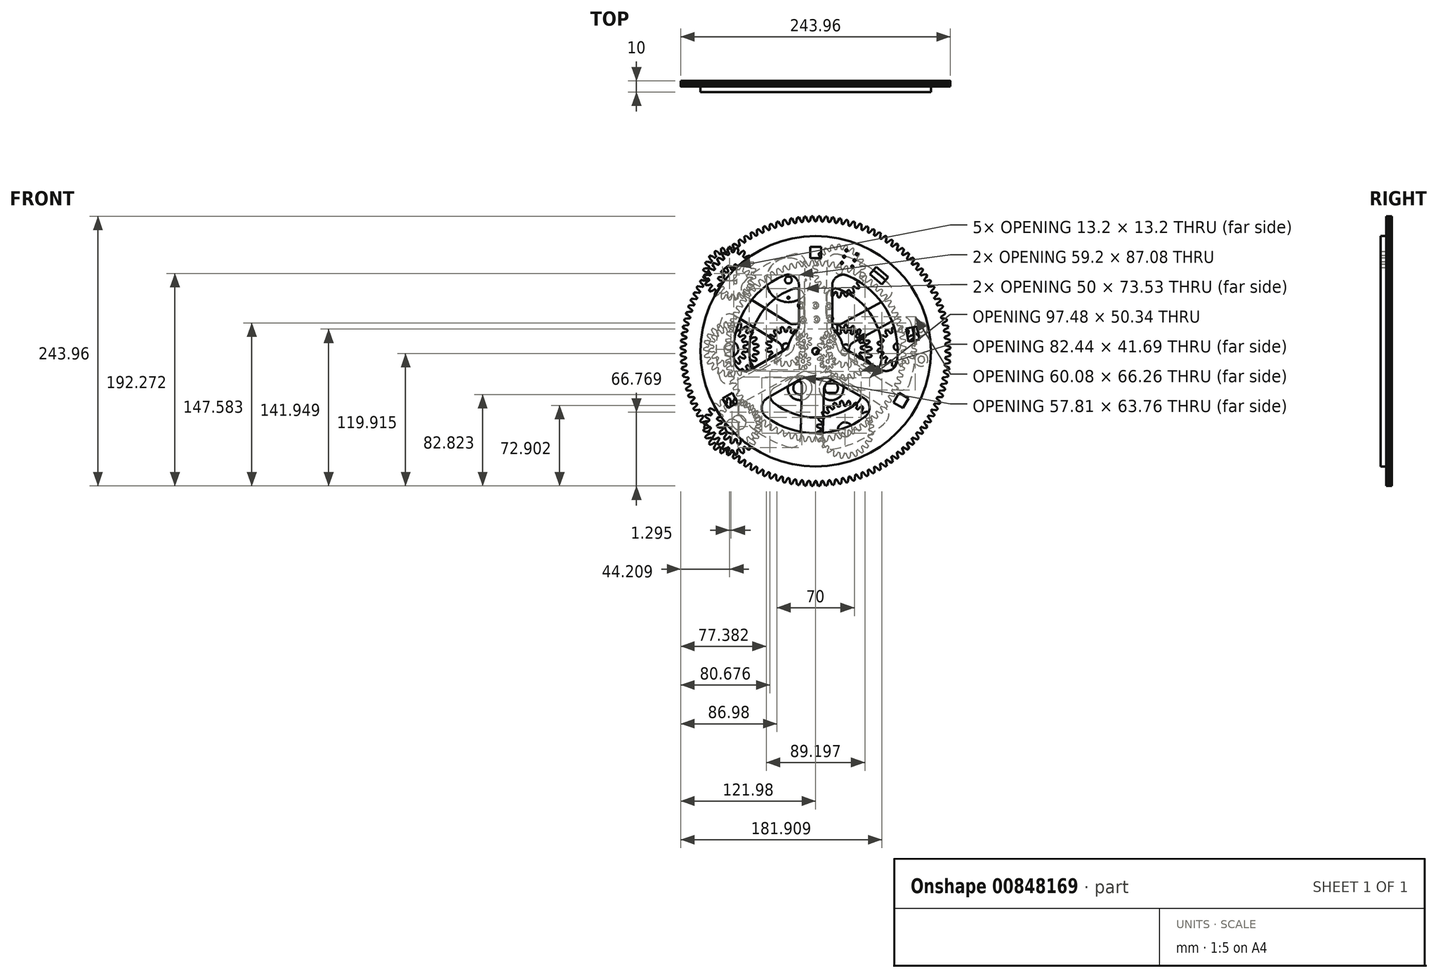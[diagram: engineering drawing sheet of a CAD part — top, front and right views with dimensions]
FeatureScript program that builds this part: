
annotation { "Feature Type Name" : "Feature", "Feature Type Description" : "" }
export const myFeature = defineFeature(function(context is Context, id is Id, definition is map)
    precondition{}
    {
        {
            var Q0;
            Q0=qCreatedBy(makeId("Front.planeOp"),FACE);
            var sketch = newSketch(context, id + "F0", { "sketchPlane" : qUnion([Q0])});
            skArc(sketch, "E0", {"start": v(10.6, 41.57) * mm, "mid": v(10.38, 40.77) * mm, "end": v(10.6, 39.97) * mm});
            skArc(sketch, "E1", {"start": v(13.36, 41.57) * mm, "mid": v(12.78, 42.16) * mm, "end": v(11.98, 42.37) * mm});
            skArc(sketch, "E2", {"start": v(13.2, 40.07) * mm, "mid": v(13.38, 40.77) * mm, "end": v(13.2, 41.47) * mm});
            skArc(sketch, "E3", {"start": v(10.77, 40.07) * mm, "mid": v(11.28, 39.56) * mm, "end": v(11.98, 39.37) * mm});
            skLineSegment(sketch, "E4", {"start": v(13.2, 41.47) * mm, "end": v(13.36, 41.57) * mm});
            skLineSegment(sketch, "E5", {"start": v(13.2, 40.07) * mm, "end": v(13.36, 39.97) * mm});
            skLineSegment(sketch, "E6", {"start": v(11.98, 39.37) * mm, "end": v(11.98, 39.17) * mm});
            skLineSegment(sketch, "E7", {"start": v(10.77, 40.07) * mm, "end": v(10.6, 39.97) * mm});
            skLineSegment(sketch, "E8", {"start": v(10.77, 41.47) * mm, "end": v(10.6, 41.57) * mm});
            skLineSegment(sketch, "E9", {"start": v(11.98, 42.17) * mm, "end": v(11.98, 42.37) * mm});
            skArc(sketch, "E10", {"start": v(11.98, 42.17) * mm, "mid": v(11.28, 41.98) * mm, "end": v(10.77, 41.47) * mm});
            skArc(sketch, "E11", {"start": v(11.98, 39.17) * mm, "mid": v(12.78, 39.38) * mm, "end": v(13.36, 39.97) * mm});
            skArc(sketch, "E12", {"start": v(-1.57, 42.17) * mm, "mid": v(-1.78, 41.37) * mm, "end": v(-1.57, 40.57) * mm});
            skArc(sketch, "E13", {"start": v(1.2, 42.17) * mm, "mid": v(0.62, 42.76) * mm, "end": v(-0.18, 42.97) * mm});
            skArc(sketch, "E14", {"start": v(1.03, 40.67) * mm, "mid": v(1.22, 41.37) * mm, "end": v(1.03, 42.07) * mm});
            skArc(sketch, "E15", {"start": v(-1.4, 40.67) * mm, "mid": v(-0.88, 40.16) * mm, "end": v(-0.18, 39.97) * mm});
            skLineSegment(sketch, "E16", {"start": v(1.03, 42.07) * mm, "end": v(1.2, 42.17) * mm});
            skLineSegment(sketch, "E17", {"start": v(1.03, 40.67) * mm, "end": v(1.2, 40.57) * mm});
            skLineSegment(sketch, "E18", {"start": v(-0.18, 39.97) * mm, "end": v(-0.18, 39.77) * mm});
            skLineSegment(sketch, "E19", {"start": v(-1.4, 40.67) * mm, "end": v(-1.57, 40.57) * mm});
            skLineSegment(sketch, "E20", {"start": v(-1.4, 42.07) * mm, "end": v(-1.57, 42.17) * mm});
            skLineSegment(sketch, "E21", {"start": v(-0.18, 42.77) * mm, "end": v(-0.18, 42.97) * mm});
            skArc(sketch, "E22", {"start": v(-0.18, 42.77) * mm, "mid": v(-0.88, 42.59) * mm, "end": v(-1.4, 42.07) * mm});
            skArc(sketch, "E23", {"start": v(-0.18, 39.77) * mm, "mid": v(0.62, 39.99) * mm, "end": v(1.2, 40.57) * mm});
            skCircle(sketch, "E24", {"center": v(-0.18, 41.37) * mm, "radius": 3 * mm});
            skArc(sketch, "E25", {"start": v(-14.37, 42.2) * mm, "mid": v(-14.59, 41.4) * mm, "end": v(-14.37, 40.6) * mm});
            skArc(sketch, "E26", {"start": v(-11.6, 42.2) * mm, "mid": v(-12.19, 42.79) * mm, "end": v(-12.99, 43) * mm});
            skArc(sketch, "E27", {"start": v(-11.77, 40.7) * mm, "mid": v(-11.59, 41.4) * mm, "end": v(-11.77, 42.1) * mm});
            skArc(sketch, "E28", {"start": v(-14.2, 40.7) * mm, "mid": v(-13.69, 40.19) * mm, "end": v(-12.99, 40) * mm});
            skLineSegment(sketch, "E29", {"start": v(-11.77, 42.1) * mm, "end": v(-11.6, 42.2) * mm});
            skLineSegment(sketch, "E30", {"start": v(-11.77, 40.7) * mm, "end": v(-11.6, 40.6) * mm});
            skLineSegment(sketch, "E31", {"start": v(-12.99, 40) * mm, "end": v(-12.99, 39.8) * mm});
            skLineSegment(sketch, "E32", {"start": v(-14.2, 40.7) * mm, "end": v(-14.37, 40.6) * mm});
            skLineSegment(sketch, "E33", {"start": v(-14.2, 42.1) * mm, "end": v(-14.37, 42.2) * mm});
            skLineSegment(sketch, "E34", {"start": v(-12.99, 42.8) * mm, "end": v(-12.99, 43) * mm});
            skArc(sketch, "E35", {"start": v(-12.99, 42.8) * mm, "mid": v(-13.69, 42.61) * mm, "end": v(-14.2, 42.1) * mm});
            skArc(sketch, "E36", {"start": v(-12.99, 39.8) * mm, "mid": v(-12.19, 40.02) * mm, "end": v(-11.6, 40.6) * mm});
            skArc(sketch, "E37", {"start": v(11.32, 30.3) * mm, "mid": v(11.1, 29.5) * mm, "end": v(11.32, 28.7) * mm});
            skArc(sketch, "E38", {"start": v(14.1, 30.3) * mm, "mid": v(13.5, 30.88) * mm, "end": v(12.7, 31.1) * mm});
            skArc(sketch, "E39", {"start": v(13.92, 28.8) * mm, "mid": v(14.1, 29.5) * mm, "end": v(13.92, 30.2) * mm});
            skArc(sketch, "E40", {"start": v(11.5, 28.8) * mm, "mid": v(12, 28.28) * mm, "end": v(12.7, 28.1) * mm});
            skLineSegment(sketch, "E41", {"start": v(13.92, 30.2) * mm, "end": v(14.1, 30.3) * mm});
            skLineSegment(sketch, "E42", {"start": v(13.92, 28.8) * mm, "end": v(14.1, 28.7) * mm});
            skLineSegment(sketch, "E43", {"start": v(12.7, 28.1) * mm, "end": v(12.7, 27.9) * mm});
            skLineSegment(sketch, "E44", {"start": v(11.5, 28.8) * mm, "end": v(11.32, 28.7) * mm});
            skLineSegment(sketch, "E45", {"start": v(11.5, 30.2) * mm, "end": v(11.32, 30.3) * mm});
            skLineSegment(sketch, "E46", {"start": v(12.7, 30.9) * mm, "end": v(12.7, 31.1) * mm});
            skArc(sketch, "E47", {"start": v(12.7, 30.9) * mm, "mid": v(12, 30.7) * mm, "end": v(11.5, 30.2) * mm});
            skArc(sketch, "E48", {"start": v(12.7, 27.9) * mm, "mid": v(13.5, 28.1) * mm, "end": v(14.1, 28.7) * mm});
            skCircle(sketch, "E49", {"center": v(12.7, 29.5) * mm, "radius": 3 * mm});
            skArc(sketch, "E50", {"start": v(-0.68, 29.53) * mm, "mid": v(-0.9, 28.73) * mm, "end": v(-0.68, 27.93) * mm});
            skArc(sketch, "E51", {"start": v(2.09, 29.53) * mm, "mid": v(1.5, 30.11) * mm, "end": v(0.7, 30.33) * mm});
            skArc(sketch, "E52", {"start": v(1.92, 28.03) * mm, "mid": v(2.1, 28.73) * mm, "end": v(1.92, 29.43) * mm});
            skArc(sketch, "E53", {"start": v(-0.5, 28.03) * mm, "mid": v(0, 27.51) * mm, "end": v(0.7, 27.33) * mm});
            skLineSegment(sketch, "E54", {"start": v(1.92, 29.43) * mm, "end": v(2.09, 29.53) * mm});
            skLineSegment(sketch, "E55", {"start": v(1.92, 28.03) * mm, "end": v(2.09, 27.93) * mm});
            skLineSegment(sketch, "E56", {"start": v(0.7, 27.33) * mm, "end": v(0.7, 27.13) * mm});
            skLineSegment(sketch, "E57", {"start": v(-0.5, 28.03) * mm, "end": v(-0.68, 27.93) * mm});
            skLineSegment(sketch, "E58", {"start": v(-0.5, 29.43) * mm, "end": v(-0.68, 29.53) * mm});
            skLineSegment(sketch, "E59", {"start": v(0.7, 30.13) * mm, "end": v(0.7, 30.33) * mm});
            skArc(sketch, "E60", {"start": v(0.7, 30.13) * mm, "mid": v(0, 29.94) * mm, "end": v(-0.5, 29.43) * mm});
            skArc(sketch, "E61", {"start": v(0.7, 27.13) * mm, "mid": v(1.5, 27.34) * mm, "end": v(2.09, 27.93) * mm});
            skArc(sketch, "E62", {"start": v(-12.86, 29.01) * mm, "mid": v(-13.07, 28.21) * mm, "end": v(-12.86, 27.41) * mm});
            skArc(sketch, "E63", {"start": v(-10.08, 29.01) * mm, "mid": v(-10.67, 29.6) * mm, "end": v(-11.47, 29.81) * mm});
            skArc(sketch, "E64", {"start": v(-10.26, 27.51) * mm, "mid": v(-10.07, 28.21) * mm, "end": v(-10.26, 28.91) * mm});
            skArc(sketch, "E65", {"start": v(-12.68, 27.51) * mm, "mid": v(-12.17, 27) * mm, "end": v(-11.47, 26.81) * mm});
            skLineSegment(sketch, "E66", {"start": v(-10.26, 28.91) * mm, "end": v(-10.08, 29.01) * mm});
            skLineSegment(sketch, "E67", {"start": v(-10.26, 27.51) * mm, "end": v(-10.08, 27.41) * mm});
            skLineSegment(sketch, "E68", {"start": v(-11.47, 26.81) * mm, "end": v(-11.47, 26.61) * mm});
            skLineSegment(sketch, "E69", {"start": v(-12.68, 27.51) * mm, "end": v(-12.86, 27.41) * mm});
            skLineSegment(sketch, "E70", {"start": v(-12.68, 28.91) * mm, "end": v(-12.86, 29.01) * mm});
            skLineSegment(sketch, "E71", {"start": v(-11.47, 29.61) * mm, "end": v(-11.47, 29.81) * mm});
            skArc(sketch, "E72", {"start": v(-11.47, 29.61) * mm, "mid": v(-12.17, 29.42) * mm, "end": v(-12.68, 28.91) * mm});
            skArc(sketch, "E73", {"start": v(-11.47, 26.61) * mm, "mid": v(-10.67, 26.83) * mm, "end": v(-10.08, 27.41) * mm});
            skArc(sketch, "E74", {"start": v(10.1, -29.05) * mm, "mid": v(8.23, -33.4) * mm, "end": v(10.1, -37.75) * mm});
            skLineSegment(sketch, "E75", {"start": v(18.36, -29.05) * mm, "end": v(10.1, -29.05) * mm});
            skLineSegment(sketch, "E76", {"start": v(18.36, -37.75) * mm, "end": v(10.1, -37.75) * mm});
            skCircle(sketch, "E77", {"center": v(14.23, -33.4) * mm, "radius": 11 * mm});
            skArc(sketch, "E78", {"start": v(18.36, -37.75) * mm, "mid": v(20.23, -33.4) * mm, "end": v(18.36, -29.05) * mm});
            skCircle(sketch, "E79", {"center": v(-14.23, -33.23) * mm, "radius": 6 * mm});
            skArc(sketch, "E80", {"start": v(9.57, -8.42) * mm, "mid": v(9.35, -9.22) * mm, "end": v(9.57, -10.02) * mm});
            skArc(sketch, "E81", {"start": v(12.34, -8.42) * mm, "mid": v(11.75, -7.84) * mm, "end": v(10.95, -7.62) * mm});
            skArc(sketch, "E82", {"start": v(12.17, -9.92) * mm, "mid": v(12.35, -9.22) * mm, "end": v(12.17, -8.52) * mm});
            skArc(sketch, "E83", {"start": v(9.74, -9.92) * mm, "mid": v(10.25, -10.43) * mm, "end": v(10.95, -10.62) * mm});
            skLineSegment(sketch, "E84", {"start": v(12.17, -8.52) * mm, "end": v(12.34, -8.42) * mm});
            skLineSegment(sketch, "E85", {"start": v(12.17, -9.92) * mm, "end": v(12.34, -10.02) * mm});
            skLineSegment(sketch, "E86", {"start": v(10.95, -10.62) * mm, "end": v(10.95, -10.82) * mm});
            skLineSegment(sketch, "E87", {"start": v(9.74, -9.92) * mm, "end": v(9.57, -10.02) * mm});
            skLineSegment(sketch, "E88", {"start": v(9.74, -8.52) * mm, "end": v(9.57, -8.42) * mm});
            skLineSegment(sketch, "E89", {"start": v(10.95, -7.82) * mm, "end": v(10.95, -7.62) * mm});
            skArc(sketch, "E90", {"start": v(10.95, -7.82) * mm, "mid": v(10.25, -8) * mm, "end": v(9.74, -8.52) * mm});
            skArc(sketch, "E91", {"start": v(10.95, -10.82) * mm, "mid": v(11.75, -10.6) * mm, "end": v(12.34, -10.02) * mm});
            skArc(sketch, "E92", {"start": v(-12.82, -8.3) * mm, "mid": v(-13.03, -9.1) * mm, "end": v(-12.82, -9.9) * mm});
            skArc(sketch, "E93", {"start": v(-10.05, -8.3) * mm, "mid": v(-10.63, -7.72) * mm, "end": v(-11.43, -7.5) * mm});
            skArc(sketch, "E94", {"start": v(-10.22, -9.8) * mm, "mid": v(-10.03, -9.1) * mm, "end": v(-10.22, -8.4) * mm});
            skArc(sketch, "E95", {"start": v(-12.65, -9.8) * mm, "mid": v(-12.13, -10.32) * mm, "end": v(-11.43, -10.5) * mm});
            skLineSegment(sketch, "E96", {"start": v(-10.22, -8.4) * mm, "end": v(-10.05, -8.3) * mm});
            skLineSegment(sketch, "E97", {"start": v(-10.22, -9.8) * mm, "end": v(-10.05, -9.9) * mm});
            skLineSegment(sketch, "E98", {"start": v(-11.43, -10.5) * mm, "end": v(-11.43, -10.7) * mm});
            skLineSegment(sketch, "E99", {"start": v(-12.65, -9.8) * mm, "end": v(-12.82, -9.9) * mm});
            skLineSegment(sketch, "E100", {"start": v(-12.65, -8.4) * mm, "end": v(-12.82, -8.3) * mm});
            skLineSegment(sketch, "E101", {"start": v(-11.43, -7.7) * mm, "end": v(-11.43, -7.5) * mm});
            skArc(sketch, "E102", {"start": v(-11.43, -7.7) * mm, "mid": v(-12.13, -7.9) * mm, "end": v(-12.65, -8.4) * mm});
            skArc(sketch, "E103", {"start": v(-11.43, -10.7) * mm, "mid": v(-10.63, -10.49) * mm, "end": v(-10.05, -9.9) * mm});
            skArc(sketch, "E104", {"start": v(12.53, -5) * mm, "mid": v(12.34, -4.94) * mm, "end": v(12.16, -4.89) * mm});
            skArc(sketch, "E105", {"start": v(12.53, -5) * mm, "mid": v(12.88, -5) * mm, "end": v(13.14, -4.76) * mm});
            skLineSegment(sketch, "E106", {"start": v(14.48, -3.36) * mm, "end": v(14.9, -3.2) * mm});
            skLineSegment(sketch, "E107", {"start": v(14.1, -3.55) * mm, "end": v(14.48, -3.36) * mm});
            skLineSegment(sketch, "E108", {"start": v(13.85, -3.73) * mm, "end": v(14.1, -3.55) * mm});
            skLineSegment(sketch, "E109", {"start": v(13.63, -3.92) * mm, "end": v(13.85, -3.73) * mm});
            skLineSegment(sketch, "E110", {"start": v(13.49, -4.09) * mm, "end": v(13.63, -3.92) * mm});
            skLineSegment(sketch, "E111", {"start": v(13.45, -4.14) * mm, "end": v(13.49, -4.09) * mm});
            skLineSegment(sketch, "E112", {"start": v(13.42, -4.2) * mm, "end": v(13.45, -4.14) * mm});
            skLineSegment(sketch, "E113", {"start": v(13.37, -4.3) * mm, "end": v(13.42, -4.2) * mm});
            skLineSegment(sketch, "E114", {"start": v(13.27, -4.5) * mm, "end": v(13.37, -4.3) * mm});
            skLineSegment(sketch, "E115", {"start": v(13.14, -4.76) * mm, "end": v(13.27, -4.5) * mm});
            skArc(sketch, "E116", {"start": v(15.47, -3.61) * mm, "mid": v(15.19, -3.4) * mm, "end": v(14.9, -3.2) * mm});
            skLineSegment(sketch, "E117", {"start": v(15.44, -4.06) * mm, "end": v(15.47, -3.61) * mm});
            skLineSegment(sketch, "E118", {"start": v(15.37, -4.47) * mm, "end": v(15.44, -4.06) * mm});
            skLineSegment(sketch, "E119", {"start": v(15.28, -4.78) * mm, "end": v(15.37, -4.47) * mm});
            skLineSegment(sketch, "E120", {"start": v(15.17, -5.03) * mm, "end": v(15.28, -4.78) * mm});
            skLineSegment(sketch, "E121", {"start": v(15.05, -5.23) * mm, "end": v(15.17, -5.03) * mm});
            skLineSegment(sketch, "E122", {"start": v(15.01, -5.28) * mm, "end": v(15.05, -5.23) * mm});
            skLineSegment(sketch, "E123", {"start": v(14.98, -5.32) * mm, "end": v(15.01, -5.28) * mm});
            skLineSegment(sketch, "E124", {"start": v(14.9, -5.4) * mm, "end": v(14.98, -5.32) * mm});
            skLineSegment(sketch, "E125", {"start": v(14.73, -5.56) * mm, "end": v(14.9, -5.4) * mm});
            skLineSegment(sketch, "E126", {"start": v(14.52, -5.76) * mm, "end": v(14.73, -5.56) * mm});
            skArc(sketch, "E127", {"start": v(14.52, -5.76) * mm, "mid": v(14.37, -6.08) * mm, "end": v(14.48, -6.42) * mm});
            skArc(sketch, "E128", {"start": v(14.7, -6.74) * mm, "mid": v(14.6, -6.58) * mm, "end": v(14.48, -6.42) * mm});
            skArc(sketch, "E129", {"start": v(14.7, -6.74) * mm, "mid": v(15, -6.94) * mm, "end": v(15.35, -6.9) * mm});
            skLineSegment(sketch, "E130", {"start": v(17.25, -6.55) * mm, "end": v(17.68, -6.66) * mm});
            skLineSegment(sketch, "E131", {"start": v(16.84, -6.5) * mm, "end": v(17.25, -6.55) * mm});
            skCircle(sketch, "E132", {"center": v(11.98, 40.77) * mm, "radius": 3 * mm});
            skLineSegment(sketch, "E133", {"start": v(16.52, -6.48) * mm, "end": v(16.84, -6.5) * mm});
            skLineSegment(sketch, "E134", {"start": v(16.24, -6.5) * mm, "end": v(16.52, -6.48) * mm});
            skLineSegment(sketch, "E135", {"start": v(16.02, -6.56) * mm, "end": v(16.24, -6.5) * mm});
            skLineSegment(sketch, "E136", {"start": v(15.96, -6.58) * mm, "end": v(16.02, -6.56) * mm});
            skLineSegment(sketch, "E137", {"start": v(15.9, -6.6) * mm, "end": v(15.96, -6.58) * mm});
            skLineSegment(sketch, "E138", {"start": v(15.8, -6.66) * mm, "end": v(15.9, -6.6) * mm});
            skLineSegment(sketch, "E139", {"start": v(15.6, -6.76) * mm, "end": v(15.8, -6.66) * mm});
            skLineSegment(sketch, "E140", {"start": v(15.35, -6.9) * mm, "end": v(15.6, -6.76) * mm});
            skArc(sketch, "E141", {"start": v(17.9, -7.33) * mm, "mid": v(17.8, -7) * mm, "end": v(17.68, -6.66) * mm});
            skLineSegment(sketch, "E142", {"start": v(17.62, -7.68) * mm, "end": v(17.9, -7.33) * mm});
            skLineSegment(sketch, "E143", {"start": v(17.32, -7.97) * mm, "end": v(17.62, -7.68) * mm});
            skLineSegment(sketch, "E144", {"start": v(17.07, -8.17) * mm, "end": v(17.32, -7.97) * mm});
            skLineSegment(sketch, "E145", {"start": v(16.83, -8.31) * mm, "end": v(17.07, -8.17) * mm});
            skLineSegment(sketch, "E146", {"start": v(16.62, -8.4) * mm, "end": v(16.83, -8.31) * mm});
            skLineSegment(sketch, "E147", {"start": v(16.55, -8.42) * mm, "end": v(16.62, -8.4) * mm});
            skLineSegment(sketch, "E148", {"start": v(16.5, -8.43) * mm, "end": v(16.55, -8.42) * mm});
            skLineSegment(sketch, "E149", {"start": v(16.38, -8.45) * mm, "end": v(16.5, -8.43) * mm});
            skLineSegment(sketch, "E150", {"start": v(16.16, -8.48) * mm, "end": v(16.38, -8.45) * mm});
            skLineSegment(sketch, "E151", {"start": v(15.87, -8.52) * mm, "end": v(16.16, -8.48) * mm});
            skArc(sketch, "E152", {"start": v(15.87, -8.52) * mm, "mid": v(15.56, -8.7) * mm, "end": v(15.45, -9.03) * mm});
            skArc(sketch, "E153", {"start": v(15.45, -9.41) * mm, "mid": v(15.45, -9.22) * mm, "end": v(15.45, -9.03) * mm});
            skArc(sketch, "E154", {"start": v(15.45, -9.41) * mm, "mid": v(15.56, -9.75) * mm, "end": v(15.87, -9.92) * mm});
            skLineSegment(sketch, "E155", {"start": v(17.62, -10.76) * mm, "end": v(17.9, -11.1) * mm});
            skLineSegment(sketch, "E156", {"start": v(17.32, -10.47) * mm, "end": v(17.62, -10.76) * mm});
            skLineSegment(sketch, "E157", {"start": v(17.07, -10.28) * mm, "end": v(17.32, -10.47) * mm});
            skLineSegment(sketch, "E158", {"start": v(16.83, -10.13) * mm, "end": v(17.07, -10.28) * mm});
            skLineSegment(sketch, "E159", {"start": v(16.62, -10.04) * mm, "end": v(16.83, -10.13) * mm});
            skLineSegment(sketch, "E160", {"start": v(16.55, -10.02) * mm, "end": v(16.62, -10.04) * mm});
            skLineSegment(sketch, "E161", {"start": v(16.5, -10.02) * mm, "end": v(16.55, -10.02) * mm});
            skLineSegment(sketch, "E162", {"start": v(16.38, -10) * mm, "end": v(16.5, -10.02) * mm});
            skLineSegment(sketch, "E163", {"start": v(16.16, -9.97) * mm, "end": v(16.38, -10) * mm});
            skLineSegment(sketch, "E164", {"start": v(15.87, -9.92) * mm, "end": v(16.16, -9.97) * mm});
            skArc(sketch, "E165", {"start": v(17.68, -11.78) * mm, "mid": v(17.8, -11.45) * mm, "end": v(17.9, -11.1) * mm});
            skLineSegment(sketch, "E166", {"start": v(17.25, -11.9) * mm, "end": v(17.68, -11.78) * mm});
            skLineSegment(sketch, "E167", {"start": v(16.84, -11.95) * mm, "end": v(17.25, -11.9) * mm});
            skLineSegment(sketch, "E168", {"start": v(16.52, -11.96) * mm, "end": v(16.84, -11.95) * mm});
            skLineSegment(sketch, "E169", {"start": v(16.24, -11.94) * mm, "end": v(16.52, -11.96) * mm});
            skLineSegment(sketch, "E170", {"start": v(16.02, -11.89) * mm, "end": v(16.24, -11.94) * mm});
            skLineSegment(sketch, "E171", {"start": v(15.96, -11.86) * mm, "end": v(16.02, -11.89) * mm});
            skLineSegment(sketch, "E172", {"start": v(15.9, -11.84) * mm, "end": v(15.96, -11.86) * mm});
            skLineSegment(sketch, "E173", {"start": v(15.8, -11.79) * mm, "end": v(15.9, -11.84) * mm});
            skLineSegment(sketch, "E174", {"start": v(15.6, -11.68) * mm, "end": v(15.8, -11.79) * mm});
            skLineSegment(sketch, "E175", {"start": v(15.35, -11.55) * mm, "end": v(15.6, -11.68) * mm});
            skArc(sketch, "E176", {"start": v(15.35, -11.55) * mm, "mid": v(15, -11.5) * mm, "end": v(14.7, -11.7) * mm});
            skArc(sketch, "E177", {"start": v(14.48, -12.02) * mm, "mid": v(14.6, -11.87) * mm, "end": v(14.7, -11.7) * mm});
            skArc(sketch, "E178", {"start": v(14.48, -12.02) * mm, "mid": v(14.37, -12.36) * mm, "end": v(14.52, -12.68) * mm});
            skLineSegment(sketch, "E179", {"start": v(15.44, -14.38) * mm, "end": v(15.47, -14.83) * mm});
            skLineSegment(sketch, "E180", {"start": v(15.37, -13.97) * mm, "end": v(15.44, -14.38) * mm});
            skLineSegment(sketch, "E181", {"start": v(15.28, -13.67) * mm, "end": v(15.37, -13.97) * mm});
            skLineSegment(sketch, "E182", {"start": v(15.17, -13.4) * mm, "end": v(15.28, -13.67) * mm});
            skLineSegment(sketch, "E183", {"start": v(15.05, -13.22) * mm, "end": v(15.17, -13.4) * mm});
            skLineSegment(sketch, "E184", {"start": v(15.01, -13.16) * mm, "end": v(15.05, -13.22) * mm});
            skLineSegment(sketch, "E185", {"start": v(14.98, -13.12) * mm, "end": v(15.01, -13.16) * mm});
            skLineSegment(sketch, "E186", {"start": v(14.9, -13.04) * mm, "end": v(14.98, -13.12) * mm});
            skLineSegment(sketch, "E187", {"start": v(14.73, -12.88) * mm, "end": v(14.9, -13.04) * mm});
            skLineSegment(sketch, "E188", {"start": v(14.52, -12.68) * mm, "end": v(14.73, -12.88) * mm});
            skArc(sketch, "E189", {"start": v(14.9, -15.25) * mm, "mid": v(15.19, -15.05) * mm, "end": v(15.47, -14.83) * mm});
            skLineSegment(sketch, "E190", {"start": v(14.48, -15.08) * mm, "end": v(14.9, -15.25) * mm});
            skLineSegment(sketch, "E191", {"start": v(14.1, -14.89) * mm, "end": v(14.48, -15.08) * mm});
            skLineSegment(sketch, "E192", {"start": v(13.85, -14.7) * mm, "end": v(14.1, -14.89) * mm});
            skLineSegment(sketch, "E193", {"start": v(13.63, -14.53) * mm, "end": v(13.85, -14.7) * mm});
            skLineSegment(sketch, "E194", {"start": v(13.49, -14.36) * mm, "end": v(13.63, -14.53) * mm});
            skLineSegment(sketch, "E195", {"start": v(13.45, -14.3) * mm, "end": v(13.49, -14.36) * mm});
            skLineSegment(sketch, "E196", {"start": v(13.42, -14.25) * mm, "end": v(13.45, -14.3) * mm});
            skLineSegment(sketch, "E197", {"start": v(13.37, -14.15) * mm, "end": v(13.42, -14.25) * mm});
            skLineSegment(sketch, "E198", {"start": v(13.27, -13.94) * mm, "end": v(13.37, -14.15) * mm});
            skLineSegment(sketch, "E199", {"start": v(13.14, -13.68) * mm, "end": v(13.27, -13.94) * mm});
            skArc(sketch, "E200", {"start": v(13.14, -13.68) * mm, "mid": v(12.88, -13.44) * mm, "end": v(12.53, -13.44) * mm});
            skArc(sketch, "E201", {"start": v(12.16, -13.56) * mm, "mid": v(12.34, -13.5) * mm, "end": v(12.53, -13.44) * mm});
            skArc(sketch, "E202", {"start": v(12.16, -13.56) * mm, "mid": v(11.87, -13.77) * mm, "end": v(11.8, -14.12) * mm});
            skLineSegment(sketch, "E203", {"start": v(-4.97, 7.85) * mm, "end": v(-4.7, 7.71) * mm});
            skLineSegment(sketch, "E204", {"start": v(-4.7, 7.71) * mm, "end": v(-4.4, 7.5) * mm});
            skLineSegment(sketch, "E205", {"start": v(-4.4, 7.5) * mm, "end": v(-4.1, 7.2) * mm});
            skLineSegment(sketch, "E206", {"start": v(-4.1, 7.2) * mm, "end": v(-3.82, 6.83) * mm});
            skLineSegment(sketch, "E207", {"start": v(-3.82, 6.83) * mm, "end": v(-3.55, 6.41) * mm});
            skArc(sketch, "E208", {"start": v(-6.5, 8.69) * mm, "mid": v(-6.38, 8.28) * mm, "end": v(-6, 8.06) * mm});
            skArc(sketch, "E209", {"start": v(-6.5, 8.69) * mm, "mid": v(-6.5, 8.9) * mm, "end": v(-6.5, 9.12) * mm});
            skArc(sketch, "E210", {"start": v(-6, 9.75) * mm, "mid": v(-6.38, 9.53) * mm, "end": v(-6.5, 9.12) * mm});
            skLineSegment(sketch, "E211", {"start": v(-6, 9.75) * mm, "end": v(-5.6, 9.83) * mm});
            skLineSegment(sketch, "E212", {"start": v(-5.6, 9.83) * mm, "end": v(-5.27, 9.89) * mm});
            skLineSegment(sketch, "E213", {"start": v(-5.27, 9.89) * mm, "end": v(-5.11, 9.92) * mm});
            skLineSegment(sketch, "E214", {"start": v(-5.11, 9.92) * mm, "end": v(-5.05, 9.93) * mm});
            skLineSegment(sketch, "E215", {"start": v(-5.05, 9.93) * mm, "end": v(-5.02, 9.94) * mm});
            skLineSegment(sketch, "E216", {"start": v(-5.02, 9.94) * mm, "end": v(-4.97, 9.96) * mm});
            skLineSegment(sketch, "E217", {"start": v(-4.97, 9.96) * mm, "end": v(-4.7, 10.1) * mm});
            skLineSegment(sketch, "E218", {"start": v(-4.7, 10.1) * mm, "end": v(-4.4, 10.32) * mm});
            skLineSegment(sketch, "E219", {"start": v(-4.4, 10.32) * mm, "end": v(-4.1, 10.61) * mm});
            skLineSegment(sketch, "E220", {"start": v(-4.1, 10.61) * mm, "end": v(-3.82, 10.97) * mm});
            skLineSegment(sketch, "E221", {"start": v(-3.82, 10.97) * mm, "end": v(-3.55, 11.4) * mm});
            skArc(sketch, "E222", {"start": v(-3.55, 11.4) * mm, "mid": v(-3.7, 11.77) * mm, "end": v(-3.86, 12.14) * mm});
            skLineSegment(sketch, "E223", {"start": v(-6.76, 11.57) * mm, "end": v(-6.41, 11.81) * mm});
            skLineSegment(sketch, "E224", {"start": v(-6.41, 11.81) * mm, "end": v(-6.14, 12) * mm});
            skLineSegment(sketch, "E225", {"start": v(-6.14, 12) * mm, "end": v(-6.01, 12.09) * mm});
            skLineSegment(sketch, "E226", {"start": v(-6.01, 12.09) * mm, "end": v(-5.96, 12.12) * mm});
            skLineSegment(sketch, "E227", {"start": v(-5.96, 12.12) * mm, "end": v(-5.93, 12.14) * mm});
            skLineSegment(sketch, "E228", {"start": v(-5.93, 12.14) * mm, "end": v(-5.88, 12.16) * mm});
            skLineSegment(sketch, "E229", {"start": v(-5.88, 12.16) * mm, "end": v(-5.6, 12.25) * mm});
            skLineSegment(sketch, "E230", {"start": v(-5.6, 12.25) * mm, "end": v(-5.23, 12.3) * mm});
            skLineSegment(sketch, "E231", {"start": v(-5.23, 12.3) * mm, "end": v(-4.8, 12.3) * mm});
            skLineSegment(sketch, "E232", {"start": v(-4.8, 12.3) * mm, "end": v(-4.35, 12.25) * mm});
            skLineSegment(sketch, "E233", {"start": v(-4.35, 12.25) * mm, "end": v(-3.86, 12.14) * mm});
            skArc(sketch, "E234", {"start": v(-7.56, 11.66) * mm, "mid": v(-7.18, 11.47) * mm, "end": v(-6.76, 11.57) * mm});
            skArc(sketch, "E235", {"start": v(-7.56, 11.66) * mm, "mid": v(-7.7, 11.82) * mm, "end": v(-7.87, 11.97) * mm});
            skArc(sketch, "E236", {"start": v(-7.96, 12.76) * mm, "mid": v(-8.06, 12.35) * mm, "end": v(-7.87, 11.97) * mm});
            skLineSegment(sketch, "E237", {"start": v(-7.96, 12.76) * mm, "end": v(-7.72, 13.12) * mm});
            skLineSegment(sketch, "E238", {"start": v(-7.72, 13.12) * mm, "end": v(-7.53, 13.39) * mm});
            skLineSegment(sketch, "E239", {"start": v(-7.53, 13.39) * mm, "end": v(-7.44, 13.52) * mm});
            skLineSegment(sketch, "E240", {"start": v(-7.44, 13.52) * mm, "end": v(-7.4, 13.57) * mm});
            skLineSegment(sketch, "E241", {"start": v(-7.4, 13.57) * mm, "end": v(-7.4, 13.6) * mm});
            skLineSegment(sketch, "E242", {"start": v(-7.4, 13.6) * mm, "end": v(-7.37, 13.65) * mm});
            skLineSegment(sketch, "E243", {"start": v(-7.37, 13.65) * mm, "end": v(-7.28, 13.93) * mm});
            skLineSegment(sketch, "E244", {"start": v(-7.28, 13.93) * mm, "end": v(-7.23, 14.3) * mm});
            skLineSegment(sketch, "E245", {"start": v(-7.23, 14.3) * mm, "end": v(-7.22, 14.72) * mm});
            skLineSegment(sketch, "E246", {"start": v(-7.22, 14.72) * mm, "end": v(-7.27, 15.18) * mm});
            skLineSegment(sketch, "E247", {"start": v(-7.27, 15.18) * mm, "end": v(-7.38, 15.67) * mm});
            skArc(sketch, "E248", {"start": v(-7.38, 15.67) * mm, "mid": v(-7.75, 15.83) * mm, "end": v(-8.13, 15.98) * mm});
            skLineSegment(sketch, "E249", {"start": v(-9.78, 13.52) * mm, "end": v(-9.7, 13.94) * mm});
            skLineSegment(sketch, "E250", {"start": v(-9.7, 13.94) * mm, "end": v(-9.64, 14.26) * mm});
            skLineSegment(sketch, "E251", {"start": v(-9.64, 14.26) * mm, "end": v(-9.61, 14.42) * mm});
            skLineSegment(sketch, "E252", {"start": v(-9.61, 14.42) * mm, "end": v(-9.6, 14.47) * mm});
            skLineSegment(sketch, "E253", {"start": v(-9.6, 14.47) * mm, "end": v(-9.59, 14.51) * mm});
            skLineSegment(sketch, "E254", {"start": v(-9.59, 14.51) * mm, "end": v(-9.57, 14.56) * mm});
            skLineSegment(sketch, "E255", {"start": v(-9.57, 14.56) * mm, "end": v(-9.43, 14.82) * mm});
            skLineSegment(sketch, "E256", {"start": v(-9.43, 14.82) * mm, "end": v(-9.21, 15.12) * mm});
            skLineSegment(sketch, "E257", {"start": v(-9.21, 15.12) * mm, "end": v(-8.92, 15.42) * mm});
            skLineSegment(sketch, "E258", {"start": v(-8.92, 15.42) * mm, "end": v(-8.55, 15.71) * mm});
            skLineSegment(sketch, "E259", {"start": v(-8.55, 15.71) * mm, "end": v(-8.13, 15.98) * mm});
            skArc(sketch, "E260", {"start": v(-10.4, 13.02) * mm, "mid": v(-10, 13.15) * mm, "end": v(-9.78, 13.52) * mm});
            skArc(sketch, "E261", {"start": v(-10.4, 13.02) * mm, "mid": v(-10.62, 13.03) * mm, "end": v(-10.84, 13.02) * mm});
            skArc(sketch, "E262", {"start": v(-11.47, 13.52) * mm, "mid": v(-11.25, 13.15) * mm, "end": v(-10.84, 13.02) * mm});
            skLineSegment(sketch, "E263", {"start": v(-11.47, 13.52) * mm, "end": v(-11.55, 13.94) * mm});
            skLineSegment(sketch, "E264", {"start": v(-11.55, 13.94) * mm, "end": v(-11.6, 14.26) * mm});
            skLineSegment(sketch, "E265", {"start": v(-11.6, 14.26) * mm, "end": v(-11.64, 14.42) * mm});
            skLineSegment(sketch, "E266", {"start": v(-11.64, 14.42) * mm, "end": v(-11.65, 14.47) * mm});
            skLineSegment(sketch, "E267", {"start": v(-11.65, 14.47) * mm, "end": v(-11.66, 14.51) * mm});
            skLineSegment(sketch, "E268", {"start": v(-11.66, 14.51) * mm, "end": v(-11.68, 14.56) * mm});
            skCircle(sketch, "E269", {"center": v(0.7, 28.73) * mm, "radius": 3 * mm});
            skLineSegment(sketch, "E270", {"start": v(-11.68, 14.56) * mm, "end": v(-11.82, 14.82) * mm});
            skLineSegment(sketch, "E271", {"start": v(-11.82, 14.82) * mm, "end": v(-12.04, 15.12) * mm});
            skLineSegment(sketch, "E272", {"start": v(-12.04, 15.12) * mm, "end": v(-12.33, 15.42) * mm});
            skLineSegment(sketch, "E273", {"start": v(-12.33, 15.42) * mm, "end": v(-12.7, 15.71) * mm});
            skLineSegment(sketch, "E274", {"start": v(-12.7, 15.71) * mm, "end": v(-13.12, 15.98) * mm});
            skArc(sketch, "E275", {"start": v(-13.12, 15.98) * mm, "mid": v(-13.5, 15.83) * mm, "end": v(-13.86, 15.67) * mm});
            skLineSegment(sketch, "E276", {"start": v(-13.29, 12.76) * mm, "end": v(-13.53, 13.12) * mm});
            skLineSegment(sketch, "E277", {"start": v(-13.53, 13.12) * mm, "end": v(-13.72, 13.39) * mm});
            skLineSegment(sketch, "E278", {"start": v(-13.72, 13.39) * mm, "end": v(-13.8, 13.52) * mm});
            skLineSegment(sketch, "E279", {"start": v(-13.8, 13.52) * mm, "end": v(-13.84, 13.57) * mm});
            skLineSegment(sketch, "E280", {"start": v(-13.84, 13.57) * mm, "end": v(-13.86, 13.6) * mm});
            skLineSegment(sketch, "E281", {"start": v(-13.86, 13.6) * mm, "end": v(-13.88, 13.65) * mm});
            skLineSegment(sketch, "E282", {"start": v(-13.88, 13.65) * mm, "end": v(-13.97, 13.93) * mm});
            skLineSegment(sketch, "E283", {"start": v(-13.97, 13.93) * mm, "end": v(-14.02, 14.3) * mm});
            skLineSegment(sketch, "E284", {"start": v(-14.02, 14.3) * mm, "end": v(-14.03, 14.72) * mm});
            skLineSegment(sketch, "E285", {"start": v(-14.03, 14.72) * mm, "end": v(-13.97, 15.18) * mm});
            skLineSegment(sketch, "E286", {"start": v(-13.97, 15.18) * mm, "end": v(-13.86, 15.67) * mm});
            skArc(sketch, "E287", {"start": v(-13.38, 11.97) * mm, "mid": v(-13.19, 12.35) * mm, "end": v(-13.29, 12.76) * mm});
            skArc(sketch, "E288", {"start": v(-13.38, 11.97) * mm, "mid": v(-13.54, 11.82) * mm, "end": v(-13.7, 11.66) * mm});
            skArc(sketch, "E289", {"start": v(-14.49, 11.57) * mm, "mid": v(-14.07, 11.47) * mm, "end": v(-13.7, 11.66) * mm});
            skLineSegment(sketch, "E290", {"start": v(-14.49, 11.57) * mm, "end": v(-14.84, 11.81) * mm});
            skLineSegment(sketch, "E291", {"start": v(-14.84, 11.81) * mm, "end": v(-15.1, 12) * mm});
            skLineSegment(sketch, "E292", {"start": v(-15.1, 12) * mm, "end": v(-15.24, 12.09) * mm});
            skLineSegment(sketch, "E293", {"start": v(-15.24, 12.09) * mm, "end": v(-15.29, 12.12) * mm});
            skLineSegment(sketch, "E294", {"start": v(-15.29, 12.12) * mm, "end": v(-15.32, 12.14) * mm});
            skLineSegment(sketch, "E295", {"start": v(-15.32, 12.14) * mm, "end": v(-15.37, 12.16) * mm});
            skLineSegment(sketch, "E296", {"start": v(-15.37, 12.16) * mm, "end": v(-15.65, 12.25) * mm});
            skLineSegment(sketch, "E297", {"start": v(-15.65, 12.25) * mm, "end": v(-16.02, 12.3) * mm});
            skLineSegment(sketch, "E298", {"start": v(-16.02, 12.3) * mm, "end": v(-16.44, 12.3) * mm});
            skLineSegment(sketch, "E299", {"start": v(-16.44, 12.3) * mm, "end": v(-16.9, 12.25) * mm});
            skLineSegment(sketch, "E300", {"start": v(-16.9, 12.25) * mm, "end": v(-17.39, 12.14) * mm});
            skArc(sketch, "E301", {"start": v(-17.39, 12.14) * mm, "mid": v(-17.55, 11.77) * mm, "end": v(-17.7, 11.4) * mm});
            skLineSegment(sketch, "E302", {"start": v(-15.24, 9.75) * mm, "end": v(-15.66, 9.83) * mm});
            skLineSegment(sketch, "E303", {"start": v(-15.66, 9.83) * mm, "end": v(-15.98, 9.89) * mm});
            skLineSegment(sketch, "E304", {"start": v(-15.98, 9.89) * mm, "end": v(-16.14, 9.92) * mm});
            skLineSegment(sketch, "E305", {"start": v(-16.14, 9.92) * mm, "end": v(-16.2, 9.93) * mm});
            skLineSegment(sketch, "E306", {"start": v(-16.2, 9.93) * mm, "end": v(-16.23, 9.94) * mm});
            skLineSegment(sketch, "E307", {"start": v(-16.23, 9.94) * mm, "end": v(-16.28, 9.96) * mm});
            skLineSegment(sketch, "E308", {"start": v(-16.28, 9.96) * mm, "end": v(-16.54, 10.1) * mm});
            skLineSegment(sketch, "E309", {"start": v(-16.54, 10.1) * mm, "end": v(-16.84, 10.32) * mm});
            skLineSegment(sketch, "E310", {"start": v(-16.84, 10.32) * mm, "end": v(-17.14, 10.61) * mm});
            skLineSegment(sketch, "E311", {"start": v(-17.14, 10.61) * mm, "end": v(-17.43, 10.97) * mm});
            skLineSegment(sketch, "E312", {"start": v(-17.43, 10.97) * mm, "end": v(-17.7, 11.4) * mm});
            skArc(sketch, "E313", {"start": v(-14.74, 9.12) * mm, "mid": v(-14.87, 9.53) * mm, "end": v(-15.24, 9.75) * mm});
            skArc(sketch, "E314", {"start": v(-14.74, 9.12) * mm, "mid": v(-14.75, 8.9) * mm, "end": v(-14.74, 8.69) * mm});
            skArc(sketch, "E315", {"start": v(-15.24, 8.06) * mm, "mid": v(-14.87, 8.28) * mm, "end": v(-14.74, 8.69) * mm});
            skLineSegment(sketch, "E316", {"start": v(-15.24, 8.06) * mm, "end": v(-15.66, 7.98) * mm});
            skLineSegment(sketch, "E317", {"start": v(-15.66, 7.98) * mm, "end": v(-15.98, 7.92) * mm});
            skLineSegment(sketch, "E318", {"start": v(-15.98, 7.92) * mm, "end": v(-16.14, 7.9) * mm});
            skLineSegment(sketch, "E319", {"start": v(-16.14, 7.9) * mm, "end": v(-16.2, 7.88) * mm});
            skLineSegment(sketch, "E320", {"start": v(-16.2, 7.88) * mm, "end": v(-16.23, 7.87) * mm});
            skLineSegment(sketch, "E321", {"start": v(-16.23, 7.87) * mm, "end": v(-16.28, 7.85) * mm});
            skLineSegment(sketch, "E322", {"start": v(-16.28, 7.85) * mm, "end": v(-16.54, 7.71) * mm});
            skLineSegment(sketch, "E323", {"start": v(-16.54, 7.71) * mm, "end": v(-16.84, 7.5) * mm});
            skLineSegment(sketch, "E324", {"start": v(-16.84, 7.5) * mm, "end": v(-17.14, 7.2) * mm});
            skLineSegment(sketch, "E325", {"start": v(-17.14, 7.2) * mm, "end": v(-17.43, 6.83) * mm});
            skLineSegment(sketch, "E326", {"start": v(-17.43, 6.83) * mm, "end": v(-17.7, 6.41) * mm});
            skArc(sketch, "E327", {"start": v(-17.7, 6.41) * mm, "mid": v(-17.55, 6.03) * mm, "end": v(-17.39, 5.66) * mm});
            skLineSegment(sketch, "E328", {"start": v(-14.49, 6.24) * mm, "end": v(-14.84, 6) * mm});
            skLineSegment(sketch, "E329", {"start": v(-14.84, 6) * mm, "end": v(-15.1, 5.8) * mm});
            skLineSegment(sketch, "E330", {"start": v(-15.1, 5.8) * mm, "end": v(-15.24, 5.72) * mm});
            skLineSegment(sketch, "E331", {"start": v(-15.24, 5.72) * mm, "end": v(-15.29, 5.69) * mm});
            skLineSegment(sketch, "E332", {"start": v(-15.29, 5.69) * mm, "end": v(-15.32, 5.67) * mm});
            skLineSegment(sketch, "E333", {"start": v(-15.32, 5.67) * mm, "end": v(-15.37, 5.65) * mm});
            skLineSegment(sketch, "E334", {"start": v(-15.37, 5.65) * mm, "end": v(-15.65, 5.56) * mm});
            skLineSegment(sketch, "E335", {"start": v(-15.65, 5.56) * mm, "end": v(-16.02, 5.5) * mm});
            skLineSegment(sketch, "E336", {"start": v(-16.02, 5.5) * mm, "end": v(-16.44, 5.5) * mm});
            skLineSegment(sketch, "E337", {"start": v(-16.44, 5.5) * mm, "end": v(-16.9, 5.55) * mm});
            skLineSegment(sketch, "E338", {"start": v(-16.9, 5.55) * mm, "end": v(-17.39, 5.66) * mm});
            skArc(sketch, "E339", {"start": v(-13.7, 6.15) * mm, "mid": v(-14.07, 6.34) * mm, "end": v(-14.49, 6.24) * mm});
            skArc(sketch, "E340", {"start": v(-13.7, 6.15) * mm, "mid": v(-13.54, 5.99) * mm, "end": v(-13.38, 5.84) * mm});
            skArc(sketch, "E341", {"start": v(-13.29, 5.04) * mm, "mid": v(-13.19, 5.46) * mm, "end": v(-13.38, 5.84) * mm});
            skLineSegment(sketch, "E342", {"start": v(-13.29, 5.04) * mm, "end": v(-13.53, 4.7) * mm});
            skLineSegment(sketch, "E343", {"start": v(-13.53, 4.7) * mm, "end": v(-13.72, 4.42) * mm});
            skLineSegment(sketch, "E344", {"start": v(-13.72, 4.42) * mm, "end": v(-13.8, 4.29) * mm});
            skLineSegment(sketch, "E345", {"start": v(-13.8, 4.29) * mm, "end": v(-13.84, 4.24) * mm});
            skLineSegment(sketch, "E346", {"start": v(-13.84, 4.24) * mm, "end": v(-13.86, 4.2) * mm});
            skLineSegment(sketch, "E347", {"start": v(-13.86, 4.2) * mm, "end": v(-13.88, 4.16) * mm});
            skLineSegment(sketch, "E348", {"start": v(-13.88, 4.16) * mm, "end": v(-13.97, 3.88) * mm});
            skLineSegment(sketch, "E349", {"start": v(-13.97, 3.88) * mm, "end": v(-14.02, 3.5) * mm});
            skLineSegment(sketch, "E350", {"start": v(-14.02, 3.5) * mm, "end": v(-14.03, 3.09) * mm});
            skLineSegment(sketch, "E351", {"start": v(-14.03, 3.09) * mm, "end": v(-13.97, 2.63) * mm});
            skLineSegment(sketch, "E352", {"start": v(-13.97, 2.63) * mm, "end": v(-13.86, 2.14) * mm});
            skArc(sketch, "E353", {"start": v(-13.86, 2.14) * mm, "mid": v(-13.5, 1.97) * mm, "end": v(-13.12, 1.83) * mm});
            skLineSegment(sketch, "E354", {"start": v(-11.47, 4.29) * mm, "end": v(-11.55, 3.87) * mm});
            skLineSegment(sketch, "E355", {"start": v(-11.55, 3.87) * mm, "end": v(-11.6, 3.55) * mm});
            skLineSegment(sketch, "E356", {"start": v(-11.6, 3.55) * mm, "end": v(-11.64, 3.39) * mm});
            skLineSegment(sketch, "E357", {"start": v(-11.64, 3.39) * mm, "end": v(-11.65, 3.33) * mm});
            skLineSegment(sketch, "E358", {"start": v(-11.65, 3.33) * mm, "end": v(-11.66, 3.3) * mm});
            skLineSegment(sketch, "E359", {"start": v(-11.66, 3.3) * mm, "end": v(-11.68, 3.25) * mm});
            skLineSegment(sketch, "E360", {"start": v(-11.68, 3.25) * mm, "end": v(-11.82, 2.98) * mm});
            skLineSegment(sketch, "E361", {"start": v(-11.82, 2.98) * mm, "end": v(-12.04, 2.69) * mm});
            skLineSegment(sketch, "E362", {"start": v(-12.04, 2.69) * mm, "end": v(-12.33, 2.39) * mm});
            skLineSegment(sketch, "E363", {"start": v(-12.33, 2.39) * mm, "end": v(-12.7, 2.1) * mm});
            skLineSegment(sketch, "E364", {"start": v(-12.7, 2.1) * mm, "end": v(-13.12, 1.83) * mm});
            skArc(sketch, "E365", {"start": v(-10.84, 4.78) * mm, "mid": v(-11.25, 4.66) * mm, "end": v(-11.47, 4.29) * mm});
            skArc(sketch, "E366", {"start": v(-10.84, 4.78) * mm, "mid": v(-10.62, 4.78) * mm, "end": v(-10.4, 4.78) * mm});
            skArc(sketch, "E367", {"start": v(-9.78, 4.29) * mm, "mid": v(-10, 4.66) * mm, "end": v(-10.4, 4.78) * mm});
            skLineSegment(sketch, "E368", {"start": v(-9.78, 4.29) * mm, "end": v(-9.7, 3.87) * mm});
            skLineSegment(sketch, "E369", {"start": v(-9.7, 3.87) * mm, "end": v(-9.64, 3.55) * mm});
            skLineSegment(sketch, "E370", {"start": v(-9.64, 3.55) * mm, "end": v(-9.61, 3.39) * mm});
            skLineSegment(sketch, "E371", {"start": v(-9.61, 3.39) * mm, "end": v(-9.6, 3.33) * mm});
            skLineSegment(sketch, "E372", {"start": v(-9.6, 3.33) * mm, "end": v(-9.59, 3.3) * mm});
            skLineSegment(sketch, "E373", {"start": v(-9.59, 3.3) * mm, "end": v(-9.57, 3.25) * mm});
            skLineSegment(sketch, "E374", {"start": v(-9.57, 3.25) * mm, "end": v(-9.43, 2.98) * mm});
            skLineSegment(sketch, "E375", {"start": v(-9.43, 2.98) * mm, "end": v(-9.21, 2.69) * mm});
            skLineSegment(sketch, "E376", {"start": v(-9.21, 2.69) * mm, "end": v(-8.92, 2.39) * mm});
            skLineSegment(sketch, "E377", {"start": v(-8.92, 2.39) * mm, "end": v(-8.55, 2.1) * mm});
            skLineSegment(sketch, "E378", {"start": v(-8.55, 2.1) * mm, "end": v(-8.13, 1.83) * mm});
            skArc(sketch, "E379", {"start": v(-8.13, 1.83) * mm, "mid": v(-7.75, 1.97) * mm, "end": v(-7.38, 2.14) * mm});
            skLineSegment(sketch, "E380", {"start": v(-7.96, 5.04) * mm, "end": v(-7.72, 4.7) * mm});
            skLineSegment(sketch, "E381", {"start": v(-7.72, 4.7) * mm, "end": v(-7.53, 4.42) * mm});
            skLineSegment(sketch, "E382", {"start": v(-7.53, 4.42) * mm, "end": v(-7.44, 4.29) * mm});
            skLineSegment(sketch, "E383", {"start": v(-7.44, 4.29) * mm, "end": v(-7.4, 4.24) * mm});
            skLineSegment(sketch, "E384", {"start": v(-7.4, 4.24) * mm, "end": v(-7.4, 4.2) * mm});
            skLineSegment(sketch, "E385", {"start": v(-7.4, 4.2) * mm, "end": v(-7.37, 4.16) * mm});
            skLineSegment(sketch, "E386", {"start": v(-7.37, 4.16) * mm, "end": v(-7.28, 3.88) * mm});
            skLineSegment(sketch, "E387", {"start": v(-7.28, 3.88) * mm, "end": v(-7.23, 3.5) * mm});
            skLineSegment(sketch, "E388", {"start": v(-7.23, 3.5) * mm, "end": v(-7.22, 3.09) * mm});
            skLineSegment(sketch, "E389", {"start": v(-7.22, 3.09) * mm, "end": v(-7.27, 2.63) * mm});
            skLineSegment(sketch, "E390", {"start": v(-7.27, 2.63) * mm, "end": v(-7.38, 2.14) * mm});
            skArc(sketch, "E391", {"start": v(-7.87, 5.84) * mm, "mid": v(-8.06, 5.46) * mm, "end": v(-7.96, 5.04) * mm});
            skArc(sketch, "E392", {"start": v(-7.87, 5.84) * mm, "mid": v(-7.7, 5.99) * mm, "end": v(-7.56, 6.15) * mm});
            skArc(sketch, "E393", {"start": v(12.61, 13.68) * mm, "mid": v(12.68, 13.33) * mm, "end": v(12.97, 13.12) * mm});
            skLineSegment(sketch, "E394", {"start": v(12.61, 13.68) * mm, "end": v(12.66, 13.97) * mm});
            skLineSegment(sketch, "E395", {"start": v(12.66, 13.97) * mm, "end": v(12.7, 14.2) * mm});
            skLineSegment(sketch, "E396", {"start": v(12.7, 14.2) * mm, "end": v(12.72, 14.3) * mm});
            skLineSegment(sketch, "E397", {"start": v(12.72, 14.3) * mm, "end": v(12.73, 14.36) * mm});
            skLineSegment(sketch, "E398", {"start": v(12.73, 14.36) * mm, "end": v(12.73, 14.43) * mm});
            skLineSegment(sketch, "E399", {"start": v(12.73, 14.43) * mm, "end": v(12.71, 14.65) * mm});
            skLineSegment(sketch, "E400", {"start": v(12.71, 14.65) * mm, "end": v(12.65, 14.93) * mm});
            skLineSegment(sketch, "E401", {"start": v(12.65, 14.93) * mm, "end": v(12.54, 15.23) * mm});
            skLineSegment(sketch, "E402", {"start": v(12.54, 15.23) * mm, "end": v(12.36, 15.6) * mm});
            skLineSegment(sketch, "E403", {"start": v(12.36, 15.6) * mm, "end": v(12.11, 15.98) * mm});
            skArc(sketch, "E404", {"start": v(12.11, 15.98) * mm, "mid": v(11.76, 15.99) * mm, "end": v(11.4, 15.98) * mm});
            skLineSegment(sketch, "E405", {"start": v(10.91, 13.68) * mm, "end": v(10.86, 13.97) * mm});
            skLineSegment(sketch, "E406", {"start": v(10.86, 13.97) * mm, "end": v(10.82, 14.2) * mm});
            skLineSegment(sketch, "E407", {"start": v(10.82, 14.2) * mm, "end": v(10.8, 14.3) * mm});
            skLineSegment(sketch, "E408", {"start": v(10.8, 14.3) * mm, "end": v(10.8, 14.36) * mm});
            skLineSegment(sketch, "E409", {"start": v(10.8, 14.36) * mm, "end": v(10.8, 14.43) * mm});
            skLineSegment(sketch, "E410", {"start": v(10.8, 14.43) * mm, "end": v(10.81, 14.65) * mm});
            skLineSegment(sketch, "E411", {"start": v(10.81, 14.65) * mm, "end": v(10.88, 14.93) * mm});
            skLineSegment(sketch, "E412", {"start": v(10.88, 14.93) * mm, "end": v(10.98, 15.23) * mm});
            skLineSegment(sketch, "E413", {"start": v(10.98, 15.23) * mm, "end": v(11.17, 15.6) * mm});
            skLineSegment(sketch, "E414", {"start": v(10.82, 3.38) * mm, "end": v(10.8, 3.27) * mm});
            skLineSegment(sketch, "E415", {"start": v(10.8, 3.27) * mm, "end": v(10.8, 3.21) * mm});
            skLineSegment(sketch, "E416", {"start": v(10.8, 3.21) * mm, "end": v(10.8, 3.14) * mm});
            skLineSegment(sketch, "E417", {"start": v(10.8, 3.14) * mm, "end": v(10.81, 2.92) * mm});
            skLineSegment(sketch, "E418", {"start": v(10.81, 2.92) * mm, "end": v(10.88, 2.65) * mm});
            skLineSegment(sketch, "E419", {"start": v(10.88, 2.65) * mm, "end": v(10.98, 2.35) * mm});
            skLineSegment(sketch, "E420", {"start": v(10.98, 2.35) * mm, "end": v(11.17, 1.97) * mm});
            skLineSegment(sketch, "E421", {"start": v(11.17, 1.97) * mm, "end": v(11.4, 1.6) * mm});
            skArc(sketch, "E422", {"start": v(11.4, 1.6) * mm, "mid": v(11.76, 1.59) * mm, "end": v(12.11, 1.6) * mm});
            skLineSegment(sketch, "E423", {"start": v(12.61, 3.89) * mm, "end": v(12.66, 3.6) * mm});
            skLineSegment(sketch, "E424", {"start": v(12.66, 3.6) * mm, "end": v(12.7, 3.38) * mm});
            skLineSegment(sketch, "E425", {"start": v(12.7, 3.38) * mm, "end": v(12.72, 3.27) * mm});
            skLineSegment(sketch, "E426", {"start": v(12.72, 3.27) * mm, "end": v(12.73, 3.21) * mm});
            skLineSegment(sketch, "E427", {"start": v(12.73, 3.21) * mm, "end": v(12.73, 3.14) * mm});
            skLineSegment(sketch, "E428", {"start": v(12.73, 3.14) * mm, "end": v(12.71, 2.92) * mm});
            skLineSegment(sketch, "E429", {"start": v(12.71, 2.92) * mm, "end": v(12.65, 2.65) * mm});
            skLineSegment(sketch, "E430", {"start": v(12.65, 2.65) * mm, "end": v(12.54, 2.35) * mm});
            skLineSegment(sketch, "E431", {"start": v(12.54, 2.35) * mm, "end": v(12.36, 1.97) * mm});
            skLineSegment(sketch, "E432", {"start": v(12.36, 1.97) * mm, "end": v(12.11, 1.6) * mm});
            skArc(sketch, "E433", {"start": v(12.97, 4.45) * mm, "mid": v(12.68, 4.24) * mm, "end": v(12.61, 3.89) * mm});
            skCircle(sketch, "E434", {"center": v(-14.23, -33.23) * mm, "radius": 11 * mm});
            skArc(sketch, "E435", {"start": v(12.97, 4.45) * mm, "mid": v(13.15, 4.5) * mm, "end": v(13.33, 4.57) * mm});
            skArc(sketch, "E436", {"start": v(13.95, 4.32) * mm, "mid": v(13.7, 4.57) * mm, "end": v(13.33, 4.57) * mm});
            skLineSegment(sketch, "E437", {"start": v(13.95, 4.32) * mm, "end": v(14.08, 4.06) * mm});
            skLineSegment(sketch, "E438", {"start": v(14.08, 4.06) * mm, "end": v(14.18, 3.86) * mm});
            skLineSegment(sketch, "E439", {"start": v(14.18, 3.86) * mm, "end": v(14.23, 3.76) * mm});
            skLineSegment(sketch, "E440", {"start": v(14.23, 3.76) * mm, "end": v(14.26, 3.7) * mm});
            skLineSegment(sketch, "E441", {"start": v(14.26, 3.7) * mm, "end": v(14.3, 3.65) * mm});
            skLineSegment(sketch, "E442", {"start": v(14.3, 3.65) * mm, "end": v(14.44, 3.48) * mm});
            skLineSegment(sketch, "E443", {"start": v(14.44, 3.48) * mm, "end": v(14.65, 3.3) * mm});
            skLineSegment(sketch, "E444", {"start": v(14.65, 3.3) * mm, "end": v(14.92, 3.12) * mm});
            skLineSegment(sketch, "E445", {"start": v(14.92, 3.12) * mm, "end": v(15.28, 2.93) * mm});
            skLineSegment(sketch, "E446", {"start": v(15.28, 2.93) * mm, "end": v(15.7, 2.76) * mm});
            skArc(sketch, "E447", {"start": v(15.7, 2.76) * mm, "mid": v(16, 2.96) * mm, "end": v(16.27, 3.18) * mm});
            skLineSegment(sketch, "E448", {"start": v(15.33, 5.33) * mm, "end": v(15.54, 5.12) * mm});
            skLineSegment(sketch, "E449", {"start": v(15.54, 5.12) * mm, "end": v(15.7, 4.97) * mm});
            skLineSegment(sketch, "E450", {"start": v(15.7, 4.97) * mm, "end": v(15.78, 4.88) * mm});
            skLineSegment(sketch, "E451", {"start": v(15.78, 4.88) * mm, "end": v(15.82, 4.85) * mm});
            skLineSegment(sketch, "E452", {"start": v(15.82, 4.85) * mm, "end": v(15.86, 4.8) * mm});
            skLineSegment(sketch, "E453", {"start": v(15.86, 4.8) * mm, "end": v(15.98, 4.6) * mm});
            skLineSegment(sketch, "E454", {"start": v(15.98, 4.6) * mm, "end": v(16.09, 4.34) * mm});
            skLineSegment(sketch, "E455", {"start": v(16.09, 4.34) * mm, "end": v(16.18, 4.04) * mm});
            skLineSegment(sketch, "E456", {"start": v(16.18, 4.04) * mm, "end": v(16.25, 3.63) * mm});
            skLineSegment(sketch, "E457", {"start": v(16.25, 3.63) * mm, "end": v(16.27, 3.18) * mm});
            skArc(sketch, "E458", {"start": v(15.29, 5.99) * mm, "mid": v(15.18, 5.65) * mm, "end": v(15.33, 5.33) * mm});
            skArc(sketch, "E459", {"start": v(15.29, 5.99) * mm, "mid": v(15.4, 6.14) * mm, "end": v(15.51, 6.3) * mm});
            skArc(sketch, "E460", {"start": v(16.16, 6.46) * mm, "mid": v(15.8, 6.5) * mm, "end": v(15.51, 6.3) * mm});
            skLineSegment(sketch, "E461", {"start": v(16.16, 6.46) * mm, "end": v(16.41, 6.33) * mm});
            skLineSegment(sketch, "E462", {"start": v(16.41, 6.33) * mm, "end": v(16.61, 6.22) * mm});
            skLineSegment(sketch, "E463", {"start": v(16.61, 6.22) * mm, "end": v(16.72, 6.17) * mm});
            skLineSegment(sketch, "E464", {"start": v(16.72, 6.17) * mm, "end": v(16.76, 6.14) * mm});
            skLineSegment(sketch, "E465", {"start": v(17.36, 9.59) * mm, "end": v(17.43, 9.6) * mm});
            skLineSegment(sketch, "E466", {"start": v(17.43, 9.6) * mm, "end": v(17.63, 9.7) * mm});
            skLineSegment(sketch, "E467", {"start": v(17.63, 9.7) * mm, "end": v(17.87, 9.84) * mm});
            skLineSegment(sketch, "E468", {"start": v(17.87, 9.84) * mm, "end": v(18.13, 10.04) * mm});
            skLineSegment(sketch, "E469", {"start": v(18.13, 10.04) * mm, "end": v(18.42, 10.33) * mm});
            skLineSegment(sketch, "E470", {"start": v(18.42, 10.33) * mm, "end": v(18.71, 10.67) * mm});
            skArc(sketch, "E471", {"start": v(18.71, 10.67) * mm, "mid": v(18.6, 11.01) * mm, "end": v(18.5, 11.34) * mm});
            skLineSegment(sketch, "E472", {"start": v(16.16, 11.1) * mm, "end": v(16.41, 11.25) * mm});
            skLineSegment(sketch, "E473", {"start": v(16.41, 11.25) * mm, "end": v(16.61, 11.35) * mm});
            skLineSegment(sketch, "E474", {"start": v(16.61, 11.35) * mm, "end": v(16.72, 11.4) * mm});
            skLineSegment(sketch, "E475", {"start": v(16.72, 11.4) * mm, "end": v(16.76, 11.43) * mm});
            skLineSegment(sketch, "E476", {"start": v(16.76, 11.43) * mm, "end": v(16.83, 11.45) * mm});
            skArc(sketch, "E477", {"start": v(15.51, 11.27) * mm, "mid": v(15.4, 11.43) * mm, "end": v(15.29, 11.59) * mm});
            skArc(sketch, "E478", {"start": v(15.33, 12.25) * mm, "mid": v(15.18, 11.92) * mm, "end": v(15.29, 11.59) * mm});
            skLineSegment(sketch, "E479", {"start": v(15.33, 12.25) * mm, "end": v(15.54, 12.45) * mm});
            skLineSegment(sketch, "E480", {"start": v(15.54, 12.45) * mm, "end": v(15.7, 12.6) * mm});
            skArc(sketch, "E481", {"start": v(15.51, 11.27) * mm, "mid": v(15.8, 11.07) * mm, "end": v(16.16, 11.1) * mm});
            skLineSegment(sketch, "E482", {"start": v(18.06, 11.46) * mm, "end": v(18.5, 11.34) * mm});
            skLineSegment(sketch, "E483", {"start": v(17.65, 11.52) * mm, "end": v(18.06, 11.46) * mm});
            skLineSegment(sketch, "E484", {"start": v(17.33, 11.53) * mm, "end": v(17.65, 11.52) * mm});
            skLineSegment(sketch, "E485", {"start": v(17.05, 11.5) * mm, "end": v(17.33, 11.53) * mm});
            skLineSegment(sketch, "E486", {"start": v(16.83, 11.45) * mm, "end": v(17.05, 11.5) * mm});
            skLineSegment(sketch, "E487", {"start": v(17.3, 9.58) * mm, "end": v(17.36, 9.59) * mm});
            skLineSegment(sketch, "E488", {"start": v(17.2, 9.56) * mm, "end": v(17.3, 9.58) * mm});
            skLineSegment(sketch, "E489", {"start": v(16.97, 9.53) * mm, "end": v(17.2, 9.56) * mm});
            skLineSegment(sketch, "E490", {"start": v(16.68, 9.49) * mm, "end": v(16.97, 9.53) * mm});
            skArc(sketch, "E491", {"start": v(16.68, 9.49) * mm, "mid": v(16.37, 9.32) * mm, "end": v(16.26, 8.98) * mm});
            skArc(sketch, "E492", {"start": v(16.26, 8.6) * mm, "mid": v(16.26, 8.79) * mm, "end": v(16.26, 8.98) * mm});
            skArc(sketch, "E493", {"start": v(16.26, 8.6) * mm, "mid": v(16.37, 8.26) * mm, "end": v(16.68, 8.08) * mm});
            skLineSegment(sketch, "E494", {"start": v(18.42, 7.25) * mm, "end": v(18.71, 6.9) * mm});
            skLineSegment(sketch, "E495", {"start": v(18.13, 7.54) * mm, "end": v(18.42, 7.25) * mm});
            skLineSegment(sketch, "E496", {"start": v(17.87, 7.73) * mm, "end": v(18.13, 7.54) * mm});
            skLineSegment(sketch, "E497", {"start": v(17.63, 7.88) * mm, "end": v(17.87, 7.73) * mm});
            skLineSegment(sketch, "E498", {"start": v(17.43, 7.97) * mm, "end": v(17.63, 7.88) * mm});
            skLineSegment(sketch, "E499", {"start": v(17.36, 7.98) * mm, "end": v(17.43, 7.97) * mm});
            skLineSegment(sketch, "E500", {"start": v(17.3, 8) * mm, "end": v(17.36, 7.98) * mm});
            skLineSegment(sketch, "E501", {"start": v(17.2, 8.01) * mm, "end": v(17.3, 8) * mm});
            skLineSegment(sketch, "E502", {"start": v(16.97, 8.04) * mm, "end": v(17.2, 8.01) * mm});
            skLineSegment(sketch, "E503", {"start": v(16.68, 8.08) * mm, "end": v(16.97, 8.04) * mm});
            skArc(sketch, "E504", {"start": v(18.5, 6.23) * mm, "mid": v(18.6, 6.56) * mm, "end": v(18.71, 6.9) * mm});
            skLineSegment(sketch, "E505", {"start": v(18.06, 6.12) * mm, "end": v(18.5, 6.23) * mm});
            skLineSegment(sketch, "E506", {"start": v(17.65, 6.06) * mm, "end": v(18.06, 6.12) * mm});
            skLineSegment(sketch, "E507", {"start": v(17.33, 6.05) * mm, "end": v(17.65, 6.06) * mm});
            skLineSegment(sketch, "E508", {"start": v(17.05, 6.07) * mm, "end": v(17.33, 6.05) * mm});
            skLineSegment(sketch, "E509", {"start": v(16.83, 6.12) * mm, "end": v(17.05, 6.07) * mm});
            skLineSegment(sketch, "E510", {"start": v(16.76, 6.14) * mm, "end": v(16.83, 6.12) * mm});
            skLineSegment(sketch, "E511", {"start": v(10.86, 3.6) * mm, "end": v(10.82, 3.38) * mm});
            skLineSegment(sketch, "E512", {"start": v(10.91, 3.89) * mm, "end": v(10.86, 3.6) * mm});
            skArc(sketch, "E513", {"start": v(10.91, 3.89) * mm, "mid": v(10.84, 4.24) * mm, "end": v(10.56, 4.45) * mm});
            skArc(sketch, "E514", {"start": v(10.19, 4.57) * mm, "mid": v(10.37, 4.5) * mm, "end": v(10.56, 4.45) * mm});
            skArc(sketch, "E515", {"start": v(10.19, 4.57) * mm, "mid": v(9.83, 4.57) * mm, "end": v(9.57, 4.32) * mm});
            skLineSegment(sketch, "E516", {"start": v(8.24, 2.93) * mm, "end": v(7.82, 2.76) * mm});
            skLineSegment(sketch, "E517", {"start": v(8.6, 3.12) * mm, "end": v(8.24, 2.93) * mm});
            skLineSegment(sketch, "E518", {"start": v(8.87, 3.3) * mm, "end": v(8.6, 3.12) * mm});
            skLineSegment(sketch, "E519", {"start": v(9.08, 3.48) * mm, "end": v(8.87, 3.3) * mm});
            skLineSegment(sketch, "E520", {"start": v(9.23, 3.65) * mm, "end": v(9.08, 3.48) * mm});
            skLineSegment(sketch, "E521", {"start": v(9.27, 3.7) * mm, "end": v(9.23, 3.65) * mm});
            skLineSegment(sketch, "E522", {"start": v(9.3, 3.76) * mm, "end": v(9.27, 3.7) * mm});
            skLineSegment(sketch, "E523", {"start": v(9.35, 3.86) * mm, "end": v(9.3, 3.76) * mm});
            skLineSegment(sketch, "E524", {"start": v(9.45, 4.06) * mm, "end": v(9.35, 3.86) * mm});
            skLineSegment(sketch, "E525", {"start": v(9.57, 4.32) * mm, "end": v(9.45, 4.06) * mm});
            skArc(sketch, "E526", {"start": v(7.25, 3.18) * mm, "mid": v(7.53, 2.96) * mm, "end": v(7.82, 2.76) * mm});
            skLineSegment(sketch, "E527", {"start": v(7.28, 3.63) * mm, "end": v(7.25, 3.18) * mm});
            skLineSegment(sketch, "E528", {"start": v(7.35, 4.04) * mm, "end": v(7.28, 3.63) * mm});
            skLineSegment(sketch, "E529", {"start": v(7.44, 4.34) * mm, "end": v(7.35, 4.04) * mm});
            skLineSegment(sketch, "E530", {"start": v(7.55, 4.6) * mm, "end": v(7.44, 4.34) * mm});
            skLineSegment(sketch, "E531", {"start": v(7.66, 4.8) * mm, "end": v(7.55, 4.6) * mm});
            skLineSegment(sketch, "E532", {"start": v(7.7, 4.85) * mm, "end": v(7.66, 4.8) * mm});
            skLineSegment(sketch, "E533", {"start": v(7.74, 4.88) * mm, "end": v(7.7, 4.85) * mm});
            skLineSegment(sketch, "E534", {"start": v(7.82, 4.97) * mm, "end": v(7.74, 4.88) * mm});
            skLineSegment(sketch, "E535", {"start": v(7.99, 5.12) * mm, "end": v(7.82, 4.97) * mm});
            skLineSegment(sketch, "E536", {"start": v(8.2, 5.33) * mm, "end": v(7.99, 5.12) * mm});
            skArc(sketch, "E537", {"start": v(8.2, 5.33) * mm, "mid": v(8.34, 5.65) * mm, "end": v(8.24, 5.99) * mm});
            skArc(sketch, "E538", {"start": v(8.01, 6.3) * mm, "mid": v(8.12, 6.14) * mm, "end": v(8.24, 5.99) * mm});
            skArc(sketch, "E539", {"start": v(8.01, 6.3) * mm, "mid": v(7.72, 6.5) * mm, "end": v(7.37, 6.46) * mm});
            skLineSegment(sketch, "E540", {"start": v(5.47, 6.12) * mm, "end": v(5.03, 6.23) * mm});
            skLineSegment(sketch, "E541", {"start": v(5.88, 6.06) * mm, "end": v(5.47, 6.12) * mm});
            skLineSegment(sketch, "E542", {"start": v(6.2, 6.05) * mm, "end": v(5.88, 6.06) * mm});
            skLineSegment(sketch, "E543", {"start": v(6.48, 6.07) * mm, "end": v(6.2, 6.05) * mm});
            skLineSegment(sketch, "E544", {"start": v(6.7, 6.12) * mm, "end": v(6.48, 6.07) * mm});
            skLineSegment(sketch, "E545", {"start": v(6.76, 6.14) * mm, "end": v(6.7, 6.12) * mm});
            skLineSegment(sketch, "E546", {"start": v(6.8, 6.17) * mm, "end": v(6.76, 6.14) * mm});
            skLineSegment(sketch, "E547", {"start": v(6.91, 6.22) * mm, "end": v(6.8, 6.17) * mm});
            skLineSegment(sketch, "E548", {"start": v(7.11, 6.33) * mm, "end": v(6.91, 6.22) * mm});
            skLineSegment(sketch, "E549", {"start": v(7.37, 6.46) * mm, "end": v(7.11, 6.33) * mm});
            skArc(sketch, "E550", {"start": v(4.81, 6.9) * mm, "mid": v(4.91, 6.56) * mm, "end": v(5.03, 6.23) * mm});
            skLineSegment(sketch, "E551", {"start": v(5.1, 7.25) * mm, "end": v(4.81, 6.9) * mm});
            skLineSegment(sketch, "E552", {"start": v(5.4, 7.54) * mm, "end": v(5.1, 7.25) * mm});
            skLineSegment(sketch, "E553", {"start": v(5.65, 7.73) * mm, "end": v(5.4, 7.54) * mm});
            skLineSegment(sketch, "E554", {"start": v(5.89, 7.88) * mm, "end": v(5.65, 7.73) * mm});
            skLineSegment(sketch, "E555", {"start": v(6.1, 7.97) * mm, "end": v(5.89, 7.88) * mm});
            skLineSegment(sketch, "E556", {"start": v(6.16, 7.98) * mm, "end": v(6.1, 7.97) * mm});
            skLineSegment(sketch, "E557", {"start": v(6.21, 8) * mm, "end": v(6.16, 7.98) * mm});
            skLineSegment(sketch, "E558", {"start": v(6.33, 8.01) * mm, "end": v(6.21, 8) * mm});
            skLineSegment(sketch, "E559", {"start": v(6.56, 8.04) * mm, "end": v(6.33, 8.01) * mm});
            skLineSegment(sketch, "E560", {"start": v(6.84, 8.08) * mm, "end": v(6.56, 8.04) * mm});
            skArc(sketch, "E561", {"start": v(6.84, 8.08) * mm, "mid": v(7.15, 8.26) * mm, "end": v(7.27, 8.6) * mm});
            skArc(sketch, "E562", {"start": v(7.27, 8.98) * mm, "mid": v(7.26, 8.79) * mm, "end": v(7.27, 8.6) * mm});
            skArc(sketch, "E563", {"start": v(7.27, 8.98) * mm, "mid": v(7.15, 9.32) * mm, "end": v(6.84, 9.49) * mm});
            skLineSegment(sketch, "E564", {"start": v(5.1, 10.33) * mm, "end": v(4.81, 10.67) * mm});
            skLineSegment(sketch, "E565", {"start": v(5.4, 10.04) * mm, "end": v(5.1, 10.33) * mm});
            skLineSegment(sketch, "E566", {"start": v(5.65, 9.84) * mm, "end": v(5.4, 10.04) * mm});
            skLineSegment(sketch, "E567", {"start": v(5.89, 9.7) * mm, "end": v(5.65, 9.84) * mm});
            skLineSegment(sketch, "E568", {"start": v(6.1, 9.6) * mm, "end": v(5.89, 9.7) * mm});
            skLineSegment(sketch, "E569", {"start": v(6.16, 9.59) * mm, "end": v(6.1, 9.6) * mm});
            skLineSegment(sketch, "E570", {"start": v(6.21, 9.58) * mm, "end": v(6.16, 9.59) * mm});
            skLineSegment(sketch, "E571", {"start": v(6.33, 9.56) * mm, "end": v(6.21, 9.58) * mm});
            skLineSegment(sketch, "E572", {"start": v(6.56, 9.53) * mm, "end": v(6.33, 9.56) * mm});
            skLineSegment(sketch, "E573", {"start": v(6.84, 9.49) * mm, "end": v(6.56, 9.53) * mm});
            skArc(sketch, "E574", {"start": v(5.03, 11.34) * mm, "mid": v(4.91, 11.01) * mm, "end": v(4.81, 10.67) * mm});
            skLineSegment(sketch, "E575", {"start": v(5.47, 11.46) * mm, "end": v(5.03, 11.34) * mm});
            skLineSegment(sketch, "E576", {"start": v(5.88, 11.52) * mm, "end": v(5.47, 11.46) * mm});
            skLineSegment(sketch, "E577", {"start": v(6.2, 11.53) * mm, "end": v(5.88, 11.52) * mm});
            skLineSegment(sketch, "E578", {"start": v(6.48, 11.5) * mm, "end": v(6.2, 11.53) * mm});
            skLineSegment(sketch, "E579", {"start": v(6.7, 11.45) * mm, "end": v(6.48, 11.5) * mm});
            skLineSegment(sketch, "E580", {"start": v(6.76, 11.43) * mm, "end": v(6.7, 11.45) * mm});
            skLineSegment(sketch, "E581", {"start": v(6.8, 11.4) * mm, "end": v(6.76, 11.43) * mm});
            skLineSegment(sketch, "E582", {"start": v(6.91, 11.35) * mm, "end": v(6.8, 11.4) * mm});
            skLineSegment(sketch, "E583", {"start": v(7.11, 11.25) * mm, "end": v(6.91, 11.35) * mm});
            skLineSegment(sketch, "E584", {"start": v(7.37, 11.1) * mm, "end": v(7.11, 11.25) * mm});
            skArc(sketch, "E585", {"start": v(7.37, 11.1) * mm, "mid": v(7.72, 11.07) * mm, "end": v(8.01, 11.27) * mm});
            skArc(sketch, "E586", {"start": v(8.24, 11.59) * mm, "mid": v(8.12, 11.43) * mm, "end": v(8.01, 11.27) * mm});
            skArc(sketch, "E587", {"start": v(8.24, 11.59) * mm, "mid": v(8.34, 11.92) * mm, "end": v(8.2, 12.25) * mm});
            skLineSegment(sketch, "E588", {"start": v(7.28, 13.95) * mm, "end": v(7.25, 14.4) * mm});
            skLineSegment(sketch, "E589", {"start": v(7.35, 13.54) * mm, "end": v(7.28, 13.95) * mm});
            skLineSegment(sketch, "E590", {"start": v(7.44, 13.23) * mm, "end": v(7.35, 13.54) * mm});
            skLineSegment(sketch, "E591", {"start": v(7.55, 12.97) * mm, "end": v(7.44, 13.23) * mm});
            skLineSegment(sketch, "E592", {"start": v(7.66, 12.78) * mm, "end": v(7.55, 12.97) * mm});
            skLineSegment(sketch, "E593", {"start": v(7.7, 12.73) * mm, "end": v(7.66, 12.78) * mm});
            skLineSegment(sketch, "E594", {"start": v(7.74, 12.69) * mm, "end": v(7.7, 12.73) * mm});
            skLineSegment(sketch, "E595", {"start": v(7.82, 12.6) * mm, "end": v(7.74, 12.69) * mm});
            skLineSegment(sketch, "E596", {"start": v(7.99, 12.45) * mm, "end": v(7.82, 12.6) * mm});
            skLineSegment(sketch, "E597", {"start": v(8.2, 12.25) * mm, "end": v(7.99, 12.45) * mm});
            skArc(sketch, "E598", {"start": v(7.82, 14.81) * mm, "mid": v(7.53, 14.61) * mm, "end": v(7.25, 14.4) * mm});
            skLineSegment(sketch, "E599", {"start": v(8.24, 14.65) * mm, "end": v(7.82, 14.81) * mm});
            skLineSegment(sketch, "E600", {"start": v(8.6, 14.45) * mm, "end": v(8.24, 14.65) * mm});
            skLineSegment(sketch, "E601", {"start": v(8.87, 14.27) * mm, "end": v(8.6, 14.45) * mm});
            skLineSegment(sketch, "E602", {"start": v(9.08, 14.1) * mm, "end": v(8.87, 14.27) * mm});
            skLineSegment(sketch, "E603", {"start": v(9.23, 13.92) * mm, "end": v(9.08, 14.1) * mm});
            skLineSegment(sketch, "E604", {"start": v(9.27, 13.86) * mm, "end": v(9.23, 13.92) * mm});
            skLineSegment(sketch, "E605", {"start": v(9.3, 13.82) * mm, "end": v(9.27, 13.86) * mm});
            skLineSegment(sketch, "E606", {"start": v(9.35, 13.71) * mm, "end": v(9.3, 13.82) * mm});
            skLineSegment(sketch, "E607", {"start": v(9.45, 13.5) * mm, "end": v(9.35, 13.71) * mm});
            skLineSegment(sketch, "E608", {"start": v(9.57, 13.25) * mm, "end": v(9.45, 13.5) * mm});
            skArc(sketch, "E609", {"start": v(9.57, 13.25) * mm, "mid": v(9.83, 13) * mm, "end": v(10.19, 13) * mm});
            skArc(sketch, "E610", {"start": v(10.56, 13.12) * mm, "mid": v(10.37, 13.07) * mm, "end": v(10.19, 13) * mm});
            skArc(sketch, "E611", {"start": v(10.56, 13.12) * mm, "mid": v(10.84, 13.33) * mm, "end": v(10.91, 13.68) * mm});
            skLineSegment(sketch, "E612", {"start": v(11.17, 15.6) * mm, "end": v(11.4, 15.98) * mm});
            skLineSegment(sketch, "E613", {"start": v(-5.02, 7.87) * mm, "end": v(-4.97, 7.85) * mm});
            skLineSegment(sketch, "E614", {"start": v(-5.05, 7.88) * mm, "end": v(-5.02, 7.87) * mm});
            skLineSegment(sketch, "E615", {"start": v(-5.11, 7.9) * mm, "end": v(-5.05, 7.88) * mm});
            skLineSegment(sketch, "E616", {"start": v(-5.27, 7.92) * mm, "end": v(-5.11, 7.9) * mm});
            skLineSegment(sketch, "E617", {"start": v(-5.6, 7.98) * mm, "end": v(-5.27, 7.92) * mm});
            skLineSegment(sketch, "E618", {"start": v(-6, 8.06) * mm, "end": v(-5.6, 7.98) * mm});
            skArc(sketch, "E619", {"start": v(-3.86, 5.66) * mm, "mid": v(-3.7, 6.03) * mm, "end": v(-3.55, 6.41) * mm});
            skLineSegment(sketch, "E620", {"start": v(-4.35, 5.55) * mm, "end": v(-3.86, 5.66) * mm});
            skLineSegment(sketch, "E621", {"start": v(-4.8, 5.5) * mm, "end": v(-4.35, 5.55) * mm});
            skLineSegment(sketch, "E622", {"start": v(-5.23, 5.5) * mm, "end": v(-4.8, 5.5) * mm});
            skLineSegment(sketch, "E623", {"start": v(-5.6, 5.56) * mm, "end": v(-5.23, 5.5) * mm});
            skLineSegment(sketch, "E624", {"start": v(-5.88, 5.65) * mm, "end": v(-5.6, 5.56) * mm});
            skLineSegment(sketch, "E625", {"start": v(-5.93, 5.67) * mm, "end": v(-5.88, 5.65) * mm});
            skLineSegment(sketch, "E626", {"start": v(-5.96, 5.69) * mm, "end": v(-5.93, 5.67) * mm});
            skLineSegment(sketch, "E627", {"start": v(-6.01, 5.72) * mm, "end": v(-5.96, 5.69) * mm});
            skLineSegment(sketch, "E628", {"start": v(-6.14, 5.8) * mm, "end": v(-6.01, 5.72) * mm});
            skLineSegment(sketch, "E629", {"start": v(-6.41, 6) * mm, "end": v(-6.14, 5.8) * mm});
            skLineSegment(sketch, "E630", {"start": v(-6.76, 6.24) * mm, "end": v(-6.41, 6) * mm});
            skArc(sketch, "E631", {"start": v(-6.76, 6.24) * mm, "mid": v(-7.18, 6.34) * mm, "end": v(-7.56, 6.15) * mm});
            skLineSegment(sketch, "E632", {"start": v(15.7, 12.6) * mm, "end": v(15.78, 12.69) * mm});
            skLineSegment(sketch, "E633", {"start": v(15.78, 12.69) * mm, "end": v(15.82, 12.73) * mm});
            skLineSegment(sketch, "E634", {"start": v(15.82, 12.73) * mm, "end": v(15.86, 12.78) * mm});
            skLineSegment(sketch, "E635", {"start": v(15.86, 12.78) * mm, "end": v(15.98, 12.97) * mm});
            skLineSegment(sketch, "E636", {"start": v(15.98, 12.97) * mm, "end": v(16.09, 13.23) * mm});
            skLineSegment(sketch, "E637", {"start": v(16.09, 13.23) * mm, "end": v(16.18, 13.54) * mm});
            skLineSegment(sketch, "E638", {"start": v(16.18, 13.54) * mm, "end": v(16.25, 13.95) * mm});
            skLineSegment(sketch, "E639", {"start": v(16.25, 13.95) * mm, "end": v(16.27, 14.4) * mm});
            skArc(sketch, "E640", {"start": v(16.27, 14.4) * mm, "mid": v(16, 14.61) * mm, "end": v(15.7, 14.81) * mm});
            skLineSegment(sketch, "E641", {"start": v(13.95, 13.25) * mm, "end": v(14.08, 13.5) * mm});
            skLineSegment(sketch, "E642", {"start": v(14.08, 13.5) * mm, "end": v(14.18, 13.71) * mm});
            skLineSegment(sketch, "E643", {"start": v(14.18, 13.71) * mm, "end": v(14.23, 13.82) * mm});
            skLineSegment(sketch, "E644", {"start": v(14.23, 13.82) * mm, "end": v(14.26, 13.86) * mm});
            skLineSegment(sketch, "E645", {"start": v(14.26, 13.86) * mm, "end": v(14.3, 13.92) * mm});
            skLineSegment(sketch, "E646", {"start": v(14.3, 13.92) * mm, "end": v(14.44, 14.1) * mm});
            skLineSegment(sketch, "E647", {"start": v(14.44, 14.1) * mm, "end": v(14.65, 14.27) * mm});
            skLineSegment(sketch, "E648", {"start": v(14.65, 14.27) * mm, "end": v(14.92, 14.45) * mm});
            skLineSegment(sketch, "E649", {"start": v(14.92, 14.45) * mm, "end": v(15.28, 14.65) * mm});
            skLineSegment(sketch, "E650", {"start": v(15.28, 14.65) * mm, "end": v(15.7, 14.81) * mm});
            skArc(sketch, "E651", {"start": v(13.33, 13) * mm, "mid": v(13.7, 13) * mm, "end": v(13.95, 13.25) * mm});
            skArc(sketch, "E652", {"start": v(13.33, 13) * mm, "mid": v(13.15, 13.07) * mm, "end": v(12.97, 13.12) * mm});
            skArc(sketch, "E653", {"start": v(-10.62, 7.3) * mm, "mid": v(-9.82, 7.52) * mm, "end": v(-9.24, 8.1) * mm});
            skArc(sketch, "E654", {"start": v(-10.62, 10.3) * mm, "mid": v(-11.32, 10.12) * mm, "end": v(-11.84, 9.6) * mm});
            skLineSegment(sketch, "E655", {"start": v(-10.62, 10.3) * mm, "end": v(-10.62, 10.5) * mm});
            skLineSegment(sketch, "E656", {"start": v(-11.84, 9.6) * mm, "end": v(-12.01, 9.7) * mm});
            skLineSegment(sketch, "E657", {"start": v(-11.84, 8.2) * mm, "end": v(-12.01, 8.1) * mm});
            skLineSegment(sketch, "E658", {"start": v(-10.62, 7.5) * mm, "end": v(-10.62, 7.3) * mm});
            skLineSegment(sketch, "E659", {"start": v(-9.41, 8.2) * mm, "end": v(-9.24, 8.1) * mm});
            skLineSegment(sketch, "E660", {"start": v(-9.41, 9.6) * mm, "end": v(-9.24, 9.7) * mm});
            skArc(sketch, "E661", {"start": v(-11.84, 8.2) * mm, "mid": v(-11.32, 7.7) * mm, "end": v(-10.62, 7.5) * mm});
            skArc(sketch, "E662", {"start": v(-9.41, 8.2) * mm, "mid": v(-9.22, 8.9) * mm, "end": v(-9.41, 9.6) * mm});
            skArc(sketch, "E663", {"start": v(-9.24, 9.7) * mm, "mid": v(-9.82, 10.29) * mm, "end": v(-10.62, 10.5) * mm});
            skArc(sketch, "E664", {"start": v(-12.01, 9.7) * mm, "mid": v(-12.22, 8.9) * mm, "end": v(-12.01, 8.1) * mm});
            skArc(sketch, "E665", {"start": v(11.76, 7.19) * mm, "mid": v(12.56, 7.4) * mm, "end": v(13.15, 7.99) * mm});
            skArc(sketch, "E666", {"start": v(11.76, 10.19) * mm, "mid": v(11.06, 10) * mm, "end": v(10.55, 9.49) * mm});
            skLineSegment(sketch, "E667", {"start": v(11.76, 10.19) * mm, "end": v(11.76, 10.39) * mm});
            skLineSegment(sketch, "E668", {"start": v(10.55, 9.49) * mm, "end": v(10.38, 9.59) * mm});
            skLineSegment(sketch, "E669", {"start": v(10.55, 8.09) * mm, "end": v(10.38, 7.99) * mm});
            skLineSegment(sketch, "E670", {"start": v(11.76, 7.39) * mm, "end": v(11.76, 7.19) * mm});
            skLineSegment(sketch, "E671", {"start": v(12.97, 8.09) * mm, "end": v(13.15, 7.99) * mm});
            skLineSegment(sketch, "E672", {"start": v(12.97, 9.49) * mm, "end": v(13.15, 9.59) * mm});
            skArc(sketch, "E673", {"start": v(10.55, 8.09) * mm, "mid": v(11.06, 7.57) * mm, "end": v(11.76, 7.39) * mm});
            skArc(sketch, "E674", {"start": v(12.97, 8.09) * mm, "mid": v(13.16, 8.79) * mm, "end": v(12.97, 9.49) * mm});
            skArc(sketch, "E675", {"start": v(13.15, 9.59) * mm, "mid": v(12.56, 10.17) * mm, "end": v(11.76, 10.39) * mm});
            skArc(sketch, "E676", {"start": v(10.38, 9.59) * mm, "mid": v(10.16, 8.79) * mm, "end": v(10.38, 7.99) * mm});
            skArc(sketch, "E677", {"start": v(-7.57, -11.77) * mm, "mid": v(-7.99, -11.67) * mm, "end": v(-8.37, -11.86) * mm});
            skLineSegment(sketch, "E678", {"start": v(-7.57, -11.77) * mm, "end": v(-7.22, -12.01) * mm});
            skLineSegment(sketch, "E679", {"start": v(-7.22, -12.01) * mm, "end": v(-6.95, -12.2) * mm});
            skLineSegment(sketch, "E680", {"start": v(-6.95, -12.2) * mm, "end": v(-6.82, -12.29) * mm});
            skLineSegment(sketch, "E681", {"start": v(-6.82, -12.29) * mm, "end": v(-6.77, -12.32) * mm});
            skLineSegment(sketch, "E682", {"start": v(-6.77, -12.32) * mm, "end": v(-6.73, -12.34) * mm});
            skLineSegment(sketch, "E683", {"start": v(-6.73, -12.34) * mm, "end": v(-6.69, -12.36) * mm});
            skLineSegment(sketch, "E684", {"start": v(-6.69, -12.36) * mm, "end": v(-6.4, -12.45) * mm});
            skLineSegment(sketch, "E685", {"start": v(-6.4, -12.45) * mm, "end": v(-6.04, -12.5) * mm});
            skLineSegment(sketch, "E686", {"start": v(-6.04, -12.5) * mm, "end": v(-5.62, -12.5) * mm});
            skLineSegment(sketch, "E687", {"start": v(-5.62, -12.5) * mm, "end": v(-5.16, -12.45) * mm});
            skLineSegment(sketch, "E688", {"start": v(-5.16, -12.45) * mm, "end": v(-4.67, -12.34) * mm});
            skArc(sketch, "E689", {"start": v(-4.67, -12.34) * mm, "mid": v(-4.5, -11.97) * mm, "end": v(-4.36, -11.6) * mm});
            skLineSegment(sketch, "E690", {"start": v(-6.82, -9.95) * mm, "end": v(-6.4, -10.03) * mm});
            skLineSegment(sketch, "E691", {"start": v(-6.4, -10.03) * mm, "end": v(-6.08, -10.09) * mm});
            skLineSegment(sketch, "E692", {"start": v(-6.08, -10.09) * mm, "end": v(-5.92, -10.12) * mm});
            skCircle(sketch, "E693", {"center": v(-12.99, 41.4) * mm, "radius": 3 * mm});
            skLineSegment(sketch, "E694", {"start": v(-5.92, -10.12) * mm, "end": v(-5.86, -10.13) * mm});
            skLineSegment(sketch, "E695", {"start": v(-5.86, -10.13) * mm, "end": v(-5.82, -10.14) * mm});
            skLineSegment(sketch, "E696", {"start": v(-5.82, -10.14) * mm, "end": v(-5.78, -10.16) * mm});
            skLineSegment(sketch, "E697", {"start": v(-5.78, -10.16) * mm, "end": v(-5.51, -10.3) * mm});
            skLineSegment(sketch, "E698", {"start": v(-5.51, -10.3) * mm, "end": v(-5.22, -10.52) * mm});
            skLineSegment(sketch, "E699", {"start": v(-5.22, -10.52) * mm, "end": v(-4.91, -10.81) * mm});
            skLineSegment(sketch, "E700", {"start": v(-4.91, -10.81) * mm, "end": v(-4.63, -11.17) * mm});
            skLineSegment(sketch, "E701", {"start": v(-4.63, -11.17) * mm, "end": v(-4.36, -11.6) * mm});
            skArc(sketch, "E702", {"start": v(-7.31, -9.32) * mm, "mid": v(-7.18, -9.73) * mm, "end": v(-6.82, -9.95) * mm});
            skArc(sketch, "E703", {"start": v(-7.31, -9.32) * mm, "mid": v(-7.3, -9.1) * mm, "end": v(-7.31, -8.89) * mm});
            skArc(sketch, "E704", {"start": v(-6.82, -8.26) * mm, "mid": v(-7.18, -8.48) * mm, "end": v(-7.31, -8.89) * mm});
            skLineSegment(sketch, "E705", {"start": v(-6.82, -8.26) * mm, "end": v(-6.4, -8.18) * mm});
            skLineSegment(sketch, "E706", {"start": v(-6.4, -8.18) * mm, "end": v(-6.08, -8.12) * mm});
            skLineSegment(sketch, "E707", {"start": v(-6.08, -8.12) * mm, "end": v(-5.92, -8.1) * mm});
            skLineSegment(sketch, "E708", {"start": v(-5.92, -8.1) * mm, "end": v(-5.86, -8.08) * mm});
            skLineSegment(sketch, "E709", {"start": v(-5.86, -8.08) * mm, "end": v(-5.82, -8.07) * mm});
            skLineSegment(sketch, "E710", {"start": v(-5.82, -8.07) * mm, "end": v(-5.78, -8.05) * mm});
            skLineSegment(sketch, "E711", {"start": v(-5.78, -8.05) * mm, "end": v(-5.51, -7.91) * mm});
            skLineSegment(sketch, "E712", {"start": v(-5.51, -7.91) * mm, "end": v(-5.22, -7.7) * mm});
            skLineSegment(sketch, "E713", {"start": v(-5.22, -7.7) * mm, "end": v(-4.91, -7.4) * mm});
            skLineSegment(sketch, "E714", {"start": v(-4.91, -7.4) * mm, "end": v(-4.63, -7.03) * mm});
            skLineSegment(sketch, "E715", {"start": v(-4.63, -7.03) * mm, "end": v(-4.36, -6.61) * mm});
            skArc(sketch, "E716", {"start": v(-4.36, -6.61) * mm, "mid": v(-4.5, -6.23) * mm, "end": v(-4.67, -5.86) * mm});
            skLineSegment(sketch, "E717", {"start": v(-7.57, -6.44) * mm, "end": v(-7.22, -6.2) * mm});
            skLineSegment(sketch, "E718", {"start": v(-7.22, -6.2) * mm, "end": v(-6.95, -6.01) * mm});
            skLineSegment(sketch, "E719", {"start": v(-6.95, -6.01) * mm, "end": v(-6.82, -5.92) * mm});
            skLineSegment(sketch, "E720", {"start": v(-6.82, -5.92) * mm, "end": v(-6.77, -5.89) * mm});
            skLineSegment(sketch, "E721", {"start": v(-6.77, -5.89) * mm, "end": v(-6.73, -5.87) * mm});
            skLineSegment(sketch, "E722", {"start": v(-6.73, -5.87) * mm, "end": v(-6.69, -5.85) * mm});
            skLineSegment(sketch, "E723", {"start": v(-6.69, -5.85) * mm, "end": v(-6.4, -5.76) * mm});
            skLineSegment(sketch, "E724", {"start": v(-6.4, -5.76) * mm, "end": v(-6.04, -5.7) * mm});
            skLineSegment(sketch, "E725", {"start": v(-6.04, -5.7) * mm, "end": v(-5.62, -5.7) * mm});
            skLineSegment(sketch, "E726", {"start": v(-5.62, -5.7) * mm, "end": v(-5.16, -5.75) * mm});
            skLineSegment(sketch, "E727", {"start": v(-5.16, -5.75) * mm, "end": v(-4.67, -5.86) * mm});
            skArc(sketch, "E728", {"start": v(-8.37, -6.35) * mm, "mid": v(-7.99, -6.54) * mm, "end": v(-7.57, -6.44) * mm});
            skArc(sketch, "E729", {"start": v(-8.37, -6.35) * mm, "mid": v(-8.52, -6.19) * mm, "end": v(-8.67, -6.04) * mm});
            skArc(sketch, "E730", {"start": v(-8.77, -5.24) * mm, "mid": v(-8.87, -5.66) * mm, "end": v(-8.67, -6.04) * mm});
            skLineSegment(sketch, "E731", {"start": v(-8.77, -5.24) * mm, "end": v(-8.52, -4.9) * mm});
            skLineSegment(sketch, "E732", {"start": v(-8.52, -4.9) * mm, "end": v(-8.34, -4.62) * mm});
            skLineSegment(sketch, "E733", {"start": v(-8.34, -4.62) * mm, "end": v(-8.25, -4.5) * mm});
            skLineSegment(sketch, "E734", {"start": v(-8.25, -4.5) * mm, "end": v(-8.22, -4.44) * mm});
            skLineSegment(sketch, "E735", {"start": v(-8.22, -4.44) * mm, "end": v(-8.2, -4.4) * mm});
            skLineSegment(sketch, "E736", {"start": v(-8.2, -4.4) * mm, "end": v(-8.18, -4.36) * mm});
            skLineSegment(sketch, "E737", {"start": v(-8.18, -4.36) * mm, "end": v(-8.1, -4.08) * mm});
            skLineSegment(sketch, "E738", {"start": v(-8.1, -4.08) * mm, "end": v(-8.04, -3.7) * mm});
            skLineSegment(sketch, "E739", {"start": v(-8.04, -3.7) * mm, "end": v(-8.03, -3.29) * mm});
            skLineSegment(sketch, "E740", {"start": v(-8.03, -3.29) * mm, "end": v(-8.08, -2.83) * mm});
            skLineSegment(sketch, "E741", {"start": v(-8.08, -2.83) * mm, "end": v(-8.2, -2.34) * mm});
            skArc(sketch, "E742", {"start": v(-8.2, -2.34) * mm, "mid": v(-8.56, -2.18) * mm, "end": v(-8.94, -2.03) * mm});
            skLineSegment(sketch, "E743", {"start": v(-10.59, -4.49) * mm, "end": v(-10.51, -4.07) * mm});
            skLineSegment(sketch, "E744", {"start": v(-10.51, -4.07) * mm, "end": v(-10.45, -3.75) * mm});
            skLineSegment(sketch, "E745", {"start": v(-10.45, -3.75) * mm, "end": v(-10.42, -3.59) * mm});
            skLineSegment(sketch, "E746", {"start": v(-10.42, -3.59) * mm, "end": v(-10.4, -3.53) * mm});
            skLineSegment(sketch, "E747", {"start": v(-10.4, -3.53) * mm, "end": v(-10.4, -3.5) * mm});
            skLineSegment(sketch, "E748", {"start": v(-10.4, -3.5) * mm, "end": v(-10.38, -3.45) * mm});
            skLineSegment(sketch, "E749", {"start": v(-10.38, -3.45) * mm, "end": v(-10.24, -3.19) * mm});
            skLineSegment(sketch, "E750", {"start": v(-10.24, -3.19) * mm, "end": v(-10.02, -2.89) * mm});
            skLineSegment(sketch, "E751", {"start": v(-10.02, -2.89) * mm, "end": v(-9.72, -2.59) * mm});
            skLineSegment(sketch, "E752", {"start": v(-9.72, -2.59) * mm, "end": v(-9.36, -2.3) * mm});
            skLineSegment(sketch, "E753", {"start": v(-9.36, -2.3) * mm, "end": v(-8.94, -2.03) * mm});
            skArc(sketch, "E754", {"start": v(-11.21, -4.99) * mm, "mid": v(-10.8, -4.86) * mm, "end": v(-10.59, -4.49) * mm});
            skArc(sketch, "E755", {"start": v(-11.21, -4.99) * mm, "mid": v(-11.43, -4.98) * mm, "end": v(-11.65, -4.99) * mm});
            skArc(sketch, "E756", {"start": v(-12.28, -4.49) * mm, "mid": v(-12.06, -4.86) * mm, "end": v(-11.65, -4.99) * mm});
            skLineSegment(sketch, "E757", {"start": v(-12.28, -4.49) * mm, "end": v(-12.35, -4.07) * mm});
            skLineSegment(sketch, "E758", {"start": v(-12.35, -4.07) * mm, "end": v(-12.41, -3.75) * mm});
            skLineSegment(sketch, "E759", {"start": v(-12.41, -3.75) * mm, "end": v(-12.44, -3.59) * mm});
            skLineSegment(sketch, "E760", {"start": v(-12.44, -3.59) * mm, "end": v(-12.46, -3.53) * mm});
            skLineSegment(sketch, "E761", {"start": v(-12.46, -3.53) * mm, "end": v(-12.47, -3.5) * mm});
            skLineSegment(sketch, "E762", {"start": v(-12.47, -3.5) * mm, "end": v(-12.49, -3.45) * mm});
            skLineSegment(sketch, "E763", {"start": v(-12.49, -3.45) * mm, "end": v(-12.62, -3.19) * mm});
            skLineSegment(sketch, "E764", {"start": v(-12.62, -3.19) * mm, "end": v(-12.85, -2.89) * mm});
            skLineSegment(sketch, "E765", {"start": v(-12.85, -2.89) * mm, "end": v(-13.14, -2.59) * mm});
            skLineSegment(sketch, "E766", {"start": v(-13.14, -2.59) * mm, "end": v(-13.5, -2.3) * mm});
            skLineSegment(sketch, "E767", {"start": v(-13.5, -2.3) * mm, "end": v(-13.92, -2.03) * mm});
            skArc(sketch, "E768", {"start": v(-13.92, -2.03) * mm, "mid": v(-14.3, -2.18) * mm, "end": v(-14.67, -2.34) * mm});
            skLineSegment(sketch, "E769", {"start": v(-14.1, -5.24) * mm, "end": v(-14.34, -4.9) * mm});
            skLineSegment(sketch, "E770", {"start": v(-14.34, -4.9) * mm, "end": v(-14.53, -4.62) * mm});
            skLineSegment(sketch, "E771", {"start": v(-14.53, -4.62) * mm, "end": v(-14.62, -4.5) * mm});
            skLineSegment(sketch, "E772", {"start": v(-14.62, -4.5) * mm, "end": v(-14.65, -4.44) * mm});
            skLineSegment(sketch, "E773", {"start": v(-14.65, -4.44) * mm, "end": v(-14.67, -4.4) * mm});
            skLineSegment(sketch, "E774", {"start": v(-14.67, -4.4) * mm, "end": v(-14.69, -4.36) * mm});
            skLineSegment(sketch, "E775", {"start": v(-14.69, -4.36) * mm, "end": v(-14.78, -4.08) * mm});
            skLineSegment(sketch, "E776", {"start": v(-14.78, -4.08) * mm, "end": v(-14.83, -3.7) * mm});
            skLineSegment(sketch, "E777", {"start": v(-14.83, -3.7) * mm, "end": v(-14.83, -3.29) * mm});
            skLineSegment(sketch, "E778", {"start": v(-14.83, -3.29) * mm, "end": v(-14.78, -2.83) * mm});
            skLineSegment(sketch, "E779", {"start": v(-14.78, -2.83) * mm, "end": v(-14.67, -2.34) * mm});
            skArc(sketch, "E780", {"start": v(-14.2, -6.04) * mm, "mid": v(-14, -5.66) * mm, "end": v(-14.1, -5.24) * mm});
            skArc(sketch, "E781", {"start": v(-14.2, -6.04) * mm, "mid": v(-14.35, -6.19) * mm, "end": v(-14.5, -6.35) * mm});
            skArc(sketch, "E782", {"start": v(-15.3, -6.44) * mm, "mid": v(-14.88, -6.54) * mm, "end": v(-14.5, -6.35) * mm});
            skLineSegment(sketch, "E783", {"start": v(-15.3, -6.44) * mm, "end": v(-15.64, -6.2) * mm});
            skLineSegment(sketch, "E784", {"start": v(-15.64, -6.2) * mm, "end": v(-15.91, -6.01) * mm});
            skLineSegment(sketch, "E785", {"start": v(-15.91, -6.01) * mm, "end": v(-16.05, -5.92) * mm});
            skLineSegment(sketch, "E786", {"start": v(-16.05, -5.92) * mm, "end": v(-16.1, -5.89) * mm});
            skLineSegment(sketch, "E787", {"start": v(-16.1, -5.89) * mm, "end": v(-16.13, -5.87) * mm});
            skLineSegment(sketch, "E788", {"start": v(-16.13, -5.87) * mm, "end": v(-16.18, -5.85) * mm});
            skLineSegment(sketch, "E789", {"start": v(-16.18, -5.85) * mm, "end": v(-16.46, -5.76) * mm});
            skLineSegment(sketch, "E790", {"start": v(-16.46, -5.76) * mm, "end": v(-16.83, -5.7) * mm});
            skLineSegment(sketch, "E791", {"start": v(-16.83, -5.7) * mm, "end": v(-17.25, -5.7) * mm});
            skLineSegment(sketch, "E792", {"start": v(-17.25, -5.7) * mm, "end": v(-17.71, -5.75) * mm});
            skLineSegment(sketch, "E793", {"start": v(-17.71, -5.75) * mm, "end": v(-18.2, -5.86) * mm});
            skArc(sketch, "E794", {"start": v(-18.2, -5.86) * mm, "mid": v(-18.36, -6.23) * mm, "end": v(-18.5, -6.61) * mm});
            skLineSegment(sketch, "E795", {"start": v(-16.05, -8.26) * mm, "end": v(-16.47, -8.18) * mm});
            skLineSegment(sketch, "E796", {"start": v(-16.47, -8.18) * mm, "end": v(-16.79, -8.12) * mm});
            skLineSegment(sketch, "E797", {"start": v(-16.79, -8.12) * mm, "end": v(-16.95, -8.1) * mm});
            skLineSegment(sketch, "E798", {"start": v(-16.95, -8.1) * mm, "end": v(-17, -8.08) * mm});
            skLineSegment(sketch, "E799", {"start": v(-17, -8.08) * mm, "end": v(-17.04, -8.07) * mm});
            skLineSegment(sketch, "E800", {"start": v(-17.04, -8.07) * mm, "end": v(-17.09, -8.05) * mm});
            skLineSegment(sketch, "E801", {"start": v(-17.09, -8.05) * mm, "end": v(-17.35, -7.91) * mm});
            skLineSegment(sketch, "E802", {"start": v(-17.35, -7.91) * mm, "end": v(-17.65, -7.7) * mm});
            skLineSegment(sketch, "E803", {"start": v(-17.65, -7.7) * mm, "end": v(-17.95, -7.4) * mm});
            skLineSegment(sketch, "E804", {"start": v(-17.95, -7.4) * mm, "end": v(-18.24, -7.03) * mm});
            skLineSegment(sketch, "E805", {"start": v(-18.24, -7.03) * mm, "end": v(-18.5, -6.61) * mm});
            skArc(sketch, "E806", {"start": v(-15.55, -8.89) * mm, "mid": v(-15.68, -8.48) * mm, "end": v(-16.05, -8.26) * mm});
            skArc(sketch, "E807", {"start": v(-15.55, -8.89) * mm, "mid": v(-15.56, -9.1) * mm, "end": v(-15.55, -9.32) * mm});
            skArc(sketch, "E808", {"start": v(-16.05, -9.95) * mm, "mid": v(-15.68, -9.73) * mm, "end": v(-15.55, -9.32) * mm});
            skLineSegment(sketch, "E809", {"start": v(-16.05, -9.95) * mm, "end": v(-16.47, -10.03) * mm});
            skLineSegment(sketch, "E810", {"start": v(-16.47, -10.03) * mm, "end": v(-16.79, -10.09) * mm});
            skLineSegment(sketch, "E811", {"start": v(-16.79, -10.09) * mm, "end": v(-16.95, -10.12) * mm});
            skLineSegment(sketch, "E812", {"start": v(-16.95, -10.12) * mm, "end": v(-17, -10.13) * mm});
            skLineSegment(sketch, "E813", {"start": v(-17, -10.13) * mm, "end": v(-17.04, -10.14) * mm});
            skLineSegment(sketch, "E814", {"start": v(-17.04, -10.14) * mm, "end": v(-17.09, -10.16) * mm});
            skLineSegment(sketch, "E815", {"start": v(-17.09, -10.16) * mm, "end": v(-17.35, -10.3) * mm});
            skLineSegment(sketch, "E816", {"start": v(-17.35, -10.3) * mm, "end": v(-17.65, -10.52) * mm});
            skLineSegment(sketch, "E817", {"start": v(-17.65, -10.52) * mm, "end": v(-17.95, -10.81) * mm});
            skLineSegment(sketch, "E818", {"start": v(-17.95, -10.81) * mm, "end": v(-18.24, -11.17) * mm});
            skLineSegment(sketch, "E819", {"start": v(-18.24, -11.17) * mm, "end": v(-18.5, -11.6) * mm});
            skArc(sketch, "E820", {"start": v(-18.5, -11.6) * mm, "mid": v(-18.36, -11.97) * mm, "end": v(-18.2, -12.34) * mm});
            skLineSegment(sketch, "E821", {"start": v(-15.3, -11.77) * mm, "end": v(-15.64, -12.01) * mm});
            skLineSegment(sketch, "E822", {"start": v(-15.64, -12.01) * mm, "end": v(-15.91, -12.2) * mm});
            skLineSegment(sketch, "E823", {"start": v(-15.91, -12.2) * mm, "end": v(-16.05, -12.29) * mm});
            skLineSegment(sketch, "E824", {"start": v(-16.05, -12.29) * mm, "end": v(-16.1, -12.32) * mm});
            skLineSegment(sketch, "E825", {"start": v(-16.1, -12.32) * mm, "end": v(-16.13, -12.34) * mm});
            skLineSegment(sketch, "E826", {"start": v(-16.13, -12.34) * mm, "end": v(-16.18, -12.36) * mm});
            skLineSegment(sketch, "E827", {"start": v(-16.18, -12.36) * mm, "end": v(-16.46, -12.45) * mm});
            skLineSegment(sketch, "E828", {"start": v(-16.46, -12.45) * mm, "end": v(-16.83, -12.5) * mm});
            skLineSegment(sketch, "E829", {"start": v(-16.83, -12.5) * mm, "end": v(-17.25, -12.5) * mm});
            skLineSegment(sketch, "E830", {"start": v(-17.25, -12.5) * mm, "end": v(-17.71, -12.45) * mm});
            skLineSegment(sketch, "E831", {"start": v(-17.71, -12.45) * mm, "end": v(-18.2, -12.34) * mm});
            skArc(sketch, "E832", {"start": v(-14.5, -11.86) * mm, "mid": v(-14.88, -11.67) * mm, "end": v(-15.3, -11.77) * mm});
            skArc(sketch, "E833", {"start": v(-14.5, -11.86) * mm, "mid": v(-14.35, -12.02) * mm, "end": v(-14.2, -12.17) * mm});
            skArc(sketch, "E834", {"start": v(-14.1, -12.97) * mm, "mid": v(-14, -12.55) * mm, "end": v(-14.2, -12.17) * mm});
            skLineSegment(sketch, "E835", {"start": v(-14.1, -12.97) * mm, "end": v(-14.34, -13.32) * mm});
            skLineSegment(sketch, "E836", {"start": v(-14.34, -13.32) * mm, "end": v(-14.53, -13.59) * mm});
            skLineSegment(sketch, "E837", {"start": v(-14.53, -13.59) * mm, "end": v(-14.62, -13.72) * mm});
            skLineSegment(sketch, "E838", {"start": v(-14.62, -13.72) * mm, "end": v(-14.65, -13.77) * mm});
            skLineSegment(sketch, "E839", {"start": v(-14.65, -13.77) * mm, "end": v(-14.67, -13.8) * mm});
            skLineSegment(sketch, "E840", {"start": v(-14.67, -13.8) * mm, "end": v(-14.69, -13.85) * mm});
            skLineSegment(sketch, "E841", {"start": v(-14.69, -13.85) * mm, "end": v(-14.78, -14.13) * mm});
            skLineSegment(sketch, "E842", {"start": v(-14.78, -14.13) * mm, "end": v(-14.83, -14.5) * mm});
            skLineSegment(sketch, "E843", {"start": v(-14.83, -14.5) * mm, "end": v(-14.83, -14.92) * mm});
            skLineSegment(sketch, "E844", {"start": v(-14.83, -14.92) * mm, "end": v(-14.78, -15.38) * mm});
            skLineSegment(sketch, "E845", {"start": v(-14.78, -15.38) * mm, "end": v(-14.67, -15.87) * mm});
            skArc(sketch, "E846", {"start": v(-14.67, -15.87) * mm, "mid": v(-14.3, -16.03) * mm, "end": v(-13.92, -16.18) * mm});
            skLineSegment(sketch, "E847", {"start": v(-12.28, -13.72) * mm, "end": v(-12.35, -14.14) * mm});
            skLineSegment(sketch, "E848", {"start": v(-12.35, -14.14) * mm, "end": v(-12.41, -14.46) * mm});
            skLineSegment(sketch, "E849", {"start": v(-12.41, -14.46) * mm, "end": v(-12.44, -14.62) * mm});
            skLineSegment(sketch, "E850", {"start": v(-12.44, -14.62) * mm, "end": v(-12.46, -14.67) * mm});
            skLineSegment(sketch, "E851", {"start": v(-12.46, -14.67) * mm, "end": v(-12.47, -14.71) * mm});
            skLineSegment(sketch, "E852", {"start": v(-12.47, -14.71) * mm, "end": v(-12.49, -14.76) * mm});
            skLineSegment(sketch, "E853", {"start": v(-12.49, -14.76) * mm, "end": v(-12.62, -15.02) * mm});
            skLineSegment(sketch, "E854", {"start": v(-12.62, -15.02) * mm, "end": v(-12.85, -15.32) * mm});
            skLineSegment(sketch, "E855", {"start": v(-12.85, -15.32) * mm, "end": v(-13.14, -15.62) * mm});
            skLineSegment(sketch, "E856", {"start": v(-13.14, -15.62) * mm, "end": v(-13.5, -15.91) * mm});
            skLineSegment(sketch, "E857", {"start": v(-13.5, -15.91) * mm, "end": v(-13.92, -16.18) * mm});
            skArc(sketch, "E858", {"start": v(-11.65, -13.22) * mm, "mid": v(-12.06, -13.35) * mm, "end": v(-12.28, -13.72) * mm});
            skArc(sketch, "E859", {"start": v(-11.65, -13.22) * mm, "mid": v(-11.43, -13.23) * mm, "end": v(-11.21, -13.22) * mm});
            skArc(sketch, "E860", {"start": v(-10.59, -13.72) * mm, "mid": v(-10.8, -13.35) * mm, "end": v(-11.21, -13.22) * mm});
            skLineSegment(sketch, "E861", {"start": v(-10.59, -13.72) * mm, "end": v(-10.51, -14.14) * mm});
            skLineSegment(sketch, "E862", {"start": v(-10.51, -14.14) * mm, "end": v(-10.45, -14.46) * mm});
            skLineSegment(sketch, "E863", {"start": v(-10.45, -14.46) * mm, "end": v(-10.42, -14.62) * mm});
            skLineSegment(sketch, "E864", {"start": v(-10.42, -14.62) * mm, "end": v(-10.4, -14.67) * mm});
            skLineSegment(sketch, "E865", {"start": v(-10.4, -14.67) * mm, "end": v(-10.4, -14.71) * mm});
            skLineSegment(sketch, "E866", {"start": v(-10.4, -14.71) * mm, "end": v(-10.38, -14.76) * mm});
            skLineSegment(sketch, "E867", {"start": v(-10.38, -14.76) * mm, "end": v(-10.24, -15.02) * mm});
            skLineSegment(sketch, "E868", {"start": v(-10.24, -15.02) * mm, "end": v(-10.02, -15.32) * mm});
            skLineSegment(sketch, "E869", {"start": v(-10.02, -15.32) * mm, "end": v(-9.72, -15.62) * mm});
            skLineSegment(sketch, "E870", {"start": v(-9.72, -15.62) * mm, "end": v(-9.36, -15.91) * mm});
            skLineSegment(sketch, "E871", {"start": v(-9.36, -15.91) * mm, "end": v(-8.94, -16.18) * mm});
            skArc(sketch, "E872", {"start": v(-8.94, -16.18) * mm, "mid": v(-8.56, -16.03) * mm, "end": v(-8.2, -15.87) * mm});
            skLineSegment(sketch, "E873", {"start": v(-8.77, -12.97) * mm, "end": v(-8.52, -13.32) * mm});
            skLineSegment(sketch, "E874", {"start": v(-8.52, -13.32) * mm, "end": v(-8.34, -13.59) * mm});
            skLineSegment(sketch, "E875", {"start": v(-8.34, -13.59) * mm, "end": v(-8.25, -13.72) * mm});
            skLineSegment(sketch, "E876", {"start": v(-8.25, -13.72) * mm, "end": v(-8.22, -13.77) * mm});
            skLineSegment(sketch, "E877", {"start": v(-8.22, -13.77) * mm, "end": v(-8.2, -13.8) * mm});
            skLineSegment(sketch, "E878", {"start": v(-8.2, -13.8) * mm, "end": v(-8.18, -13.85) * mm});
            skLineSegment(sketch, "E879", {"start": v(-8.18, -13.85) * mm, "end": v(-8.1, -14.13) * mm});
            skLineSegment(sketch, "E880", {"start": v(-8.1, -14.13) * mm, "end": v(-8.04, -14.5) * mm});
            skLineSegment(sketch, "E881", {"start": v(-8.04, -14.5) * mm, "end": v(-8.03, -14.92) * mm});
            skLineSegment(sketch, "E882", {"start": v(-8.03, -14.92) * mm, "end": v(-8.08, -15.38) * mm});
            skLineSegment(sketch, "E883", {"start": v(-8.08, -15.38) * mm, "end": v(-8.2, -15.87) * mm});
            skArc(sketch, "E884", {"start": v(-8.67, -12.17) * mm, "mid": v(-8.87, -12.55) * mm, "end": v(-8.77, -12.97) * mm});
            skArc(sketch, "E885", {"start": v(-8.67, -12.17) * mm, "mid": v(-8.52, -12.02) * mm, "end": v(-8.37, -11.86) * mm});
            skArc(sketch, "E886", {"start": v(11.8, -4.32) * mm, "mid": v(11.87, -4.67) * mm, "end": v(12.16, -4.89) * mm});
            skLineSegment(sketch, "E887", {"start": v(11.8, -4.32) * mm, "end": v(11.86, -4.04) * mm});
            skLineSegment(sketch, "E888", {"start": v(11.86, -4.04) * mm, "end": v(11.9, -3.82) * mm});
            skLineSegment(sketch, "E889", {"start": v(11.9, -3.82) * mm, "end": v(11.91, -3.7) * mm});
            skLineSegment(sketch, "E890", {"start": v(11.91, -3.7) * mm, "end": v(11.92, -3.65) * mm});
            skLineSegment(sketch, "E891", {"start": v(11.92, -3.65) * mm, "end": v(11.92, -3.58) * mm});
            skLineSegment(sketch, "E892", {"start": v(11.92, -3.58) * mm, "end": v(11.9, -3.36) * mm});
            skLineSegment(sketch, "E893", {"start": v(11.9, -3.36) * mm, "end": v(11.84, -3.08) * mm});
            skLineSegment(sketch, "E894", {"start": v(11.84, -3.08) * mm, "end": v(11.73, -2.78) * mm});
            skLineSegment(sketch, "E895", {"start": v(11.73, -2.78) * mm, "end": v(11.55, -2.41) * mm});
            skLineSegment(sketch, "E896", {"start": v(11.55, -2.41) * mm, "end": v(11.3, -2.03) * mm});
            skArc(sketch, "E897", {"start": v(11.3, -2.03) * mm, "mid": v(10.95, -2.02) * mm, "end": v(10.6, -2.03) * mm});
            skLineSegment(sketch, "E898", {"start": v(10.1, -4.32) * mm, "end": v(10.05, -4.04) * mm});
            skLineSegment(sketch, "E899", {"start": v(10.05, -4.04) * mm, "end": v(10.01, -3.82) * mm});
            skLineSegment(sketch, "E900", {"start": v(10.01, -3.82) * mm, "end": v(10, -3.7) * mm});
            skLineSegment(sketch, "E901", {"start": v(10, -3.7) * mm, "end": v(9.99, -3.65) * mm});
            skLineSegment(sketch, "E902", {"start": v(9.99, -3.65) * mm, "end": v(9.98, -3.58) * mm});
            skLineSegment(sketch, "E903", {"start": v(9.98, -3.58) * mm, "end": v(10, -3.36) * mm});
            skLineSegment(sketch, "E904", {"start": v(10, -3.36) * mm, "end": v(10.07, -3.08) * mm});
            skLineSegment(sketch, "E905", {"start": v(10.07, -3.08) * mm, "end": v(10.17, -2.78) * mm});
            skLineSegment(sketch, "E906", {"start": v(10.17, -2.78) * mm, "end": v(10.36, -2.41) * mm});
            skLineSegment(sketch, "E907", {"start": v(10.36, -2.41) * mm, "end": v(10.6, -2.03) * mm});
            skArc(sketch, "E908", {"start": v(9.75, -4.89) * mm, "mid": v(10.03, -4.67) * mm, "end": v(10.1, -4.32) * mm});
            skArc(sketch, "E909", {"start": v(9.75, -4.89) * mm, "mid": v(9.56, -4.94) * mm, "end": v(9.38, -5) * mm});
            skArc(sketch, "E910", {"start": v(8.76, -4.76) * mm, "mid": v(9.03, -5) * mm, "end": v(9.38, -5) * mm});
            skLineSegment(sketch, "E911", {"start": v(8.76, -4.76) * mm, "end": v(8.64, -4.5) * mm});
            skLineSegment(sketch, "E912", {"start": v(8.64, -4.5) * mm, "end": v(8.54, -4.3) * mm});
            skLineSegment(sketch, "E913", {"start": v(8.54, -4.3) * mm, "end": v(8.48, -4.2) * mm});
            skLineSegment(sketch, "E914", {"start": v(8.48, -4.2) * mm, "end": v(8.46, -4.14) * mm});
            skLineSegment(sketch, "E915", {"start": v(8.46, -4.14) * mm, "end": v(8.42, -4.09) * mm});
            skLineSegment(sketch, "E916", {"start": v(8.42, -4.09) * mm, "end": v(8.27, -3.92) * mm});
            skLineSegment(sketch, "E917", {"start": v(8.27, -3.92) * mm, "end": v(8.06, -3.73) * mm});
            skLineSegment(sketch, "E918", {"start": v(8.06, -3.73) * mm, "end": v(7.8, -3.55) * mm});
            skLineSegment(sketch, "E919", {"start": v(7.8, -3.55) * mm, "end": v(7.43, -3.36) * mm});
            skLineSegment(sketch, "E920", {"start": v(7.43, -3.36) * mm, "end": v(7.01, -3.2) * mm});
            skArc(sketch, "E921", {"start": v(7.01, -3.2) * mm, "mid": v(6.72, -3.4) * mm, "end": v(6.44, -3.61) * mm});
            skLineSegment(sketch, "E922", {"start": v(7.39, -5.76) * mm, "end": v(7.18, -5.56) * mm});
            skLineSegment(sketch, "E923", {"start": v(7.18, -5.56) * mm, "end": v(7.02, -5.4) * mm});
            skLineSegment(sketch, "E924", {"start": v(7.02, -5.4) * mm, "end": v(6.93, -5.32) * mm});
            skLineSegment(sketch, "E925", {"start": v(6.93, -5.32) * mm, "end": v(6.9, -5.28) * mm});
            skLineSegment(sketch, "E926", {"start": v(6.9, -5.28) * mm, "end": v(6.85, -5.23) * mm});
            skLineSegment(sketch, "E927", {"start": v(6.85, -5.23) * mm, "end": v(6.74, -5.03) * mm});
            skLineSegment(sketch, "E928", {"start": v(6.74, -5.03) * mm, "end": v(6.63, -4.78) * mm});
            skLineSegment(sketch, "E929", {"start": v(6.63, -4.78) * mm, "end": v(6.54, -4.47) * mm});
            skLineSegment(sketch, "E930", {"start": v(6.54, -4.47) * mm, "end": v(6.47, -4.06) * mm});
            skLineSegment(sketch, "E931", {"start": v(6.47, -4.06) * mm, "end": v(6.44, -3.61) * mm});
            skArc(sketch, "E932", {"start": v(7.43, -6.42) * mm, "mid": v(7.54, -6.08) * mm, "end": v(7.39, -5.76) * mm});
            skArc(sketch, "E933", {"start": v(7.43, -6.42) * mm, "mid": v(7.31, -6.58) * mm, "end": v(7.2, -6.74) * mm});
            skArc(sketch, "E934", {"start": v(6.56, -6.9) * mm, "mid": v(6.91, -6.94) * mm, "end": v(7.2, -6.74) * mm});
            skLineSegment(sketch, "E935", {"start": v(6.56, -6.9) * mm, "end": v(6.3, -6.76) * mm});
            skLineSegment(sketch, "E936", {"start": v(6.3, -6.76) * mm, "end": v(6.1, -6.66) * mm});
            skLineSegment(sketch, "E937", {"start": v(6.1, -6.66) * mm, "end": v(6, -6.6) * mm});
            skLineSegment(sketch, "E938", {"start": v(6, -6.6) * mm, "end": v(5.95, -6.58) * mm});
            skLineSegment(sketch, "E939", {"start": v(5.95, -6.58) * mm, "end": v(5.89, -6.56) * mm});
            skLineSegment(sketch, "E940", {"start": v(5.89, -6.56) * mm, "end": v(5.67, -6.5) * mm});
            skLineSegment(sketch, "E941", {"start": v(5.67, -6.5) * mm, "end": v(5.39, -6.48) * mm});
            skLineSegment(sketch, "E942", {"start": v(5.39, -6.48) * mm, "end": v(5.07, -6.5) * mm});
            skLineSegment(sketch, "E943", {"start": v(5.07, -6.5) * mm, "end": v(4.66, -6.55) * mm});
            skLineSegment(sketch, "E944", {"start": v(4.66, -6.55) * mm, "end": v(4.22, -6.66) * mm});
            skArc(sketch, "E945", {"start": v(4.22, -6.66) * mm, "mid": v(4.1, -7) * mm, "end": v(4, -7.33) * mm});
            skLineSegment(sketch, "E946", {"start": v(6.03, -8.52) * mm, "end": v(5.75, -8.48) * mm});
            skLineSegment(sketch, "E947", {"start": v(5.75, -8.48) * mm, "end": v(5.52, -8.45) * mm});
            skLineSegment(sketch, "E948", {"start": v(5.52, -8.45) * mm, "end": v(5.4, -8.43) * mm});
            skLineSegment(sketch, "E949", {"start": v(5.4, -8.43) * mm, "end": v(5.35, -8.42) * mm});
            skLineSegment(sketch, "E950", {"start": v(5.35, -8.42) * mm, "end": v(5.29, -8.4) * mm});
            skLineSegment(sketch, "E951", {"start": v(5.29, -8.4) * mm, "end": v(5.08, -8.31) * mm});
            skLineSegment(sketch, "E952", {"start": v(5.08, -8.31) * mm, "end": v(4.84, -8.17) * mm});
            skLineSegment(sketch, "E953", {"start": v(4.84, -8.17) * mm, "end": v(4.59, -7.97) * mm});
            skLineSegment(sketch, "E954", {"start": v(4.59, -7.97) * mm, "end": v(4.3, -7.68) * mm});
            skLineSegment(sketch, "E955", {"start": v(4.3, -7.68) * mm, "end": v(4, -7.33) * mm});
            skArc(sketch, "E956", {"start": v(6.46, -9.03) * mm, "mid": v(6.34, -8.7) * mm, "end": v(6.03, -8.52) * mm});
            skArc(sketch, "E957", {"start": v(6.46, -9.03) * mm, "mid": v(6.45, -9.22) * mm, "end": v(6.46, -9.41) * mm});
            skArc(sketch, "E958", {"start": v(6.03, -9.92) * mm, "mid": v(6.34, -9.75) * mm, "end": v(6.46, -9.41) * mm});
            skLineSegment(sketch, "E959", {"start": v(6.03, -9.92) * mm, "end": v(5.75, -9.97) * mm});
            skCircle(sketch, "E960", {"center": v(-11.47, 28.21) * mm, "radius": 3 * mm});
            skLineSegment(sketch, "E961", {"start": v(5.75, -9.97) * mm, "end": v(5.52, -10) * mm});
            skLineSegment(sketch, "E962", {"start": v(5.52, -10) * mm, "end": v(5.4, -10.02) * mm});
            skLineSegment(sketch, "E963", {"start": v(5.4, -10.02) * mm, "end": v(5.35, -10.02) * mm});
            skLineSegment(sketch, "E964", {"start": v(5.35, -10.02) * mm, "end": v(5.29, -10.04) * mm});
            skLineSegment(sketch, "E965", {"start": v(5.29, -10.04) * mm, "end": v(5.08, -10.13) * mm});
            skLineSegment(sketch, "E966", {"start": v(5.08, -10.13) * mm, "end": v(4.84, -10.28) * mm});
            skLineSegment(sketch, "E967", {"start": v(4.84, -10.28) * mm, "end": v(4.59, -10.47) * mm});
            skLineSegment(sketch, "E968", {"start": v(4.59, -10.47) * mm, "end": v(4.3, -10.76) * mm});
            skLineSegment(sketch, "E969", {"start": v(4.3, -10.76) * mm, "end": v(4, -11.1) * mm});
            skArc(sketch, "E970", {"start": v(4, -11.1) * mm, "mid": v(4.1, -11.45) * mm, "end": v(4.22, -11.78) * mm});
            skLineSegment(sketch, "E971", {"start": v(6.56, -11.55) * mm, "end": v(6.3, -11.68) * mm});
            skLineSegment(sketch, "E972", {"start": v(6.3, -11.68) * mm, "end": v(6.1, -11.79) * mm});
            skLineSegment(sketch, "E973", {"start": v(6.1, -11.79) * mm, "end": v(6, -11.84) * mm});
            skLineSegment(sketch, "E974", {"start": v(6, -11.84) * mm, "end": v(5.95, -11.86) * mm});
            skLineSegment(sketch, "E975", {"start": v(5.95, -11.86) * mm, "end": v(5.89, -11.89) * mm});
            skLineSegment(sketch, "E976", {"start": v(5.89, -11.89) * mm, "end": v(5.67, -11.94) * mm});
            skLineSegment(sketch, "E977", {"start": v(5.67, -11.94) * mm, "end": v(5.39, -11.96) * mm});
            skLineSegment(sketch, "E978", {"start": v(5.39, -11.96) * mm, "end": v(5.07, -11.95) * mm});
            skLineSegment(sketch, "E979", {"start": v(5.07, -11.95) * mm, "end": v(4.66, -11.9) * mm});
            skLineSegment(sketch, "E980", {"start": v(4.66, -11.9) * mm, "end": v(4.22, -11.78) * mm});
            skArc(sketch, "E981", {"start": v(7.2, -11.7) * mm, "mid": v(6.91, -11.5) * mm, "end": v(6.56, -11.55) * mm});
            skArc(sketch, "E982", {"start": v(7.2, -11.7) * mm, "mid": v(7.31, -11.87) * mm, "end": v(7.43, -12.02) * mm});
            skArc(sketch, "E983", {"start": v(7.39, -12.68) * mm, "mid": v(7.54, -12.36) * mm, "end": v(7.43, -12.02) * mm});
            skLineSegment(sketch, "E984", {"start": v(7.39, -12.68) * mm, "end": v(7.18, -12.88) * mm});
            skLineSegment(sketch, "E985", {"start": v(7.18, -12.88) * mm, "end": v(7.02, -13.04) * mm});
            skLineSegment(sketch, "E986", {"start": v(7.02, -13.04) * mm, "end": v(6.93, -13.12) * mm});
            skLineSegment(sketch, "E987", {"start": v(6.93, -13.12) * mm, "end": v(6.9, -13.16) * mm});
            skLineSegment(sketch, "E988", {"start": v(6.9, -13.16) * mm, "end": v(6.85, -13.22) * mm});
            skLineSegment(sketch, "E989", {"start": v(6.85, -13.22) * mm, "end": v(6.74, -13.4) * mm});
            skLineSegment(sketch, "E990", {"start": v(6.74, -13.4) * mm, "end": v(6.63, -13.67) * mm});
            skLineSegment(sketch, "E991", {"start": v(6.63, -13.67) * mm, "end": v(6.54, -13.97) * mm});
            skLineSegment(sketch, "E992", {"start": v(6.54, -13.97) * mm, "end": v(6.47, -14.38) * mm});
            skLineSegment(sketch, "E993", {"start": v(6.47, -14.38) * mm, "end": v(6.44, -14.83) * mm});
            skArc(sketch, "E994", {"start": v(6.44, -14.83) * mm, "mid": v(6.72, -15.05) * mm, "end": v(7.01, -15.25) * mm});
            skLineSegment(sketch, "E995", {"start": v(8.76, -13.68) * mm, "end": v(8.64, -13.94) * mm});
            skLineSegment(sketch, "E996", {"start": v(8.64, -13.94) * mm, "end": v(8.54, -14.15) * mm});
            skLineSegment(sketch, "E997", {"start": v(8.54, -14.15) * mm, "end": v(8.48, -14.25) * mm});
            skLineSegment(sketch, "E998", {"start": v(8.48, -14.25) * mm, "end": v(8.46, -14.3) * mm});
            skLineSegment(sketch, "E999", {"start": v(8.46, -14.3) * mm, "end": v(8.42, -14.36) * mm});
            skLineSegment(sketch, "E1000", {"start": v(8.42, -14.36) * mm, "end": v(8.27, -14.53) * mm});
            skLineSegment(sketch, "E1001", {"start": v(8.27, -14.53) * mm, "end": v(8.06, -14.7) * mm});
            skLineSegment(sketch, "E1002", {"start": v(8.06, -14.7) * mm, "end": v(7.8, -14.89) * mm});
            skLineSegment(sketch, "E1003", {"start": v(7.8, -14.89) * mm, "end": v(7.43, -15.08) * mm});
            skLineSegment(sketch, "E1004", {"start": v(7.43, -15.08) * mm, "end": v(7.01, -15.25) * mm});
            skArc(sketch, "E1005", {"start": v(9.38, -13.44) * mm, "mid": v(9.03, -13.44) * mm, "end": v(8.76, -13.68) * mm});
            skArc(sketch, "E1006", {"start": v(9.38, -13.44) * mm, "mid": v(9.56, -13.5) * mm, "end": v(9.75, -13.56) * mm});
            skArc(sketch, "E1007", {"start": v(10.1, -14.12) * mm, "mid": v(10.03, -13.77) * mm, "end": v(9.75, -13.56) * mm});
            skLineSegment(sketch, "E1008", {"start": v(10.1, -14.12) * mm, "end": v(10.05, -14.4) * mm});
            skLineSegment(sketch, "E1009", {"start": v(10.05, -14.4) * mm, "end": v(10.01, -14.63) * mm});
            skLineSegment(sketch, "E1010", {"start": v(10.01, -14.63) * mm, "end": v(10, -14.74) * mm});
            skLineSegment(sketch, "E1011", {"start": v(10, -14.74) * mm, "end": v(9.99, -14.8) * mm});
            skLineSegment(sketch, "E1012", {"start": v(9.99, -14.8) * mm, "end": v(9.98, -14.86) * mm});
            skLineSegment(sketch, "E1013", {"start": v(9.98, -14.86) * mm, "end": v(10, -15.09) * mm});
            skLineSegment(sketch, "E1014", {"start": v(10, -15.09) * mm, "end": v(10.07, -15.36) * mm});
            skLineSegment(sketch, "E1015", {"start": v(10.07, -15.36) * mm, "end": v(10.17, -15.66) * mm});
            skLineSegment(sketch, "E1016", {"start": v(10.17, -15.66) * mm, "end": v(10.36, -16.03) * mm});
            skLineSegment(sketch, "E1017", {"start": v(10.36, -16.03) * mm, "end": v(10.6, -16.41) * mm});
            skArc(sketch, "E1018", {"start": v(10.6, -16.41) * mm, "mid": v(10.95, -16.42) * mm, "end": v(11.3, -16.41) * mm});
            skLineSegment(sketch, "E1019", {"start": v(11.8, -14.12) * mm, "end": v(11.86, -14.4) * mm});
            skLineSegment(sketch, "E1020", {"start": v(11.86, -14.4) * mm, "end": v(11.9, -14.63) * mm});
            skLineSegment(sketch, "E1021", {"start": v(11.9, -14.63) * mm, "end": v(11.91, -14.74) * mm});
            skLineSegment(sketch, "E1022", {"start": v(11.91, -14.74) * mm, "end": v(11.92, -14.8) * mm});
            skLineSegment(sketch, "E1023", {"start": v(11.92, -14.8) * mm, "end": v(11.92, -14.86) * mm});
            skLineSegment(sketch, "E1024", {"start": v(11.92, -14.86) * mm, "end": v(11.9, -15.09) * mm});
            skLineSegment(sketch, "E1025", {"start": v(11.9, -15.09) * mm, "end": v(11.84, -15.36) * mm});
            skLineSegment(sketch, "E1026", {"start": v(11.84, -15.36) * mm, "end": v(11.73, -15.66) * mm});
            skLineSegment(sketch, "E1027", {"start": v(11.73, -15.66) * mm, "end": v(11.55, -16.03) * mm});
            skLineSegment(sketch, "E1028", {"start": v(11.55, -16.03) * mm, "end": v(11.3, -16.41) * mm});
            skSolve(sketch);
        }
        {
            var Q0;
            Q0=qCreatedBy(makeId("Front.planeOp"),FACE);
            var sketch = newSketch(context, id + "F1", { "sketchPlane" : qUnion([Q0])});
            skArc(sketch, "E1029", {"start": v(-65.12, 71.31) * mm, "mid": v(-65.39, 71.53) * mm, "end": v(-65.66, 71.75) * mm});
            skArc(sketch, "E1030", {"start": v(-65.12, 71.31) * mm, "mid": v(-64.55, 71.12) * mm, "end": v(-64, 71.37) * mm});
            skLineSegment(sketch, "E1031", {"start": v(-61.43, 72.85) * mm, "end": v(-60.46, 73.02) * mm});
            skLineSegment(sketch, "E1032", {"start": v(-62.28, 72.6) * mm, "end": v(-61.43, 72.85) * mm});
            skLineSegment(sketch, "E1033", {"start": v(-63.02, 72.25) * mm, "end": v(-62.28, 72.6) * mm});
            skLineSegment(sketch, "E1034", {"start": v(-63.17, 72.16) * mm, "end": v(-63.02, 72.25) * mm});
            skLineSegment(sketch, "E1035", {"start": v(-63.29, 72.07) * mm, "end": v(-63.17, 72.16) * mm});
            skLineSegment(sketch, "E1036", {"start": v(-63.37, 72) * mm, "end": v(-63.29, 72.07) * mm});
            skLineSegment(sketch, "E1037", {"start": v(-63.59, 71.8) * mm, "end": v(-63.37, 72) * mm});
            skLineSegment(sketch, "E1038", {"start": v(-64, 71.37) * mm, "end": v(-63.59, 71.8) * mm});
            skArc(sketch, "E1039", {"start": v(-59.66, 72) * mm, "mid": v(-60.05, 72.52) * mm, "end": v(-60.46, 73.02) * mm});
            skLineSegment(sketch, "E1040", {"start": v(-60.03, 71.1) * mm, "end": v(-59.66, 72) * mm});
            skLineSegment(sketch, "E1041", {"start": v(-60.46, 70.33) * mm, "end": v(-60.03, 71.1) * mm});
            skLineSegment(sketch, "E1042", {"start": v(-60.97, 69.68) * mm, "end": v(-60.46, 70.33) * mm});
            skLineSegment(sketch, "E1043", {"start": v(-61.1, 69.56) * mm, "end": v(-60.97, 69.68) * mm});
            skLineSegment(sketch, "E1044", {"start": v(-61.2, 69.46) * mm, "end": v(-61.1, 69.56) * mm});
            skLineSegment(sketch, "E1045", {"start": v(-61.3, 69.4) * mm, "end": v(-61.2, 69.46) * mm});
            skLineSegment(sketch, "E1046", {"start": v(-62.05, 68.93) * mm, "end": v(-61.55, 69.23) * mm});
            skArc(sketch, "E1047", {"start": v(-62.05, 68.93) * mm, "mid": v(-62.41, 68.45) * mm, "end": v(-62.35, 67.84) * mm});
            skArc(sketch, "E1048", {"start": v(-62.05, 67.22) * mm, "mid": v(-62.2, 67.53) * mm, "end": v(-62.35, 67.84) * mm});
            skArc(sketch, "E1049", {"start": v(-62.05, 67.22) * mm, "mid": v(-61.62, 66.8) * mm, "end": v(-61.01, 66.78) * mm});
            skLineSegment(sketch, "E1050", {"start": v(-58.06, 67) * mm, "end": v(-57.12, 66.73) * mm});
            skLineSegment(sketch, "E1051", {"start": v(-58.93, 67.15) * mm, "end": v(-58.06, 67) * mm});
            skLineSegment(sketch, "E1052", {"start": v(-59.76, 67.15) * mm, "end": v(-58.93, 67.15) * mm});
            skLineSegment(sketch, "E1053", {"start": v(-60.07, 67.1) * mm, "end": v(-59.93, 67.13) * mm});
            skLineSegment(sketch, "E1054", {"start": v(-60.18, 67.08) * mm, "end": v(-60.07, 67.1) * mm});
            skLineSegment(sketch, "E1055", {"start": v(-60.46, 66.98) * mm, "end": v(-60.18, 67.08) * mm});
            skLineSegment(sketch, "E1056", {"start": v(-61.01, 66.78) * mm, "end": v(-60.46, 66.98) * mm});
            skArc(sketch, "E1057", {"start": v(-56.83, 65.47) * mm, "mid": v(-56.96, 66.1) * mm, "end": v(-57.12, 66.73) * mm});
            skLineSegment(sketch, "E1058", {"start": v(-57.56, 64.81) * mm, "end": v(-56.83, 65.47) * mm});
            skLineSegment(sketch, "E1059", {"start": v(-58.28, 64.3) * mm, "end": v(-57.56, 64.81) * mm});
            skLineSegment(sketch, "E1060", {"start": v(-59.02, 63.94) * mm, "end": v(-58.28, 64.3) * mm});
            skLineSegment(sketch, "E1061", {"start": v(-59.19, 63.89) * mm, "end": v(-59.02, 63.94) * mm});
            skLineSegment(sketch, "E1062", {"start": v(-59.33, 63.85) * mm, "end": v(-59.19, 63.89) * mm});
            skLineSegment(sketch, "E1063", {"start": v(-59.43, 63.83) * mm, "end": v(-59.33, 63.85) * mm});
            skLineSegment(sketch, "E1064", {"start": v(-59.73, 63.8) * mm, "end": v(-59.43, 63.83) * mm});
            skLineSegment(sketch, "E1065", {"start": v(-60.32, 63.74) * mm, "end": v(-59.73, 63.8) * mm});
            skArc(sketch, "E1066", {"start": v(-60.32, 63.74) * mm, "mid": v(-60.86, 63.46) * mm, "end": v(-61.06, 62.9) * mm});
            skArc(sketch, "E1067", {"start": v(-61.06, 62.2) * mm, "mid": v(-61.06, 62.54) * mm, "end": v(-61.06, 62.9) * mm});
            skArc(sketch, "E1068", {"start": v(-61.06, 62.2) * mm, "mid": v(-60.86, 61.63) * mm, "end": v(-60.32, 61.35) * mm});
            skLineSegment(sketch, "E1069", {"start": v(-57.56, 60.27) * mm, "end": v(-56.83, 59.61) * mm});
            skLineSegment(sketch, "E1070", {"start": v(-58.28, 60.78) * mm, "end": v(-57.56, 60.27) * mm});
            skLineSegment(sketch, "E1071", {"start": v(-59.02, 61.14) * mm, "end": v(-58.28, 60.78) * mm});
            skLineSegment(sketch, "E1072", {"start": v(-59.19, 61.2) * mm, "end": v(-59.02, 61.14) * mm});
            skLineSegment(sketch, "E1073", {"start": v(-59.33, 61.24) * mm, "end": v(-59.19, 61.2) * mm});
            skLineSegment(sketch, "E1074", {"start": v(-59.43, 61.26) * mm, "end": v(-59.33, 61.24) * mm});
            skLineSegment(sketch, "E1075", {"start": v(-59.73, 61.3) * mm, "end": v(-59.43, 61.26) * mm});
            skLineSegment(sketch, "E1076", {"start": v(-60.32, 61.35) * mm, "end": v(-59.73, 61.3) * mm});
            skArc(sketch, "E1077", {"start": v(-57.12, 58.36) * mm, "mid": v(-56.96, 58.98) * mm, "end": v(-56.83, 59.61) * mm});
            skLineSegment(sketch, "E1078", {"start": v(-58.06, 58.08) * mm, "end": v(-57.12, 58.36) * mm});
            skLineSegment(sketch, "E1079", {"start": v(-58.93, 57.94) * mm, "end": v(-58.06, 58.08) * mm});
            skLineSegment(sketch, "E1080", {"start": v(-59.76, 57.93) * mm, "end": v(-58.93, 57.94) * mm});
            skLineSegment(sketch, "E1081", {"start": v(-59.93, 57.95) * mm, "end": v(-59.76, 57.93) * mm});
            skLineSegment(sketch, "E1082", {"start": v(-60.07, 57.98) * mm, "end": v(-59.93, 57.95) * mm});
            skLineSegment(sketch, "E1083", {"start": v(-60.18, 58) * mm, "end": v(-60.07, 57.98) * mm});
            skLineSegment(sketch, "E1084", {"start": v(-60.46, 58.1) * mm, "end": v(-60.18, 58) * mm});
            skLineSegment(sketch, "E1085", {"start": v(-61.01, 58.3) * mm, "end": v(-60.46, 58.1) * mm});
            skArc(sketch, "E1086", {"start": v(-61.01, 58.3) * mm, "mid": v(-61.62, 58.3) * mm, "end": v(-62.05, 57.87) * mm});
            skArc(sketch, "E1087", {"start": v(-62.35, 57.24) * mm, "mid": v(-62.2, 57.55) * mm, "end": v(-62.05, 57.87) * mm});
            skArc(sketch, "E1088", {"start": v(-62.35, 57.24) * mm, "mid": v(-62.41, 56.64) * mm, "end": v(-62.05, 56.16) * mm});
            skLineSegment(sketch, "E1089", {"start": v(-60.03, 54) * mm, "end": v(-59.66, 53.08) * mm});
            skLineSegment(sketch, "E1090", {"start": v(-60.46, 54.76) * mm, "end": v(-60.03, 54) * mm});
            skLineSegment(sketch, "E1091", {"start": v(-60.97, 55.4) * mm, "end": v(-60.46, 54.76) * mm});
            skLineSegment(sketch, "E1092", {"start": v(-61.1, 55.53) * mm, "end": v(-60.97, 55.4) * mm});
            skLineSegment(sketch, "E1093", {"start": v(-61.2, 55.63) * mm, "end": v(-61.1, 55.53) * mm});
            skLineSegment(sketch, "E1094", {"start": v(-61.3, 55.7) * mm, "end": v(-61.2, 55.63) * mm});
            skLineSegment(sketch, "E1095", {"start": v(-61.55, 55.85) * mm, "end": v(-61.3, 55.7) * mm});
            skLineSegment(sketch, "E1096", {"start": v(-62.05, 56.16) * mm, "end": v(-61.55, 55.85) * mm});
            skArc(sketch, "E1097", {"start": v(-60.46, 52.07) * mm, "mid": v(-60.05, 52.57) * mm, "end": v(-59.66, 53.08) * mm});
            skLineSegment(sketch, "E1098", {"start": v(-61.43, 52.23) * mm, "end": v(-60.46, 52.07) * mm});
            skLineSegment(sketch, "E1099", {"start": v(-62.28, 52.48) * mm, "end": v(-61.43, 52.23) * mm});
            skLineSegment(sketch, "E1100", {"start": v(-63.02, 52.84) * mm, "end": v(-62.28, 52.48) * mm});
            skLineSegment(sketch, "E1101", {"start": v(-63.17, 52.93) * mm, "end": v(-63.02, 52.84) * mm});
            skLineSegment(sketch, "E1102", {"start": v(-63.29, 53.01) * mm, "end": v(-63.17, 52.93) * mm});
            skLineSegment(sketch, "E1103", {"start": v(-63.37, 53.08) * mm, "end": v(-63.29, 53.01) * mm});
            skLineSegment(sketch, "E1104", {"start": v(-63.59, 53.3) * mm, "end": v(-63.37, 53.08) * mm});
            skLineSegment(sketch, "E1105", {"start": v(-64, 53.72) * mm, "end": v(-63.59, 53.3) * mm});
            skArc(sketch, "E1106", {"start": v(-64, 53.72) * mm, "mid": v(-64.55, 53.97) * mm, "end": v(-65.12, 53.77) * mm});
            skArc(sketch, "E1107", {"start": v(-65.66, 53.34) * mm, "mid": v(-65.39, 53.55) * mm, "end": v(-65.12, 53.77) * mm});
            skArc(sketch, "E1108", {"start": v(-65.66, 53.34) * mm, "mid": v(-65.98, 52.82) * mm, "end": v(-65.86, 52.23) * mm});
            skLineSegment(sketch, "E1109", {"start": v(-64.98, 49.4) * mm, "end": v(-65.04, 48.42) * mm});
            skLineSegment(sketch, "E1110", {"start": v(-65.04, 50.28) * mm, "end": v(-64.98, 49.4) * mm});
            skLineSegment(sketch, "E1111", {"start": v(-65.22, 51.09) * mm, "end": v(-65.04, 50.28) * mm});
            skLineSegment(sketch, "E1112", {"start": v(-65.27, 51.25) * mm, "end": v(-65.22, 51.09) * mm});
            skLineSegment(sketch, "E1113", {"start": v(-65.33, 51.39) * mm, "end": v(-65.27, 51.25) * mm});
            skLineSegment(sketch, "E1114", {"start": v(-65.38, 51.48) * mm, "end": v(-65.33, 51.39) * mm});
            skLineSegment(sketch, "E1115", {"start": v(-65.54, 51.74) * mm, "end": v(-65.38, 51.48) * mm});
            skLineSegment(sketch, "E1116", {"start": v(-65.86, 52.23) * mm, "end": v(-65.54, 51.74) * mm});
            skArc(sketch, "E1117", {"start": v(-66.2, 47.86) * mm, "mid": v(-65.62, 48.13) * mm, "end": v(-65.04, 48.42) * mm});
            skLineSegment(sketch, "E1118", {"start": v(-67, 48.43) * mm, "end": v(-66.2, 47.86) * mm});
            skLineSegment(sketch, "E1119", {"start": v(-67.66, 49.02) * mm, "end": v(-67, 48.43) * mm});
            skLineSegment(sketch, "E1120", {"start": v(-68.18, 49.66) * mm, "end": v(-67.66, 49.02) * mm});
            skLineSegment(sketch, "E1121", {"start": v(-87.56, 64.81) * mm, "end": v(-88.29, 65.47) * mm});
            skLineSegment(sketch, "E1122", {"start": v(-86.83, 64.3) * mm, "end": v(-87.56, 64.81) * mm});
            skLineSegment(sketch, "E1123", {"start": v(-86.1, 63.94) * mm, "end": v(-86.83, 64.3) * mm});
            skLineSegment(sketch, "E1124", {"start": v(-85.93, 63.89) * mm, "end": v(-86.1, 63.94) * mm});
            skLineSegment(sketch, "E1125", {"start": v(-85.79, 63.85) * mm, "end": v(-85.93, 63.89) * mm});
            skLineSegment(sketch, "E1126", {"start": v(-85.68, 63.83) * mm, "end": v(-85.79, 63.85) * mm});
            skLineSegment(sketch, "E1127", {"start": v(-85.38, 63.8) * mm, "end": v(-85.68, 63.83) * mm});
            skLineSegment(sketch, "E1128", {"start": v(-84.8, 63.74) * mm, "end": v(-85.38, 63.8) * mm});
            skArc(sketch, "E1129", {"start": v(-88, 66.73) * mm, "mid": v(-88.16, 66.1) * mm, "end": v(-88.29, 65.47) * mm});
            skLineSegment(sketch, "E1130", {"start": v(-87.06, 67) * mm, "end": v(-88, 66.73) * mm});
            skLineSegment(sketch, "E1131", {"start": v(-86.19, 67.15) * mm, "end": v(-87.06, 67) * mm});
            skLineSegment(sketch, "E1132", {"start": v(-85.36, 67.15) * mm, "end": v(-86.19, 67.15) * mm});
            skLineSegment(sketch, "E1133", {"start": v(-85.2, 67.13) * mm, "end": v(-85.36, 67.15) * mm});
            skLineSegment(sketch, "E1134", {"start": v(-85.04, 67.1) * mm, "end": v(-85.2, 67.13) * mm});
            skLineSegment(sketch, "E1135", {"start": v(-84.94, 67.08) * mm, "end": v(-85.04, 67.1) * mm});
            skLineSegment(sketch, "E1136", {"start": v(-84.66, 66.98) * mm, "end": v(-84.94, 67.08) * mm});
            skLineSegment(sketch, "E1137", {"start": v(-84.1, 66.78) * mm, "end": v(-84.66, 66.98) * mm});
            skArc(sketch, "E1138", {"start": v(-84.1, 66.78) * mm, "mid": v(-83.5, 66.8) * mm, "end": v(-83.07, 67.22) * mm});
            skArc(sketch, "E1139", {"start": v(-82.76, 67.84) * mm, "mid": v(-82.92, 67.53) * mm, "end": v(-83.07, 67.22) * mm});
            skArc(sketch, "E1140", {"start": v(-82.76, 67.84) * mm, "mid": v(-82.7, 68.45) * mm, "end": v(-83.07, 68.93) * mm});
            skLineSegment(sketch, "E1141", {"start": v(-85.09, 71.1) * mm, "end": v(-85.46, 72) * mm});
            skLineSegment(sketch, "E1142", {"start": v(-84.65, 70.33) * mm, "end": v(-85.09, 71.1) * mm});
            skLineSegment(sketch, "E1143", {"start": v(-84.14, 69.68) * mm, "end": v(-84.65, 70.33) * mm});
            skLineSegment(sketch, "E1144", {"start": v(-84.02, 69.56) * mm, "end": v(-84.14, 69.68) * mm});
            skLineSegment(sketch, "E1145", {"start": v(-83.91, 69.46) * mm, "end": v(-84.02, 69.56) * mm});
            skLineSegment(sketch, "E1146", {"start": v(-83.83, 69.4) * mm, "end": v(-83.91, 69.46) * mm});
            skLineSegment(sketch, "E1147", {"start": v(-83.57, 69.23) * mm, "end": v(-83.83, 69.4) * mm});
            skLineSegment(sketch, "E1148", {"start": v(-83.07, 68.93) * mm, "end": v(-83.57, 69.23) * mm});
            skArc(sketch, "E1149", {"start": v(-84.66, 73.02) * mm, "mid": v(-85.07, 72.52) * mm, "end": v(-85.46, 72) * mm});
            skLineSegment(sketch, "E1150", {"start": v(-83.68, 72.85) * mm, "end": v(-84.66, 73.02) * mm});
            skLineSegment(sketch, "E1151", {"start": v(-82.84, 72.6) * mm, "end": v(-83.68, 72.85) * mm});
            skLineSegment(sketch, "E1152", {"start": v(-82.1, 72.25) * mm, "end": v(-82.84, 72.6) * mm});
            skLineSegment(sketch, "E1153", {"start": v(-81.95, 72.16) * mm, "end": v(-82.1, 72.25) * mm});
            skLineSegment(sketch, "E1154", {"start": v(-81.83, 72.07) * mm, "end": v(-81.95, 72.16) * mm});
            skLineSegment(sketch, "E1155", {"start": v(-81.74, 72) * mm, "end": v(-81.83, 72.07) * mm});
            skLineSegment(sketch, "E1156", {"start": v(-81.53, 71.8) * mm, "end": v(-81.74, 72) * mm});
            skLineSegment(sketch, "E1157", {"start": v(-81.12, 71.37) * mm, "end": v(-81.53, 71.8) * mm});
            skArc(sketch, "E1158", {"start": v(-81.12, 71.37) * mm, "mid": v(-80.57, 71.12) * mm, "end": v(-80, 71.31) * mm});
            skArc(sketch, "E1159", {"start": v(-79.45, 71.75) * mm, "mid": v(-79.73, 71.53) * mm, "end": v(-80, 71.31) * mm});
            skArc(sketch, "E1160", {"start": v(-79.45, 71.75) * mm, "mid": v(-79.14, 72.26) * mm, "end": v(-79.26, 72.86) * mm});
            skLineSegment(sketch, "E1161", {"start": v(-80.13, 75.68) * mm, "end": v(-80.08, 76.67) * mm});
            skLineSegment(sketch, "E1162", {"start": v(-80.08, 74.8) * mm, "end": v(-80.13, 75.68) * mm});
            skLineSegment(sketch, "E1163", {"start": v(-79.9, 74) * mm, "end": v(-80.08, 74.8) * mm});
            skLineSegment(sketch, "E1164", {"start": v(-79.84, 73.84) * mm, "end": v(-79.9, 74) * mm});
            skLineSegment(sketch, "E1165", {"start": v(-79.79, 73.7) * mm, "end": v(-79.84, 73.84) * mm});
            skLineSegment(sketch, "E1166", {"start": v(-79.74, 73.6) * mm, "end": v(-79.79, 73.7) * mm});
            skLineSegment(sketch, "E1167", {"start": v(-79.58, 73.35) * mm, "end": v(-79.74, 73.6) * mm});
            skLineSegment(sketch, "E1168", {"start": v(-79.26, 72.86) * mm, "end": v(-79.58, 73.35) * mm});
            skArc(sketch, "E1169", {"start": v(-78.91, 77.23) * mm, "mid": v(-79.5, 76.96) * mm, "end": v(-80.08, 76.67) * mm});
            skLineSegment(sketch, "E1170", {"start": v(-78.1, 76.66) * mm, "end": v(-78.91, 77.23) * mm});
            skLineSegment(sketch, "E1171", {"start": v(-77.46, 76.07) * mm, "end": v(-78.1, 76.66) * mm});
            skLineSegment(sketch, "E1172", {"start": v(-76.94, 75.43) * mm, "end": v(-77.46, 76.07) * mm});
            skLineSegment(sketch, "E1173", {"start": v(-76.85, 75.28) * mm, "end": v(-76.94, 75.43) * mm});
            skLineSegment(sketch, "E1174", {"start": v(-76.77, 75.15) * mm, "end": v(-76.85, 75.28) * mm});
            skLineSegment(sketch, "E1175", {"start": v(-76.73, 75.05) * mm, "end": v(-76.77, 75.15) * mm});
            skLineSegment(sketch, "E1176", {"start": v(-76.63, 74.77) * mm, "end": v(-76.73, 75.05) * mm});
            skLineSegment(sketch, "E1177", {"start": v(-76.44, 74.2) * mm, "end": v(-76.63, 74.77) * mm});
            skArc(sketch, "E1178", {"start": v(-76.44, 74.2) * mm, "mid": v(-76.06, 73.75) * mm, "end": v(-75.46, 73.67) * mm});
            skArc(sketch, "E1179", {"start": v(-74.78, 73.83) * mm, "mid": v(-75.12, 73.75) * mm, "end": v(-75.46, 73.67) * mm});
            skArc(sketch, "E1180", {"start": v(-74.78, 73.83) * mm, "mid": v(-74.27, 74.15) * mm, "end": v(-74.12, 74.74) * mm});
            skLineSegment(sketch, "E1181", {"start": v(-73.68, 77.67) * mm, "end": v(-73.2, 78.53) * mm});
            skLineSegment(sketch, "E1182", {"start": v(-74.01, 76.85) * mm, "end": v(-73.68, 77.67) * mm});
            skLineSegment(sketch, "E1183", {"start": v(-74.2, 76.05) * mm, "end": v(-74.01, 76.85) * mm});
            skLineSegment(sketch, "E1184", {"start": v(-74.22, 75.88) * mm, "end": v(-74.2, 76.05) * mm});
            skLineSegment(sketch, "E1185", {"start": v(-74.23, 75.73) * mm, "end": v(-74.22, 75.88) * mm});
            skLineSegment(sketch, "E1186", {"start": v(-74.23, 75.62) * mm, "end": v(-74.23, 75.73) * mm});
            skLineSegment(sketch, "E1187", {"start": v(-74.2, 75.32) * mm, "end": v(-74.23, 75.62) * mm});
            skLineSegment(sketch, "E1188", {"start": v(-74.12, 74.74) * mm, "end": v(-74.2, 75.32) * mm});
            skArc(sketch, "E1189", {"start": v(-71.91, 78.53) * mm, "mid": v(-72.56, 78.54) * mm, "end": v(-73.2, 78.53) * mm});
            skLineSegment(sketch, "E1190", {"start": v(-71.43, 77.67) * mm, "end": v(-71.91, 78.53) * mm});
            skLineSegment(sketch, "E1191", {"start": v(-71.1, 76.85) * mm, "end": v(-71.43, 77.67) * mm});
            skLineSegment(sketch, "E1192", {"start": v(-70.91, 76.05) * mm, "end": v(-71.1, 76.85) * mm});
            skLineSegment(sketch, "E1193", {"start": v(-36.7, 15.65) * mm, "end": v(-36.79, 15.77) * mm});
            skLineSegment(sketch, "E1194", {"start": v(-36.56, 15.47) * mm, "end": v(-36.7, 15.65) * mm});
            skLineSegment(sketch, "E1195", {"start": v(-36.19, 15.03) * mm, "end": v(-36.56, 15.47) * mm});
            skArc(sketch, "E1196", {"start": v(-36.4, 19.44) * mm, "mid": v(-36.96, 19.08) * mm, "end": v(-37.5, 18.7) * mm});
            skLineSegment(sketch, "E1197", {"start": v(-35.5, 18.97) * mm, "end": v(-36.4, 19.44) * mm});
            skLineSegment(sketch, "E1198", {"start": v(-34.77, 18.45) * mm, "end": v(-35.5, 18.97) * mm});
            skLineSegment(sketch, "E1199", {"start": v(-34.56, 18.29) * mm, "end": v(-34.77, 18.45) * mm});
            skLineSegment(sketch, "E1200", {"start": v(-34.38, 18.12) * mm, "end": v(-34.56, 18.29) * mm});
            skLineSegment(sketch, "E1201", {"start": v(-34.22, 17.96) * mm, "end": v(-34.38, 18.12) * mm});
            skLineSegment(sketch, "E1202", {"start": v(-34.08, 17.8) * mm, "end": v(-34.22, 17.96) * mm});
            skLineSegment(sketch, "E1203", {"start": v(-33.96, 17.66) * mm, "end": v(-34.08, 17.8) * mm});
            skLineSegment(sketch, "E1204", {"start": v(-33.88, 17.54) * mm, "end": v(-33.96, 17.66) * mm});
            skLineSegment(sketch, "E1205", {"start": v(-33.77, 17.34) * mm, "end": v(-33.88, 17.54) * mm});
            skLineSegment(sketch, "E1206", {"start": v(-33.5, 16.82) * mm, "end": v(-33.77, 17.34) * mm});
            skArc(sketch, "E1207", {"start": v(-33.5, 16.82) * mm, "mid": v(-33.05, 16.43) * mm, "end": v(-32.45, 16.45) * mm});
            skArc(sketch, "E1208", {"start": v(-31.8, 16.72) * mm, "mid": v(-32.12, 16.59) * mm, "end": v(-32.45, 16.45) * mm});
            skCircle(sketch, "E1209", {"center": v(-24.64, 64.38) * mm, "radius": 20 * mm});
            skArc(sketch, "E1210", {"start": v(-31.8, 16.72) * mm, "mid": v(-31.35, 17.13) * mm, "end": v(-31.31, 17.73) * mm});
            skLineSegment(sketch, "E1211", {"start": v(-31.41, 20.67) * mm, "end": v(-31.12, 21.63) * mm});
            skLineSegment(sketch, "E1212", {"start": v(-31.57, 19.78) * mm, "end": v(-31.41, 20.67) * mm});
            skLineSegment(sketch, "E1213", {"start": v(-31.6, 19.52) * mm, "end": v(-31.57, 19.78) * mm});
            skLineSegment(sketch, "E1214", {"start": v(-31.6, 19.27) * mm, "end": v(-31.6, 19.52) * mm});
            skLineSegment(sketch, "E1215", {"start": v(-31.6, 19.04) * mm, "end": v(-31.6, 19.27) * mm});
            skLineSegment(sketch, "E1216", {"start": v(-31.6, 18.83) * mm, "end": v(-31.6, 19.04) * mm});
            skLineSegment(sketch, "E1217", {"start": v(-31.58, 18.65) * mm, "end": v(-31.6, 18.83) * mm});
            skLineSegment(sketch, "E1218", {"start": v(-31.55, 18.5) * mm, "end": v(-31.58, 18.65) * mm});
            skLineSegment(sketch, "E1219", {"start": v(-31.49, 18.28) * mm, "end": v(-31.55, 18.5) * mm});
            skLineSegment(sketch, "E1220", {"start": v(-31.31, 17.73) * mm, "end": v(-31.49, 18.28) * mm});
            skArc(sketch, "E1221", {"start": v(-29.81, 21.89) * mm, "mid": v(-30.47, 21.77) * mm, "end": v(-31.12, 21.63) * mm});
            skLineSegment(sketch, "E1222", {"start": v(-29.17, 21.11) * mm, "end": v(-29.81, 21.89) * mm});
            skLineSegment(sketch, "E1223", {"start": v(-28.68, 20.35) * mm, "end": v(-29.17, 21.11) * mm});
            skLineSegment(sketch, "E1224", {"start": v(-28.56, 20.12) * mm, "end": v(-28.68, 20.35) * mm});
            skLineSegment(sketch, "E1225", {"start": v(-28.46, 19.9) * mm, "end": v(-28.56, 20.12) * mm});
            skLineSegment(sketch, "E1226", {"start": v(-28.37, 19.68) * mm, "end": v(-28.46, 19.9) * mm});
            skLineSegment(sketch, "E1227", {"start": v(-28.3, 19.49) * mm, "end": v(-28.37, 19.68) * mm});
            skLineSegment(sketch, "E1228", {"start": v(-28.25, 19.31) * mm, "end": v(-28.3, 19.49) * mm});
            skLineSegment(sketch, "E1229", {"start": v(-28.22, 19.17) * mm, "end": v(-28.25, 19.31) * mm});
            skLineSegment(sketch, "E1230", {"start": v(-28.2, 18.94) * mm, "end": v(-28.22, 19.17) * mm});
            skLineSegment(sketch, "E1231", {"start": v(-28.14, 18.36) * mm, "end": v(-28.2, 18.94) * mm});
            skArc(sketch, "E1232", {"start": v(-28.14, 18.36) * mm, "mid": v(-27.87, 17.82) * mm, "end": v(-27.3, 17.61) * mm});
            skArc(sketch, "E1233", {"start": v(-26.6, 17.61) * mm, "mid": v(-26.96, 17.62) * mm, "end": v(-27.3, 17.61) * mm});
            skArc(sketch, "E1234", {"start": v(-26.6, 17.61) * mm, "mid": v(-26.04, 17.82) * mm, "end": v(-25.77, 18.36) * mm});
            skLineSegment(sketch, "E1235", {"start": v(-24.74, 21.11) * mm, "end": v(-24.1, 21.89) * mm});
            skLineSegment(sketch, "E1236", {"start": v(-25.23, 20.35) * mm, "end": v(-24.74, 21.11) * mm});
            skLineSegment(sketch, "E1237", {"start": v(-25.35, 20.12) * mm, "end": v(-25.23, 20.35) * mm});
            skLineSegment(sketch, "E1238", {"start": v(-25.45, 19.9) * mm, "end": v(-25.35, 20.12) * mm});
            skLineSegment(sketch, "E1239", {"start": v(-25.54, 19.68) * mm, "end": v(-25.45, 19.9) * mm});
            skLineSegment(sketch, "E1240", {"start": v(-25.61, 19.49) * mm, "end": v(-25.54, 19.68) * mm});
            skLineSegment(sketch, "E1241", {"start": v(-25.66, 19.31) * mm, "end": v(-25.61, 19.49) * mm});
            skLineSegment(sketch, "E1242", {"start": v(-25.7, 19.17) * mm, "end": v(-25.66, 19.31) * mm});
            skLineSegment(sketch, "E1243", {"start": v(-25.72, 18.94) * mm, "end": v(-25.7, 19.17) * mm});
            skLineSegment(sketch, "E1244", {"start": v(-25.77, 18.36) * mm, "end": v(-25.72, 18.94) * mm});
            skArc(sketch, "E1245", {"start": v(-22.8, 21.63) * mm, "mid": v(-23.44, 21.77) * mm, "end": v(-24.1, 21.89) * mm});
            skLineSegment(sketch, "E1246", {"start": v(-22.5, 20.67) * mm, "end": v(-22.8, 21.63) * mm});
            skLineSegment(sketch, "E1247", {"start": v(-22.34, 19.78) * mm, "end": v(-22.5, 20.67) * mm});
            skLineSegment(sketch, "E1248", {"start": v(-22.32, 19.52) * mm, "end": v(-22.34, 19.78) * mm});
            skLineSegment(sketch, "E1249", {"start": v(-22.3, 19.27) * mm, "end": v(-22.32, 19.52) * mm});
            skLineSegment(sketch, "E1250", {"start": v(-22.3, 19.04) * mm, "end": v(-22.3, 19.27) * mm});
            skLineSegment(sketch, "E1251", {"start": v(-22.32, 18.83) * mm, "end": v(-22.3, 19.04) * mm});
            skLineSegment(sketch, "E1252", {"start": v(-22.34, 18.65) * mm, "end": v(-22.32, 18.83) * mm});
            skLineSegment(sketch, "E1253", {"start": v(-22.36, 18.5) * mm, "end": v(-22.34, 18.65) * mm});
            skArc(sketch, "E1254", {"start": v(-84.05, 62.9) * mm, "mid": v(-84.26, 63.46) * mm, "end": v(-84.8, 63.74) * mm});
            skLineSegment(sketch, "E1255", {"start": v(-10.4, -0.34) * mm, "end": v(-9.44, -0.04) * mm});
            skArc(sketch, "E1256", {"start": v(-84.05, 62.9) * mm, "mid": v(-84.06, 62.54) * mm, "end": v(-84.05, 62.2) * mm});
            skArc(sketch, "E1257", {"start": v(-9.44, -0.04) * mm, "mid": v(-9.3, 0.6) * mm, "end": v(-9.18, 1.26) * mm});
            skArc(sketch, "E1258", {"start": v(-84.8, 61.35) * mm, "mid": v(-84.26, 61.63) * mm, "end": v(-84.05, 62.2) * mm});
            skLineSegment(sketch, "E1259", {"start": v(-12.71, 2.93) * mm, "end": v(-12.13, 2.88) * mm});
            skLineSegment(sketch, "E1260", {"start": v(-84.8, 61.35) * mm, "end": v(-85.38, 61.3) * mm});
            skLineSegment(sketch, "E1261", {"start": v(-12.13, 2.88) * mm, "end": v(-11.9, 2.86) * mm});
            skLineSegment(sketch, "E1262", {"start": v(-85.38, 61.3) * mm, "end": v(-85.68, 61.26) * mm});
            skLineSegment(sketch, "E1263", {"start": v(-11.9, 2.86) * mm, "end": v(-11.76, 2.82) * mm});
            skLineSegment(sketch, "E1264", {"start": v(-85.68, 61.26) * mm, "end": v(-85.79, 61.24) * mm});
            skLineSegment(sketch, "E1265", {"start": v(-11.76, 2.82) * mm, "end": v(-11.59, 2.77) * mm});
            skLineSegment(sketch, "E1266", {"start": v(-85.79, 61.24) * mm, "end": v(-85.93, 61.2) * mm});
            skLineSegment(sketch, "E1267", {"start": v(-11.59, 2.77) * mm, "end": v(-11.39, 2.7) * mm});
            skLineSegment(sketch, "E1268", {"start": v(-85.93, 61.2) * mm, "end": v(-86.1, 61.14) * mm});
            skLineSegment(sketch, "E1269", {"start": v(-11.39, 2.7) * mm, "end": v(-11.18, 2.62) * mm});
            skLineSegment(sketch, "E1270", {"start": v(-11.18, 2.62) * mm, "end": v(-10.95, 2.51) * mm});
            skLineSegment(sketch, "E1271", {"start": v(-86.83, 60.78) * mm, "end": v(-87.56, 60.27) * mm});
            skLineSegment(sketch, "E1272", {"start": v(-10.95, 2.51) * mm, "end": v(-10.72, 2.39) * mm});
            skLineSegment(sketch, "E1273", {"start": v(-87.56, 60.27) * mm, "end": v(-88.29, 59.61) * mm});
            skLineSegment(sketch, "E1274", {"start": v(-10.72, 2.39) * mm, "end": v(-9.96, 1.9) * mm});
            skArc(sketch, "E1275", {"start": v(-88.29, 59.61) * mm, "mid": v(-88.16, 58.98) * mm, "end": v(-88, 58.36) * mm});
            skLineSegment(sketch, "E1276", {"start": v(-9.96, 1.9) * mm, "end": v(-9.18, 1.26) * mm});
            skLineSegment(sketch, "E1277", {"start": v(-84.1, 58.3) * mm, "end": v(-84.66, 58.1) * mm});
            skArc(sketch, "E1278", {"start": v(-13.46, 3.76) * mm, "mid": v(-13.25, 3.2) * mm, "end": v(-12.71, 2.93) * mm});
            skLineSegment(sketch, "E1279", {"start": v(-84.66, 58.1) * mm, "end": v(-84.94, 58) * mm});
            skArc(sketch, "E1280", {"start": v(-13.46, 3.76) * mm, "mid": v(-13.46, 4.12) * mm, "end": v(-13.46, 4.47) * mm});
            skLineSegment(sketch, "E1281", {"start": v(-84.94, 58) * mm, "end": v(-85.04, 57.98) * mm});
            skArc(sketch, "E1282", {"start": v(-12.71, 5.3) * mm, "mid": v(-13.25, 5.04) * mm, "end": v(-13.46, 4.47) * mm});
            skLineSegment(sketch, "E1283", {"start": v(-85.04, 57.98) * mm, "end": v(-85.2, 57.95) * mm});
            skLineSegment(sketch, "E1284", {"start": v(-12.71, 5.3) * mm, "end": v(-12.13, 5.35) * mm});
            skLineSegment(sketch, "E1285", {"start": v(-85.2, 57.95) * mm, "end": v(-85.36, 57.93) * mm});
            skLineSegment(sketch, "E1286", {"start": v(-12.13, 5.35) * mm, "end": v(-11.9, 5.38) * mm});
            skLineSegment(sketch, "E1287", {"start": v(-85.36, 57.93) * mm, "end": v(-86.19, 57.94) * mm});
            skLineSegment(sketch, "E1288", {"start": v(-11.9, 5.38) * mm, "end": v(-11.76, 5.4) * mm});
            skLineSegment(sketch, "E1289", {"start": v(-86.19, 57.94) * mm, "end": v(-87.06, 58.08) * mm});
            skLineSegment(sketch, "E1290", {"start": v(-11.76, 5.4) * mm, "end": v(-11.59, 5.46) * mm});
            skLineSegment(sketch, "E1291", {"start": v(-87.06, 58.08) * mm, "end": v(-88, 58.36) * mm});
            skLineSegment(sketch, "E1292", {"start": v(-11.59, 5.46) * mm, "end": v(-11.39, 5.53) * mm});
            skArc(sketch, "E1293", {"start": v(-83.07, 57.87) * mm, "mid": v(-83.5, 58.3) * mm, "end": v(-84.1, 58.3) * mm});
            skLineSegment(sketch, "E1294", {"start": v(-11.39, 5.53) * mm, "end": v(-11.18, 5.62) * mm});
            skArc(sketch, "E1295", {"start": v(-83.07, 57.87) * mm, "mid": v(-82.92, 57.55) * mm, "end": v(-82.76, 57.24) * mm});
            skLineSegment(sketch, "E1296", {"start": v(-11.18, 5.62) * mm, "end": v(-10.95, 5.72) * mm});
            skArc(sketch, "E1297", {"start": v(-83.07, 56.16) * mm, "mid": v(-82.7, 56.64) * mm, "end": v(-82.76, 57.24) * mm});
            skLineSegment(sketch, "E1298", {"start": v(-10.95, 5.72) * mm, "end": v(-10.72, 5.85) * mm});
            skLineSegment(sketch, "E1299", {"start": v(-83.07, 56.16) * mm, "end": v(-83.57, 55.85) * mm});
            skLineSegment(sketch, "E1300", {"start": v(-10.72, 5.85) * mm, "end": v(-9.96, 6.33) * mm});
            skLineSegment(sketch, "E1301", {"start": v(-83.57, 55.85) * mm, "end": v(-83.83, 55.7) * mm});
            skLineSegment(sketch, "E1302", {"start": v(-9.96, 6.33) * mm, "end": v(-9.18, 6.97) * mm});
            skLineSegment(sketch, "E1303", {"start": v(-83.83, 55.7) * mm, "end": v(-83.91, 55.63) * mm});
            skArc(sketch, "E1304", {"start": v(-9.18, 6.97) * mm, "mid": v(-9.3, 7.63) * mm, "end": v(-9.44, 8.28) * mm});
            skLineSegment(sketch, "E1305", {"start": v(-83.91, 55.63) * mm, "end": v(-84.02, 55.53) * mm});
            skLineSegment(sketch, "E1306", {"start": v(-13.34, 8.47) * mm, "end": v(-12.79, 8.65) * mm});
            skLineSegment(sketch, "E1307", {"start": v(-84.02, 55.53) * mm, "end": v(-84.14, 55.4) * mm});
            skLineSegment(sketch, "E1308", {"start": v(-12.79, 8.65) * mm, "end": v(-12.57, 8.71) * mm});
            skLineSegment(sketch, "E1309", {"start": v(-84.14, 55.4) * mm, "end": v(-84.65, 54.76) * mm});
            skLineSegment(sketch, "E1310", {"start": v(-12.57, 8.71) * mm, "end": v(-12.42, 8.74) * mm});
            skLineSegment(sketch, "E1311", {"start": v(-84.65, 54.76) * mm, "end": v(-85.09, 54) * mm});
            skLineSegment(sketch, "E1312", {"start": v(-12.42, 8.74) * mm, "end": v(-12.24, 8.76) * mm});
            skLineSegment(sketch, "E1313", {"start": v(-85.09, 54) * mm, "end": v(-85.46, 53.08) * mm});
            skLineSegment(sketch, "E1314", {"start": v(-12.24, 8.76) * mm, "end": v(-12.03, 8.77) * mm});
            skArc(sketch, "E1315", {"start": v(-85.46, 53.08) * mm, "mid": v(-85.07, 52.57) * mm, "end": v(-84.66, 52.07) * mm});
            skLineSegment(sketch, "E1316", {"start": v(-12.03, 8.77) * mm, "end": v(-11.8, 8.77) * mm});
            skLineSegment(sketch, "E1317", {"start": v(-81.12, 53.72) * mm, "end": v(-81.53, 53.3) * mm});
            skLineSegment(sketch, "E1318", {"start": v(-11.8, 8.77) * mm, "end": v(-11.56, 8.76) * mm});
            skLineSegment(sketch, "E1319", {"start": v(-81.53, 53.3) * mm, "end": v(-81.74, 53.08) * mm});
            skLineSegment(sketch, "E1320", {"start": v(-11.56, 8.76) * mm, "end": v(-11.3, 8.73) * mm});
            skLineSegment(sketch, "E1321", {"start": v(-81.74, 53.08) * mm, "end": v(-81.83, 53.01) * mm});
            skLineSegment(sketch, "E1322", {"start": v(-11.3, 8.73) * mm, "end": v(-10.4, 8.57) * mm});
            skLineSegment(sketch, "E1323", {"start": v(-81.83, 53.01) * mm, "end": v(-81.95, 52.93) * mm});
            skLineSegment(sketch, "E1324", {"start": v(-10.4, 8.57) * mm, "end": v(-9.44, 8.28) * mm});
            skLineSegment(sketch, "E1325", {"start": v(-81.95, 52.93) * mm, "end": v(-82.1, 52.84) * mm});
            skArc(sketch, "E1326", {"start": v(-14.35, 8.96) * mm, "mid": v(-13.94, 8.51) * mm, "end": v(-13.34, 8.47) * mm});
            skLineSegment(sketch, "E1327", {"start": v(-82.1, 52.84) * mm, "end": v(-82.84, 52.48) * mm});
            skArc(sketch, "E1328", {"start": v(-14.35, 8.96) * mm, "mid": v(-14.48, 9.28) * mm, "end": v(-14.62, 9.6) * mm});
            skLineSegment(sketch, "E1329", {"start": v(-82.84, 52.48) * mm, "end": v(-83.68, 52.23) * mm});
            skArc(sketch, "E1330", {"start": v(-14.25, 10.66) * mm, "mid": v(-14.65, 10.2) * mm, "end": v(-14.62, 9.6) * mm});
            skLineSegment(sketch, "E1331", {"start": v(-83.68, 52.23) * mm, "end": v(-84.66, 52.07) * mm});
            skLineSegment(sketch, "E1332", {"start": v(-14.25, 10.66) * mm, "end": v(-13.73, 10.93) * mm});
            skArc(sketch, "E1333", {"start": v(-80, 53.77) * mm, "mid": v(-80.57, 53.97) * mm, "end": v(-81.12, 53.72) * mm});
            skLineSegment(sketch, "E1334", {"start": v(-13.73, 10.93) * mm, "end": v(-13.53, 11.04) * mm});
            skArc(sketch, "E1335", {"start": v(-80, 53.77) * mm, "mid": v(-79.73, 53.55) * mm, "end": v(-79.45, 53.34) * mm});
            skLineSegment(sketch, "E1336", {"start": v(-13.53, 11.04) * mm, "end": v(-13.41, 11.12) * mm});
            skArc(sketch, "E1337", {"start": v(-79.26, 52.23) * mm, "mid": v(-79.14, 52.82) * mm, "end": v(-79.45, 53.34) * mm});
            skLineSegment(sketch, "E1338", {"start": v(-13.41, 11.12) * mm, "end": v(-13.27, 11.24) * mm});
            skLineSegment(sketch, "E1339", {"start": v(-79.26, 52.23) * mm, "end": v(-79.58, 51.74) * mm});
            skLineSegment(sketch, "E1340", {"start": v(-13.27, 11.24) * mm, "end": v(-13.12, 11.38) * mm});
            skLineSegment(sketch, "E1341", {"start": v(-79.58, 51.74) * mm, "end": v(-79.74, 51.48) * mm});
            skLineSegment(sketch, "E1342", {"start": v(-13.12, 11.38) * mm, "end": v(-12.95, 11.54) * mm});
            skLineSegment(sketch, "E1343", {"start": v(-79.74, 51.48) * mm, "end": v(-79.79, 51.39) * mm});
            skLineSegment(sketch, "E1344", {"start": v(-12.95, 11.54) * mm, "end": v(-12.79, 11.73) * mm});
            skLineSegment(sketch, "E1345", {"start": v(-79.79, 51.39) * mm, "end": v(-79.84, 51.25) * mm});
            skLineSegment(sketch, "E1346", {"start": v(-12.79, 11.73) * mm, "end": v(-12.62, 11.93) * mm});
            skLineSegment(sketch, "E1347", {"start": v(-79.84, 51.25) * mm, "end": v(-79.9, 51.09) * mm});
            skLineSegment(sketch, "E1348", {"start": v(-12.62, 11.93) * mm, "end": v(-12.1, 12.67) * mm});
            skLineSegment(sketch, "E1349", {"start": v(-79.9, 51.09) * mm, "end": v(-80.08, 50.28) * mm});
            skLineSegment(sketch, "E1350", {"start": v(-12.1, 12.67) * mm, "end": v(-11.63, 13.56) * mm});
            skLineSegment(sketch, "E1351", {"start": v(-80.08, 50.28) * mm, "end": v(-80.13, 49.4) * mm});
            skArc(sketch, "E1352", {"start": v(-11.63, 13.56) * mm, "mid": v(-11.99, 14.12) * mm, "end": v(-12.37, 14.66) * mm});
            skLineSegment(sketch, "E1353", {"start": v(-80.13, 49.4) * mm, "end": v(-80.08, 48.42) * mm});
            skLineSegment(sketch, "E1354", {"start": v(-16.05, 13.35) * mm, "end": v(-15.6, 13.72) * mm});
            skArc(sketch, "E1355", {"start": v(-80.08, 48.42) * mm, "mid": v(-79.5, 48.13) * mm, "end": v(-78.91, 47.86) * mm});
            skLineSegment(sketch, "E1356", {"start": v(-15.6, 13.72) * mm, "end": v(-15.42, 13.87) * mm});
            skLineSegment(sketch, "E1357", {"start": v(-76.44, 50.88) * mm, "end": v(-76.63, 50.32) * mm});
            skLineSegment(sketch, "E1358", {"start": v(-15.42, 13.87) * mm, "end": v(-15.3, 13.95) * mm});
            skLineSegment(sketch, "E1359", {"start": v(-76.63, 50.32) * mm, "end": v(-76.73, 50.03) * mm});
            skLineSegment(sketch, "E1360", {"start": v(-15.3, 13.95) * mm, "end": v(-15.14, 14.03) * mm});
            skLineSegment(sketch, "E1361", {"start": v(-76.73, 50.03) * mm, "end": v(-76.77, 49.94) * mm});
            skLineSegment(sketch, "E1362", {"start": v(-15.14, 14.03) * mm, "end": v(-14.95, 14.12) * mm});
            skLineSegment(sketch, "E1363", {"start": v(-76.77, 49.94) * mm, "end": v(-76.85, 49.8) * mm});
            skLineSegment(sketch, "E1364", {"start": v(-14.95, 14.12) * mm, "end": v(-14.74, 14.21) * mm});
            skLineSegment(sketch, "E1365", {"start": v(-76.85, 49.8) * mm, "end": v(-76.94, 49.66) * mm});
            skLineSegment(sketch, "E1366", {"start": v(-14.74, 14.21) * mm, "end": v(-14.5, 14.3) * mm});
            skLineSegment(sketch, "E1367", {"start": v(-76.94, 49.66) * mm, "end": v(-77.46, 49.02) * mm});
            skLineSegment(sketch, "E1368", {"start": v(-14.5, 14.3) * mm, "end": v(-14.25, 14.37) * mm});
            skLineSegment(sketch, "E1369", {"start": v(-77.46, 49.02) * mm, "end": v(-78.1, 48.43) * mm});
            skLineSegment(sketch, "E1370", {"start": v(-14.25, 14.37) * mm, "end": v(-13.37, 14.57) * mm});
            skLineSegment(sketch, "E1371", {"start": v(-78.1, 48.43) * mm, "end": v(-78.91, 47.86) * mm});
            skLineSegment(sketch, "E1372", {"start": v(-13.37, 14.57) * mm, "end": v(-12.37, 14.66) * mm});
            skArc(sketch, "E1373", {"start": v(-75.46, 51.41) * mm, "mid": v(-76.06, 51.34) * mm, "end": v(-76.44, 50.88) * mm});
            skArc(sketch, "E1374", {"start": v(-17.16, 13.4) * mm, "mid": v(-16.62, 13.16) * mm, "end": v(-16.05, 13.35) * mm});
            skArc(sketch, "E1375", {"start": v(-75.46, 51.41) * mm, "mid": v(-75.12, 51.33) * mm, "end": v(-74.78, 51.26) * mm});
            skArc(sketch, "E1376", {"start": v(-17.16, 13.4) * mm, "mid": v(-17.41, 13.66) * mm, "end": v(-17.66, 13.9) * mm});
            skArc(sketch, "E1377", {"start": v(-74.12, 50.35) * mm, "mid": v(-74.27, 50.93) * mm, "end": v(-74.78, 51.26) * mm});
            skArc(sketch, "E1378", {"start": v(-17.72, 15.03) * mm, "mid": v(-17.92, 14.46) * mm, "end": v(-17.66, 13.9) * mm});
            skLineSegment(sketch, "E1379", {"start": v(-74.12, 50.35) * mm, "end": v(-74.2, 49.76) * mm});
            skLineSegment(sketch, "E1380", {"start": v(-17.72, 15.03) * mm, "end": v(-17.35, 15.47) * mm});
            skLineSegment(sketch, "E1381", {"start": v(-74.2, 49.76) * mm, "end": v(-74.23, 49.46) * mm});
            skLineSegment(sketch, "E1382", {"start": v(-17.35, 15.47) * mm, "end": v(-17.2, 15.65) * mm});
            skLineSegment(sketch, "E1383", {"start": v(-74.23, 49.46) * mm, "end": v(-74.23, 49.36) * mm});
            skLineSegment(sketch, "E1384", {"start": v(-17.2, 15.65) * mm, "end": v(-17.13, 15.77) * mm});
            skLineSegment(sketch, "E1385", {"start": v(-74.23, 49.36) * mm, "end": v(-74.22, 49.2) * mm});
            skLineSegment(sketch, "E1386", {"start": v(-17.13, 15.77) * mm, "end": v(-17.04, 15.93) * mm});
            skLineSegment(sketch, "E1387", {"start": v(-74.22, 49.2) * mm, "end": v(-74.2, 49.04) * mm});
            skLineSegment(sketch, "E1388", {"start": v(-17.04, 15.93) * mm, "end": v(-16.95, 16.12) * mm});
            skLineSegment(sketch, "E1389", {"start": v(-74.2, 49.04) * mm, "end": v(-74.01, 48.23) * mm});
            skLineSegment(sketch, "E1390", {"start": v(-16.95, 16.12) * mm, "end": v(-16.86, 16.34) * mm});
            skLineSegment(sketch, "E1391", {"start": v(-74.01, 48.23) * mm, "end": v(-73.68, 47.42) * mm});
            skLineSegment(sketch, "E1392", {"start": v(-16.86, 16.34) * mm, "end": v(-16.78, 16.57) * mm});
            skLineSegment(sketch, "E1393", {"start": v(-73.68, 47.42) * mm, "end": v(-73.2, 46.56) * mm});
            skLineSegment(sketch, "E1394", {"start": v(-16.78, 16.57) * mm, "end": v(-16.7, 16.82) * mm});
            skArc(sketch, "E1395", {"start": v(-73.2, 46.56) * mm, "mid": v(-72.56, 46.54) * mm, "end": v(-71.91, 46.56) * mm});
            skLineSegment(sketch, "E1396", {"start": v(-16.7, 16.82) * mm, "end": v(-16.5, 17.7) * mm});
            skLineSegment(sketch, "E1397", {"start": v(-71, 50.35) * mm, "end": v(-70.92, 49.76) * mm});
            skLineSegment(sketch, "E1398", {"start": v(-16.5, 17.7) * mm, "end": v(-16.4, 18.7) * mm});
            skLineSegment(sketch, "E1399", {"start": v(-70.92, 49.76) * mm, "end": v(-70.89, 49.46) * mm});
            skArc(sketch, "E1400", {"start": v(-16.4, 18.7) * mm, "mid": v(-16.96, 19.08) * mm, "end": v(-17.52, 19.44) * mm});
            skLineSegment(sketch, "E1401", {"start": v(-70.89, 49.46) * mm, "end": v(-70.89, 49.36) * mm});
            skLineSegment(sketch, "E1402", {"start": v(-20.4, 16.82) * mm, "end": v(-20.14, 17.34) * mm});
            skLineSegment(sketch, "E1403", {"start": v(-70.89, 49.36) * mm, "end": v(-70.9, 49.2) * mm});
            skLineSegment(sketch, "E1404", {"start": v(-20.14, 17.34) * mm, "end": v(-20.03, 17.54) * mm});
            skLineSegment(sketch, "E1405", {"start": v(-70.9, 49.2) * mm, "end": v(-70.91, 49.04) * mm});
            skLineSegment(sketch, "E1406", {"start": v(-20.03, 17.54) * mm, "end": v(-19.95, 17.66) * mm});
            skLineSegment(sketch, "E1407", {"start": v(-70.91, 49.04) * mm, "end": v(-71.1, 48.23) * mm});
            skLineSegment(sketch, "E1408", {"start": v(-19.95, 17.66) * mm, "end": v(-19.83, 17.8) * mm});
            skLineSegment(sketch, "E1409", {"start": v(-71.1, 48.23) * mm, "end": v(-71.43, 47.42) * mm});
            skLineSegment(sketch, "E1410", {"start": v(-19.83, 17.8) * mm, "end": v(-19.7, 17.96) * mm});
            skLineSegment(sketch, "E1411", {"start": v(-71.43, 47.42) * mm, "end": v(-71.91, 46.56) * mm});
            skLineSegment(sketch, "E1412", {"start": v(-19.7, 17.96) * mm, "end": v(-19.53, 18.12) * mm});
            skArc(sketch, "E1413", {"start": v(-70.34, 51.26) * mm, "mid": v(-70.85, 50.93) * mm, "end": v(-71, 50.35) * mm});
            skLineSegment(sketch, "E1414", {"start": v(-19.53, 18.12) * mm, "end": v(-19.35, 18.29) * mm});
            skArc(sketch, "E1415", {"start": v(-70.34, 51.26) * mm, "mid": v(-70, 51.33) * mm, "end": v(-69.66, 51.41) * mm});
            skLineSegment(sketch, "E1416", {"start": v(-19.35, 18.29) * mm, "end": v(-19.15, 18.45) * mm});
            skArc(sketch, "E1417", {"start": v(-68.67, 50.88) * mm, "mid": v(-69.06, 51.34) * mm, "end": v(-69.66, 51.41) * mm});
            skLineSegment(sketch, "E1418", {"start": v(-19.15, 18.45) * mm, "end": v(-18.4, 18.97) * mm});
            skLineSegment(sketch, "E1419", {"start": v(-68.67, 50.88) * mm, "end": v(-68.49, 50.32) * mm});
            skLineSegment(sketch, "E1420", {"start": v(-18.4, 18.97) * mm, "end": v(-17.52, 19.44) * mm});
            skLineSegment(sketch, "E1421", {"start": v(-68.49, 50.32) * mm, "end": v(-68.39, 50.03) * mm});
            skArc(sketch, "E1422", {"start": v(-21.47, 16.45) * mm, "mid": v(-20.86, 16.43) * mm, "end": v(-20.4, 16.82) * mm});
            skLineSegment(sketch, "E1423", {"start": v(-68.39, 50.03) * mm, "end": v(-68.34, 49.94) * mm});
            skArc(sketch, "E1424", {"start": v(-21.47, 16.45) * mm, "mid": v(-21.79, 16.59) * mm, "end": v(-22.12, 16.72) * mm});
            skLineSegment(sketch, "E1425", {"start": v(-68.34, 49.94) * mm, "end": v(-68.27, 49.8) * mm});
            skArc(sketch, "E1426", {"start": v(-22.6, 17.73) * mm, "mid": v(-22.56, 17.13) * mm, "end": v(-22.12, 16.72) * mm});
            skLineSegment(sketch, "E1427", {"start": v(-68.27, 49.8) * mm, "end": v(-68.18, 49.66) * mm});
            skLineSegment(sketch, "E1428", {"start": v(-22.6, 17.73) * mm, "end": v(-22.42, 18.28) * mm});
            skLineSegment(sketch, "E1429", {"start": v(-22.42, 18.28) * mm, "end": v(-22.36, 18.5) * mm});
            skLineSegment(sketch, "E1430", {"start": v(-37.05, 16.34) * mm, "end": v(-37.13, 16.57) * mm});
            skLineSegment(sketch, "E1431", {"start": v(-37.13, 16.57) * mm, "end": v(-37.21, 16.82) * mm});
            skLineSegment(sketch, "E1432", {"start": v(-37.21, 16.82) * mm, "end": v(-37.4, 17.7) * mm});
            skLineSegment(sketch, "E1433", {"start": v(-37.4, 17.7) * mm, "end": v(-37.5, 18.7) * mm});
            skArc(sketch, "E1434", {"start": v(-36.25, 13.9) * mm, "mid": v(-36, 14.46) * mm, "end": v(-36.19, 15.03) * mm});
            skArc(sketch, "E1435", {"start": v(-36.25, 13.9) * mm, "mid": v(-36.5, 13.66) * mm, "end": v(-36.75, 13.4) * mm});
            skArc(sketch, "E1436", {"start": v(-37.87, 13.35) * mm, "mid": v(-37.3, 13.16) * mm, "end": v(-36.75, 13.4) * mm});
            skLineSegment(sketch, "E1437", {"start": v(-37.87, 13.35) * mm, "end": v(-38.31, 13.72) * mm});
            skLineSegment(sketch, "E1438", {"start": v(-38.31, 13.72) * mm, "end": v(-38.49, 13.87) * mm});
            skLineSegment(sketch, "E1439", {"start": v(-38.49, 13.87) * mm, "end": v(-38.61, 13.95) * mm});
            skLineSegment(sketch, "E1440", {"start": v(-38.61, 13.95) * mm, "end": v(-38.77, 14.03) * mm});
            skLineSegment(sketch, "E1441", {"start": v(-38.77, 14.03) * mm, "end": v(-38.96, 14.12) * mm});
            skLineSegment(sketch, "E1442", {"start": v(-38.96, 14.12) * mm, "end": v(-39.18, 14.21) * mm});
            skLineSegment(sketch, "E1443", {"start": v(-39.18, 14.21) * mm, "end": v(-39.4, 14.3) * mm});
            skLineSegment(sketch, "E1444", {"start": v(-39.4, 14.3) * mm, "end": v(-39.66, 14.37) * mm});
            skLineSegment(sketch, "E1445", {"start": v(-39.66, 14.37) * mm, "end": v(-40.54, 14.57) * mm});
            skLineSegment(sketch, "E1446", {"start": v(-40.54, 14.57) * mm, "end": v(-41.54, 14.66) * mm});
            skArc(sketch, "E1447", {"start": v(-41.54, 14.66) * mm, "mid": v(-41.92, 14.12) * mm, "end": v(-42.28, 13.56) * mm});
            skLineSegment(sketch, "E1448", {"start": v(-39.66, 10.66) * mm, "end": v(-40.18, 10.93) * mm});
            skLineSegment(sketch, "E1449", {"start": v(-40.18, 10.93) * mm, "end": v(-40.38, 11.04) * mm});
            skLineSegment(sketch, "E1450", {"start": v(-40.38, 11.04) * mm, "end": v(-40.5, 11.12) * mm});
            skLineSegment(sketch, "E1451", {"start": v(-40.5, 11.12) * mm, "end": v(-40.64, 11.24) * mm});
            skLineSegment(sketch, "E1452", {"start": v(-40.64, 11.24) * mm, "end": v(-40.8, 11.38) * mm});
            skLineSegment(sketch, "E1453", {"start": v(-40.8, 11.38) * mm, "end": v(-40.96, 11.54) * mm});
            skLineSegment(sketch, "E1454", {"start": v(-40.96, 11.54) * mm, "end": v(-41.12, 11.73) * mm});
            skLineSegment(sketch, "E1455", {"start": v(-41.12, 11.73) * mm, "end": v(-41.3, 11.93) * mm});
            skLineSegment(sketch, "E1456", {"start": v(-41.3, 11.93) * mm, "end": v(-41.8, 12.67) * mm});
            skLineSegment(sketch, "E1457", {"start": v(-41.8, 12.67) * mm, "end": v(-42.28, 13.56) * mm});
            skArc(sketch, "E1458", {"start": v(-39.29, 9.6) * mm, "mid": v(-39.26, 10.2) * mm, "end": v(-39.66, 10.66) * mm});
            skArc(sketch, "E1459", {"start": v(-39.29, 9.6) * mm, "mid": v(-39.43, 9.28) * mm, "end": v(-39.56, 8.96) * mm});
            skArc(sketch, "E1460", {"start": v(-40.57, 8.47) * mm, "mid": v(-39.97, 8.51) * mm, "end": v(-39.56, 8.96) * mm});
            skLineSegment(sketch, "E1461", {"start": v(-40.57, 8.47) * mm, "end": v(-41.12, 8.65) * mm});
            skLineSegment(sketch, "E1462", {"start": v(-41.12, 8.65) * mm, "end": v(-41.34, 8.71) * mm});
            skLineSegment(sketch, "E1463", {"start": v(-41.34, 8.71) * mm, "end": v(-41.49, 8.74) * mm});
            skLineSegment(sketch, "E1464", {"start": v(-41.49, 8.74) * mm, "end": v(-41.67, 8.76) * mm});
            skLineSegment(sketch, "E1465", {"start": v(-41.67, 8.76) * mm, "end": v(-41.88, 8.77) * mm});
            skLineSegment(sketch, "E1466", {"start": v(-41.88, 8.77) * mm, "end": v(-42.1, 8.77) * mm});
            skLineSegment(sketch, "E1467", {"start": v(-42.1, 8.77) * mm, "end": v(-42.35, 8.76) * mm});
            skLineSegment(sketch, "E1468", {"start": v(-42.35, 8.76) * mm, "end": v(-42.61, 8.73) * mm});
            skLineSegment(sketch, "E1469", {"start": v(-70.88, -82.6) * mm, "end": v(-70.54, -83.46) * mm});
            skLineSegment(sketch, "E1470", {"start": v(-70.54, -83.46) * mm, "end": v(-70.07, -84.37) * mm});
            skArc(sketch, "E1471", {"start": v(-70.07, -84.37) * mm, "mid": v(-69.39, -84.38) * mm, "end": v(-68.7, -84.37) * mm});
            skLineSegment(sketch, "E1472", {"start": v(-67.72, -80.58) * mm, "end": v(-67.67, -81.15) * mm});
            skLineSegment(sketch, "E1473", {"start": v(-67.67, -81.15) * mm, "end": v(-67.66, -81.33) * mm});
            skLineSegment(sketch, "E1474", {"start": v(-67.66, -81.33) * mm, "end": v(-67.67, -81.53) * mm});
            skLineSegment(sketch, "E1475", {"start": v(-67.67, -81.53) * mm, "end": v(-67.7, -81.76) * mm});
            skLineSegment(sketch, "E1476", {"start": v(-67.7, -81.76) * mm, "end": v(-67.75, -82.02) * mm});
            skLineSegment(sketch, "E1477", {"start": v(-67.75, -82.02) * mm, "end": v(-67.81, -82.3) * mm});
            skLineSegment(sketch, "E1478", {"start": v(-67.81, -82.3) * mm, "end": v(-67.9, -82.6) * mm});
            skLineSegment(sketch, "E1479", {"start": v(-67.9, -82.6) * mm, "end": v(-68.23, -83.46) * mm});
            skLineSegment(sketch, "E1480", {"start": v(-68.23, -83.46) * mm, "end": v(-68.7, -84.37) * mm});
            skArc(sketch, "E1481", {"start": v(-67.05, -79.7) * mm, "mid": v(-67.56, -80) * mm, "end": v(-67.72, -80.58) * mm});
            skArc(sketch, "E1482", {"start": v(-67.05, -79.7) * mm, "mid": v(-66.7, -79.65) * mm, "end": v(-66.35, -79.58) * mm});
            skArc(sketch, "E1483", {"start": v(-65.41, -80.18) * mm, "mid": v(-65.76, -79.7) * mm, "end": v(-66.35, -79.58) * mm});
            skLineSegment(sketch, "E1484", {"start": v(-65.41, -80.18) * mm, "end": v(-65.27, -80.73) * mm});
            skLineSegment(sketch, "E1485", {"start": v(-65.27, -80.73) * mm, "end": v(-65.21, -80.9) * mm});
            skLineSegment(sketch, "E1486", {"start": v(-65.21, -80.9) * mm, "end": v(-65.14, -81.08) * mm});
            skLineSegment(sketch, "E1487", {"start": v(-65.14, -81.08) * mm, "end": v(-65.03, -81.3) * mm});
            skLineSegment(sketch, "E1488", {"start": v(-65.03, -81.3) * mm, "end": v(-64.9, -81.52) * mm});
            skLineSegment(sketch, "E1489", {"start": v(-64.9, -81.52) * mm, "end": v(-64.74, -81.76) * mm});
            skLineSegment(sketch, "E1490", {"start": v(-64.74, -81.76) * mm, "end": v(-64.56, -82) * mm});
            skLineSegment(sketch, "E1491", {"start": v(-64.56, -82) * mm, "end": v(-63.95, -82.7) * mm});
            skLineSegment(sketch, "E1492", {"start": v(-63.95, -82.7) * mm, "end": v(-63.2, -83.4) * mm});
            skArc(sketch, "E1493", {"start": v(-63.2, -83.4) * mm, "mid": v(-62.55, -83.18) * mm, "end": v(-61.91, -82.93) * mm});
            skLineSegment(sketch, "E1494", {"start": v(-62.28, -79.04) * mm, "end": v(-62.04, -79.55) * mm});
            skLineSegment(sketch, "E1495", {"start": v(-62.04, -79.55) * mm, "end": v(-61.97, -79.72) * mm});
            skLineSegment(sketch, "E1496", {"start": v(-61.97, -79.72) * mm, "end": v(-61.91, -79.91) * mm});
            skLineSegment(sketch, "E1497", {"start": v(-61.91, -79.91) * mm, "end": v(-61.86, -80.14) * mm});
            skLineSegment(sketch, "E1498", {"start": v(-61.86, -80.14) * mm, "end": v(-61.81, -80.4) * mm});
            skLineSegment(sketch, "E1499", {"start": v(-61.81, -80.4) * mm, "end": v(-61.78, -80.68) * mm});
            skLineSegment(sketch, "E1500", {"start": v(-61.78, -80.68) * mm, "end": v(-61.76, -80.99) * mm});
            skLineSegment(sketch, "E1501", {"start": v(-61.76, -80.99) * mm, "end": v(-61.78, -81.91) * mm});
            skLineSegment(sketch, "E1502", {"start": v(-61.78, -81.91) * mm, "end": v(-61.91, -82.93) * mm});
            skArc(sketch, "E1503", {"start": v(-61.95, -77.98) * mm, "mid": v(-62.33, -78.44) * mm, "end": v(-62.28, -79.04) * mm});
            skArc(sketch, "E1504", {"start": v(-61.95, -77.98) * mm, "mid": v(-61.64, -77.8) * mm, "end": v(-61.33, -77.63) * mm});
            skArc(sketch, "E1505", {"start": v(-60.25, -77.86) * mm, "mid": v(-60.74, -77.53) * mm, "end": v(-61.33, -77.63) * mm});
            skLineSegment(sketch, "E1506", {"start": v(-60.25, -77.86) * mm, "end": v(-59.93, -78.33) * mm});
            skLineSegment(sketch, "E1507", {"start": v(-59.93, -78.33) * mm, "end": v(-59.82, -78.48) * mm});
            skLineSegment(sketch, "E1508", {"start": v(-59.82, -78.48) * mm, "end": v(-59.68, -78.62) * mm});
            skLineSegment(sketch, "E1509", {"start": v(-59.68, -78.62) * mm, "end": v(-59.5, -78.78) * mm});
            skLineSegment(sketch, "E1510", {"start": v(-59.5, -78.78) * mm, "end": v(-59.3, -78.95) * mm});
            skLineSegment(sketch, "E1511", {"start": v(-59.3, -78.95) * mm, "end": v(-59.08, -79.12) * mm});
            skLineSegment(sketch, "E1512", {"start": v(-59.08, -79.12) * mm, "end": v(-58.82, -79.29) * mm});
            skLineSegment(sketch, "E1513", {"start": v(-58.82, -79.29) * mm, "end": v(-58.01, -79.74) * mm});
            skLineSegment(sketch, "E1514", {"start": v(-58.01, -79.74) * mm, "end": v(-57.06, -80.13) * mm});
            skArc(sketch, "E1515", {"start": v(18, 12.91) * mm, "mid": v(17.74, 12.67) * mm, "end": v(17.5, 12.41) * mm});
            skArc(sketch, "E1516", {"start": v(-42.28, -5.32) * mm, "mid": v(-41.92, -5.88) * mm, "end": v(-41.54, -6.43) * mm});
            skLineSegment(sketch, "E1517", {"start": v(80.86, -9.73) * mm, "end": v(81, -9.89) * mm});
            skLineSegment(sketch, "E1518", {"start": v(88.66, 8.6) * mm, "end": v(88.89, 8.6) * mm});
            skLineSegment(sketch, "E1519", {"start": v(25.94, 18.5) * mm, "end": v(25.87, 18.69) * mm});
            skLineSegment(sketch, "E1520", {"start": v(12.9, -1.47) * mm, "end": v(12.76, -1.5) * mm});
            skLineSegment(sketch, "E1521", {"start": v(-25.72, -10.7) * mm, "end": v(-25.7, -10.93) * mm});
            skArc(sketch, "E1522", {"start": v(-78.53, -50.9) * mm, "mid": v(-78.03, -51.24) * mm, "end": v(-77.44, -51.14) * mm});
            skLineSegment(sketch, "E1523", {"start": v(78.37, 19.35) * mm, "end": v(78.35, 19.61) * mm});
            skLineSegment(sketch, "E1524", {"start": v(-51.73, -65.83) * mm, "end": v(-51.47, -65.95) * mm});
            skLineSegment(sketch, "E1525", {"start": v(28.52, -11.7) * mm, "end": v(28.55, -11.93) * mm});
            skLineSegment(sketch, "E1526", {"start": v(42.34, 1.86) * mm, "end": v(42.48, 1.83) * mm});
            skLineSegment(sketch, "E1527", {"start": v(-65.27, -48.04) * mm, "end": v(-65.21, -47.87) * mm});
            skArc(sketch, "E1528", {"start": v(16.38, 12.35) * mm, "mid": v(16.95, 12.16) * mm, "end": v(17.5, 12.41) * mm});
            skLineSegment(sketch, "E1529", {"start": v(-37.87, -5.12) * mm, "end": v(-38.31, -5.5) * mm});
            skLineSegment(sketch, "E1530", {"start": v(81, -9.89) * mm, "end": v(81.16, -10.05) * mm});
            skLineSegment(sketch, "E1531", {"start": v(88.89, 8.6) * mm, "end": v(89.13, 8.6) * mm});
            skLineSegment(sketch, "E1532", {"start": v(25.87, 18.69) * mm, "end": v(25.79, 18.9) * mm});
            skLineSegment(sketch, "E1533", {"start": v(12.76, -1.5) * mm, "end": v(12.57, -1.52) * mm});
            skLineSegment(sketch, "E1534", {"start": v(-25.7, -10.93) * mm, "end": v(-25.66, -11.08) * mm});
            skLineSegment(sketch, "E1535", {"start": v(-78.53, -50.9) * mm, "end": v(-78.85, -50.43) * mm});
            skLineSegment(sketch, "E1536", {"start": v(78.35, 19.61) * mm, "end": v(78.19, 20.5) * mm});
            skLineSegment(sketch, "E1537", {"start": v(-51.47, -65.95) * mm, "end": v(-51.2, -66.08) * mm});
            skLineSegment(sketch, "E1538", {"start": v(28.55, -11.93) * mm, "end": v(28.58, -12.07) * mm});
            skLineSegment(sketch, "E1539", {"start": v(42.48, 1.83) * mm, "end": v(42.66, 1.78) * mm});
            skLineSegment(sketch, "E1540", {"start": v(-65.21, -47.87) * mm, "end": v(-65.14, -47.68) * mm});
            skLineSegment(sketch, "E1541", {"start": v(16.38, 12.35) * mm, "end": v(15.93, 12.73) * mm});
            skLineSegment(sketch, "E1542", {"start": v(-38.31, -5.5) * mm, "end": v(-38.49, -5.63) * mm});
            skLineSegment(sketch, "E1543", {"start": v(81.16, -10.05) * mm, "end": v(81.34, -10.22) * mm});
            skLineSegment(sketch, "E1544", {"start": v(89.13, 8.6) * mm, "end": v(89.4, 8.57) * mm});
            skLineSegment(sketch, "E1545", {"start": v(25.79, 18.9) * mm, "end": v(25.68, 19.12) * mm});
            skLineSegment(sketch, "E1546", {"start": v(12.57, -1.52) * mm, "end": v(12.36, -1.53) * mm});
            skLineSegment(sketch, "E1547", {"start": v(-25.66, -11.08) * mm, "end": v(-25.61, -11.25) * mm});
            skLineSegment(sketch, "E1548", {"start": v(-78.85, -50.43) * mm, "end": v(-78.96, -50.29) * mm});
            skLineSegment(sketch, "E1549", {"start": v(78.19, 20.5) * mm, "end": v(77.9, 21.46) * mm});
            skLineSegment(sketch, "E1550", {"start": v(-51.2, -66.08) * mm, "end": v(-50.4, -66.56) * mm});
            skLineSegment(sketch, "E1551", {"start": v(28.58, -12.07) * mm, "end": v(28.63, -12.25) * mm});
            skLineSegment(sketch, "E1552", {"start": v(42.66, 1.78) * mm, "end": v(42.85, 1.7) * mm});
            skLineSegment(sketch, "E1553", {"start": v(-65.14, -47.68) * mm, "end": v(-65.03, -47.47) * mm});
            skLineSegment(sketch, "E1554", {"start": v(15.93, 12.73) * mm, "end": v(15.76, 12.87) * mm});
            skLineSegment(sketch, "E1555", {"start": v(-38.49, -5.63) * mm, "end": v(-38.61, -5.71) * mm});
            skLineSegment(sketch, "E1556", {"start": v(81.34, -10.22) * mm, "end": v(81.54, -10.38) * mm});
            skLineSegment(sketch, "E1557", {"start": v(89.4, 8.57) * mm, "end": v(90.28, 8.4) * mm});
            skLineSegment(sketch, "E1558", {"start": v(25.68, 19.12) * mm, "end": v(25.56, 19.35) * mm});
            skLineSegment(sketch, "E1559", {"start": v(12.36, -1.53) * mm, "end": v(12.14, -1.53) * mm});
            skLineSegment(sketch, "E1560", {"start": v(-25.61, -11.25) * mm, "end": v(-25.54, -11.45) * mm});
            skLineSegment(sketch, "E1561", {"start": v(-78.96, -50.29) * mm, "end": v(-79.1, -50.14) * mm});
            skArc(sketch, "E1562", {"start": v(77.9, 21.46) * mm, "mid": v(77.25, 21.6) * mm, "end": v(76.6, 21.72) * mm});
            skLineSegment(sketch, "E1563", {"start": v(-50.4, -66.56) * mm, "end": v(-49.58, -67.18) * mm});
            skLineSegment(sketch, "E1564", {"start": v(28.63, -12.25) * mm, "end": v(28.7, -12.45) * mm});
            skLineSegment(sketch, "E1565", {"start": v(42.85, 1.7) * mm, "end": v(43.07, 1.62) * mm});
            skLineSegment(sketch, "E1566", {"start": v(-65.03, -47.47) * mm, "end": v(-64.9, -47.25) * mm});
            skLineSegment(sketch, "E1567", {"start": v(15.76, 12.87) * mm, "end": v(15.63, 12.95) * mm});
            skLineSegment(sketch, "E1568", {"start": v(-38.61, -5.71) * mm, "end": v(-38.77, -5.8) * mm});
            skLineSegment(sketch, "E1569", {"start": v(81.54, -10.38) * mm, "end": v(82.29, -10.9) * mm});
            skLineSegment(sketch, "E1570", {"start": v(90.28, 8.4) * mm, "end": v(91.25, 8.11) * mm});
            skLineSegment(sketch, "E1571", {"start": v(25.56, 19.35) * mm, "end": v(25.07, 20.12) * mm});
            skLineSegment(sketch, "E1572", {"start": v(12.14, -1.53) * mm, "end": v(11.89, -1.52) * mm});
            skLineSegment(sketch, "E1573", {"start": v(-25.54, -11.45) * mm, "end": v(-25.45, -11.66) * mm});
            skLineSegment(sketch, "E1574", {"start": v(-79.1, -50.14) * mm, "end": v(-79.27, -49.98) * mm});
            skLineSegment(sketch, "E1575", {"start": v(74.92, 18.2) * mm, "end": v(74.97, 18.77) * mm});
            skArc(sketch, "E1576", {"start": v(-53.9, -64.74) * mm, "mid": v(-53.68, -65.3) * mm, "end": v(-53.15, -65.56) * mm});
            skLineSegment(sketch, "E1577", {"start": v(28.7, -12.45) * mm, "end": v(28.79, -12.66) * mm});
            skLineSegment(sketch, "E1578", {"start": v(43.07, 1.62) * mm, "end": v(43.29, 1.51) * mm});
            skLineSegment(sketch, "E1579", {"start": v(-64.9, -47.25) * mm, "end": v(-64.74, -47) * mm});
            skLineSegment(sketch, "E1580", {"start": v(15.63, 12.95) * mm, "end": v(15.47, 13.04) * mm});
            skLineSegment(sketch, "E1581", {"start": v(-38.77, -5.8) * mm, "end": v(-38.96, -5.9) * mm});
            skLineSegment(sketch, "E1582", {"start": v(82.29, -10.9) * mm, "end": v(83.18, -11.37) * mm});
            skArc(sketch, "E1583", {"start": v(86.34, 8.79) * mm, "mid": v(86.75, 8.35) * mm, "end": v(87.35, 8.3) * mm});
            skLineSegment(sketch, "E1584", {"start": v(25.07, 20.12) * mm, "end": v(24.43, 20.9) * mm});
            skLineSegment(sketch, "E1585", {"start": v(11.89, -1.52) * mm, "end": v(11.63, -1.5) * mm});
            skLineSegment(sketch, "E1586", {"start": v(-25.45, -11.66) * mm, "end": v(-25.35, -11.88) * mm});
            skLineSegment(sketch, "E1587", {"start": v(-79.27, -49.98) * mm, "end": v(-79.47, -49.82) * mm});
            skLineSegment(sketch, "E1588", {"start": v(74.97, 18.77) * mm, "end": v(75, 19) * mm});
            skArc(sketch, "E1589", {"start": v(-53.9, -64.74) * mm, "mid": v(-53.89, -64.38) * mm, "end": v(-53.9, -64.03) * mm});
            skLineSegment(sketch, "E1590", {"start": v(28.79, -12.66) * mm, "end": v(28.9, -12.88) * mm});
            skLineSegment(sketch, "E1591", {"start": v(43.29, 1.51) * mm, "end": v(43.52, 1.4) * mm});
            skLineSegment(sketch, "E1592", {"start": v(15.47, 13.04) * mm, "end": v(15.28, 13.13) * mm});
            skLineSegment(sketch, "E1593", {"start": v(-38.96, -5.9) * mm, "end": v(-39.18, -5.98) * mm});
            skArc(sketch, "E1594", {"start": v(83.18, -11.37) * mm, "mid": v(83.74, -11.02) * mm, "end": v(84.28, -10.64) * mm});
            skArc(sketch, "E1595", {"start": v(86.34, 8.79) * mm, "mid": v(86.2, 9.12) * mm, "end": v(86.07, 9.44) * mm});
            skArc(sketch, "E1596", {"start": v(24.43, 20.9) * mm, "mid": v(23.78, 20.78) * mm, "end": v(23.13, 20.63) * mm});
            skLineSegment(sketch, "E1597", {"start": v(11.63, -1.5) * mm, "end": v(10.74, -1.33) * mm});
            skLineSegment(sketch, "E1598", {"start": v(-25.35, -11.88) * mm, "end": v(-25.23, -12.12) * mm});
            skLineSegment(sketch, "E1599", {"start": v(-79.47, -49.82) * mm, "end": v(-79.7, -49.65) * mm});
            skLineSegment(sketch, "E1600", {"start": v(75, 19) * mm, "end": v(75.03, 19.14) * mm});
            skArc(sketch, "E1601", {"start": v(-53.15, -63.2) * mm, "mid": v(-53.68, -63.47) * mm, "end": v(-53.9, -64.03) * mm});
            skLineSegment(sketch, "E1602", {"start": v(28.9, -12.88) * mm, "end": v(29.02, -13.11) * mm});
            skLineSegment(sketch, "E1603", {"start": v(43.52, 1.4) * mm, "end": v(44.28, 0.9) * mm});
            skLineSegment(sketch, "E1604", {"start": v(-64.56, -46.76) * mm, "end": v(-63.95, -46.06) * mm});
            skLineSegment(sketch, "E1605", {"start": v(15.28, 13.13) * mm, "end": v(15.07, 13.22) * mm});
            skLineSegment(sketch, "E1606", {"start": v(-39.18, -5.98) * mm, "end": v(-39.4, -6.06) * mm});
            skLineSegment(sketch, "E1607", {"start": v(82.97, -6.96) * mm, "end": v(83.34, -7.4) * mm});
            skArc(sketch, "E1608", {"start": v(86.44, 10.5) * mm, "mid": v(86.04, 10.04) * mm, "end": v(86.07, 9.44) * mm});
            skLineSegment(sketch, "E1609", {"start": v(22.93, 16.73) * mm, "end": v(22.76, 17.29) * mm});
            skLineSegment(sketch, "E1610", {"start": v(10.74, -1.33) * mm, "end": v(9.78, -1.04) * mm});
            skLineSegment(sketch, "E1611", {"start": v(-25.23, -12.12) * mm, "end": v(-24.74, -12.88) * mm});
            skLineSegment(sketch, "E1612", {"start": v(-79.7, -49.65) * mm, "end": v(-79.95, -49.48) * mm});
            skLineSegment(sketch, "E1613", {"start": v(75.03, 19.14) * mm, "end": v(75.08, 19.32) * mm});
            skLineSegment(sketch, "E1614", {"start": v(-53.15, -63.2) * mm, "end": v(-52.58, -63.17) * mm});
            skLineSegment(sketch, "E1615", {"start": v(29.02, -13.11) * mm, "end": v(29.5, -13.87) * mm});
            skLineSegment(sketch, "E1616", {"start": v(44.28, 0.9) * mm, "end": v(45.06, 0.26) * mm});
            skLineSegment(sketch, "E1617", {"start": v(-63.95, -46.06) * mm, "end": v(-63.2, -45.37) * mm});
            skLineSegment(sketch, "E1618", {"start": v(15.07, 13.22) * mm, "end": v(14.84, 13.3) * mm});
            skLineSegment(sketch, "E1619", {"start": v(-39.4, -6.06) * mm, "end": v(-39.66, -6.14) * mm});
            skLineSegment(sketch, "E1620", {"start": v(83.34, -7.4) * mm, "end": v(83.49, -7.58) * mm});
            skLineSegment(sketch, "E1621", {"start": v(86.44, 10.5) * mm, "end": v(86.96, 10.76) * mm});
            skLineSegment(sketch, "E1622", {"start": v(22.76, 17.29) * mm, "end": v(22.7, 17.5) * mm});
            skArc(sketch, "E1623", {"start": v(14.68, -1.72) * mm, "mid": v(14.28, -1.27) * mm, "end": v(13.67, -1.23) * mm});
            skLineSegment(sketch, "E1624", {"start": v(-24.74, -12.88) * mm, "end": v(-24.1, -13.65) * mm});
            skLineSegment(sketch, "E1625", {"start": v(-79.95, -49.48) * mm, "end": v(-80.76, -49.03) * mm});
            skLineSegment(sketch, "E1626", {"start": v(75.08, 19.32) * mm, "end": v(75.15, 19.52) * mm});
            skLineSegment(sketch, "E1627", {"start": v(-52.58, -63.17) * mm, "end": v(-52.4, -63.14) * mm});
            skLineSegment(sketch, "E1628", {"start": v(29.5, -13.87) * mm, "end": v(30.14, -14.65) * mm});
            skArc(sketch, "E1629", {"start": v(40.78, 2.77) * mm, "mid": v(41, 2.2) * mm, "end": v(41.53, 1.94) * mm});
            skArc(sketch, "E1630", {"start": v(-66.35, -49.18) * mm, "mid": v(-65.76, -49.08) * mm, "end": v(-65.41, -48.6) * mm});
            skLineSegment(sketch, "E1631", {"start": v(14.84, 13.3) * mm, "end": v(14.59, 13.38) * mm});
            skLineSegment(sketch, "E1632", {"start": v(-39.66, -6.14) * mm, "end": v(-40.54, -6.33) * mm});
            skLineSegment(sketch, "E1633", {"start": v(83.49, -7.58) * mm, "end": v(83.56, -7.7) * mm});
            skLineSegment(sketch, "E1634", {"start": v(86.96, 10.76) * mm, "end": v(87.16, 10.87) * mm});
            skLineSegment(sketch, "E1635", {"start": v(22.7, 17.5) * mm, "end": v(22.67, 17.65) * mm});
            skArc(sketch, "E1636", {"start": v(14.68, -1.72) * mm, "mid": v(14.82, -2.04) * mm, "end": v(14.95, -2.37) * mm});
            skArc(sketch, "E1637", {"start": v(-24.1, -13.65) * mm, "mid": v(-23.44, -13.54) * mm, "end": v(-22.8, -13.4) * mm});
            skLineSegment(sketch, "E1638", {"start": v(-80.76, -49.03) * mm, "end": v(-81.72, -48.63) * mm});
            skLineSegment(sketch, "E1639", {"start": v(75.15, 19.52) * mm, "end": v(75.24, 19.73) * mm});
            skLineSegment(sketch, "E1640", {"start": v(-52.4, -63.14) * mm, "end": v(-52.2, -63.1) * mm});
            skArc(sketch, "E1641", {"start": v(30.14, -14.65) * mm, "mid": v(30.8, -14.53) * mm, "end": v(31.45, -14.4) * mm});
            skArc(sketch, "E1642", {"start": v(40.78, 2.77) * mm, "mid": v(40.79, 3.12) * mm, "end": v(40.78, 3.47) * mm});
            skArc(sketch, "E1643", {"start": v(-66.35, -49.18) * mm, "mid": v(-66.7, -49.12) * mm, "end": v(-67.05, -49.06) * mm});
            skLineSegment(sketch, "E1644", {"start": v(14.59, 13.38) * mm, "end": v(13.7, 13.57) * mm});
            skLineSegment(sketch, "E1645", {"start": v(-40.54, -6.33) * mm, "end": v(-41.54, -6.43) * mm});
            skLineSegment(sketch, "E1646", {"start": v(83.56, -7.7) * mm, "end": v(83.65, -7.87) * mm});
            skLineSegment(sketch, "E1647", {"start": v(87.16, 10.87) * mm, "end": v(87.28, 10.96) * mm});
            skLineSegment(sketch, "E1648", {"start": v(22.67, 17.65) * mm, "end": v(22.65, 17.84) * mm});
            skArc(sketch, "E1649", {"start": v(14.58, -3.43) * mm, "mid": v(14.98, -2.97) * mm, "end": v(14.95, -2.37) * mm});
            skLineSegment(sketch, "E1650", {"start": v(-22.6, -9.5) * mm, "end": v(-22.42, -10.05) * mm});
            skArc(sketch, "E1651", {"start": v(-81.72, -48.63) * mm, "mid": v(-82.24, -49.06) * mm, "end": v(-82.76, -49.5) * mm});
            skLineSegment(sketch, "E1652", {"start": v(75.24, 19.73) * mm, "end": v(75.34, 19.95) * mm});
            skLineSegment(sketch, "E1653", {"start": v(-52.2, -63.1) * mm, "end": v(-51.98, -63.03) * mm});
            skLineSegment(sketch, "E1654", {"start": v(31.64, -10.5) * mm, "end": v(31.82, -11.05) * mm});
            skArc(sketch, "E1655", {"start": v(41.53, 4.3) * mm, "mid": v(41, 4.04) * mm, "end": v(40.78, 3.47) * mm});
            skArc(sketch, "E1656", {"start": v(-72.56, 63.94) * mm, "mid": v(-73.26, 63.76) * mm, "end": v(-73.77, 63.24) * mm});
            skLineSegment(sketch, "E1657", {"start": v(13.7, 13.57) * mm, "end": v(12.7, 13.67) * mm});
            skArc(sketch, "E1658", {"start": v(-36.75, -5.18) * mm, "mid": v(-37.3, -4.92) * mm, "end": v(-37.87, -5.12) * mm});
            skLineSegment(sketch, "E1659", {"start": v(83.65, -7.87) * mm, "end": v(83.74, -8.06) * mm});
            skLineSegment(sketch, "E1660", {"start": v(87.28, 10.96) * mm, "end": v(87.42, 11.07) * mm});
            skLineSegment(sketch, "E1661", {"start": v(22.65, 17.84) * mm, "end": v(22.64, 18.04) * mm});
            skLineSegment(sketch, "E1662", {"start": v(14.58, -3.43) * mm, "end": v(14.07, -3.7) * mm});
            skLineSegment(sketch, "E1663", {"start": v(-22.42, -10.05) * mm, "end": v(-22.36, -10.27) * mm});
            skLineSegment(sketch, "E1664", {"start": v(-81.08, -53.04) * mm, "end": v(-81.48, -52.64) * mm});
            skLineSegment(sketch, "E1665", {"start": v(75.34, 19.95) * mm, "end": v(75.46, 20.18) * mm});
            skLineSegment(sketch, "E1666", {"start": v(-51.98, -63.03) * mm, "end": v(-51.73, -62.93) * mm});
            skLineSegment(sketch, "E1667", {"start": v(31.82, -11.05) * mm, "end": v(31.88, -11.26) * mm});
            skLineSegment(sketch, "E1668", {"start": v(41.53, 4.3) * mm, "end": v(42.11, 4.36) * mm});
            skArc(sketch, "E1669", {"start": v(12.7, 13.67) * mm, "mid": v(12.32, 13.12) * mm, "end": v(11.96, 12.56) * mm});
            skArc(sketch, "E1670", {"start": v(-36.75, -5.18) * mm, "mid": v(-36.5, -5.43) * mm, "end": v(-36.25, -5.68) * mm});
            skLineSegment(sketch, "E1671", {"start": v(83.74, -8.06) * mm, "end": v(83.83, -8.27) * mm});
            skLineSegment(sketch, "E1672", {"start": v(87.42, 11.07) * mm, "end": v(87.58, 11.21) * mm});
            skLineSegment(sketch, "E1673", {"start": v(22.64, 18.04) * mm, "end": v(22.64, 18.27) * mm});
            skLineSegment(sketch, "E1674", {"start": v(14.07, -3.7) * mm, "end": v(13.87, -3.8) * mm});
            skLineSegment(sketch, "E1675", {"start": v(-22.36, -10.27) * mm, "end": v(-22.34, -10.41) * mm});
            skLineSegment(sketch, "E1676", {"start": v(-81.48, -52.64) * mm, "end": v(-81.6, -52.51) * mm});
            skLineSegment(sketch, "E1677", {"start": v(75.46, 20.18) * mm, "end": v(75.95, 20.94) * mm});
            skLineSegment(sketch, "E1678", {"start": v(-51.73, -62.93) * mm, "end": v(-51.47, -62.82) * mm});
            skLineSegment(sketch, "E1679", {"start": v(13.87, -3.8) * mm, "end": v(13.75, -3.89) * mm});
            skLineSegment(sketch, "E1680", {"start": v(-22.34, -10.41) * mm, "end": v(-22.32, -10.6) * mm});
            skLineSegment(sketch, "E1681", {"start": v(-81.6, -52.51) * mm, "end": v(-81.73, -52.35) * mm});
            skLineSegment(sketch, "E1682", {"start": v(75.95, 20.94) * mm, "end": v(76.6, 21.72) * mm});
            skLineSegment(sketch, "E1683", {"start": v(-51.47, -62.82) * mm, "end": v(-51.2, -62.69) * mm});
            skArc(sketch, "E1684", {"start": v(-72.56, 60.94) * mm, "mid": v(-71.76, 61.16) * mm, "end": v(-71.17, 61.74) * mm});
            skLineSegment(sketch, "E1685", {"start": v(13.75, -3.89) * mm, "end": v(13.6, -4) * mm});
            skLineSegment(sketch, "E1686", {"start": v(-22.32, -10.6) * mm, "end": v(-22.3, -10.8) * mm});
            skLineSegment(sketch, "E1687", {"start": v(-81.73, -52.35) * mm, "end": v(-81.85, -52.15) * mm});
            skArc(sketch, "E1688", {"start": v(74.09, 17.45) * mm, "mid": v(74.65, 17.65) * mm, "end": v(74.92, 18.2) * mm});
            skLineSegment(sketch, "E1689", {"start": v(-51.2, -62.69) * mm, "end": v(-50.4, -62.2) * mm});
            skLineSegment(sketch, "E1690", {"start": v(31.93, -11.6) * mm, "end": v(31.94, -11.8) * mm});
            skLineSegment(sketch, "E1691", {"start": v(42.48, 4.41) * mm, "end": v(42.66, 4.47) * mm});
            skLineSegment(sketch, "E1692", {"start": v(-72.56, 63.94) * mm, "end": v(-72.56, 64.14) * mm});
            skLineSegment(sketch, "E1693", {"start": v(13.6, -4) * mm, "end": v(13.45, -4.14) * mm});
            skLineSegment(sketch, "E1694", {"start": v(-22.3, -10.8) * mm, "end": v(-22.3, -11.04) * mm});
            skLineSegment(sketch, "E1695", {"start": v(-81.85, -52.15) * mm, "end": v(-81.98, -51.93) * mm});
            skArc(sketch, "E1696", {"start": v(74.09, 17.45) * mm, "mid": v(73.73, 17.45) * mm, "end": v(73.38, 17.45) * mm});
            skLineSegment(sketch, "E1697", {"start": v(-50.4, -62.2) * mm, "end": v(-49.58, -61.58) * mm});
            skLineSegment(sketch, "E1698", {"start": v(31.94, -11.8) * mm, "end": v(31.94, -12.03) * mm});
            skLineSegment(sketch, "E1699", {"start": v(42.66, 4.47) * mm, "end": v(42.85, 4.54) * mm});
            skLineSegment(sketch, "E1700", {"start": v(-73.77, 63.24) * mm, "end": v(-73.94, 63.34) * mm});
            skLineSegment(sketch, "E1701", {"start": v(13.45, -4.14) * mm, "end": v(13.28, -4.3) * mm});
            skLineSegment(sketch, "E1702", {"start": v(-22.3, -11.04) * mm, "end": v(-22.32, -11.28) * mm});
            skLineSegment(sketch, "E1703", {"start": v(-81.98, -51.93) * mm, "end": v(-82.1, -51.67) * mm});
            skArc(sketch, "E1704", {"start": v(72.55, 18.2) * mm, "mid": v(72.82, 17.65) * mm, "end": v(73.38, 17.45) * mm});
            skArc(sketch, "E1705", {"start": v(-49.58, -61.58) * mm, "mid": v(-49.7, -60.91) * mm, "end": v(-49.82, -60.24) * mm});
            skLineSegment(sketch, "E1706", {"start": v(31.94, -12.03) * mm, "end": v(31.93, -12.28) * mm});
            skLineSegment(sketch, "E1707", {"start": v(42.85, 4.54) * mm, "end": v(43.07, 4.62) * mm});
            skLineSegment(sketch, "E1708", {"start": v(-73.77, 61.84) * mm, "end": v(-73.94, 61.74) * mm});
            skLineSegment(sketch, "E1709", {"start": v(13.28, -4.3) * mm, "end": v(13.12, -4.49) * mm});
            skLineSegment(sketch, "E1710", {"start": v(-22.32, -11.28) * mm, "end": v(-22.34, -11.54) * mm});
            skLineSegment(sketch, "E1711", {"start": v(-82.1, -51.67) * mm, "end": v(-82.23, -51.4) * mm});
            skLineSegment(sketch, "E1712", {"start": v(72.55, 18.2) * mm, "end": v(72.5, 18.77) * mm});
            skLineSegment(sketch, "E1713", {"start": v(-53.72, -59.93) * mm, "end": v(-53.17, -59.78) * mm});
            skLineSegment(sketch, "E1714", {"start": v(31.93, -12.28) * mm, "end": v(31.9, -12.54) * mm});
            skLineSegment(sketch, "E1715", {"start": v(43.07, 4.62) * mm, "end": v(43.29, 4.73) * mm});
            skLineSegment(sketch, "E1716", {"start": v(-72.56, 61.14) * mm, "end": v(-72.56, 60.94) * mm});
            skLineSegment(sketch, "E1717", {"start": v(13.12, -4.49) * mm, "end": v(12.95, -4.69) * mm});
            skLineSegment(sketch, "E1718", {"start": v(-22.34, -11.54) * mm, "end": v(-22.5, -12.43) * mm});
            skLineSegment(sketch, "E1719", {"start": v(-82.23, -51.4) * mm, "end": v(-82.53, -50.51) * mm});
            skLineSegment(sketch, "E1720", {"start": v(72.5, 18.77) * mm, "end": v(72.47, 19) * mm});
            skLineSegment(sketch, "E1721", {"start": v(-53.17, -59.78) * mm, "end": v(-53, -59.74) * mm});
            skLineSegment(sketch, "E1722", {"start": v(31.9, -12.54) * mm, "end": v(31.74, -13.43) * mm});
            skLineSegment(sketch, "E1723", {"start": v(43.29, 4.73) * mm, "end": v(43.52, 4.85) * mm});
            skLineSegment(sketch, "E1724", {"start": v(-71.35, 61.84) * mm, "end": v(-71.17, 61.74) * mm});
            skLineSegment(sketch, "E1725", {"start": v(12.95, -4.69) * mm, "end": v(12.44, -5.43) * mm});
            skLineSegment(sketch, "E1726", {"start": v(-22.5, -12.43) * mm, "end": v(-22.8, -13.4) * mm});
            skLineSegment(sketch, "E1727", {"start": v(-82.53, -50.51) * mm, "end": v(-82.76, -49.5) * mm});
            skLineSegment(sketch, "E1728", {"start": v(72.47, 19) * mm, "end": v(72.44, 19.14) * mm});
            skLineSegment(sketch, "E1729", {"start": v(-53, -59.74) * mm, "end": v(-52.8, -59.72) * mm});
            skLineSegment(sketch, "E1730", {"start": v(-71.35, 63.24) * mm, "end": v(-71.17, 63.34) * mm});
            skLineSegment(sketch, "E1731", {"start": v(12.44, -5.43) * mm, "end": v(11.96, -6.32) * mm});
            skArc(sketch, "E1732", {"start": v(-22.12, -8.49) * mm, "mid": v(-22.56, -8.9) * mm, "end": v(-22.6, -9.5) * mm});
            skArc(sketch, "E1733", {"start": v(-81.03, -54.15) * mm, "mid": v(-80.83, -53.59) * mm, "end": v(-81.08, -53.04) * mm});
            skLineSegment(sketch, "E1734", {"start": v(72.44, 19.14) * mm, "end": v(72.4, 19.32) * mm});
            skLineSegment(sketch, "E1735", {"start": v(-52.8, -59.72) * mm, "end": v(-52.56, -59.7) * mm});
            skArc(sketch, "E1736", {"start": v(11.96, -6.32) * mm, "mid": v(12.32, -6.88) * mm, "end": v(12.7, -7.42) * mm});
            skArc(sketch, "E1737", {"start": v(-22.12, -8.49) * mm, "mid": v(-21.79, -8.36) * mm, "end": v(-21.47, -8.22) * mm});
            skArc(sketch, "E1738", {"start": v(-81.03, -54.15) * mm, "mid": v(-81.26, -54.42) * mm, "end": v(-81.49, -54.7) * mm});
            skLineSegment(sketch, "E1739", {"start": v(72.4, 19.32) * mm, "end": v(72.32, 19.52) * mm});
            skLineSegment(sketch, "E1740", {"start": v(-52.56, -59.7) * mm, "end": v(-52.3, -59.7) * mm});
            skLineSegment(sketch, "E1741", {"start": v(16.38, -6.11) * mm, "end": v(15.93, -6.49) * mm});
            skArc(sketch, "E1742", {"start": v(-20.4, -8.59) * mm, "mid": v(-20.86, -8.2) * mm, "end": v(-21.47, -8.22) * mm});
            skArc(sketch, "E1743", {"start": v(-82.59, -54.84) * mm, "mid": v(-82, -54.99) * mm, "end": v(-81.49, -54.7) * mm});
            skLineSegment(sketch, "E1744", {"start": v(72.32, 19.52) * mm, "end": v(72.23, 19.73) * mm});
            skLineSegment(sketch, "E1745", {"start": v(-52.3, -59.7) * mm, "end": v(-52.02, -59.72) * mm});
            skArc(sketch, "E1746", {"start": v(33.83, -9.58) * mm, "mid": v(33.38, -9.19) * mm, "end": v(32.78, -9.21) * mm});
            skLineSegment(sketch, "E1747", {"start": v(40.9, 7.48) * mm, "end": v(41.45, 7.65) * mm});
            skArc(sketch, "E1748", {"start": v(-29.47, 2.67) * mm, "mid": v(-29, 2.07) * mm, "end": v(-28.4, 1.6) * mm});
            skLineSegment(sketch, "E1749", {"start": v(15.93, -6.49) * mm, "end": v(15.76, -6.63) * mm});
            skLineSegment(sketch, "E1750", {"start": v(-20.4, -8.59) * mm, "end": v(-20.14, -9.1) * mm});
            skLineSegment(sketch, "E1751", {"start": v(-82.59, -54.84) * mm, "end": v(-83.05, -54.5) * mm});
            skLineSegment(sketch, "E1752", {"start": v(72.23, 19.73) * mm, "end": v(72.13, 19.95) * mm});
            skLineSegment(sketch, "E1753", {"start": v(-52.02, -59.72) * mm, "end": v(-51.71, -59.76) * mm});
            skLineSegment(sketch, "E1754", {"start": v(33.83, -9.58) * mm, "end": v(34.1, -10.1) * mm});
            skLineSegment(sketch, "E1755", {"start": v(41.45, 7.65) * mm, "end": v(41.67, 7.72) * mm});
            skLineSegment(sketch, "E1756", {"start": v(-65.22, 74) * mm, "end": v(-65.04, 74.8) * mm});
            skLineSegment(sketch, "E1757", {"start": v(-65.04, 74.8) * mm, "end": v(-64.98, 75.68) * mm});
            skLineSegment(sketch, "E1758", {"start": v(-64.98, 75.68) * mm, "end": v(-65.04, 76.67) * mm});
            skArc(sketch, "E1759", {"start": v(-65.04, 76.67) * mm, "mid": v(-65.62, 76.96) * mm, "end": v(-66.2, 77.23) * mm});
            skLineSegment(sketch, "E1760", {"start": v(-68.67, 74.2) * mm, "end": v(-68.49, 74.77) * mm});
            skLineSegment(sketch, "E1761", {"start": v(-68.49, 74.77) * mm, "end": v(-68.39, 75.05) * mm});
            skLineSegment(sketch, "E1762", {"start": v(-68.18, 75.43) * mm, "end": v(-67.66, 76.07) * mm});
            skLineSegment(sketch, "E1763", {"start": v(-68.27, 75.28) * mm, "end": v(-68.18, 75.43) * mm});
            skLineSegment(sketch, "E1764", {"start": v(-68.34, 75.15) * mm, "end": v(-68.27, 75.28) * mm});
            skLineSegment(sketch, "E1765", {"start": v(-68.39, 75.05) * mm, "end": v(-68.34, 75.15) * mm});
            skLineSegment(sketch, "E1766", {"start": v(36.9, -8.23) * mm, "end": v(37.04, -8.41) * mm});
            skLineSegment(sketch, "E1767", {"start": v(40, 9.67) * mm, "end": v(40.5, 9.94) * mm});
            skLineSegment(sketch, "E1768", {"start": v(-65.27, 73.84) * mm, "end": v(-65.22, 74) * mm});
            skLineSegment(sketch, "E1769", {"start": v(36.52, -7.79) * mm, "end": v(36.9, -8.23) * mm});
            skArc(sketch, "E1770", {"start": v(40, 9.67) * mm, "mid": v(39.6, 9.21) * mm, "end": v(39.62, 8.61) * mm});
            skLineSegment(sketch, "E1771", {"start": v(-65.33, 73.7) * mm, "end": v(-65.27, 73.84) * mm});
            skArc(sketch, "E1772", {"start": v(17.5, -6.17) * mm, "mid": v(17.74, -6.42) * mm, "end": v(18, -6.67) * mm});
            skArc(sketch, "E1773", {"start": v(-17.52, -11.2) * mm, "mid": v(-16.96, -10.85) * mm, "end": v(-16.4, -10.47) * mm});
            skLineSegment(sketch, "E1774", {"start": v(-84.25, -57.72) * mm, "end": v(-84.77, -57.49) * mm});
            skLineSegment(sketch, "E1775", {"start": v(69.08, 18.87) * mm, "end": v(69.08, 19.1) * mm});
            skLineSegment(sketch, "E1776", {"start": v(-53.5, -57.15) * mm, "end": v(-53.3, -56.98) * mm});
            skArc(sketch, "E1777", {"start": v(36.73, -12.2) * mm, "mid": v(37.29, -11.84) * mm, "end": v(37.83, -11.47) * mm});
            skArc(sketch, "E1778", {"start": v(39.9, 7.96) * mm, "mid": v(39.76, 8.29) * mm, "end": v(39.62, 8.61) * mm});
            skLineSegment(sketch, "E1779", {"start": v(-65.38, 73.6) * mm, "end": v(-65.33, 73.7) * mm});
            skArc(sketch, "E1780", {"start": v(17.5, -6.17) * mm, "mid": v(16.95, -5.92) * mm, "end": v(16.38, -6.11) * mm});
            skLineSegment(sketch, "E1781", {"start": v(-18.4, -10.73) * mm, "end": v(-17.52, -11.2) * mm});
            skArc(sketch, "E1782", {"start": v(-86.36, -53.8) * mm, "mid": v(-86.7, -54.38) * mm, "end": v(-87.04, -54.98) * mm});
            skLineSegment(sketch, "E1783", {"start": v(69.1, 18.66) * mm, "end": v(69.08, 18.87) * mm});
            skLineSegment(sketch, "E1784", {"start": v(-53.68, -57.3) * mm, "end": v(-53.5, -57.15) * mm});
            skLineSegment(sketch, "E1785", {"start": v(35.84, -11.73) * mm, "end": v(36.73, -12.2) * mm});
            skArc(sketch, "E1786", {"start": v(39.9, 7.96) * mm, "mid": v(40.3, 7.52) * mm, "end": v(40.9, 7.48) * mm});
            skLineSegment(sketch, "E1787", {"start": v(-65.54, 73.35) * mm, "end": v(-65.38, 73.6) * mm});
            skLineSegment(sketch, "E1788", {"start": v(13.7, -7.33) * mm, "end": v(12.7, -7.42) * mm});
            skLineSegment(sketch, "E1789", {"start": v(-19.15, -10.22) * mm, "end": v(-18.4, -10.73) * mm});
            skLineSegment(sketch, "E1790", {"start": v(-85.33, -53.85) * mm, "end": v(-86.36, -53.8) * mm});
            skLineSegment(sketch, "E1791", {"start": v(69.11, 18.48) * mm, "end": v(69.1, 18.66) * mm});
            skLineSegment(sketch, "E1792", {"start": v(-53.85, -57.4) * mm, "end": v(-53.68, -57.3) * mm});
            skLineSegment(sketch, "E1793", {"start": v(35.1, -11.21) * mm, "end": v(35.84, -11.73) * mm});
            skLineSegment(sketch, "E1794", {"start": v(43.84, 7.58) * mm, "end": v(44.8, 7.28) * mm});
            skLineSegment(sketch, "E1795", {"start": v(-65.86, 72.86) * mm, "end": v(-65.54, 73.35) * mm});
            skLineSegment(sketch, "E1796", {"start": v(14.59, -7.13) * mm, "end": v(13.7, -7.33) * mm});
            skLineSegment(sketch, "E1797", {"start": v(-19.35, -10.05) * mm, "end": v(-19.15, -10.22) * mm});
            skLineSegment(sketch, "E1798", {"start": v(-84.41, -54) * mm, "end": v(-85.33, -53.85) * mm});
            skLineSegment(sketch, "E1799", {"start": v(69.14, 18.34) * mm, "end": v(69.11, 18.48) * mm});
            skLineSegment(sketch, "E1800", {"start": v(-54, -57.49) * mm, "end": v(-53.85, -57.4) * mm});
            skLineSegment(sketch, "E1801", {"start": v(34.9, -11.05) * mm, "end": v(35.1, -11.21) * mm});
            skLineSegment(sketch, "E1802", {"start": v(42.95, 7.74) * mm, "end": v(43.84, 7.58) * mm});
            skArc(sketch, "E1803", {"start": v(-65.86, 72.86) * mm, "mid": v(-65.98, 72.26) * mm, "end": v(-65.66, 71.75) * mm});
            skLineSegment(sketch, "E1804", {"start": v(14.84, -7.06) * mm, "end": v(14.59, -7.13) * mm});
            skLineSegment(sketch, "E1805", {"start": v(-19.53, -9.89) * mm, "end": v(-19.35, -10.05) * mm});
            skLineSegment(sketch, "E1806", {"start": v(-84.12, -54.06) * mm, "end": v(-84.41, -54) * mm});
            skLineSegment(sketch, "E1807", {"start": v(69.2, 18.12) * mm, "end": v(69.14, 18.34) * mm});
            skLineSegment(sketch, "E1808", {"start": v(-54.53, -57.72) * mm, "end": v(-54, -57.49) * mm});
            skLineSegment(sketch, "E1809", {"start": v(34.71, -10.88) * mm, "end": v(34.9, -11.05) * mm});
            skLineSegment(sketch, "E1810", {"start": v(42.69, 7.76) * mm, "end": v(42.95, 7.74) * mm});
            skLineSegment(sketch, "E1811", {"start": v(15.07, -6.97) * mm, "end": v(14.84, -7.06) * mm});
            skLineSegment(sketch, "E1812", {"start": v(-19.7, -9.72) * mm, "end": v(-19.53, -9.89) * mm});
            skLineSegment(sketch, "E1813", {"start": v(-83.84, -54.14) * mm, "end": v(-84.12, -54.06) * mm});
            skLineSegment(sketch, "E1814", {"start": v(69.38, 17.56) * mm, "end": v(69.2, 18.12) * mm});
            skArc(sketch, "E1815", {"start": v(-54.53, -57.72) * mm, "mid": v(-54.94, -58.15) * mm, "end": v(-54.95, -58.75) * mm});
            skLineSegment(sketch, "E1816", {"start": v(34.55, -10.72) * mm, "end": v(34.71, -10.88) * mm});
            skLineSegment(sketch, "E1817", {"start": v(42.44, 7.77) * mm, "end": v(42.69, 7.76) * mm});
            skLineSegment(sketch, "E1818", {"start": v(15.28, -6.89) * mm, "end": v(15.07, -6.97) * mm});
            skLineSegment(sketch, "E1819", {"start": v(-19.83, -9.57) * mm, "end": v(-19.7, -9.72) * mm});
            skLineSegment(sketch, "E1820", {"start": v(-83.6, -54.23) * mm, "end": v(-83.84, -54.14) * mm});
            skArc(sketch, "E1821", {"start": v(70.88, 21.72) * mm, "mid": v(70.22, 21.6) * mm, "end": v(69.57, 21.46) * mm});
            skArc(sketch, "E1822", {"start": v(-54.7, -59.42) * mm, "mid": v(-54.82, -59.08) * mm, "end": v(-54.95, -58.75) * mm});
            skLineSegment(sketch, "E1823", {"start": v(34.41, -10.56) * mm, "end": v(34.55, -10.72) * mm});
            skLineSegment(sketch, "E1824", {"start": v(42.21, 7.77) * mm, "end": v(42.44, 7.77) * mm});
            skLineSegment(sketch, "E1825", {"start": v(15.47, -6.8) * mm, "end": v(15.28, -6.89) * mm});
            skLineSegment(sketch, "E1826", {"start": v(-19.95, -9.43) * mm, "end": v(-19.83, -9.57) * mm});
            skLineSegment(sketch, "E1827", {"start": v(-83.38, -54.32) * mm, "end": v(-83.6, -54.23) * mm});
            skLineSegment(sketch, "E1828", {"start": v(71.52, 20.94) * mm, "end": v(70.88, 21.72) * mm});
            skArc(sketch, "E1829", {"start": v(-54.7, -59.42) * mm, "mid": v(-54.32, -59.87) * mm, "end": v(-53.72, -59.93) * mm});
            skLineSegment(sketch, "E1830", {"start": v(34.3, -10.42) * mm, "end": v(34.41, -10.56) * mm});
            skLineSegment(sketch, "E1831", {"start": v(42, 7.76) * mm, "end": v(42.21, 7.77) * mm});
            skLineSegment(sketch, "E1832", {"start": v(15.63, -6.7) * mm, "end": v(15.47, -6.8) * mm});
            skLineSegment(sketch, "E1833", {"start": v(-20.03, -9.3) * mm, "end": v(-19.95, -9.43) * mm});
            skLineSegment(sketch, "E1834", {"start": v(-83.2, -54.41) * mm, "end": v(-83.38, -54.32) * mm});
            skLineSegment(sketch, "E1835", {"start": v(72, 20.18) * mm, "end": v(71.52, 20.94) * mm});
            skLineSegment(sketch, "E1836", {"start": v(-50.8, -59.93) * mm, "end": v(-49.82, -60.24) * mm});
            skLineSegment(sketch, "E1837", {"start": v(34.21, -10.3) * mm, "end": v(34.3, -10.42) * mm});
            skLineSegment(sketch, "E1838", {"start": v(41.82, 7.74) * mm, "end": v(42, 7.76) * mm});
            skLineSegment(sketch, "E1839", {"start": v(15.76, -6.63) * mm, "end": v(15.63, -6.7) * mm});
            skLineSegment(sketch, "E1840", {"start": v(-20.14, -9.1) * mm, "end": v(-20.03, -9.3) * mm});
            skLineSegment(sketch, "E1841", {"start": v(-83.05, -54.5) * mm, "end": v(-83.2, -54.41) * mm});
            skLineSegment(sketch, "E1842", {"start": v(72.13, 19.95) * mm, "end": v(72, 20.18) * mm});
            skLineSegment(sketch, "E1843", {"start": v(-51.71, -59.76) * mm, "end": v(-50.8, -59.93) * mm});
            skLineSegment(sketch, "E1844", {"start": v(34.1, -10.1) * mm, "end": v(34.21, -10.3) * mm});
            skLineSegment(sketch, "E1845", {"start": v(41.67, 7.72) * mm, "end": v(41.82, 7.74) * mm});
            skArc(sketch, "E1846", {"start": v(18, 12.91) * mm, "mid": v(18.25, 13.46) * mm, "end": v(18.06, 14.03) * mm});
            skLineSegment(sketch, "E1847", {"start": v(-41.8, -4.43) * mm, "end": v(-42.28, -5.32) * mm});
            skLineSegment(sketch, "E1848", {"start": v(80.74, -9.6) * mm, "end": v(80.86, -9.73) * mm});
            skLineSegment(sketch, "E1849", {"start": v(88.45, 8.6) * mm, "end": v(88.66, 8.6) * mm});
            skLineSegment(sketch, "E1850", {"start": v(26, 18.31) * mm, "end": v(25.94, 18.5) * mm});
            skLineSegment(sketch, "E1851", {"start": v(13.12, -1.4) * mm, "end": v(12.9, -1.47) * mm});
            skLineSegment(sketch, "E1852", {"start": v(-25.77, -10.13) * mm, "end": v(-25.72, -10.7) * mm});
            skArc(sketch, "E1853", {"start": v(-76.83, -50.79) * mm, "mid": v(-77.14, -50.96) * mm, "end": v(-77.44, -51.14) * mm});
            skLineSegment(sketch, "E1854", {"start": v(78.39, 19.1) * mm, "end": v(78.37, 19.35) * mm});
            skLineSegment(sketch, "E1855", {"start": v(-51.98, -65.74) * mm, "end": v(-51.73, -65.83) * mm});
            skLineSegment(sketch, "E1856", {"start": v(28.47, -11.12) * mm, "end": v(28.52, -11.7) * mm});
            skLineSegment(sketch, "E1857", {"start": v(42.11, 1.89) * mm, "end": v(42.34, 1.86) * mm});
            skLineSegment(sketch, "E1858", {"start": v(-65.41, -48.6) * mm, "end": v(-65.27, -48.04) * mm});
            skLineSegment(sketch, "E1859", {"start": v(16.84, 16.7) * mm, "end": v(16.74, 17.7) * mm});
            skLineSegment(sketch, "E1860", {"start": v(-41.3, -3.7) * mm, "end": v(-41.8, -4.43) * mm});
            skLineSegment(sketch, "E1861", {"start": v(80.66, -9.47) * mm, "end": v(80.74, -9.6) * mm});
            skLineSegment(sketch, "E1862", {"start": v(88.27, 8.57) * mm, "end": v(88.45, 8.6) * mm});
            skLineSegment(sketch, "E1863", {"start": v(26.03, 18.17) * mm, "end": v(26, 18.31) * mm});
            skLineSegment(sketch, "E1864", {"start": v(13.67, -1.23) * mm, "end": v(13.12, -1.4) * mm});
            skArc(sketch, "E1865", {"start": v(-25.77, -10.13) * mm, "mid": v(-26.04, -9.59) * mm, "end": v(-26.6, -9.38) * mm});
            skArc(sketch, "E1866", {"start": v(-76.83, -50.79) * mm, "mid": v(-76.45, -50.33) * mm, "end": v(-76.5, -49.73) * mm});
            skLineSegment(sketch, "E1867", {"start": v(78.39, 18.87) * mm, "end": v(78.39, 19.1) * mm});
            skLineSegment(sketch, "E1868", {"start": v(-52.2, -65.67) * mm, "end": v(-51.98, -65.74) * mm});
            skArc(sketch, "E1869", {"start": v(28.47, -11.12) * mm, "mid": v(28.2, -10.58) * mm, "end": v(27.64, -10.37) * mm});
            skLineSegment(sketch, "E1870", {"start": v(41.53, 1.94) * mm, "end": v(42.11, 1.89) * mm});
            skArc(sketch, "E1871", {"start": v(-61.91, -45.83) * mm, "mid": v(-62.55, -45.59) * mm, "end": v(-63.2, -45.37) * mm});
            skLineSegment(sketch, "E1872", {"start": v(17.03, 15.82) * mm, "end": v(16.84, 16.7) * mm});
            skLineSegment(sketch, "E1873", {"start": v(-41.12, -3.5) * mm, "end": v(-41.3, -3.7) * mm});
            skLineSegment(sketch, "E1874", {"start": v(80.55, -9.27) * mm, "end": v(80.66, -9.47) * mm});
            skLineSegment(sketch, "E1875", {"start": v(88.12, 8.55) * mm, "end": v(88.27, 8.57) * mm});
            skLineSegment(sketch, "E1876", {"start": v(26.05, 17.94) * mm, "end": v(26.03, 18.17) * mm});
            skArc(sketch, "E1877", {"start": v(9.52, 0.26) * mm, "mid": v(9.63, -0.39) * mm, "end": v(9.78, -1.04) * mm});
            skArc(sketch, "E1878", {"start": v(-27.3, -9.38) * mm, "mid": v(-26.96, -9.38) * mm, "end": v(-26.6, -9.38) * mm});
            skLineSegment(sketch, "E1879", {"start": v(-77, -46.86) * mm, "end": v(-76.86, -45.83) * mm});
            skLineSegment(sketch, "E1880", {"start": v(78.38, 18.66) * mm, "end": v(78.39, 18.87) * mm});
            skLineSegment(sketch, "E1881", {"start": v(-52.4, -65.63) * mm, "end": v(-52.2, -65.67) * mm});
            skArc(sketch, "E1882", {"start": v(26.93, -10.37) * mm, "mid": v(27.29, -10.38) * mm, "end": v(27.64, -10.37) * mm});
            skArc(sketch, "E1883", {"start": v(44.8, -1.04) * mm, "mid": v(44.94, -0.39) * mm, "end": v(45.06, 0.26) * mm});
            skLineSegment(sketch, "E1884", {"start": v(-61.78, -46.86) * mm, "end": v(-61.91, -45.83) * mm});
            skLineSegment(sketch, "E1885", {"start": v(17.1, 15.57) * mm, "end": v(17.03, 15.82) * mm});
            skLineSegment(sketch, "E1886", {"start": v(-40.96, -3.3) * mm, "end": v(-41.12, -3.5) * mm});
            skLineSegment(sketch, "E1887", {"start": v(80.28, -8.75) * mm, "end": v(80.55, -9.27) * mm});
            skLineSegment(sketch, "E1888", {"start": v(87.9, 8.48) * mm, "end": v(88.12, 8.55) * mm});
            skLineSegment(sketch, "E1889", {"start": v(26.1, 17.37) * mm, "end": v(26.05, 17.94) * mm});
            skLineSegment(sketch, "E1890", {"start": v(10.3, 0.9) * mm, "end": v(9.52, 0.26) * mm});
            skArc(sketch, "E1891", {"start": v(-27.3, -9.38) * mm, "mid": v(-27.87, -9.59) * mm, "end": v(-28.14, -10.13) * mm});
            skLineSegment(sketch, "E1892", {"start": v(-77.01, -47.78) * mm, "end": v(-77, -46.86) * mm});
            skLineSegment(sketch, "E1893", {"start": v(78.36, 18.48) * mm, "end": v(78.38, 18.66) * mm});
            skLineSegment(sketch, "E1894", {"start": v(-52.58, -65.6) * mm, "end": v(-52.4, -65.63) * mm});
            skArc(sketch, "E1895", {"start": v(26.93, -10.37) * mm, "mid": v(26.37, -10.58) * mm, "end": v(26.1, -11.12) * mm});
            skLineSegment(sketch, "E1896", {"start": v(43.84, -1.33) * mm, "end": v(44.8, -1.04) * mm});
            skLineSegment(sketch, "E1897", {"start": v(-61.76, -47.78) * mm, "end": v(-61.78, -46.86) * mm});
            skLineSegment(sketch, "E1898", {"start": v(17.2, 15.34) * mm, "end": v(17.1, 15.57) * mm});
            skLineSegment(sketch, "E1899", {"start": v(-40.8, -3.15) * mm, "end": v(-40.96, -3.3) * mm});
            skArc(sketch, "E1900", {"start": v(80.28, -8.75) * mm, "mid": v(79.83, -8.36) * mm, "end": v(79.23, -8.38) * mm});
            skLineSegment(sketch, "E1901", {"start": v(87.35, 8.3) * mm, "end": v(87.9, 8.48) * mm});
            skArc(sketch, "E1902", {"start": v(26.1, 17.37) * mm, "mid": v(26.37, 16.83) * mm, "end": v(26.93, 16.62) * mm});
            skLineSegment(sketch, "E1903", {"start": v(-77, -48.09) * mm, "end": v(-77.01, -47.78) * mm});
            skLineSegment(sketch, "E1904", {"start": v(78.33, 18.34) * mm, "end": v(78.36, 18.48) * mm});
            skLineSegment(sketch, "E1905", {"start": v(-53.15, -65.56) * mm, "end": v(-52.58, -65.6) * mm});
            skLineSegment(sketch, "E1906", {"start": v(25.07, -13.87) * mm, "end": v(24.43, -14.65) * mm});
            skLineSegment(sketch, "E1907", {"start": v(42.95, -1.5) * mm, "end": v(43.84, -1.33) * mm});
            skLineSegment(sketch, "E1908", {"start": v(-61.78, -48.09) * mm, "end": v(-61.76, -47.78) * mm});
            skLineSegment(sketch, "E1909", {"start": v(-76.96, -48.37) * mm, "end": v(-77, -48.09) * mm});
            skLineSegment(sketch, "E1910", {"start": v(78.27, 18.12) * mm, "end": v(78.33, 18.34) * mm});
            skArc(sketch, "E1911", {"start": v(-49.82, -68.52) * mm, "mid": v(-49.7, -67.86) * mm, "end": v(-49.58, -67.18) * mm});
            skLineSegment(sketch, "E1912", {"start": v(17.28, 15.13) * mm, "end": v(17.2, 15.34) * mm});
            skLineSegment(sketch, "E1913", {"start": v(-40.64, -3) * mm, "end": v(-40.8, -3.15) * mm});
            skArc(sketch, "E1914", {"start": v(78.57, -8.65) * mm, "mid": v(78.9, -8.52) * mm, "end": v(79.23, -8.38) * mm});
            skArc(sketch, "E1915", {"start": v(91.5, 6.8) * mm, "mid": v(91.39, 7.46) * mm, "end": v(91.25, 8.11) * mm});
            skArc(sketch, "E1916", {"start": v(27.64, 16.62) * mm, "mid": v(27.29, 16.62) * mm, "end": v(26.93, 16.62) * mm});
            skLineSegment(sketch, "E1917", {"start": v(25.56, -13.11) * mm, "end": v(25.07, -13.87) * mm});
            skLineSegment(sketch, "E1918", {"start": v(42.69, -1.52) * mm, "end": v(42.95, -1.5) * mm});
            skLineSegment(sketch, "E1919", {"start": v(-61.81, -48.37) * mm, "end": v(-61.78, -48.09) * mm});
            skLineSegment(sketch, "E1920", {"start": v(-76.92, -48.63) * mm, "end": v(-76.96, -48.37) * mm});
            skLineSegment(sketch, "E1921", {"start": v(78.09, 17.56) * mm, "end": v(78.27, 18.12) * mm});
            skLineSegment(sketch, "E1922", {"start": v(-50.8, -68.83) * mm, "end": v(-49.82, -68.52) * mm});
            skLineSegment(sketch, "E1923", {"start": v(17.37, 14.94) * mm, "end": v(17.28, 15.13) * mm});
            skLineSegment(sketch, "E1924", {"start": v(-40.5, -2.9) * mm, "end": v(-40.64, -3) * mm});
            skArc(sketch, "E1925", {"start": v(78.57, -8.65) * mm, "mid": v(78.13, -9.06) * mm, "end": v(78.09, -9.66) * mm});
            skLineSegment(sketch, "E1926", {"start": v(90.73, 6.17) * mm, "end": v(91.5, 6.8) * mm});
            skArc(sketch, "E1927", {"start": v(27.64, 16.62) * mm, "mid": v(28.2, 16.83) * mm, "end": v(28.47, 17.37) * mm});
            skLineSegment(sketch, "E1928", {"start": v(25.68, -12.88) * mm, "end": v(25.56, -13.11) * mm});
            skLineSegment(sketch, "E1929", {"start": v(42.44, -1.53) * mm, "end": v(42.69, -1.52) * mm});
            skLineSegment(sketch, "E1930", {"start": v(-61.86, -48.63) * mm, "end": v(-61.81, -48.37) * mm});
            skLineSegment(sketch, "E1931", {"start": v(-76.87, -48.86) * mm, "end": v(-76.92, -48.63) * mm});
            skArc(sketch, "E1932", {"start": v(78.09, 17.56) * mm, "mid": v(78.13, 16.96) * mm, "end": v(78.57, 16.55) * mm});
            skLineSegment(sketch, "E1933", {"start": v(-51.71, -69.01) * mm, "end": v(-50.8, -68.83) * mm});
            skLineSegment(sketch, "E1934", {"start": v(17.46, 14.78) * mm, "end": v(17.37, 14.94) * mm});
            skLineSegment(sketch, "E1935", {"start": v(-40.38, -2.8) * mm, "end": v(-40.5, -2.9) * mm});
            skLineSegment(sketch, "E1936", {"start": v(78.19, -12.6) * mm, "end": v(77.9, -13.56) * mm});
            skLineSegment(sketch, "E1937", {"start": v(89.97, 5.68) * mm, "end": v(90.73, 6.17) * mm});
            skLineSegment(sketch, "E1938", {"start": v(29.5, 20.12) * mm, "end": v(30.14, 20.9) * mm});
            skLineSegment(sketch, "E1939", {"start": v(25.79, -12.66) * mm, "end": v(25.68, -12.88) * mm});
            skLineSegment(sketch, "E1940", {"start": v(42.21, -1.53) * mm, "end": v(42.44, -1.53) * mm});
            skLineSegment(sketch, "E1941", {"start": v(-61.91, -48.86) * mm, "end": v(-61.86, -48.63) * mm});
            skLineSegment(sketch, "E1942", {"start": v(-76.8, -49.05) * mm, "end": v(-76.87, -48.86) * mm});
            skArc(sketch, "E1943", {"start": v(79.23, 16.28) * mm, "mid": v(78.9, 16.42) * mm, "end": v(78.57, 16.55) * mm});
            skLineSegment(sketch, "E1944", {"start": v(-52.02, -69.04) * mm, "end": v(-51.71, -69.01) * mm});
            skLineSegment(sketch, "E1945", {"start": v(17.54, 14.65) * mm, "end": v(17.46, 14.78) * mm});
            skLineSegment(sketch, "E1946", {"start": v(-40.18, -2.7) * mm, "end": v(-40.38, -2.8) * mm});
            skLineSegment(sketch, "E1947", {"start": v(78.35, -11.7) * mm, "end": v(78.19, -12.6) * mm});
            skLineSegment(sketch, "E1948", {"start": v(89.74, 5.56) * mm, "end": v(89.97, 5.68) * mm});
            skLineSegment(sketch, "E1949", {"start": v(29.02, 19.35) * mm, "end": v(29.5, 20.12) * mm});
            skLineSegment(sketch, "E1950", {"start": v(25.87, -12.45) * mm, "end": v(25.79, -12.66) * mm});
            skLineSegment(sketch, "E1951", {"start": v(42, -1.52) * mm, "end": v(42.21, -1.53) * mm});
            skLineSegment(sketch, "E1952", {"start": v(-61.97, -49.05) * mm, "end": v(-61.91, -48.86) * mm});
            skLineSegment(sketch, "E1953", {"start": v(-76.74, -49.21) * mm, "end": v(-76.8, -49.05) * mm});
            skArc(sketch, "E1954", {"start": v(79.23, 16.28) * mm, "mid": v(79.83, 16.26) * mm, "end": v(80.28, 16.66) * mm});
            skLineSegment(sketch, "E1955", {"start": v(-52.3, -69.06) * mm, "end": v(-52.02, -69.04) * mm});
            skLineSegment(sketch, "E1956", {"start": v(17.68, 14.48) * mm, "end": v(17.54, 14.65) * mm});
            skLineSegment(sketch, "E1957", {"start": v(-39.66, -2.43) * mm, "end": v(-40.18, -2.7) * mm});
            skLineSegment(sketch, "E1958", {"start": v(78.37, -11.45) * mm, "end": v(78.35, -11.7) * mm});
            skLineSegment(sketch, "E1959", {"start": v(89.51, 5.45) * mm, "end": v(89.74, 5.56) * mm});
            skLineSegment(sketch, "E1960", {"start": v(28.9, 19.12) * mm, "end": v(29.02, 19.35) * mm});
            skLineSegment(sketch, "E1961", {"start": v(25.94, -12.25) * mm, "end": v(25.87, -12.45) * mm});
            skLineSegment(sketch, "E1962", {"start": v(41.82, -1.5) * mm, "end": v(42, -1.52) * mm});
            skLineSegment(sketch, "E1963", {"start": v(-62.04, -49.21) * mm, "end": v(-61.97, -49.05) * mm});
            skLineSegment(sketch, "E1964", {"start": v(-76.5, -49.73) * mm, "end": v(-76.74, -49.21) * mm});
            skLineSegment(sketch, "E1965", {"start": v(82.29, 18.8) * mm, "end": v(83.18, 19.28) * mm});
            skLineSegment(sketch, "E1966", {"start": v(-52.56, -69.06) * mm, "end": v(-52.3, -69.06) * mm});
            skLineSegment(sketch, "E1967", {"start": v(18.06, 14.03) * mm, "end": v(17.68, 14.48) * mm});
            skArc(sketch, "E1968", {"start": v(-39.66, -2.43) * mm, "mid": v(-39.26, -1.98) * mm, "end": v(-39.29, -1.37) * mm});
            skLineSegment(sketch, "E1969", {"start": v(78.39, -11.2) * mm, "end": v(78.37, -11.45) * mm});
            skLineSegment(sketch, "E1970", {"start": v(89.3, 5.36) * mm, "end": v(89.51, 5.45) * mm});
            skLineSegment(sketch, "E1971", {"start": v(28.79, 18.9) * mm, "end": v(28.9, 19.12) * mm});
            skLineSegment(sketch, "E1972", {"start": v(26, -12.07) * mm, "end": v(25.94, -12.25) * mm});
            skLineSegment(sketch, "E1973", {"start": v(41.67, -1.47) * mm, "end": v(41.82, -1.5) * mm});
            skLineSegment(sketch, "E1974", {"start": v(-87.3, -65.95) * mm, "end": v(-87.58, -66.08) * mm});
            skLineSegment(sketch, "E1975", {"start": v(61.03, 14.2) * mm, "end": v(60.15, 14.4) * mm});
            skLineSegment(sketch, "E1976", {"start": v(-62.28, -49.73) * mm, "end": v(-62.04, -49.21) * mm});
            skArc(sketch, "E1977", {"start": v(-75.59, -45.37) * mm, "mid": v(-76.23, -45.59) * mm, "end": v(-76.86, -45.83) * mm});
            skLineSegment(sketch, "E1978", {"start": v(81.54, 18.29) * mm, "end": v(82.29, 18.8) * mm});
            skLineSegment(sketch, "E1979", {"start": v(-52.8, -69.05) * mm, "end": v(-52.56, -69.06) * mm});
            skArc(sketch, "E1980", {"start": v(17.85, 18.45) * mm, "mid": v(17.29, 18.09) * mm, "end": v(16.74, 17.7) * mm});
            skArc(sketch, "E1981", {"start": v(-39.56, -0.72) * mm, "mid": v(-39.43, -1.05) * mm, "end": v(-39.29, -1.37) * mm});
            skLineSegment(sketch, "E1982", {"start": v(78.39, -10.97) * mm, "end": v(78.39, -11.2) * mm});
            skLineSegment(sketch, "E1983", {"start": v(89.1, 5.3) * mm, "end": v(89.3, 5.36) * mm});
            skLineSegment(sketch, "E1984", {"start": v(28.7, 18.69) * mm, "end": v(28.79, 18.9) * mm});
            skLineSegment(sketch, "E1985", {"start": v(26.03, -11.93) * mm, "end": v(26, -12.07) * mm});
            skLineSegment(sketch, "E1986", {"start": v(41.45, -1.4) * mm, "end": v(41.67, -1.47) * mm});
            skLineSegment(sketch, "E1987", {"start": v(-87.04, -65.83) * mm, "end": v(-87.3, -65.95) * mm});
            skLineSegment(sketch, "E1988", {"start": v(61.28, 14.13) * mm, "end": v(61.03, 14.2) * mm});
            skArc(sketch, "E1989", {"start": v(-62.28, -49.73) * mm, "mid": v(-62.33, -50.32) * mm, "end": v(-61.95, -50.79) * mm});
            skLineSegment(sketch, "E1990", {"start": v(-74.83, -46.06) * mm, "end": v(-75.59, -45.37) * mm});
            skLineSegment(sketch, "E1991", {"start": v(81.34, 18.12) * mm, "end": v(81.54, 18.29) * mm});
            skLineSegment(sketch, "E1992", {"start": v(-53, -69.03) * mm, "end": v(-52.8, -69.05) * mm});
            skLineSegment(sketch, "E1993", {"start": v(18.74, 17.97) * mm, "end": v(17.85, 18.45) * mm});
            skArc(sketch, "E1994", {"start": v(-39.56, -0.72) * mm, "mid": v(-39.97, -0.28) * mm, "end": v(-40.57, -0.24) * mm});
            skLineSegment(sketch, "E1995", {"start": v(78.38, -10.76) * mm, "end": v(78.39, -10.97) * mm});
            skLineSegment(sketch, "E1996", {"start": v(88.93, 5.24) * mm, "end": v(89.1, 5.3) * mm});
            skLineSegment(sketch, "E1997", {"start": v(28.63, 18.5) * mm, "end": v(28.7, 18.69) * mm});
            skLineSegment(sketch, "E1998", {"start": v(26.05, -11.7) * mm, "end": v(26.03, -11.93) * mm});
            skLineSegment(sketch, "E1999", {"start": v(40.9, -1.23) * mm, "end": v(41.45, -1.4) * mm});
            skLineSegment(sketch, "E2000", {"start": v(-86.8, -65.74) * mm, "end": v(-87.04, -65.83) * mm});
            skLineSegment(sketch, "E2001", {"start": v(61.52, 14.05) * mm, "end": v(61.28, 14.13) * mm});
            skArc(sketch, "E2002", {"start": v(-61.33, -51.14) * mm, "mid": v(-61.64, -50.96) * mm, "end": v(-61.95, -50.79) * mm});
            skLineSegment(sketch, "E2003", {"start": v(-53.17, -68.99) * mm, "end": v(-53, -69.03) * mm});
            skLineSegment(sketch, "E2004", {"start": v(19.48, 17.46) * mm, "end": v(18.74, 17.97) * mm});
            skLineSegment(sketch, "E2005", {"start": v(-43.5, -0.34) * mm, "end": v(-44.47, -0.04) * mm});
            skLineSegment(sketch, "E2006", {"start": v(78.36, -10.58) * mm, "end": v(78.38, -10.76) * mm});
            skLineSegment(sketch, "E2007", {"start": v(88.78, 5.21) * mm, "end": v(88.93, 5.24) * mm});
            skLineSegment(sketch, "E2008", {"start": v(28.58, 18.31) * mm, "end": v(28.63, 18.5) * mm});
            skLineSegment(sketch, "E2009", {"start": v(26.1, -11.12) * mm, "end": v(26.05, -11.7) * mm});
            skArc(sketch, "E2010", {"start": v(40.9, -1.23) * mm, "mid": v(40.3, -1.27) * mm, "end": v(39.9, -1.72) * mm});
            skLineSegment(sketch, "E2011", {"start": v(-86.57, -65.67) * mm, "end": v(-86.8, -65.74) * mm});
            skLineSegment(sketch, "E2012", {"start": v(61.73, 13.96) * mm, "end": v(61.52, 14.05) * mm});
            skArc(sketch, "E2013", {"start": v(-61.33, -51.14) * mm, "mid": v(-60.74, -51.24) * mm, "end": v(-60.25, -50.9) * mm});
            skLineSegment(sketch, "E2014", {"start": v(-74.04, -47) * mm, "end": v(-74.22, -46.76) * mm});
            skLineSegment(sketch, "E2015", {"start": v(81, 17.8) * mm, "end": v(81.16, 17.95) * mm});
            skLineSegment(sketch, "E2016", {"start": v(-53.72, -68.83) * mm, "end": v(-53.17, -68.99) * mm});
            skLineSegment(sketch, "E2017", {"start": v(19.68, 17.3) * mm, "end": v(19.48, 17.46) * mm});
            skLineSegment(sketch, "E2018", {"start": v(-42.61, -0.5) * mm, "end": v(-43.5, -0.34) * mm});
            skLineSegment(sketch, "E2019", {"start": v(78.33, -10.43) * mm, "end": v(78.36, -10.58) * mm});
            skLineSegment(sketch, "E2020", {"start": v(88.56, 5.19) * mm, "end": v(88.78, 5.21) * mm});
            skLineSegment(sketch, "E2021", {"start": v(28.55, 18.17) * mm, "end": v(28.58, 18.31) * mm});
            skArc(sketch, "E2022", {"start": v(23.13, -14.4) * mm, "mid": v(23.78, -14.53) * mm, "end": v(24.43, -14.65) * mm});
            skArc(sketch, "E2023", {"start": v(39.62, -2.37) * mm, "mid": v(39.76, -2.04) * mm, "end": v(39.9, -1.72) * mm});
            skLineSegment(sketch, "E2024", {"start": v(-86.38, -65.63) * mm, "end": v(-86.57, -65.67) * mm});
            skLineSegment(sketch, "E2025", {"start": v(61.92, 13.87) * mm, "end": v(61.73, 13.96) * mm});
            skLineSegment(sketch, "E2026", {"start": v(-58.01, -49.03) * mm, "end": v(-57.06, -48.63) * mm});
            skLineSegment(sketch, "E2027", {"start": v(-73.88, -47.25) * mm, "end": v(-74.04, -47) * mm});
            skLineSegment(sketch, "E2028", {"start": v(80.86, 17.64) * mm, "end": v(81, 17.8) * mm});
            skArc(sketch, "E2029", {"start": v(-53.72, -68.83) * mm, "mid": v(-54.32, -68.9) * mm, "end": v(-54.7, -69.35) * mm});
            skLineSegment(sketch, "E2030", {"start": v(19.86, 17.12) * mm, "end": v(19.68, 17.3) * mm});
            skLineSegment(sketch, "E2031", {"start": v(-42.35, -0.52) * mm, "end": v(-42.61, -0.5) * mm});
            skLineSegment(sketch, "E2032", {"start": v(78.27, -10.22) * mm, "end": v(78.33, -10.43) * mm});
            skLineSegment(sketch, "E2033", {"start": v(87.98, 5.14) * mm, "end": v(88.56, 5.19) * mm});
            skLineSegment(sketch, "E2034", {"start": v(28.52, 17.94) * mm, "end": v(28.55, 18.17) * mm});
            skLineSegment(sketch, "E2035", {"start": v(22.83, -13.43) * mm, "end": v(23.13, -14.4) * mm});
            skArc(sketch, "E2036", {"start": v(39.62, -2.37) * mm, "mid": v(39.6, -2.97) * mm, "end": v(40, -3.43) * mm});
            skLineSegment(sketch, "E2037", {"start": v(-86.2, -65.6) * mm, "end": v(-86.38, -65.63) * mm});
            skLineSegment(sketch, "E2038", {"start": v(62.08, 13.78) * mm, "end": v(61.92, 13.87) * mm});
            skLineSegment(sketch, "E2039", {"start": v(-58.82, -49.48) * mm, "end": v(-58.01, -49.03) * mm});
            skLineSegment(sketch, "E2040", {"start": v(-73.75, -47.47) * mm, "end": v(-73.88, -47.25) * mm});
            skLineSegment(sketch, "E2041", {"start": v(80.74, 17.5) * mm, "end": v(80.86, 17.64) * mm});
            skArc(sketch, "E2042", {"start": v(-54.95, -70.02) * mm, "mid": v(-54.82, -69.68) * mm, "end": v(-54.7, -69.35) * mm});
            skLineSegment(sketch, "E2043", {"start": v(20.02, 16.96) * mm, "end": v(19.86, 17.12) * mm});
            skLineSegment(sketch, "E2044", {"start": v(-42.1, -0.53) * mm, "end": v(-42.35, -0.52) * mm});
            skLineSegment(sketch, "E2045", {"start": v(78.09, -9.66) * mm, "end": v(78.27, -10.22) * mm});
            skArc(sketch, "E2046", {"start": v(87.98, 5.14) * mm, "mid": v(87.44, 4.87) * mm, "end": v(87.23, 4.3) * mm});
            skLineSegment(sketch, "E2047", {"start": v(28.47, 17.37) * mm, "end": v(28.52, 17.94) * mm});
            skLineSegment(sketch, "E2048", {"start": v(22.67, -12.54) * mm, "end": v(22.83, -13.43) * mm});
            skLineSegment(sketch, "E2049", {"start": v(42.14, -5.43) * mm, "end": v(42.61, -6.32) * mm});
            skLineSegment(sketch, "E2050", {"start": v(-85.63, -65.56) * mm, "end": v(-86.2, -65.6) * mm});
            skLineSegment(sketch, "E2051", {"start": v(62.2, 13.7) * mm, "end": v(62.08, 13.78) * mm});
            skLineSegment(sketch, "E2052", {"start": v(-59.08, -49.65) * mm, "end": v(-58.82, -49.48) * mm});
            skLineSegment(sketch, "E2053", {"start": v(-73.64, -47.68) * mm, "end": v(-73.75, -47.47) * mm});
            skLineSegment(sketch, "E2054", {"start": v(80.66, 17.37) * mm, "end": v(80.74, 17.5) * mm});
            skArc(sketch, "E2055", {"start": v(-54.95, -70.02) * mm, "mid": v(-54.94, -70.61) * mm, "end": v(-54.53, -71.04) * mm});
            skLineSegment(sketch, "E2056", {"start": v(20.16, 16.8) * mm, "end": v(20.02, 16.96) * mm});
            skLineSegment(sketch, "E2057", {"start": v(-41.88, -0.53) * mm, "end": v(-42.1, -0.53) * mm});
            skArc(sketch, "E2058", {"start": v(76.6, -13.82) * mm, "mid": v(77.25, -13.7) * mm, "end": v(77.9, -13.56) * mm});
            skArc(sketch, "E2059", {"start": v(87.23, 3.6) * mm, "mid": v(87.23, 3.95) * mm, "end": v(87.23, 4.3) * mm});
            skArc(sketch, "E2060", {"start": v(31.45, 20.63) * mm, "mid": v(30.8, 20.78) * mm, "end": v(30.14, 20.9) * mm});
            skLineSegment(sketch, "E2061", {"start": v(22.65, -12.28) * mm, "end": v(22.67, -12.54) * mm});
            skLineSegment(sketch, "E2062", {"start": v(41.62, -4.69) * mm, "end": v(42.14, -5.43) * mm});
            skArc(sketch, "E2063", {"start": v(-85.63, -65.56) * mm, "mid": v(-85.1, -65.3) * mm, "end": v(-84.88, -64.74) * mm});
            skLineSegment(sketch, "E2064", {"start": v(62.38, 13.56) * mm, "end": v(62.2, 13.7) * mm});
            skLineSegment(sketch, "E2065", {"start": v(-59.3, -49.82) * mm, "end": v(-59.08, -49.65) * mm});
            skLineSegment(sketch, "E2066", {"start": v(-73.56, -47.87) * mm, "end": v(-73.64, -47.68) * mm});
            skLineSegment(sketch, "E2067", {"start": v(80.55, 17.17) * mm, "end": v(80.66, 17.37) * mm});
            skLineSegment(sketch, "E2068", {"start": v(-52.3, -72.92) * mm, "end": v(-51.74, -73.79) * mm});
            skLineSegment(sketch, "E2069", {"start": v(20.28, 16.66) * mm, "end": v(20.16, 16.8) * mm});
            skLineSegment(sketch, "E2070", {"start": v(-41.67, -0.52) * mm, "end": v(-41.88, -0.53) * mm});
            skLineSegment(sketch, "E2071", {"start": v(75.95, -13.04) * mm, "end": v(76.6, -13.82) * mm});
            skArc(sketch, "E2072", {"start": v(87.23, 3.6) * mm, "mid": v(87.44, 3.03) * mm, "end": v(87.98, 2.76) * mm});
            skLineSegment(sketch, "E2073", {"start": v(31.74, 19.67) * mm, "end": v(31.45, 20.63) * mm});
            skLineSegment(sketch, "E2074", {"start": v(22.64, -12.03) * mm, "end": v(22.65, -12.28) * mm});
            skLineSegment(sketch, "E2075", {"start": v(41.46, -4.49) * mm, "end": v(41.62, -4.69) * mm});
            skArc(sketch, "E2076", {"start": v(-84.88, -64.03) * mm, "mid": v(-84.89, -64.38) * mm, "end": v(-84.88, -64.74) * mm});
            skLineSegment(sketch, "E2077", {"start": v(62.82, 13.18) * mm, "end": v(62.38, 13.56) * mm});
            skLineSegment(sketch, "E2078", {"start": v(-59.5, -49.98) * mm, "end": v(-59.3, -49.82) * mm});
            skLineSegment(sketch, "E2079", {"start": v(-73.5, -48.04) * mm, "end": v(-73.56, -47.87) * mm});
            skLineSegment(sketch, "E2080", {"start": v(80.28, 16.66) * mm, "end": v(80.55, 17.17) * mm});
            skLineSegment(sketch, "E2081", {"start": v(-52.87, -72.2) * mm, "end": v(-52.3, -72.92) * mm});
            skLineSegment(sketch, "E2082", {"start": v(20.36, 16.54) * mm, "end": v(20.28, 16.66) * mm});
            skLineSegment(sketch, "E2083", {"start": v(-41.49, -0.5) * mm, "end": v(-41.67, -0.52) * mm});
            skLineSegment(sketch, "E2084", {"start": v(75.46, -12.28) * mm, "end": v(75.95, -13.04) * mm});
            skLineSegment(sketch, "E2085", {"start": v(90.73, 1.73) * mm, "end": v(91.5, 1.1) * mm});
            skLineSegment(sketch, "E2086", {"start": v(31.9, 18.78) * mm, "end": v(31.74, 19.67) * mm});
            skLineSegment(sketch, "E2087", {"start": v(22.64, -11.8) * mm, "end": v(22.64, -12.03) * mm});
            skLineSegment(sketch, "E2088", {"start": v(41.3, -4.3) * mm, "end": v(41.46, -4.49) * mm});
            skArc(sketch, "E2089", {"start": v(-84.88, -64.03) * mm, "mid": v(-85.1, -63.47) * mm, "end": v(-85.63, -63.2) * mm});
            skArc(sketch, "E2090", {"start": v(62.82, 13.18) * mm, "mid": v(63.4, 13) * mm, "end": v(63.94, 13.24) * mm});
            skLineSegment(sketch, "E2091", {"start": v(-59.68, -50.14) * mm, "end": v(-59.5, -49.98) * mm});
            skLineSegment(sketch, "E2092", {"start": v(-73.37, -48.6) * mm, "end": v(-73.5, -48.04) * mm});
            skArc(sketch, "E2093", {"start": v(84.28, 18.54) * mm, "mid": v(83.74, 18.92) * mm, "end": v(83.18, 19.28) * mm});
            skLineSegment(sketch, "E2094", {"start": v(-53.09, -71.98) * mm, "end": v(-52.87, -72.2) * mm});
            skLineSegment(sketch, "E2095", {"start": v(20.47, 16.34) * mm, "end": v(20.36, 16.54) * mm});
            skLineSegment(sketch, "E2096", {"start": v(-41.34, -0.48) * mm, "end": v(-41.49, -0.5) * mm});
            skLineSegment(sketch, "E2097", {"start": v(75.34, -12.05) * mm, "end": v(75.46, -12.28) * mm});
            skLineSegment(sketch, "E2098", {"start": v(89.97, 2.22) * mm, "end": v(90.73, 1.73) * mm});
            skLineSegment(sketch, "E2099", {"start": v(31.93, 18.52) * mm, "end": v(31.9, 18.78) * mm});
            skLineSegment(sketch, "E2100", {"start": v(22.65, -11.6) * mm, "end": v(22.64, -11.8) * mm});
            skLineSegment(sketch, "E2101", {"start": v(41.13, -4.14) * mm, "end": v(41.3, -4.3) * mm});
            skLineSegment(sketch, "E2102", {"start": v(-88.37, -62.2) * mm, "end": v(-89.2, -61.58) * mm});
            skArc(sketch, "E2103", {"start": v(64.44, 13.74) * mm, "mid": v(64.19, 13.5) * mm, "end": v(63.94, 13.24) * mm});
            skLineSegment(sketch, "E2104", {"start": v(-59.82, -50.29) * mm, "end": v(-59.68, -50.14) * mm});
            skArc(sketch, "E2105", {"start": v(-73.37, -48.6) * mm, "mid": v(-73.02, -49.08) * mm, "end": v(-72.43, -49.18) * mm});
            skLineSegment(sketch, "E2106", {"start": v(84.18, 17.54) * mm, "end": v(84.28, 18.54) * mm});
            skLineSegment(sketch, "E2107", {"start": v(-53.3, -71.78) * mm, "end": v(-53.09, -71.98) * mm});
            skLineSegment(sketch, "E2108", {"start": v(20.74, 15.83) * mm, "end": v(20.47, 16.34) * mm});
            skLineSegment(sketch, "E2109", {"start": v(-41.12, -0.41) * mm, "end": v(-41.34, -0.48) * mm});
            skLineSegment(sketch, "E2110", {"start": v(75.24, -11.83) * mm, "end": v(75.34, -12.05) * mm});
            skLineSegment(sketch, "E2111", {"start": v(89.74, 2.34) * mm, "end": v(89.97, 2.22) * mm});
            skLineSegment(sketch, "E2112", {"start": v(31.94, 18.27) * mm, "end": v(31.93, 18.52) * mm});
            skLineSegment(sketch, "E2113", {"start": v(22.67, -11.4) * mm, "end": v(22.65, -11.6) * mm});
            skLineSegment(sketch, "E2114", {"start": v(40.97, -4) * mm, "end": v(41.13, -4.14) * mm});
            skLineSegment(sketch, "E2115", {"start": v(-87.58, -62.69) * mm, "end": v(-88.37, -62.2) * mm});
            skArc(sketch, "E2116", {"start": v(64.44, 13.74) * mm, "mid": v(64.7, 14.3) * mm, "end": v(64.5, 14.86) * mm});
            skLineSegment(sketch, "E2117", {"start": v(-59.93, -50.43) * mm, "end": v(-59.82, -50.29) * mm});
            skArc(sketch, "E2118", {"start": v(-71.73, -49.06) * mm, "mid": v(-72.08, -49.12) * mm, "end": v(-72.43, -49.18) * mm});
            skLineSegment(sketch, "E2119", {"start": v(84, 16.65) * mm, "end": v(84.18, 17.54) * mm});
            skLineSegment(sketch, "E2120", {"start": v(-53.5, -71.61) * mm, "end": v(-53.3, -71.78) * mm});
            skArc(sketch, "E2121", {"start": v(20.74, 15.83) * mm, "mid": v(21.2, 15.43) * mm, "end": v(21.8, 15.45) * mm});
            skLineSegment(sketch, "E2122", {"start": v(-40.57, -0.24) * mm, "end": v(-41.12, -0.41) * mm});
            skLineSegment(sketch, "E2123", {"start": v(75.15, -11.62) * mm, "end": v(75.24, -11.83) * mm});
            skLineSegment(sketch, "E2124", {"start": v(89.51, 2.45) * mm, "end": v(89.74, 2.34) * mm});
            skLineSegment(sketch, "E2125", {"start": v(31.94, 18.04) * mm, "end": v(31.94, 18.27) * mm});
            skLineSegment(sketch, "E2126", {"start": v(22.7, -11.26) * mm, "end": v(22.67, -11.4) * mm});
            skLineSegment(sketch, "E2127", {"start": v(40.83, -3.89) * mm, "end": v(40.97, -4) * mm});
            skLineSegment(sketch, "E2128", {"start": v(-87.3, -62.82) * mm, "end": v(-87.58, -62.69) * mm});
            skLineSegment(sketch, "E2129", {"start": v(63.29, 17.54) * mm, "end": v(63.19, 18.54) * mm});
            skLineSegment(sketch, "E2130", {"start": v(-60.25, -50.9) * mm, "end": v(-59.93, -50.43) * mm});
            skArc(sketch, "E2131", {"start": v(-71.73, -49.06) * mm, "mid": v(-71.21, -48.76) * mm, "end": v(-71.05, -48.18) * mm});
            skLineSegment(sketch, "E2132", {"start": v(83.91, 16.4) * mm, "end": v(84, 16.65) * mm});
            skLineSegment(sketch, "E2133", {"start": v(-53.68, -71.47) * mm, "end": v(-53.5, -71.61) * mm});
            skArc(sketch, "E2134", {"start": v(22.45, 15.72) * mm, "mid": v(22.12, 15.6) * mm, "end": v(21.8, 15.45) * mm});
            skArc(sketch, "E2135", {"start": v(-44.73, 1.26) * mm, "mid": v(-44.61, 0.6) * mm, "end": v(-44.47, -0.04) * mm});
            skLineSegment(sketch, "E2136", {"start": v(75.08, -11.42) * mm, "end": v(75.15, -11.62) * mm});
            skLineSegment(sketch, "E2137", {"start": v(89.3, 2.54) * mm, "end": v(89.51, 2.45) * mm});
            skLineSegment(sketch, "E2138", {"start": v(31.93, 17.84) * mm, "end": v(31.94, 18.04) * mm});
            skLineSegment(sketch, "E2139", {"start": v(22.76, -11.05) * mm, "end": v(22.7, -11.26) * mm});
            skLineSegment(sketch, "E2140", {"start": v(40.7, -3.8) * mm, "end": v(40.83, -3.89) * mm});
            skLineSegment(sketch, "E2141", {"start": v(-87.04, -62.93) * mm, "end": v(-87.3, -62.82) * mm});
            skLineSegment(sketch, "E2142", {"start": v(63.48, 16.65) * mm, "end": v(63.29, 17.54) * mm});
            skArc(sketch, "E2143", {"start": v(-56.02, -49.5) * mm, "mid": v(-56.53, -49.06) * mm, "end": v(-57.06, -48.63) * mm});
            skLineSegment(sketch, "E2144", {"start": v(-70.54, -45.3) * mm, "end": v(-70.07, -44.4) * mm});
            skLineSegment(sketch, "E2145", {"start": v(83.83, 16.17) * mm, "end": v(83.91, 16.4) * mm});
            skLineSegment(sketch, "E2146", {"start": v(-53.85, -71.36) * mm, "end": v(-53.68, -71.47) * mm});
            skArc(sketch, "E2147", {"start": v(22.45, 15.72) * mm, "mid": v(22.9, 16.13) * mm, "end": v(22.93, 16.73) * mm});
            skLineSegment(sketch, "E2148", {"start": v(-43.95, 1.9) * mm, "end": v(-44.73, 1.26) * mm});
            skLineSegment(sketch, "E2149", {"start": v(75.03, -11.24) * mm, "end": v(75.08, -11.42) * mm});
            skLineSegment(sketch, "E2150", {"start": v(89.1, 2.6) * mm, "end": v(89.3, 2.54) * mm});
            skLineSegment(sketch, "E2151", {"start": v(31.9, 17.65) * mm, "end": v(31.93, 17.84) * mm});
            skLineSegment(sketch, "E2152", {"start": v(22.93, -10.5) * mm, "end": v(22.76, -11.05) * mm});
            skLineSegment(sketch, "E2153", {"start": v(40.5, -3.7) * mm, "end": v(40.7, -3.8) * mm});
            skLineSegment(sketch, "E2154", {"start": v(-86.8, -63.03) * mm, "end": v(-87.04, -62.93) * mm});
            skLineSegment(sketch, "E2155", {"start": v(63.56, 16.4) * mm, "end": v(63.48, 16.65) * mm});
            skLineSegment(sketch, "E2156", {"start": v(-56.24, -50.51) * mm, "end": v(-56.02, -49.5) * mm});
            skLineSegment(sketch, "E2157", {"start": v(-70.88, -46.17) * mm, "end": v(-70.54, -45.3) * mm});
            skLineSegment(sketch, "E2158", {"start": v(83.74, 15.96) * mm, "end": v(83.83, 16.17) * mm});
            skLineSegment(sketch, "E2159", {"start": v(-54, -71.28) * mm, "end": v(-53.85, -71.36) * mm});
            skLineSegment(sketch, "E2160", {"start": v(22.83, 19.67) * mm, "end": v(23.13, 20.63) * mm});
            skLineSegment(sketch, "E2161", {"start": v(-43.19, 2.39) * mm, "end": v(-43.95, 1.9) * mm});
            skLineSegment(sketch, "E2162", {"start": v(75, -11.1) * mm, "end": v(75.03, -11.24) * mm});
            skLineSegment(sketch, "E2163", {"start": v(88.93, 2.66) * mm, "end": v(89.1, 2.6) * mm});
            skLineSegment(sketch, "E2164", {"start": v(31.88, 17.5) * mm, "end": v(31.9, 17.65) * mm});
            skLineSegment(sketch, "E2165", {"start": v(11.05, 1.4) * mm, "end": v(10.3, 0.9) * mm});
            skLineSegment(sketch, "E2166", {"start": v(-29.17, -12.88) * mm, "end": v(-29.81, -13.65) * mm});
            skLineSegment(sketch, "E2167", {"start": v(-11.3, -0.5) * mm, "end": v(-10.4, -0.34) * mm});
            skArc(sketch, "E2168", {"start": v(22.93, -10.5) * mm, "mid": v(22.9, -9.9) * mm, "end": v(22.45, -9.48) * mm});
            skLineSegment(sketch, "E2169", {"start": v(40, -3.43) * mm, "end": v(40.5, -3.7) * mm});
            skLineSegment(sketch, "E2170", {"start": v(-86.57, -63.1) * mm, "end": v(-86.8, -63.03) * mm});
            skLineSegment(sketch, "E2171", {"start": v(63.64, 16.17) * mm, "end": v(63.56, 16.4) * mm});
            skLineSegment(sketch, "E2172", {"start": v(-56.54, -51.4) * mm, "end": v(-56.24, -50.51) * mm});
            skLineSegment(sketch, "E2173", {"start": v(-70.96, -46.47) * mm, "end": v(-70.88, -46.17) * mm});
            skLineSegment(sketch, "E2174", {"start": v(83.65, 15.77) * mm, "end": v(83.74, 15.96) * mm});
            skLineSegment(sketch, "E2175", {"start": v(-54.53, -71.04) * mm, "end": v(-54, -71.28) * mm});
            skLineSegment(sketch, "E2176", {"start": v(11.29, 1.51) * mm, "end": v(11.05, 1.4) * mm});
            skLineSegment(sketch, "E2177", {"start": v(-28.68, -12.12) * mm, "end": v(-29.17, -12.88) * mm});
            skLineSegment(sketch, "E2178", {"start": v(-11.56, -0.52) * mm, "end": v(-11.3, -0.5) * mm});
            skArc(sketch, "E2179", {"start": v(21.8, -9.21) * mm, "mid": v(22.12, -9.35) * mm, "end": v(22.45, -9.48) * mm});
            skArc(sketch, "E2180", {"start": v(41.87, -7.42) * mm, "mid": v(42.25, -6.88) * mm, "end": v(42.61, -6.32) * mm});
            skLineSegment(sketch, "E2181", {"start": v(-86.38, -63.14) * mm, "end": v(-86.57, -63.1) * mm});
            skLineSegment(sketch, "E2182", {"start": v(63.73, 15.96) * mm, "end": v(63.64, 16.17) * mm});
            skLineSegment(sketch, "E2183", {"start": v(-56.67, -51.67) * mm, "end": v(-56.54, -51.4) * mm});
            skLineSegment(sketch, "E2184", {"start": v(-71.03, -46.74) * mm, "end": v(-70.96, -46.47) * mm});
            skLineSegment(sketch, "E2185", {"start": v(83.56, 15.6) * mm, "end": v(83.65, 15.77) * mm});
            skArc(sketch, "E2186", {"start": v(-52.42, -74.97) * mm, "mid": v(-52.07, -74.38) * mm, "end": v(-51.74, -73.79) * mm});
            skLineSegment(sketch, "E2187", {"start": v(11.5, 1.62) * mm, "end": v(11.29, 1.51) * mm});
            skLineSegment(sketch, "E2188", {"start": v(-28.56, -11.88) * mm, "end": v(-28.68, -12.12) * mm});
            skLineSegment(sketch, "E2189", {"start": v(-11.8, -0.53) * mm, "end": v(-11.56, -0.52) * mm});
            skArc(sketch, "E2190", {"start": v(21.8, -9.21) * mm, "mid": v(21.2, -9.19) * mm, "end": v(20.74, -9.58) * mm});
            skLineSegment(sketch, "E2191", {"start": v(40.87, -7.33) * mm, "end": v(41.87, -7.42) * mm});
            skLineSegment(sketch, "E2192", {"start": v(-86.2, -63.17) * mm, "end": v(-86.38, -63.14) * mm});
            skLineSegment(sketch, "E2193", {"start": v(63.82, 15.77) * mm, "end": v(63.73, 15.96) * mm});
            skLineSegment(sketch, "E2194", {"start": v(-56.8, -51.93) * mm, "end": v(-56.67, -51.67) * mm});
            skLineSegment(sketch, "E2195", {"start": v(-71.07, -47) * mm, "end": v(-71.03, -46.74) * mm});
            skLineSegment(sketch, "E2196", {"start": v(83.49, 15.48) * mm, "end": v(83.56, 15.6) * mm});
            skLineSegment(sketch, "E2197", {"start": v(-53.45, -74.92) * mm, "end": v(-52.42, -74.97) * mm});
            skLineSegment(sketch, "E2198", {"start": v(11.72, 1.7) * mm, "end": v(11.5, 1.62) * mm});
            skLineSegment(sketch, "E2199", {"start": v(-28.46, -11.66) * mm, "end": v(-28.56, -11.88) * mm});
            skLineSegment(sketch, "E2200", {"start": v(-12.03, -0.53) * mm, "end": v(-11.8, -0.53) * mm});
            skLineSegment(sketch, "E2201", {"start": v(18.74, -11.73) * mm, "end": v(17.85, -12.2) * mm});
            skLineSegment(sketch, "E2202", {"start": v(39.99, -7.13) * mm, "end": v(40.87, -7.33) * mm});
            skLineSegment(sketch, "E2203", {"start": v(-85.63, -63.2) * mm, "end": v(-86.2, -63.17) * mm});
            skLineSegment(sketch, "E2204", {"start": v(63.9, 15.6) * mm, "end": v(63.82, 15.77) * mm});
            skLineSegment(sketch, "E2205", {"start": v(-56.92, -52.15) * mm, "end": v(-56.8, -51.93) * mm});
            skLineSegment(sketch, "E2206", {"start": v(11.89, 7.76) * mm, "end": v(11.63, 7.74) * mm});
            skLineSegment(sketch, "E2207", {"start": v(-14.5, -6.06) * mm, "end": v(-14.25, -6.14) * mm});
            skLineSegment(sketch, "E2208", {"start": v(-34.77, -10.22) * mm, "end": v(-35.5, -10.73) * mm});
            skLineSegment(sketch, "E2209", {"start": v(-71.1, -47.24) * mm, "end": v(-71.07, -47) * mm});
            skLineSegment(sketch, "E2210", {"start": v(83.34, 15.3) * mm, "end": v(83.49, 15.48) * mm});
            skLineSegment(sketch, "E2211", {"start": v(-54.36, -74.78) * mm, "end": v(-53.45, -74.92) * mm});
            skLineSegment(sketch, "E2212", {"start": v(-42.33, 2.77) * mm, "end": v(-42.52, 2.7) * mm});
            skLineSegment(sketch, "E2213", {"start": v(11.92, 1.78) * mm, "end": v(11.72, 1.7) * mm});
            skLineSegment(sketch, "E2214", {"start": v(-28.37, -11.45) * mm, "end": v(-28.46, -11.66) * mm});
            skLineSegment(sketch, "E2215", {"start": v(-12.24, -0.52) * mm, "end": v(-12.03, -0.53) * mm});
            skLineSegment(sketch, "E2216", {"start": v(19.48, -11.21) * mm, "end": v(18.74, -11.73) * mm});
            skLineSegment(sketch, "E2217", {"start": v(39.74, -7.06) * mm, "end": v(39.99, -7.13) * mm});
            skArc(sketch, "E2218", {"start": v(-88.95, -60.24) * mm, "mid": v(-89.08, -60.91) * mm, "end": v(-89.2, -61.58) * mm});
            skLineSegment(sketch, "E2219", {"start": v(63.98, 15.48) * mm, "end": v(63.9, 15.6) * mm});
            skLineSegment(sketch, "E2220", {"start": v(-57.05, -52.35) * mm, "end": v(-56.92, -52.15) * mm});
            skLineSegment(sketch, "E2221", {"start": v(12.14, 7.77) * mm, "end": v(11.89, 7.76) * mm});
            skLineSegment(sketch, "E2222", {"start": v(-14.74, -5.98) * mm, "end": v(-14.5, -6.06) * mm});
            skLineSegment(sketch, "E2223", {"start": v(-34.56, -10.05) * mm, "end": v(-34.77, -10.22) * mm});
            skLineSegment(sketch, "E2224", {"start": v(-71.12, -47.43) * mm, "end": v(-71.1, -47.24) * mm});
            skLineSegment(sketch, "E2225", {"start": v(82.97, 14.86) * mm, "end": v(83.34, 15.3) * mm});
            skLineSegment(sketch, "E2226", {"start": v(-54.66, -74.7) * mm, "end": v(-54.36, -74.78) * mm});
            skLineSegment(sketch, "E2227", {"start": v(-42.15, 2.82) * mm, "end": v(-42.33, 2.77) * mm});
            skLineSegment(sketch, "E2228", {"start": v(12.1, 1.83) * mm, "end": v(11.92, 1.78) * mm});
            skLineSegment(sketch, "E2229", {"start": v(-28.3, -11.25) * mm, "end": v(-28.37, -11.45) * mm});
            skLineSegment(sketch, "E2230", {"start": v(-12.42, -0.5) * mm, "end": v(-12.24, -0.52) * mm});
            skLineSegment(sketch, "E2231", {"start": v(19.68, -11.05) * mm, "end": v(19.48, -11.21) * mm});
            skLineSegment(sketch, "E2232", {"start": v(39.5, -6.97) * mm, "end": v(39.74, -7.06) * mm});
            skLineSegment(sketch, "E2233", {"start": v(-87.97, -59.93) * mm, "end": v(-88.95, -60.24) * mm});
            skLineSegment(sketch, "E2234", {"start": v(64.13, 15.3) * mm, "end": v(63.98, 15.48) * mm});
            skLineSegment(sketch, "E2235", {"start": v(-57.17, -52.51) * mm, "end": v(-57.05, -52.35) * mm});
            skLineSegment(sketch, "E2236", {"start": v(12.36, 7.77) * mm, "end": v(12.14, 7.77) * mm});
            skLineSegment(sketch, "E2237", {"start": v(-14.95, -5.9) * mm, "end": v(-14.74, -5.98) * mm});
            skLineSegment(sketch, "E2238", {"start": v(-34.38, -9.89) * mm, "end": v(-34.56, -10.05) * mm});
            skLineSegment(sketch, "E2239", {"start": v(-71.1, -47.62) * mm, "end": v(-71.12, -47.43) * mm});
            skArc(sketch, "E2240", {"start": v(82.97, 14.86) * mm, "mid": v(82.78, 14.3) * mm, "end": v(83.03, 13.74) * mm});
            skLineSegment(sketch, "E2241", {"start": v(-54.93, -74.62) * mm, "end": v(-54.66, -74.7) * mm});
            skLineSegment(sketch, "E2242", {"start": v(-42, 2.86) * mm, "end": v(-42.15, 2.82) * mm});
            skLineSegment(sketch, "E2243", {"start": v(12.24, 1.86) * mm, "end": v(12.1, 1.83) * mm});
            skLineSegment(sketch, "E2244", {"start": v(-28.25, -11.08) * mm, "end": v(-28.3, -11.25) * mm});
            skLineSegment(sketch, "E2245", {"start": v(-12.57, -0.48) * mm, "end": v(-12.42, -0.5) * mm});
            skLineSegment(sketch, "E2246", {"start": v(19.86, -10.88) * mm, "end": v(19.68, -11.05) * mm});
            skLineSegment(sketch, "E2247", {"start": v(39.3, -6.89) * mm, "end": v(39.5, -6.97) * mm});
            skLineSegment(sketch, "E2248", {"start": v(-87.06, -59.76) * mm, "end": v(-87.97, -59.93) * mm});
            skLineSegment(sketch, "E2249", {"start": v(64.5, 14.86) * mm, "end": v(64.13, 15.3) * mm});
            skLineSegment(sketch, "E2250", {"start": v(-57.3, -52.64) * mm, "end": v(-57.17, -52.51) * mm});
            skLineSegment(sketch, "E2251", {"start": v(12.57, 7.76) * mm, "end": v(12.36, 7.77) * mm});
            skLineSegment(sketch, "E2252", {"start": v(-15.14, -5.8) * mm, "end": v(-14.95, -5.9) * mm});
            skLineSegment(sketch, "E2253", {"start": v(-34.22, -9.72) * mm, "end": v(-34.38, -9.89) * mm});
            skLineSegment(sketch, "E2254", {"start": v(-71.05, -48.18) * mm, "end": v(-71.1, -47.62) * mm});
            skArc(sketch, "E2255", {"start": v(83.53, 13.24) * mm, "mid": v(83.28, 13.5) * mm, "end": v(83.03, 13.74) * mm});
            skLineSegment(sketch, "E2256", {"start": v(-55.18, -74.53) * mm, "end": v(-54.93, -74.62) * mm});
            skLineSegment(sketch, "E2257", {"start": v(-41.78, 2.88) * mm, "end": v(-42, 2.86) * mm});
            skLineSegment(sketch, "E2258", {"start": v(12.47, 1.89) * mm, "end": v(12.24, 1.86) * mm});
            skLineSegment(sketch, "E2259", {"start": v(-28.22, -10.93) * mm, "end": v(-28.25, -11.08) * mm});
            skLineSegment(sketch, "E2260", {"start": v(-12.79, -0.41) * mm, "end": v(-12.57, -0.48) * mm});
            skLineSegment(sketch, "E2261", {"start": v(20.02, -10.72) * mm, "end": v(19.86, -10.88) * mm});
            skLineSegment(sketch, "E2262", {"start": v(39.1, -6.8) * mm, "end": v(39.3, -6.89) * mm});
            skLineSegment(sketch, "E2263", {"start": v(-86.76, -59.72) * mm, "end": v(-87.06, -59.76) * mm});
            skArc(sketch, "E2264", {"start": v(64.3, 19.28) * mm, "mid": v(63.73, 18.92) * mm, "end": v(63.19, 18.54) * mm});
            skLineSegment(sketch, "E2265", {"start": v(-57.7, -53.04) * mm, "end": v(-57.3, -52.64) * mm});
            skLineSegment(sketch, "E2266", {"start": v(12.76, 7.74) * mm, "end": v(12.57, 7.76) * mm});
            skLineSegment(sketch, "E2267", {"start": v(-15.3, -5.71) * mm, "end": v(-15.14, -5.8) * mm});
            skLineSegment(sketch, "E2268", {"start": v(-34.08, -9.57) * mm, "end": v(-34.22, -9.72) * mm});
            skArc(sketch, "E2269", {"start": v(-68.7, -44.4) * mm, "mid": v(-69.39, -44.38) * mm, "end": v(-70.07, -44.4) * mm});
            skArc(sketch, "E2270", {"start": v(83.53, 13.24) * mm, "mid": v(84.07, 13) * mm, "end": v(84.65, 13.18) * mm});
            skLineSegment(sketch, "E2271", {"start": v(-55.4, -74.44) * mm, "end": v(-55.18, -74.53) * mm});
            skLineSegment(sketch, "E2272", {"start": v(-41.2, 2.93) * mm, "end": v(-41.78, 2.88) * mm});
            skLineSegment(sketch, "E2273", {"start": v(-70.96, -82.3) * mm, "end": v(-70.88, -82.6) * mm});
            skLineSegment(sketch, "E2274", {"start": v(64.5, -6.96) * mm, "end": v(64.13, -7.4) * mm});
            skLineSegment(sketch, "E2275", {"start": v(13.04, 1.94) * mm, "end": v(12.47, 1.89) * mm});
            skLineSegment(sketch, "E2276", {"start": v(-28.2, -10.7) * mm, "end": v(-28.22, -10.93) * mm});
            skLineSegment(sketch, "E2277", {"start": v(-13.34, -0.24) * mm, "end": v(-12.79, -0.41) * mm});
            skLineSegment(sketch, "E2278", {"start": v(20.16, -10.56) * mm, "end": v(20.02, -10.72) * mm});
            skLineSegment(sketch, "E2279", {"start": v(38.94, -6.7) * mm, "end": v(39.1, -6.8) * mm});
            skLineSegment(sketch, "E2280", {"start": v(-86.47, -59.7) * mm, "end": v(-86.76, -59.72) * mm});
            skLineSegment(sketch, "E2281", {"start": v(65.18, 18.8) * mm, "end": v(64.3, 19.28) * mm});
            skArc(sketch, "E2282", {"start": v(-57.7, -53.04) * mm, "mid": v(-57.94, -53.59) * mm, "end": v(-57.75, -54.15) * mm});
            skLineSegment(sketch, "E2283", {"start": v(12.9, 7.72) * mm, "end": v(12.76, 7.74) * mm});
            skLineSegment(sketch, "E2284", {"start": v(-15.42, -5.63) * mm, "end": v(-15.3, -5.71) * mm});
            skLineSegment(sketch, "E2285", {"start": v(-33.96, -9.43) * mm, "end": v(-34.08, -9.57) * mm});
            skLineSegment(sketch, "E2286", {"start": v(-68.23, -45.3) * mm, "end": v(-68.7, -44.4) * mm});
            skLineSegment(sketch, "E2287", {"start": v(87.32, 14.4) * mm, "end": v(88.32, 14.5) * mm});
            skLineSegment(sketch, "E2288", {"start": v(-55.57, -74.35) * mm, "end": v(-55.4, -74.44) * mm});
            skArc(sketch, "E2289", {"start": v(-41.2, 2.93) * mm, "mid": v(-40.66, 3.2) * mm, "end": v(-40.45, 3.76) * mm});
            skLineSegment(sketch, "E2290", {"start": v(-71.03, -82.02) * mm, "end": v(-70.96, -82.3) * mm});
            skArc(sketch, "E2291", {"start": v(64.5, -6.96) * mm, "mid": v(64.7, -6.39) * mm, "end": v(64.44, -5.84) * mm});
            skArc(sketch, "E2292", {"start": v(13.04, 1.94) * mm, "mid": v(13.58, 2.2) * mm, "end": v(13.8, 2.77) * mm});
            skLineSegment(sketch, "E2293", {"start": v(-28.14, -10.13) * mm, "end": v(-28.2, -10.7) * mm});
            skArc(sketch, "E2294", {"start": v(-13.34, -0.24) * mm, "mid": v(-13.94, -0.28) * mm, "end": v(-14.35, -0.72) * mm});
            skLineSegment(sketch, "E2295", {"start": v(20.28, -10.42) * mm, "end": v(20.16, -10.56) * mm});
            skLineSegment(sketch, "E2296", {"start": v(38.82, -6.63) * mm, "end": v(38.94, -6.7) * mm});
            skLineSegment(sketch, "E2297", {"start": v(-86.21, -59.7) * mm, "end": v(-86.47, -59.7) * mm});
            skLineSegment(sketch, "E2298", {"start": v(65.93, 18.29) * mm, "end": v(65.18, 18.8) * mm});
            skArc(sketch, "E2299", {"start": v(-57.29, -54.7) * mm, "mid": v(-57.51, -54.42) * mm, "end": v(-57.75, -54.15) * mm});
            skLineSegment(sketch, "E2300", {"start": v(13.12, 7.65) * mm, "end": v(12.9, 7.72) * mm});
            skLineSegment(sketch, "E2301", {"start": v(-15.6, -5.5) * mm, "end": v(-15.42, -5.63) * mm});
            skLineSegment(sketch, "E2302", {"start": v(-33.88, -9.3) * mm, "end": v(-33.96, -9.43) * mm});
            skLineSegment(sketch, "E2303", {"start": v(-67.9, -46.17) * mm, "end": v(-68.23, -45.3) * mm});
            skLineSegment(sketch, "E2304", {"start": v(86.44, 14.2) * mm, "end": v(87.32, 14.4) * mm});
            skLineSegment(sketch, "E2305", {"start": v(-55.73, -74.26) * mm, "end": v(-55.57, -74.35) * mm});
            skArc(sketch, "E2306", {"start": v(-40.45, 4.47) * mm, "mid": v(-40.46, 4.12) * mm, "end": v(-40.45, 3.76) * mm});
            skLineSegment(sketch, "E2307", {"start": v(-71.07, -81.76) * mm, "end": v(-71.03, -82.02) * mm});
            skArc(sketch, "E2308", {"start": v(63.94, -5.34) * mm, "mid": v(64.19, -5.6) * mm, "end": v(64.44, -5.84) * mm});
            skArc(sketch, "E2309", {"start": v(13.8, 3.47) * mm, "mid": v(13.79, 3.12) * mm, "end": v(13.8, 2.77) * mm});
            skArc(sketch, "E2310", {"start": v(-31.12, -13.4) * mm, "mid": v(-30.47, -13.54) * mm, "end": v(-29.81, -13.65) * mm});
            skArc(sketch, "E2311", {"start": v(-14.62, -1.37) * mm, "mid": v(-14.48, -1.05) * mm, "end": v(-14.35, -0.72) * mm});
            skLineSegment(sketch, "E2312", {"start": v(20.36, -10.3) * mm, "end": v(20.28, -10.42) * mm});
            skLineSegment(sketch, "E2313", {"start": v(38.64, -6.49) * mm, "end": v(38.82, -6.63) * mm});
            skLineSegment(sketch, "E2314", {"start": v(-85.98, -59.72) * mm, "end": v(-86.21, -59.7) * mm});
            skLineSegment(sketch, "E2315", {"start": v(66.13, 18.12) * mm, "end": v(65.93, 18.29) * mm});
            skArc(sketch, "E2316", {"start": v(-57.29, -54.7) * mm, "mid": v(-56.77, -54.99) * mm, "end": v(-56.19, -54.84) * mm});
            skLineSegment(sketch, "E2317", {"start": v(13.67, 7.48) * mm, "end": v(13.12, 7.65) * mm});
            skLineSegment(sketch, "E2318", {"start": v(-16.05, -5.12) * mm, "end": v(-15.6, -5.5) * mm});
            skLineSegment(sketch, "E2319", {"start": v(-33.77, -9.1) * mm, "end": v(-33.88, -9.3) * mm});
            skLineSegment(sketch, "E2320", {"start": v(-67.81, -46.47) * mm, "end": v(-67.9, -46.17) * mm});
            skLineSegment(sketch, "E2321", {"start": v(86.19, 14.13) * mm, "end": v(86.44, 14.2) * mm});
            skLineSegment(sketch, "E2322", {"start": v(-56.19, -73.92) * mm, "end": v(-55.73, -74.26) * mm});
            skArc(sketch, "E2323", {"start": v(-40.45, 4.47) * mm, "mid": v(-40.66, 5.04) * mm, "end": v(-41.2, 5.3) * mm});
            skLineSegment(sketch, "E2324", {"start": v(-71.1, -81.53) * mm, "end": v(-71.07, -81.76) * mm});
            skArc(sketch, "E2325", {"start": v(63.94, -5.34) * mm, "mid": v(63.4, -5.09) * mm, "end": v(62.82, -5.28) * mm});
            skArc(sketch, "E2326", {"start": v(13.8, 3.47) * mm, "mid": v(13.58, 4.04) * mm, "end": v(13.04, 4.3) * mm});
            skLineSegment(sketch, "E2327", {"start": v(-31.41, -12.43) * mm, "end": v(-31.12, -13.4) * mm});
            skArc(sketch, "E2328", {"start": v(-14.62, -1.37) * mm, "mid": v(-14.65, -1.98) * mm, "end": v(-14.25, -2.43) * mm});
            skLineSegment(sketch, "E2329", {"start": v(20.47, -10.1) * mm, "end": v(20.36, -10.3) * mm});
            skLineSegment(sketch, "E2330", {"start": v(38.2, -6.11) * mm, "end": v(38.64, -6.49) * mm});
            skLineSegment(sketch, "E2331", {"start": v(-85.78, -59.74) * mm, "end": v(-85.98, -59.72) * mm});
            skLineSegment(sketch, "E2332", {"start": v(66.3, 17.95) * mm, "end": v(66.13, 18.12) * mm});
            skLineSegment(sketch, "E2333", {"start": v(-53.45, -53.85) * mm, "end": v(-52.42, -53.8) * mm});
            skArc(sketch, "E2334", {"start": v(13.67, 7.48) * mm, "mid": v(14.28, 7.52) * mm, "end": v(14.68, 7.96) * mm});
            skArc(sketch, "E2335", {"start": v(-16.05, -5.12) * mm, "mid": v(-16.62, -4.92) * mm, "end": v(-17.16, -5.18) * mm});
            skLineSegment(sketch, "E2336", {"start": v(-33.5, -8.59) * mm, "end": v(-33.77, -9.1) * mm});
            skLineSegment(sketch, "E2337", {"start": v(-67.75, -46.74) * mm, "end": v(-67.81, -46.47) * mm});
            skLineSegment(sketch, "E2338", {"start": v(85.95, 14.05) * mm, "end": v(86.19, 14.13) * mm});
            skArc(sketch, "E2339", {"start": v(-56.19, -73.92) * mm, "mid": v(-56.77, -73.78) * mm, "end": v(-57.29, -74.07) * mm});
            skLineSegment(sketch, "E2340", {"start": v(-43.95, 6.33) * mm, "end": v(-44.73, 6.97) * mm});
            skLineSegment(sketch, "E2341", {"start": v(-71.12, -81.33) * mm, "end": v(-71.1, -81.53) * mm});
            skLineSegment(sketch, "E2342", {"start": v(60.15, -6.5) * mm, "end": v(59.15, -6.6) * mm});
            skLineSegment(sketch, "E2343", {"start": v(10.3, 5.34) * mm, "end": v(9.52, 5.98) * mm});
            skLineSegment(sketch, "E2344", {"start": v(-31.57, -11.54) * mm, "end": v(-31.41, -12.43) * mm});
            skLineSegment(sketch, "E2345", {"start": v(-12.1, -4.43) * mm, "end": v(-11.63, -5.32) * mm});
            skLineSegment(sketch, "E2346", {"start": v(20.74, -9.58) * mm, "end": v(20.47, -10.1) * mm});
            skArc(sketch, "E2347", {"start": v(38.2, -6.11) * mm, "mid": v(37.63, -5.92) * mm, "end": v(37.08, -6.17) * mm});
            skLineSegment(sketch, "E2348", {"start": v(-85.6, -59.78) * mm, "end": v(-85.78, -59.74) * mm});
            skLineSegment(sketch, "E2349", {"start": v(66.47, 17.8) * mm, "end": v(66.3, 17.95) * mm});
            skLineSegment(sketch, "E2350", {"start": v(-54.36, -54) * mm, "end": v(-53.45, -53.85) * mm});
            skArc(sketch, "E2351", {"start": v(14.95, 8.61) * mm, "mid": v(14.82, 8.29) * mm, "end": v(14.68, 7.96) * mm});
            skArc(sketch, "E2352", {"start": v(-37.5, -10.47) * mm, "mid": v(-36.96, -10.85) * mm, "end": v(-36.4, -11.2) * mm});
            skLineSegment(sketch, "E2353", {"start": v(-67.7, -47) * mm, "end": v(-67.75, -46.74) * mm});
            skLineSegment(sketch, "E2354", {"start": v(85.74, 13.96) * mm, "end": v(85.95, 14.05) * mm});
            skArc(sketch, "E2355", {"start": v(-57.75, -74.62) * mm, "mid": v(-57.51, -74.35) * mm, "end": v(-57.29, -74.07) * mm});
            skLineSegment(sketch, "E2356", {"start": v(-43.19, 5.85) * mm, "end": v(-43.95, 6.33) * mm});
            skLineSegment(sketch, "E2357", {"start": v(-71.1, -81.15) * mm, "end": v(-71.12, -81.33) * mm});
            skLineSegment(sketch, "E2358", {"start": v(61.03, -6.3) * mm, "end": v(60.15, -6.5) * mm});
            skLineSegment(sketch, "E2359", {"start": v(11.05, 4.85) * mm, "end": v(10.3, 5.34) * mm});
            skLineSegment(sketch, "E2360", {"start": v(-31.6, -11.28) * mm, "end": v(-31.57, -11.54) * mm});
            skLineSegment(sketch, "E2361", {"start": v(-12.62, -3.7) * mm, "end": v(-12.1, -4.43) * mm});
            skArc(sketch, "E2362", {"start": v(16.74, -11.47) * mm, "mid": v(17.29, -11.84) * mm, "end": v(17.85, -12.2) * mm});
            skArc(sketch, "E2363", {"start": v(-17.66, -5.68) * mm, "mid": v(-17.41, -5.43) * mm, "end": v(-17.16, -5.18) * mm});
            skLineSegment(sketch, "E2364", {"start": v(-85.05, -59.93) * mm, "end": v(-85.6, -59.78) * mm});
            skLineSegment(sketch, "E2365", {"start": v(66.61, 17.64) * mm, "end": v(66.47, 17.8) * mm});
            skLineSegment(sketch, "E2366", {"start": v(-54.66, -54.06) * mm, "end": v(-54.36, -54) * mm});
            skArc(sketch, "E2367", {"start": v(14.95, 8.61) * mm, "mid": v(14.98, 9.21) * mm, "end": v(14.58, 9.67) * mm});
            skLineSegment(sketch, "E2368", {"start": v(-37.4, -9.47) * mm, "end": v(-37.5, -10.47) * mm});
            skLineSegment(sketch, "E2369", {"start": v(-67.67, -47.24) * mm, "end": v(-67.7, -47) * mm});
            skLineSegment(sketch, "E2370", {"start": v(85.55, 13.87) * mm, "end": v(85.74, 13.96) * mm});
            skArc(sketch, "E2371", {"start": v(-57.75, -74.62) * mm, "mid": v(-57.94, -75.18) * mm, "end": v(-57.7, -75.72) * mm});
            skLineSegment(sketch, "E2372", {"start": v(-42.96, 5.72) * mm, "end": v(-43.19, 5.85) * mm});
            skLineSegment(sketch, "E2373", {"start": v(-71.05, -80.58) * mm, "end": v(-71.1, -81.15) * mm});
            skLineSegment(sketch, "E2374", {"start": v(61.28, -6.23) * mm, "end": v(61.03, -6.3) * mm});
            skLineSegment(sketch, "E2375", {"start": v(11.29, 4.73) * mm, "end": v(11.05, 4.85) * mm});
            skLineSegment(sketch, "E2376", {"start": v(-31.6, -11.04) * mm, "end": v(-31.6, -11.28) * mm});
            skLineSegment(sketch, "E2377", {"start": v(-12.79, -3.5) * mm, "end": v(-12.62, -3.7) * mm});
            skLineSegment(sketch, "E2378", {"start": v(16.84, -10.46) * mm, "end": v(16.74, -11.47) * mm});
            skArc(sketch, "E2379", {"start": v(-17.66, -5.68) * mm, "mid": v(-17.92, -6.22) * mm, "end": v(-17.72, -6.8) * mm});
            skArc(sketch, "E2380", {"start": v(-85.05, -59.93) * mm, "mid": v(-84.46, -59.87) * mm, "end": v(-84.07, -59.42) * mm});
            skLineSegment(sketch, "E2381", {"start": v(66.73, 17.5) * mm, "end": v(66.61, 17.64) * mm});
            skLineSegment(sketch, "E2382", {"start": v(-54.93, -54.14) * mm, "end": v(-54.66, -54.06) * mm});
            skLineSegment(sketch, "E2383", {"start": v(12.44, 11.67) * mm, "end": v(11.96, 12.56) * mm});
            skLineSegment(sketch, "E2384", {"start": v(-37.21, -8.58) * mm, "end": v(-37.4, -9.47) * mm});
            skLineSegment(sketch, "E2385", {"start": v(-67.66, -47.43) * mm, "end": v(-67.67, -47.24) * mm});
            skLineSegment(sketch, "E2386", {"start": v(85.4, 13.78) * mm, "end": v(85.55, 13.87) * mm});
            skLineSegment(sketch, "E2387", {"start": v(-56.24, -78.25) * mm, "end": v(-56.02, -79.26) * mm});
            skLineSegment(sketch, "E2388", {"start": v(-42.73, 5.62) * mm, "end": v(-42.96, 5.72) * mm});
            skArc(sketch, "E2389", {"start": v(-71.05, -80.58) * mm, "mid": v(-71.21, -80) * mm, "end": v(-71.73, -79.7) * mm});
            skLineSegment(sketch, "E2390", {"start": v(61.52, -6.14) * mm, "end": v(61.28, -6.23) * mm});
            skLineSegment(sketch, "E2391", {"start": v(11.5, 4.62) * mm, "end": v(11.29, 4.73) * mm});
            skLineSegment(sketch, "E2392", {"start": v(-31.6, -10.8) * mm, "end": v(-31.6, -11.04) * mm});
            skLineSegment(sketch, "E2393", {"start": v(-12.95, -3.3) * mm, "end": v(-12.79, -3.5) * mm});
            skLineSegment(sketch, "E2394", {"start": v(17.03, -9.58) * mm, "end": v(16.84, -10.46) * mm});
            skLineSegment(sketch, "E2395", {"start": v(-16.5, -9.47) * mm, "end": v(-16.4, -10.47) * mm});
            skArc(sketch, "E2396", {"start": v(-83.83, -58.75) * mm, "mid": v(-83.95, -59.08) * mm, "end": v(-84.07, -59.42) * mm});
            skLineSegment(sketch, "E2397", {"start": v(66.81, 17.37) * mm, "end": v(66.73, 17.5) * mm});
            skLineSegment(sketch, "E2398", {"start": v(-55.18, -54.23) * mm, "end": v(-54.93, -54.14) * mm});
            skLineSegment(sketch, "E2399", {"start": v(12.95, 10.93) * mm, "end": v(12.44, 11.67) * mm});
            skLineSegment(sketch, "E2400", {"start": v(-37.13, -8.33) * mm, "end": v(-37.21, -8.58) * mm});
            skLineSegment(sketch, "E2401", {"start": v(-67.67, -47.62) * mm, "end": v(-67.66, -47.43) * mm});
            skLineSegment(sketch, "E2402", {"start": v(85.27, 13.7) * mm, "end": v(85.4, 13.78) * mm});
            skLineSegment(sketch, "E2403", {"start": v(-56.54, -77.38) * mm, "end": v(-56.24, -78.25) * mm});
            skLineSegment(sketch, "E2404", {"start": v(-42.52, 5.53) * mm, "end": v(-42.73, 5.62) * mm});
            skArc(sketch, "E2405", {"start": v(-72.43, -79.58) * mm, "mid": v(-72.08, -79.65) * mm, "end": v(-71.73, -79.7) * mm});
            skLineSegment(sketch, "E2406", {"start": v(61.73, -6.06) * mm, "end": v(61.52, -6.14) * mm});
            skLineSegment(sketch, "E2407", {"start": v(11.72, 4.54) * mm, "end": v(11.5, 4.62) * mm});
            skLineSegment(sketch, "E2408", {"start": v(-31.6, -10.6) * mm, "end": v(-31.6, -10.8) * mm});
            skLineSegment(sketch, "E2409", {"start": v(-13.12, -3.15) * mm, "end": v(-12.95, -3.3) * mm});
            skArc(sketch, "E2410", {"start": v(45.06, 5.98) * mm, "mid": v(44.94, 6.63) * mm, "end": v(44.8, 7.28) * mm});
            skArc(sketch, "E2411", {"start": v(32.13, -9.48) * mm, "mid": v(32.45, -9.35) * mm, "end": v(32.78, -9.21) * mm});
            skLineSegment(sketch, "E2412", {"start": v(-36.96, 16.12) * mm, "end": v(-37.05, 16.34) * mm});
            skLineSegment(sketch, "E2413", {"start": v(17.1, -9.33) * mm, "end": v(17.03, -9.58) * mm});
            skLineSegment(sketch, "E2414", {"start": v(-16.7, -8.58) * mm, "end": v(-16.5, -9.47) * mm});
            skArc(sketch, "E2415", {"start": v(-83.83, -58.75) * mm, "mid": v(-83.83, -58.15) * mm, "end": v(-84.25, -57.72) * mm});
            skLineSegment(sketch, "E2416", {"start": v(66.92, 17.17) * mm, "end": v(66.81, 17.37) * mm});
            skLineSegment(sketch, "E2417", {"start": v(-55.4, -54.32) * mm, "end": v(-55.18, -54.23) * mm});
            skLineSegment(sketch, "E2418", {"start": v(13.12, 10.73) * mm, "end": v(12.95, 10.93) * mm});
            skLineSegment(sketch, "E2419", {"start": v(-37.05, -8.1) * mm, "end": v(-37.13, -8.33) * mm});
            skLineSegment(sketch, "E2420", {"start": v(-67.72, -48.18) * mm, "end": v(-67.67, -47.62) * mm});
            skLineSegment(sketch, "E2421", {"start": v(85.09, 13.56) * mm, "end": v(85.27, 13.7) * mm});
            skLineSegment(sketch, "E2422", {"start": v(-56.67, -77.1) * mm, "end": v(-56.54, -77.38) * mm});
            skLineSegment(sketch, "E2423", {"start": v(-42.33, 5.46) * mm, "end": v(-42.52, 5.53) * mm});
            skArc(sketch, "E2424", {"start": v(-72.43, -79.58) * mm, "mid": v(-73.02, -79.7) * mm, "end": v(-73.37, -80.18) * mm});
            skLineSegment(sketch, "E2425", {"start": v(61.92, -5.97) * mm, "end": v(61.73, -6.06) * mm});
            skLineSegment(sketch, "E2426", {"start": v(11.92, 4.47) * mm, "end": v(11.72, 4.54) * mm});
            skLineSegment(sketch, "E2427", {"start": v(-31.58, -10.41) * mm, "end": v(-31.6, -10.6) * mm});
            skLineSegment(sketch, "E2428", {"start": v(-13.27, -3) * mm, "end": v(-13.12, -3.15) * mm});
            skLineSegment(sketch, "E2429", {"start": v(44.28, 5.34) * mm, "end": v(45.06, 5.98) * mm});
            skArc(sketch, "E2430", {"start": v(32.13, -9.48) * mm, "mid": v(31.68, -9.9) * mm, "end": v(31.64, -10.5) * mm});
            skLineSegment(sketch, "E2431", {"start": v(-36.87, 15.93) * mm, "end": v(-36.96, 16.12) * mm});
            skLineSegment(sketch, "E2432", {"start": v(17.2, -9.1) * mm, "end": v(17.1, -9.33) * mm});
            skLineSegment(sketch, "E2433", {"start": v(-16.78, -8.33) * mm, "end": v(-16.7, -8.58) * mm});
            skLineSegment(sketch, "E2434", {"start": v(-86.48, -55.85) * mm, "end": v(-87.04, -54.98) * mm});
            skLineSegment(sketch, "E2435", {"start": v(67.19, 16.66) * mm, "end": v(66.92, 17.17) * mm});
            skLineSegment(sketch, "E2436", {"start": v(-55.57, -54.41) * mm, "end": v(-55.4, -54.32) * mm});
            skLineSegment(sketch, "E2437", {"start": v(13.28, 10.55) * mm, "end": v(13.12, 10.73) * mm});
            skLineSegment(sketch, "E2438", {"start": v(-36.96, -7.9) * mm, "end": v(-37.05, -8.1) * mm});
            skArc(sketch, "E2439", {"start": v(-67.72, -48.18) * mm, "mid": v(-67.56, -48.76) * mm, "end": v(-67.05, -49.06) * mm});
            skLineSegment(sketch, "E2440", {"start": v(84.65, 13.18) * mm, "end": v(85.09, 13.56) * mm});
            skLineSegment(sketch, "E2441", {"start": v(-56.8, -76.84) * mm, "end": v(-56.67, -77.1) * mm});
            skLineSegment(sketch, "E2442", {"start": v(-42.15, 5.4) * mm, "end": v(-42.33, 5.46) * mm});
            skLineSegment(sketch, "E2443", {"start": v(-74.83, -82.7) * mm, "end": v(-75.59, -83.4) * mm});
            skLineSegment(sketch, "E2444", {"start": v(62.08, -5.88) * mm, "end": v(61.92, -5.97) * mm});
            skLineSegment(sketch, "E2445", {"start": v(12.1, 4.41) * mm, "end": v(11.92, 4.47) * mm});
            skLineSegment(sketch, "E2446", {"start": v(-31.55, -10.27) * mm, "end": v(-31.58, -10.41) * mm});
            skLineSegment(sketch, "E2447", {"start": v(-13.41, -2.9) * mm, "end": v(-13.27, -3) * mm});
            skLineSegment(sketch, "E2448", {"start": v(43.52, 4.85) * mm, "end": v(44.28, 5.34) * mm});
            skLineSegment(sketch, "E2449", {"start": v(31.74, -13.43) * mm, "end": v(31.45, -14.4) * mm});
            skLineSegment(sketch, "E2450", {"start": v(-36.79, 15.77) * mm, "end": v(-36.87, 15.93) * mm});
            skLineSegment(sketch, "E2451", {"start": v(17.28, -8.89) * mm, "end": v(17.2, -9.1) * mm});
            skLineSegment(sketch, "E2452", {"start": v(-16.86, -8.1) * mm, "end": v(-16.78, -8.33) * mm});
            skLineSegment(sketch, "E2453", {"start": v(-85.9, -56.57) * mm, "end": v(-86.48, -55.85) * mm});
            skArc(sketch, "E2454", {"start": v(67.19, 16.66) * mm, "mid": v(67.64, 16.26) * mm, "end": v(68.24, 16.28) * mm});
            skLineSegment(sketch, "E2455", {"start": v(-55.73, -54.5) * mm, "end": v(-55.57, -54.41) * mm});
            skLineSegment(sketch, "E2456", {"start": v(13.45, 10.38) * mm, "end": v(13.28, 10.55) * mm});
            skLineSegment(sketch, "E2457", {"start": v(-36.87, -7.7) * mm, "end": v(-36.96, -7.9) * mm});
            skArc(sketch, "E2458", {"start": v(83.03, -5.84) * mm, "mid": v(83.28, -5.6) * mm, "end": v(83.53, -5.34) * mm});
            skArc(sketch, "E2459", {"start": v(89.06, 13.4) * mm, "mid": v(88.7, 13.95) * mm, "end": v(88.32, 14.5) * mm});
            skLineSegment(sketch, "E2460", {"start": v(-56.92, -76.61) * mm, "end": v(-56.8, -76.84) * mm});
            skLineSegment(sketch, "E2461", {"start": v(-42, 5.38) * mm, "end": v(-42.15, 5.4) * mm});
            skLineSegment(sketch, "E2462", {"start": v(-74.22, -82) * mm, "end": v(-74.83, -82.7) * mm});
            skLineSegment(sketch, "E2463", {"start": v(62.2, -5.8) * mm, "end": v(62.08, -5.88) * mm});
            skLineSegment(sketch, "E2464", {"start": v(12.24, 4.38) * mm, "end": v(12.1, 4.41) * mm});
            skLineSegment(sketch, "E2465", {"start": v(-31.49, -10.05) * mm, "end": v(-31.55, -10.27) * mm});
            skLineSegment(sketch, "E2466", {"start": v(-13.53, -2.8) * mm, "end": v(-13.41, -2.9) * mm});
            skLineSegment(sketch, "E2467", {"start": v(17.37, -8.7) * mm, "end": v(17.28, -8.89) * mm});
            skLineSegment(sketch, "E2468", {"start": v(-16.95, -7.9) * mm, "end": v(-16.86, -8.1) * mm});
            skLineSegment(sketch, "E2469", {"start": v(-85.7, -56.79) * mm, "end": v(-85.9, -56.57) * mm});
            skArc(sketch, "E2470", {"start": v(68.9, 16.55) * mm, "mid": v(68.57, 16.42) * mm, "end": v(68.24, 16.28) * mm});
            skLineSegment(sketch, "E2471", {"start": v(-56.19, -54.84) * mm, "end": v(-55.73, -54.5) * mm});
            skLineSegment(sketch, "E2472", {"start": v(13.6, 10.24) * mm, "end": v(13.45, 10.38) * mm});
            skLineSegment(sketch, "E2473", {"start": v(-36.79, -7.54) * mm, "end": v(-36.87, -7.7) * mm});
            skArc(sketch, "E2474", {"start": v(83.03, -5.84) * mm, "mid": v(82.78, -6.39) * mm, "end": v(82.97, -6.96) * mm});
            skLineSegment(sketch, "E2475", {"start": v(88.59, 12.5) * mm, "end": v(89.06, 13.4) * mm});
            skLineSegment(sketch, "E2476", {"start": v(-57.05, -76.42) * mm, "end": v(-56.92, -76.61) * mm});
            skLineSegment(sketch, "E2477", {"start": v(-41.78, 5.35) * mm, "end": v(-42, 5.38) * mm});
            skLineSegment(sketch, "E2478", {"start": v(-74.04, -81.76) * mm, "end": v(-74.22, -82) * mm});
            skLineSegment(sketch, "E2479", {"start": v(62.38, -5.66) * mm, "end": v(62.2, -5.8) * mm});
            skLineSegment(sketch, "E2480", {"start": v(12.47, 4.36) * mm, "end": v(12.24, 4.38) * mm});
            skLineSegment(sketch, "E2481", {"start": v(-31.31, -9.5) * mm, "end": v(-31.49, -10.05) * mm});
            skLineSegment(sketch, "E2482", {"start": v(-13.73, -2.7) * mm, "end": v(-13.53, -2.8) * mm});
            skLineSegment(sketch, "E2483", {"start": v(17.46, -8.54) * mm, "end": v(17.37, -8.7) * mm});
            skLineSegment(sketch, "E2484", {"start": v(-17.04, -7.7) * mm, "end": v(-16.95, -7.9) * mm});
            skLineSegment(sketch, "E2485", {"start": v(-85.48, -56.98) * mm, "end": v(-85.7, -56.79) * mm});
            skArc(sketch, "E2486", {"start": v(68.9, 16.55) * mm, "mid": v(69.34, 16.96) * mm, "end": v(69.38, 17.56) * mm});
            skArc(sketch, "E2487", {"start": v(-51.74, -54.98) * mm, "mid": v(-52.07, -54.38) * mm, "end": v(-52.42, -53.8) * mm});
            skLineSegment(sketch, "E2488", {"start": v(13.75, 10.13) * mm, "end": v(13.6, 10.24) * mm});
            skLineSegment(sketch, "E2489", {"start": v(-36.7, -7.42) * mm, "end": v(-36.79, -7.54) * mm});
            skLineSegment(sketch, "E2490", {"start": v(84.18, -9.63) * mm, "end": v(84.28, -10.64) * mm});
            skLineSegment(sketch, "E2491", {"start": v(88.07, 11.76) * mm, "end": v(88.59, 12.5) * mm});
            skLineSegment(sketch, "E2492", {"start": v(-57.17, -76.26) * mm, "end": v(-57.05, -76.42) * mm});
            skLineSegment(sketch, "E2493", {"start": v(-41.2, 5.3) * mm, "end": v(-41.78, 5.35) * mm});
            skLineSegment(sketch, "E2494", {"start": v(-73.88, -81.52) * mm, "end": v(-74.04, -81.76) * mm});
            skLineSegment(sketch, "E2495", {"start": v(62.82, -5.28) * mm, "end": v(62.38, -5.66) * mm});
            skLineSegment(sketch, "E2496", {"start": v(13.04, 4.3) * mm, "end": v(12.47, 4.36) * mm});
            skArc(sketch, "E2497", {"start": v(-31.31, -9.5) * mm, "mid": v(-31.35, -8.9) * mm, "end": v(-31.8, -8.49) * mm});
            skLineSegment(sketch, "E2498", {"start": v(-14.25, -2.43) * mm, "end": v(-13.73, -2.7) * mm});
            skLineSegment(sketch, "E2499", {"start": v(17.54, -8.41) * mm, "end": v(17.46, -8.54) * mm});
            skLineSegment(sketch, "E2500", {"start": v(-17.13, -7.54) * mm, "end": v(-17.04, -7.7) * mm});
            skLineSegment(sketch, "E2501", {"start": v(-85.28, -57.15) * mm, "end": v(-85.48, -56.98) * mm});
            skLineSegment(sketch, "E2502", {"start": v(69.28, 20.5) * mm, "end": v(69.57, 21.46) * mm});
            skLineSegment(sketch, "E2503", {"start": v(-52.3, -55.85) * mm, "end": v(-51.74, -54.98) * mm});
            skLineSegment(sketch, "E2504", {"start": v(13.87, 10.04) * mm, "end": v(13.75, 10.13) * mm});
            skLineSegment(sketch, "E2505", {"start": v(-36.56, -7.24) * mm, "end": v(-36.7, -7.42) * mm});
            skLineSegment(sketch, "E2506", {"start": v(84, -8.75) * mm, "end": v(84.18, -9.63) * mm});
            skLineSegment(sketch, "E2507", {"start": v(87.9, 11.56) * mm, "end": v(88.07, 11.76) * mm});
            skLineSegment(sketch, "E2508", {"start": v(-57.3, -76.12) * mm, "end": v(-57.17, -76.26) * mm});
            skArc(sketch, "E2509", {"start": v(-44.47, 8.28) * mm, "mid": v(-44.61, 7.63) * mm, "end": v(-44.73, 6.97) * mm});
            skLineSegment(sketch, "E2510", {"start": v(-73.75, -81.3) * mm, "end": v(-73.88, -81.52) * mm});
            skArc(sketch, "E2511", {"start": v(58.4, -5.49) * mm, "mid": v(58.77, -6.05) * mm, "end": v(59.15, -6.6) * mm});
            skArc(sketch, "E2512", {"start": v(9.78, 7.28) * mm, "mid": v(9.63, 6.63) * mm, "end": v(9.52, 5.98) * mm});
            skArc(sketch, "E2513", {"start": v(-32.45, -8.22) * mm, "mid": v(-32.12, -8.36) * mm, "end": v(-31.8, -8.49) * mm});
            skArc(sketch, "E2514", {"start": v(-12.37, -6.43) * mm, "mid": v(-11.99, -5.88) * mm, "end": v(-11.63, -5.32) * mm});
            skLineSegment(sketch, "E2515", {"start": v(17.68, -8.23) * mm, "end": v(17.54, -8.41) * mm});
            skLineSegment(sketch, "E2516", {"start": v(-17.2, -7.42) * mm, "end": v(-17.13, -7.54) * mm});
            skLineSegment(sketch, "E2517", {"start": v(-85.1, -57.3) * mm, "end": v(-85.28, -57.15) * mm});
            skLineSegment(sketch, "E2518", {"start": v(69.12, 19.61) * mm, "end": v(69.28, 20.5) * mm});
            skLineSegment(sketch, "E2519", {"start": v(-52.87, -56.57) * mm, "end": v(-52.3, -55.85) * mm});
            skLineSegment(sketch, "E2520", {"start": v(14.07, 9.94) * mm, "end": v(13.87, 10.04) * mm});
            skLineSegment(sketch, "E2521", {"start": v(-36.19, -6.8) * mm, "end": v(-36.56, -7.24) * mm});
            skLineSegment(sketch, "E2522", {"start": v(83.91, -8.5) * mm, "end": v(84, -8.75) * mm});
            skLineSegment(sketch, "E2523", {"start": v(87.74, 11.38) * mm, "end": v(87.9, 11.56) * mm});
            skLineSegment(sketch, "E2524", {"start": v(-57.7, -75.72) * mm, "end": v(-57.3, -76.12) * mm});
            skLineSegment(sketch, "E2525", {"start": v(-43.5, 8.57) * mm, "end": v(-44.47, 8.28) * mm});
            skLineSegment(sketch, "E2526", {"start": v(-73.64, -81.08) * mm, "end": v(-73.75, -81.3) * mm});
            skLineSegment(sketch, "E2527", {"start": v(58.88, -4.6) * mm, "end": v(58.4, -5.49) * mm});
            skLineSegment(sketch, "E2528", {"start": v(10.74, 7.58) * mm, "end": v(9.78, 7.28) * mm});
            skArc(sketch, "E2529", {"start": v(-32.45, -8.22) * mm, "mid": v(-33.05, -8.2) * mm, "end": v(-33.5, -8.59) * mm});
            skLineSegment(sketch, "E2530", {"start": v(-13.37, -6.33) * mm, "end": v(-12.37, -6.43) * mm});
            skLineSegment(sketch, "E2531", {"start": v(18.06, -7.79) * mm, "end": v(17.68, -8.23) * mm});
            skLineSegment(sketch, "E2532", {"start": v(-17.35, -7.24) * mm, "end": v(-17.2, -7.42) * mm});
            skLineSegment(sketch, "E2533", {"start": v(-84.93, -57.4) * mm, "end": v(-85.1, -57.3) * mm});
            skLineSegment(sketch, "E2534", {"start": v(69.1, 19.35) * mm, "end": v(69.12, 19.61) * mm});
            skLineSegment(sketch, "E2535", {"start": v(-53.09, -56.79) * mm, "end": v(-52.87, -56.57) * mm});
            skLineSegment(sketch, "E2536", {"start": v(14.58, 9.67) * mm, "end": v(14.07, 9.94) * mm});
            skArc(sketch, "E2537", {"start": v(-36.19, -6.8) * mm, "mid": v(-36, -6.22) * mm, "end": v(-36.25, -5.68) * mm});
            skLineSegment(sketch, "E2538", {"start": v(83.83, -8.27) * mm, "end": v(83.91, -8.5) * mm});
            skLineSegment(sketch, "E2539", {"start": v(87.58, 11.21) * mm, "end": v(87.74, 11.38) * mm});
            skArc(sketch, "E2540", {"start": v(-57.06, -80.13) * mm, "mid": v(-56.53, -79.7) * mm, "end": v(-56.02, -79.26) * mm});
            skLineSegment(sketch, "E2541", {"start": v(-42.61, 8.73) * mm, "end": v(-43.5, 8.57) * mm});
            skLineSegment(sketch, "E2542", {"start": v(-73.56, -80.9) * mm, "end": v(-73.64, -81.08) * mm});
            skLineSegment(sketch, "E2543", {"start": v(59.4, -3.86) * mm, "end": v(58.88, -4.6) * mm});
            skLineSegment(sketch, "E2544", {"start": v(11.63, 7.74) * mm, "end": v(10.74, 7.58) * mm});
            skLineSegment(sketch, "E2545", {"start": v(-35.5, -10.73) * mm, "end": v(-36.4, -11.2) * mm});
            skLineSegment(sketch, "E2546", {"start": v(-14.25, -6.14) * mm, "end": v(-13.37, -6.33) * mm});
            skArc(sketch, "E2547", {"start": v(18.06, -7.79) * mm, "mid": v(18.25, -7.22) * mm, "end": v(18, -6.67) * mm});
            skLineSegment(sketch, "E2548", {"start": v(-17.72, -6.8) * mm, "end": v(-17.35, -7.24) * mm});
            skLineSegment(sketch, "E2549", {"start": v(-84.77, -57.49) * mm, "end": v(-84.93, -57.4) * mm});
            skLineSegment(sketch, "E2550", {"start": v(69.08, 19.1) * mm, "end": v(69.1, 19.35) * mm});
            skLineSegment(sketch, "E2551", {"start": v(-53.3, -56.98) * mm, "end": v(-53.09, -56.79) * mm});
            skLineSegment(sketch, "E2552", {"start": v(-42.96, 2.51) * mm, "end": v(-43.19, 2.39) * mm});
            skLineSegment(sketch, "E2553", {"start": v(22.67, 18.78) * mm, "end": v(22.83, 19.67) * mm});
            skLineSegment(sketch, "E2554", {"start": v(88.78, 2.7) * mm, "end": v(88.93, 2.66) * mm});
            skLineSegment(sketch, "E2555", {"start": v(31.82, 17.29) * mm, "end": v(31.88, 17.5) * mm});
            skLineSegment(sketch, "E2556", {"start": v(74.97, -10.87) * mm, "end": v(75, -11.1) * mm});
            skLineSegment(sketch, "E2557", {"start": v(-42.73, 2.62) * mm, "end": v(-42.96, 2.51) * mm});
            skLineSegment(sketch, "E2558", {"start": v(22.65, 18.52) * mm, "end": v(22.67, 18.78) * mm});
            skLineSegment(sketch, "E2559", {"start": v(88.56, 2.72) * mm, "end": v(88.78, 2.7) * mm});
            skLineSegment(sketch, "E2560", {"start": v(31.64, 16.73) * mm, "end": v(31.82, 17.29) * mm});
            skLineSegment(sketch, "E2561", {"start": v(74.92, -10.3) * mm, "end": v(74.97, -10.87) * mm});
            skLineSegment(sketch, "E2562", {"start": v(-42.52, 2.7) * mm, "end": v(-42.73, 2.62) * mm});
            skLineSegment(sketch, "E2563", {"start": v(22.64, 18.27) * mm, "end": v(22.65, 18.52) * mm});
            skLineSegment(sketch, "E2564", {"start": v(87.98, 2.76) * mm, "end": v(88.56, 2.72) * mm});
            skArc(sketch, "E2565", {"start": v(31.64, 16.73) * mm, "mid": v(31.68, 16.13) * mm, "end": v(32.13, 15.72) * mm});
            skArc(sketch, "E2566", {"start": v(74.92, -10.3) * mm, "mid": v(74.65, -9.75) * mm, "end": v(74.09, -9.54) * mm});
            skLineSegment(sketch, "E2567", {"start": v(-73.5, -80.73) * mm, "end": v(-73.56, -80.9) * mm});
            skLineSegment(sketch, "E2568", {"start": v(59.57, -3.66) * mm, "end": v(59.4, -3.86) * mm});
            skLineSegment(sketch, "E2569", {"start": v(-73.37, -80.18) * mm, "end": v(-73.5, -80.73) * mm});
            skLineSegment(sketch, "E2570", {"start": v(59.73, -3.47) * mm, "end": v(59.57, -3.66) * mm});
            skArc(sketch, "E2571", {"start": v(-76.86, -82.93) * mm, "mid": v(-76.23, -83.18) * mm, "end": v(-75.59, -83.4) * mm});
            skLineSegment(sketch, "E2572", {"start": v(59.9, -3.31) * mm, "end": v(59.73, -3.47) * mm});
            skLineSegment(sketch, "E2573", {"start": v(-77, -81.91) * mm, "end": v(-76.86, -82.93) * mm});
            skLineSegment(sketch, "E2574", {"start": v(60.05, -3.17) * mm, "end": v(59.9, -3.31) * mm});
            skLineSegment(sketch, "E2575", {"start": v(-77.01, -80.99) * mm, "end": v(-77, -81.91) * mm});
            skLineSegment(sketch, "E2576", {"start": v(60.2, -3.06) * mm, "end": v(60.05, -3.17) * mm});
            skLineSegment(sketch, "E2577", {"start": v(-77, -80.68) * mm, "end": v(-77.01, -80.99) * mm});
            skLineSegment(sketch, "E2578", {"start": v(60.31, -2.97) * mm, "end": v(60.2, -3.06) * mm});
            skLineSegment(sketch, "E2579", {"start": v(-70.9, 75.88) * mm, "end": v(-70.91, 76.05) * mm});
            skLineSegment(sketch, "E2580", {"start": v(-76.96, -80.4) * mm, "end": v(-77, -80.68) * mm});
            skLineSegment(sketch, "E2581", {"start": v(60.51, -2.86) * mm, "end": v(60.31, -2.97) * mm});
            skLineSegment(sketch, "E2582", {"start": v(-70.89, 75.73) * mm, "end": v(-70.9, 75.88) * mm});
            skLineSegment(sketch, "E2583", {"start": v(-76.92, -80.14) * mm, "end": v(-76.96, -80.4) * mm});
            skLineSegment(sketch, "E2584", {"start": v(61.03, -2.6) * mm, "end": v(60.51, -2.86) * mm});
            skLineSegment(sketch, "E2585", {"start": v(-70.89, 75.62) * mm, "end": v(-70.89, 75.73) * mm});
            skLineSegment(sketch, "E2586", {"start": v(-76.87, -79.91) * mm, "end": v(-76.92, -80.14) * mm});
            skArc(sketch, "E2587", {"start": v(61.03, -2.6) * mm, "mid": v(61.43, -2.14) * mm, "end": v(61.4, -1.54) * mm});
            skLineSegment(sketch, "E2588", {"start": v(-70.92, 75.32) * mm, "end": v(-70.89, 75.62) * mm});
            skLineSegment(sketch, "E2589", {"start": v(-76.8, -79.72) * mm, "end": v(-76.87, -79.91) * mm});
            skArc(sketch, "E2590", {"start": v(61.13, -0.89) * mm, "mid": v(61.26, -1.22) * mm, "end": v(61.4, -1.54) * mm});
            skLineSegment(sketch, "E2591", {"start": v(-71, 74.74) * mm, "end": v(-70.92, 75.32) * mm});
            skArc(sketch, "E2592", {"start": v(-71, 74.74) * mm, "mid": v(-70.85, 74.15) * mm, "end": v(-70.34, 73.83) * mm});
            skArc(sketch, "E2593", {"start": v(-69.66, 73.67) * mm, "mid": v(-70, 73.75) * mm, "end": v(-70.34, 73.83) * mm});
            skArc(sketch, "E2594", {"start": v(-69.66, 73.67) * mm, "mid": v(-69.06, 73.75) * mm, "end": v(-68.67, 74.2) * mm});
            skLineSegment(sketch, "E2595", {"start": v(-67, 76.66) * mm, "end": v(-66.2, 77.23) * mm});
            skLineSegment(sketch, "E2596", {"start": v(-67.66, 76.07) * mm, "end": v(-67, 76.66) * mm});
            skLineSegment(sketch, "E2597", {"start": v(37.04, -8.41) * mm, "end": v(37.12, -8.54) * mm});
            skLineSegment(sketch, "E2598", {"start": v(40.5, 9.94) * mm, "end": v(40.7, 10.04) * mm});
            skLineSegment(sketch, "E2599", {"start": v(64.13, -7.4) * mm, "end": v(63.98, -7.58) * mm});
            skArc(sketch, "E2600", {"start": v(-82.76, -79.26) * mm, "mid": v(-82.24, -79.7) * mm, "end": v(-81.72, -80.13) * mm});
            skLineSegment(sketch, "E2601", {"start": v(57.73, 2.34) * mm, "end": v(57.5, 2.22) * mm});
            skLineSegment(sketch, "E2602", {"start": v(-26.96, 1.22) * mm, "end": v(-26.96, 1.02) * mm});
            skLineSegment(sketch, "E2603", {"start": v(37.12, -8.54) * mm, "end": v(37.2, -8.7) * mm});
            skLineSegment(sketch, "E2604", {"start": v(40.7, 10.04) * mm, "end": v(40.83, 10.13) * mm});
            skLineSegment(sketch, "E2605", {"start": v(63.98, -7.58) * mm, "end": v(63.9, -7.7) * mm});
            skLineSegment(sketch, "E2606", {"start": v(-78.53, -77.86) * mm, "end": v(-78.85, -78.33) * mm});
            skLineSegment(sketch, "E2607", {"start": v(57.5, 2.22) * mm, "end": v(56.74, 1.73) * mm});
            skLineSegment(sketch, "E2608", {"start": v(-25.5, 1.6) * mm, "end": v(-25.4, 1.43) * mm});
            skLineSegment(sketch, "E2609", {"start": v(37.2, -8.7) * mm, "end": v(37.3, -8.89) * mm});
            skLineSegment(sketch, "E2610", {"start": v(40.83, 10.13) * mm, "end": v(40.97, 10.24) * mm});
            skLineSegment(sketch, "E2611", {"start": v(63.9, -7.7) * mm, "end": v(63.82, -7.87) * mm});
            skLineSegment(sketch, "E2612", {"start": v(-78.85, -78.33) * mm, "end": v(-78.96, -78.48) * mm});
            skLineSegment(sketch, "E2613", {"start": v(56.74, 1.73) * mm, "end": v(55.96, 1.1) * mm});
            skLineSegment(sketch, "E2614", {"start": v(-24.44, 2.67) * mm, "end": v(-24.27, 2.57) * mm});
            skLineSegment(sketch, "E2615", {"start": v(37.3, -8.89) * mm, "end": v(37.38, -9.1) * mm});
            skLineSegment(sketch, "E2616", {"start": v(40.97, 10.24) * mm, "end": v(41.13, 10.38) * mm});
            skLineSegment(sketch, "E2617", {"start": v(63.82, -7.87) * mm, "end": v(63.73, -8.06) * mm});
            skLineSegment(sketch, "E2618", {"start": v(-78.96, -78.48) * mm, "end": v(-79.1, -78.62) * mm});
            skArc(sketch, "E2619", {"start": v(55.96, 1.1) * mm, "mid": v(56.08, 0.44) * mm, "end": v(56.22, -0.21) * mm});
            skLineSegment(sketch, "E2620", {"start": v(-24.06, 4.12) * mm, "end": v(-23.86, 4.12) * mm});
            skLineSegment(sketch, "E2621", {"start": v(37.38, -9.1) * mm, "end": v(37.47, -9.33) * mm});
            skLineSegment(sketch, "E2622", {"start": v(41.13, 10.38) * mm, "end": v(41.3, 10.55) * mm});
            skLineSegment(sketch, "E2623", {"start": v(63.73, -8.06) * mm, "end": v(63.64, -8.27) * mm});
            skLineSegment(sketch, "E2624", {"start": v(-79.1, -78.62) * mm, "end": v(-79.27, -78.78) * mm});
            skLineSegment(sketch, "E2625", {"start": v(60.12, -0.4) * mm, "end": v(59.57, -0.58) * mm});
            skLineSegment(sketch, "E2626", {"start": v(-24.44, 5.57) * mm, "end": v(-24.27, 5.67) * mm});
            skLineSegment(sketch, "E2627", {"start": v(37.47, -9.33) * mm, "end": v(37.54, -9.58) * mm});
            skLineSegment(sketch, "E2628", {"start": v(41.3, 10.55) * mm, "end": v(41.46, 10.73) * mm});
            skLineSegment(sketch, "E2629", {"start": v(63.64, -8.27) * mm, "end": v(63.56, -8.5) * mm});
            skLineSegment(sketch, "E2630", {"start": v(-79.27, -78.78) * mm, "end": v(-79.47, -78.95) * mm});
            skLineSegment(sketch, "E2631", {"start": v(59.57, -0.58) * mm, "end": v(59.35, -0.64) * mm});
            skLineSegment(sketch, "E2632", {"start": v(-25.5, 6.63) * mm, "end": v(-25.4, 6.8) * mm});
            skLineSegment(sketch, "E2633", {"start": v(37.54, -9.58) * mm, "end": v(37.74, -10.46) * mm});
            skLineSegment(sketch, "E2634", {"start": v(41.46, 10.73) * mm, "end": v(41.62, 10.93) * mm});
            skLineSegment(sketch, "E2635", {"start": v(63.56, -8.5) * mm, "end": v(63.48, -8.75) * mm});
            skLineSegment(sketch, "E2636", {"start": v(-79.47, -78.95) * mm, "end": v(-79.7, -79.12) * mm});
            skLineSegment(sketch, "E2637", {"start": v(59.35, -0.64) * mm, "end": v(59.2, -0.67) * mm});
            skArc(sketch, "E2638", {"start": v(-24.44, 5.57) * mm, "mid": v(-24.9, 6.17) * mm, "end": v(-25.5, 6.63) * mm});
            skLineSegment(sketch, "E2639", {"start": v(37.74, -10.46) * mm, "end": v(37.83, -11.47) * mm});
            skLineSegment(sketch, "E2640", {"start": v(41.62, 10.93) * mm, "end": v(42.14, 11.67) * mm});
            skLineSegment(sketch, "E2641", {"start": v(63.48, -8.75) * mm, "end": v(63.29, -9.63) * mm});
            skLineSegment(sketch, "E2642", {"start": v(-79.7, -79.12) * mm, "end": v(-79.95, -79.29) * mm});
            skLineSegment(sketch, "E2643", {"start": v(59.2, -0.67) * mm, "end": v(59.02, -0.69) * mm});
            skArc(sketch, "E2644", {"start": v(-23.86, 4.12) * mm, "mid": v(-23.96, 4.92) * mm, "end": v(-24.27, 5.67) * mm});
            skArc(sketch, "E2645", {"start": v(36.58, -6.67) * mm, "mid": v(36.33, -7.22) * mm, "end": v(36.52, -7.79) * mm});
            skLineSegment(sketch, "E2646", {"start": v(42.14, 11.67) * mm, "end": v(42.61, 12.56) * mm});
            skLineSegment(sketch, "E2647", {"start": v(63.29, -9.63) * mm, "end": v(63.19, -10.64) * mm});
            skLineSegment(sketch, "E2648", {"start": v(-79.95, -79.29) * mm, "end": v(-80.76, -79.74) * mm});
            skLineSegment(sketch, "E2649", {"start": v(59.02, -0.69) * mm, "end": v(58.81, -0.7) * mm});
            skArc(sketch, "E2650", {"start": v(-24.44, 2.67) * mm, "mid": v(-24.15, 3.37) * mm, "end": v(-24.06, 4.12) * mm});
            skArc(sketch, "E2651", {"start": v(36.58, -6.67) * mm, "mid": v(36.83, -6.42) * mm, "end": v(37.08, -6.17) * mm});
            skArc(sketch, "E2652", {"start": v(42.61, 12.56) * mm, "mid": v(42.25, 13.12) * mm, "end": v(41.87, 13.67) * mm});
            skArc(sketch, "E2653", {"start": v(63.19, -10.64) * mm, "mid": v(63.73, -11.02) * mm, "end": v(64.3, -11.37) * mm});
            skLineSegment(sketch, "E2654", {"start": v(-80.76, -79.74) * mm, "end": v(-81.72, -80.13) * mm});
            skLineSegment(sketch, "E2655", {"start": v(58.81, -0.7) * mm, "end": v(58.58, -0.7) * mm});
            skArc(sketch, "E2656", {"start": v(-25.4, 1.43) * mm, "mid": v(-24.76, 1.92) * mm, "end": v(-24.27, 2.57) * mm});
            skArc(sketch, "E2657", {"start": v(84.65, -5.28) * mm, "mid": v(84.07, -5.09) * mm, "end": v(83.53, -5.34) * mm});
            skLineSegment(sketch, "E2658", {"start": v(38.2, 12.35) * mm, "end": v(38.64, 12.73) * mm});
            skLineSegment(sketch, "E2659", {"start": v(67.19, -8.75) * mm, "end": v(66.92, -9.27) * mm});
            skArc(sketch, "E2660", {"start": v(-77.44, -77.63) * mm, "mid": v(-78.03, -77.53) * mm, "end": v(-78.53, -77.86) * mm});
            skLineSegment(sketch, "E2661", {"start": v(58.58, -0.7) * mm, "end": v(58.34, -0.69) * mm});
            skArc(sketch, "E2662", {"start": v(-26.96, 1.22) * mm, "mid": v(-26.2, 1.32) * mm, "end": v(-25.5, 1.6) * mm});
            skLineSegment(sketch, "E2663", {"start": v(84.65, -5.28) * mm, "end": v(85.09, -5.66) * mm});
            skLineSegment(sketch, "E2664", {"start": v(38.64, 12.73) * mm, "end": v(38.82, 12.87) * mm});
            skLineSegment(sketch, "E2665", {"start": v(66.92, -9.27) * mm, "end": v(66.81, -9.47) * mm});
            skArc(sketch, "E2666", {"start": v(-77.44, -77.63) * mm, "mid": v(-77.14, -77.8) * mm, "end": v(-76.83, -77.98) * mm});
            skLineSegment(sketch, "E2667", {"start": v(58.34, -0.69) * mm, "end": v(58.08, -0.66) * mm});
            skArc(sketch, "E2668", {"start": v(-28.5, 1.43) * mm, "mid": v(-27.76, 1.12) * mm, "end": v(-26.96, 1.02) * mm});
            skLineSegment(sketch, "E2669", {"start": v(85.09, -5.66) * mm, "end": v(85.27, -5.8) * mm});
            skLineSegment(sketch, "E2670", {"start": v(38.82, 12.87) * mm, "end": v(38.94, 12.95) * mm});
            skLineSegment(sketch, "E2671", {"start": v(66.81, -9.47) * mm, "end": v(66.73, -9.6) * mm});
            skArc(sketch, "E2672", {"start": v(-76.5, -79.04) * mm, "mid": v(-76.45, -78.44) * mm, "end": v(-76.83, -77.98) * mm});
            skLineSegment(sketch, "E2673", {"start": v(58.08, -0.66) * mm, "end": v(57.19, -0.5) * mm});
            skArc(sketch, "E2674", {"start": v(-30.06, 4.12) * mm, "mid": v(-29.95, 3.31) * mm, "end": v(-29.64, 2.57) * mm});
            skLineSegment(sketch, "E2675", {"start": v(85.27, -5.8) * mm, "end": v(85.4, -5.88) * mm});
            skLineSegment(sketch, "E2676", {"start": v(38.94, 12.95) * mm, "end": v(39.1, 13.04) * mm});
            skLineSegment(sketch, "E2677", {"start": v(66.73, -9.6) * mm, "end": v(66.61, -9.73) * mm});
            skLineSegment(sketch, "E2678", {"start": v(-76.5, -79.04) * mm, "end": v(-76.74, -79.55) * mm});
            skLineSegment(sketch, "E2679", {"start": v(57.19, -0.5) * mm, "end": v(56.22, -0.21) * mm});
            skArc(sketch, "E2680", {"start": v(-28.5, 6.8) * mm, "mid": v(-29.15, 6.3) * mm, "end": v(-29.64, 5.67) * mm});
            skLineSegment(sketch, "E2681", {"start": v(85.4, -5.88) * mm, "end": v(85.55, -5.97) * mm});
            skLineSegment(sketch, "E2682", {"start": v(39.1, 13.04) * mm, "end": v(39.3, 13.13) * mm});
            skLineSegment(sketch, "E2683", {"start": v(66.61, -9.73) * mm, "end": v(66.47, -9.89) * mm});
            skLineSegment(sketch, "E2684", {"start": v(-76.74, -79.55) * mm, "end": v(-76.8, -79.72) * mm});
            skArc(sketch, "E2685", {"start": v(61.13, -0.89) * mm, "mid": v(60.72, -0.44) * mm, "end": v(60.12, -0.4) * mm});
            skArc(sketch, "E2686", {"start": v(-29.47, 5.57) * mm, "mid": v(-29.76, 4.87) * mm, "end": v(-29.86, 4.12) * mm});
            skLineSegment(sketch, "E2687", {"start": v(85.55, -5.97) * mm, "end": v(85.74, -6.06) * mm});
            skLineSegment(sketch, "E2688", {"start": v(39.3, 13.13) * mm, "end": v(39.5, 13.22) * mm});
            skLineSegment(sketch, "E2689", {"start": v(66.47, -9.89) * mm, "end": v(66.3, -10.05) * mm});
            skLineSegment(sketch, "E2690", {"start": v(85.74, -6.06) * mm, "end": v(85.95, -6.14) * mm});
            skLineSegment(sketch, "E2691", {"start": v(39.5, 13.22) * mm, "end": v(39.74, 13.3) * mm});
            skLineSegment(sketch, "E2692", {"start": v(66.3, -10.05) * mm, "end": v(66.13, -10.22) * mm});
            skLineSegment(sketch, "E2693", {"start": v(85.95, -6.14) * mm, "end": v(86.19, -6.23) * mm});
            skLineSegment(sketch, "E2694", {"start": v(39.74, 13.3) * mm, "end": v(39.99, 13.38) * mm});
            skLineSegment(sketch, "E2695", {"start": v(66.13, -10.22) * mm, "end": v(65.93, -10.38) * mm});
            skLineSegment(sketch, "E2696", {"start": v(86.19, -6.23) * mm, "end": v(86.44, -6.3) * mm});
            skLineSegment(sketch, "E2697", {"start": v(39.99, 13.38) * mm, "end": v(40.87, 13.57) * mm});
            skLineSegment(sketch, "E2698", {"start": v(65.93, -10.38) * mm, "end": v(65.18, -10.9) * mm});
            skLineSegment(sketch, "E2699", {"start": v(86.44, -6.3) * mm, "end": v(87.32, -6.5) * mm});
            skLineSegment(sketch, "E2700", {"start": v(40.87, 13.57) * mm, "end": v(41.87, 13.67) * mm});
            skLineSegment(sketch, "E2701", {"start": v(65.18, -10.9) * mm, "end": v(64.3, -11.37) * mm});
            skLineSegment(sketch, "E2702", {"start": v(87.32, -6.5) * mm, "end": v(88.32, -6.6) * mm});
            skArc(sketch, "E2703", {"start": v(37.08, 12.41) * mm, "mid": v(37.63, 12.16) * mm, "end": v(38.2, 12.35) * mm});
            skArc(sketch, "E2704", {"start": v(68.24, -8.38) * mm, "mid": v(67.64, -8.36) * mm, "end": v(67.19, -8.75) * mm});
            skArc(sketch, "E2705", {"start": v(88.32, -6.6) * mm, "mid": v(88.7, -6.05) * mm, "end": v(89.06, -5.49) * mm});
            skArc(sketch, "E2706", {"start": v(37.08, 12.41) * mm, "mid": v(36.83, 12.67) * mm, "end": v(36.58, 12.91) * mm});
            skArc(sketch, "E2707", {"start": v(68.24, -8.38) * mm, "mid": v(68.57, -8.52) * mm, "end": v(68.9, -8.65) * mm});
            skLineSegment(sketch, "E2708", {"start": v(86.44, -2.6) * mm, "end": v(86.96, -2.86) * mm});
            skArc(sketch, "E2709", {"start": v(36.52, 14.03) * mm, "mid": v(36.33, 13.46) * mm, "end": v(36.58, 12.91) * mm});
            skArc(sketch, "E2710", {"start": v(69.38, -9.66) * mm, "mid": v(69.34, -9.06) * mm, "end": v(68.9, -8.65) * mm});
            skLineSegment(sketch, "E2711", {"start": v(86.96, -2.86) * mm, "end": v(87.16, -2.97) * mm});
            skLineSegment(sketch, "E2712", {"start": v(36.52, 14.03) * mm, "end": v(36.9, 14.48) * mm});
            skLineSegment(sketch, "E2713", {"start": v(69.38, -9.66) * mm, "end": v(69.2, -10.22) * mm});
            skLineSegment(sketch, "E2714", {"start": v(87.16, -2.97) * mm, "end": v(87.28, -3.06) * mm});
            skLineSegment(sketch, "E2715", {"start": v(36.9, 14.48) * mm, "end": v(37.04, 14.65) * mm});
            skLineSegment(sketch, "E2716", {"start": v(69.2, -10.22) * mm, "end": v(69.14, -10.43) * mm});
            skLineSegment(sketch, "E2717", {"start": v(87.28, -3.06) * mm, "end": v(87.42, -3.17) * mm});
            skLineSegment(sketch, "E2718", {"start": v(37.04, 14.65) * mm, "end": v(37.12, 14.78) * mm});
            skLineSegment(sketch, "E2719", {"start": v(69.14, -10.43) * mm, "end": v(69.11, -10.58) * mm});
            skLineSegment(sketch, "E2720", {"start": v(87.42, -3.17) * mm, "end": v(87.58, -3.31) * mm});
            skLineSegment(sketch, "E2721", {"start": v(37.12, 14.78) * mm, "end": v(37.2, 14.94) * mm});
            skLineSegment(sketch, "E2722", {"start": v(69.11, -10.58) * mm, "end": v(69.1, -10.76) * mm});
            skLineSegment(sketch, "E2723", {"start": v(87.58, -3.31) * mm, "end": v(87.74, -3.47) * mm});
            skLineSegment(sketch, "E2724", {"start": v(37.2, 14.94) * mm, "end": v(37.3, 15.13) * mm});
            skLineSegment(sketch, "E2725", {"start": v(69.1, -10.76) * mm, "end": v(69.08, -10.97) * mm});
            skLineSegment(sketch, "E2726", {"start": v(87.74, -3.47) * mm, "end": v(87.9, -3.66) * mm});
            skLineSegment(sketch, "E2727", {"start": v(37.3, 15.13) * mm, "end": v(37.38, 15.34) * mm});
            skLineSegment(sketch, "E2728", {"start": v(69.08, -10.97) * mm, "end": v(69.08, -11.2) * mm});
            skLineSegment(sketch, "E2729", {"start": v(87.9, -3.66) * mm, "end": v(88.07, -3.86) * mm});
            skLineSegment(sketch, "E2730", {"start": v(37.38, 15.34) * mm, "end": v(37.47, 15.57) * mm});
            skLineSegment(sketch, "E2731", {"start": v(69.08, -11.2) * mm, "end": v(69.1, -11.45) * mm});
            skLineSegment(sketch, "E2732", {"start": v(88.07, -3.86) * mm, "end": v(88.59, -4.6) * mm});
            skLineSegment(sketch, "E2733", {"start": v(37.47, 15.57) * mm, "end": v(37.54, 15.82) * mm});
            skLineSegment(sketch, "E2734", {"start": v(69.1, -11.45) * mm, "end": v(69.12, -11.7) * mm});
            skLineSegment(sketch, "E2735", {"start": v(88.59, -4.6) * mm, "end": v(89.06, -5.49) * mm});
            skLineSegment(sketch, "E2736", {"start": v(37.54, 15.82) * mm, "end": v(37.74, 16.7) * mm});
            skLineSegment(sketch, "E2737", {"start": v(69.12, -11.7) * mm, "end": v(69.28, -12.6) * mm});
            skArc(sketch, "E2738", {"start": v(86.07, -1.54) * mm, "mid": v(86.04, -2.14) * mm, "end": v(86.44, -2.6) * mm});
            skLineSegment(sketch, "E2739", {"start": v(37.74, 16.7) * mm, "end": v(37.83, 17.7) * mm});
            skLineSegment(sketch, "E2740", {"start": v(69.28, -12.6) * mm, "end": v(69.57, -13.56) * mm});
            skArc(sketch, "E2741", {"start": v(86.07, -1.54) * mm, "mid": v(86.2, -1.22) * mm, "end": v(86.34, -0.89) * mm});
            skArc(sketch, "E2742", {"start": v(37.83, 17.7) * mm, "mid": v(37.29, 18.09) * mm, "end": v(36.73, 18.45) * mm});
            skArc(sketch, "E2743", {"start": v(69.57, -13.56) * mm, "mid": v(70.22, -13.7) * mm, "end": v(70.88, -13.82) * mm});
            skArc(sketch, "E2744", {"start": v(87.35, -0.4) * mm, "mid": v(86.75, -0.44) * mm, "end": v(86.34, -0.89) * mm});
            skLineSegment(sketch, "E2745", {"start": v(33.83, 15.83) * mm, "end": v(34.1, 16.34) * mm});
            skLineSegment(sketch, "E2746", {"start": v(72.55, -10.3) * mm, "end": v(72.5, -10.87) * mm});
            skLineSegment(sketch, "E2747", {"start": v(87.35, -0.4) * mm, "end": v(87.9, -0.58) * mm});
            skLineSegment(sketch, "E2748", {"start": v(34.1, 16.34) * mm, "end": v(34.21, 16.54) * mm});
            skLineSegment(sketch, "E2749", {"start": v(72.5, -10.87) * mm, "end": v(72.47, -11.1) * mm});
            skLineSegment(sketch, "E2750", {"start": v(87.9, -0.58) * mm, "end": v(88.12, -0.64) * mm});
            skLineSegment(sketch, "E2751", {"start": v(34.21, 16.54) * mm, "end": v(34.3, 16.66) * mm});
            skLineSegment(sketch, "E2752", {"start": v(72.47, -11.1) * mm, "end": v(72.44, -11.24) * mm});
            skLineSegment(sketch, "E2753", {"start": v(88.12, -0.64) * mm, "end": v(88.27, -0.67) * mm});
            skLineSegment(sketch, "E2754", {"start": v(34.3, 16.66) * mm, "end": v(34.41, 16.8) * mm});
            skLineSegment(sketch, "E2755", {"start": v(72.44, -11.24) * mm, "end": v(72.4, -11.42) * mm});
            skLineSegment(sketch, "E2756", {"start": v(88.27, -0.67) * mm, "end": v(88.45, -0.69) * mm});
            skLineSegment(sketch, "E2757", {"start": v(34.41, 16.8) * mm, "end": v(34.55, 16.96) * mm});
            skLineSegment(sketch, "E2758", {"start": v(72.4, -11.42) * mm, "end": v(72.32, -11.62) * mm});
            skLineSegment(sketch, "E2759", {"start": v(88.45, -0.69) * mm, "end": v(88.66, -0.7) * mm});
            skLineSegment(sketch, "E2760", {"start": v(34.55, 16.96) * mm, "end": v(34.71, 17.12) * mm});
            skLineSegment(sketch, "E2761", {"start": v(72.32, -11.62) * mm, "end": v(72.23, -11.83) * mm});
            skLineSegment(sketch, "E2762", {"start": v(88.66, -0.7) * mm, "end": v(88.89, -0.7) * mm});
            skLineSegment(sketch, "E2763", {"start": v(34.71, 17.12) * mm, "end": v(34.9, 17.3) * mm});
            skLineSegment(sketch, "E2764", {"start": v(72.23, -11.83) * mm, "end": v(72.13, -12.05) * mm});
            skLineSegment(sketch, "E2765", {"start": v(88.89, -0.7) * mm, "end": v(89.13, -0.69) * mm});
            skLineSegment(sketch, "E2766", {"start": v(34.9, 17.3) * mm, "end": v(35.1, 17.46) * mm});
            skLineSegment(sketch, "E2767", {"start": v(72.13, -12.05) * mm, "end": v(72, -12.28) * mm});
            skLineSegment(sketch, "E2768", {"start": v(89.13, -0.69) * mm, "end": v(89.4, -0.66) * mm});
            skLineSegment(sketch, "E2769", {"start": v(35.1, 17.46) * mm, "end": v(35.84, 17.97) * mm});
            skLineSegment(sketch, "E2770", {"start": v(72, -12.28) * mm, "end": v(71.52, -13.04) * mm});
            skLineSegment(sketch, "E2771", {"start": v(89.4, -0.66) * mm, "end": v(90.28, -0.5) * mm});
            skLineSegment(sketch, "E2772", {"start": v(35.84, 17.97) * mm, "end": v(36.73, 18.45) * mm});
            skLineSegment(sketch, "E2773", {"start": v(71.52, -13.04) * mm, "end": v(70.88, -13.82) * mm});
            skLineSegment(sketch, "E2774", {"start": v(90.28, -0.5) * mm, "end": v(91.25, -0.21) * mm});
            skArc(sketch, "E2775", {"start": v(32.78, 15.45) * mm, "mid": v(33.38, 15.43) * mm, "end": v(33.83, 15.83) * mm});
            skArc(sketch, "E2776", {"start": v(73.38, -9.54) * mm, "mid": v(72.82, -9.75) * mm, "end": v(72.55, -10.3) * mm});
            skArc(sketch, "E2777", {"start": v(91.25, -0.21) * mm, "mid": v(91.39, 0.44) * mm, "end": v(91.5, 1.1) * mm});
            skArc(sketch, "E2778", {"start": v(32.78, 15.45) * mm, "mid": v(32.45, 15.6) * mm, "end": v(32.13, 15.72) * mm});
            skArc(sketch, "E2779", {"start": v(73.38, -9.54) * mm, "mid": v(73.73, -9.55) * mm, "end": v(74.09, -9.54) * mm});
            skCircle(sketch, "E2780", {"center": v(27.29, 3.12) * mm, "radius": 3.1 * mm});
            skLineSegment(sketch, "E2781", {"start": v(-87.58, -66.08) * mm, "end": v(-88.37, -66.56) * mm});
            skLineSegment(sketch, "E2782", {"start": v(60.15, 14.4) * mm, "end": v(59.15, 14.5) * mm});
            skArc(sketch, "E2783", {"start": v(-71.35, 61.84) * mm, "mid": v(-71.16, 62.54) * mm, "end": v(-71.35, 63.24) * mm});
            skLineSegment(sketch, "E2784", {"start": v(-88.37, -66.56) * mm, "end": v(-89.2, -67.18) * mm});
            skArc(sketch, "E2785", {"start": v(59.15, 14.5) * mm, "mid": v(58.77, 13.95) * mm, "end": v(58.4, 13.4) * mm});
            skArc(sketch, "E2786", {"start": v(-73.77, 61.84) * mm, "mid": v(-73.26, 61.33) * mm, "end": v(-72.56, 61.14) * mm});
            skArc(sketch, "E2787", {"start": v(-89.2, -67.18) * mm, "mid": v(-89.08, -67.86) * mm, "end": v(-88.95, -68.52) * mm});
            skLineSegment(sketch, "E2788", {"start": v(61.03, 10.5) * mm, "end": v(60.51, 10.76) * mm});
            skArc(sketch, "E2789", {"start": v(-71.17, 63.34) * mm, "mid": v(-71.76, 63.93) * mm, "end": v(-72.56, 64.14) * mm});
            skLineSegment(sketch, "E2790", {"start": v(-85.05, -68.83) * mm, "end": v(-85.6, -68.99) * mm});
            skLineSegment(sketch, "E2791", {"start": v(60.51, 10.76) * mm, "end": v(60.31, 10.87) * mm});
            skArc(sketch, "E2792", {"start": v(-73.94, 63.34) * mm, "mid": v(-74.16, 62.54) * mm, "end": v(-73.94, 61.74) * mm});
            skLineSegment(sketch, "E2793", {"start": v(-85.6, -68.99) * mm, "end": v(-85.78, -69.03) * mm});
            skLineSegment(sketch, "E2794", {"start": v(60.31, 10.87) * mm, "end": v(60.2, 10.96) * mm});
            skLineSegment(sketch, "E2795", {"start": v(-85.78, -69.03) * mm, "end": v(-85.98, -69.05) * mm});
            skLineSegment(sketch, "E2796", {"start": v(60.2, 10.96) * mm, "end": v(60.05, 11.07) * mm});
            skLineSegment(sketch, "E2797", {"start": v(-85.98, -69.05) * mm, "end": v(-86.21, -69.06) * mm});
            skLineSegment(sketch, "E2798", {"start": v(60.05, 11.07) * mm, "end": v(59.9, 11.21) * mm});
            skLineSegment(sketch, "E2799", {"start": v(-86.21, -69.06) * mm, "end": v(-86.47, -69.06) * mm});
            skLineSegment(sketch, "E2800", {"start": v(59.9, 11.21) * mm, "end": v(59.73, 11.38) * mm});
            skLineSegment(sketch, "E2801", {"start": v(-86.47, -69.06) * mm, "end": v(-86.76, -69.04) * mm});
            skLineSegment(sketch, "E2802", {"start": v(59.73, 11.38) * mm, "end": v(59.57, 11.56) * mm});
            skLineSegment(sketch, "E2803", {"start": v(-86.76, -69.04) * mm, "end": v(-87.06, -69.01) * mm});
            skLineSegment(sketch, "E2804", {"start": v(59.57, 11.56) * mm, "end": v(59.4, 11.76) * mm});
            skLineSegment(sketch, "E2805", {"start": v(-87.06, -69.01) * mm, "end": v(-87.97, -68.83) * mm});
            skLineSegment(sketch, "E2806", {"start": v(59.4, 11.76) * mm, "end": v(58.88, 12.5) * mm});
            skLineSegment(sketch, "E2807", {"start": v(-87.97, -68.83) * mm, "end": v(-88.95, -68.52) * mm});
            skLineSegment(sketch, "E2808", {"start": v(58.88, 12.5) * mm, "end": v(58.4, 13.4) * mm});
            skArc(sketch, "E2809", {"start": v(-84.07, -69.35) * mm, "mid": v(-84.46, -68.9) * mm, "end": v(-85.05, -68.83) * mm});
            skArc(sketch, "E2810", {"start": v(61.4, 9.44) * mm, "mid": v(61.43, 10.04) * mm, "end": v(61.03, 10.5) * mm});
            skArc(sketch, "E2811", {"start": v(-84.07, -69.35) * mm, "mid": v(-83.95, -69.68) * mm, "end": v(-83.83, -70.02) * mm});
            skArc(sketch, "E2812", {"start": v(61.4, 9.44) * mm, "mid": v(61.26, 9.12) * mm, "end": v(61.13, 8.79) * mm});
            skArc(sketch, "E2813", {"start": v(-84.25, -71.04) * mm, "mid": v(-83.83, -70.61) * mm, "end": v(-83.83, -70.02) * mm});
            skArc(sketch, "E2814", {"start": v(60.12, 8.3) * mm, "mid": v(60.72, 8.35) * mm, "end": v(61.13, 8.79) * mm});
            skArc(sketch, "E2815", {"start": v(-66.09, -58.67) * mm, "mid": v(-67.68, -58) * mm, "end": v(-69.39, -57.78) * mm});
            skLineSegment(sketch, "E2816", {"start": v(-84.25, -71.04) * mm, "end": v(-84.77, -71.28) * mm});
            skLineSegment(sketch, "E2817", {"start": v(60.12, 8.3) * mm, "end": v(59.57, 8.48) * mm});
            skArc(sketch, "E2818", {"start": v(-69.39, -57.98) * mm, "mid": v(-71.04, -58.2) * mm, "end": v(-72.59, -58.84) * mm});
            skLineSegment(sketch, "E2819", {"start": v(-84.77, -71.28) * mm, "end": v(-84.93, -71.36) * mm});
            skLineSegment(sketch, "E2820", {"start": v(59.57, 8.48) * mm, "end": v(59.35, 8.55) * mm});
            skLineSegment(sketch, "E2821", {"start": v(-69.39, -57.98) * mm, "end": v(-69.39, -57.78) * mm});
            skLineSegment(sketch, "E2822", {"start": v(-84.93, -71.36) * mm, "end": v(-85.1, -71.47) * mm});
            skLineSegment(sketch, "E2823", {"start": v(59.35, 8.55) * mm, "end": v(59.2, 8.57) * mm});
            skLineSegment(sketch, "E2824", {"start": v(-72.59, -58.84) * mm, "end": v(-72.69, -58.67) * mm});
            skLineSegment(sketch, "E2825", {"start": v(-85.1, -71.47) * mm, "end": v(-85.28, -71.61) * mm});
            skLineSegment(sketch, "E2826", {"start": v(59.2, 8.57) * mm, "end": v(59.02, 8.6) * mm});
            skLineSegment(sketch, "E2827", {"start": v(-74.93, -61.18) * mm, "end": v(-75.1, -61.08) * mm});
            skLineSegment(sketch, "E2828", {"start": v(-85.28, -71.61) * mm, "end": v(-85.48, -71.78) * mm});
            skLineSegment(sketch, "E2829", {"start": v(59.02, 8.6) * mm, "end": v(58.81, 8.6) * mm});
            skLineSegment(sketch, "E2830", {"start": v(-75.79, -64.38) * mm, "end": v(-75.99, -64.38) * mm});
            skLineSegment(sketch, "E2831", {"start": v(-85.48, -71.78) * mm, "end": v(-85.7, -71.98) * mm});
            skLineSegment(sketch, "E2832", {"start": v(58.81, 8.6) * mm, "end": v(58.58, 8.6) * mm});
            skLineSegment(sketch, "E2833", {"start": v(-74.93, -67.58) * mm, "end": v(-75.1, -67.68) * mm});
            skLineSegment(sketch, "E2834", {"start": v(-85.7, -71.98) * mm, "end": v(-85.9, -72.2) * mm});
            skLineSegment(sketch, "E2835", {"start": v(58.58, 8.6) * mm, "end": v(58.34, 8.6) * mm});
            skLineSegment(sketch, "E2836", {"start": v(-72.59, -69.93) * mm, "end": v(-72.69, -70.1) * mm});
            skLineSegment(sketch, "E2837", {"start": v(-85.9, -72.2) * mm, "end": v(-86.48, -72.92) * mm});
            skLineSegment(sketch, "E2838", {"start": v(58.34, 8.6) * mm, "end": v(58.08, 8.57) * mm});
            skLineSegment(sketch, "E2839", {"start": v(-69.39, -70.78) * mm, "end": v(-69.39, -70.98) * mm});
            skLineSegment(sketch, "E2840", {"start": v(-86.48, -72.92) * mm, "end": v(-87.04, -73.79) * mm});
            skLineSegment(sketch, "E2841", {"start": v(58.08, 8.57) * mm, "end": v(57.19, 8.4) * mm});
            skLineSegment(sketch, "E2842", {"start": v(-66.19, -69.93) * mm, "end": v(-66.09, -70.1) * mm});
            skArc(sketch, "E2843", {"start": v(-87.04, -73.79) * mm, "mid": v(-86.7, -74.38) * mm, "end": v(-86.36, -74.97) * mm});
            skLineSegment(sketch, "E2844", {"start": v(57.19, 8.4) * mm, "end": v(56.22, 8.11) * mm});
            skLineSegment(sketch, "E2845", {"start": v(-63.85, -67.58) * mm, "end": v(-63.67, -67.68) * mm});
            skLineSegment(sketch, "E2846", {"start": v(-82.59, -73.92) * mm, "end": v(-83.05, -74.26) * mm});
            skArc(sketch, "E2847", {"start": v(56.22, 8.11) * mm, "mid": v(56.08, 7.46) * mm, "end": v(55.96, 6.8) * mm});
            skLineSegment(sketch, "E2848", {"start": v(-62.99, -64.38) * mm, "end": v(-62.79, -64.38) * mm});
            skLineSegment(sketch, "E2849", {"start": v(-83.05, -74.26) * mm, "end": v(-83.2, -74.35) * mm});
            skLineSegment(sketch, "E2850", {"start": v(59.5, 5.14) * mm, "end": v(58.91, 5.19) * mm});
            skLineSegment(sketch, "E2851", {"start": v(-63.85, -61.18) * mm, "end": v(-63.67, -61.08) * mm});
            skLineSegment(sketch, "E2852", {"start": v(-83.2, -74.35) * mm, "end": v(-83.38, -74.44) * mm});
            skLineSegment(sketch, "E2853", {"start": v(58.91, 5.19) * mm, "end": v(58.69, 5.21) * mm});
            skLineSegment(sketch, "E2854", {"start": v(-66.19, -58.84) * mm, "end": v(-66.09, -58.67) * mm});
            skLineSegment(sketch, "E2855", {"start": v(-83.38, -74.44) * mm, "end": v(-83.6, -74.53) * mm});
            skLineSegment(sketch, "E2856", {"start": v(58.69, 5.21) * mm, "end": v(58.54, 5.24) * mm});
            skArc(sketch, "E2857", {"start": v(-63.85, -61.18) * mm, "mid": v(-64.86, -59.86) * mm, "end": v(-66.19, -58.84) * mm});
            skLineSegment(sketch, "E2858", {"start": v(58.54, 5.24) * mm, "end": v(58.37, 5.3) * mm});
            skLineSegment(sketch, "E2859", {"start": v(-83.6, -74.53) * mm, "end": v(-83.84, -74.62) * mm});
            skArc(sketch, "E2860", {"start": v(-62.79, -64.38) * mm, "mid": v(-63.01, -62.68) * mm, "end": v(-63.67, -61.08) * mm});
            skLineSegment(sketch, "E2861", {"start": v(58.37, 5.3) * mm, "end": v(58.17, 5.36) * mm});
            skLineSegment(sketch, "E2862", {"start": v(-83.84, -74.62) * mm, "end": v(-84.12, -74.7) * mm});
            skArc(sketch, "E2863", {"start": v(-63.85, -67.58) * mm, "mid": v(-63.2, -66.04) * mm, "end": v(-62.99, -64.38) * mm});
            skLineSegment(sketch, "E2864", {"start": v(58.17, 5.36) * mm, "end": v(57.96, 5.45) * mm});
            skLineSegment(sketch, "E2865", {"start": v(-84.12, -74.7) * mm, "end": v(-84.41, -74.78) * mm});
            skArc(sketch, "E2866", {"start": v(-66.09, -70.1) * mm, "mid": v(-64.72, -69.05) * mm, "end": v(-63.67, -67.68) * mm});
            skLineSegment(sketch, "E2867", {"start": v(-84.41, -74.78) * mm, "end": v(-85.33, -74.92) * mm});
            skLineSegment(sketch, "E2868", {"start": v(57.96, 5.45) * mm, "end": v(57.73, 5.56) * mm});
            skArc(sketch, "E2869", {"start": v(-69.39, -70.78) * mm, "mid": v(-67.73, -70.57) * mm, "end": v(-66.19, -69.93) * mm});
            skLineSegment(sketch, "E2870", {"start": v(-85.33, -74.92) * mm, "end": v(-86.36, -74.97) * mm});
            skLineSegment(sketch, "E2871", {"start": v(57.73, 5.56) * mm, "end": v(57.5, 5.68) * mm});
            skArc(sketch, "E2872", {"start": v(-72.69, -70.1) * mm, "mid": v(-71.1, -70.76) * mm, "end": v(-69.39, -70.98) * mm});
            skArc(sketch, "E2873", {"start": v(-81.49, -74.07) * mm, "mid": v(-82, -73.78) * mm, "end": v(-82.59, -73.92) * mm});
            skLineSegment(sketch, "E2874", {"start": v(57.5, 5.68) * mm, "end": v(56.74, 6.17) * mm});
            skArc(sketch, "E2875", {"start": v(-75.99, -64.38) * mm, "mid": v(-75.76, -66.1) * mm, "end": v(-75.1, -67.68) * mm});
            skArc(sketch, "E2876", {"start": v(-81.49, -74.07) * mm, "mid": v(-81.26, -74.35) * mm, "end": v(-81.03, -74.62) * mm});
            skLineSegment(sketch, "E2877", {"start": v(56.74, 6.17) * mm, "end": v(55.96, 6.8) * mm});
            skArc(sketch, "E2878", {"start": v(-72.69, -58.67) * mm, "mid": v(-74.05, -59.72) * mm, "end": v(-75.1, -61.08) * mm});
            skArc(sketch, "E2879", {"start": v(-81.08, -75.72) * mm, "mid": v(-80.83, -75.18) * mm, "end": v(-81.03, -74.62) * mm});
            skArc(sketch, "E2880", {"start": v(60.24, 4.3) * mm, "mid": v(60.03, 4.87) * mm, "end": v(59.5, 5.14) * mm});
            skArc(sketch, "E2881", {"start": v(-74.93, -61.18) * mm, "mid": v(-75.57, -62.73) * mm, "end": v(-75.79, -64.38) * mm});
            skLineSegment(sketch, "E2882", {"start": v(-81.08, -75.72) * mm, "end": v(-81.48, -76.12) * mm});
            skArc(sketch, "E2883", {"start": v(60.24, 4.3) * mm, "mid": v(60.23, 3.95) * mm, "end": v(60.24, 3.6) * mm});
            skArc(sketch, "E2884", {"start": v(-74.93, -67.58) * mm, "mid": v(-73.91, -68.9) * mm, "end": v(-72.59, -69.93) * mm});
            skLineSegment(sketch, "E2885", {"start": v(-81.48, -76.12) * mm, "end": v(-81.6, -76.26) * mm});
            skArc(sketch, "E2886", {"start": v(59.5, 2.76) * mm, "mid": v(60.03, 3.03) * mm, "end": v(60.24, 3.6) * mm});
            skArc(sketch, "E2887", {"start": v(-25.4, 6.8) * mm, "mid": v(-26.15, 7.11) * mm, "end": v(-26.96, 7.22) * mm});
            skLineSegment(sketch, "E2888", {"start": v(-74.22, -46.76) * mm, "end": v(-74.83, -46.06) * mm});
            skLineSegment(sketch, "E2889", {"start": v(81.16, 17.95) * mm, "end": v(81.34, 18.12) * mm});
            skCircle(sketch, "E2890", {"center": v(73.73, 3.95) * mm, "radius": 3.1 * mm});
            skLineSegment(sketch, "E2891", {"start": v(-81.6, -76.26) * mm, "end": v(-81.73, -76.42) * mm});
            skLineSegment(sketch, "E2892", {"start": v(59.5, 2.76) * mm, "end": v(58.91, 2.72) * mm});
            skArc(sketch, "E2893", {"start": v(-26.96, 7.02) * mm, "mid": v(-27.7, 6.92) * mm, "end": v(-28.4, 6.63) * mm});
            skLineSegment(sketch, "E2894", {"start": v(-81.73, -76.42) * mm, "end": v(-81.85, -76.61) * mm});
            skLineSegment(sketch, "E2895", {"start": v(58.91, 2.72) * mm, "end": v(58.69, 2.7) * mm});
            skLineSegment(sketch, "E2896", {"start": v(-26.96, 7.02) * mm, "end": v(-26.96, 7.22) * mm});
            skLineSegment(sketch, "E2897", {"start": v(-81.85, -76.61) * mm, "end": v(-81.98, -76.84) * mm});
            skLineSegment(sketch, "E2898", {"start": v(58.69, 2.7) * mm, "end": v(58.54, 2.66) * mm});
            skLineSegment(sketch, "E2899", {"start": v(-28.4, 6.63) * mm, "end": v(-28.5, 6.8) * mm});
            skLineSegment(sketch, "E2900", {"start": v(-81.98, -76.84) * mm, "end": v(-82.1, -77.1) * mm});
            skLineSegment(sketch, "E2901", {"start": v(58.54, 2.66) * mm, "end": v(58.37, 2.6) * mm});
            skLineSegment(sketch, "E2902", {"start": v(-29.47, 5.57) * mm, "end": v(-29.64, 5.67) * mm});
            skLineSegment(sketch, "E2903", {"start": v(-82.1, -77.1) * mm, "end": v(-82.23, -77.38) * mm});
            skLineSegment(sketch, "E2904", {"start": v(58.37, 2.6) * mm, "end": v(58.17, 2.54) * mm});
            skLineSegment(sketch, "E2905", {"start": v(-29.86, 4.12) * mm, "end": v(-30.06, 4.12) * mm});
            skLineSegment(sketch, "E2906", {"start": v(-82.23, -77.38) * mm, "end": v(-82.53, -78.25) * mm});
            skLineSegment(sketch, "E2907", {"start": v(58.17, 2.54) * mm, "end": v(57.96, 2.45) * mm});
            skLineSegment(sketch, "E2908", {"start": v(-29.47, 2.67) * mm, "end": v(-29.64, 2.57) * mm});
            skLineSegment(sketch, "E2909", {"start": v(-82.53, -78.25) * mm, "end": v(-82.76, -79.26) * mm});
            skLineSegment(sketch, "E2910", {"start": v(57.96, 2.45) * mm, "end": v(57.73, 2.34) * mm});
            skLineSegment(sketch, "E2911", {"start": v(-28.4, 1.6) * mm, "end": v(-28.5, 1.43) * mm});
            skCircle(sketch, "E2912", {"center": v(-24.64, 64.38) * mm, "radius": 3.1 * mm});
            skLineSegment(sketch, "E2913", {"start": v(31.88, -11.26) * mm, "end": v(31.9, -11.4) * mm});
            skLineSegment(sketch, "E2914", {"start": v(42.11, 4.36) * mm, "end": v(42.34, 4.38) * mm});
            skCircle(sketch, "E2915", {"center": v(-8.9, 64.38) * mm, "radius": 0.75 * mm});
            skCircle(sketch, "E2916", {"center": v(-24.64, 48.38) * mm, "radius": 1 * mm});
            skLineSegment(sketch, "E2917", {"start": v(31.9, -11.4) * mm, "end": v(31.93, -11.6) * mm});
            skLineSegment(sketch, "E2918", {"start": v(42.34, 4.38) * mm, "end": v(42.48, 4.41) * mm});
            skCircle(sketch, "E2919", {"center": v(-40.14, 64.38) * mm, "radius": 0.5 * mm});
            skLineSegment(sketch, "E2920", {"start": v(-88.47, 15.45) * mm, "end": v(-88.55, 15.58) * mm});
            skLineSegment(sketch, "E2921", {"start": v(-88.33, 15.28) * mm, "end": v(-88.47, 15.45) * mm});
            skLineSegment(sketch, "E2922", {"start": v(-87.95, 14.83) * mm, "end": v(-88.33, 15.28) * mm});
            skArc(sketch, "E2923", {"start": v(-88.16, 19.25) * mm, "mid": v(-88.72, 18.89) * mm, "end": v(-89.27, 18.5) * mm});
            skLineSegment(sketch, "E2924", {"start": v(-87.27, 18.77) * mm, "end": v(-88.16, 19.25) * mm});
            skLineSegment(sketch, "E2925", {"start": v(-86.53, 18.26) * mm, "end": v(-87.27, 18.77) * mm});
            skLineSegment(sketch, "E2926", {"start": v(-86.33, 18.1) * mm, "end": v(-86.53, 18.26) * mm});
            skLineSegment(sketch, "E2927", {"start": v(-86.15, 17.92) * mm, "end": v(-86.33, 18.1) * mm});
            skLineSegment(sketch, "E2928", {"start": v(-85.98, 17.76) * mm, "end": v(-86.15, 17.92) * mm});
            skLineSegment(sketch, "E2929", {"start": v(-85.84, 17.6) * mm, "end": v(-85.98, 17.76) * mm});
            skLineSegment(sketch, "E2930", {"start": v(-85.73, 17.46) * mm, "end": v(-85.84, 17.6) * mm});
            skLineSegment(sketch, "E2931", {"start": v(-85.64, 17.34) * mm, "end": v(-85.73, 17.46) * mm});
            skLineSegment(sketch, "E2932", {"start": v(-85.53, 17.14) * mm, "end": v(-85.64, 17.34) * mm});
            skLineSegment(sketch, "E2933", {"start": v(-85.27, 16.63) * mm, "end": v(-85.53, 17.14) * mm});
            skArc(sketch, "E2934", {"start": v(-85.27, 16.63) * mm, "mid": v(-84.81, 16.23) * mm, "end": v(-84.21, 16.25) * mm});
            skArc(sketch, "E2935", {"start": v(-83.56, 16.52) * mm, "mid": v(-83.89, 16.4) * mm, "end": v(-84.21, 16.25) * mm});
            skArc(sketch, "E2936", {"start": v(-83.56, 16.52) * mm, "mid": v(-83.12, 16.93) * mm, "end": v(-83.08, 17.53) * mm});
            skLineSegment(sketch, "E2937", {"start": v(-83.18, 20.47) * mm, "end": v(-82.88, 21.43) * mm});
            skLineSegment(sketch, "E2938", {"start": v(-83.34, 19.58) * mm, "end": v(-83.18, 20.47) * mm});
            skLineSegment(sketch, "E2939", {"start": v(-83.36, 19.32) * mm, "end": v(-83.34, 19.58) * mm});
            skLineSegment(sketch, "E2940", {"start": v(-83.37, 19.07) * mm, "end": v(-83.36, 19.32) * mm});
            skLineSegment(sketch, "E2941", {"start": v(-83.37, 18.84) * mm, "end": v(-83.37, 19.07) * mm});
            skLineSegment(sketch, "E2942", {"start": v(-83.36, 18.63) * mm, "end": v(-83.37, 18.84) * mm});
            skLineSegment(sketch, "E2943", {"start": v(-83.34, 18.45) * mm, "end": v(-83.36, 18.63) * mm});
            skLineSegment(sketch, "E2944", {"start": v(-83.32, 18.3) * mm, "end": v(-83.34, 18.45) * mm});
            skLineSegment(sketch, "E2945", {"start": v(-83.25, 18.09) * mm, "end": v(-83.32, 18.3) * mm});
            skLineSegment(sketch, "E2946", {"start": v(-83.08, 17.53) * mm, "end": v(-83.25, 18.09) * mm});
            skArc(sketch, "E2947", {"start": v(-81.58, 21.7) * mm, "mid": v(-82.23, 21.58) * mm, "end": v(-82.88, 21.43) * mm});
            skLineSegment(sketch, "E2948", {"start": v(-80.94, 20.92) * mm, "end": v(-81.58, 21.7) * mm});
            skLineSegment(sketch, "E2949", {"start": v(-80.45, 20.15) * mm, "end": v(-80.94, 20.92) * mm});
            skLineSegment(sketch, "E2950", {"start": v(-80.33, 19.92) * mm, "end": v(-80.45, 20.15) * mm});
            skLineSegment(sketch, "E2951", {"start": v(-80.22, 19.7) * mm, "end": v(-80.33, 19.92) * mm});
            skLineSegment(sketch, "E2952", {"start": v(-80.13, 19.49) * mm, "end": v(-80.22, 19.7) * mm});
            skLineSegment(sketch, "E2953", {"start": v(-80.06, 19.3) * mm, "end": v(-80.13, 19.49) * mm});
            skLineSegment(sketch, "E2954", {"start": v(-80.01, 19.11) * mm, "end": v(-80.06, 19.3) * mm});
            skLineSegment(sketch, "E2955", {"start": v(-79.98, 18.97) * mm, "end": v(-80.01, 19.11) * mm});
            skLineSegment(sketch, "E2956", {"start": v(-79.96, 18.74) * mm, "end": v(-79.98, 18.97) * mm});
            skLineSegment(sketch, "E2957", {"start": v(-79.9, 18.16) * mm, "end": v(-79.96, 18.74) * mm});
            skArc(sketch, "E2958", {"start": v(-79.9, 18.16) * mm, "mid": v(-79.64, 17.63) * mm, "end": v(-79.07, 17.42) * mm});
            skArc(sketch, "E2959", {"start": v(-78.37, 17.42) * mm, "mid": v(-78.72, 17.42) * mm, "end": v(-79.07, 17.42) * mm});
            skArc(sketch, "E2960", {"start": v(-78.37, 17.42) * mm, "mid": v(-77.8, 17.63) * mm, "end": v(-77.53, 18.16) * mm});
            skLineSegment(sketch, "E2961", {"start": v(-76.5, 20.92) * mm, "end": v(-75.86, 21.7) * mm});
            skLineSegment(sketch, "E2962", {"start": v(-77, 20.15) * mm, "end": v(-76.5, 20.92) * mm});
            skLineSegment(sketch, "E2963", {"start": v(-77.11, 19.92) * mm, "end": v(-77, 20.15) * mm});
            skLineSegment(sketch, "E2964", {"start": v(-77.22, 19.7) * mm, "end": v(-77.11, 19.92) * mm});
            skLineSegment(sketch, "E2965", {"start": v(-77.3, 19.49) * mm, "end": v(-77.22, 19.7) * mm});
            skLineSegment(sketch, "E2966", {"start": v(-77.38, 19.3) * mm, "end": v(-77.3, 19.49) * mm});
            skLineSegment(sketch, "E2967", {"start": v(-77.43, 19.11) * mm, "end": v(-77.38, 19.3) * mm});
            skLineSegment(sketch, "E2968", {"start": v(-77.46, 18.97) * mm, "end": v(-77.43, 19.11) * mm});
            skLineSegment(sketch, "E2969", {"start": v(-77.49, 18.74) * mm, "end": v(-77.46, 18.97) * mm});
            skLineSegment(sketch, "E2970", {"start": v(-77.53, 18.16) * mm, "end": v(-77.49, 18.74) * mm});
            skArc(sketch, "E2971", {"start": v(-74.56, 21.43) * mm, "mid": v(-75.2, 21.58) * mm, "end": v(-75.86, 21.7) * mm});
            skLineSegment(sketch, "E2972", {"start": v(-74.27, 20.47) * mm, "end": v(-74.56, 21.43) * mm});
            skLineSegment(sketch, "E2973", {"start": v(-74.1, 19.58) * mm, "end": v(-74.27, 20.47) * mm});
            skLineSegment(sketch, "E2974", {"start": v(-74.08, 19.32) * mm, "end": v(-74.1, 19.58) * mm});
            skLineSegment(sketch, "E2975", {"start": v(-74.07, 19.07) * mm, "end": v(-74.08, 19.32) * mm});
            skLineSegment(sketch, "E2976", {"start": v(-74.07, 18.84) * mm, "end": v(-74.07, 19.07) * mm});
            skLineSegment(sketch, "E2977", {"start": v(-74.08, 18.63) * mm, "end": v(-74.07, 18.84) * mm});
            skLineSegment(sketch, "E2978", {"start": v(-74.1, 18.45) * mm, "end": v(-74.08, 18.63) * mm});
            skLineSegment(sketch, "E2979", {"start": v(-74.13, 18.3) * mm, "end": v(-74.1, 18.45) * mm});
            skLineSegment(sketch, "E2980", {"start": v(-62.17, -0.53) * mm, "end": v(-61.2, -0.24) * mm});
            skArc(sketch, "E2981", {"start": v(-61.2, -0.24) * mm, "mid": v(-61.07, 0.4) * mm, "end": v(-60.95, 1.06) * mm});
            skLineSegment(sketch, "E2982", {"start": v(-64.48, 2.73) * mm, "end": v(-63.9, 2.69) * mm});
            skLineSegment(sketch, "E2983", {"start": v(-63.9, 2.69) * mm, "end": v(-63.67, 2.66) * mm});
            skLineSegment(sketch, "E2984", {"start": v(-63.67, 2.66) * mm, "end": v(-63.53, 2.63) * mm});
            skLineSegment(sketch, "E2985", {"start": v(-63.53, 2.63) * mm, "end": v(-63.35, 2.58) * mm});
            skLineSegment(sketch, "E2986", {"start": v(-63.35, 2.58) * mm, "end": v(-63.15, 2.5) * mm});
            skLineSegment(sketch, "E2987", {"start": v(-63.15, 2.5) * mm, "end": v(-62.94, 2.42) * mm});
            skLineSegment(sketch, "E2988", {"start": v(-62.94, 2.42) * mm, "end": v(-62.72, 2.31) * mm});
            skLineSegment(sketch, "E2989", {"start": v(-62.72, 2.31) * mm, "end": v(-62.49, 2.2) * mm});
            skLineSegment(sketch, "E2990", {"start": v(-62.49, 2.2) * mm, "end": v(-61.73, 1.7) * mm});
            skLineSegment(sketch, "E2991", {"start": v(-61.73, 1.7) * mm, "end": v(-60.95, 1.06) * mm});
            skArc(sketch, "E2992", {"start": v(-65.23, 3.57) * mm, "mid": v(-65.02, 3) * mm, "end": v(-64.48, 2.73) * mm});
            skArc(sketch, "E2993", {"start": v(-65.23, 3.57) * mm, "mid": v(-65.22, 3.92) * mm, "end": v(-65.23, 4.27) * mm});
            skArc(sketch, "E2994", {"start": v(-64.48, 5.1) * mm, "mid": v(-65.02, 4.84) * mm, "end": v(-65.23, 4.27) * mm});
            skLineSegment(sketch, "E2995", {"start": v(-64.48, 5.1) * mm, "end": v(-63.9, 5.16) * mm});
            skLineSegment(sketch, "E2996", {"start": v(-63.9, 5.16) * mm, "end": v(-63.67, 5.18) * mm});
            skLineSegment(sketch, "E2997", {"start": v(-63.67, 5.18) * mm, "end": v(-63.53, 5.21) * mm});
            skLineSegment(sketch, "E2998", {"start": v(-63.53, 5.21) * mm, "end": v(-63.35, 5.27) * mm});
            skLineSegment(sketch, "E2999", {"start": v(-63.35, 5.27) * mm, "end": v(-63.15, 5.34) * mm});
            skLineSegment(sketch, "E3000", {"start": v(-63.15, 5.34) * mm, "end": v(-62.94, 5.42) * mm});
            skLineSegment(sketch, "E3001", {"start": v(-62.94, 5.42) * mm, "end": v(-62.72, 5.53) * mm});
            skLineSegment(sketch, "E3002", {"start": v(-62.72, 5.53) * mm, "end": v(-62.49, 5.65) * mm});
            skLineSegment(sketch, "E3003", {"start": v(-62.49, 5.65) * mm, "end": v(-61.73, 6.14) * mm});
            skLineSegment(sketch, "E3004", {"start": v(-61.73, 6.14) * mm, "end": v(-60.95, 6.78) * mm});
            skArc(sketch, "E3005", {"start": v(-60.95, 6.78) * mm, "mid": v(-61.07, 7.43) * mm, "end": v(-61.2, 8.08) * mm});
            skLineSegment(sketch, "E3006", {"start": v(-65.1, 8.28) * mm, "end": v(-64.55, 8.45) * mm});
            skLineSegment(sketch, "E3007", {"start": v(-64.55, 8.45) * mm, "end": v(-64.33, 8.52) * mm});
            skLineSegment(sketch, "E3008", {"start": v(-64.33, 8.52) * mm, "end": v(-64.19, 8.54) * mm});
            skLineSegment(sketch, "E3009", {"start": v(-64.19, 8.54) * mm, "end": v(-64, 8.56) * mm});
            skLineSegment(sketch, "E3010", {"start": v(-64, 8.56) * mm, "end": v(-63.8, 8.57) * mm});
            skLineSegment(sketch, "E3011", {"start": v(-63.8, 8.57) * mm, "end": v(-63.57, 8.57) * mm});
            skLineSegment(sketch, "E3012", {"start": v(-63.57, 8.57) * mm, "end": v(-63.32, 8.56) * mm});
            skLineSegment(sketch, "E3013", {"start": v(-63.32, 8.56) * mm, "end": v(-63.06, 8.54) * mm});
            skLineSegment(sketch, "E3014", {"start": v(-63.06, 8.54) * mm, "end": v(-62.17, 8.38) * mm});
            skLineSegment(sketch, "E3015", {"start": v(-62.17, 8.38) * mm, "end": v(-61.2, 8.08) * mm});
            skArc(sketch, "E3016", {"start": v(-66.12, 8.76) * mm, "mid": v(-65.7, 8.32) * mm, "end": v(-65.1, 8.28) * mm});
            skArc(sketch, "E3017", {"start": v(-66.12, 8.76) * mm, "mid": v(-66.25, 9.09) * mm, "end": v(-66.39, 9.41) * mm});
            skArc(sketch, "E3018", {"start": v(-66.02, 10.47) * mm, "mid": v(-66.41, 10.01) * mm, "end": v(-66.39, 9.41) * mm});
            skLineSegment(sketch, "E3019", {"start": v(-66.02, 10.47) * mm, "end": v(-65.5, 10.73) * mm});
            skLineSegment(sketch, "E3020", {"start": v(-65.5, 10.73) * mm, "end": v(-65.3, 10.84) * mm});
            skLineSegment(sketch, "E3021", {"start": v(-65.3, 10.84) * mm, "end": v(-65.18, 10.93) * mm});
            skLineSegment(sketch, "E3022", {"start": v(-65.18, 10.93) * mm, "end": v(-65.04, 11.04) * mm});
            skLineSegment(sketch, "E3023", {"start": v(-65.04, 11.04) * mm, "end": v(-64.88, 11.18) * mm});
            skLineSegment(sketch, "E3024", {"start": v(-64.88, 11.18) * mm, "end": v(-64.72, 11.35) * mm});
            skLineSegment(sketch, "E3025", {"start": v(-64.72, 11.35) * mm, "end": v(-64.55, 11.53) * mm});
            skLineSegment(sketch, "E3026", {"start": v(-64.55, 11.53) * mm, "end": v(-64.38, 11.73) * mm});
            skLineSegment(sketch, "E3027", {"start": v(-64.38, 11.73) * mm, "end": v(-63.87, 12.47) * mm});
            skLineSegment(sketch, "E3028", {"start": v(-63.87, 12.47) * mm, "end": v(-63.4, 13.36) * mm});
            skArc(sketch, "E3029", {"start": v(-63.4, 13.36) * mm, "mid": v(-63.75, 13.92) * mm, "end": v(-64.13, 14.47) * mm});
            skLineSegment(sketch, "E3030", {"start": v(-67.8, 13.15) * mm, "end": v(-67.37, 13.53) * mm});
            skLineSegment(sketch, "E3031", {"start": v(-67.37, 13.53) * mm, "end": v(-67.19, 13.67) * mm});
            skLineSegment(sketch, "E3032", {"start": v(-67.19, 13.67) * mm, "end": v(-67.06, 13.75) * mm});
            skLineSegment(sketch, "E3033", {"start": v(-67.06, 13.75) * mm, "end": v(-66.9, 13.84) * mm});
            skLineSegment(sketch, "E3034", {"start": v(-66.9, 13.84) * mm, "end": v(-66.71, 13.93) * mm});
            skLineSegment(sketch, "E3035", {"start": v(-66.71, 13.93) * mm, "end": v(-66.5, 14.02) * mm});
            skLineSegment(sketch, "E3036", {"start": v(-66.5, 14.02) * mm, "end": v(-66.27, 14.1) * mm});
            skLineSegment(sketch, "E3037", {"start": v(-66.27, 14.1) * mm, "end": v(-66.02, 14.18) * mm});
            skLineSegment(sketch, "E3038", {"start": v(-66.02, 14.18) * mm, "end": v(-65.14, 14.37) * mm});
            skLineSegment(sketch, "E3039", {"start": v(-65.14, 14.37) * mm, "end": v(-64.13, 14.47) * mm});
            skArc(sketch, "E3040", {"start": v(-68.93, 13.21) * mm, "mid": v(-68.38, 12.96) * mm, "end": v(-67.8, 13.15) * mm});
            skArc(sketch, "E3041", {"start": v(-68.93, 13.21) * mm, "mid": v(-69.17, 13.47) * mm, "end": v(-69.43, 13.71) * mm});
            skArc(sketch, "E3042", {"start": v(-69.49, 14.83) * mm, "mid": v(-69.68, 14.26) * mm, "end": v(-69.43, 13.71) * mm});
            skLineSegment(sketch, "E3043", {"start": v(-69.49, 14.83) * mm, "end": v(-69.11, 15.28) * mm});
            skLineSegment(sketch, "E3044", {"start": v(-69.11, 15.28) * mm, "end": v(-68.97, 15.45) * mm});
            skLineSegment(sketch, "E3045", {"start": v(-68.97, 15.45) * mm, "end": v(-68.9, 15.58) * mm});
            skLineSegment(sketch, "E3046", {"start": v(-68.9, 15.58) * mm, "end": v(-68.8, 15.74) * mm});
            skLineSegment(sketch, "E3047", {"start": v(-68.8, 15.74) * mm, "end": v(-68.71, 15.93) * mm});
            skLineSegment(sketch, "E3048", {"start": v(-68.71, 15.93) * mm, "end": v(-68.63, 16.14) * mm});
            skLineSegment(sketch, "E3049", {"start": v(-68.63, 16.14) * mm, "end": v(-68.54, 16.37) * mm});
            skLineSegment(sketch, "E3050", {"start": v(-68.54, 16.37) * mm, "end": v(-68.46, 16.62) * mm});
            skLineSegment(sketch, "E3051", {"start": v(-68.46, 16.62) * mm, "end": v(-68.27, 17.5) * mm});
            skLineSegment(sketch, "E3052", {"start": v(-68.27, 17.5) * mm, "end": v(-68.17, 18.5) * mm});
            skArc(sketch, "E3053", {"start": v(-68.17, 18.5) * mm, "mid": v(-68.72, 18.89) * mm, "end": v(-69.28, 19.25) * mm});
            skLineSegment(sketch, "E3054", {"start": v(-72.17, 16.63) * mm, "end": v(-71.9, 17.14) * mm});
            skLineSegment(sketch, "E3055", {"start": v(-71.9, 17.14) * mm, "end": v(-71.8, 17.34) * mm});
            skLineSegment(sketch, "E3056", {"start": v(-71.8, 17.34) * mm, "end": v(-71.71, 17.46) * mm});
            skLineSegment(sketch, "E3057", {"start": v(-71.71, 17.46) * mm, "end": v(-71.6, 17.6) * mm});
            skLineSegment(sketch, "E3058", {"start": v(-71.6, 17.6) * mm, "end": v(-71.46, 17.76) * mm});
            skLineSegment(sketch, "E3059", {"start": v(-71.46, 17.76) * mm, "end": v(-71.3, 17.92) * mm});
            skLineSegment(sketch, "E3060", {"start": v(-71.3, 17.92) * mm, "end": v(-71.11, 18.1) * mm});
            skLineSegment(sketch, "E3061", {"start": v(-71.11, 18.1) * mm, "end": v(-70.91, 18.26) * mm});
            skLineSegment(sketch, "E3062", {"start": v(-70.91, 18.26) * mm, "end": v(-70.17, 18.77) * mm});
            skLineSegment(sketch, "E3063", {"start": v(-70.17, 18.77) * mm, "end": v(-69.28, 19.25) * mm});
            skArc(sketch, "E3064", {"start": v(-73.23, 16.25) * mm, "mid": v(-72.63, 16.23) * mm, "end": v(-72.17, 16.63) * mm});
            skArc(sketch, "E3065", {"start": v(-73.23, 16.25) * mm, "mid": v(-73.55, 16.4) * mm, "end": v(-73.88, 16.52) * mm});
            skArc(sketch, "E3066", {"start": v(-74.37, 17.53) * mm, "mid": v(-74.33, 16.93) * mm, "end": v(-73.88, 16.52) * mm});
            skLineSegment(sketch, "E3067", {"start": v(-74.37, 17.53) * mm, "end": v(-74.19, 18.09) * mm});
            skLineSegment(sketch, "E3068", {"start": v(-74.19, 18.09) * mm, "end": v(-74.13, 18.3) * mm});
            skLineSegment(sketch, "E3069", {"start": v(-88.82, 16.14) * mm, "end": v(-88.9, 16.37) * mm});
            skLineSegment(sketch, "E3070", {"start": v(-88.9, 16.37) * mm, "end": v(-88.98, 16.62) * mm});
            skLineSegment(sketch, "E3071", {"start": v(-88.98, 16.62) * mm, "end": v(-89.17, 17.5) * mm});
            skLineSegment(sketch, "E3072", {"start": v(-89.17, 17.5) * mm, "end": v(-89.27, 18.5) * mm});
            skArc(sketch, "E3073", {"start": v(-88.01, 13.71) * mm, "mid": v(-87.76, 14.26) * mm, "end": v(-87.95, 14.83) * mm});
            skArc(sketch, "E3074", {"start": v(-88.01, 13.71) * mm, "mid": v(-88.27, 13.47) * mm, "end": v(-88.51, 13.21) * mm});
            skArc(sketch, "E3075", {"start": v(-89.63, 13.15) * mm, "mid": v(-89.06, 12.96) * mm, "end": v(-88.51, 13.21) * mm});
            skLineSegment(sketch, "E3076", {"start": v(-89.63, 13.15) * mm, "end": v(-90.07, 13.53) * mm});
            skLineSegment(sketch, "E3077", {"start": v(-90.07, 13.53) * mm, "end": v(-90.25, 13.67) * mm});
            skLineSegment(sketch, "E3078", {"start": v(-90.25, 13.67) * mm, "end": v(-90.38, 13.75) * mm});
            skLineSegment(sketch, "E3079", {"start": v(-90.38, 13.75) * mm, "end": v(-90.54, 13.84) * mm});
            skLineSegment(sketch, "E3080", {"start": v(-90.54, 13.84) * mm, "end": v(-90.73, 13.93) * mm});
            skLineSegment(sketch, "E3081", {"start": v(-90.73, 13.93) * mm, "end": v(-90.94, 14.02) * mm});
            skLineSegment(sketch, "E3082", {"start": v(-90.94, 14.02) * mm, "end": v(-91.17, 14.1) * mm});
            skLineSegment(sketch, "E3083", {"start": v(-91.17, 14.1) * mm, "end": v(-91.42, 14.18) * mm});
            skLineSegment(sketch, "E3084", {"start": v(-91.42, 14.18) * mm, "end": v(-92.3, 14.37) * mm});
            skLineSegment(sketch, "E3085", {"start": v(-92.3, 14.37) * mm, "end": v(-93.3, 14.47) * mm});
            skArc(sketch, "E3086", {"start": v(-93.3, 14.47) * mm, "mid": v(-93.69, 13.92) * mm, "end": v(-94.05, 13.36) * mm});
            skLineSegment(sketch, "E3087", {"start": v(-91.43, 10.47) * mm, "end": v(-91.94, 10.73) * mm});
            skLineSegment(sketch, "E3088", {"start": v(-91.94, 10.73) * mm, "end": v(-92.14, 10.84) * mm});
            skLineSegment(sketch, "E3089", {"start": v(-92.14, 10.84) * mm, "end": v(-92.26, 10.93) * mm});
            skLineSegment(sketch, "E3090", {"start": v(-92.26, 10.93) * mm, "end": v(-92.4, 11.04) * mm});
            skLineSegment(sketch, "E3091", {"start": v(-92.4, 11.04) * mm, "end": v(-92.56, 11.18) * mm});
            skLineSegment(sketch, "E3092", {"start": v(-92.56, 11.18) * mm, "end": v(-92.72, 11.35) * mm});
            skLineSegment(sketch, "E3093", {"start": v(-92.72, 11.35) * mm, "end": v(-92.89, 11.53) * mm});
            skLineSegment(sketch, "E3094", {"start": v(-92.89, 11.53) * mm, "end": v(-93.06, 11.73) * mm});
            skLineSegment(sketch, "E3095", {"start": v(-93.06, 11.73) * mm, "end": v(-93.57, 12.47) * mm});
            skLineSegment(sketch, "E3096", {"start": v(-93.57, 12.47) * mm, "end": v(-94.05, 13.36) * mm});
            skArc(sketch, "E3097", {"start": v(-91.05, 9.41) * mm, "mid": v(-91.03, 10.01) * mm, "end": v(-91.43, 10.47) * mm});
            skArc(sketch, "E3098", {"start": v(-91.05, 9.41) * mm, "mid": v(-91.2, 9.09) * mm, "end": v(-91.32, 8.76) * mm});
            skArc(sketch, "E3099", {"start": v(-92.33, 8.28) * mm, "mid": v(-91.73, 8.32) * mm, "end": v(-91.32, 8.76) * mm});
            skLineSegment(sketch, "E3100", {"start": v(-92.33, 8.28) * mm, "end": v(-92.89, 8.45) * mm});
            skLineSegment(sketch, "E3101", {"start": v(-92.89, 8.45) * mm, "end": v(-93.1, 8.52) * mm});
            skLineSegment(sketch, "E3102", {"start": v(-93.1, 8.52) * mm, "end": v(-93.25, 8.54) * mm});
            skLineSegment(sketch, "E3103", {"start": v(-93.25, 8.54) * mm, "end": v(-93.43, 8.56) * mm});
            skLineSegment(sketch, "E3104", {"start": v(-93.43, 8.56) * mm, "end": v(-93.64, 8.57) * mm});
            skLineSegment(sketch, "E3105", {"start": v(-93.64, 8.57) * mm, "end": v(-93.87, 8.57) * mm});
            skLineSegment(sketch, "E3106", {"start": v(-93.87, 8.57) * mm, "end": v(-94.12, 8.56) * mm});
            skLineSegment(sketch, "E3107", {"start": v(-94.12, 8.56) * mm, "end": v(-94.38, 8.54) * mm});
            skArc(sketch, "E3108", {"start": v(-94.05, -5.52) * mm, "mid": v(-93.69, -6.08) * mm, "end": v(-93.3, -6.62) * mm});
            skLineSegment(sketch, "E3109", {"start": v(-77.49, -10.9) * mm, "end": v(-77.46, -11.13) * mm});
            skLineSegment(sketch, "E3110", {"start": v(-89.63, -5.31) * mm, "end": v(-90.07, -5.69) * mm});
            skLineSegment(sketch, "E3111", {"start": v(-77.46, -11.13) * mm, "end": v(-77.43, -11.27) * mm});
            skLineSegment(sketch, "E3112", {"start": v(-90.07, -5.69) * mm, "end": v(-90.25, -5.83) * mm});
            skLineSegment(sketch, "E3113", {"start": v(-77.43, -11.27) * mm, "end": v(-77.38, -11.45) * mm});
            skLineSegment(sketch, "E3114", {"start": v(-90.25, -5.83) * mm, "end": v(-90.38, -5.9) * mm});
            skLineSegment(sketch, "E3115", {"start": v(-77.38, -11.45) * mm, "end": v(-77.3, -11.65) * mm});
            skLineSegment(sketch, "E3116", {"start": v(-90.38, -5.9) * mm, "end": v(-90.54, -6) * mm});
            skLineSegment(sketch, "E3117", {"start": v(-77.3, -11.65) * mm, "end": v(-77.22, -11.86) * mm});
            skLineSegment(sketch, "E3118", {"start": v(-90.54, -6) * mm, "end": v(-90.73, -6.09) * mm});
            skLineSegment(sketch, "E3119", {"start": v(-77.22, -11.86) * mm, "end": v(-77.11, -12.08) * mm});
            skLineSegment(sketch, "E3120", {"start": v(-90.73, -6.09) * mm, "end": v(-90.94, -6.17) * mm});
            skLineSegment(sketch, "E3121", {"start": v(-77.11, -12.08) * mm, "end": v(-77, -12.31) * mm});
            skLineSegment(sketch, "E3122", {"start": v(-90.94, -6.17) * mm, "end": v(-91.17, -6.26) * mm});
            skLineSegment(sketch, "E3123", {"start": v(-77, -12.31) * mm, "end": v(-76.5, -13.07) * mm});
            skLineSegment(sketch, "E3124", {"start": v(-91.17, -6.26) * mm, "end": v(-91.42, -6.33) * mm});
            skLineSegment(sketch, "E3125", {"start": v(-76.5, -13.07) * mm, "end": v(-75.86, -13.85) * mm});
            skLineSegment(sketch, "E3126", {"start": v(-91.42, -6.33) * mm, "end": v(-92.3, -6.53) * mm});
            skArc(sketch, "E3127", {"start": v(-75.86, -13.85) * mm, "mid": v(-75.2, -13.73) * mm, "end": v(-74.56, -13.6) * mm});
            skLineSegment(sketch, "E3128", {"start": v(-92.3, -6.53) * mm, "end": v(-93.3, -6.62) * mm});
            skLineSegment(sketch, "E3129", {"start": v(-74.37, -9.7) * mm, "end": v(-74.19, -10.25) * mm});
            skArc(sketch, "E3130", {"start": v(-88.51, -5.37) * mm, "mid": v(-89.06, -5.12) * mm, "end": v(-89.63, -5.31) * mm});
            skLineSegment(sketch, "E3131", {"start": v(-74.19, -10.25) * mm, "end": v(-74.13, -10.46) * mm});
            skArc(sketch, "E3132", {"start": v(-88.51, -5.37) * mm, "mid": v(-88.27, -5.62) * mm, "end": v(-88.01, -5.87) * mm});
            skLineSegment(sketch, "E3133", {"start": v(-74.13, -10.46) * mm, "end": v(-74.1, -10.6) * mm});
            skLineSegment(sketch, "E3134", {"start": v(-74.1, -10.6) * mm, "end": v(-74.08, -10.8) * mm});
            skLineSegment(sketch, "E3135", {"start": v(-74.08, -10.8) * mm, "end": v(-74.07, -11) * mm});
            skLineSegment(sketch, "E3136", {"start": v(-74.07, -11) * mm, "end": v(-74.07, -11.23) * mm});
            skLineSegment(sketch, "E3137", {"start": v(-74.07, -11.23) * mm, "end": v(-74.08, -11.48) * mm});
            skLineSegment(sketch, "E3138", {"start": v(-74.08, -11.48) * mm, "end": v(-74.1, -11.74) * mm});
            skLineSegment(sketch, "E3139", {"start": v(-74.1, -11.74) * mm, "end": v(-74.27, -12.63) * mm});
            skLineSegment(sketch, "E3140", {"start": v(-74.27, -12.63) * mm, "end": v(-74.56, -13.6) * mm});
            skArc(sketch, "E3141", {"start": v(-73.88, -8.68) * mm, "mid": v(-74.33, -9.1) * mm, "end": v(-74.37, -9.7) * mm});
            skArc(sketch, "E3142", {"start": v(-73.88, -8.68) * mm, "mid": v(-73.55, -8.55) * mm, "end": v(-73.23, -8.41) * mm});
            skArc(sketch, "E3143", {"start": v(-72.17, -8.78) * mm, "mid": v(-72.63, -8.39) * mm, "end": v(-73.23, -8.41) * mm});
            skArc(sketch, "E3144", {"start": v(-81.23, 2.47) * mm, "mid": v(-80.77, 1.87) * mm, "end": v(-80.17, 1.4) * mm});
            skLineSegment(sketch, "E3145", {"start": v(-72.17, -8.78) * mm, "end": v(-71.9, -9.3) * mm});
            skArc(sketch, "E3146", {"start": v(-69.28, -11.4) * mm, "mid": v(-68.72, -11.04) * mm, "end": v(-68.17, -10.67) * mm});
            skLineSegment(sketch, "E3147", {"start": v(-70.17, -10.93) * mm, "end": v(-69.28, -11.4) * mm});
            skLineSegment(sketch, "E3148", {"start": v(-70.91, -10.41) * mm, "end": v(-70.17, -10.93) * mm});
            skLineSegment(sketch, "E3149", {"start": v(-71.11, -10.25) * mm, "end": v(-70.91, -10.41) * mm});
            skLineSegment(sketch, "E3150", {"start": v(-71.3, -10.08) * mm, "end": v(-71.11, -10.25) * mm});
            skLineSegment(sketch, "E3151", {"start": v(-71.46, -9.92) * mm, "end": v(-71.3, -10.08) * mm});
            skLineSegment(sketch, "E3152", {"start": v(-71.6, -9.76) * mm, "end": v(-71.46, -9.92) * mm});
            skLineSegment(sketch, "E3153", {"start": v(-71.71, -9.62) * mm, "end": v(-71.6, -9.76) * mm});
            skLineSegment(sketch, "E3154", {"start": v(-71.8, -9.5) * mm, "end": v(-71.71, -9.62) * mm});
            skLineSegment(sketch, "E3155", {"start": v(-71.9, -9.3) * mm, "end": v(-71.8, -9.5) * mm});
            skLineSegment(sketch, "E3156", {"start": v(-93.57, -4.63) * mm, "end": v(-94.05, -5.52) * mm});
            skLineSegment(sketch, "E3157", {"start": v(-77.53, -10.32) * mm, "end": v(-77.49, -10.9) * mm});
            skLineSegment(sketch, "E3158", {"start": v(-93.06, -3.89) * mm, "end": v(-93.57, -4.63) * mm});
            skArc(sketch, "E3159", {"start": v(-77.53, -10.32) * mm, "mid": v(-77.8, -9.78) * mm, "end": v(-78.37, -9.57) * mm});
            skLineSegment(sketch, "E3160", {"start": v(-92.89, -3.69) * mm, "end": v(-93.06, -3.89) * mm});
            skArc(sketch, "E3161", {"start": v(-79.07, -9.57) * mm, "mid": v(-78.72, -9.58) * mm, "end": v(-78.37, -9.57) * mm});
            skLineSegment(sketch, "E3162", {"start": v(-92.72, -3.5) * mm, "end": v(-92.89, -3.69) * mm});
            skArc(sketch, "E3163", {"start": v(-79.07, -9.57) * mm, "mid": v(-79.64, -9.78) * mm, "end": v(-79.9, -10.32) * mm});
            skLineSegment(sketch, "E3164", {"start": v(-92.56, -3.34) * mm, "end": v(-92.72, -3.5) * mm});
            skLineSegment(sketch, "E3165", {"start": v(-92.4, -3.2) * mm, "end": v(-92.56, -3.34) * mm});
            skLineSegment(sketch, "E3166", {"start": v(-92.26, -3.09) * mm, "end": v(-92.4, -3.2) * mm});
            skLineSegment(sketch, "E3167", {"start": v(-92.14, -3) * mm, "end": v(-92.26, -3.09) * mm});
            skLineSegment(sketch, "E3168", {"start": v(-91.94, -2.9) * mm, "end": v(-92.14, -3) * mm});
            skLineSegment(sketch, "E3169", {"start": v(-91.43, -2.63) * mm, "end": v(-91.94, -2.9) * mm});
            skArc(sketch, "E3170", {"start": v(-91.43, -2.63) * mm, "mid": v(-91.03, -2.17) * mm, "end": v(-91.05, -1.57) * mm});
            skArc(sketch, "E3171", {"start": v(-91.32, -0.92) * mm, "mid": v(-91.2, -1.24) * mm, "end": v(-91.05, -1.57) * mm});
            skArc(sketch, "E3172", {"start": v(-91.32, -0.92) * mm, "mid": v(-91.73, -0.47) * mm, "end": v(-92.33, -0.43) * mm});
            skLineSegment(sketch, "E3173", {"start": v(-95.27, -0.53) * mm, "end": v(-96.23, -0.24) * mm});
            skLineSegment(sketch, "E3174", {"start": v(-94.38, -0.7) * mm, "end": v(-95.27, -0.53) * mm});
            skLineSegment(sketch, "E3175", {"start": v(-94.12, -0.72) * mm, "end": v(-94.38, -0.7) * mm});
            skLineSegment(sketch, "E3176", {"start": v(-93.87, -0.73) * mm, "end": v(-94.12, -0.72) * mm});
            skLineSegment(sketch, "E3177", {"start": v(-93.64, -0.73) * mm, "end": v(-93.87, -0.73) * mm});
            skLineSegment(sketch, "E3178", {"start": v(-93.43, -0.72) * mm, "end": v(-93.64, -0.73) * mm});
            skLineSegment(sketch, "E3179", {"start": v(-93.25, -0.7) * mm, "end": v(-93.43, -0.72) * mm});
            skLineSegment(sketch, "E3180", {"start": v(-93.1, -0.67) * mm, "end": v(-93.25, -0.7) * mm});
            skLineSegment(sketch, "E3181", {"start": v(-92.89, -0.6) * mm, "end": v(-93.1, -0.67) * mm});
            skLineSegment(sketch, "E3182", {"start": v(-92.33, -0.43) * mm, "end": v(-92.89, -0.6) * mm});
            skArc(sketch, "E3183", {"start": v(-96.5, 1.06) * mm, "mid": v(-96.37, 0.4) * mm, "end": v(-96.23, -0.24) * mm});
            skLineSegment(sketch, "E3184", {"start": v(-95.71, 1.7) * mm, "end": v(-96.5, 1.06) * mm});
            skLineSegment(sketch, "E3185", {"start": v(-94.95, 2.2) * mm, "end": v(-95.71, 1.7) * mm});
            skLineSegment(sketch, "E3186", {"start": v(-80.94, -13.07) * mm, "end": v(-81.58, -13.85) * mm});
            skLineSegment(sketch, "E3187", {"start": v(-63.06, -0.7) * mm, "end": v(-62.17, -0.53) * mm});
            skLineSegment(sketch, "E3188", {"start": v(-80.45, -12.31) * mm, "end": v(-80.94, -13.07) * mm});
            skLineSegment(sketch, "E3189", {"start": v(-63.32, -0.72) * mm, "end": v(-63.06, -0.7) * mm});
            skLineSegment(sketch, "E3190", {"start": v(-80.33, -12.08) * mm, "end": v(-80.45, -12.31) * mm});
            skLineSegment(sketch, "E3191", {"start": v(-63.57, -0.73) * mm, "end": v(-63.32, -0.72) * mm});
            skLineSegment(sketch, "E3192", {"start": v(-80.22, -11.86) * mm, "end": v(-80.33, -12.08) * mm});
            skLineSegment(sketch, "E3193", {"start": v(-63.8, -0.73) * mm, "end": v(-63.57, -0.73) * mm});
            skLineSegment(sketch, "E3194", {"start": v(-66.27, -6.26) * mm, "end": v(-66.02, -6.33) * mm});
            skLineSegment(sketch, "E3195", {"start": v(-86.53, -10.41) * mm, "end": v(-87.27, -10.93) * mm});
            skLineSegment(sketch, "E3196", {"start": v(-94.09, 2.58) * mm, "end": v(-94.29, 2.5) * mm});
            skLineSegment(sketch, "E3197", {"start": v(-80.13, -11.65) * mm, "end": v(-80.22, -11.86) * mm});
            skLineSegment(sketch, "E3198", {"start": v(-64, -0.72) * mm, "end": v(-63.8, -0.73) * mm});
            skLineSegment(sketch, "E3199", {"start": v(-66.5, -6.17) * mm, "end": v(-66.27, -6.26) * mm});
            skLineSegment(sketch, "E3200", {"start": v(-86.33, -10.25) * mm, "end": v(-86.53, -10.41) * mm});
            skLineSegment(sketch, "E3201", {"start": v(-93.91, 2.63) * mm, "end": v(-94.09, 2.58) * mm});
            skLineSegment(sketch, "E3202", {"start": v(-80.06, -11.45) * mm, "end": v(-80.13, -11.65) * mm});
            skLineSegment(sketch, "E3203", {"start": v(-64.19, -0.7) * mm, "end": v(-64, -0.72) * mm});
            skLineSegment(sketch, "E3204", {"start": v(-66.71, -6.09) * mm, "end": v(-66.5, -6.17) * mm});
            skLineSegment(sketch, "E3205", {"start": v(-86.15, -10.08) * mm, "end": v(-86.33, -10.25) * mm});
            skLineSegment(sketch, "E3206", {"start": v(-93.77, 2.66) * mm, "end": v(-93.91, 2.63) * mm});
            skLineSegment(sketch, "E3207", {"start": v(-80.01, -11.27) * mm, "end": v(-80.06, -11.45) * mm});
            skLineSegment(sketch, "E3208", {"start": v(-64.33, -0.67) * mm, "end": v(-64.19, -0.7) * mm});
            skLineSegment(sketch, "E3209", {"start": v(-66.9, -6) * mm, "end": v(-66.71, -6.09) * mm});
            skLineSegment(sketch, "E3210", {"start": v(-85.98, -9.92) * mm, "end": v(-86.15, -10.08) * mm});
            skLineSegment(sketch, "E3211", {"start": v(-93.54, 2.69) * mm, "end": v(-93.77, 2.66) * mm});
            skLineSegment(sketch, "E3212", {"start": v(-79.98, -11.13) * mm, "end": v(-80.01, -11.27) * mm});
            skLineSegment(sketch, "E3213", {"start": v(-64.55, -0.6) * mm, "end": v(-64.33, -0.67) * mm});
            skLineSegment(sketch, "E3214", {"start": v(-67.06, -5.9) * mm, "end": v(-66.9, -6) * mm});
            skLineSegment(sketch, "E3215", {"start": v(-85.84, -9.76) * mm, "end": v(-85.98, -9.92) * mm});
            skLineSegment(sketch, "E3216", {"start": v(-92.96, 2.73) * mm, "end": v(-93.54, 2.69) * mm});
            skLineSegment(sketch, "E3217", {"start": v(-79.96, -10.9) * mm, "end": v(-79.98, -11.13) * mm});
            skLineSegment(sketch, "E3218", {"start": v(-65.1, -0.43) * mm, "end": v(-64.55, -0.6) * mm});
            skLineSegment(sketch, "E3219", {"start": v(-67.19, -5.83) * mm, "end": v(-67.06, -5.9) * mm});
            skLineSegment(sketch, "E3220", {"start": v(-85.73, -9.62) * mm, "end": v(-85.84, -9.76) * mm});
            skArc(sketch, "E3221", {"start": v(-92.96, 2.73) * mm, "mid": v(-92.42, 3) * mm, "end": v(-92.22, 3.57) * mm});
            skLineSegment(sketch, "E3222", {"start": v(-79.9, -10.32) * mm, "end": v(-79.96, -10.9) * mm});
            skArc(sketch, "E3223", {"start": v(-65.1, -0.43) * mm, "mid": v(-65.7, -0.47) * mm, "end": v(-66.12, -0.92) * mm});
            skLineSegment(sketch, "E3224", {"start": v(-67.37, -5.69) * mm, "end": v(-67.19, -5.83) * mm});
            skLineSegment(sketch, "E3225", {"start": v(-85.64, -9.5) * mm, "end": v(-85.73, -9.62) * mm});
            skArc(sketch, "E3226", {"start": v(-92.22, 4.27) * mm, "mid": v(-92.22, 3.92) * mm, "end": v(-92.22, 3.57) * mm});
            skArc(sketch, "E3227", {"start": v(-82.88, -13.6) * mm, "mid": v(-82.23, -13.73) * mm, "end": v(-81.58, -13.85) * mm});
            skArc(sketch, "E3228", {"start": v(-66.39, -1.57) * mm, "mid": v(-66.25, -1.24) * mm, "end": v(-66.12, -0.92) * mm});
            skLineSegment(sketch, "E3229", {"start": v(-67.8, -5.31) * mm, "end": v(-67.37, -5.69) * mm});
            skLineSegment(sketch, "E3230", {"start": v(-85.53, -9.3) * mm, "end": v(-85.64, -9.5) * mm});
            skArc(sketch, "E3231", {"start": v(-92.22, 4.27) * mm, "mid": v(-92.42, 4.84) * mm, "end": v(-92.96, 5.1) * mm});
            skLineSegment(sketch, "E3232", {"start": v(-83.18, -12.63) * mm, "end": v(-82.88, -13.6) * mm});
            skArc(sketch, "E3233", {"start": v(-66.39, -1.57) * mm, "mid": v(-66.41, -2.17) * mm, "end": v(-66.02, -2.63) * mm});
            skArc(sketch, "E3234", {"start": v(-67.8, -5.31) * mm, "mid": v(-68.38, -5.12) * mm, "end": v(-68.93, -5.37) * mm});
            skLineSegment(sketch, "E3235", {"start": v(-85.27, -8.78) * mm, "end": v(-85.53, -9.3) * mm});
            skLineSegment(sketch, "E3236", {"start": v(-95.71, 6.14) * mm, "end": v(-96.5, 6.78) * mm});
            skLineSegment(sketch, "E3237", {"start": v(-83.34, -11.74) * mm, "end": v(-83.18, -12.63) * mm});
            skLineSegment(sketch, "E3238", {"start": v(-63.87, -4.63) * mm, "end": v(-63.4, -5.52) * mm});
            skArc(sketch, "E3239", {"start": v(-89.27, -10.67) * mm, "mid": v(-88.72, -11.04) * mm, "end": v(-88.16, -11.4) * mm});
            skLineSegment(sketch, "E3240", {"start": v(-94.95, 5.65) * mm, "end": v(-95.71, 6.14) * mm});
            skLineSegment(sketch, "E3241", {"start": v(-83.36, -11.48) * mm, "end": v(-83.34, -11.74) * mm});
            skLineSegment(sketch, "E3242", {"start": v(-64.38, -3.89) * mm, "end": v(-63.87, -4.63) * mm});
            skArc(sketch, "E3243", {"start": v(-69.43, -5.87) * mm, "mid": v(-69.17, -5.62) * mm, "end": v(-68.93, -5.37) * mm});
            skLineSegment(sketch, "E3244", {"start": v(-89.17, -9.66) * mm, "end": v(-89.27, -10.67) * mm});
            skLineSegment(sketch, "E3245", {"start": v(-94.72, 5.53) * mm, "end": v(-94.95, 5.65) * mm});
            skLineSegment(sketch, "E3246", {"start": v(-83.37, -11.23) * mm, "end": v(-83.36, -11.48) * mm});
            skLineSegment(sketch, "E3247", {"start": v(-64.55, -3.69) * mm, "end": v(-64.38, -3.89) * mm});
            skArc(sketch, "E3248", {"start": v(-69.43, -5.87) * mm, "mid": v(-69.68, -6.42) * mm, "end": v(-69.49, -6.99) * mm});
            skLineSegment(sketch, "E3249", {"start": v(-88.98, -8.78) * mm, "end": v(-89.17, -9.66) * mm});
            skLineSegment(sketch, "E3250", {"start": v(-94.5, 5.42) * mm, "end": v(-94.72, 5.53) * mm});
            skLineSegment(sketch, "E3251", {"start": v(-83.37, -11) * mm, "end": v(-83.37, -11.23) * mm});
            skLineSegment(sketch, "E3252", {"start": v(-64.72, -3.5) * mm, "end": v(-64.55, -3.69) * mm});
            skLineSegment(sketch, "E3253", {"start": v(-68.27, -9.66) * mm, "end": v(-68.17, -10.67) * mm});
            skLineSegment(sketch, "E3254", {"start": v(-88.9, -8.53) * mm, "end": v(-88.98, -8.78) * mm});
            skLineSegment(sketch, "E3255", {"start": v(-94.29, 5.34) * mm, "end": v(-94.5, 5.42) * mm});
            skLineSegment(sketch, "E3256", {"start": v(-83.36, -10.8) * mm, "end": v(-83.37, -11) * mm});
            skLineSegment(sketch, "E3257", {"start": v(-64.88, -3.34) * mm, "end": v(-64.72, -3.5) * mm});
            skLineSegment(sketch, "E3258", {"start": v(-88.73, 15.93) * mm, "end": v(-88.82, 16.14) * mm});
            skLineSegment(sketch, "E3259", {"start": v(-68.46, -8.78) * mm, "end": v(-68.27, -9.66) * mm});
            skLineSegment(sketch, "E3260", {"start": v(-88.82, -8.3) * mm, "end": v(-88.9, -8.53) * mm});
            skLineSegment(sketch, "E3261", {"start": v(-94.09, 5.27) * mm, "end": v(-94.29, 5.34) * mm});
            skLineSegment(sketch, "E3262", {"start": v(-83.34, -10.6) * mm, "end": v(-83.36, -10.8) * mm});
            skLineSegment(sketch, "E3263", {"start": v(-65.04, -3.2) * mm, "end": v(-64.88, -3.34) * mm});
            skLineSegment(sketch, "E3264", {"start": v(-88.64, 15.74) * mm, "end": v(-88.73, 15.93) * mm});
            skLineSegment(sketch, "E3265", {"start": v(-68.54, -8.53) * mm, "end": v(-68.46, -8.78) * mm});
            skLineSegment(sketch, "E3266", {"start": v(-88.73, -8.09) * mm, "end": v(-88.82, -8.3) * mm});
            skLineSegment(sketch, "E3267", {"start": v(-93.91, 5.21) * mm, "end": v(-94.09, 5.27) * mm});
            skLineSegment(sketch, "E3268", {"start": v(-83.32, -10.46) * mm, "end": v(-83.34, -10.6) * mm});
            skLineSegment(sketch, "E3269", {"start": v(-65.18, -3.09) * mm, "end": v(-65.04, -3.2) * mm});
            skLineSegment(sketch, "E3270", {"start": v(-88.55, 15.58) * mm, "end": v(-88.64, 15.74) * mm});
            skLineSegment(sketch, "E3271", {"start": v(-68.63, -8.3) * mm, "end": v(-68.54, -8.53) * mm});
            skLineSegment(sketch, "E3272", {"start": v(-88.64, -7.9) * mm, "end": v(-88.73, -8.09) * mm});
            skLineSegment(sketch, "E3273", {"start": v(-93.77, 5.18) * mm, "end": v(-93.91, 5.21) * mm});
            skLineSegment(sketch, "E3274", {"start": v(-83.25, -10.25) * mm, "end": v(-83.32, -10.46) * mm});
            skLineSegment(sketch, "E3275", {"start": v(-65.3, -3) * mm, "end": v(-65.18, -3.09) * mm});
            skLineSegment(sketch, "E3276", {"start": v(-68.71, -8.09) * mm, "end": v(-68.63, -8.3) * mm});
            skLineSegment(sketch, "E3277", {"start": v(-88.55, -7.74) * mm, "end": v(-88.64, -7.9) * mm});
            skLineSegment(sketch, "E3278", {"start": v(-93.54, 5.16) * mm, "end": v(-93.77, 5.18) * mm});
            skLineSegment(sketch, "E3279", {"start": v(-83.08, -9.7) * mm, "end": v(-83.25, -10.25) * mm});
            skLineSegment(sketch, "E3280", {"start": v(-65.5, -2.9) * mm, "end": v(-65.3, -3) * mm});
            skLineSegment(sketch, "E3281", {"start": v(-68.8, -7.9) * mm, "end": v(-68.71, -8.09) * mm});
            skLineSegment(sketch, "E3282", {"start": v(-88.47, -7.61) * mm, "end": v(-88.55, -7.74) * mm});
            skLineSegment(sketch, "E3283", {"start": v(-92.96, 5.1) * mm, "end": v(-93.54, 5.16) * mm});
            skArc(sketch, "E3284", {"start": v(-83.08, -9.7) * mm, "mid": v(-83.12, -9.1) * mm, "end": v(-83.56, -8.68) * mm});
            skLineSegment(sketch, "E3285", {"start": v(-66.02, -2.63) * mm, "end": v(-65.5, -2.9) * mm});
            skLineSegment(sketch, "E3286", {"start": v(-68.9, -7.74) * mm, "end": v(-68.8, -7.9) * mm});
            skLineSegment(sketch, "E3287", {"start": v(-88.33, -7.43) * mm, "end": v(-88.47, -7.61) * mm});
            skArc(sketch, "E3288", {"start": v(-96.23, 8.08) * mm, "mid": v(-96.37, 7.43) * mm, "end": v(-96.5, 6.78) * mm});
            skArc(sketch, "E3289", {"start": v(-84.21, -8.41) * mm, "mid": v(-83.89, -8.55) * mm, "end": v(-83.56, -8.68) * mm});
            skArc(sketch, "E3290", {"start": v(-64.13, -6.62) * mm, "mid": v(-63.75, -6.08) * mm, "end": v(-63.4, -5.52) * mm});
            skLineSegment(sketch, "E3291", {"start": v(-68.97, -7.61) * mm, "end": v(-68.9, -7.74) * mm});
            skLineSegment(sketch, "E3292", {"start": v(-87.95, -6.99) * mm, "end": v(-88.33, -7.43) * mm});
            skLineSegment(sketch, "E3293", {"start": v(-95.27, 8.38) * mm, "end": v(-96.23, 8.08) * mm});
            skArc(sketch, "E3294", {"start": v(-84.21, -8.41) * mm, "mid": v(-84.81, -8.39) * mm, "end": v(-85.27, -8.78) * mm});
            skLineSegment(sketch, "E3295", {"start": v(-65.14, -6.53) * mm, "end": v(-64.13, -6.62) * mm});
            skLineSegment(sketch, "E3296", {"start": v(-69.11, -7.43) * mm, "end": v(-68.97, -7.61) * mm});
            skArc(sketch, "E3297", {"start": v(-87.95, -6.99) * mm, "mid": v(-87.76, -6.42) * mm, "end": v(-88.01, -5.87) * mm});
            skLineSegment(sketch, "E3298", {"start": v(-94.38, 8.54) * mm, "end": v(-95.27, 8.38) * mm});
            skLineSegment(sketch, "E3299", {"start": v(-87.27, -10.93) * mm, "end": v(-88.16, -11.4) * mm});
            skLineSegment(sketch, "E3300", {"start": v(-66.02, -6.33) * mm, "end": v(-65.14, -6.53) * mm});
            skLineSegment(sketch, "E3301", {"start": v(-69.49, -6.99) * mm, "end": v(-69.11, -7.43) * mm});
            skLineSegment(sketch, "E3302", {"start": v(-94.72, 2.31) * mm, "end": v(-94.95, 2.2) * mm});
            skLineSegment(sketch, "E3303", {"start": v(-94.5, 2.42) * mm, "end": v(-94.72, 2.31) * mm});
            skLineSegment(sketch, "E3304", {"start": v(-94.29, 2.5) * mm, "end": v(-94.5, 2.42) * mm});
            skLineSegment(sketch, "E3305", {"start": v(-78.72, 1.02) * mm, "end": v(-78.72, 0.82) * mm});
            skLineSegment(sketch, "E3306", {"start": v(-77.27, 1.4) * mm, "end": v(-77.17, 1.24) * mm});
            skLineSegment(sketch, "E3307", {"start": v(-76.2, 2.47) * mm, "end": v(-76.04, 2.37) * mm});
            skLineSegment(sketch, "E3308", {"start": v(-75.82, 3.92) * mm, "end": v(-75.62, 3.92) * mm});
            skLineSegment(sketch, "E3309", {"start": v(-76.2, 5.37) * mm, "end": v(-76.04, 5.47) * mm});
            skLineSegment(sketch, "E3310", {"start": v(-77.27, 6.43) * mm, "end": v(-77.17, 6.6) * mm});
            skArc(sketch, "E3311", {"start": v(-76.2, 5.37) * mm, "mid": v(-76.67, 5.97) * mm, "end": v(-77.27, 6.43) * mm});
            skArc(sketch, "E3312", {"start": v(-75.62, 3.92) * mm, "mid": v(-75.73, 4.72) * mm, "end": v(-76.04, 5.47) * mm});
            skArc(sketch, "E3313", {"start": v(-76.2, 2.47) * mm, "mid": v(-75.92, 3.17) * mm, "end": v(-75.82, 3.92) * mm});
            skArc(sketch, "E3314", {"start": v(-77.17, 1.24) * mm, "mid": v(-76.53, 1.73) * mm, "end": v(-76.04, 2.37) * mm});
            skArc(sketch, "E3315", {"start": v(-78.72, 1.02) * mm, "mid": v(-77.97, 1.12) * mm, "end": v(-77.27, 1.4) * mm});
            skArc(sketch, "E3316", {"start": v(-80.27, 1.24) * mm, "mid": v(-79.52, 0.93) * mm, "end": v(-78.72, 0.82) * mm});
            skArc(sketch, "E3317", {"start": v(-81.82, 3.92) * mm, "mid": v(-81.71, 3.12) * mm, "end": v(-81.4, 2.37) * mm});
            skArc(sketch, "E3318", {"start": v(-80.27, 6.6) * mm, "mid": v(-80.91, 6.11) * mm, "end": v(-81.4, 5.47) * mm});
            skArc(sketch, "E3319", {"start": v(-81.23, 5.37) * mm, "mid": v(-81.52, 4.67) * mm, "end": v(-81.62, 3.92) * mm});
            skArc(sketch, "E3320", {"start": v(-77.17, 6.6) * mm, "mid": v(-77.92, 6.92) * mm, "end": v(-78.72, 7.02) * mm});
            skArc(sketch, "E3321", {"start": v(-78.72, 6.82) * mm, "mid": v(-79.47, 6.72) * mm, "end": v(-80.17, 6.43) * mm});
            skLineSegment(sketch, "E3322", {"start": v(-78.72, 6.82) * mm, "end": v(-78.72, 7.02) * mm});
            skLineSegment(sketch, "E3323", {"start": v(-80.17, 6.43) * mm, "end": v(-80.27, 6.6) * mm});
            skLineSegment(sketch, "E3324", {"start": v(-81.23, 5.37) * mm, "end": v(-81.4, 5.47) * mm});
            skLineSegment(sketch, "E3325", {"start": v(-81.62, 3.92) * mm, "end": v(-81.82, 3.92) * mm});
            skLineSegment(sketch, "E3326", {"start": v(-81.23, 2.47) * mm, "end": v(-81.4, 2.37) * mm});
            skLineSegment(sketch, "E3327", {"start": v(-80.17, 1.4) * mm, "end": v(-80.27, 1.24) * mm});
            skLineSegment(sketch, "E3328", {"start": v(-64.74, -47) * mm, "end": v(-64.56, -46.76) * mm});
            skLineSegment(sketch, "E3329", {"start": v(-61.3, 69.4) * mm, "end": v(-61.55, 69.23) * mm});
            skLineSegment(sketch, "E3330", {"start": v(-59.76, 67.15) * mm, "end": v(-59.93, 67.13) * mm});
            skLineSegment(sketch, "E3331", {"start": v(-86.83, 60.78) * mm, "end": v(-86.1, 61.14) * mm});
            skSolve(sketch);
        }
        {
            var Q0;
            Q0=qCreatedBy(makeId("Front.planeOp"),FACE);
            var sketch = newSketch(context, id + "F2", { "sketchPlane" : qUnion([Q0])});
            skArc(sketch, "E3332", {"start": v(8.16, 58.25) * mm, "mid": v(8.42, 58.01) * mm, "end": v(8.7, 57.79) * mm});
            skArc(sketch, "E3333", {"start": v(8.16, 58.25) * mm, "mid": v(7.61, 58.45) * mm, "end": v(7.08, 58.2) * mm});
            skLineSegment(sketch, "E3334", {"start": v(4.56, 56.78) * mm, "end": v(3.52, 56.5) * mm});
            skLineSegment(sketch, "E3335", {"start": v(5.47, 57.12) * mm, "end": v(4.56, 56.78) * mm});
            skLineSegment(sketch, "E3336", {"start": v(5.8, 57.28) * mm, "end": v(5.47, 57.12) * mm});
            skLineSegment(sketch, "E3337", {"start": v(6.11, 57.44) * mm, "end": v(5.8, 57.28) * mm});
            skLineSegment(sketch, "E3338", {"start": v(6.38, 57.6) * mm, "end": v(6.11, 57.44) * mm});
            skLineSegment(sketch, "E3339", {"start": v(6.6, 57.75) * mm, "end": v(6.38, 57.6) * mm});
            skLineSegment(sketch, "E3340", {"start": v(6.75, 57.88) * mm, "end": v(6.6, 57.75) * mm});
            skLineSegment(sketch, "E3341", {"start": v(7.08, 58.2) * mm, "end": v(6.75, 57.88) * mm});
            skArc(sketch, "E3342", {"start": v(2.6, 57.57) * mm, "mid": v(3.05, 57.03) * mm, "end": v(3.52, 56.5) * mm});
            skLineSegment(sketch, "E3343", {"start": v(3.02, 58.56) * mm, "end": v(2.6, 57.57) * mm});
            skLineSegment(sketch, "E3344", {"start": v(3.48, 59.41) * mm, "end": v(3.02, 58.56) * mm});
            skLineSegment(sketch, "E3345", {"start": v(3.69, 59.72) * mm, "end": v(3.48, 59.41) * mm});
            skLineSegment(sketch, "E3346", {"start": v(3.89, 60) * mm, "end": v(3.69, 59.72) * mm});
            skLineSegment(sketch, "E3347", {"start": v(4.09, 60.24) * mm, "end": v(3.89, 60) * mm});
            skLineSegment(sketch, "E3348", {"start": v(4.27, 60.44) * mm, "end": v(4.09, 60.24) * mm});
            skLineSegment(sketch, "E3349", {"start": v(4.42, 60.58) * mm, "end": v(4.27, 60.44) * mm});
            skLineSegment(sketch, "E3350", {"start": v(4.8, 60.85) * mm, "end": v(4.42, 60.58) * mm});
            skArc(sketch, "E3351", {"start": v(4.8, 60.85) * mm, "mid": v(5.1, 61.35) * mm, "end": v(4.98, 61.91) * mm});
            skArc(sketch, "E3352", {"start": v(4.6, 62.5) * mm, "mid": v(4.79, 62.2) * mm, "end": v(4.98, 61.92) * mm});
            skArc(sketch, "E3353", {"start": v(4.6, 62.5) * mm, "mid": v(4.13, 62.85) * mm, "end": v(3.56, 62.77) * mm});
            skLineSegment(sketch, "E3354", {"start": v(0.74, 62.11) * mm, "end": v(-0.34, 62.15) * mm});
            skLineSegment(sketch, "E3355", {"start": v(1.7, 62.18) * mm, "end": v(0.74, 62.11) * mm});
            skLineSegment(sketch, "E3356", {"start": v(2.07, 62.24) * mm, "end": v(1.7, 62.18) * mm});
            skLineSegment(sketch, "E3357", {"start": v(2.4, 62.3) * mm, "end": v(2.07, 62.24) * mm});
            skLineSegment(sketch, "E3358", {"start": v(2.7, 62.39) * mm, "end": v(2.4, 62.3) * mm});
            skLineSegment(sketch, "E3359", {"start": v(2.97, 62.47) * mm, "end": v(2.7, 62.39) * mm});
            skLineSegment(sketch, "E3360", {"start": v(3.15, 62.55) * mm, "end": v(2.97, 62.47) * mm});
            skLineSegment(sketch, "E3361", {"start": v(3.56, 62.77) * mm, "end": v(3.15, 62.55) * mm});
            skArc(sketch, "E3362", {"start": v(-0.92, 63.43) * mm, "mid": v(-0.64, 62.78) * mm, "end": v(-0.34, 62.15) * mm});
            skLineSegment(sketch, "E3363", {"start": v(-0.24, 64.26) * mm, "end": v(-0.92, 63.43) * mm});
            skLineSegment(sketch, "E3364", {"start": v(0.44, 64.94) * mm, "end": v(-0.24, 64.26) * mm});
            skLineSegment(sketch, "E3365", {"start": v(0.73, 65.18) * mm, "end": v(0.44, 64.94) * mm});
            skLineSegment(sketch, "E3366", {"start": v(1, 65.4) * mm, "end": v(0.73, 65.18) * mm});
            skLineSegment(sketch, "E3367", {"start": v(1.26, 65.57) * mm, "end": v(1, 65.4) * mm});
            skLineSegment(sketch, "E3368", {"start": v(1.49, 65.7) * mm, "end": v(1.26, 65.57) * mm});
            skLineSegment(sketch, "E3369", {"start": v(1.67, 65.8) * mm, "end": v(1.49, 65.7) * mm});
            skLineSegment(sketch, "E3370", {"start": v(2.1, 65.96) * mm, "end": v(1.67, 65.8) * mm});
            skArc(sketch, "E3371", {"start": v(2.1, 65.96) * mm, "mid": v(2.54, 66.34) * mm, "end": v(2.58, 66.92) * mm});
            skArc(sketch, "E3372", {"start": v(2.39, 67.6) * mm, "mid": v(2.48, 67.26) * mm, "end": v(2.58, 66.92) * mm});
            skArc(sketch, "E3373", {"start": v(2.39, 67.6) * mm, "mid": v(2.03, 68.06) * mm, "end": v(1.46, 68.15) * mm});
            skLineSegment(sketch, "E3374", {"start": v(-1.43, 68.3) * mm, "end": v(-2.45, 68.64) * mm});
            skLineSegment(sketch, "E3375", {"start": v(-0.49, 68.1) * mm, "end": v(-1.43, 68.3) * mm});
            skLineSegment(sketch, "E3376", {"start": v(-0.12, 68.05) * mm, "end": v(-0.49, 68.1) * mm});
            skLineSegment(sketch, "E3377", {"start": v(0.23, 68.02) * mm, "end": v(-0.12, 68.05) * mm});
            skLineSegment(sketch, "E3378", {"start": v(0.54, 68.02) * mm, "end": v(0.23, 68.02) * mm});
            skLineSegment(sketch, "E3379", {"start": v(0.8, 68.02) * mm, "end": v(0.54, 68.02) * mm});
            skLineSegment(sketch, "E3380", {"start": v(1, 68.05) * mm, "end": v(0.8, 68.02) * mm});
            skLineSegment(sketch, "E3381", {"start": v(1.46, 68.15) * mm, "end": v(1, 68.05) * mm});
            skArc(sketch, "E3382", {"start": v(-2.65, 70.03) * mm, "mid": v(-2.56, 69.34) * mm, "end": v(-2.45, 68.64) * mm});
            skLineSegment(sketch, "E3383", {"start": v(-1.77, 70.64) * mm, "end": v(-2.65, 70.03) * mm});
            skLineSegment(sketch, "E3384", {"start": v(-0.92, 71.1) * mm, "end": v(-1.77, 70.64) * mm});
            skLineSegment(sketch, "E3385", {"start": v(-0.58, 71.26) * mm, "end": v(-0.92, 71.1) * mm});
            skLineSegment(sketch, "E3386", {"start": v(-0.26, 71.38) * mm, "end": v(-0.58, 71.26) * mm});
            skLineSegment(sketch, "E3387", {"start": v(0.04, 71.48) * mm, "end": v(-0.26, 71.38) * mm});
            skLineSegment(sketch, "E3388", {"start": v(0.3, 71.54) * mm, "end": v(0.04, 71.48) * mm});
            skLineSegment(sketch, "E3389", {"start": v(0.5, 71.58) * mm, "end": v(0.3, 71.54) * mm});
            skLineSegment(sketch, "E3390", {"start": v(0.96, 71.6) * mm, "end": v(0.5, 71.58) * mm});
            skArc(sketch, "E3391", {"start": v(0.96, 71.6) * mm, "mid": v(1.49, 71.86) * mm, "end": v(1.7, 72.4) * mm});
            skArc(sketch, "E3392", {"start": v(1.7, 73.1) * mm, "mid": v(1.7, 72.75) * mm, "end": v(1.7, 72.4) * mm});
            skArc(sketch, "E3393", {"start": v(1.7, 73.1) * mm, "mid": v(1.49, 73.65) * mm, "end": v(0.96, 73.9) * mm});
            skLineSegment(sketch, "E3394", {"start": v(-1.77, 74.86) * mm, "end": v(-2.65, 75.47) * mm});
            skLineSegment(sketch, "E3395", {"start": v(-0.92, 74.4) * mm, "end": v(-1.77, 74.86) * mm});
            skLineSegment(sketch, "E3396", {"start": v(-0.58, 74.25) * mm, "end": v(-0.92, 74.4) * mm});
            skLineSegment(sketch, "E3397", {"start": v(-0.26, 74.12) * mm, "end": v(-0.58, 74.25) * mm});
            skLineSegment(sketch, "E3398", {"start": v(0.04, 74.03) * mm, "end": v(-0.26, 74.12) * mm});
            skLineSegment(sketch, "E3399", {"start": v(0.3, 73.96) * mm, "end": v(0.04, 74.03) * mm});
            skLineSegment(sketch, "E3400", {"start": v(0.5, 73.92) * mm, "end": v(0.3, 73.96) * mm});
            skLineSegment(sketch, "E3401", {"start": v(0.96, 73.9) * mm, "end": v(0.5, 73.92) * mm});
            skArc(sketch, "E3402", {"start": v(-2.45, 76.86) * mm, "mid": v(-2.56, 76.17) * mm, "end": v(-2.65, 75.47) * mm});
            skLineSegment(sketch, "E3403", {"start": v(-1.43, 77.2) * mm, "end": v(-2.45, 76.86) * mm});
            skLineSegment(sketch, "E3404", {"start": v(-0.49, 77.4) * mm, "end": v(-1.43, 77.2) * mm});
            skLineSegment(sketch, "E3405", {"start": v(-0.12, 77.45) * mm, "end": v(-0.49, 77.4) * mm});
            skLineSegment(sketch, "E3406", {"start": v(0.23, 77.48) * mm, "end": v(-0.12, 77.45) * mm});
            skLineSegment(sketch, "E3407", {"start": v(0.54, 77.49) * mm, "end": v(0.23, 77.48) * mm});
            skLineSegment(sketch, "E3408", {"start": v(0.8, 77.48) * mm, "end": v(0.54, 77.49) * mm});
            skLineSegment(sketch, "E3409", {"start": v(1, 77.46) * mm, "end": v(0.8, 77.48) * mm});
            skLineSegment(sketch, "E3410", {"start": v(1.46, 77.36) * mm, "end": v(1, 77.46) * mm});
            skArc(sketch, "E3411", {"start": v(1.46, 77.36) * mm, "mid": v(2.03, 77.44) * mm, "end": v(2.39, 77.9) * mm});
            skArc(sketch, "E3412", {"start": v(2.58, 78.58) * mm, "mid": v(2.48, 78.25) * mm, "end": v(2.39, 77.9) * mm});
            skArc(sketch, "E3413", {"start": v(2.58, 78.58) * mm, "mid": v(2.54, 79.16) * mm, "end": v(2.1, 79.55) * mm});
            skLineSegment(sketch, "E3414", {"start": v(-0.24, 81.24) * mm, "end": v(-0.92, 82.08) * mm});
            skLineSegment(sketch, "E3415", {"start": v(0.44, 80.56) * mm, "end": v(-0.24, 81.24) * mm});
            skLineSegment(sketch, "E3416", {"start": v(0.73, 80.32) * mm, "end": v(0.44, 80.56) * mm});
            skLineSegment(sketch, "E3417", {"start": v(1, 80.1) * mm, "end": v(0.73, 80.32) * mm});
            skLineSegment(sketch, "E3418", {"start": v(1.26, 79.93) * mm, "end": v(1, 80.1) * mm});
            skLineSegment(sketch, "E3419", {"start": v(1.49, 79.8) * mm, "end": v(1.26, 79.93) * mm});
            skLineSegment(sketch, "E3420", {"start": v(1.67, 79.7) * mm, "end": v(1.49, 79.8) * mm});
            skLineSegment(sketch, "E3421", {"start": v(2.1, 79.55) * mm, "end": v(1.67, 79.7) * mm});
            skArc(sketch, "E3422", {"start": v(-0.34, 83.36) * mm, "mid": v(-0.64, 82.72) * mm, "end": v(-0.92, 82.08) * mm});
            skLineSegment(sketch, "E3423", {"start": v(0.74, 83.39) * mm, "end": v(-0.34, 83.36) * mm});
            skLineSegment(sketch, "E3424", {"start": v(1.7, 83.32) * mm, "end": v(0.74, 83.39) * mm});
            skLineSegment(sketch, "E3425", {"start": v(2.07, 83.26) * mm, "end": v(1.7, 83.32) * mm});
            skLineSegment(sketch, "E3426", {"start": v(2.4, 83.2) * mm, "end": v(2.07, 83.26) * mm});
            skLineSegment(sketch, "E3427", {"start": v(2.7, 83.11) * mm, "end": v(2.4, 83.2) * mm});
            skLineSegment(sketch, "E3428", {"start": v(2.97, 83.03) * mm, "end": v(2.7, 83.11) * mm});
            skLineSegment(sketch, "E3429", {"start": v(3.15, 82.95) * mm, "end": v(2.97, 83.03) * mm});
            skLineSegment(sketch, "E3430", {"start": v(3.56, 82.73) * mm, "end": v(3.15, 82.95) * mm});
            skArc(sketch, "E3431", {"start": v(3.56, 82.73) * mm, "mid": v(4.13, 82.65) * mm, "end": v(4.6, 83) * mm});
            skArc(sketch, "E3432", {"start": v(4.98, 83.59) * mm, "mid": v(4.79, 83.3) * mm, "end": v(4.6, 83) * mm});
            skArc(sketch, "E3433", {"start": v(4.98, 83.59) * mm, "mid": v(5.1, 84.16) * mm, "end": v(4.8, 84.65) * mm});
            skLineSegment(sketch, "E3434", {"start": v(3.02, 86.94) * mm, "end": v(2.6, 87.93) * mm});
            skLineSegment(sketch, "E3435", {"start": v(3.48, 86.1) * mm, "end": v(3.02, 86.94) * mm});
            skLineSegment(sketch, "E3436", {"start": v(3.69, 85.78) * mm, "end": v(3.48, 86.1) * mm});
            skLineSegment(sketch, "E3437", {"start": v(3.89, 85.5) * mm, "end": v(3.69, 85.78) * mm});
            skLineSegment(sketch, "E3438", {"start": v(4.09, 85.26) * mm, "end": v(3.89, 85.5) * mm});
            skLineSegment(sketch, "E3439", {"start": v(4.27, 85.06) * mm, "end": v(4.09, 85.26) * mm});
            skLineSegment(sketch, "E3440", {"start": v(4.42, 84.93) * mm, "end": v(4.27, 85.06) * mm});
            skLineSegment(sketch, "E3441", {"start": v(4.8, 84.65) * mm, "end": v(4.42, 84.93) * mm});
            skArc(sketch, "E3442", {"start": v(3.52, 89) * mm, "mid": v(3.05, 88.47) * mm, "end": v(2.6, 87.93) * mm});
            skLineSegment(sketch, "E3443", {"start": v(4.56, 88.72) * mm, "end": v(3.52, 89) * mm});
            skLineSegment(sketch, "E3444", {"start": v(5.47, 88.38) * mm, "end": v(4.56, 88.72) * mm});
            skLineSegment(sketch, "E3445", {"start": v(5.8, 88.23) * mm, "end": v(5.47, 88.38) * mm});
            skLineSegment(sketch, "E3446", {"start": v(6.11, 88.06) * mm, "end": v(5.8, 88.23) * mm});
            skLineSegment(sketch, "E3447", {"start": v(6.38, 87.9) * mm, "end": v(6.11, 88.06) * mm});
            skLineSegment(sketch, "E3448", {"start": v(6.6, 87.75) * mm, "end": v(6.38, 87.9) * mm});
            skLineSegment(sketch, "E3449", {"start": v(6.75, 87.62) * mm, "end": v(6.6, 87.75) * mm});
            skLineSegment(sketch, "E3450", {"start": v(7.08, 87.3) * mm, "end": v(6.75, 87.62) * mm});
            skArc(sketch, "E3451", {"start": v(7.08, 87.3) * mm, "mid": v(7.61, 87.06) * mm, "end": v(8.16, 87.26) * mm});
            skArc(sketch, "E3452", {"start": v(8.7, 87.72) * mm, "mid": v(8.42, 87.49) * mm, "end": v(8.16, 87.26) * mm});
            skArc(sketch, "E3453", {"start": v(8.7, 87.72) * mm, "mid": v(8.96, 88.23) * mm, "end": v(8.8, 88.79) * mm});
            skLineSegment(sketch, "E3454", {"start": v(7.75, 91.49) * mm, "end": v(7.63, 92.55) * mm});
            skLineSegment(sketch, "E3455", {"start": v(7.96, 90.54) * mm, "end": v(7.75, 91.49) * mm});
            skLineSegment(sketch, "E3456", {"start": v(8.07, 90.18) * mm, "end": v(7.96, 90.54) * mm});
            skLineSegment(sketch, "E3457", {"start": v(8.18, 89.86) * mm, "end": v(8.07, 90.18) * mm});
            skLineSegment(sketch, "E3458", {"start": v(8.3, 89.57) * mm, "end": v(8.18, 89.86) * mm});
            skLineSegment(sketch, "E3459", {"start": v(8.42, 89.33) * mm, "end": v(8.3, 89.57) * mm});
            skLineSegment(sketch, "E3460", {"start": v(8.53, 89.16) * mm, "end": v(8.42, 89.33) * mm});
            skLineSegment(sketch, "E3461", {"start": v(8.8, 88.79) * mm, "end": v(8.53, 89.16) * mm});
            skArc(sketch, "E3462", {"start": v(8.82, 93.31) * mm, "mid": v(8.22, 92.94) * mm, "end": v(7.63, 92.55) * mm});
            skLineSegment(sketch, "E3463", {"start": v(9.74, 92.76) * mm, "end": v(8.82, 93.31) * mm});
            skLineSegment(sketch, "E3464", {"start": v(10.5, 92.18) * mm, "end": v(9.74, 92.76) * mm});
            skLineSegment(sketch, "E3465", {"start": v(10.79, 91.93) * mm, "end": v(10.5, 92.18) * mm});
            skLineSegment(sketch, "E3466", {"start": v(11.04, 91.7) * mm, "end": v(10.79, 91.93) * mm});
            skLineSegment(sketch, "E3467", {"start": v(11.25, 91.46) * mm, "end": v(11.04, 91.7) * mm});
            skLineSegment(sketch, "E3468", {"start": v(11.42, 91.25) * mm, "end": v(11.25, 91.46) * mm});
            skLineSegment(sketch, "E3469", {"start": v(11.53, 91.09) * mm, "end": v(11.42, 91.25) * mm});
            skLineSegment(sketch, "E3470", {"start": v(11.75, 90.68) * mm, "end": v(11.53, 91.09) * mm});
            skArc(sketch, "E3471", {"start": v(11.75, 90.68) * mm, "mid": v(12.2, 90.3) * mm, "end": v(12.77, 90.34) * mm});
            skArc(sketch, "E3472", {"start": v(13.41, 90.63) * mm, "mid": v(13.1, 90.49) * mm, "end": v(12.77, 90.34) * mm});
            skArc(sketch, "E3473", {"start": v(13.41, 90.63) * mm, "mid": v(13.82, 91.05) * mm, "end": v(13.83, 91.63) * mm});
            skLineSegment(sketch, "E3474", {"start": v(13.57, 94.51) * mm, "end": v(13.76, 95.57) * mm});
            skLineSegment(sketch, "E3475", {"start": v(13.5, 93.55) * mm, "end": v(13.57, 94.51) * mm});
            skLineSegment(sketch, "E3476", {"start": v(13.5, 93.18) * mm, "end": v(13.5, 93.55) * mm});
            skLineSegment(sketch, "E3477", {"start": v(13.53, 92.83) * mm, "end": v(13.5, 93.18) * mm});
            skLineSegment(sketch, "E3478", {"start": v(13.57, 92.52) * mm, "end": v(13.53, 92.83) * mm});
            skLineSegment(sketch, "E3479", {"start": v(13.61, 92.26) * mm, "end": v(13.57, 92.52) * mm});
            skLineSegment(sketch, "E3480", {"start": v(13.66, 92.06) * mm, "end": v(13.61, 92.26) * mm});
            skLineSegment(sketch, "E3481", {"start": v(13.83, 91.63) * mm, "end": v(13.66, 92.06) * mm});
            skArc(sketch, "E3482", {"start": v(15.1, 95.97) * mm, "mid": v(14.43, 95.78) * mm, "end": v(13.76, 95.57) * mm});
            skLineSegment(sketch, "E3483", {"start": v(15.84, 95.18) * mm, "end": v(15.1, 95.97) * mm});
            skLineSegment(sketch, "E3484", {"start": v(16.42, 94.4) * mm, "end": v(15.84, 95.18) * mm});
            skLineSegment(sketch, "E3485", {"start": v(16.61, 94.09) * mm, "end": v(16.42, 94.4) * mm});
            skLineSegment(sketch, "E3486", {"start": v(16.78, 93.79) * mm, "end": v(16.61, 94.09) * mm});
            skLineSegment(sketch, "E3487", {"start": v(16.92, 93.5) * mm, "end": v(16.78, 93.79) * mm});
            skLineSegment(sketch, "E3488", {"start": v(17.02, 93.26) * mm, "end": v(16.92, 93.5) * mm});
            skLineSegment(sketch, "E3489", {"start": v(17.09, 93.07) * mm, "end": v(17.02, 93.26) * mm});
            skLineSegment(sketch, "E3490", {"start": v(17.18, 92.61) * mm, "end": v(17.09, 93.07) * mm});
            skArc(sketch, "E3491", {"start": v(17.18, 92.61) * mm, "mid": v(17.5, 92.13) * mm, "end": v(18.07, 92) * mm});
            skArc(sketch, "E3492", {"start": v(18.77, 92.1) * mm, "mid": v(18.42, 92.05) * mm, "end": v(18.07, 92) * mm});
            skArc(sketch, "E3493", {"start": v(18.77, 92.1) * mm, "mid": v(19.27, 92.38) * mm, "end": v(19.44, 92.94) * mm});
            skLineSegment(sketch, "E3494", {"start": v(20.01, 95.78) * mm, "end": v(20.49, 96.74) * mm});
            skLineSegment(sketch, "E3495", {"start": v(19.68, 94.87) * mm, "end": v(20.01, 95.78) * mm});
            skLineSegment(sketch, "E3496", {"start": v(19.57, 94.51) * mm, "end": v(19.68, 94.87) * mm});
            skLineSegment(sketch, "E3497", {"start": v(19.5, 94.18) * mm, "end": v(19.57, 94.51) * mm});
            skLineSegment(sketch, "E3498", {"start": v(19.44, 93.87) * mm, "end": v(19.5, 94.18) * mm});
            skLineSegment(sketch, "E3499", {"start": v(19.42, 93.6) * mm, "end": v(19.44, 93.87) * mm});
            skLineSegment(sketch, "E3500", {"start": v(19.4, 93.4) * mm, "end": v(19.42, 93.6) * mm});
            skLineSegment(sketch, "E3501", {"start": v(19.44, 92.94) * mm, "end": v(19.4, 93.4) * mm});
            skArc(sketch, "E3502", {"start": v(21.9, 96.74) * mm, "mid": v(21.2, 96.75) * mm, "end": v(20.49, 96.74) * mm});
            skLineSegment(sketch, "E3503", {"start": v(22.37, 95.78) * mm, "end": v(21.9, 96.74) * mm});
            skLineSegment(sketch, "E3504", {"start": v(22.7, 94.87) * mm, "end": v(22.37, 95.78) * mm});
            skLineSegment(sketch, "E3505", {"start": v(22.81, 94.51) * mm, "end": v(22.7, 94.87) * mm});
            skLineSegment(sketch, "E3506", {"start": v(22.89, 94.18) * mm, "end": v(22.81, 94.51) * mm});
            skLineSegment(sketch, "E3507", {"start": v(22.94, 93.87) * mm, "end": v(22.89, 94.18) * mm});
            skLineSegment(sketch, "E3508", {"start": v(22.97, 93.6) * mm, "end": v(22.94, 93.87) * mm});
            skLineSegment(sketch, "E3509", {"start": v(22.98, 93.4) * mm, "end": v(22.97, 93.6) * mm});
            skLineSegment(sketch, "E3510", {"start": v(22.94, 92.94) * mm, "end": v(22.98, 93.4) * mm});
            skArc(sketch, "E3511", {"start": v(22.94, 92.94) * mm, "mid": v(23.11, 92.38) * mm, "end": v(23.62, 92.1) * mm});
            skArc(sketch, "E3512", {"start": v(24.32, 92) * mm, "mid": v(23.97, 92.05) * mm, "end": v(23.62, 92.1) * mm});
            skArc(sketch, "E3513", {"start": v(24.32, 92) * mm, "mid": v(24.88, 92.13) * mm, "end": v(25.2, 92.61) * mm});
            skLineSegment(sketch, "E3514", {"start": v(26.55, 95.18) * mm, "end": v(27.28, 95.97) * mm});
            skLineSegment(sketch, "E3515", {"start": v(25.97, 94.4) * mm, "end": v(26.55, 95.18) * mm});
            skLineSegment(sketch, "E3516", {"start": v(25.77, 94.09) * mm, "end": v(25.97, 94.4) * mm});
            skLineSegment(sketch, "E3517", {"start": v(25.6, 93.79) * mm, "end": v(25.77, 94.09) * mm});
            skLineSegment(sketch, "E3518", {"start": v(25.46, 93.5) * mm, "end": v(25.6, 93.79) * mm});
            skLineSegment(sketch, "E3519", {"start": v(25.36, 93.26) * mm, "end": v(25.46, 93.5) * mm});
            skLineSegment(sketch, "E3520", {"start": v(25.3, 93.07) * mm, "end": v(25.36, 93.26) * mm});
            skLineSegment(sketch, "E3521", {"start": v(25.2, 92.61) * mm, "end": v(25.3, 93.07) * mm});
            skArc(sketch, "E3522", {"start": v(28.63, 95.57) * mm, "mid": v(27.95, 95.78) * mm, "end": v(27.28, 95.97) * mm});
            skLineSegment(sketch, "E3523", {"start": v(28.81, 94.51) * mm, "end": v(28.63, 95.57) * mm});
            skLineSegment(sketch, "E3524", {"start": v(28.88, 93.55) * mm, "end": v(28.81, 94.51) * mm});
            skLineSegment(sketch, "E3525", {"start": v(28.88, 93.18) * mm, "end": v(28.88, 93.55) * mm});
            skLineSegment(sketch, "E3526", {"start": v(28.86, 92.83) * mm, "end": v(28.88, 93.18) * mm});
            skLineSegment(sketch, "E3527", {"start": v(28.82, 92.52) * mm, "end": v(28.86, 92.83) * mm});
            skLineSegment(sketch, "E3528", {"start": v(28.77, 92.26) * mm, "end": v(28.82, 92.52) * mm});
            skLineSegment(sketch, "E3529", {"start": v(28.72, 92.06) * mm, "end": v(28.77, 92.26) * mm});
            skLineSegment(sketch, "E3530", {"start": v(28.56, 91.63) * mm, "end": v(28.72, 92.06) * mm});
            skArc(sketch, "E3531", {"start": v(28.56, 91.63) * mm, "mid": v(28.56, 91.05) * mm, "end": v(28.97, 90.63) * mm});
            skArc(sketch, "E3532", {"start": v(29.61, 90.34) * mm, "mid": v(29.3, 90.49) * mm, "end": v(28.97, 90.63) * mm});
            skArc(sketch, "E3533", {"start": v(29.61, 90.34) * mm, "mid": v(30.2, 90.3) * mm, "end": v(30.64, 90.68) * mm});
            skLineSegment(sketch, "E3534", {"start": v(32.65, 92.76) * mm, "end": v(33.57, 93.31) * mm});
            skLineSegment(sketch, "E3535", {"start": v(31.88, 92.18) * mm, "end": v(32.65, 92.76) * mm});
            skLineSegment(sketch, "E3536", {"start": v(31.6, 91.93) * mm, "end": v(31.88, 92.18) * mm});
            skLineSegment(sketch, "E3537", {"start": v(31.35, 91.7) * mm, "end": v(31.6, 91.93) * mm});
            skLineSegment(sketch, "E3538", {"start": v(31.14, 91.46) * mm, "end": v(31.35, 91.7) * mm});
            skLineSegment(sketch, "E3539", {"start": v(30.97, 91.25) * mm, "end": v(31.14, 91.46) * mm});
            skLineSegment(sketch, "E3540", {"start": v(30.86, 91.09) * mm, "end": v(30.97, 91.25) * mm});
            skLineSegment(sketch, "E3541", {"start": v(30.64, 90.68) * mm, "end": v(30.86, 91.09) * mm});
            skArc(sketch, "E3542", {"start": v(34.75, 92.55) * mm, "mid": v(34.17, 92.94) * mm, "end": v(33.57, 93.31) * mm});
            skLineSegment(sketch, "E3543", {"start": v(34.63, 91.49) * mm, "end": v(34.75, 92.55) * mm});
            skLineSegment(sketch, "E3544", {"start": v(34.43, 90.54) * mm, "end": v(34.63, 91.49) * mm});
            skLineSegment(sketch, "E3545", {"start": v(34.32, 90.18) * mm, "end": v(34.43, 90.54) * mm});
            skLineSegment(sketch, "E3546", {"start": v(34.2, 89.86) * mm, "end": v(34.32, 90.18) * mm});
            skLineSegment(sketch, "E3547", {"start": v(34.08, 89.57) * mm, "end": v(34.2, 89.86) * mm});
            skLineSegment(sketch, "E3548", {"start": v(33.96, 89.33) * mm, "end": v(34.08, 89.57) * mm});
            skLineSegment(sketch, "E3549", {"start": v(33.86, 89.16) * mm, "end": v(33.96, 89.33) * mm});
            skLineSegment(sketch, "E3550", {"start": v(33.58, 88.79) * mm, "end": v(33.86, 89.16) * mm});
            skArc(sketch, "E3551", {"start": v(33.58, 88.79) * mm, "mid": v(33.42, 88.23) * mm, "end": v(33.7, 87.72) * mm});
            skArc(sketch, "E3552", {"start": v(34.23, 87.26) * mm, "mid": v(33.96, 87.49) * mm, "end": v(33.7, 87.72) * mm});
            skArc(sketch, "E3553", {"start": v(34.23, 87.26) * mm, "mid": v(34.77, 87.06) * mm, "end": v(35.3, 87.3) * mm});
            skLineSegment(sketch, "E3554", {"start": v(37.82, 88.72) * mm, "end": v(38.86, 89) * mm});
            skLineSegment(sketch, "E3555", {"start": v(36.92, 88.38) * mm, "end": v(37.82, 88.72) * mm});
            skLineSegment(sketch, "E3556", {"start": v(36.58, 88.23) * mm, "end": v(36.92, 88.38) * mm});
            skLineSegment(sketch, "E3557", {"start": v(36.27, 88.06) * mm, "end": v(36.58, 88.23) * mm});
            skLineSegment(sketch, "E3558", {"start": v(36, 87.9) * mm, "end": v(36.27, 88.06) * mm});
            skLineSegment(sketch, "E3559", {"start": v(35.79, 87.75) * mm, "end": v(36, 87.9) * mm});
            skLineSegment(sketch, "E3560", {"start": v(35.63, 87.62) * mm, "end": v(35.79, 87.75) * mm});
            skLineSegment(sketch, "E3561", {"start": v(35.3, 87.3) * mm, "end": v(35.63, 87.62) * mm});
            skArc(sketch, "E3562", {"start": v(39.78, 87.93) * mm, "mid": v(39.33, 88.47) * mm, "end": v(38.86, 89) * mm});
            skLineSegment(sketch, "E3563", {"start": v(39.37, 86.94) * mm, "end": v(39.78, 87.93) * mm});
            skLineSegment(sketch, "E3564", {"start": v(38.9, 86.1) * mm, "end": v(39.37, 86.94) * mm});
            skLineSegment(sketch, "E3565", {"start": v(38.7, 85.78) * mm, "end": v(38.9, 86.1) * mm});
            skLineSegment(sketch, "E3566", {"start": v(38.5, 85.5) * mm, "end": v(38.7, 85.78) * mm});
            skLineSegment(sketch, "E3567", {"start": v(38.3, 85.26) * mm, "end": v(38.5, 85.5) * mm});
            skLineSegment(sketch, "E3568", {"start": v(38.11, 85.06) * mm, "end": v(38.3, 85.26) * mm});
            skLineSegment(sketch, "E3569", {"start": v(37.97, 84.93) * mm, "end": v(38.11, 85.06) * mm});
            skLineSegment(sketch, "E3570", {"start": v(37.6, 84.65) * mm, "end": v(37.97, 84.93) * mm});
            skArc(sketch, "E3571", {"start": v(37.6, 84.65) * mm, "mid": v(37.29, 84.16) * mm, "end": v(37.4, 83.59) * mm});
            skArc(sketch, "E3572", {"start": v(37.78, 83) * mm, "mid": v(37.6, 83.3) * mm, "end": v(37.4, 83.59) * mm});
            skArc(sketch, "E3573", {"start": v(37.78, 83) * mm, "mid": v(38.25, 82.65) * mm, "end": v(38.83, 82.73) * mm});
            skLineSegment(sketch, "E3574", {"start": v(41.65, 83.39) * mm, "end": v(42.72, 83.36) * mm});
            skLineSegment(sketch, "E3575", {"start": v(40.68, 83.32) * mm, "end": v(41.65, 83.39) * mm});
            skLineSegment(sketch, "E3576", {"start": v(40.31, 83.26) * mm, "end": v(40.68, 83.32) * mm});
            skLineSegment(sketch, "E3577", {"start": v(39.98, 83.2) * mm, "end": v(40.31, 83.26) * mm});
            skLineSegment(sketch, "E3578", {"start": v(39.68, 83.11) * mm, "end": v(39.98, 83.2) * mm});
            skLineSegment(sketch, "E3579", {"start": v(39.42, 83.03) * mm, "end": v(39.68, 83.11) * mm});
            skLineSegment(sketch, "E3580", {"start": v(39.24, 82.95) * mm, "end": v(39.42, 83.03) * mm});
            skLineSegment(sketch, "E3581", {"start": v(38.83, 82.73) * mm, "end": v(39.24, 82.95) * mm});
            skArc(sketch, "E3582", {"start": v(43.3, 82.08) * mm, "mid": v(43.02, 82.72) * mm, "end": v(42.72, 83.36) * mm});
            skLineSegment(sketch, "E3583", {"start": v(42.63, 81.24) * mm, "end": v(43.3, 82.08) * mm});
            skLineSegment(sketch, "E3584", {"start": v(41.94, 80.56) * mm, "end": v(42.63, 81.24) * mm});
            skLineSegment(sketch, "E3585", {"start": v(41.66, 80.32) * mm, "end": v(41.94, 80.56) * mm});
            skLineSegment(sketch, "E3586", {"start": v(41.39, 80.1) * mm, "end": v(41.66, 80.32) * mm});
            skLineSegment(sketch, "E3587", {"start": v(41.13, 79.93) * mm, "end": v(41.39, 80.1) * mm});
            skLineSegment(sketch, "E3588", {"start": v(40.9, 79.8) * mm, "end": v(41.13, 79.93) * mm});
            skLineSegment(sketch, "E3589", {"start": v(40.72, 79.7) * mm, "end": v(40.9, 79.8) * mm});
            skLineSegment(sketch, "E3590", {"start": v(40.28, 79.55) * mm, "end": v(40.72, 79.7) * mm});
            skArc(sketch, "E3591", {"start": v(40.28, 79.55) * mm, "mid": v(39.85, 79.16) * mm, "end": v(39.8, 78.58) * mm});
            skArc(sketch, "E3592", {"start": v(40, 77.9) * mm, "mid": v(39.9, 78.25) * mm, "end": v(39.8, 78.58) * mm});
            skArc(sketch, "E3593", {"start": v(40, 77.9) * mm, "mid": v(40.35, 77.44) * mm, "end": v(40.93, 77.36) * mm});
            skLineSegment(sketch, "E3594", {"start": v(43.82, 77.2) * mm, "end": v(44.84, 76.86) * mm});
            skLineSegment(sketch, "E3595", {"start": v(42.87, 77.4) * mm, "end": v(43.82, 77.2) * mm});
            skLineSegment(sketch, "E3596", {"start": v(42.5, 77.45) * mm, "end": v(42.87, 77.4) * mm});
            skLineSegment(sketch, "E3597", {"start": v(42.16, 77.48) * mm, "end": v(42.5, 77.45) * mm});
            skLineSegment(sketch, "E3598", {"start": v(41.85, 77.49) * mm, "end": v(42.16, 77.48) * mm});
            skLineSegment(sketch, "E3599", {"start": v(41.58, 77.48) * mm, "end": v(41.85, 77.49) * mm});
            skLineSegment(sketch, "E3600", {"start": v(41.38, 77.46) * mm, "end": v(41.58, 77.48) * mm});
            skLineSegment(sketch, "E3601", {"start": v(40.93, 77.36) * mm, "end": v(41.38, 77.46) * mm});
            skArc(sketch, "E3602", {"start": v(45.04, 75.47) * mm, "mid": v(44.95, 76.17) * mm, "end": v(44.84, 76.86) * mm});
            skLineSegment(sketch, "E3603", {"start": v(44.15, 74.86) * mm, "end": v(45.04, 75.47) * mm});
            skLineSegment(sketch, "E3604", {"start": v(43.3, 74.4) * mm, "end": v(44.15, 74.86) * mm});
            skLineSegment(sketch, "E3605", {"start": v(42.96, 74.25) * mm, "end": v(43.3, 74.4) * mm});
            skLineSegment(sketch, "E3606", {"start": v(42.64, 74.12) * mm, "end": v(42.96, 74.25) * mm});
            skLineSegment(sketch, "E3607", {"start": v(42.34, 74.03) * mm, "end": v(42.64, 74.12) * mm});
            skLineSegment(sketch, "E3608", {"start": v(42.08, 73.96) * mm, "end": v(42.34, 74.03) * mm});
            skLineSegment(sketch, "E3609", {"start": v(41.89, 73.92) * mm, "end": v(42.08, 73.96) * mm});
            skLineSegment(sketch, "E3610", {"start": v(41.42, 73.9) * mm, "end": v(41.89, 73.92) * mm});
            skArc(sketch, "E3611", {"start": v(41.42, 73.9) * mm, "mid": v(40.9, 73.65) * mm, "end": v(40.69, 73.1) * mm});
            skArc(sketch, "E3612", {"start": v(40.69, 72.4) * mm, "mid": v(40.7, 72.75) * mm, "end": v(40.69, 73.1) * mm});
            skArc(sketch, "E3613", {"start": v(40.69, 72.4) * mm, "mid": v(40.9, 71.86) * mm, "end": v(41.42, 71.6) * mm});
            skLineSegment(sketch, "E3614", {"start": v(44.15, 70.64) * mm, "end": v(45.04, 70.03) * mm});
            skLineSegment(sketch, "E3615", {"start": v(43.3, 71.1) * mm, "end": v(44.15, 70.64) * mm});
            skLineSegment(sketch, "E3616", {"start": v(42.96, 71.26) * mm, "end": v(43.3, 71.1) * mm});
            skLineSegment(sketch, "E3617", {"start": v(42.64, 71.38) * mm, "end": v(42.96, 71.26) * mm});
            skLineSegment(sketch, "E3618", {"start": v(42.08, 71.54) * mm, "end": v(42.34, 71.48) * mm});
            skLineSegment(sketch, "E3619", {"start": v(41.89, 71.58) * mm, "end": v(42.08, 71.54) * mm});
            skLineSegment(sketch, "E3620", {"start": v(41.42, 71.6) * mm, "end": v(41.89, 71.58) * mm});
            skArc(sketch, "E3621", {"start": v(44.84, 68.64) * mm, "mid": v(44.95, 69.34) * mm, "end": v(45.04, 70.03) * mm});
            skLineSegment(sketch, "E3622", {"start": v(43.82, 68.3) * mm, "end": v(44.84, 68.64) * mm});
            skLineSegment(sketch, "E3623", {"start": v(42.87, 68.1) * mm, "end": v(43.82, 68.3) * mm});
            skLineSegment(sketch, "E3624", {"start": v(42.5, 68.05) * mm, "end": v(42.87, 68.1) * mm});
            skLineSegment(sketch, "E3625", {"start": v(42.16, 68.02) * mm, "end": v(42.5, 68.05) * mm});
            skLineSegment(sketch, "E3626", {"start": v(41.85, 68.02) * mm, "end": v(42.16, 68.02) * mm});
            skLineSegment(sketch, "E3627", {"start": v(41.58, 68.02) * mm, "end": v(41.85, 68.02) * mm});
            skLineSegment(sketch, "E3628", {"start": v(41.38, 68.05) * mm, "end": v(41.58, 68.02) * mm});
            skLineSegment(sketch, "E3629", {"start": v(40.93, 68.15) * mm, "end": v(41.38, 68.05) * mm});
            skArc(sketch, "E3630", {"start": v(40.93, 68.15) * mm, "mid": v(40.35, 68.06) * mm, "end": v(40, 67.6) * mm});
            skArc(sketch, "E3631", {"start": v(39.8, 66.92) * mm, "mid": v(39.9, 67.26) * mm, "end": v(40, 67.6) * mm});
            skArc(sketch, "E3632", {"start": v(39.8, 66.92) * mm, "mid": v(39.85, 66.34) * mm, "end": v(40.28, 65.96) * mm});
            skLineSegment(sketch, "E3633", {"start": v(42.63, 64.26) * mm, "end": v(43.3, 63.43) * mm});
            skLineSegment(sketch, "E3634", {"start": v(41.94, 64.94) * mm, "end": v(42.63, 64.26) * mm});
            skLineSegment(sketch, "E3635", {"start": v(41.66, 65.18) * mm, "end": v(41.94, 64.94) * mm});
            skLineSegment(sketch, "E3636", {"start": v(41.39, 65.4) * mm, "end": v(41.66, 65.18) * mm});
            skLineSegment(sketch, "E3637", {"start": v(41.13, 65.57) * mm, "end": v(41.39, 65.4) * mm});
            skLineSegment(sketch, "E3638", {"start": v(40.9, 65.7) * mm, "end": v(41.13, 65.57) * mm});
            skLineSegment(sketch, "E3639", {"start": v(40.72, 65.8) * mm, "end": v(40.9, 65.7) * mm});
            skLineSegment(sketch, "E3640", {"start": v(40.28, 65.96) * mm, "end": v(40.72, 65.8) * mm});
            skArc(sketch, "E3641", {"start": v(42.72, 62.15) * mm, "mid": v(43.02, 62.78) * mm, "end": v(43.3, 63.43) * mm});
            skLineSegment(sketch, "E3642", {"start": v(41.65, 62.11) * mm, "end": v(42.72, 62.15) * mm});
            skLineSegment(sketch, "E3643", {"start": v(40.68, 62.18) * mm, "end": v(41.65, 62.11) * mm});
            skLineSegment(sketch, "E3644", {"start": v(40.31, 62.24) * mm, "end": v(40.68, 62.18) * mm});
            skLineSegment(sketch, "E3645", {"start": v(39.98, 62.3) * mm, "end": v(40.31, 62.24) * mm});
            skLineSegment(sketch, "E3646", {"start": v(39.68, 62.39) * mm, "end": v(39.98, 62.3) * mm});
            skLineSegment(sketch, "E3647", {"start": v(39.42, 62.47) * mm, "end": v(39.68, 62.39) * mm});
            skLineSegment(sketch, "E3648", {"start": v(39.24, 62.55) * mm, "end": v(39.42, 62.47) * mm});
            skLineSegment(sketch, "E3649", {"start": v(38.83, 62.77) * mm, "end": v(39.24, 62.55) * mm});
            skArc(sketch, "E3650", {"start": v(38.83, 62.77) * mm, "mid": v(38.25, 62.85) * mm, "end": v(37.78, 62.5) * mm});
            skArc(sketch, "E3651", {"start": v(37.4, 61.91) * mm, "mid": v(37.6, 62.2) * mm, "end": v(37.78, 62.5) * mm});
            skArc(sketch, "E3652", {"start": v(37.4, 61.91) * mm, "mid": v(37.29, 61.35) * mm, "end": v(37.6, 60.85) * mm});
            skLineSegment(sketch, "E3653", {"start": v(39.37, 58.56) * mm, "end": v(39.78, 57.57) * mm});
            skLineSegment(sketch, "E3654", {"start": v(38.9, 59.41) * mm, "end": v(39.37, 58.56) * mm});
            skLineSegment(sketch, "E3655", {"start": v(38.7, 59.72) * mm, "end": v(38.9, 59.41) * mm});
            skLineSegment(sketch, "E3656", {"start": v(38.5, 60) * mm, "end": v(38.7, 59.72) * mm});
            skLineSegment(sketch, "E3657", {"start": v(38.3, 60.24) * mm, "end": v(38.5, 60) * mm});
            skLineSegment(sketch, "E3658", {"start": v(38.11, 60.44) * mm, "end": v(38.3, 60.24) * mm});
            skLineSegment(sketch, "E3659", {"start": v(37.97, 60.58) * mm, "end": v(38.11, 60.44) * mm});
            skLineSegment(sketch, "E3660", {"start": v(37.6, 60.85) * mm, "end": v(37.97, 60.58) * mm});
            skArc(sketch, "E3661", {"start": v(38.86, 56.5) * mm, "mid": v(39.33, 57.03) * mm, "end": v(39.78, 57.57) * mm});
            skLineSegment(sketch, "E3662", {"start": v(37.82, 56.78) * mm, "end": v(38.86, 56.5) * mm});
            skLineSegment(sketch, "E3663", {"start": v(36.92, 57.12) * mm, "end": v(37.82, 56.78) * mm});
            skLineSegment(sketch, "E3664", {"start": v(36.58, 57.28) * mm, "end": v(36.92, 57.12) * mm});
            skLineSegment(sketch, "E3665", {"start": v(36.27, 57.44) * mm, "end": v(36.58, 57.28) * mm});
            skLineSegment(sketch, "E3666", {"start": v(36, 57.6) * mm, "end": v(36.27, 57.44) * mm});
            skLineSegment(sketch, "E3667", {"start": v(35.79, 57.75) * mm, "end": v(36, 57.6) * mm});
            skLineSegment(sketch, "E3668", {"start": v(35.63, 57.88) * mm, "end": v(35.79, 57.75) * mm});
            skLineSegment(sketch, "E3669", {"start": v(35.3, 58.2) * mm, "end": v(35.63, 57.88) * mm});
            skArc(sketch, "E3670", {"start": v(35.3, 58.2) * mm, "mid": v(34.77, 58.45) * mm, "end": v(34.23, 58.25) * mm});
            skArc(sketch, "E3671", {"start": v(33.7, 57.79) * mm, "mid": v(33.96, 58.01) * mm, "end": v(34.23, 58.25) * mm});
            skArc(sketch, "E3672", {"start": v(33.7, 57.79) * mm, "mid": v(33.42, 57.27) * mm, "end": v(33.58, 56.71) * mm});
            skLineSegment(sketch, "E3673", {"start": v(34.63, 54.02) * mm, "end": v(34.75, 52.95) * mm});
            skLineSegment(sketch, "E3674", {"start": v(34.43, 54.96) * mm, "end": v(34.63, 54.02) * mm});
            skLineSegment(sketch, "E3675", {"start": v(34.32, 55.32) * mm, "end": v(34.43, 54.96) * mm});
            skLineSegment(sketch, "E3676", {"start": v(34.2, 55.64) * mm, "end": v(34.32, 55.32) * mm});
            skLineSegment(sketch, "E3677", {"start": v(34.08, 55.93) * mm, "end": v(34.2, 55.64) * mm});
            skLineSegment(sketch, "E3678", {"start": v(33.96, 56.17) * mm, "end": v(34.08, 55.93) * mm});
            skLineSegment(sketch, "E3679", {"start": v(33.86, 56.34) * mm, "end": v(33.96, 56.17) * mm});
            skLineSegment(sketch, "E3680", {"start": v(33.58, 56.71) * mm, "end": v(33.86, 56.34) * mm});
            skArc(sketch, "E3681", {"start": v(33.57, 52.19) * mm, "mid": v(34.17, 52.56) * mm, "end": v(34.75, 52.95) * mm});
            skLineSegment(sketch, "E3682", {"start": v(32.65, 52.74) * mm, "end": v(33.57, 52.19) * mm});
            skLineSegment(sketch, "E3683", {"start": v(31.88, 53.32) * mm, "end": v(32.65, 52.74) * mm});
            skLineSegment(sketch, "E3684", {"start": v(31.6, 53.57) * mm, "end": v(31.88, 53.32) * mm});
            skLineSegment(sketch, "E3685", {"start": v(31.35, 53.81) * mm, "end": v(31.6, 53.57) * mm});
            skLineSegment(sketch, "E3686", {"start": v(31.14, 54.04) * mm, "end": v(31.35, 53.81) * mm});
            skLineSegment(sketch, "E3687", {"start": v(30.97, 54.25) * mm, "end": v(31.14, 54.04) * mm});
            skLineSegment(sketch, "E3688", {"start": v(30.86, 54.41) * mm, "end": v(30.97, 54.25) * mm});
            skLineSegment(sketch, "E3689", {"start": v(30.64, 54.82) * mm, "end": v(30.86, 54.41) * mm});
            skArc(sketch, "E3690", {"start": v(30.64, 54.82) * mm, "mid": v(30.2, 55.2) * mm, "end": v(29.61, 55.16) * mm});
            skArc(sketch, "E3691", {"start": v(28.97, 54.87) * mm, "mid": v(29.3, 55.01) * mm, "end": v(29.61, 55.16) * mm});
            skArc(sketch, "E3692", {"start": v(28.97, 54.87) * mm, "mid": v(28.56, 54.46) * mm, "end": v(28.56, 53.87) * mm});
            skLineSegment(sketch, "E3693", {"start": v(28.81, 50.99) * mm, "end": v(28.63, 49.93) * mm});
            skLineSegment(sketch, "E3694", {"start": v(28.88, 51.96) * mm, "end": v(28.81, 50.99) * mm});
            skLineSegment(sketch, "E3695", {"start": v(28.88, 52.33) * mm, "end": v(28.88, 51.96) * mm});
            skLineSegment(sketch, "E3696", {"start": v(28.86, 52.67) * mm, "end": v(28.88, 52.33) * mm});
            skLineSegment(sketch, "E3697", {"start": v(28.82, 52.98) * mm, "end": v(28.86, 52.67) * mm});
            skLineSegment(sketch, "E3698", {"start": v(28.77, 53.25) * mm, "end": v(28.82, 52.98) * mm});
            skLineSegment(sketch, "E3699", {"start": v(28.72, 53.44) * mm, "end": v(28.77, 53.25) * mm});
            skLineSegment(sketch, "E3700", {"start": v(28.56, 53.87) * mm, "end": v(28.72, 53.44) * mm});
            skArc(sketch, "E3701", {"start": v(27.28, 49.54) * mm, "mid": v(27.95, 49.72) * mm, "end": v(28.63, 49.93) * mm});
            skLineSegment(sketch, "E3702", {"start": v(26.55, 50.33) * mm, "end": v(27.28, 49.54) * mm});
            skLineSegment(sketch, "E3703", {"start": v(25.97, 51.1) * mm, "end": v(26.55, 50.33) * mm});
            skLineSegment(sketch, "E3704", {"start": v(25.77, 51.42) * mm, "end": v(25.97, 51.1) * mm});
            skLineSegment(sketch, "E3705", {"start": v(25.6, 51.72) * mm, "end": v(25.77, 51.42) * mm});
            skLineSegment(sketch, "E3706", {"start": v(25.46, 52) * mm, "end": v(25.6, 51.72) * mm});
            skLineSegment(sketch, "E3707", {"start": v(25.36, 52.25) * mm, "end": v(25.46, 52) * mm});
            skLineSegment(sketch, "E3708", {"start": v(25.3, 52.43) * mm, "end": v(25.36, 52.25) * mm});
            skLineSegment(sketch, "E3709", {"start": v(25.2, 52.89) * mm, "end": v(25.3, 52.43) * mm});
            skArc(sketch, "E3710", {"start": v(25.2, 52.89) * mm, "mid": v(24.88, 53.37) * mm, "end": v(24.32, 53.5) * mm});
            skArc(sketch, "E3711", {"start": v(23.62, 53.4) * mm, "mid": v(23.97, 53.45) * mm, "end": v(24.32, 53.5) * mm});
            skArc(sketch, "E3712", {"start": v(23.62, 53.4) * mm, "mid": v(23.11, 53.12) * mm, "end": v(22.94, 52.56) * mm});
            skLineSegment(sketch, "E3713", {"start": v(22.37, 49.72) * mm, "end": v(21.9, 48.76) * mm});
            skLineSegment(sketch, "E3714", {"start": v(22.7, 50.63) * mm, "end": v(22.37, 49.72) * mm});
            skLineSegment(sketch, "E3715", {"start": v(22.81, 51) * mm, "end": v(22.7, 50.63) * mm});
            skLineSegment(sketch, "E3716", {"start": v(22.89, 51.33) * mm, "end": v(22.81, 51) * mm});
            skLineSegment(sketch, "E3717", {"start": v(22.94, 51.63) * mm, "end": v(22.89, 51.33) * mm});
            skLineSegment(sketch, "E3718", {"start": v(22.97, 51.9) * mm, "end": v(22.94, 51.63) * mm});
            skLineSegment(sketch, "E3719", {"start": v(22.98, 52.1) * mm, "end": v(22.97, 51.9) * mm});
            skLineSegment(sketch, "E3720", {"start": v(22.94, 52.56) * mm, "end": v(22.98, 52.1) * mm});
            skArc(sketch, "E3721", {"start": v(20.49, 48.76) * mm, "mid": v(21.2, 48.75) * mm, "end": v(21.9, 48.76) * mm});
            skLineSegment(sketch, "E3722", {"start": v(20.01, 49.72) * mm, "end": v(20.49, 48.76) * mm});
            skLineSegment(sketch, "E3723", {"start": v(19.68, 50.63) * mm, "end": v(20.01, 49.72) * mm});
            skLineSegment(sketch, "E3724", {"start": v(19.57, 51) * mm, "end": v(19.68, 50.63) * mm});
            skLineSegment(sketch, "E3725", {"start": v(19.5, 51.33) * mm, "end": v(19.57, 51) * mm});
            skLineSegment(sketch, "E3726", {"start": v(19.44, 51.63) * mm, "end": v(19.5, 51.33) * mm});
            skLineSegment(sketch, "E3727", {"start": v(19.42, 51.9) * mm, "end": v(19.44, 51.63) * mm});
            skLineSegment(sketch, "E3728", {"start": v(19.4, 52.1) * mm, "end": v(19.42, 51.9) * mm});
            skLineSegment(sketch, "E3729", {"start": v(19.44, 52.56) * mm, "end": v(19.4, 52.1) * mm});
            skArc(sketch, "E3730", {"start": v(19.44, 52.56) * mm, "mid": v(19.27, 53.12) * mm, "end": v(18.77, 53.4) * mm});
            skArc(sketch, "E3731", {"start": v(18.07, 53.5) * mm, "mid": v(18.42, 53.45) * mm, "end": v(18.77, 53.4) * mm});
            skArc(sketch, "E3732", {"start": v(18.07, 53.5) * mm, "mid": v(17.5, 53.37) * mm, "end": v(17.18, 52.89) * mm});
            skLineSegment(sketch, "E3733", {"start": v(15.84, 50.33) * mm, "end": v(15.1, 49.54) * mm});
            skLineSegment(sketch, "E3734", {"start": v(16.42, 51.1) * mm, "end": v(15.84, 50.33) * mm});
            skLineSegment(sketch, "E3735", {"start": v(16.61, 51.42) * mm, "end": v(16.42, 51.1) * mm});
            skLineSegment(sketch, "E3736", {"start": v(16.78, 51.72) * mm, "end": v(16.61, 51.42) * mm});
            skLineSegment(sketch, "E3737", {"start": v(16.92, 52) * mm, "end": v(16.78, 51.72) * mm});
            skLineSegment(sketch, "E3738", {"start": v(17.02, 52.25) * mm, "end": v(16.92, 52) * mm});
            skLineSegment(sketch, "E3739", {"start": v(17.09, 52.43) * mm, "end": v(17.02, 52.25) * mm});
            skLineSegment(sketch, "E3740", {"start": v(17.18, 52.89) * mm, "end": v(17.09, 52.43) * mm});
            skArc(sketch, "E3741", {"start": v(13.76, 49.93) * mm, "mid": v(14.43, 49.72) * mm, "end": v(15.1, 49.54) * mm});
            skLineSegment(sketch, "E3742", {"start": v(13.57, 50.99) * mm, "end": v(13.76, 49.93) * mm});
            skLineSegment(sketch, "E3743", {"start": v(13.5, 51.96) * mm, "end": v(13.57, 50.99) * mm});
            skLineSegment(sketch, "E3744", {"start": v(13.5, 52.33) * mm, "end": v(13.5, 51.96) * mm});
            skLineSegment(sketch, "E3745", {"start": v(13.53, 52.67) * mm, "end": v(13.5, 52.33) * mm});
            skLineSegment(sketch, "E3746", {"start": v(13.57, 52.98) * mm, "end": v(13.53, 52.67) * mm});
            skLineSegment(sketch, "E3747", {"start": v(13.61, 53.25) * mm, "end": v(13.57, 52.98) * mm});
            skLineSegment(sketch, "E3748", {"start": v(13.66, 53.44) * mm, "end": v(13.61, 53.25) * mm});
            skLineSegment(sketch, "E3749", {"start": v(13.83, 53.87) * mm, "end": v(13.66, 53.44) * mm});
            skArc(sketch, "E3750", {"start": v(13.83, 53.87) * mm, "mid": v(13.82, 54.46) * mm, "end": v(13.41, 54.87) * mm});
            skArc(sketch, "E3751", {"start": v(12.77, 55.16) * mm, "mid": v(13.1, 55.01) * mm, "end": v(13.41, 54.87) * mm});
            skArc(sketch, "E3752", {"start": v(12.77, 55.16) * mm, "mid": v(12.2, 55.2) * mm, "end": v(11.75, 54.82) * mm});
            skLineSegment(sketch, "E3753", {"start": v(9.74, 52.74) * mm, "end": v(8.82, 52.19) * mm});
            skLineSegment(sketch, "E3754", {"start": v(10.5, 53.32) * mm, "end": v(9.74, 52.74) * mm});
            skLineSegment(sketch, "E3755", {"start": v(10.79, 53.57) * mm, "end": v(10.5, 53.32) * mm});
            skLineSegment(sketch, "E3756", {"start": v(11.04, 53.81) * mm, "end": v(10.79, 53.57) * mm});
            skLineSegment(sketch, "E3757", {"start": v(11.25, 54.04) * mm, "end": v(11.04, 53.81) * mm});
            skLineSegment(sketch, "E3758", {"start": v(11.42, 54.25) * mm, "end": v(11.25, 54.04) * mm});
            skLineSegment(sketch, "E3759", {"start": v(11.53, 54.41) * mm, "end": v(11.42, 54.25) * mm});
            skLineSegment(sketch, "E3760", {"start": v(11.75, 54.82) * mm, "end": v(11.53, 54.41) * mm});
            skArc(sketch, "E3761", {"start": v(7.63, 52.95) * mm, "mid": v(8.22, 52.56) * mm, "end": v(8.82, 52.19) * mm});
            skLineSegment(sketch, "E3762", {"start": v(7.75, 54.02) * mm, "end": v(7.63, 52.95) * mm});
            skLineSegment(sketch, "E3763", {"start": v(7.96, 54.96) * mm, "end": v(7.75, 54.02) * mm});
            skLineSegment(sketch, "E3764", {"start": v(8.07, 55.32) * mm, "end": v(7.96, 54.96) * mm});
            skLineSegment(sketch, "E3765", {"start": v(8.18, 55.64) * mm, "end": v(8.07, 55.32) * mm});
            skLineSegment(sketch, "E3766", {"start": v(8.3, 55.93) * mm, "end": v(8.18, 55.64) * mm});
            skLineSegment(sketch, "E3767", {"start": v(8.42, 56.17) * mm, "end": v(8.3, 55.93) * mm});
            skLineSegment(sketch, "E3768", {"start": v(8.53, 56.34) * mm, "end": v(8.42, 56.17) * mm});
            skLineSegment(sketch, "E3769", {"start": v(8.8, 56.71) * mm, "end": v(8.53, 56.34) * mm});
            skArc(sketch, "E3770", {"start": v(8.8, 56.71) * mm, "mid": v(8.96, 57.27) * mm, "end": v(8.7, 57.79) * mm});
            skArc(sketch, "E3771", {"start": v(94.83, 23.2) * mm, "mid": v(94.03, 23.09) * mm, "end": v(93.28, 22.78) * mm});
            skArc(sketch, "E3772", {"start": v(97.52, 21.64) * mm, "mid": v(97.03, 22.29) * mm, "end": v(96.38, 22.78) * mm});
            skArc(sketch, "E3773", {"start": v(97.52, 18.54) * mm, "mid": v(97.83, 19.3) * mm, "end": v(97.93, 20.1) * mm});
            skArc(sketch, "E3774", {"start": v(94.83, 17) * mm, "mid": v(95.64, 17.1) * mm, "end": v(96.38, 17.41) * mm});
            skArc(sketch, "E3775", {"start": v(92.15, 18.54) * mm, "mid": v(92.64, 17.9) * mm, "end": v(93.28, 17.41) * mm});
            skArc(sketch, "E3776", {"start": v(91.93, 20.1) * mm, "mid": v(92.03, 19.34) * mm, "end": v(92.32, 18.64) * mm});
            skArc(sketch, "E3777", {"start": v(93.38, 17.58) * mm, "mid": v(94.08, 17.3) * mm, "end": v(94.83, 17.2) * mm});
            skArc(sketch, "E3778", {"start": v(96.28, 17.58) * mm, "mid": v(96.88, 18.04) * mm, "end": v(97.35, 18.64) * mm});
            skArc(sketch, "E3779", {"start": v(97.73, 20.1) * mm, "mid": v(97.64, 20.85) * mm, "end": v(97.35, 21.54) * mm});
            skArc(sketch, "E3780", {"start": v(96.28, 22.6) * mm, "mid": v(95.58, 22.9) * mm, "end": v(94.83, 23) * mm});
            skLineSegment(sketch, "E3781", {"start": v(96.28, 22.6) * mm, "end": v(96.38, 22.78) * mm});
            skLineSegment(sketch, "E3782", {"start": v(97.35, 21.54) * mm, "end": v(97.52, 21.64) * mm});
            skLineSegment(sketch, "E3783", {"start": v(97.73, 20.1) * mm, "end": v(97.93, 20.1) * mm});
            skLineSegment(sketch, "E3784", {"start": v(97.35, 18.64) * mm, "end": v(97.52, 18.54) * mm});
            skLineSegment(sketch, "E3785", {"start": v(96.28, 17.58) * mm, "end": v(96.38, 17.41) * mm});
            skLineSegment(sketch, "E3786", {"start": v(94.83, 17.2) * mm, "end": v(94.83, 17) * mm});
            skLineSegment(sketch, "E3787", {"start": v(93.38, 17.58) * mm, "end": v(93.28, 17.41) * mm});
            skLineSegment(sketch, "E3788", {"start": v(92.32, 18.64) * mm, "end": v(92.15, 18.54) * mm});
            skLineSegment(sketch, "E3789", {"start": v(91.93, 20.1) * mm, "end": v(91.73, 20.1) * mm});
            skLineSegment(sketch, "E3790", {"start": v(92.32, 21.54) * mm, "end": v(92.15, 21.64) * mm});
            skLineSegment(sketch, "E3791", {"start": v(93.38, 22.6) * mm, "end": v(93.28, 22.78) * mm});
            skLineSegment(sketch, "E3792", {"start": v(94.83, 23) * mm, "end": v(94.83, 23.2) * mm});
            skArc(sketch, "E3793", {"start": v(93.38, 22.6) * mm, "mid": v(92.78, 22.15) * mm, "end": v(92.32, 21.54) * mm});
            skArc(sketch, "E3794", {"start": v(92.15, 21.64) * mm, "mid": v(91.84, 20.9) * mm, "end": v(91.73, 20.1) * mm});
            skLineSegment(sketch, "E3795", {"start": v(42.34, 71.48) * mm, "end": v(42.64, 71.38) * mm});
            skCircle(sketch, "E3796", {"center": v(94.83, 20.1) * mm, "radius": 6 * mm});
            skArc(sketch, "E3797", {"start": v(95.62, -4.48) * mm, "mid": v(94.81, -4.58) * mm, "end": v(94.07, -4.9) * mm});
            skArc(sketch, "E3798", {"start": v(98.3, -6.03) * mm, "mid": v(97.8, -5.38) * mm, "end": v(97.17, -4.9) * mm});
            skArc(sketch, "E3799", {"start": v(98.3, -9.13) * mm, "mid": v(98.61, -8.38) * mm, "end": v(98.72, -7.58) * mm});
            skArc(sketch, "E3800", {"start": v(95.62, -10.68) * mm, "mid": v(96.42, -10.57) * mm, "end": v(97.17, -10.26) * mm});
            skArc(sketch, "E3801", {"start": v(92.93, -9.13) * mm, "mid": v(93.43, -9.77) * mm, "end": v(94.07, -10.26) * mm});
            skArc(sketch, "E3802", {"start": v(92.72, -7.58) * mm, "mid": v(92.82, -8.33) * mm, "end": v(93.1, -9.03) * mm});
            skArc(sketch, "E3803", {"start": v(94.17, -10.09) * mm, "mid": v(94.87, -10.38) * mm, "end": v(95.62, -10.48) * mm});
            skArc(sketch, "E3804", {"start": v(97.07, -10.09) * mm, "mid": v(97.67, -9.63) * mm, "end": v(98.13, -9.03) * mm});
            skArc(sketch, "E3805", {"start": v(98.52, -7.58) * mm, "mid": v(98.42, -6.83) * mm, "end": v(98.13, -6.13) * mm});
            skArc(sketch, "E3806", {"start": v(97.07, -5.07) * mm, "mid": v(96.37, -4.78) * mm, "end": v(95.62, -4.68) * mm});
            skLineSegment(sketch, "E3807", {"start": v(97.07, -5.07) * mm, "end": v(97.17, -4.9) * mm});
            skLineSegment(sketch, "E3808", {"start": v(98.13, -6.13) * mm, "end": v(98.3, -6.03) * mm});
            skLineSegment(sketch, "E3809", {"start": v(98.52, -7.58) * mm, "end": v(98.72, -7.58) * mm});
            skLineSegment(sketch, "E3810", {"start": v(98.13, -9.03) * mm, "end": v(98.3, -9.13) * mm});
            skLineSegment(sketch, "E3811", {"start": v(97.07, -10.09) * mm, "end": v(97.17, -10.26) * mm});
            skLineSegment(sketch, "E3812", {"start": v(95.62, -10.48) * mm, "end": v(95.62, -10.68) * mm});
            skLineSegment(sketch, "E3813", {"start": v(94.17, -10.09) * mm, "end": v(94.07, -10.26) * mm});
            skLineSegment(sketch, "E3814", {"start": v(93.1, -9.03) * mm, "end": v(92.93, -9.13) * mm});
            skLineSegment(sketch, "E3815", {"start": v(92.72, -7.58) * mm, "end": v(92.52, -7.58) * mm});
            skLineSegment(sketch, "E3816", {"start": v(93.1, -6.13) * mm, "end": v(92.93, -6.03) * mm});
            skLineSegment(sketch, "E3817", {"start": v(94.17, -5.07) * mm, "end": v(94.07, -4.9) * mm});
            skLineSegment(sketch, "E3818", {"start": v(95.62, -4.68) * mm, "end": v(95.62, -4.48) * mm});
            skArc(sketch, "E3819", {"start": v(94.17, -5.07) * mm, "mid": v(93.57, -5.53) * mm, "end": v(93.1, -6.13) * mm});
            skArc(sketch, "E3820", {"start": v(92.93, -6.03) * mm, "mid": v(92.62, -6.77) * mm, "end": v(92.52, -7.58) * mm});
            skCircle(sketch, "E3821", {"center": v(95.62, -7.58) * mm, "radius": 6 * mm});
            skArc(sketch, "E3822", {"start": v(26.72, -64.3) * mm, "mid": v(25.01, -64.52) * mm, "end": v(23.42, -65.17) * mm});
            skArc(sketch, "E3823", {"start": v(32.43, -67.6) * mm, "mid": v(31.39, -66.22) * mm, "end": v(30.02, -65.17) * mm});
            skArc(sketch, "E3824", {"start": v(32.43, -74.2) * mm, "mid": v(33.1, -72.6) * mm, "end": v(33.32, -70.9) * mm});
            skArc(sketch, "E3825", {"start": v(26.72, -77.5) * mm, "mid": v(28.43, -77.27) * mm, "end": v(30.02, -76.6) * mm});
            skArc(sketch, "E3826", {"start": v(21, -74.2) * mm, "mid": v(22.05, -75.56) * mm, "end": v(23.42, -76.6) * mm});
            skArc(sketch, "E3827", {"start": v(20.32, -70.9) * mm, "mid": v(20.54, -72.55) * mm, "end": v(21.18, -74.1) * mm});
            skArc(sketch, "E3828", {"start": v(23.52, -76.43) * mm, "mid": v(25.06, -77.07) * mm, "end": v(26.72, -77.3) * mm});
            skArc(sketch, "E3829", {"start": v(29.92, -76.43) * mm, "mid": v(31.24, -75.42) * mm, "end": v(32.26, -74.1) * mm});
            skArc(sketch, "E3830", {"start": v(33.12, -70.9) * mm, "mid": v(32.9, -69.23) * mm, "end": v(32.26, -67.7) * mm});
            skArc(sketch, "E3831", {"start": v(29.92, -65.35) * mm, "mid": v(28.37, -64.7) * mm, "end": v(26.72, -64.5) * mm});
            skLineSegment(sketch, "E3832", {"start": v(29.92, -65.35) * mm, "end": v(30.02, -65.17) * mm});
            skLineSegment(sketch, "E3833", {"start": v(32.26, -67.7) * mm, "end": v(32.43, -67.6) * mm});
            skLineSegment(sketch, "E3834", {"start": v(33.12, -70.9) * mm, "end": v(33.32, -70.9) * mm});
            skLineSegment(sketch, "E3835", {"start": v(32.26, -74.1) * mm, "end": v(32.43, -74.2) * mm});
            skLineSegment(sketch, "E3836", {"start": v(29.92, -76.43) * mm, "end": v(30.02, -76.6) * mm});
            skLineSegment(sketch, "E3837", {"start": v(26.72, -77.3) * mm, "end": v(26.72, -77.5) * mm});
            skLineSegment(sketch, "E3838", {"start": v(23.52, -76.43) * mm, "end": v(23.42, -76.6) * mm});
            skLineSegment(sketch, "E3839", {"start": v(21.18, -74.1) * mm, "end": v(21, -74.2) * mm});
            skLineSegment(sketch, "E3840", {"start": v(20.32, -70.9) * mm, "end": v(20.12, -70.9) * mm});
            skLineSegment(sketch, "E3841", {"start": v(21.18, -67.7) * mm, "end": v(21, -67.6) * mm});
            skLineSegment(sketch, "E3842", {"start": v(23.52, -65.35) * mm, "end": v(23.42, -65.17) * mm});
            skLineSegment(sketch, "E3843", {"start": v(26.72, -64.5) * mm, "end": v(26.72, -64.3) * mm});
            skArc(sketch, "E3844", {"start": v(23.52, -65.35) * mm, "mid": v(22.2, -66.37) * mm, "end": v(21.18, -67.7) * mm});
            skArc(sketch, "E3845", {"start": v(21, -67.6) * mm, "mid": v(20.34, -69.18) * mm, "end": v(20.12, -70.9) * mm});
            skArc(sketch, "E3846", {"start": v(-75.55, -61.56) * mm, "mid": v(-77.26, -61.78) * mm, "end": v(-78.85, -62.44) * mm});
            skArc(sketch, "E3847", {"start": v(-69.83, -64.86) * mm, "mid": v(-70.88, -63.5) * mm, "end": v(-72.25, -62.44) * mm});
            skArc(sketch, "E3848", {"start": v(-69.83, -71.46) * mm, "mid": v(-69.17, -69.87) * mm, "end": v(-68.95, -68.16) * mm});
            skArc(sketch, "E3849", {"start": v(-75.55, -74.76) * mm, "mid": v(-73.84, -74.53) * mm, "end": v(-72.25, -73.87) * mm});
            skArc(sketch, "E3850", {"start": v(-81.27, -71.46) * mm, "mid": v(-80.22, -72.82) * mm, "end": v(-78.85, -73.87) * mm});
            skArc(sketch, "E3851", {"start": v(-81.95, -68.16) * mm, "mid": v(-81.73, -69.81) * mm, "end": v(-81.1, -71.36) * mm});
            skArc(sketch, "E3852", {"start": v(-78.75, -73.7) * mm, "mid": v(-77.2, -74.34) * mm, "end": v(-75.55, -74.56) * mm});
            skArc(sketch, "E3853", {"start": v(-72.35, -73.7) * mm, "mid": v(-71.02, -72.68) * mm, "end": v(-70, -71.36) * mm});
            skArc(sketch, "E3854", {"start": v(-69.15, -68.16) * mm, "mid": v(-69.37, -66.5) * mm, "end": v(-70, -64.96) * mm});
            skArc(sketch, "E3855", {"start": v(-72.35, -62.62) * mm, "mid": v(-73.9, -61.98) * mm, "end": v(-75.55, -61.76) * mm});
            skLineSegment(sketch, "E3856", {"start": v(-72.35, -62.62) * mm, "end": v(-72.25, -62.44) * mm});
            skLineSegment(sketch, "E3857", {"start": v(-70, -64.96) * mm, "end": v(-69.83, -64.86) * mm});
            skLineSegment(sketch, "E3858", {"start": v(-69.15, -68.16) * mm, "end": v(-68.95, -68.16) * mm});
            skLineSegment(sketch, "E3859", {"start": v(-70, -71.36) * mm, "end": v(-69.83, -71.46) * mm});
            skLineSegment(sketch, "E3860", {"start": v(-72.35, -73.7) * mm, "end": v(-72.25, -73.87) * mm});
            skLineSegment(sketch, "E3861", {"start": v(-75.55, -74.56) * mm, "end": v(-75.55, -74.76) * mm});
            skLineSegment(sketch, "E3862", {"start": v(-78.75, -73.7) * mm, "end": v(-78.85, -73.87) * mm});
            skLineSegment(sketch, "E3863", {"start": v(-81.1, -71.36) * mm, "end": v(-81.27, -71.46) * mm});
            skLineSegment(sketch, "E3864", {"start": v(-81.95, -68.16) * mm, "end": v(-82.15, -68.16) * mm});
            skLineSegment(sketch, "E3865", {"start": v(-81.1, -64.96) * mm, "end": v(-81.27, -64.86) * mm});
            skLineSegment(sketch, "E3866", {"start": v(-78.75, -62.62) * mm, "end": v(-78.85, -62.44) * mm});
            skLineSegment(sketch, "E3867", {"start": v(-75.55, -61.76) * mm, "end": v(-75.55, -61.56) * mm});
            skArc(sketch, "E3868", {"start": v(-78.75, -62.62) * mm, "mid": v(-80.08, -63.63) * mm, "end": v(-81.1, -64.96) * mm});
            skArc(sketch, "E3869", {"start": v(-81.27, -64.86) * mm, "mid": v(-81.92, -66.45) * mm, "end": v(-82.15, -68.16) * mm});
            skArc(sketch, "E3870", {"start": v(25.8, 2.2) * mm, "mid": v(24.99, 2.1) * mm, "end": v(24.24, 1.8) * mm});
            skArc(sketch, "E3871", {"start": v(28.48, 0.66) * mm, "mid": v(27.98, 1.3) * mm, "end": v(27.34, 1.8) * mm});
            skArc(sketch, "E3872", {"start": v(28.48, -2.44) * mm, "mid": v(28.79, -1.7) * mm, "end": v(28.9, -0.9) * mm});
            skArc(sketch, "E3873", {"start": v(25.8, -4) * mm, "mid": v(26.6, -3.88) * mm, "end": v(27.34, -3.58) * mm});
            skArc(sketch, "E3874", {"start": v(23.1, -2.44) * mm, "mid": v(23.6, -3.08) * mm, "end": v(24.24, -3.58) * mm});
            skArc(sketch, "E3875", {"start": v(22.9, -0.9) * mm, "mid": v(23, -1.64) * mm, "end": v(23.28, -2.34) * mm});
            skArc(sketch, "E3876", {"start": v(24.34, -3.4) * mm, "mid": v(25.04, -3.7) * mm, "end": v(25.8, -3.8) * mm});
            skArc(sketch, "E3877", {"start": v(27.24, -3.4) * mm, "mid": v(27.84, -2.94) * mm, "end": v(28.3, -2.34) * mm});
            skArc(sketch, "E3878", {"start": v(28.7, -0.9) * mm, "mid": v(28.6, -0.14) * mm, "end": v(28.3, 0.56) * mm});
            skArc(sketch, "E3879", {"start": v(27.24, 1.62) * mm, "mid": v(26.54, 1.91) * mm, "end": v(25.8, 2) * mm});
            skLineSegment(sketch, "E3880", {"start": v(27.24, 1.62) * mm, "end": v(27.34, 1.8) * mm});
            skLineSegment(sketch, "E3881", {"start": v(28.3, 0.56) * mm, "end": v(28.48, 0.66) * mm});
            skLineSegment(sketch, "E3882", {"start": v(28.7, -0.9) * mm, "end": v(28.9, -0.9) * mm});
            skLineSegment(sketch, "E3883", {"start": v(28.3, -2.34) * mm, "end": v(28.48, -2.44) * mm});
            skLineSegment(sketch, "E3884", {"start": v(27.24, -3.4) * mm, "end": v(27.34, -3.58) * mm});
            skLineSegment(sketch, "E3885", {"start": v(25.8, -3.8) * mm, "end": v(25.8, -4) * mm});
            skLineSegment(sketch, "E3886", {"start": v(24.34, -3.4) * mm, "end": v(24.24, -3.58) * mm});
            skLineSegment(sketch, "E3887", {"start": v(23.28, -2.34) * mm, "end": v(23.1, -2.44) * mm});
            skLineSegment(sketch, "E3888", {"start": v(22.9, -0.9) * mm, "end": v(22.7, -0.9) * mm});
            skLineSegment(sketch, "E3889", {"start": v(23.28, 0.56) * mm, "end": v(23.1, 0.66) * mm});
            skLineSegment(sketch, "E3890", {"start": v(24.34, 1.62) * mm, "end": v(24.24, 1.8) * mm});
            skLineSegment(sketch, "E3891", {"start": v(25.8, 2) * mm, "end": v(25.8, 2.2) * mm});
            skArc(sketch, "E3892", {"start": v(24.34, 1.62) * mm, "mid": v(23.74, 1.16) * mm, "end": v(23.28, 0.56) * mm});
            skArc(sketch, "E3893", {"start": v(23.1, 0.66) * mm, "mid": v(22.8, -0.09) * mm, "end": v(22.7, -0.9) * mm});
            skArc(sketch, "E3894", {"start": v(-76.48, 8.44) * mm, "mid": v(-78.18, 8.22) * mm, "end": v(-79.78, 7.56) * mm});
            skArc(sketch, "E3895", {"start": v(-70.76, 5.14) * mm, "mid": v(-71.8, 6.5) * mm, "end": v(-73.18, 7.56) * mm});
            skArc(sketch, "E3896", {"start": v(-70.76, -1.46) * mm, "mid": v(-70.1, 0.13) * mm, "end": v(-69.88, 1.84) * mm});
            skArc(sketch, "E3897", {"start": v(-76.48, -4.76) * mm, "mid": v(-74.77, -4.53) * mm, "end": v(-73.18, -3.87) * mm});
            skArc(sketch, "E3898", {"start": v(-82.2, -1.46) * mm, "mid": v(-81.14, -2.82) * mm, "end": v(-79.78, -3.87) * mm});
            skArc(sketch, "E3899", {"start": v(-82.88, 1.84) * mm, "mid": v(-82.66, 0.19) * mm, "end": v(-82.02, -1.36) * mm});
            skArc(sketch, "E3900", {"start": v(-79.68, -3.7) * mm, "mid": v(-78.13, -4.34) * mm, "end": v(-76.48, -4.56) * mm});
            skArc(sketch, "E3901", {"start": v(-73.28, -3.7) * mm, "mid": v(-71.95, -2.68) * mm, "end": v(-70.93, -1.36) * mm});
            skArc(sketch, "E3902", {"start": v(-70.08, 1.84) * mm, "mid": v(-70.3, 3.5) * mm, "end": v(-70.93, 5.04) * mm});
            skArc(sketch, "E3903", {"start": v(-73.28, 7.38) * mm, "mid": v(-74.82, 8.02) * mm, "end": v(-76.48, 8.24) * mm});
            skLineSegment(sketch, "E3904", {"start": v(-73.28, 7.38) * mm, "end": v(-73.18, 7.56) * mm});
            skLineSegment(sketch, "E3905", {"start": v(-70.93, 5.04) * mm, "end": v(-70.76, 5.14) * mm});
            skLineSegment(sketch, "E3906", {"start": v(-70.08, 1.84) * mm, "end": v(-69.88, 1.84) * mm});
            skCircle(sketch, "E3907", {"center": v(21.2, 72.75) * mm, "radius": 3.1 * mm});
            skLineSegment(sketch, "E3908", {"start": v(-70.93, -1.36) * mm, "end": v(-70.76, -1.46) * mm});
            skLineSegment(sketch, "E3909", {"start": v(-73.28, -3.7) * mm, "end": v(-73.18, -3.87) * mm});
            skLineSegment(sketch, "E3910", {"start": v(-76.48, -4.56) * mm, "end": v(-76.48, -4.76) * mm});
            skLineSegment(sketch, "E3911", {"start": v(-79.68, -3.7) * mm, "end": v(-79.78, -3.87) * mm});
            skLineSegment(sketch, "E3912", {"start": v(-82.02, -1.36) * mm, "end": v(-82.2, -1.46) * mm});
            skLineSegment(sketch, "E3913", {"start": v(-82.88, 1.84) * mm, "end": v(-83.08, 1.84) * mm});
            skLineSegment(sketch, "E3914", {"start": v(-82.02, 5.04) * mm, "end": v(-82.2, 5.14) * mm});
            skLineSegment(sketch, "E3915", {"start": v(-79.68, 7.38) * mm, "end": v(-79.78, 7.56) * mm});
            skLineSegment(sketch, "E3916", {"start": v(-76.48, 8.24) * mm, "end": v(-76.48, 8.44) * mm});
            skArc(sketch, "E3917", {"start": v(-79.68, 7.38) * mm, "mid": v(-81, 6.37) * mm, "end": v(-82.02, 5.04) * mm});
            skArc(sketch, "E3918", {"start": v(-82.2, 5.14) * mm, "mid": v(-82.85, 3.55) * mm, "end": v(-83.08, 1.84) * mm});
            skArc(sketch, "E3919", {"start": v(-77.77, 76.9) * mm, "mid": v(-79.48, 76.67) * mm, "end": v(-81.07, 76) * mm});
            skArc(sketch, "E3920", {"start": v(-72.06, 73.6) * mm, "mid": v(-73.1, 74.96) * mm, "end": v(-74.47, 76) * mm});
            skArc(sketch, "E3921", {"start": v(-72.06, 67) * mm, "mid": v(-71.4, 68.58) * mm, "end": v(-71.17, 70.3) * mm});
            skArc(sketch, "E3922", {"start": v(-77.77, 63.7) * mm, "mid": v(-76.06, 63.92) * mm, "end": v(-74.47, 64.58) * mm});
            skArc(sketch, "E3923", {"start": v(-83.49, 67) * mm, "mid": v(-82.44, 65.63) * mm, "end": v(-81.07, 64.58) * mm});
            skArc(sketch, "E3924", {"start": v(-84.17, 70.3) * mm, "mid": v(-83.95, 68.64) * mm, "end": v(-83.31, 67.1) * mm});
            skArc(sketch, "E3925", {"start": v(-80.97, 64.75) * mm, "mid": v(-79.43, 64.11) * mm, "end": v(-77.77, 63.9) * mm});
            skArc(sketch, "E3926", {"start": v(-74.57, 64.75) * mm, "mid": v(-73.25, 65.77) * mm, "end": v(-72.23, 67.1) * mm});
            skArc(sketch, "E3927", {"start": v(-71.37, 70.3) * mm, "mid": v(-71.59, 71.95) * mm, "end": v(-72.23, 73.5) * mm});
            skArc(sketch, "E3928", {"start": v(-74.57, 75.83) * mm, "mid": v(-76.11, 76.47) * mm, "end": v(-77.77, 76.7) * mm});
            skLineSegment(sketch, "E3929", {"start": v(-74.57, 75.83) * mm, "end": v(-74.47, 76) * mm});
            skLineSegment(sketch, "E3930", {"start": v(-72.23, 73.5) * mm, "end": v(-72.06, 73.6) * mm});
            skLineSegment(sketch, "E3931", {"start": v(-71.37, 70.3) * mm, "end": v(-71.17, 70.3) * mm});
            skLineSegment(sketch, "E3932", {"start": v(-72.23, 67.1) * mm, "end": v(-72.06, 67) * mm});
            skLineSegment(sketch, "E3933", {"start": v(-74.57, 64.75) * mm, "end": v(-74.47, 64.58) * mm});
            skLineSegment(sketch, "E3934", {"start": v(-77.77, 63.9) * mm, "end": v(-77.77, 63.7) * mm});
            skLineSegment(sketch, "E3935", {"start": v(-80.97, 64.75) * mm, "end": v(-81.07, 64.58) * mm});
            skLineSegment(sketch, "E3936", {"start": v(-83.31, 67.1) * mm, "end": v(-83.49, 67) * mm});
            skLineSegment(sketch, "E3937", {"start": v(-84.17, 70.3) * mm, "end": v(-84.37, 70.3) * mm});
            skLineSegment(sketch, "E3938", {"start": v(-83.31, 73.5) * mm, "end": v(-83.49, 73.6) * mm});
            skLineSegment(sketch, "E3939", {"start": v(-80.97, 75.83) * mm, "end": v(-81.07, 76) * mm});
            skLineSegment(sketch, "E3940", {"start": v(-77.77, 76.7) * mm, "end": v(-77.77, 76.9) * mm});
            skArc(sketch, "E3941", {"start": v(-80.97, 75.83) * mm, "mid": v(-82.3, 74.82) * mm, "end": v(-83.31, 73.5) * mm});
            skArc(sketch, "E3942", {"start": v(-83.49, 73.6) * mm, "mid": v(-84.15, 72) * mm, "end": v(-84.37, 70.3) * mm});
            skArc(sketch, "E3943", {"start": v(5.86, -76.12) * mm, "mid": v(5.95, -76.46) * mm, "end": v(6.04, -76.79) * mm});
            skArc(sketch, "E3944", {"start": v(5.86, -76.12) * mm, "mid": v(5.53, -75.66) * mm, "end": v(4.96, -75.56) * mm});
            skLineSegment(sketch, "E3945", {"start": v(2.08, -75.33) * mm, "end": v(1.04, -75) * mm});
            skLineSegment(sketch, "E3946", {"start": v(3.04, -75.55) * mm, "end": v(2.08, -75.33) * mm});
            skLineSegment(sketch, "E3947", {"start": v(3.5, -75.61) * mm, "end": v(3.04, -75.55) * mm});
            skLineSegment(sketch, "E3948", {"start": v(3.9, -75.65) * mm, "end": v(3.5, -75.61) * mm});
            skLineSegment(sketch, "E3949", {"start": v(4.27, -75.65) * mm, "end": v(3.9, -75.65) * mm});
            skLineSegment(sketch, "E3950", {"start": v(4.56, -75.64) * mm, "end": v(4.27, -75.65) * mm});
            skLineSegment(sketch, "E3951", {"start": v(4.96, -75.56) * mm, "end": v(4.56, -75.64) * mm});
            skArc(sketch, "E3952", {"start": v(0.86, -73.58) * mm, "mid": v(0.94, -74.28) * mm, "end": v(1.04, -75) * mm});
            skLineSegment(sketch, "E3953", {"start": v(1.77, -72.98) * mm, "end": v(0.86, -73.58) * mm});
            skLineSegment(sketch, "E3954", {"start": v(2.64, -72.52) * mm, "end": v(1.77, -72.98) * mm});
            skLineSegment(sketch, "E3955", {"start": v(3.06, -72.34) * mm, "end": v(2.64, -72.52) * mm});
            skLineSegment(sketch, "E3956", {"start": v(3.45, -72.2) * mm, "end": v(3.06, -72.34) * mm});
            skLineSegment(sketch, "E3957", {"start": v(3.8, -72.1) * mm, "end": v(3.45, -72.2) * mm});
            skLineSegment(sketch, "E3958", {"start": v(4.08, -72.04) * mm, "end": v(3.8, -72.1) * mm});
            skLineSegment(sketch, "E3959", {"start": v(4.5, -72.01) * mm, "end": v(4.08, -72.04) * mm});
            skArc(sketch, "E3960", {"start": v(4.5, -72.01) * mm, "mid": v(5.02, -71.77) * mm, "end": v(5.22, -71.24) * mm});
            skArc(sketch, "E3961", {"start": v(5.22, -70.54) * mm, "mid": v(5.22, -70.9) * mm, "end": v(5.22, -71.24) * mm});
            skArc(sketch, "E3962", {"start": v(5.22, -70.54) * mm, "mid": v(5.02, -70) * mm, "end": v(4.5, -69.77) * mm});
            skLineSegment(sketch, "E3963", {"start": v(1.77, -68.8) * mm, "end": v(0.86, -68.2) * mm});
            skLineSegment(sketch, "E3964", {"start": v(2.64, -69.26) * mm, "end": v(1.77, -68.8) * mm});
            skLineSegment(sketch, "E3965", {"start": v(3.06, -69.44) * mm, "end": v(2.64, -69.26) * mm});
            skLineSegment(sketch, "E3966", {"start": v(3.45, -69.58) * mm, "end": v(3.06, -69.44) * mm});
            skLineSegment(sketch, "E3967", {"start": v(3.8, -69.68) * mm, "end": v(3.45, -69.58) * mm});
            skLineSegment(sketch, "E3968", {"start": v(4.08, -69.74) * mm, "end": v(3.8, -69.68) * mm});
            skLineSegment(sketch, "E3969", {"start": v(4.5, -69.77) * mm, "end": v(4.08, -69.74) * mm});
            skArc(sketch, "E3970", {"start": v(1.04, -66.8) * mm, "mid": v(0.94, -67.5) * mm, "end": v(0.86, -68.2) * mm});
            skLineSegment(sketch, "E3971", {"start": v(2.08, -66.45) * mm, "end": v(1.04, -66.8) * mm});
            skLineSegment(sketch, "E3972", {"start": v(3.04, -66.23) * mm, "end": v(2.08, -66.45) * mm});
            skLineSegment(sketch, "E3973", {"start": v(3.5, -66.17) * mm, "end": v(3.04, -66.23) * mm});
            skLineSegment(sketch, "E3974", {"start": v(3.9, -66.13) * mm, "end": v(3.5, -66.17) * mm});
            skLineSegment(sketch, "E3975", {"start": v(4.27, -66.13) * mm, "end": v(3.9, -66.13) * mm});
            skLineSegment(sketch, "E3976", {"start": v(4.56, -66.15) * mm, "end": v(4.27, -66.13) * mm});
            skLineSegment(sketch, "E3977", {"start": v(4.96, -66.22) * mm, "end": v(4.56, -66.15) * mm});
            skArc(sketch, "E3978", {"start": v(4.96, -66.22) * mm, "mid": v(5.53, -66.12) * mm, "end": v(5.86, -65.66) * mm});
            skArc(sketch, "E3979", {"start": v(6.04, -65) * mm, "mid": v(5.95, -65.33) * mm, "end": v(5.86, -65.66) * mm});
            skArc(sketch, "E3980", {"start": v(6.04, -65) * mm, "mid": v(5.98, -64.42) * mm, "end": v(5.54, -64.06) * mm});
            skLineSegment(sketch, "E3981", {"start": v(3.16, -62.42) * mm, "end": v(2.43, -61.6) * mm});
            skLineSegment(sketch, "E3982", {"start": v(3.89, -63.09) * mm, "end": v(3.16, -62.42) * mm});
            skLineSegment(sketch, "E3983", {"start": v(4.24, -63.37) * mm, "end": v(3.89, -63.09) * mm});
            skLineSegment(sketch, "E3984", {"start": v(4.58, -63.6) * mm, "end": v(4.24, -63.37) * mm});
            skLineSegment(sketch, "E3985", {"start": v(4.9, -63.79) * mm, "end": v(4.58, -63.6) * mm});
            skLineSegment(sketch, "E3986", {"start": v(5.15, -63.92) * mm, "end": v(4.9, -63.79) * mm});
            skLineSegment(sketch, "E3987", {"start": v(5.54, -64.06) * mm, "end": v(5.15, -63.92) * mm});
            skArc(sketch, "E3988", {"start": v(2.98, -60.29) * mm, "mid": v(2.7, -60.94) * mm, "end": v(2.43, -61.6) * mm});
            skLineSegment(sketch, "E3989", {"start": v(4.07, -60.22) * mm, "end": v(2.98, -60.29) * mm});
            skLineSegment(sketch, "E3990", {"start": v(5.06, -60.26) * mm, "end": v(4.07, -60.22) * mm});
            skLineSegment(sketch, "E3991", {"start": v(5.5, -60.32) * mm, "end": v(5.06, -60.26) * mm});
            skLineSegment(sketch, "E3992", {"start": v(5.91, -60.4) * mm, "end": v(5.5, -60.32) * mm});
            skLineSegment(sketch, "E3993", {"start": v(6.26, -60.48) * mm, "end": v(5.91, -60.4) * mm});
            skLineSegment(sketch, "E3994", {"start": v(6.54, -60.57) * mm, "end": v(6.26, -60.48) * mm});
            skLineSegment(sketch, "E3995", {"start": v(6.91, -60.75) * mm, "end": v(6.54, -60.57) * mm});
            skArc(sketch, "E3996", {"start": v(6.91, -60.75) * mm, "mid": v(7.48, -60.8) * mm, "end": v(7.93, -60.44) * mm});
            skArc(sketch, "E3997", {"start": v(8.27, -59.84) * mm, "mid": v(8.1, -60.14) * mm, "end": v(7.93, -60.44) * mm});
            skArc(sketch, "E3998", {"start": v(8.27, -59.84) * mm, "mid": v(8.36, -59.28) * mm, "end": v(8.03, -58.8) * mm});
            skLineSegment(sketch, "E3999", {"start": v(6.16, -56.61) * mm, "end": v(5.66, -55.63) * mm});
            skLineSegment(sketch, "E4000", {"start": v(6.68, -57.45) * mm, "end": v(6.16, -56.61) * mm});
            skLineSegment(sketch, "E4001", {"start": v(6.96, -57.8) * mm, "end": v(6.68, -57.45) * mm});
            skLineSegment(sketch, "E4002", {"start": v(7.22, -58.12) * mm, "end": v(6.96, -57.8) * mm});
            skLineSegment(sketch, "E4003", {"start": v(7.47, -58.38) * mm, "end": v(7.22, -58.12) * mm});
            skLineSegment(sketch, "E4004", {"start": v(7.7, -58.58) * mm, "end": v(7.47, -58.38) * mm});
            skLineSegment(sketch, "E4005", {"start": v(8.03, -58.8) * mm, "end": v(7.7, -58.58) * mm});
            skArc(sketch, "E4006", {"start": v(6.53, -54.5) * mm, "mid": v(6.1, -55.06) * mm, "end": v(5.66, -55.63) * mm});
            skLineSegment(sketch, "E4007", {"start": v(7.6, -54.72) * mm, "end": v(6.53, -54.5) * mm});
            skLineSegment(sketch, "E4008", {"start": v(8.55, -55.02) * mm, "end": v(7.6, -54.72) * mm});
            skLineSegment(sketch, "E4009", {"start": v(8.97, -55.19) * mm, "end": v(8.55, -55.02) * mm});
            skLineSegment(sketch, "E4010", {"start": v(9.34, -55.36) * mm, "end": v(8.97, -55.19) * mm});
            skLineSegment(sketch, "E4011", {"start": v(9.66, -55.54) * mm, "end": v(9.34, -55.36) * mm});
            skLineSegment(sketch, "E4012", {"start": v(9.9, -55.7) * mm, "end": v(9.66, -55.54) * mm});
            skLineSegment(sketch, "E4013", {"start": v(10.21, -55.97) * mm, "end": v(9.9, -55.7) * mm});
            skArc(sketch, "E4014", {"start": v(10.21, -55.97) * mm, "mid": v(10.75, -56.17) * mm, "end": v(11.27, -55.93) * mm});
            skArc(sketch, "E4015", {"start": v(11.76, -55.44) * mm, "mid": v(11.52, -55.69) * mm, "end": v(11.27, -55.93) * mm});
            skArc(sketch, "E4016", {"start": v(11.76, -55.44) * mm, "mid": v(12, -54.92) * mm, "end": v(11.8, -54.38) * mm});
            skLineSegment(sketch, "E4017", {"start": v(10.55, -51.78) * mm, "end": v(10.33, -50.7) * mm});
            skLineSegment(sketch, "E4018", {"start": v(10.85, -52.72) * mm, "end": v(10.55, -51.78) * mm});
            skLineSegment(sketch, "E4019", {"start": v(11.01, -53.14) * mm, "end": v(10.85, -52.72) * mm});
            skLineSegment(sketch, "E4020", {"start": v(11.2, -53.51) * mm, "end": v(11.01, -53.14) * mm});
            skLineSegment(sketch, "E4021", {"start": v(11.37, -53.83) * mm, "end": v(11.2, -53.51) * mm});
            skLineSegment(sketch, "E4022", {"start": v(11.53, -54.07) * mm, "end": v(11.37, -53.83) * mm});
            skLineSegment(sketch, "E4023", {"start": v(11.8, -54.38) * mm, "end": v(11.53, -54.07) * mm});
            skArc(sketch, "E4024", {"start": v(11.46, -49.84) * mm, "mid": v(10.9, -50.26) * mm, "end": v(10.33, -50.7) * mm});
            skLineSegment(sketch, "E4025", {"start": v(12.44, -50.33) * mm, "end": v(11.46, -49.84) * mm});
            skLineSegment(sketch, "E4026", {"start": v(13.27, -50.85) * mm, "end": v(12.44, -50.33) * mm});
            skLineSegment(sketch, "E4027", {"start": v(13.64, -51.13) * mm, "end": v(13.27, -50.85) * mm});
            skLineSegment(sketch, "E4028", {"start": v(13.95, -51.4) * mm, "end": v(13.64, -51.13) * mm});
            skLineSegment(sketch, "E4029", {"start": v(14.21, -51.65) * mm, "end": v(13.95, -51.4) * mm});
            skLineSegment(sketch, "E4030", {"start": v(14.4, -51.87) * mm, "end": v(14.21, -51.65) * mm});
            skLineSegment(sketch, "E4031", {"start": v(14.64, -52.2) * mm, "end": v(14.4, -51.87) * mm});
            skArc(sketch, "E4032", {"start": v(14.64, -52.2) * mm, "mid": v(15.1, -52.54) * mm, "end": v(15.67, -52.45) * mm});
            skArc(sketch, "E4033", {"start": v(16.27, -52.1) * mm, "mid": v(15.97, -52.27) * mm, "end": v(15.67, -52.45) * mm});
            skArc(sketch, "E4034", {"start": v(16.27, -52.1) * mm, "mid": v(16.63, -51.65) * mm, "end": v(16.58, -51.09) * mm});
            skLineSegment(sketch, "E4035", {"start": v(16.05, -48.24) * mm, "end": v(16.11, -47.15) * mm});
            skLineSegment(sketch, "E4036", {"start": v(16.09, -49.23) * mm, "end": v(16.05, -48.24) * mm});
            skLineSegment(sketch, "E4037", {"start": v(16.14, -49.68) * mm, "end": v(16.09, -49.23) * mm});
            skLineSegment(sketch, "E4038", {"start": v(16.22, -50.09) * mm, "end": v(16.14, -49.68) * mm});
            skLineSegment(sketch, "E4039", {"start": v(16.3, -50.44) * mm, "end": v(16.22, -50.09) * mm});
            skLineSegment(sketch, "E4040", {"start": v(16.4, -50.71) * mm, "end": v(16.3, -50.44) * mm});
            skLineSegment(sketch, "E4041", {"start": v(16.58, -51.09) * mm, "end": v(16.4, -50.71) * mm});
            skArc(sketch, "E4042", {"start": v(17.43, -46.6) * mm, "mid": v(16.77, -46.87) * mm, "end": v(16.11, -47.15) * mm});
            skLineSegment(sketch, "E4043", {"start": v(18.25, -47.33) * mm, "end": v(17.43, -46.6) * mm});
            skLineSegment(sketch, "E4044", {"start": v(18.92, -48.06) * mm, "end": v(18.25, -47.33) * mm});
            skLineSegment(sketch, "E4045", {"start": v(19.2, -48.41) * mm, "end": v(18.92, -48.06) * mm});
            skLineSegment(sketch, "E4046", {"start": v(19.43, -48.75) * mm, "end": v(19.2, -48.41) * mm});
            skLineSegment(sketch, "E4047", {"start": v(19.62, -49.07) * mm, "end": v(19.43, -48.75) * mm});
            skLineSegment(sketch, "E4048", {"start": v(19.75, -49.33) * mm, "end": v(19.62, -49.07) * mm});
            skLineSegment(sketch, "E4049", {"start": v(19.88, -49.72) * mm, "end": v(19.75, -49.33) * mm});
            skArc(sketch, "E4050", {"start": v(19.88, -49.72) * mm, "mid": v(20.25, -50.16) * mm, "end": v(20.82, -50.22) * mm});
            skArc(sketch, "E4051", {"start": v(21.49, -50.04) * mm, "mid": v(21.15, -50.12) * mm, "end": v(20.82, -50.22) * mm});
            skArc(sketch, "E4052", {"start": v(21.49, -50.04) * mm, "mid": v(21.95, -49.7) * mm, "end": v(22.05, -49.14) * mm});
            skLineSegment(sketch, "E4053", {"start": v(22.28, -46.25) * mm, "end": v(22.62, -45.22) * mm});
            skLineSegment(sketch, "E4054", {"start": v(22.06, -47.22) * mm, "end": v(22.28, -46.25) * mm});
            skLineSegment(sketch, "E4055", {"start": v(22, -47.67) * mm, "end": v(22.06, -47.22) * mm});
            skLineSegment(sketch, "E4056", {"start": v(21.96, -48.08) * mm, "end": v(22, -47.67) * mm});
            skLineSegment(sketch, "E4057", {"start": v(21.95, -48.44) * mm, "end": v(21.96, -48.08) * mm});
            skLineSegment(sketch, "E4058", {"start": v(21.97, -48.73) * mm, "end": v(21.95, -48.44) * mm});
            skLineSegment(sketch, "E4059", {"start": v(22.05, -49.14) * mm, "end": v(21.97, -48.73) * mm});
            skArc(sketch, "E4060", {"start": v(24.03, -45.03) * mm, "mid": v(23.32, -45.11) * mm, "end": v(22.62, -45.22) * mm});
            skLineSegment(sketch, "E4061", {"start": v(24.63, -45.94) * mm, "end": v(24.03, -45.03) * mm});
            skLineSegment(sketch, "E4062", {"start": v(25.1, -46.82) * mm, "end": v(24.63, -45.94) * mm});
            skLineSegment(sketch, "E4063", {"start": v(25.27, -47.23) * mm, "end": v(25.1, -46.82) * mm});
            skLineSegment(sketch, "E4064", {"start": v(25.4, -47.62) * mm, "end": v(25.27, -47.23) * mm});
            skLineSegment(sketch, "E4065", {"start": v(25.5, -47.97) * mm, "end": v(25.4, -47.62) * mm});
            skLineSegment(sketch, "E4066", {"start": v(25.57, -48.26) * mm, "end": v(25.5, -47.97) * mm});
            skLineSegment(sketch, "E4067", {"start": v(25.6, -48.67) * mm, "end": v(25.57, -48.26) * mm});
            skArc(sketch, "E4068", {"start": v(25.6, -48.67) * mm, "mid": v(25.84, -49.19) * mm, "end": v(26.37, -49.4) * mm});
            skArc(sketch, "E4069", {"start": v(27.07, -49.4) * mm, "mid": v(26.72, -49.4) * mm, "end": v(26.37, -49.4) * mm});
            skArc(sketch, "E4070", {"start": v(27.07, -49.4) * mm, "mid": v(27.6, -49.19) * mm, "end": v(27.84, -48.67) * mm});
            skLineSegment(sketch, "E4071", {"start": v(28.8, -45.94) * mm, "end": v(29.4, -45.03) * mm});
            skLineSegment(sketch, "E4072", {"start": v(28.34, -46.82) * mm, "end": v(28.8, -45.94) * mm});
            skLineSegment(sketch, "E4073", {"start": v(28.17, -47.23) * mm, "end": v(28.34, -46.82) * mm});
            skLineSegment(sketch, "E4074", {"start": v(28.03, -47.62) * mm, "end": v(28.17, -47.23) * mm});
            skLineSegment(sketch, "E4075", {"start": v(27.93, -47.97) * mm, "end": v(28.03, -47.62) * mm});
            skLineSegment(sketch, "E4076", {"start": v(27.87, -48.26) * mm, "end": v(27.93, -47.97) * mm});
            skLineSegment(sketch, "E4077", {"start": v(27.84, -48.67) * mm, "end": v(27.87, -48.26) * mm});
            skArc(sketch, "E4078", {"start": v(30.82, -45.22) * mm, "mid": v(30.11, -45.11) * mm, "end": v(29.4, -45.03) * mm});
            skLineSegment(sketch, "E4079", {"start": v(31.16, -46.25) * mm, "end": v(30.82, -45.22) * mm});
            skLineSegment(sketch, "E4080", {"start": v(31.38, -47.22) * mm, "end": v(31.16, -46.25) * mm});
            skLineSegment(sketch, "E4081", {"start": v(31.44, -47.67) * mm, "end": v(31.38, -47.22) * mm});
            skLineSegment(sketch, "E4082", {"start": v(31.48, -48.08) * mm, "end": v(31.44, -47.67) * mm});
            skLineSegment(sketch, "E4083", {"start": v(31.48, -48.44) * mm, "end": v(31.48, -48.08) * mm});
            skLineSegment(sketch, "E4084", {"start": v(31.46, -48.73) * mm, "end": v(31.48, -48.44) * mm});
            skLineSegment(sketch, "E4085", {"start": v(31.39, -49.14) * mm, "end": v(31.46, -48.73) * mm});
            skArc(sketch, "E4086", {"start": v(31.39, -49.14) * mm, "mid": v(31.48, -49.7) * mm, "end": v(31.95, -50.04) * mm});
            skArc(sketch, "E4087", {"start": v(32.62, -50.22) * mm, "mid": v(32.28, -50.12) * mm, "end": v(31.95, -50.04) * mm});
            skArc(sketch, "E4088", {"start": v(32.62, -50.22) * mm, "mid": v(33.19, -50.16) * mm, "end": v(33.55, -49.72) * mm});
            skLineSegment(sketch, "E4089", {"start": v(35.19, -47.33) * mm, "end": v(36, -46.6) * mm});
            skLineSegment(sketch, "E4090", {"start": v(34.52, -48.06) * mm, "end": v(35.19, -47.33) * mm});
            skLineSegment(sketch, "E4091", {"start": v(34.24, -48.41) * mm, "end": v(34.52, -48.06) * mm});
            skLineSegment(sketch, "E4092", {"start": v(34, -48.75) * mm, "end": v(34.24, -48.41) * mm});
            skLineSegment(sketch, "E4093", {"start": v(33.82, -49.07) * mm, "end": v(34, -48.75) * mm});
            skLineSegment(sketch, "E4094", {"start": v(33.69, -49.33) * mm, "end": v(33.82, -49.07) * mm});
            skLineSegment(sketch, "E4095", {"start": v(33.55, -49.72) * mm, "end": v(33.69, -49.33) * mm});
            skArc(sketch, "E4096", {"start": v(37.32, -47.15) * mm, "mid": v(36.67, -46.87) * mm, "end": v(36, -46.6) * mm});
            skLineSegment(sketch, "E4097", {"start": v(37.39, -48.24) * mm, "end": v(37.32, -47.15) * mm});
            skLineSegment(sketch, "E4098", {"start": v(37.35, -49.23) * mm, "end": v(37.39, -48.24) * mm});
            skLineSegment(sketch, "E4099", {"start": v(37.3, -49.68) * mm, "end": v(37.35, -49.23) * mm});
            skLineSegment(sketch, "E4100", {"start": v(37.22, -50.09) * mm, "end": v(37.3, -49.68) * mm});
            skLineSegment(sketch, "E4101", {"start": v(37.13, -50.44) * mm, "end": v(37.22, -50.09) * mm});
            skLineSegment(sketch, "E4102", {"start": v(37.04, -50.71) * mm, "end": v(37.13, -50.44) * mm});
            skLineSegment(sketch, "E4103", {"start": v(36.86, -51.09) * mm, "end": v(37.04, -50.71) * mm});
            skArc(sketch, "E4104", {"start": v(36.86, -51.09) * mm, "mid": v(36.8, -51.65) * mm, "end": v(37.17, -52.1) * mm});
            skArc(sketch, "E4105", {"start": v(37.77, -52.45) * mm, "mid": v(37.47, -52.27) * mm, "end": v(37.17, -52.1) * mm});
            skArc(sketch, "E4106", {"start": v(37.77, -52.45) * mm, "mid": v(38.33, -52.54) * mm, "end": v(38.8, -52.2) * mm});
            skLineSegment(sketch, "E4107", {"start": v(41, -50.33) * mm, "end": v(41.97, -49.84) * mm});
            skLineSegment(sketch, "E4108", {"start": v(40.16, -50.85) * mm, "end": v(41, -50.33) * mm});
            skLineSegment(sketch, "E4109", {"start": v(39.8, -51.13) * mm, "end": v(40.16, -50.85) * mm});
            skLineSegment(sketch, "E4110", {"start": v(39.49, -51.4) * mm, "end": v(39.8, -51.13) * mm});
            skLineSegment(sketch, "E4111", {"start": v(39.23, -51.65) * mm, "end": v(39.49, -51.4) * mm});
            skLineSegment(sketch, "E4112", {"start": v(39.03, -51.87) * mm, "end": v(39.23, -51.65) * mm});
            skLineSegment(sketch, "E4113", {"start": v(38.8, -52.2) * mm, "end": v(39.03, -51.87) * mm});
            skArc(sketch, "E4114", {"start": v(43.1, -50.7) * mm, "mid": v(42.55, -50.26) * mm, "end": v(41.97, -49.84) * mm});
            skLineSegment(sketch, "E4115", {"start": v(42.88, -51.78) * mm, "end": v(43.1, -50.7) * mm});
            skLineSegment(sketch, "E4116", {"start": v(42.6, -52.72) * mm, "end": v(42.88, -51.78) * mm});
            skLineSegment(sketch, "E4117", {"start": v(42.42, -53.14) * mm, "end": v(42.6, -52.72) * mm});
            skLineSegment(sketch, "E4118", {"start": v(42.25, -53.51) * mm, "end": v(42.42, -53.14) * mm});
            skLineSegment(sketch, "E4119", {"start": v(42.07, -53.83) * mm, "end": v(42.25, -53.51) * mm});
            skLineSegment(sketch, "E4120", {"start": v(41.9, -54.07) * mm, "end": v(42.07, -53.83) * mm});
            skLineSegment(sketch, "E4121", {"start": v(41.64, -54.38) * mm, "end": v(41.9, -54.07) * mm});
            skArc(sketch, "E4122", {"start": v(41.64, -54.38) * mm, "mid": v(41.44, -54.92) * mm, "end": v(41.67, -55.44) * mm});
            skArc(sketch, "E4123", {"start": v(42.16, -55.93) * mm, "mid": v(41.92, -55.69) * mm, "end": v(41.67, -55.44) * mm});
            skArc(sketch, "E4124", {"start": v(42.16, -55.93) * mm, "mid": v(42.69, -56.17) * mm, "end": v(43.22, -55.97) * mm});
            skLineSegment(sketch, "E4125", {"start": v(45.83, -54.72) * mm, "end": v(46.9, -54.5) * mm});
            skLineSegment(sketch, "E4126", {"start": v(44.9, -55.02) * mm, "end": v(45.83, -54.72) * mm});
            skLineSegment(sketch, "E4127", {"start": v(44.47, -55.19) * mm, "end": v(44.9, -55.02) * mm});
            skLineSegment(sketch, "E4128", {"start": v(44.1, -55.36) * mm, "end": v(44.47, -55.19) * mm});
            skLineSegment(sketch, "E4129", {"start": v(43.78, -55.54) * mm, "end": v(44.1, -55.36) * mm});
            skLineSegment(sketch, "E4130", {"start": v(43.54, -55.7) * mm, "end": v(43.78, -55.54) * mm});
            skLineSegment(sketch, "E4131", {"start": v(43.22, -55.97) * mm, "end": v(43.54, -55.7) * mm});
            skArc(sketch, "E4132", {"start": v(47.77, -55.63) * mm, "mid": v(47.35, -55.06) * mm, "end": v(46.9, -54.5) * mm});
            skLineSegment(sketch, "E4133", {"start": v(47.28, -56.61) * mm, "end": v(47.77, -55.63) * mm});
            skLineSegment(sketch, "E4134", {"start": v(46.75, -57.45) * mm, "end": v(47.28, -56.61) * mm});
            skLineSegment(sketch, "E4135", {"start": v(46.48, -57.8) * mm, "end": v(46.75, -57.45) * mm});
            skLineSegment(sketch, "E4136", {"start": v(46.21, -58.12) * mm, "end": v(46.48, -57.8) * mm});
            skLineSegment(sketch, "E4137", {"start": v(45.96, -58.38) * mm, "end": v(46.21, -58.12) * mm});
            skLineSegment(sketch, "E4138", {"start": v(45.74, -58.58) * mm, "end": v(45.96, -58.38) * mm});
            skLineSegment(sketch, "E4139", {"start": v(45.4, -58.8) * mm, "end": v(45.74, -58.58) * mm});
            skArc(sketch, "E4140", {"start": v(45.4, -58.8) * mm, "mid": v(45.07, -59.28) * mm, "end": v(45.16, -59.84) * mm});
            skArc(sketch, "E4141", {"start": v(45.5, -60.44) * mm, "mid": v(45.34, -60.14) * mm, "end": v(45.16, -59.84) * mm});
            skArc(sketch, "E4142", {"start": v(45.5, -60.44) * mm, "mid": v(45.95, -60.8) * mm, "end": v(46.52, -60.75) * mm});
            skLineSegment(sketch, "E4143", {"start": v(49.37, -60.22) * mm, "end": v(50.46, -60.29) * mm});
            skLineSegment(sketch, "E4144", {"start": v(48.38, -60.26) * mm, "end": v(49.37, -60.22) * mm});
            skLineSegment(sketch, "E4145", {"start": v(47.93, -60.32) * mm, "end": v(48.38, -60.26) * mm});
            skLineSegment(sketch, "E4146", {"start": v(47.52, -60.4) * mm, "end": v(47.93, -60.32) * mm});
            skLineSegment(sketch, "E4147", {"start": v(47.17, -60.48) * mm, "end": v(47.52, -60.4) * mm});
            skLineSegment(sketch, "E4148", {"start": v(46.9, -60.57) * mm, "end": v(47.17, -60.48) * mm});
            skLineSegment(sketch, "E4149", {"start": v(46.52, -60.75) * mm, "end": v(46.9, -60.57) * mm});
            skArc(sketch, "E4150", {"start": v(51, -61.6) * mm, "mid": v(50.74, -60.94) * mm, "end": v(50.46, -60.29) * mm});
            skLineSegment(sketch, "E4151", {"start": v(50.28, -62.42) * mm, "end": v(51, -61.6) * mm});
            skLineSegment(sketch, "E4152", {"start": v(49.55, -63.09) * mm, "end": v(50.28, -62.42) * mm});
            skLineSegment(sketch, "E4153", {"start": v(49.2, -63.37) * mm, "end": v(49.55, -63.09) * mm});
            skLineSegment(sketch, "E4154", {"start": v(48.85, -63.6) * mm, "end": v(49.2, -63.37) * mm});
            skLineSegment(sketch, "E4155", {"start": v(48.54, -63.79) * mm, "end": v(48.85, -63.6) * mm});
            skLineSegment(sketch, "E4156", {"start": v(48.28, -63.92) * mm, "end": v(48.54, -63.79) * mm});
            skLineSegment(sketch, "E4157", {"start": v(47.9, -64.06) * mm, "end": v(48.28, -63.92) * mm});
            skArc(sketch, "E4158", {"start": v(47.9, -64.06) * mm, "mid": v(47.45, -64.42) * mm, "end": v(47.4, -65) * mm});
            skArc(sketch, "E4159", {"start": v(47.57, -65.66) * mm, "mid": v(47.49, -65.33) * mm, "end": v(47.4, -65) * mm});
            skArc(sketch, "E4160", {"start": v(47.57, -65.66) * mm, "mid": v(47.9, -66.12) * mm, "end": v(48.47, -66.22) * mm});
            skLineSegment(sketch, "E4161", {"start": v(51.36, -66.45) * mm, "end": v(52.4, -66.8) * mm});
            skLineSegment(sketch, "E4162", {"start": v(50.4, -66.23) * mm, "end": v(51.36, -66.45) * mm});
            skLineSegment(sketch, "E4163", {"start": v(49.94, -66.17) * mm, "end": v(50.4, -66.23) * mm});
            skLineSegment(sketch, "E4164", {"start": v(49.53, -66.13) * mm, "end": v(49.94, -66.17) * mm});
            skLineSegment(sketch, "E4165", {"start": v(49.17, -66.13) * mm, "end": v(49.53, -66.13) * mm});
            skLineSegment(sketch, "E4166", {"start": v(48.88, -66.15) * mm, "end": v(49.17, -66.13) * mm});
            skLineSegment(sketch, "E4167", {"start": v(48.47, -66.22) * mm, "end": v(48.88, -66.15) * mm});
            skArc(sketch, "E4168", {"start": v(52.58, -68.2) * mm, "mid": v(52.5, -67.5) * mm, "end": v(52.4, -66.8) * mm});
            skLineSegment(sketch, "E4169", {"start": v(51.67, -68.8) * mm, "end": v(52.58, -68.2) * mm});
            skLineSegment(sketch, "E4170", {"start": v(50.8, -69.26) * mm, "end": v(51.67, -68.8) * mm});
            skLineSegment(sketch, "E4171", {"start": v(50.37, -69.44) * mm, "end": v(50.8, -69.26) * mm});
            skLineSegment(sketch, "E4172", {"start": v(49.99, -69.58) * mm, "end": v(50.37, -69.44) * mm});
            skLineSegment(sketch, "E4173", {"start": v(49.64, -69.68) * mm, "end": v(49.99, -69.58) * mm});
            skLineSegment(sketch, "E4174", {"start": v(49.35, -69.74) * mm, "end": v(49.64, -69.68) * mm});
            skLineSegment(sketch, "E4175", {"start": v(48.94, -69.77) * mm, "end": v(49.35, -69.74) * mm});
            skArc(sketch, "E4176", {"start": v(48.94, -69.77) * mm, "mid": v(48.42, -70) * mm, "end": v(48.22, -70.54) * mm});
            skArc(sketch, "E4177", {"start": v(48.22, -71.24) * mm, "mid": v(48.22, -70.9) * mm, "end": v(48.22, -70.54) * mm});
            skArc(sketch, "E4178", {"start": v(48.22, -71.24) * mm, "mid": v(48.42, -71.77) * mm, "end": v(48.94, -72.01) * mm});
            skLineSegment(sketch, "E4179", {"start": v(51.67, -72.98) * mm, "end": v(52.58, -73.58) * mm});
            skLineSegment(sketch, "E4180", {"start": v(50.8, -72.52) * mm, "end": v(51.67, -72.98) * mm});
            skLineSegment(sketch, "E4181", {"start": v(50.37, -72.34) * mm, "end": v(50.8, -72.52) * mm});
            skLineSegment(sketch, "E4182", {"start": v(49.99, -72.2) * mm, "end": v(50.37, -72.34) * mm});
            skLineSegment(sketch, "E4183", {"start": v(49.64, -72.1) * mm, "end": v(49.99, -72.2) * mm});
            skLineSegment(sketch, "E4184", {"start": v(49.35, -72.04) * mm, "end": v(49.64, -72.1) * mm});
            skLineSegment(sketch, "E4185", {"start": v(48.94, -72.01) * mm, "end": v(49.35, -72.04) * mm});
            skArc(sketch, "E4186", {"start": v(52.4, -75) * mm, "mid": v(52.5, -74.28) * mm, "end": v(52.58, -73.58) * mm});
            skLineSegment(sketch, "E4187", {"start": v(51.36, -75.33) * mm, "end": v(52.4, -75) * mm});
            skLineSegment(sketch, "E4188", {"start": v(50.4, -75.55) * mm, "end": v(51.36, -75.33) * mm});
            skLineSegment(sketch, "E4189", {"start": v(49.94, -75.61) * mm, "end": v(50.4, -75.55) * mm});
            skLineSegment(sketch, "E4190", {"start": v(49.53, -75.65) * mm, "end": v(49.94, -75.61) * mm});
            skLineSegment(sketch, "E4191", {"start": v(49.17, -75.65) * mm, "end": v(49.53, -75.65) * mm});
            skLineSegment(sketch, "E4192", {"start": v(48.88, -75.64) * mm, "end": v(49.17, -75.65) * mm});
            skLineSegment(sketch, "E4193", {"start": v(48.47, -75.56) * mm, "end": v(48.88, -75.64) * mm});
            skArc(sketch, "E4194", {"start": v(48.47, -75.56) * mm, "mid": v(47.9, -75.66) * mm, "end": v(47.57, -76.12) * mm});
            skArc(sketch, "E4195", {"start": v(47.4, -76.79) * mm, "mid": v(47.49, -76.46) * mm, "end": v(47.57, -76.12) * mm});
            skArc(sketch, "E4196", {"start": v(47.4, -76.79) * mm, "mid": v(47.45, -77.36) * mm, "end": v(47.9, -77.73) * mm});
            skLineSegment(sketch, "E4197", {"start": v(50.28, -79.36) * mm, "end": v(51, -80.18) * mm});
            skLineSegment(sketch, "E4198", {"start": v(49.55, -78.7) * mm, "end": v(50.28, -79.36) * mm});
            skLineSegment(sketch, "E4199", {"start": v(49.2, -78.41) * mm, "end": v(49.55, -78.7) * mm});
            skLineSegment(sketch, "E4200", {"start": v(48.85, -78.18) * mm, "end": v(49.2, -78.41) * mm});
            skLineSegment(sketch, "E4201", {"start": v(48.54, -78) * mm, "end": v(48.85, -78.18) * mm});
            skLineSegment(sketch, "E4202", {"start": v(48.28, -77.86) * mm, "end": v(48.54, -78) * mm});
            skLineSegment(sketch, "E4203", {"start": v(47.9, -77.73) * mm, "end": v(48.28, -77.86) * mm});
            skArc(sketch, "E4204", {"start": v(50.46, -81.5) * mm, "mid": v(50.74, -80.84) * mm, "end": v(51, -80.18) * mm});
            skLineSegment(sketch, "E4205", {"start": v(49.37, -81.56) * mm, "end": v(50.46, -81.5) * mm});
            skLineSegment(sketch, "E4206", {"start": v(48.38, -81.52) * mm, "end": v(49.37, -81.56) * mm});
            skLineSegment(sketch, "E4207", {"start": v(47.93, -81.46) * mm, "end": v(48.38, -81.52) * mm});
            skLineSegment(sketch, "E4208", {"start": v(47.52, -81.4) * mm, "end": v(47.93, -81.46) * mm});
            skLineSegment(sketch, "E4209", {"start": v(47.17, -81.3) * mm, "end": v(47.52, -81.4) * mm});
            skLineSegment(sketch, "E4210", {"start": v(46.9, -81.2) * mm, "end": v(47.17, -81.3) * mm});
            skLineSegment(sketch, "E4211", {"start": v(46.52, -81.03) * mm, "end": v(46.9, -81.2) * mm});
            skArc(sketch, "E4212", {"start": v(46.52, -81.03) * mm, "mid": v(45.95, -80.98) * mm, "end": v(45.5, -81.34) * mm});
            skArc(sketch, "E4213", {"start": v(45.16, -81.94) * mm, "mid": v(45.34, -81.64) * mm, "end": v(45.5, -81.34) * mm});
            skArc(sketch, "E4214", {"start": v(45.16, -81.94) * mm, "mid": v(45.07, -82.5) * mm, "end": v(45.4, -82.97) * mm});
            skLineSegment(sketch, "E4215", {"start": v(47.28, -85.17) * mm, "end": v(47.77, -86.15) * mm});
            skLineSegment(sketch, "E4216", {"start": v(46.75, -84.34) * mm, "end": v(47.28, -85.17) * mm});
            skLineSegment(sketch, "E4217", {"start": v(46.48, -83.97) * mm, "end": v(46.75, -84.34) * mm});
            skLineSegment(sketch, "E4218", {"start": v(46.21, -83.66) * mm, "end": v(46.48, -83.97) * mm});
            skLineSegment(sketch, "E4219", {"start": v(45.96, -83.4) * mm, "end": v(46.21, -83.66) * mm});
            skLineSegment(sketch, "E4220", {"start": v(45.74, -83.2) * mm, "end": v(45.96, -83.4) * mm});
            skLineSegment(sketch, "E4221", {"start": v(45.4, -82.97) * mm, "end": v(45.74, -83.2) * mm});
            skArc(sketch, "E4222", {"start": v(46.9, -87.28) * mm, "mid": v(47.35, -86.72) * mm, "end": v(47.77, -86.15) * mm});
            skLineSegment(sketch, "E4223", {"start": v(45.83, -87.06) * mm, "end": v(46.9, -87.28) * mm});
            skLineSegment(sketch, "E4224", {"start": v(44.9, -86.76) * mm, "end": v(45.83, -87.06) * mm});
            skLineSegment(sketch, "E4225", {"start": v(44.47, -86.6) * mm, "end": v(44.9, -86.76) * mm});
            skLineSegment(sketch, "E4226", {"start": v(44.1, -86.42) * mm, "end": v(44.47, -86.6) * mm});
            skLineSegment(sketch, "E4227", {"start": v(43.78, -86.24) * mm, "end": v(44.1, -86.42) * mm});
            skLineSegment(sketch, "E4228", {"start": v(43.54, -86.08) * mm, "end": v(43.78, -86.24) * mm});
            skLineSegment(sketch, "E4229", {"start": v(43.22, -85.81) * mm, "end": v(43.54, -86.08) * mm});
            skArc(sketch, "E4230", {"start": v(43.22, -85.81) * mm, "mid": v(42.69, -85.61) * mm, "end": v(42.16, -85.85) * mm});
            skArc(sketch, "E4231", {"start": v(41.67, -86.34) * mm, "mid": v(41.92, -86.1) * mm, "end": v(42.16, -85.85) * mm});
            skArc(sketch, "E4232", {"start": v(41.67, -86.34) * mm, "mid": v(41.44, -86.86) * mm, "end": v(41.64, -87.4) * mm});
            skLineSegment(sketch, "E4233", {"start": v(42.88, -90) * mm, "end": v(43.1, -91.08) * mm});
            skLineSegment(sketch, "E4234", {"start": v(42.6, -89.06) * mm, "end": v(42.88, -90) * mm});
            skLineSegment(sketch, "E4235", {"start": v(42.42, -88.64) * mm, "end": v(42.6, -89.06) * mm});
            skLineSegment(sketch, "E4236", {"start": v(42.25, -88.27) * mm, "end": v(42.42, -88.64) * mm});
            skLineSegment(sketch, "E4237", {"start": v(42.07, -87.95) * mm, "end": v(42.25, -88.27) * mm});
            skLineSegment(sketch, "E4238", {"start": v(41.9, -87.7) * mm, "end": v(42.07, -87.95) * mm});
            skLineSegment(sketch, "E4239", {"start": v(41.64, -87.4) * mm, "end": v(41.9, -87.7) * mm});
            skArc(sketch, "E4240", {"start": v(41.97, -91.94) * mm, "mid": v(42.55, -91.52) * mm, "end": v(43.1, -91.08) * mm});
            skLineSegment(sketch, "E4241", {"start": v(41, -91.45) * mm, "end": v(41.97, -91.94) * mm});
            skLineSegment(sketch, "E4242", {"start": v(40.16, -90.93) * mm, "end": v(41, -91.45) * mm});
            skLineSegment(sketch, "E4243", {"start": v(39.8, -90.65) * mm, "end": v(40.16, -90.93) * mm});
            skLineSegment(sketch, "E4244", {"start": v(39.49, -90.39) * mm, "end": v(39.8, -90.65) * mm});
            skLineSegment(sketch, "E4245", {"start": v(39.23, -90.13) * mm, "end": v(39.49, -90.39) * mm});
            skLineSegment(sketch, "E4246", {"start": v(39.03, -89.92) * mm, "end": v(39.23, -90.13) * mm});
            skLineSegment(sketch, "E4247", {"start": v(38.8, -89.57) * mm, "end": v(39.03, -89.92) * mm});
            skArc(sketch, "E4248", {"start": v(38.8, -89.57) * mm, "mid": v(38.33, -89.25) * mm, "end": v(37.77, -89.33) * mm});
            skArc(sketch, "E4249", {"start": v(37.17, -89.68) * mm, "mid": v(37.47, -89.51) * mm, "end": v(37.77, -89.33) * mm});
            skArc(sketch, "E4250", {"start": v(37.17, -89.68) * mm, "mid": v(36.8, -90.13) * mm, "end": v(36.86, -90.7) * mm});
            skLineSegment(sketch, "E4251", {"start": v(37.39, -93.54) * mm, "end": v(37.32, -94.63) * mm});
            skLineSegment(sketch, "E4252", {"start": v(37.35, -92.55) * mm, "end": v(37.39, -93.54) * mm});
            skLineSegment(sketch, "E4253", {"start": v(37.3, -92.1) * mm, "end": v(37.35, -92.55) * mm});
            skLineSegment(sketch, "E4254", {"start": v(37.22, -91.7) * mm, "end": v(37.3, -92.1) * mm});
            skLineSegment(sketch, "E4255", {"start": v(37.13, -91.34) * mm, "end": v(37.22, -91.7) * mm});
            skLineSegment(sketch, "E4256", {"start": v(37.04, -91.07) * mm, "end": v(37.13, -91.34) * mm});
            skLineSegment(sketch, "E4257", {"start": v(36.86, -90.7) * mm, "end": v(37.04, -91.07) * mm});
            skArc(sketch, "E4258", {"start": v(36, -95.18) * mm, "mid": v(36.67, -94.91) * mm, "end": v(37.32, -94.63) * mm});
            skLineSegment(sketch, "E4259", {"start": v(35.19, -94.45) * mm, "end": v(36, -95.18) * mm});
            skLineSegment(sketch, "E4260", {"start": v(34.52, -93.72) * mm, "end": v(35.19, -94.45) * mm});
            skLineSegment(sketch, "E4261", {"start": v(34.24, -93.37) * mm, "end": v(34.52, -93.72) * mm});
            skLineSegment(sketch, "E4262", {"start": v(34, -93.03) * mm, "end": v(34.24, -93.37) * mm});
            skLineSegment(sketch, "E4263", {"start": v(33.82, -92.72) * mm, "end": v(34, -93.03) * mm});
            skLineSegment(sketch, "E4264", {"start": v(33.69, -92.45) * mm, "end": v(33.82, -92.72) * mm});
            skLineSegment(sketch, "E4265", {"start": v(33.55, -92.06) * mm, "end": v(33.69, -92.45) * mm});
            skArc(sketch, "E4266", {"start": v(33.55, -92.06) * mm, "mid": v(33.19, -91.63) * mm, "end": v(32.62, -91.57) * mm});
            skArc(sketch, "E4267", {"start": v(31.95, -91.74) * mm, "mid": v(32.28, -91.66) * mm, "end": v(32.62, -91.57) * mm});
            skArc(sketch, "E4268", {"start": v(31.95, -91.74) * mm, "mid": v(31.48, -92.08) * mm, "end": v(31.39, -92.65) * mm});
            skLineSegment(sketch, "E4269", {"start": v(31.16, -95.53) * mm, "end": v(30.82, -96.57) * mm});
            skLineSegment(sketch, "E4270", {"start": v(31.38, -94.57) * mm, "end": v(31.16, -95.53) * mm});
            skLineSegment(sketch, "E4271", {"start": v(31.44, -94.12) * mm, "end": v(31.38, -94.57) * mm});
            skLineSegment(sketch, "E4272", {"start": v(31.48, -93.7) * mm, "end": v(31.44, -94.12) * mm});
            skLineSegment(sketch, "E4273", {"start": v(31.48, -93.34) * mm, "end": v(31.48, -93.7) * mm});
            skLineSegment(sketch, "E4274", {"start": v(31.46, -93.05) * mm, "end": v(31.48, -93.34) * mm});
            skLineSegment(sketch, "E4275", {"start": v(31.39, -92.65) * mm, "end": v(31.46, -93.05) * mm});
            skArc(sketch, "E4276", {"start": v(29.4, -96.75) * mm, "mid": v(30.11, -96.67) * mm, "end": v(30.82, -96.57) * mm});
            skLineSegment(sketch, "E4277", {"start": v(28.8, -95.84) * mm, "end": v(29.4, -96.75) * mm});
            skLineSegment(sketch, "E4278", {"start": v(28.34, -94.96) * mm, "end": v(28.8, -95.84) * mm});
            skLineSegment(sketch, "E4279", {"start": v(28.17, -94.55) * mm, "end": v(28.34, -94.96) * mm});
            skLineSegment(sketch, "E4280", {"start": v(28.03, -94.16) * mm, "end": v(28.17, -94.55) * mm});
            skLineSegment(sketch, "E4281", {"start": v(27.93, -93.8) * mm, "end": v(28.03, -94.16) * mm});
            skLineSegment(sketch, "E4282", {"start": v(27.87, -93.52) * mm, "end": v(27.93, -93.8) * mm});
            skLineSegment(sketch, "E4283", {"start": v(27.84, -93.11) * mm, "end": v(27.87, -93.52) * mm});
            skArc(sketch, "E4284", {"start": v(27.84, -93.11) * mm, "mid": v(27.6, -92.6) * mm, "end": v(27.07, -92.39) * mm});
            skArc(sketch, "E4285", {"start": v(26.37, -92.39) * mm, "mid": v(26.72, -92.4) * mm, "end": v(27.07, -92.39) * mm});
            skArc(sketch, "E4286", {"start": v(26.37, -92.39) * mm, "mid": v(25.84, -92.6) * mm, "end": v(25.6, -93.11) * mm});
            skLineSegment(sketch, "E4287", {"start": v(24.63, -95.84) * mm, "end": v(24.03, -96.75) * mm});
            skLineSegment(sketch, "E4288", {"start": v(25.1, -94.96) * mm, "end": v(24.63, -95.84) * mm});
            skLineSegment(sketch, "E4289", {"start": v(25.27, -94.55) * mm, "end": v(25.1, -94.96) * mm});
            skLineSegment(sketch, "E4290", {"start": v(25.4, -94.16) * mm, "end": v(25.27, -94.55) * mm});
            skLineSegment(sketch, "E4291", {"start": v(25.5, -93.8) * mm, "end": v(25.4, -94.16) * mm});
            skLineSegment(sketch, "E4292", {"start": v(25.57, -93.52) * mm, "end": v(25.5, -93.8) * mm});
            skLineSegment(sketch, "E4293", {"start": v(25.6, -93.11) * mm, "end": v(25.57, -93.52) * mm});
            skArc(sketch, "E4294", {"start": v(22.62, -96.57) * mm, "mid": v(23.32, -96.67) * mm, "end": v(24.03, -96.75) * mm});
            skLineSegment(sketch, "E4295", {"start": v(22.28, -95.53) * mm, "end": v(22.62, -96.57) * mm});
            skLineSegment(sketch, "E4296", {"start": v(22.06, -94.57) * mm, "end": v(22.28, -95.53) * mm});
            skLineSegment(sketch, "E4297", {"start": v(22, -94.12) * mm, "end": v(22.06, -94.57) * mm});
            skLineSegment(sketch, "E4298", {"start": v(21.96, -93.7) * mm, "end": v(22, -94.12) * mm});
            skLineSegment(sketch, "E4299", {"start": v(21.95, -93.34) * mm, "end": v(21.96, -93.7) * mm});
            skLineSegment(sketch, "E4300", {"start": v(21.97, -93.05) * mm, "end": v(21.95, -93.34) * mm});
            skLineSegment(sketch, "E4301", {"start": v(22.05, -92.65) * mm, "end": v(21.97, -93.05) * mm});
            skArc(sketch, "E4302", {"start": v(22.05, -92.65) * mm, "mid": v(21.95, -92.08) * mm, "end": v(21.49, -91.74) * mm});
            skArc(sketch, "E4303", {"start": v(20.82, -91.57) * mm, "mid": v(21.15, -91.66) * mm, "end": v(21.49, -91.74) * mm});
            skArc(sketch, "E4304", {"start": v(20.82, -91.57) * mm, "mid": v(20.25, -91.63) * mm, "end": v(19.88, -92.06) * mm});
            skLineSegment(sketch, "E4305", {"start": v(18.25, -94.45) * mm, "end": v(17.43, -95.18) * mm});
            skLineSegment(sketch, "E4306", {"start": v(18.92, -93.72) * mm, "end": v(18.25, -94.45) * mm});
            skLineSegment(sketch, "E4307", {"start": v(19.2, -93.37) * mm, "end": v(18.92, -93.72) * mm});
            skLineSegment(sketch, "E4308", {"start": v(19.43, -93.03) * mm, "end": v(19.2, -93.37) * mm});
            skLineSegment(sketch, "E4309", {"start": v(19.62, -92.72) * mm, "end": v(19.43, -93.03) * mm});
            skLineSegment(sketch, "E4310", {"start": v(19.75, -92.45) * mm, "end": v(19.62, -92.72) * mm});
            skLineSegment(sketch, "E4311", {"start": v(19.88, -92.06) * mm, "end": v(19.75, -92.45) * mm});
            skArc(sketch, "E4312", {"start": v(16.11, -94.63) * mm, "mid": v(16.77, -94.91) * mm, "end": v(17.43, -95.18) * mm});
            skLineSegment(sketch, "E4313", {"start": v(16.05, -93.54) * mm, "end": v(16.11, -94.63) * mm});
            skLineSegment(sketch, "E4314", {"start": v(16.09, -92.55) * mm, "end": v(16.05, -93.54) * mm});
            skLineSegment(sketch, "E4315", {"start": v(16.14, -92.1) * mm, "end": v(16.09, -92.55) * mm});
            skLineSegment(sketch, "E4316", {"start": v(16.22, -91.7) * mm, "end": v(16.14, -92.1) * mm});
            skLineSegment(sketch, "E4317", {"start": v(16.3, -91.34) * mm, "end": v(16.22, -91.7) * mm});
            skLineSegment(sketch, "E4318", {"start": v(16.4, -91.07) * mm, "end": v(16.3, -91.34) * mm});
            skLineSegment(sketch, "E4319", {"start": v(16.58, -90.7) * mm, "end": v(16.4, -91.07) * mm});
            skArc(sketch, "E4320", {"start": v(16.58, -90.7) * mm, "mid": v(16.63, -90.13) * mm, "end": v(16.27, -89.68) * mm});
            skArc(sketch, "E4321", {"start": v(15.67, -89.33) * mm, "mid": v(15.97, -89.51) * mm, "end": v(16.27, -89.68) * mm});
            skArc(sketch, "E4322", {"start": v(15.67, -89.33) * mm, "mid": v(15.1, -89.25) * mm, "end": v(14.64, -89.57) * mm});
            skLineSegment(sketch, "E4323", {"start": v(12.44, -91.45) * mm, "end": v(11.46, -91.94) * mm});
            skLineSegment(sketch, "E4324", {"start": v(13.27, -90.93) * mm, "end": v(12.44, -91.45) * mm});
            skLineSegment(sketch, "E4325", {"start": v(13.64, -90.65) * mm, "end": v(13.27, -90.93) * mm});
            skLineSegment(sketch, "E4326", {"start": v(13.95, -90.39) * mm, "end": v(13.64, -90.65) * mm});
            skLineSegment(sketch, "E4327", {"start": v(14.21, -90.13) * mm, "end": v(13.95, -90.39) * mm});
            skLineSegment(sketch, "E4328", {"start": v(14.4, -89.92) * mm, "end": v(14.21, -90.13) * mm});
            skLineSegment(sketch, "E4329", {"start": v(14.64, -89.57) * mm, "end": v(14.4, -89.92) * mm});
            skArc(sketch, "E4330", {"start": v(10.33, -91.08) * mm, "mid": v(10.9, -91.52) * mm, "end": v(11.46, -91.94) * mm});
            skLineSegment(sketch, "E4331", {"start": v(10.55, -90) * mm, "end": v(10.33, -91.08) * mm});
            skLineSegment(sketch, "E4332", {"start": v(10.85, -89.06) * mm, "end": v(10.55, -90) * mm});
            skLineSegment(sketch, "E4333", {"start": v(11.01, -88.64) * mm, "end": v(10.85, -89.06) * mm});
            skLineSegment(sketch, "E4334", {"start": v(11.2, -88.27) * mm, "end": v(11.01, -88.64) * mm});
            skLineSegment(sketch, "E4335", {"start": v(11.37, -87.95) * mm, "end": v(11.2, -88.27) * mm});
            skLineSegment(sketch, "E4336", {"start": v(11.53, -87.7) * mm, "end": v(11.37, -87.95) * mm});
            skLineSegment(sketch, "E4337", {"start": v(11.8, -87.4) * mm, "end": v(11.53, -87.7) * mm});
            skArc(sketch, "E4338", {"start": v(11.8, -87.4) * mm, "mid": v(12, -86.86) * mm, "end": v(11.76, -86.34) * mm});
            skArc(sketch, "E4339", {"start": v(11.27, -85.85) * mm, "mid": v(11.52, -86.1) * mm, "end": v(11.76, -86.34) * mm});
            skArc(sketch, "E4340", {"start": v(11.27, -85.85) * mm, "mid": v(10.75, -85.61) * mm, "end": v(10.21, -85.81) * mm});
            skLineSegment(sketch, "E4341", {"start": v(7.6, -87.06) * mm, "end": v(6.53, -87.28) * mm});
            skLineSegment(sketch, "E4342", {"start": v(8.55, -86.76) * mm, "end": v(7.6, -87.06) * mm});
            skLineSegment(sketch, "E4343", {"start": v(8.97, -86.6) * mm, "end": v(8.55, -86.76) * mm});
            skLineSegment(sketch, "E4344", {"start": v(9.34, -86.42) * mm, "end": v(8.97, -86.6) * mm});
            skLineSegment(sketch, "E4345", {"start": v(9.66, -86.24) * mm, "end": v(9.34, -86.42) * mm});
            skLineSegment(sketch, "E4346", {"start": v(9.9, -86.08) * mm, "end": v(9.66, -86.24) * mm});
            skLineSegment(sketch, "E4347", {"start": v(10.21, -85.81) * mm, "end": v(9.9, -86.08) * mm});
            skArc(sketch, "E4348", {"start": v(5.66, -86.15) * mm, "mid": v(6.1, -86.72) * mm, "end": v(6.53, -87.28) * mm});
            skLineSegment(sketch, "E4349", {"start": v(6.16, -85.17) * mm, "end": v(5.66, -86.15) * mm});
            skLineSegment(sketch, "E4350", {"start": v(6.68, -84.34) * mm, "end": v(6.16, -85.17) * mm});
            skLineSegment(sketch, "E4351", {"start": v(6.96, -83.97) * mm, "end": v(6.68, -84.34) * mm});
            skLineSegment(sketch, "E4352", {"start": v(7.22, -83.66) * mm, "end": v(6.96, -83.97) * mm});
            skLineSegment(sketch, "E4353", {"start": v(7.47, -83.4) * mm, "end": v(7.22, -83.66) * mm});
            skLineSegment(sketch, "E4354", {"start": v(7.7, -83.2) * mm, "end": v(7.47, -83.4) * mm});
            skLineSegment(sketch, "E4355", {"start": v(8.03, -82.97) * mm, "end": v(7.7, -83.2) * mm});
            skArc(sketch, "E4356", {"start": v(8.03, -82.97) * mm, "mid": v(8.36, -82.5) * mm, "end": v(8.27, -81.94) * mm});
            skArc(sketch, "E4357", {"start": v(7.93, -81.34) * mm, "mid": v(8.1, -81.64) * mm, "end": v(8.27, -81.94) * mm});
            skArc(sketch, "E4358", {"start": v(7.93, -81.34) * mm, "mid": v(7.48, -80.98) * mm, "end": v(6.91, -81.03) * mm});
            skLineSegment(sketch, "E4359", {"start": v(4.07, -81.56) * mm, "end": v(2.98, -81.5) * mm});
            skLineSegment(sketch, "E4360", {"start": v(5.06, -81.52) * mm, "end": v(4.07, -81.56) * mm});
            skLineSegment(sketch, "E4361", {"start": v(5.5, -81.46) * mm, "end": v(5.06, -81.52) * mm});
            skLineSegment(sketch, "E4362", {"start": v(5.91, -81.4) * mm, "end": v(5.5, -81.46) * mm});
            skLineSegment(sketch, "E4363", {"start": v(6.26, -81.3) * mm, "end": v(5.91, -81.4) * mm});
            skLineSegment(sketch, "E4364", {"start": v(6.54, -81.2) * mm, "end": v(6.26, -81.3) * mm});
            skLineSegment(sketch, "E4365", {"start": v(6.91, -81.03) * mm, "end": v(6.54, -81.2) * mm});
            skArc(sketch, "E4366", {"start": v(2.43, -80.18) * mm, "mid": v(2.7, -80.84) * mm, "end": v(2.98, -81.5) * mm});
            skLineSegment(sketch, "E4367", {"start": v(3.16, -79.36) * mm, "end": v(2.43, -80.18) * mm});
            skLineSegment(sketch, "E4368", {"start": v(3.89, -78.7) * mm, "end": v(3.16, -79.36) * mm});
            skLineSegment(sketch, "E4369", {"start": v(4.24, -78.41) * mm, "end": v(3.89, -78.7) * mm});
            skLineSegment(sketch, "E4370", {"start": v(4.58, -78.18) * mm, "end": v(4.24, -78.41) * mm});
            skLineSegment(sketch, "E4371", {"start": v(4.9, -78) * mm, "end": v(4.58, -78.18) * mm});
            skLineSegment(sketch, "E4372", {"start": v(5.15, -77.86) * mm, "end": v(4.9, -78) * mm});
            skLineSegment(sketch, "E4373", {"start": v(5.54, -77.73) * mm, "end": v(5.15, -77.86) * mm});
            skArc(sketch, "E4374", {"start": v(5.54, -77.73) * mm, "mid": v(5.98, -77.36) * mm, "end": v(6.04, -76.79) * mm});
            skArc(sketch, "E4375", {"start": v(9.67, -13.55) * mm, "mid": v(9.89, -13.83) * mm, "end": v(10.11, -14.1) * mm});
            skArc(sketch, "E4376", {"start": v(9.67, -13.55) * mm, "mid": v(9.17, -13.27) * mm, "end": v(8.61, -13.4) * mm});
            skLineSegment(sketch, "E4377", {"start": v(5.89, -14.38) * mm, "end": v(4.8, -14.48) * mm});
            skLineSegment(sketch, "E4378", {"start": v(6.85, -14.2) * mm, "end": v(5.89, -14.38) * mm});
            skLineSegment(sketch, "E4379", {"start": v(7.2, -14.1) * mm, "end": v(6.85, -14.2) * mm});
            skLineSegment(sketch, "E4380", {"start": v(7.54, -13.98) * mm, "end": v(7.2, -14.1) * mm});
            skLineSegment(sketch, "E4381", {"start": v(7.84, -13.87) * mm, "end": v(7.54, -13.98) * mm});
            skLineSegment(sketch, "E4382", {"start": v(8.09, -13.75) * mm, "end": v(7.84, -13.87) * mm});
            skLineSegment(sketch, "E4383", {"start": v(8.27, -13.65) * mm, "end": v(8.09, -13.75) * mm});
            skLineSegment(sketch, "E4384", {"start": v(8.61, -13.4) * mm, "end": v(8.27, -13.65) * mm});
            skArc(sketch, "E4385", {"start": v(4.07, -13.27) * mm, "mid": v(4.43, -13.88) * mm, "end": v(4.8, -14.48) * mm});
            skLineSegment(sketch, "E4386", {"start": v(4.66, -12.36) * mm, "end": v(4.07, -13.27) * mm});
            skLineSegment(sketch, "E4387", {"start": v(5.26, -11.6) * mm, "end": v(4.66, -12.36) * mm});
            skLineSegment(sketch, "E4388", {"start": v(5.52, -11.31) * mm, "end": v(5.26, -11.6) * mm});
            skLineSegment(sketch, "E4389", {"start": v(5.77, -11.07) * mm, "end": v(5.52, -11.31) * mm});
            skLineSegment(sketch, "E4390", {"start": v(6, -10.86) * mm, "end": v(5.77, -11.07) * mm});
            skLineSegment(sketch, "E4391", {"start": v(6.22, -10.7) * mm, "end": v(6, -10.86) * mm});
            skLineSegment(sketch, "E4392", {"start": v(6.4, -10.58) * mm, "end": v(6.22, -10.7) * mm});
            skLineSegment(sketch, "E4393", {"start": v(6.77, -10.39) * mm, "end": v(6.4, -10.58) * mm});
            skArc(sketch, "E4394", {"start": v(6.77, -10.39) * mm, "mid": v(7.16, -9.95) * mm, "end": v(7.13, -9.38) * mm});
            skArc(sketch, "E4395", {"start": v(6.85, -8.74) * mm, "mid": v(6.99, -9.06) * mm, "end": v(7.13, -9.38) * mm});
            skArc(sketch, "E4396", {"start": v(6.85, -8.74) * mm, "mid": v(6.45, -8.32) * mm, "end": v(5.87, -8.3) * mm});
            skLineSegment(sketch, "E4397", {"start": v(2.99, -8.51) * mm, "end": v(1.92, -8.32) * mm});
            skLineSegment(sketch, "E4398", {"start": v(3.96, -8.59) * mm, "end": v(2.99, -8.51) * mm});
            skLineSegment(sketch, "E4399", {"start": v(4.34, -8.6) * mm, "end": v(3.96, -8.59) * mm});
            skLineSegment(sketch, "E4400", {"start": v(4.69, -8.58) * mm, "end": v(4.34, -8.6) * mm});
            skLineSegment(sketch, "E4401", {"start": v(5, -8.54) * mm, "end": v(4.69, -8.58) * mm});
            skLineSegment(sketch, "E4402", {"start": v(5.27, -8.5) * mm, "end": v(5, -8.54) * mm});
            skLineSegment(sketch, "E4403", {"start": v(5.47, -8.45) * mm, "end": v(5.27, -8.5) * mm});
            skLineSegment(sketch, "E4404", {"start": v(5.87, -8.3) * mm, "end": v(5.47, -8.45) * mm});
            skArc(sketch, "E4405", {"start": v(1.54, -6.95) * mm, "mid": v(1.72, -7.64) * mm, "end": v(1.92, -8.32) * mm});
            skLineSegment(sketch, "E4406", {"start": v(2.35, -6.23) * mm, "end": v(1.54, -6.95) * mm});
            skLineSegment(sketch, "E4407", {"start": v(3.14, -5.66) * mm, "end": v(2.35, -6.23) * mm});
            skLineSegment(sketch, "E4408", {"start": v(3.46, -5.46) * mm, "end": v(3.14, -5.66) * mm});
            skLineSegment(sketch, "E4409", {"start": v(3.77, -5.3) * mm, "end": v(3.46, -5.46) * mm});
            skLineSegment(sketch, "E4410", {"start": v(4.05, -5.15) * mm, "end": v(3.77, -5.3) * mm});
            skLineSegment(sketch, "E4411", {"start": v(4.3, -5.05) * mm, "end": v(4.05, -5.15) * mm});
            skLineSegment(sketch, "E4412", {"start": v(4.5, -4.99) * mm, "end": v(4.3, -5.05) * mm});
            skLineSegment(sketch, "E4413", {"start": v(4.92, -4.9) * mm, "end": v(4.5, -4.99) * mm});
            skArc(sketch, "E4414", {"start": v(4.92, -4.9) * mm, "mid": v(5.4, -4.59) * mm, "end": v(5.53, -4.03) * mm});
            skArc(sketch, "E4415", {"start": v(5.44, -3.34) * mm, "mid": v(5.48, -3.68) * mm, "end": v(5.53, -4.03) * mm});
            skArc(sketch, "E4416", {"start": v(5.44, -3.34) * mm, "mid": v(5.16, -2.83) * mm, "end": v(4.6, -2.66) * mm});
            skLineSegment(sketch, "E4417", {"start": v(1.78, -2.07) * mm, "end": v(0.8, -1.6) * mm});
            skLineSegment(sketch, "E4418", {"start": v(2.7, -2.41) * mm, "end": v(1.78, -2.07) * mm});
            skLineSegment(sketch, "E4419", {"start": v(3.05, -2.52) * mm, "end": v(2.7, -2.41) * mm});
            skLineSegment(sketch, "E4420", {"start": v(3.4, -2.6) * mm, "end": v(3.05, -2.52) * mm});
            skLineSegment(sketch, "E4421", {"start": v(3.7, -2.65) * mm, "end": v(3.4, -2.6) * mm});
            skLineSegment(sketch, "E4422", {"start": v(3.98, -2.68) * mm, "end": v(3.7, -2.65) * mm});
            skLineSegment(sketch, "E4423", {"start": v(4.19, -2.69) * mm, "end": v(3.98, -2.68) * mm});
            skLineSegment(sketch, "E4424", {"start": v(4.6, -2.66) * mm, "end": v(4.19, -2.69) * mm});
            skArc(sketch, "E4425", {"start": v(0.8, -0.18) * mm, "mid": v(0.8, -0.9) * mm, "end": v(0.8, -1.6) * mm});
            skLineSegment(sketch, "E4426", {"start": v(1.78, 0.3) * mm, "end": v(0.8, -0.18) * mm});
            skLineSegment(sketch, "E4427", {"start": v(-58.58, 14.08) * mm, "end": v(-58.43, 14.22) * mm});
            skLineSegment(sketch, "E4428", {"start": v(-58.43, 14.22) * mm, "end": v(-58.24, 14.41) * mm});
            skLineSegment(sketch, "E4429", {"start": v(-58.24, 14.41) * mm, "end": v(-58.03, 14.65) * mm});
            skLineSegment(sketch, "E4430", {"start": v(-58.03, 14.65) * mm, "end": v(-57.81, 14.93) * mm});
            skLineSegment(sketch, "E4431", {"start": v(-57.81, 14.93) * mm, "end": v(-57.6, 15.24) * mm});
            skLineSegment(sketch, "E4432", {"start": v(-57.6, 15.24) * mm, "end": v(-57.1, 16.08) * mm});
            skLineSegment(sketch, "E4433", {"start": v(-57.1, 16.08) * mm, "end": v(-56.64, 17.06) * mm});
            skArc(sketch, "E4434", {"start": v(-56.64, 17.06) * mm, "mid": v(-57.08, 17.62) * mm, "end": v(-57.54, 18.16) * mm});
            skLineSegment(sketch, "E4435", {"start": v(-61.16, 16.58) * mm, "end": v(-60.85, 16.87) * mm});
            skLineSegment(sketch, "E4436", {"start": v(-60.85, 16.87) * mm, "end": v(-60.69, 17) * mm});
            skLineSegment(sketch, "E4437", {"start": v(-60.69, 17) * mm, "end": v(-60.46, 17.14) * mm});
            skLineSegment(sketch, "E4438", {"start": v(-60.46, 17.14) * mm, "end": v(-60.18, 17.3) * mm});
            skLineSegment(sketch, "E4439", {"start": v(-60.18, 17.3) * mm, "end": v(-59.87, 17.45) * mm});
            skLineSegment(sketch, "E4440", {"start": v(-59.87, 17.45) * mm, "end": v(-59.52, 17.6) * mm});
            skLineSegment(sketch, "E4441", {"start": v(-59.52, 17.6) * mm, "end": v(-58.6, 17.92) * mm});
            skLineSegment(sketch, "E4442", {"start": v(-58.6, 17.92) * mm, "end": v(-57.54, 18.16) * mm});
            skArc(sketch, "E4443", {"start": v(-62.23, 16.58) * mm, "mid": v(-61.7, 16.37) * mm, "end": v(-61.16, 16.58) * mm});
            skArc(sketch, "E4444", {"start": v(-62.23, 16.58) * mm, "mid": v(-62.48, 16.82) * mm, "end": v(-62.74, 17.06) * mm});
            skArc(sketch, "E4445", {"start": v(-62.82, 18.13) * mm, "mid": v(-63, 17.58) * mm, "end": v(-62.74, 17.06) * mm});
            skLineSegment(sketch, "E4446", {"start": v(-62.82, 18.13) * mm, "end": v(-62.55, 18.46) * mm});
            skLineSegment(sketch, "E4447", {"start": v(-62.55, 18.46) * mm, "end": v(-62.44, 18.63) * mm});
            skLineSegment(sketch, "E4448", {"start": v(-62.44, 18.63) * mm, "end": v(-62.3, 18.87) * mm});
            skLineSegment(sketch, "E4449", {"start": v(-62.3, 18.87) * mm, "end": v(-62.17, 19.16) * mm});
            skLineSegment(sketch, "E4450", {"start": v(-91.13, 19.76) * mm, "end": v(-92, 20.2) * mm});
            skLineSegment(sketch, "E4451", {"start": v(-92, 20.2) * mm, "end": v(-93.02, 20.59) * mm});
            skArc(sketch, "E4452", {"start": v(-93.02, 20.59) * mm, "mid": v(-93.54, 20.11) * mm, "end": v(-94.05, 19.62) * mm});
            skLineSegment(sketch, "E4453", {"start": v(-92.23, 16.12) * mm, "end": v(-92.54, 16.4) * mm});
            skLineSegment(sketch, "E4454", {"start": v(-92.54, 16.4) * mm, "end": v(-92.67, 16.56) * mm});
            skLineSegment(sketch, "E4455", {"start": v(-92.67, 16.56) * mm, "end": v(-92.84, 16.78) * mm});
            skLineSegment(sketch, "E4456", {"start": v(-92.84, 16.78) * mm, "end": v(-93, 17.05) * mm});
            skLineSegment(sketch, "E4457", {"start": v(-93, 17.05) * mm, "end": v(-93.18, 17.35) * mm});
            skLineSegment(sketch, "E4458", {"start": v(-93.18, 17.35) * mm, "end": v(-93.36, 17.68) * mm});
            skLineSegment(sketch, "E4459", {"start": v(-93.36, 17.68) * mm, "end": v(-93.73, 18.59) * mm});
            skLineSegment(sketch, "E4460", {"start": v(-93.73, 18.59) * mm, "end": v(-94.05, 19.62) * mm});
            skArc(sketch, "E4461", {"start": v(-92.16, 15.05) * mm, "mid": v(-91.98, 15.6) * mm, "end": v(-92.23, 16.12) * mm});
            skArc(sketch, "E4462", {"start": v(-92.16, 15.05) * mm, "mid": v(-92.38, 14.78) * mm, "end": v(-92.6, 14.5) * mm});
            skArc(sketch, "E4463", {"start": v(-93.66, 14.36) * mm, "mid": v(-93.1, 14.22) * mm, "end": v(-92.6, 14.5) * mm});
            skLineSegment(sketch, "E4464", {"start": v(-93.66, 14.36) * mm, "end": v(-94, 14.6) * mm});
            skLineSegment(sketch, "E4465", {"start": v(-94, 14.6) * mm, "end": v(-94.18, 14.7) * mm});
            skLineSegment(sketch, "E4466", {"start": v(-94.18, 14.7) * mm, "end": v(-94.43, 14.82) * mm});
            skLineSegment(sketch, "E4467", {"start": v(-94.43, 14.82) * mm, "end": v(-94.73, 14.94) * mm});
            skLineSegment(sketch, "E4468", {"start": v(-94.73, 14.94) * mm, "end": v(-95.06, 15.05) * mm});
            skLineSegment(sketch, "E4469", {"start": v(-95.06, 15.05) * mm, "end": v(-95.42, 15.15) * mm});
            skLineSegment(sketch, "E4470", {"start": v(-95.42, 15.15) * mm, "end": v(-96.38, 15.33) * mm});
            skLineSegment(sketch, "E4471", {"start": v(-96.38, 15.33) * mm, "end": v(-97.46, 15.43) * mm});
            skArc(sketch, "E4472", {"start": v(-97.46, 15.43) * mm, "mid": v(-97.84, 14.83) * mm, "end": v(-98.2, 14.22) * mm});
            skLineSegment(sketch, "E4473", {"start": v(-95.5, 11.34) * mm, "end": v(-95.87, 11.53) * mm});
            skLineSegment(sketch, "E4474", {"start": v(-95.87, 11.53) * mm, "end": v(-96.04, 11.65) * mm});
            skLineSegment(sketch, "E4475", {"start": v(-96.04, 11.65) * mm, "end": v(-96.26, 11.81) * mm});
            skLineSegment(sketch, "E4476", {"start": v(-96.26, 11.81) * mm, "end": v(-96.5, 12.02) * mm});
            skLineSegment(sketch, "E4477", {"start": v(-96.5, 12.02) * mm, "end": v(-96.75, 12.27) * mm});
            skLineSegment(sketch, "E4478", {"start": v(-96.75, 12.27) * mm, "end": v(-97, 12.54) * mm});
            skLineSegment(sketch, "E4479", {"start": v(-97, 12.54) * mm, "end": v(-97.61, 13.3) * mm});
            skLineSegment(sketch, "E4480", {"start": v(-97.61, 13.3) * mm, "end": v(-98.2, 14.22) * mm});
            skArc(sketch, "E4481", {"start": v(-95.14, 10.33) * mm, "mid": v(-95.11, 10.9) * mm, "end": v(-95.5, 11.34) * mm});
            skArc(sketch, "E4482", {"start": v(-95.14, 10.33) * mm, "mid": v(-95.28, 10) * mm, "end": v(-95.42, 9.69) * mm});
            skArc(sketch, "E4483", {"start": v(-96.4, 9.26) * mm, "mid": v(-95.82, 9.28) * mm, "end": v(-95.42, 9.69) * mm});
            skLineSegment(sketch, "E4484", {"start": v(-96.4, 9.26) * mm, "end": v(-96.8, 9.4) * mm});
            skLineSegment(sketch, "E4485", {"start": v(-96.8, 9.4) * mm, "end": v(-97, 9.45) * mm});
            skLineSegment(sketch, "E4486", {"start": v(-97, 9.45) * mm, "end": v(-97.27, 9.5) * mm});
            skArc(sketch, "E4487", {"start": v(-90.16, 54.26) * mm, "mid": v(-90, 54.81) * mm, "end": v(-90.27, 55.33) * mm});
            skLineSegment(sketch, "E4488", {"start": v(-97.27, 9.5) * mm, "end": v(-97.58, 9.53) * mm});
            skLineSegment(sketch, "E4489", {"start": v(-90.16, 54.26) * mm, "end": v(-90.44, 53.88) * mm});
            skLineSegment(sketch, "E4490", {"start": v(-97.58, 9.53) * mm, "end": v(-97.93, 9.54) * mm});
            skLineSegment(sketch, "E4491", {"start": v(-90.44, 53.88) * mm, "end": v(-90.54, 53.71) * mm});
            skLineSegment(sketch, "E4492", {"start": v(-97.93, 9.54) * mm, "end": v(-98.3, 9.54) * mm});
            skLineSegment(sketch, "E4493", {"start": v(-90.54, 53.71) * mm, "end": v(-90.66, 53.47) * mm});
            skLineSegment(sketch, "E4494", {"start": v(-98.3, 9.54) * mm, "end": v(-99.28, 9.46) * mm});
            skLineSegment(sketch, "E4495", {"start": v(-90.66, 53.47) * mm, "end": v(-90.78, 53.19) * mm});
            skLineSegment(sketch, "E4496", {"start": v(-99.28, 9.46) * mm, "end": v(-100.35, 9.27) * mm});
            skLineSegment(sketch, "E4497", {"start": v(-90.78, 53.19) * mm, "end": v(-90.9, 52.86) * mm});
            skArc(sketch, "E4498", {"start": v(-100.35, 9.27) * mm, "mid": v(-100.55, 8.59) * mm, "end": v(-100.73, 7.9) * mm});
            skLineSegment(sketch, "E4499", {"start": v(-90.9, 52.86) * mm, "end": v(-91, 52.5) * mm});
            skLineSegment(sketch, "E4500", {"start": v(-97.35, 5.85) * mm, "end": v(-97.77, 5.94) * mm});
            skLineSegment(sketch, "E4501", {"start": v(-91, 52.5) * mm, "end": v(-91.21, 51.56) * mm});
            skLineSegment(sketch, "E4502", {"start": v(-97.77, 5.94) * mm, "end": v(-97.96, 6) * mm});
            skLineSegment(sketch, "E4503", {"start": v(-91.21, 51.56) * mm, "end": v(-91.33, 50.5) * mm});
            skLineSegment(sketch, "E4504", {"start": v(-97.96, 6) * mm, "end": v(-98.22, 6.1) * mm});
            skArc(sketch, "E4505", {"start": v(-91.33, 50.5) * mm, "mid": v(-90.75, 50.1) * mm, "end": v(-90.15, 49.73) * mm});
            skLineSegment(sketch, "E4506", {"start": v(-98.22, 6.1) * mm, "end": v(-98.5, 6.24) * mm});
            skLineSegment(sketch, "E4507", {"start": v(-87.21, 52.36) * mm, "end": v(-87.43, 51.96) * mm});
            skLineSegment(sketch, "E4508", {"start": v(-98.5, 6.24) * mm, "end": v(-98.8, 6.41) * mm});
            skLineSegment(sketch, "E4509", {"start": v(-87.43, 51.96) * mm, "end": v(-87.55, 51.8) * mm});
            skLineSegment(sketch, "E4510", {"start": v(-98.8, 6.41) * mm, "end": v(-99.13, 6.6) * mm});
            skLineSegment(sketch, "E4511", {"start": v(-87.55, 51.8) * mm, "end": v(-87.72, 51.58) * mm});
            skLineSegment(sketch, "E4512", {"start": v(-99.13, 6.6) * mm, "end": v(-99.92, 7.18) * mm});
            skLineSegment(sketch, "E4513", {"start": v(-87.72, 51.58) * mm, "end": v(-87.93, 51.35) * mm});
            skLineSegment(sketch, "E4514", {"start": v(-99.92, 7.18) * mm, "end": v(-100.73, 7.9) * mm});
            skLineSegment(sketch, "E4515", {"start": v(-87.93, 51.35) * mm, "end": v(-88.17, 51.11) * mm});
            skArc(sketch, "E4516", {"start": v(-96.74, 4.98) * mm, "mid": v(-96.87, 5.54) * mm, "end": v(-97.35, 5.85) * mm});
            skLineSegment(sketch, "E4517", {"start": v(-88.17, 51.11) * mm, "end": v(-88.45, 50.86) * mm});
            skArc(sketch, "E4518", {"start": v(-96.74, 4.98) * mm, "mid": v(-96.79, 4.63) * mm, "end": v(-96.83, 4.29) * mm});
            skLineSegment(sketch, "E4519", {"start": v(-88.45, 50.86) * mm, "end": v(-89.23, 50.28) * mm});
            skArc(sketch, "E4520", {"start": v(-97.66, 3.61) * mm, "mid": v(-97.1, 3.78) * mm, "end": v(-96.83, 4.29) * mm});
            skLineSegment(sketch, "E4521", {"start": v(-89.23, 50.28) * mm, "end": v(-90.15, 49.73) * mm});
            skLineSegment(sketch, "E4522", {"start": v(-97.66, 3.61) * mm, "end": v(-98.08, 3.64) * mm});
            skArc(sketch, "E4523", {"start": v(-86.2, 52.7) * mm, "mid": v(-86.77, 52.74) * mm, "end": v(-87.21, 52.36) * mm});
            skLineSegment(sketch, "E4524", {"start": v(-98.08, 3.64) * mm, "end": v(-98.29, 3.63) * mm});
            skArc(sketch, "E4525", {"start": v(-86.2, 52.7) * mm, "mid": v(-85.87, 52.55) * mm, "end": v(-85.55, 52.41) * mm});
            skLineSegment(sketch, "E4526", {"start": v(-98.29, 3.63) * mm, "end": v(-98.56, 3.6) * mm});
            skArc(sketch, "E4527", {"start": v(-85.14, 51.42) * mm, "mid": v(-85.14, 52) * mm, "end": v(-85.55, 52.41) * mm});
            skLineSegment(sketch, "E4528", {"start": v(-98.56, 3.6) * mm, "end": v(-98.87, 3.55) * mm});
            skLineSegment(sketch, "E4529", {"start": v(-85.14, 51.42) * mm, "end": v(-85.3, 50.98) * mm});
            skLineSegment(sketch, "E4530", {"start": v(-98.87, 3.55) * mm, "end": v(-99.21, 3.47) * mm});
            skLineSegment(sketch, "E4531", {"start": v(-85.3, 50.98) * mm, "end": v(-85.35, 50.79) * mm});
            skLineSegment(sketch, "E4532", {"start": v(-99.21, 3.47) * mm, "end": v(-99.58, 3.37) * mm});
            skLineSegment(sketch, "E4533", {"start": v(-85.35, 50.79) * mm, "end": v(-85.4, 50.52) * mm});
            skLineSegment(sketch, "E4534", {"start": v(-99.58, 3.37) * mm, "end": v(-100.5, 3.03) * mm});
            skLineSegment(sketch, "E4535", {"start": v(-85.4, 50.52) * mm, "end": v(-85.44, 50.21) * mm});
            skLineSegment(sketch, "E4536", {"start": v(-100.5, 3.03) * mm, "end": v(-101.47, 2.55) * mm});
            skLineSegment(sketch, "E4537", {"start": v(-85.44, 50.21) * mm, "end": v(-85.46, 49.87) * mm});
            skArc(sketch, "E4538", {"start": v(-101.47, 2.55) * mm, "mid": v(-101.48, 1.84) * mm, "end": v(-101.47, 1.13) * mm});
            skLineSegment(sketch, "E4539", {"start": v(-85.46, 49.87) * mm, "end": v(-85.46, 49.5) * mm});
            skLineSegment(sketch, "E4540", {"start": v(-97.66, 0.07) * mm, "end": v(-98.08, 0.04) * mm});
            skLineSegment(sketch, "E4541", {"start": v(-85.46, 49.5) * mm, "end": v(-85.4, 48.53) * mm});
            skLineSegment(sketch, "E4542", {"start": v(-98.08, 0.04) * mm, "end": v(-98.29, 0.05) * mm});
            skLineSegment(sketch, "E4543", {"start": v(-85.4, 48.53) * mm, "end": v(-85.2, 47.47) * mm});
            skLineSegment(sketch, "E4544", {"start": v(-98.29, 0.05) * mm, "end": v(-98.56, 0.08) * mm});
            skArc(sketch, "E4545", {"start": v(-85.2, 47.47) * mm, "mid": v(-84.53, 47.26) * mm, "end": v(-83.85, 47.08) * mm});
            skLineSegment(sketch, "E4546", {"start": v(-98.56, 0.08) * mm, "end": v(-98.87, 0.14) * mm});
            skLineSegment(sketch, "E4547", {"start": v(-81.78, 50.43) * mm, "end": v(-81.88, 49.98) * mm});
            skLineSegment(sketch, "E4548", {"start": v(-98.87, 0.14) * mm, "end": v(-99.21, 0.22) * mm});
            skLineSegment(sketch, "E4549", {"start": v(-81.88, 49.98) * mm, "end": v(-81.94, 49.79) * mm});
            skLineSegment(sketch, "E4550", {"start": v(-99.21, 0.22) * mm, "end": v(-99.58, 0.32) * mm});
            skLineSegment(sketch, "E4551", {"start": v(-81.94, 49.79) * mm, "end": v(-82.04, 49.54) * mm});
            skLineSegment(sketch, "E4552", {"start": v(-99.58, 0.32) * mm, "end": v(-100.5, 0.66) * mm});
            skLineSegment(sketch, "E4553", {"start": v(-82.04, 49.54) * mm, "end": v(-82.18, 49.26) * mm});
            skLineSegment(sketch, "E4554", {"start": v(-100.5, 0.66) * mm, "end": v(-101.47, 1.13) * mm});
            skLineSegment(sketch, "E4555", {"start": v(-82.18, 49.26) * mm, "end": v(-82.35, 48.96) * mm});
            skArc(sketch, "E4556", {"start": v(-96.83, -0.6) * mm, "mid": v(-97.1, -0.1) * mm, "end": v(-97.66, 0.07) * mm});
            skLineSegment(sketch, "E4557", {"start": v(-82.35, 48.96) * mm, "end": v(-82.55, 48.64) * mm});
            skArc(sketch, "E4558", {"start": v(-96.83, -0.6) * mm, "mid": v(-96.79, -0.95) * mm, "end": v(-96.74, -1.3) * mm});
            skLineSegment(sketch, "E4559", {"start": v(-82.55, 48.64) * mm, "end": v(-83.13, 47.87) * mm});
            skArc(sketch, "E4560", {"start": v(-97.35, -2.17) * mm, "mid": v(-96.87, -1.86) * mm, "end": v(-96.74, -1.3) * mm});
            skLineSegment(sketch, "E4561", {"start": v(-83.13, 47.87) * mm, "end": v(-83.85, 47.08) * mm});
            skLineSegment(sketch, "E4562", {"start": v(-97.35, -2.17) * mm, "end": v(-97.77, -2.25) * mm});
            skArc(sketch, "E4563", {"start": v(-80.9, 51.04) * mm, "mid": v(-81.46, 50.92) * mm, "end": v(-81.78, 50.43) * mm});
            skLineSegment(sketch, "E4564", {"start": v(-97.77, -2.25) * mm, "end": v(-97.96, -2.32) * mm});
            skArc(sketch, "E4565", {"start": v(-80.9, 51.04) * mm, "mid": v(-80.55, 51) * mm, "end": v(-80.2, 50.94) * mm});
            skLineSegment(sketch, "E4566", {"start": v(-97.96, -2.32) * mm, "end": v(-98.22, -2.42) * mm});
            skArc(sketch, "E4567", {"start": v(-79.52, 50.1) * mm, "mid": v(-79.7, 50.66) * mm, "end": v(-80.2, 50.94) * mm});
            skLineSegment(sketch, "E4568", {"start": v(-98.22, -2.42) * mm, "end": v(-98.5, -2.56) * mm});
            skLineSegment(sketch, "E4569", {"start": v(-79.52, 50.1) * mm, "end": v(-79.56, 49.64) * mm});
            skLineSegment(sketch, "E4570", {"start": v(-98.5, -2.56) * mm, "end": v(-98.8, -2.73) * mm});
            skLineSegment(sketch, "E4571", {"start": v(-79.56, 49.64) * mm, "end": v(-79.55, 49.44) * mm});
            skLineSegment(sketch, "E4572", {"start": v(-98.8, -2.73) * mm, "end": v(-99.13, -2.92) * mm});
            skLineSegment(sketch, "E4573", {"start": v(-79.55, 49.44) * mm, "end": v(-79.52, 49.18) * mm});
            skLineSegment(sketch, "E4574", {"start": v(-99.13, -2.92) * mm, "end": v(-99.92, -3.5) * mm});
            skLineSegment(sketch, "E4575", {"start": v(-79.52, 49.18) * mm, "end": v(-79.47, 48.87) * mm});
            skLineSegment(sketch, "E4576", {"start": v(-99.92, -3.5) * mm, "end": v(-100.73, -4.22) * mm});
            skLineSegment(sketch, "E4577", {"start": v(-79.47, 48.87) * mm, "end": v(-79.4, 48.53) * mm});
            skArc(sketch, "E4578", {"start": v(-100.73, -4.22) * mm, "mid": v(-100.55, -4.9) * mm, "end": v(-100.35, -5.58) * mm});
            skLineSegment(sketch, "E4579", {"start": v(-79.4, 48.53) * mm, "end": v(-79.29, 48.17) * mm});
            skLineSegment(sketch, "E4580", {"start": v(-96.4, -5.58) * mm, "end": v(-96.8, -5.72) * mm});
            skLineSegment(sketch, "E4581", {"start": v(-79.29, 48.17) * mm, "end": v(-78.95, 47.27) * mm});
            skLineSegment(sketch, "E4582", {"start": v(-96.8, -5.72) * mm, "end": v(-97, -5.77) * mm});
            skLineSegment(sketch, "E4583", {"start": v(-78.95, 47.27) * mm, "end": v(-78.48, 46.3) * mm});
            skLineSegment(sketch, "E4584", {"start": v(-97, -5.77) * mm, "end": v(-97.27, -5.81) * mm});
            skArc(sketch, "E4585", {"start": v(-78.48, 46.3) * mm, "mid": v(-77.77, 46.3) * mm, "end": v(-77.07, 46.3) * mm});
            skLineSegment(sketch, "E4586", {"start": v(-97.27, -5.81) * mm, "end": v(-97.58, -5.84) * mm});
            skLineSegment(sketch, "E4587", {"start": v(-76.02, 50.1) * mm, "end": v(-75.99, 49.64) * mm});
            skLineSegment(sketch, "E4588", {"start": v(-97.58, -5.84) * mm, "end": v(-97.93, -5.86) * mm});
            skLineSegment(sketch, "E4589", {"start": v(-75.99, 49.64) * mm, "end": v(-76, 49.44) * mm});
            skLineSegment(sketch, "E4590", {"start": v(-97.93, -5.86) * mm, "end": v(-98.3, -5.86) * mm});
            skLineSegment(sketch, "E4591", {"start": v(-76, 49.44) * mm, "end": v(-76.02, 49.18) * mm});
            skLineSegment(sketch, "E4592", {"start": v(-98.3, -5.86) * mm, "end": v(-99.28, -5.78) * mm});
            skLineSegment(sketch, "E4593", {"start": v(-76.02, 49.18) * mm, "end": v(-76.08, 48.87) * mm});
            skLineSegment(sketch, "E4594", {"start": v(-99.28, -5.78) * mm, "end": v(-100.35, -5.58) * mm});
            skLineSegment(sketch, "E4595", {"start": v(-76.08, 48.87) * mm, "end": v(-76.15, 48.53) * mm});
            skArc(sketch, "E4596", {"start": v(-95.42, -6) * mm, "mid": v(-95.82, -5.6) * mm, "end": v(-96.4, -5.58) * mm});
            skLineSegment(sketch, "E4597", {"start": v(-76.15, 48.53) * mm, "end": v(-76.25, 48.17) * mm});
            skArc(sketch, "E4598", {"start": v(-95.42, -6) * mm, "mid": v(-95.28, -6.33) * mm, "end": v(-95.14, -6.64) * mm});
            skLineSegment(sketch, "E4599", {"start": v(-76.25, 48.17) * mm, "end": v(-76.6, 47.27) * mm});
            skArc(sketch, "E4600", {"start": v(-95.5, -7.65) * mm, "mid": v(-95.11, -7.22) * mm, "end": v(-95.14, -6.64) * mm});
            skLineSegment(sketch, "E4601", {"start": v(-76.6, 47.27) * mm, "end": v(-77.07, 46.3) * mm});
            skLineSegment(sketch, "E4602", {"start": v(-95.5, -7.65) * mm, "end": v(-95.87, -7.85) * mm});
            skArc(sketch, "E4603", {"start": v(-75.34, 50.94) * mm, "mid": v(-75.85, 50.66) * mm, "end": v(-76.02, 50.1) * mm});
            skLineSegment(sketch, "E4604", {"start": v(-95.87, -7.85) * mm, "end": v(-96.04, -7.96) * mm});
            skArc(sketch, "E4605", {"start": v(-75.34, 50.94) * mm, "mid": v(-75, 51) * mm, "end": v(-74.65, 51.04) * mm});
            skLineSegment(sketch, "E4606", {"start": v(-96.04, -7.96) * mm, "end": v(-96.26, -8.13) * mm});
            skArc(sketch, "E4607", {"start": v(-73.76, 50.43) * mm, "mid": v(-74.08, 50.92) * mm, "end": v(-74.65, 51.04) * mm});
            skLineSegment(sketch, "E4608", {"start": v(-96.26, -8.13) * mm, "end": v(-96.5, -8.34) * mm});
            skLineSegment(sketch, "E4609", {"start": v(-73.76, 50.43) * mm, "end": v(-73.67, 49.98) * mm});
            skLineSegment(sketch, "E4610", {"start": v(-96.5, -8.34) * mm, "end": v(-96.75, -8.58) * mm});
            skLineSegment(sketch, "E4611", {"start": v(-73.67, 49.98) * mm, "end": v(-73.6, 49.79) * mm});
            skLineSegment(sketch, "E4612", {"start": v(-96.75, -8.58) * mm, "end": v(-97, -8.86) * mm});
            skLineSegment(sketch, "E4613", {"start": v(-73.6, 49.79) * mm, "end": v(-73.5, 49.54) * mm});
            skLineSegment(sketch, "E4614", {"start": v(-97, -8.86) * mm, "end": v(-97.61, -9.62) * mm});
            skLineSegment(sketch, "E4615", {"start": v(-73.5, 49.54) * mm, "end": v(-73.36, 49.26) * mm});
            skLineSegment(sketch, "E4616", {"start": v(-97.61, -9.62) * mm, "end": v(-98.2, -10.54) * mm});
            skLineSegment(sketch, "E4617", {"start": v(-73.36, 49.26) * mm, "end": v(-73.2, 48.96) * mm});
            skArc(sketch, "E4618", {"start": v(-98.2, -10.54) * mm, "mid": v(-97.84, -11.15) * mm, "end": v(-97.46, -11.75) * mm});
            skLineSegment(sketch, "E4619", {"start": v(-73.2, 48.96) * mm, "end": v(-73, 48.64) * mm});
            skLineSegment(sketch, "E4620", {"start": v(-93.66, -10.68) * mm, "end": v(-94, -10.92) * mm});
            skLineSegment(sketch, "E4621", {"start": v(-73, 48.64) * mm, "end": v(-72.42, 47.87) * mm});
            skLineSegment(sketch, "E4622", {"start": v(-94, -10.92) * mm, "end": v(-94.18, -11.02) * mm});
            skLineSegment(sketch, "E4623", {"start": v(-72.42, 47.87) * mm, "end": v(-71.69, 47.08) * mm});
            skLineSegment(sketch, "E4624", {"start": v(-94.18, -11.02) * mm, "end": v(-94.43, -11.14) * mm});
            skArc(sketch, "E4625", {"start": v(-71.69, 47.08) * mm, "mid": v(-71, 47.26) * mm, "end": v(-70.34, 47.47) * mm});
            skLineSegment(sketch, "E4626", {"start": v(-94.43, -11.14) * mm, "end": v(-94.73, -11.25) * mm});
            skLineSegment(sketch, "E4627", {"start": v(-70.4, 51.42) * mm, "end": v(-70.24, 50.98) * mm});
            skLineSegment(sketch, "E4628", {"start": v(-94.73, -11.25) * mm, "end": v(-95.06, -11.36) * mm});
            skLineSegment(sketch, "E4629", {"start": v(-70.24, 50.98) * mm, "end": v(-70.2, 50.79) * mm});
            skLineSegment(sketch, "E4630", {"start": v(-95.06, -11.36) * mm, "end": v(-95.42, -11.46) * mm});
            skLineSegment(sketch, "E4631", {"start": v(-70.2, 50.79) * mm, "end": v(-70.14, 50.52) * mm});
            skLineSegment(sketch, "E4632", {"start": v(-95.42, -11.46) * mm, "end": v(-96.38, -11.65) * mm});
            skLineSegment(sketch, "E4633", {"start": v(-70.14, 50.52) * mm, "end": v(-70.1, 50.21) * mm});
            skLineSegment(sketch, "E4634", {"start": v(-96.38, -11.65) * mm, "end": v(-97.46, -11.75) * mm});
            skLineSegment(sketch, "E4635", {"start": v(-70.1, 50.21) * mm, "end": v(-70.09, 49.87) * mm});
            skArc(sketch, "E4636", {"start": v(-92.6, -10.82) * mm, "mid": v(-93.1, -10.53) * mm, "end": v(-93.66, -10.68) * mm});
            skLineSegment(sketch, "E4637", {"start": v(-70.09, 49.87) * mm, "end": v(-70.08, 49.5) * mm});
            skArc(sketch, "E4638", {"start": v(-92.6, -10.82) * mm, "mid": v(-92.38, -11.1) * mm, "end": v(-92.16, -11.36) * mm});
            skLineSegment(sketch, "E4639", {"start": v(-70.08, 49.5) * mm, "end": v(-70.15, 48.53) * mm});
            skArc(sketch, "E4640", {"start": v(-96.72, -75) * mm, "mid": v(-96.29, -74.63) * mm, "end": v(-96.22, -74.06) * mm});
            skLineSegment(sketch, "E4641", {"start": v(-70.15, 48.53) * mm, "end": v(-70.34, 47.47) * mm});
            skLineSegment(sketch, "E4642", {"start": v(-96.72, -75) * mm, "end": v(-97.11, -75.13) * mm});
            skArc(sketch, "E4643", {"start": v(-70, 52.41) * mm, "mid": v(-70.4, 52) * mm, "end": v(-70.4, 51.42) * mm});
            skLineSegment(sketch, "E4644", {"start": v(-97.11, -75.13) * mm, "end": v(-97.37, -75.26) * mm});
            skArc(sketch, "E4645", {"start": v(-70, 52.41) * mm, "mid": v(-69.67, 52.55) * mm, "end": v(-69.35, 52.7) * mm});
            skLineSegment(sketch, "E4646", {"start": v(-97.37, -75.26) * mm, "end": v(-97.69, -75.44) * mm});
            skArc(sketch, "E4647", {"start": v(-68.33, 52.36) * mm, "mid": v(-68.77, 52.74) * mm, "end": v(-69.35, 52.7) * mm});
            skLineSegment(sketch, "E4648", {"start": v(-97.69, -75.44) * mm, "end": v(-98.03, -75.68) * mm});
            skLineSegment(sketch, "E4649", {"start": v(-68.33, 52.36) * mm, "end": v(-68.1, 51.96) * mm});
            skLineSegment(sketch, "E4650", {"start": v(-98.03, -75.68) * mm, "end": v(-98.38, -75.96) * mm});
            skLineSegment(sketch, "E4651", {"start": v(-68.1, 51.96) * mm, "end": v(-68, 51.8) * mm});
            skLineSegment(sketch, "E4652", {"start": v(-98.38, -75.96) * mm, "end": v(-99.1, -76.63) * mm});
            skLineSegment(sketch, "E4653", {"start": v(-68, 51.8) * mm, "end": v(-67.83, 51.58) * mm});
            skLineSegment(sketch, "E4654", {"start": v(-99.1, -76.63) * mm, "end": v(-99.83, -77.44) * mm});
            skLineSegment(sketch, "E4655", {"start": v(-67.83, 51.58) * mm, "end": v(-67.61, 51.35) * mm});
            skArc(sketch, "E4656", {"start": v(-99.83, -77.44) * mm, "mid": v(-99.57, -78.1) * mm, "end": v(-99.29, -78.76) * mm});
            skLineSegment(sketch, "E4657", {"start": v(-67.61, 51.35) * mm, "end": v(-67.37, 51.11) * mm});
            skLineSegment(sketch, "E4658", {"start": v(-95.36, -78.3) * mm, "end": v(-95.73, -78.48) * mm});
            skLineSegment(sketch, "E4659", {"start": v(-67.37, 51.11) * mm, "end": v(-67.09, 50.86) * mm});
            skLineSegment(sketch, "E4660", {"start": v(-95.73, -78.48) * mm, "end": v(-96, -78.57) * mm});
            skLineSegment(sketch, "E4661", {"start": v(-67.09, 50.86) * mm, "end": v(-66.31, 50.28) * mm});
            skLineSegment(sketch, "E4662", {"start": v(-96, -78.57) * mm, "end": v(-96.35, -78.66) * mm});
            skLineSegment(sketch, "E4663", {"start": v(-66.31, 50.28) * mm, "end": v(-65.4, 49.73) * mm});
            skLineSegment(sketch, "E4664", {"start": v(-96.35, -78.66) * mm, "end": v(-96.76, -78.73) * mm});
            skArc(sketch, "E4665", {"start": v(-65.4, 49.73) * mm, "mid": v(-64.8, 50.1) * mm, "end": v(-64.2, 50.5) * mm});
            skLineSegment(sketch, "E4666", {"start": v(-96.76, -78.73) * mm, "end": v(-97.21, -78.79) * mm});
            skLineSegment(sketch, "E4667", {"start": v(-65.39, 54.26) * mm, "end": v(-65.1, 53.88) * mm});
            skLineSegment(sketch, "E4668", {"start": v(-97.21, -78.79) * mm, "end": v(-98.2, -78.83) * mm});
            skLineSegment(sketch, "E4669", {"start": v(-65.1, 53.88) * mm, "end": v(-65, 53.71) * mm});
            skLineSegment(sketch, "E4670", {"start": v(-98.2, -78.83) * mm, "end": v(-99.29, -78.76) * mm});
            skLineSegment(sketch, "E4671", {"start": v(-65, 53.71) * mm, "end": v(-64.88, 53.47) * mm});
            skArc(sketch, "E4672", {"start": v(-94.34, -78.6) * mm, "mid": v(-94.79, -78.25) * mm, "end": v(-95.36, -78.3) * mm});
            skLineSegment(sketch, "E4673", {"start": v(-64.88, 53.47) * mm, "end": v(-64.76, 53.19) * mm});
            skArc(sketch, "E4674", {"start": v(-94.34, -78.6) * mm, "mid": v(-94.17, -78.9) * mm, "end": v(-94, -79.2) * mm});
            skLineSegment(sketch, "E4675", {"start": v(-64.76, 53.19) * mm, "end": v(-64.64, 52.86) * mm});
            skArc(sketch, "E4676", {"start": v(-94.23, -80.24) * mm, "mid": v(-93.9, -79.77) * mm, "end": v(-94, -79.2) * mm});
            skLineSegment(sketch, "E4677", {"start": v(-64.64, 52.86) * mm, "end": v(-64.54, 52.5) * mm});
            skLineSegment(sketch, "E4678", {"start": v(-94.23, -80.24) * mm, "end": v(-94.58, -80.47) * mm});
            skLineSegment(sketch, "E4679", {"start": v(-64.54, 52.5) * mm, "end": v(-64.33, 51.56) * mm});
            skLineSegment(sketch, "E4680", {"start": v(-94.58, -80.47) * mm, "end": v(-94.8, -80.67) * mm});
            skLineSegment(sketch, "E4681", {"start": v(-64.33, 51.56) * mm, "end": v(-64.2, 50.5) * mm});
            skLineSegment(sketch, "E4682", {"start": v(-94.8, -80.67) * mm, "end": v(-95.05, -80.93) * mm});
            skArc(sketch, "E4683", {"start": v(-65.27, 55.33) * mm, "mid": v(-65.54, 54.81) * mm, "end": v(-65.39, 54.26) * mm});
            skLineSegment(sketch, "E4684", {"start": v(-95.05, -80.93) * mm, "end": v(-95.31, -81.24) * mm});
            skArc(sketch, "E4685", {"start": v(-65.27, 55.33) * mm, "mid": v(-65, 55.56) * mm, "end": v(-64.74, 55.79) * mm});
            skLineSegment(sketch, "E4686", {"start": v(-95.31, -81.24) * mm, "end": v(-95.59, -81.6) * mm});
            skArc(sketch, "E4687", {"start": v(-63.66, 55.75) * mm, "mid": v(-64.2, 55.99) * mm, "end": v(-64.74, 55.79) * mm});
            skLineSegment(sketch, "E4688", {"start": v(-95.59, -81.6) * mm, "end": v(-96.11, -82.44) * mm});
            skLineSegment(sketch, "E4689", {"start": v(-63.66, 55.75) * mm, "end": v(-63.33, 55.42) * mm});
            skLineSegment(sketch, "E4690", {"start": v(-96.11, -82.44) * mm, "end": v(-96.6, -83.41) * mm});
            skLineSegment(sketch, "E4691", {"start": v(-63.33, 55.42) * mm, "end": v(-63.18, 55.3) * mm});
            skArc(sketch, "E4692", {"start": v(-96.6, -83.41) * mm, "mid": v(-96.18, -83.99) * mm, "end": v(-95.73, -84.55) * mm});
            skLineSegment(sketch, "E4693", {"start": v(-63.18, 55.3) * mm, "end": v(-62.96, 55.14) * mm});
            skLineSegment(sketch, "E4694", {"start": v(-92.06, -83.08) * mm, "end": v(-92.37, -83.35) * mm});
            skLineSegment(sketch, "E4695", {"start": v(-62.96, 55.14) * mm, "end": v(-62.69, 54.98) * mm});
            skLineSegment(sketch, "E4696", {"start": v(-92.37, -83.35) * mm, "end": v(-92.61, -83.5) * mm});
            skLineSegment(sketch, "E4697", {"start": v(-62.69, 54.98) * mm, "end": v(-62.39, 54.82) * mm});
            skLineSegment(sketch, "E4698", {"start": v(-92.61, -83.5) * mm, "end": v(-92.93, -83.68) * mm});
            skLineSegment(sketch, "E4699", {"start": v(-62.39, 54.82) * mm, "end": v(-62.05, 54.66) * mm});
            skLineSegment(sketch, "E4700", {"start": v(-92.93, -83.68) * mm, "end": v(-93.3, -83.86) * mm});
            skLineSegment(sketch, "E4701", {"start": v(-62.05, 54.66) * mm, "end": v(-61.14, 54.32) * mm});
            skLineSegment(sketch, "E4702", {"start": v(-93.3, -83.86) * mm, "end": v(-93.72, -84.03) * mm});
            skLineSegment(sketch, "E4703", {"start": v(-61.14, 54.32) * mm, "end": v(-60.1, 54.05) * mm});
            skLineSegment(sketch, "E4704", {"start": v(-93.72, -84.03) * mm, "end": v(-94.66, -84.32) * mm});
            skArc(sketch, "E4705", {"start": v(-60.1, 54.05) * mm, "mid": v(-59.63, 54.58) * mm, "end": v(-59.18, 55.11) * mm});
            skLineSegment(sketch, "E4706", {"start": v(-94.66, -84.32) * mm, "end": v(-95.73, -84.55) * mm});
            skLineSegment(sketch, "E4707", {"start": v(-61.37, 58.4) * mm, "end": v(-61, 58.12) * mm});
            skArc(sketch, "E4708", {"start": v(-91, -83.11) * mm, "mid": v(-91.52, -82.88) * mm, "end": v(-92.06, -83.08) * mm});
            skLineSegment(sketch, "E4709", {"start": v(-61, 58.12) * mm, "end": v(-60.85, 57.98) * mm});
            skArc(sketch, "E4710", {"start": v(-91, -83.11) * mm, "mid": v(-90.75, -83.36) * mm, "end": v(-90.5, -83.6) * mm});
            skLineSegment(sketch, "E4711", {"start": v(-60.85, 57.98) * mm, "end": v(-60.67, 57.78) * mm});
            skArc(sketch, "E4712", {"start": v(-90.47, -84.66) * mm, "mid": v(-90.27, -84.13) * mm, "end": v(-90.5, -83.6) * mm});
            skLineSegment(sketch, "E4713", {"start": v(-60.67, 57.78) * mm, "end": v(-60.47, 57.54) * mm});
            skLineSegment(sketch, "E4714", {"start": v(-90.47, -84.66) * mm, "end": v(-90.74, -84.98) * mm});
            skLineSegment(sketch, "E4715", {"start": v(-60.47, 57.54) * mm, "end": v(-60.27, 57.27) * mm});
            skLineSegment(sketch, "E4716", {"start": v(-90.74, -84.98) * mm, "end": v(-90.9, -85.22) * mm});
            skLineSegment(sketch, "E4717", {"start": v(-60.27, 57.27) * mm, "end": v(-60.06, 56.95) * mm});
            skLineSegment(sketch, "E4718", {"start": v(-90.9, -85.22) * mm, "end": v(-91.08, -85.54) * mm});
            skLineSegment(sketch, "E4719", {"start": v(-60.06, 56.95) * mm, "end": v(-59.6, 56.1) * mm});
            skLineSegment(sketch, "E4720", {"start": v(-91.08, -85.54) * mm, "end": v(-91.25, -85.9) * mm});
            skLineSegment(sketch, "E4721", {"start": v(-59.6, 56.1) * mm, "end": v(-59.18, 55.11) * mm});
            skLineSegment(sketch, "E4722", {"start": v(-91.25, -85.9) * mm, "end": v(-91.42, -86.33) * mm});
            skArc(sketch, "E4723", {"start": v(-61.56, 59.46) * mm, "mid": v(-61.68, 58.89) * mm, "end": v(-61.37, 58.4) * mm});
            skLineSegment(sketch, "E4724", {"start": v(-91.42, -86.33) * mm, "end": v(-91.72, -87.27) * mm});
            skArc(sketch, "E4725", {"start": v(-61.56, 59.46) * mm, "mid": v(-61.37, 59.75) * mm, "end": v(-61.18, 60.05) * mm});
            skLineSegment(sketch, "E4726", {"start": v(-91.72, -87.27) * mm, "end": v(-91.94, -88.34) * mm});
            skArc(sketch, "E4727", {"start": v(-60.14, 60.32) * mm, "mid": v(-60.71, 60.4) * mm, "end": v(-61.18, 60.05) * mm});
            skArc(sketch, "E4728", {"start": v(-91.94, -88.34) * mm, "mid": v(-91.38, -88.78) * mm, "end": v(-90.8, -89.21) * mm});
            skLineSegment(sketch, "E4729", {"start": v(-60.14, 60.32) * mm, "end": v(-59.73, 60.1) * mm});
            skLineSegment(sketch, "E4730", {"start": v(-87.63, -86.84) * mm, "end": v(-87.86, -87.18) * mm});
            skLineSegment(sketch, "E4731", {"start": v(-59.73, 60.1) * mm, "end": v(-59.54, 60.01) * mm});
            skLineSegment(sketch, "E4732", {"start": v(-87.86, -87.18) * mm, "end": v(-88.06, -87.4) * mm});
            skLineSegment(sketch, "E4733", {"start": v(-59.54, 60.01) * mm, "end": v(-59.29, 59.93) * mm});
            skLineSegment(sketch, "E4734", {"start": v(-88.06, -87.4) * mm, "end": v(-88.32, -87.65) * mm});
            skLineSegment(sketch, "E4735", {"start": v(-59.29, 59.93) * mm, "end": v(-58.99, 59.85) * mm});
            skLineSegment(sketch, "E4736", {"start": v(-88.32, -87.65) * mm, "end": v(-88.63, -87.92) * mm});
            skLineSegment(sketch, "E4737", {"start": v(-58.99, 59.85) * mm, "end": v(-58.65, 59.78) * mm});
            skLineSegment(sketch, "E4738", {"start": v(-88.63, -87.92) * mm, "end": v(-89, -88.2) * mm});
            skLineSegment(sketch, "E4739", {"start": v(-58.65, 59.78) * mm, "end": v(-58.28, 59.72) * mm});
            skLineSegment(sketch, "E4740", {"start": v(-89, -88.2) * mm, "end": v(-89.83, -88.72) * mm});
            skLineSegment(sketch, "E4741", {"start": v(-58.28, 59.72) * mm, "end": v(-57.32, 59.65) * mm});
            skLineSegment(sketch, "E4742", {"start": v(-89.83, -88.72) * mm, "end": v(-90.8, -89.21) * mm});
            skLineSegment(sketch, "E4743", {"start": v(-57.32, 59.65) * mm, "end": v(-56.24, 59.69) * mm});
            skArc(sketch, "E4744", {"start": v(-86.6, -86.6) * mm, "mid": v(-87.16, -86.51) * mm, "end": v(-87.63, -86.84) * mm});
            skArc(sketch, "E4745", {"start": v(-56.24, 59.69) * mm, "mid": v(-55.94, 60.32) * mm, "end": v(-55.66, 60.97) * mm});
            skArc(sketch, "E4746", {"start": v(-86.6, -86.6) * mm, "mid": v(-86.3, -86.78) * mm, "end": v(-86, -86.95) * mm});
            skLineSegment(sketch, "E4747", {"start": v(-58.68, 63.5) * mm, "end": v(-58.25, 63.34) * mm});
            skArc(sketch, "E4748", {"start": v(-85.69, -87.96) * mm, "mid": v(-85.64, -87.4) * mm, "end": v(-86, -86.95) * mm});
            skLineSegment(sketch, "E4749", {"start": v(-58.25, 63.34) * mm, "end": v(-58.07, 63.25) * mm});
            skLineSegment(sketch, "E4750", {"start": v(-85.69, -87.96) * mm, "end": v(-85.87, -88.34) * mm});
            skLineSegment(sketch, "E4751", {"start": v(-58.07, 63.25) * mm, "end": v(-57.84, 63.11) * mm});
            skLineSegment(sketch, "E4752", {"start": v(-85.87, -88.34) * mm, "end": v(-85.96, -88.61) * mm});
            skLineSegment(sketch, "E4753", {"start": v(-57.84, 63.11) * mm, "end": v(-57.58, 62.93) * mm});
            skLineSegment(sketch, "E4754", {"start": v(-85.96, -88.61) * mm, "end": v(-86.05, -88.96) * mm});
            skLineSegment(sketch, "E4755", {"start": v(-57.58, 62.93) * mm, "end": v(-57.3, 62.72) * mm});
            skLineSegment(sketch, "E4756", {"start": v(-86.05, -88.96) * mm, "end": v(-86.12, -89.37) * mm});
            skLineSegment(sketch, "E4757", {"start": v(-57.3, 62.72) * mm, "end": v(-57.02, 62.48) * mm});
            skLineSegment(sketch, "E4758", {"start": v(-86.12, -89.37) * mm, "end": v(-86.18, -89.82) * mm});
            skLineSegment(sketch, "E4759", {"start": v(-57.02, 62.48) * mm, "end": v(-56.34, 61.8) * mm});
            skLineSegment(sketch, "E4760", {"start": v(-86.18, -89.82) * mm, "end": v(-86.22, -90.8) * mm});
            skLineSegment(sketch, "E4761", {"start": v(-56.34, 61.8) * mm, "end": v(-55.66, 60.97) * mm});
            skLineSegment(sketch, "E4762", {"start": v(-86.22, -90.8) * mm, "end": v(-86.16, -91.9) * mm});
            skArc(sketch, "E4763", {"start": v(-59.16, 64.46) * mm, "mid": v(-59.12, 63.88) * mm, "end": v(-58.68, 63.5) * mm});
            skArc(sketch, "E4764", {"start": v(-86.16, -91.9) * mm, "mid": v(-85.5, -92.18) * mm, "end": v(-84.84, -92.44) * mm});
            skArc(sketch, "E4765", {"start": v(-59.16, 64.46) * mm, "mid": v(-59.06, 64.8) * mm, "end": v(-58.97, 65.14) * mm});
            skLineSegment(sketch, "E4766", {"start": v(-82.38, -89.33) * mm, "end": v(-82.52, -89.72) * mm});
            skArc(sketch, "E4767", {"start": v(-58.04, 65.69) * mm, "mid": v(-58.61, 65.6) * mm, "end": v(-58.97, 65.14) * mm});
            skLineSegment(sketch, "E4768", {"start": v(-82.52, -89.72) * mm, "end": v(-82.65, -89.98) * mm});
            skLineSegment(sketch, "E4769", {"start": v(-58.04, 65.69) * mm, "end": v(-57.59, 65.59) * mm});
            skLineSegment(sketch, "E4770", {"start": v(-82.65, -89.98) * mm, "end": v(-82.84, -90.3) * mm});
            skLineSegment(sketch, "E4771", {"start": v(-57.59, 65.59) * mm, "end": v(-57.39, 65.57) * mm});
            skLineSegment(sketch, "E4772", {"start": v(-82.84, -90.3) * mm, "end": v(-83.07, -90.63) * mm});
            skLineSegment(sketch, "E4773", {"start": v(-57.39, 65.57) * mm, "end": v(-57.12, 65.56) * mm});
            skLineSegment(sketch, "E4774", {"start": v(-83.07, -90.63) * mm, "end": v(-83.35, -91) * mm});
            skLineSegment(sketch, "E4775", {"start": v(-57.12, 65.56) * mm, "end": v(-56.8, 65.56) * mm});
            skLineSegment(sketch, "E4776", {"start": v(-83.35, -91) * mm, "end": v(-84.02, -91.72) * mm});
            skLineSegment(sketch, "E4777", {"start": v(-56.8, 65.56) * mm, "end": v(-56.46, 65.6) * mm});
            skLineSegment(sketch, "E4778", {"start": v(-84.02, -91.72) * mm, "end": v(-84.84, -92.44) * mm});
            skLineSegment(sketch, "E4779", {"start": v(-56.46, 65.6) * mm, "end": v(-56.1, 65.64) * mm});
            skArc(sketch, "E4780", {"start": v(-81.45, -88.83) * mm, "mid": v(-82.02, -88.9) * mm, "end": v(-82.38, -89.33) * mm});
            skLineSegment(sketch, "E4781", {"start": v(-56.1, 65.64) * mm, "end": v(-55.15, 65.85) * mm});
            skArc(sketch, "E4782", {"start": v(-81.45, -88.83) * mm, "mid": v(-81.11, -88.93) * mm, "end": v(-80.78, -89.01) * mm});
            skLineSegment(sketch, "E4783", {"start": v(-55.15, 65.85) * mm, "end": v(-54.13, 66.18) * mm});
            skArc(sketch, "E4784", {"start": v(-80.22, -89.91) * mm, "mid": v(-80.32, -89.35) * mm, "end": v(-80.78, -89.01) * mm});
            skArc(sketch, "E4785", {"start": v(-54.13, 66.18) * mm, "mid": v(-54.02, 66.88) * mm, "end": v(-53.93, 67.58) * mm});
            skLineSegment(sketch, "E4786", {"start": v(-80.22, -89.91) * mm, "end": v(-80.3, -90.32) * mm});
            skLineSegment(sketch, "E4787", {"start": v(-57.54, 69.15) * mm, "end": v(-57.08, 69.12) * mm});
            skLineSegment(sketch, "E4788", {"start": v(-80.3, -90.32) * mm, "end": v(-80.31, -90.6) * mm});
            skLineSegment(sketch, "E4789", {"start": v(-57.08, 69.12) * mm, "end": v(-56.88, 69.08) * mm});
            skLineSegment(sketch, "E4790", {"start": v(-80.31, -90.6) * mm, "end": v(-80.3, -90.97) * mm});
            skLineSegment(sketch, "E4791", {"start": v(-56.88, 69.08) * mm, "end": v(-56.62, 69.02) * mm});
            skLineSegment(sketch, "E4792", {"start": v(-80.3, -90.97) * mm, "end": v(-80.27, -91.38) * mm});
            skLineSegment(sketch, "E4793", {"start": v(-56.62, 69.02) * mm, "end": v(-56.32, 68.92) * mm});
            skLineSegment(sketch, "E4794", {"start": v(-80.27, -91.38) * mm, "end": v(-80.2, -91.83) * mm});
            skLineSegment(sketch, "E4795", {"start": v(-56.32, 68.92) * mm, "end": v(-56, 68.8) * mm});
            skLineSegment(sketch, "E4796", {"start": v(-80.2, -91.83) * mm, "end": v(-80, -92.8) * mm});
            skLineSegment(sketch, "E4797", {"start": v(-56, 68.8) * mm, "end": v(-55.66, 68.65) * mm});
            skLineSegment(sketch, "E4798", {"start": v(-80, -92.8) * mm, "end": v(-79.65, -93.83) * mm});
            skLineSegment(sketch, "E4799", {"start": v(-55.66, 68.65) * mm, "end": v(-54.81, 68.18) * mm});
            skArc(sketch, "E4800", {"start": v(-79.65, -93.83) * mm, "mid": v(-78.94, -93.94) * mm, "end": v(-78.23, -94.02) * mm});
            skLineSegment(sketch, "E4801", {"start": v(-54.81, 68.18) * mm, "end": v(-53.93, 67.58) * mm});
            skLineSegment(sketch, "E4802", {"start": v(-76.67, -90.38) * mm, "end": v(-76.7, -90.8) * mm});
            skArc(sketch, "E4803", {"start": v(-58.27, 69.94) * mm, "mid": v(-58.07, 69.4) * mm, "end": v(-57.54, 69.15) * mm});
            skLineSegment(sketch, "E4804", {"start": v(-76.7, -90.8) * mm, "end": v(-76.76, -91.08) * mm});
            skArc(sketch, "E4805", {"start": v(-58.27, 69.94) * mm, "mid": v(-58.27, 70.3) * mm, "end": v(-58.27, 70.64) * mm});
            skLineSegment(sketch, "E4806", {"start": v(-76.76, -91.08) * mm, "end": v(-76.86, -91.43) * mm});
            skArc(sketch, "E4807", {"start": v(-57.54, 71.43) * mm, "mid": v(-58.07, 71.19) * mm, "end": v(-58.27, 70.64) * mm});
            skLineSegment(sketch, "E4808", {"start": v(-76.86, -91.43) * mm, "end": v(-77, -91.81) * mm});
            skLineSegment(sketch, "E4809", {"start": v(-57.54, 71.43) * mm, "end": v(-57.08, 71.46) * mm});
            skLineSegment(sketch, "E4810", {"start": v(-77, -91.81) * mm, "end": v(-77.18, -92.23) * mm});
            skLineSegment(sketch, "E4811", {"start": v(-57.08, 71.46) * mm, "end": v(-56.88, 71.5) * mm});
            skLineSegment(sketch, "E4812", {"start": v(-77.18, -92.23) * mm, "end": v(-77.63, -93.1) * mm});
            skLineSegment(sketch, "E4813", {"start": v(-56.88, 71.5) * mm, "end": v(-56.62, 71.57) * mm});
            skLineSegment(sketch, "E4814", {"start": v(-77.63, -93.1) * mm, "end": v(-78.23, -94.02) * mm});
            skLineSegment(sketch, "E4815", {"start": v(-56.62, 71.57) * mm, "end": v(-56.32, 71.66) * mm});
            skArc(sketch, "E4816", {"start": v(-75.9, -89.66) * mm, "mid": v(-76.43, -89.86) * mm, "end": v(-76.67, -90.38) * mm});
            skLineSegment(sketch, "E4817", {"start": v(-56.32, 71.66) * mm, "end": v(-56, 71.79) * mm});
            skArc(sketch, "E4818", {"start": v(-75.9, -89.66) * mm, "mid": v(-75.55, -89.66) * mm, "end": v(-75.2, -89.66) * mm});
            skLineSegment(sketch, "E4819", {"start": v(-56, 71.79) * mm, "end": v(-55.66, 71.94) * mm});
            skArc(sketch, "E4820", {"start": v(-74.43, -90.38) * mm, "mid": v(-74.67, -89.86) * mm, "end": v(-75.2, -89.66) * mm});
            skLineSegment(sketch, "E4821", {"start": v(-55.66, 71.94) * mm, "end": v(-54.81, 72.4) * mm});
            skLineSegment(sketch, "E4822", {"start": v(-74.43, -90.38) * mm, "end": v(-74.4, -90.8) * mm});
            skLineSegment(sketch, "E4823", {"start": v(-54.81, 72.4) * mm, "end": v(-53.93, 73) * mm});
            skLineSegment(sketch, "E4824", {"start": v(-74.4, -90.8) * mm, "end": v(-74.34, -91.08) * mm});
            skArc(sketch, "E4825", {"start": v(-53.93, 73) * mm, "mid": v(-54.02, 73.7) * mm, "end": v(-54.13, 74.4) * mm});
            skLineSegment(sketch, "E4826", {"start": v(-74.34, -91.08) * mm, "end": v(-74.24, -91.43) * mm});
            skLineSegment(sketch, "E4827", {"start": v(-58.04, 74.9) * mm, "end": v(-57.59, 75) * mm});
            skLineSegment(sketch, "E4828", {"start": v(-74.24, -91.43) * mm, "end": v(-74.1, -91.81) * mm});
            skLineSegment(sketch, "E4829", {"start": v(-57.59, 75) * mm, "end": v(-57.39, 75.02) * mm});
            skLineSegment(sketch, "E4830", {"start": v(-74.1, -91.81) * mm, "end": v(-73.92, -92.23) * mm});
            skLineSegment(sketch, "E4831", {"start": v(-57.39, 75.02) * mm, "end": v(-57.12, 75.03) * mm});
            skLineSegment(sketch, "E4832", {"start": v(-73.92, -92.23) * mm, "end": v(-73.46, -93.1) * mm});
            skLineSegment(sketch, "E4833", {"start": v(-57.12, 75.03) * mm, "end": v(-56.8, 75.02) * mm});
            skLineSegment(sketch, "E4834", {"start": v(-56.8, 75.02) * mm, "end": v(-56.46, 75) * mm});
            skLineSegment(sketch, "E4835", {"start": v(-56.46, 75) * mm, "end": v(-56.1, 74.94) * mm});
            skLineSegment(sketch, "E4836", {"start": v(-56.1, 74.94) * mm, "end": v(-55.15, 74.74) * mm});
            skLineSegment(sketch, "E4837", {"start": v(-55.15, 74.74) * mm, "end": v(-54.13, 74.4) * mm});
            skArc(sketch, "E4838", {"start": v(-58.97, 75.45) * mm, "mid": v(-58.61, 74.99) * mm, "end": v(-58.04, 74.9) * mm});
            skArc(sketch, "E4839", {"start": v(-58.97, 75.45) * mm, "mid": v(-59.06, 75.79) * mm, "end": v(-59.16, 76.12) * mm});
            skArc(sketch, "E4840", {"start": v(-58.68, 77.09) * mm, "mid": v(-59.12, 76.7) * mm, "end": v(-59.16, 76.12) * mm});
            skLineSegment(sketch, "E4841", {"start": v(-97.96, 65.59) * mm, "end": v(-98.16, 65.57) * mm});
            skLineSegment(sketch, "E4842", {"start": v(-98.16, 65.57) * mm, "end": v(-98.42, 65.56) * mm});
            skLineSegment(sketch, "E4843", {"start": v(-98.42, 65.56) * mm, "end": v(-98.74, 65.56) * mm});
            skLineSegment(sketch, "E4844", {"start": v(-98.74, 65.56) * mm, "end": v(-99.08, 65.6) * mm});
            skLineSegment(sketch, "E4845", {"start": v(-99.08, 65.6) * mm, "end": v(-99.45, 65.64) * mm});
            skLineSegment(sketch, "E4846", {"start": v(-99.45, 65.64) * mm, "end": v(-100.4, 65.85) * mm});
            skLineSegment(sketch, "E4847", {"start": v(-100.4, 65.85) * mm, "end": v(-101.42, 66.18) * mm});
            skArc(sketch, "E4848", {"start": v(-96.58, 65.14) * mm, "mid": v(-96.93, 65.6) * mm, "end": v(-97.5, 65.69) * mm});
            skArc(sketch, "E4849", {"start": v(-96.58, 65.14) * mm, "mid": v(-96.48, 64.8) * mm, "end": v(-96.38, 64.46) * mm});
            skArc(sketch, "E4850", {"start": v(-96.86, 63.5) * mm, "mid": v(-96.43, 63.88) * mm, "end": v(-96.38, 64.46) * mm});
            skLineSegment(sketch, "E4851", {"start": v(-96.86, 63.5) * mm, "end": v(-97.3, 63.34) * mm});
            skLineSegment(sketch, "E4852", {"start": v(-97.3, 63.34) * mm, "end": v(-97.48, 63.25) * mm});
            skLineSegment(sketch, "E4853", {"start": v(-97.48, 63.25) * mm, "end": v(-97.7, 63.11) * mm});
            skLineSegment(sketch, "E4854", {"start": v(-97.7, 63.11) * mm, "end": v(-97.97, 62.93) * mm});
            skLineSegment(sketch, "E4855", {"start": v(-97.97, 62.93) * mm, "end": v(-98.24, 62.72) * mm});
            skLineSegment(sketch, "E4856", {"start": v(-98.24, 62.72) * mm, "end": v(-98.52, 62.48) * mm});
            skLineSegment(sketch, "E4857", {"start": v(-98.52, 62.48) * mm, "end": v(-99.2, 61.8) * mm});
            skLineSegment(sketch, "E4858", {"start": v(-99.2, 61.8) * mm, "end": v(-99.89, 60.97) * mm});
            skArc(sketch, "E4859", {"start": v(-99.89, 60.97) * mm, "mid": v(-99.6, 60.32) * mm, "end": v(-99.3, 59.69) * mm});
            skLineSegment(sketch, "E4860", {"start": v(-95.4, 60.32) * mm, "end": v(-95.81, 60.1) * mm});
            skLineSegment(sketch, "E4861", {"start": v(-95.81, 60.1) * mm, "end": v(-96, 60.01) * mm});
            skLineSegment(sketch, "E4862", {"start": v(-96, 60.01) * mm, "end": v(-96.25, 59.93) * mm});
            skLineSegment(sketch, "E4863", {"start": v(-96.25, 59.93) * mm, "end": v(-96.56, 59.85) * mm});
            skLineSegment(sketch, "E4864", {"start": v(-96.56, 59.85) * mm, "end": v(-96.9, 59.78) * mm});
            skLineSegment(sketch, "E4865", {"start": v(-96.9, 59.78) * mm, "end": v(-97.26, 59.72) * mm});
            skLineSegment(sketch, "E4866", {"start": v(-97.26, 59.72) * mm, "end": v(-98.23, 59.65) * mm});
            skLineSegment(sketch, "E4867", {"start": v(-98.23, 59.65) * mm, "end": v(-99.3, 59.69) * mm});
            skArc(sketch, "E4868", {"start": v(-94.36, 60.05) * mm, "mid": v(-94.83, 60.4) * mm, "end": v(-95.4, 60.32) * mm});
            skArc(sketch, "E4869", {"start": v(-94.36, 60.05) * mm, "mid": v(-94.18, 59.75) * mm, "end": v(-93.98, 59.46) * mm});
            skArc(sketch, "E4870", {"start": v(-94.17, 58.4) * mm, "mid": v(-93.86, 58.89) * mm, "end": v(-93.98, 59.46) * mm});
            skLineSegment(sketch, "E4871", {"start": v(-94.17, 58.4) * mm, "end": v(-94.55, 58.12) * mm});
            skLineSegment(sketch, "E4872", {"start": v(-94.55, 58.12) * mm, "end": v(-94.7, 57.98) * mm});
            skLineSegment(sketch, "E4873", {"start": v(-94.7, 57.98) * mm, "end": v(-94.88, 57.78) * mm});
            skLineSegment(sketch, "E4874", {"start": v(-94.88, 57.78) * mm, "end": v(-95.07, 57.54) * mm});
            skLineSegment(sketch, "E4875", {"start": v(-95.07, 57.54) * mm, "end": v(-95.28, 57.27) * mm});
            skLineSegment(sketch, "E4876", {"start": v(-95.28, 57.27) * mm, "end": v(-95.48, 56.95) * mm});
            skLineSegment(sketch, "E4877", {"start": v(-95.48, 56.95) * mm, "end": v(-95.95, 56.1) * mm});
            skLineSegment(sketch, "E4878", {"start": v(-95.95, 56.1) * mm, "end": v(-96.36, 55.11) * mm});
            skArc(sketch, "E4879", {"start": v(-96.36, 55.11) * mm, "mid": v(-95.9, 54.58) * mm, "end": v(-95.44, 54.05) * mm});
            skLineSegment(sketch, "E4880", {"start": v(-91.88, 55.75) * mm, "end": v(-92.2, 55.42) * mm});
            skLineSegment(sketch, "E4881", {"start": v(-92.2, 55.42) * mm, "end": v(-92.36, 55.3) * mm});
            skLineSegment(sketch, "E4882", {"start": v(-92.36, 55.3) * mm, "end": v(-92.59, 55.14) * mm});
            skLineSegment(sketch, "E4883", {"start": v(-92.59, 55.14) * mm, "end": v(-92.85, 54.98) * mm});
            skLineSegment(sketch, "E4884", {"start": v(-92.85, 54.98) * mm, "end": v(-93.16, 54.82) * mm});
            skLineSegment(sketch, "E4885", {"start": v(-93.16, 54.82) * mm, "end": v(-93.5, 54.66) * mm});
            skLineSegment(sketch, "E4886", {"start": v(-93.5, 54.66) * mm, "end": v(-94.4, 54.32) * mm});
            skLineSegment(sketch, "E4887", {"start": v(-94.4, 54.32) * mm, "end": v(-95.44, 54.05) * mm});
            skArc(sketch, "E4888", {"start": v(-90.8, 55.79) * mm, "mid": v(-91.35, 55.99) * mm, "end": v(-91.88, 55.75) * mm});
            skArc(sketch, "E4889", {"start": v(-90.8, 55.79) * mm, "mid": v(-90.54, 55.56) * mm, "end": v(-90.27, 55.33) * mm});
            skArc(sketch, "E4890", {"start": v(-92.23, -12.43) * mm, "mid": v(-91.98, -11.91) * mm, "end": v(-92.16, -11.36) * mm});
            skLineSegment(sketch, "E4891", {"start": v(-92.23, -12.43) * mm, "end": v(-92.54, -12.72) * mm});
            skLineSegment(sketch, "E4892", {"start": v(-92.54, -12.72) * mm, "end": v(-92.67, -12.88) * mm});
            skLineSegment(sketch, "E4893", {"start": v(-92.67, -12.88) * mm, "end": v(-92.84, -13.1) * mm});
            skLineSegment(sketch, "E4894", {"start": v(-92.84, -13.1) * mm, "end": v(-93, -13.36) * mm});
            skLineSegment(sketch, "E4895", {"start": v(-93, -13.36) * mm, "end": v(-93.18, -13.66) * mm});
            skLineSegment(sketch, "E4896", {"start": v(-93.18, -13.66) * mm, "end": v(-93.36, -14) * mm});
            skLineSegment(sketch, "E4897", {"start": v(-93.36, -14) * mm, "end": v(-93.73, -14.9) * mm});
            skLineSegment(sketch, "E4898", {"start": v(-93.73, -14.9) * mm, "end": v(-94.05, -15.94) * mm});
            skArc(sketch, "E4899", {"start": v(-94.05, -15.94) * mm, "mid": v(-93.54, -16.43) * mm, "end": v(-93.02, -16.9) * mm});
            skLineSegment(sketch, "E4900", {"start": v(-89.64, -14.85) * mm, "end": v(-89.9, -15.18) * mm});
            skLineSegment(sketch, "E4901", {"start": v(-89.9, -15.18) * mm, "end": v(-90.06, -15.32) * mm});
            skLineSegment(sketch, "E4902", {"start": v(-90.06, -15.32) * mm, "end": v(-90.26, -15.5) * mm});
            skLineSegment(sketch, "E4903", {"start": v(-90.26, -15.5) * mm, "end": v(-90.52, -15.7) * mm});
            skLineSegment(sketch, "E4904", {"start": v(-90.52, -15.7) * mm, "end": v(-90.8, -15.89) * mm});
            skLineSegment(sketch, "E4905", {"start": v(-90.8, -15.89) * mm, "end": v(-91.13, -16.08) * mm});
            skLineSegment(sketch, "E4906", {"start": v(-91.13, -16.08) * mm, "end": v(-92, -16.52) * mm});
            skLineSegment(sketch, "E4907", {"start": v(-92, -16.52) * mm, "end": v(-93.02, -16.9) * mm});
            skArc(sketch, "E4908", {"start": v(-88.58, -14.7) * mm, "mid": v(-89.14, -14.56) * mm, "end": v(-89.64, -14.85) * mm});
            skArc(sketch, "E4909", {"start": v(-88.58, -14.7) * mm, "mid": v(-88.3, -14.9) * mm, "end": v(-88.01, -15.1) * mm});
            skArc(sketch, "E4910", {"start": v(-87.8, -16.15) * mm, "mid": v(-87.7, -15.58) * mm, "end": v(-88.01, -15.1) * mm});
            skLineSegment(sketch, "E4911", {"start": v(-87.8, -16.15) * mm, "end": v(-88.01, -16.51) * mm});
            skLineSegment(sketch, "E4912", {"start": v(-88.01, -16.51) * mm, "end": v(-88.1, -16.7) * mm});
            skLineSegment(sketch, "E4913", {"start": v(-88.1, -16.7) * mm, "end": v(-88.2, -16.96) * mm});
            skLineSegment(sketch, "E4914", {"start": v(-88.2, -16.96) * mm, "end": v(-88.3, -17.26) * mm});
            skLineSegment(sketch, "E4915", {"start": v(-88.3, -17.26) * mm, "end": v(-88.38, -17.6) * mm});
            skLineSegment(sketch, "E4916", {"start": v(-88.38, -17.6) * mm, "end": v(-88.46, -17.97) * mm});
            skLineSegment(sketch, "E4917", {"start": v(-88.46, -17.97) * mm, "end": v(-88.58, -18.94) * mm});
            skLineSegment(sketch, "E4918", {"start": v(-88.58, -18.94) * mm, "end": v(-88.6, -20.02) * mm});
            skArc(sketch, "E4919", {"start": v(-88.6, -20.02) * mm, "mid": v(-87.98, -20.35) * mm, "end": v(-87.34, -20.67) * mm});
            skLineSegment(sketch, "E4920", {"start": v(-84.65, -17.78) * mm, "end": v(-84.82, -18.17) * mm});
            skLineSegment(sketch, "E4921", {"start": v(-84.82, -18.17) * mm, "end": v(-84.92, -18.35) * mm});
            skLineSegment(sketch, "E4922", {"start": v(-84.92, -18.35) * mm, "end": v(-85.07, -18.58) * mm});
            skLineSegment(sketch, "E4923", {"start": v(-85.07, -18.58) * mm, "end": v(-85.27, -18.83) * mm});
            skLineSegment(sketch, "E4924", {"start": v(-85.27, -18.83) * mm, "end": v(-85.5, -19.1) * mm});
            skLineSegment(sketch, "E4925", {"start": v(-85.5, -19.1) * mm, "end": v(-85.75, -19.37) * mm});
            skLineSegment(sketch, "E4926", {"start": v(-85.75, -19.37) * mm, "end": v(-86.47, -20.03) * mm});
            skLineSegment(sketch, "E4927", {"start": v(-86.47, -20.03) * mm, "end": v(-87.34, -20.67) * mm});
            skArc(sketch, "E4928", {"start": v(-83.67, -17.35) * mm, "mid": v(-84.25, -17.37) * mm, "end": v(-84.65, -17.78) * mm});
            skArc(sketch, "E4929", {"start": v(-83.67, -17.35) * mm, "mid": v(-83.34, -17.47) * mm, "end": v(-83.01, -17.59) * mm});
            skArc(sketch, "E4930", {"start": v(-82.52, -18.54) * mm, "mid": v(-82.57, -17.96) * mm, "end": v(-83.01, -17.59) * mm});
            skLineSegment(sketch, "E4931", {"start": v(-82.52, -18.54) * mm, "end": v(-82.63, -18.95) * mm});
            skLineSegment(sketch, "E4932", {"start": v(-82.63, -18.95) * mm, "end": v(-82.67, -19.15) * mm});
            skLineSegment(sketch, "E4933", {"start": v(-82.67, -19.15) * mm, "end": v(-82.7, -19.42) * mm});
            skLineSegment(sketch, "E4934", {"start": v(-82.7, -19.42) * mm, "end": v(-82.7, -19.74) * mm});
            skLineSegment(sketch, "E4935", {"start": v(-82.7, -19.74) * mm, "end": v(-82.7, -20.09) * mm});
            skLineSegment(sketch, "E4936", {"start": v(-82.7, -20.09) * mm, "end": v(-82.67, -20.46) * mm});
            skLineSegment(sketch, "E4937", {"start": v(-82.67, -20.46) * mm, "end": v(-82.52, -21.43) * mm});
            skLineSegment(sketch, "E4938", {"start": v(-82.52, -21.43) * mm, "end": v(-82.26, -22.48) * mm});
            skArc(sketch, "E4939", {"start": v(-82.26, -22.48) * mm, "mid": v(-81.56, -22.63) * mm, "end": v(-80.87, -22.77) * mm});
            skLineSegment(sketch, "E4940", {"start": v(-79.05, -19.26) * mm, "end": v(-79.11, -19.68) * mm});
            skLineSegment(sketch, "E4941", {"start": v(-79.11, -19.68) * mm, "end": v(-79.16, -19.88) * mm});
            skLineSegment(sketch, "E4942", {"start": v(-79.16, -19.88) * mm, "end": v(-79.25, -20.14) * mm});
            skLineSegment(sketch, "E4943", {"start": v(-65.36, -17) * mm, "end": v(-65.18, -17.21) * mm});
            skLineSegment(sketch, "E4944", {"start": v(-65.18, -17.21) * mm, "end": v(-64.95, -17.44) * mm});
            skLineSegment(sketch, "E4945", {"start": v(-64.95, -17.44) * mm, "end": v(-64.7, -17.67) * mm});
            skLineSegment(sketch, "E4946", {"start": v(-64.7, -17.67) * mm, "end": v(-64.4, -17.9) * mm});
            skLineSegment(sketch, "E4947", {"start": v(-64.4, -17.9) * mm, "end": v(-63.6, -18.46) * mm});
            skLineSegment(sketch, "E4948", {"start": v(-63.6, -18.46) * mm, "end": v(-62.64, -18.98) * mm});
            skArc(sketch, "E4949", {"start": v(-62.64, -18.98) * mm, "mid": v(-62.06, -18.58) * mm, "end": v(-61.49, -18.16) * mm});
            skLineSegment(sketch, "E4950", {"start": v(-62.82, -14.44) * mm, "end": v(-62.55, -14.77) * mm});
            skLineSegment(sketch, "E4951", {"start": v(-62.55, -14.77) * mm, "end": v(-62.44, -14.95) * mm});
            skLineSegment(sketch, "E4952", {"start": v(-62.44, -14.95) * mm, "end": v(-62.3, -15.19) * mm});
            skLineSegment(sketch, "E4953", {"start": v(-62.3, -15.19) * mm, "end": v(-62.17, -15.47) * mm});
            skLineSegment(sketch, "E4954", {"start": v(-62.17, -15.47) * mm, "end": v(-62.04, -15.8) * mm});
            skLineSegment(sketch, "E4955", {"start": v(-62.04, -15.8) * mm, "end": v(-61.91, -16.15) * mm});
            skLineSegment(sketch, "E4956", {"start": v(-61.91, -16.15) * mm, "end": v(-61.66, -17.1) * mm});
            skLineSegment(sketch, "E4957", {"start": v(-61.66, -17.1) * mm, "end": v(-61.49, -18.16) * mm});
            skArc(sketch, "E4958", {"start": v(-62.74, -13.38) * mm, "mid": v(-63, -13.9) * mm, "end": v(-62.82, -14.44) * mm});
            skArc(sketch, "E4959", {"start": v(-62.74, -13.38) * mm, "mid": v(-62.48, -13.14) * mm, "end": v(-62.23, -12.9) * mm});
            skArc(sketch, "E4960", {"start": v(-61.16, -12.9) * mm, "mid": v(-61.7, -12.68) * mm, "end": v(-62.23, -12.9) * mm});
            skLineSegment(sketch, "E4961", {"start": v(-61.16, -12.9) * mm, "end": v(-60.85, -13.19) * mm});
            skLineSegment(sketch, "E4962", {"start": v(-60.85, -13.19) * mm, "end": v(-60.69, -13.31) * mm});
            skLineSegment(sketch, "E4963", {"start": v(-60.69, -13.31) * mm, "end": v(-60.46, -13.46) * mm});
            skLineSegment(sketch, "E4964", {"start": v(-60.46, -13.46) * mm, "end": v(-60.18, -13.61) * mm});
            skLineSegment(sketch, "E4965", {"start": v(-60.18, -13.61) * mm, "end": v(-59.87, -13.77) * mm});
            skLineSegment(sketch, "E4966", {"start": v(-59.87, -13.77) * mm, "end": v(-59.52, -13.92) * mm});
            skArc(sketch, "E4967", {"start": v(-59.15, -9.1) * mm, "mid": v(-58.96, -8.8) * mm, "end": v(-58.78, -8.5) * mm});
            skArc(sketch, "E4968", {"start": v(-57.75, -8.22) * mm, "mid": v(-58.33, -8.16) * mm, "end": v(-58.78, -8.5) * mm});
            skLineSegment(sketch, "E4969", {"start": v(-57.75, -8.22) * mm, "end": v(-57.38, -8.42) * mm});
            skLineSegment(sketch, "E4970", {"start": v(-57.38, -8.42) * mm, "end": v(-57.18, -8.49) * mm});
            skLineSegment(sketch, "E4971", {"start": v(-57.18, -8.49) * mm, "end": v(-56.92, -8.57) * mm});
            skLineSegment(sketch, "E4972", {"start": v(-56.92, -8.57) * mm, "end": v(-56.61, -8.64) * mm});
            skLineSegment(sketch, "E4973", {"start": v(-54.92, -8.81) * mm, "end": v(-53.84, -8.76) * mm});
            skLineSegment(sketch, "E4974", {"start": v(-55.9, -8.76) * mm, "end": v(-54.92, -8.81) * mm});
            skLineSegment(sketch, "E4975", {"start": v(-56.27, -8.7) * mm, "end": v(-55.9, -8.76) * mm});
            skLineSegment(sketch, "E4976", {"start": v(-56.61, -8.64) * mm, "end": v(-56.27, -8.7) * mm});
            skArc(sketch, "E4977", {"start": v(-59.15, -9.1) * mm, "mid": v(-59.25, -9.67) * mm, "end": v(-58.93, -10.15) * mm});
            skLineSegment(sketch, "E4978", {"start": v(-57.1, -12.4) * mm, "end": v(-56.64, -13.38) * mm});
            skLineSegment(sketch, "E4979", {"start": v(-57.6, -11.55) * mm, "end": v(-57.1, -12.4) * mm});
            skLineSegment(sketch, "E4980", {"start": v(-57.81, -11.24) * mm, "end": v(-57.6, -11.55) * mm});
            skLineSegment(sketch, "E4981", {"start": v(-58.03, -10.97) * mm, "end": v(-57.81, -11.24) * mm});
            skLineSegment(sketch, "E4982", {"start": v(-58.24, -10.73) * mm, "end": v(-58.03, -10.97) * mm});
            skLineSegment(sketch, "E4983", {"start": v(-58.43, -10.53) * mm, "end": v(-58.24, -10.73) * mm});
            skLineSegment(sketch, "E4984", {"start": v(-58.58, -10.4) * mm, "end": v(-58.43, -10.53) * mm});
            skLineSegment(sketch, "E4985", {"start": v(-58.93, -10.15) * mm, "end": v(-58.58, -10.4) * mm});
            skArc(sketch, "E4986", {"start": v(-57.54, -14.48) * mm, "mid": v(-57.08, -13.93) * mm, "end": v(-56.64, -13.38) * mm});
            skLineSegment(sketch, "E4987", {"start": v(-58.6, -14.23) * mm, "end": v(-57.54, -14.48) * mm});
            skLineSegment(sketch, "E4988", {"start": v(-59.52, -13.92) * mm, "end": v(-58.6, -14.23) * mm});
            skLineSegment(sketch, "E4989", {"start": v(-65.49, -16.85) * mm, "end": v(-65.36, -17) * mm});
            skLineSegment(sketch, "E4990", {"start": v(-65.7, -16.48) * mm, "end": v(-65.49, -16.85) * mm});
            skArc(sketch, "E4991", {"start": v(-65.7, -16.48) * mm, "mid": v(-66.16, -16.13) * mm, "end": v(-66.74, -16.2) * mm});
            skArc(sketch, "E4992", {"start": v(-67.36, -16.52) * mm, "mid": v(-67.05, -16.36) * mm, "end": v(-66.74, -16.2) * mm});
            skArc(sketch, "E4993", {"start": v(-67.36, -16.52) * mm, "mid": v(-67.74, -16.95) * mm, "end": v(-67.72, -17.53) * mm});
            skLineSegment(sketch, "E4994", {"start": v(-67.32, -20.4) * mm, "end": v(-67.44, -21.47) * mm});
            skLineSegment(sketch, "E4995", {"start": v(-67.3, -19.41) * mm, "end": v(-67.32, -20.4) * mm});
            skLineSegment(sketch, "E4996", {"start": v(-67.33, -19.04) * mm, "end": v(-67.3, -19.41) * mm});
            skLineSegment(sketch, "E4997", {"start": v(-67.37, -18.7) * mm, "end": v(-67.33, -19.04) * mm});
            skLineSegment(sketch, "E4998", {"start": v(-67.42, -18.38) * mm, "end": v(-67.37, -18.7) * mm});
            skLineSegment(sketch, "E4999", {"start": v(-67.49, -18.11) * mm, "end": v(-67.42, -18.38) * mm});
            skLineSegment(sketch, "E5000", {"start": v(-67.55, -17.91) * mm, "end": v(-67.49, -18.11) * mm});
            skLineSegment(sketch, "E5001", {"start": v(-67.72, -17.53) * mm, "end": v(-67.55, -17.91) * mm});
            skArc(sketch, "E5002", {"start": v(-68.78, -21.94) * mm, "mid": v(-68.1, -21.71) * mm, "end": v(-67.44, -21.47) * mm});
            skLineSegment(sketch, "E5003", {"start": v(-69.55, -21.18) * mm, "end": v(-68.78, -21.94) * mm});
            skLineSegment(sketch, "E5004", {"start": v(-70.18, -20.43) * mm, "end": v(-69.55, -21.18) * mm});
            skLineSegment(sketch, "E5005", {"start": v(-70.4, -20.13) * mm, "end": v(-70.18, -20.43) * mm});
            skLineSegment(sketch, "E5006", {"start": v(-70.58, -19.83) * mm, "end": v(-70.4, -20.13) * mm});
            skLineSegment(sketch, "E5007", {"start": v(-70.74, -19.56) * mm, "end": v(-70.58, -19.83) * mm});
            skLineSegment(sketch, "E5008", {"start": v(-70.86, -19.3) * mm, "end": v(-70.74, -19.56) * mm});
            skLineSegment(sketch, "E5009", {"start": v(-70.94, -19.12) * mm, "end": v(-70.86, -19.3) * mm});
            skLineSegment(sketch, "E5010", {"start": v(-71.05, -18.7) * mm, "end": v(-70.94, -19.12) * mm});
            skArc(sketch, "E5011", {"start": v(-71.05, -18.7) * mm, "mid": v(-71.4, -18.25) * mm, "end": v(-71.96, -18.15) * mm});
            skArc(sketch, "E5012", {"start": v(-72.65, -18.3) * mm, "mid": v(-72.3, -18.23) * mm, "end": v(-71.96, -18.15) * mm});
            skArc(sketch, "E5013", {"start": v(-72.65, -18.3) * mm, "mid": v(-73.13, -18.6) * mm, "end": v(-73.27, -19.17) * mm});
            skLineSegment(sketch, "E5014", {"start": v(-73.66, -22.04) * mm, "end": v(-74.06, -23.04) * mm});
            skLineSegment(sketch, "E5015", {"start": v(-73.38, -21.1) * mm, "end": v(-73.66, -22.04) * mm});
            skLineSegment(sketch, "E5016", {"start": v(-73.3, -20.73) * mm, "end": v(-73.38, -21.1) * mm});
            skLineSegment(sketch, "E5017", {"start": v(-73.25, -20.39) * mm, "end": v(-73.3, -20.73) * mm});
            skLineSegment(sketch, "E5018", {"start": v(-73.21, -20.07) * mm, "end": v(-73.25, -20.39) * mm});
            skLineSegment(sketch, "E5019", {"start": v(-73.2, -19.8) * mm, "end": v(-73.21, -20.07) * mm});
            skLineSegment(sketch, "E5020", {"start": v(-73.2, -19.6) * mm, "end": v(-73.2, -19.8) * mm});
            skLineSegment(sketch, "E5021", {"start": v(-73.27, -19.17) * mm, "end": v(-73.2, -19.6) * mm});
            skArc(sketch, "E5022", {"start": v(-75.48, -23.14) * mm, "mid": v(-74.77, -23.1) * mm, "end": v(-74.06, -23.04) * mm});
            skLineSegment(sketch, "E5023", {"start": v(-76.02, -22.2) * mm, "end": v(-75.48, -23.14) * mm});
            skLineSegment(sketch, "E5024", {"start": v(-76.42, -21.3) * mm, "end": v(-76.02, -22.2) * mm});
            skLineSegment(sketch, "E5025", {"start": v(-76.55, -20.95) * mm, "end": v(-76.42, -21.3) * mm});
            skLineSegment(sketch, "E5026", {"start": v(-76.65, -20.62) * mm, "end": v(-76.55, -20.95) * mm});
            skLineSegment(sketch, "E5027", {"start": v(-76.72, -20.31) * mm, "end": v(-76.65, -20.62) * mm});
            skLineSegment(sketch, "E5028", {"start": v(-76.77, -20.04) * mm, "end": v(-76.72, -20.31) * mm});
            skLineSegment(sketch, "E5029", {"start": v(-76.8, -19.84) * mm, "end": v(-76.77, -20.04) * mm});
            skLineSegment(sketch, "E5030", {"start": v(-76.8, -19.41) * mm, "end": v(-76.8, -19.84) * mm});
            skArc(sketch, "E5031", {"start": v(-76.8, -19.41) * mm, "mid": v(-77, -18.87) * mm, "end": v(-77.53, -18.63) * mm});
            skArc(sketch, "E5032", {"start": v(-78.22, -18.58) * mm, "mid": v(-77.88, -18.6) * mm, "end": v(-77.53, -18.63) * mm});
            skArc(sketch, "E5033", {"start": v(-78.22, -18.58) * mm, "mid": v(-78.78, -18.75) * mm, "end": v(-79.05, -19.26) * mm});
            skLineSegment(sketch, "E5034", {"start": v(-80.2, -21.91) * mm, "end": v(-80.87, -22.77) * mm});
            skLineSegment(sketch, "E5035", {"start": v(-79.68, -21.08) * mm, "end": v(-80.2, -21.91) * mm});
            skLineSegment(sketch, "E5036", {"start": v(-79.5, -20.75) * mm, "end": v(-79.68, -21.08) * mm});
            skLineSegment(sketch, "E5037", {"start": v(-79.36, -20.43) * mm, "end": v(-79.5, -20.75) * mm});
            skLineSegment(sketch, "E5038", {"start": v(-79.25, -20.14) * mm, "end": v(-79.36, -20.43) * mm});
            skLineSegment(sketch, "E5039", {"start": v(-97.5, 65.69) * mm, "end": v(-97.96, 65.59) * mm});
            skArc(sketch, "E5040", {"start": v(-101.62, 67.58) * mm, "mid": v(-101.53, 66.88) * mm, "end": v(-101.42, 66.18) * mm});
            skLineSegment(sketch, "E5041", {"start": v(-100.73, 68.18) * mm, "end": v(-101.62, 67.58) * mm});
            skLineSegment(sketch, "E5042", {"start": v(-99.88, 68.65) * mm, "end": v(-100.73, 68.18) * mm});
            skLineSegment(sketch, "E5043", {"start": v(-99.54, 68.8) * mm, "end": v(-99.88, 68.65) * mm});
            skLineSegment(sketch, "E5044", {"start": v(-99.22, 68.92) * mm, "end": v(-99.54, 68.8) * mm});
            skLineSegment(sketch, "E5045", {"start": v(-98.92, 69.02) * mm, "end": v(-99.22, 68.92) * mm});
            skLineSegment(sketch, "E5046", {"start": v(-98.66, 69.08) * mm, "end": v(-98.92, 69.02) * mm});
            skLineSegment(sketch, "E5047", {"start": v(-98.47, 69.12) * mm, "end": v(-98.66, 69.08) * mm});
            skLineSegment(sketch, "E5048", {"start": v(-98, 69.15) * mm, "end": v(-98.47, 69.12) * mm});
            skArc(sketch, "E5049", {"start": v(-98, 69.15) * mm, "mid": v(-97.48, 69.4) * mm, "end": v(-97.27, 69.94) * mm});
            skArc(sketch, "E5050", {"start": v(-97.27, 70.64) * mm, "mid": v(-97.27, 70.3) * mm, "end": v(-97.27, 69.94) * mm});
            skArc(sketch, "E5051", {"start": v(-97.27, 70.64) * mm, "mid": v(-97.48, 71.19) * mm, "end": v(-98, 71.43) * mm});
            skLineSegment(sketch, "E5052", {"start": v(-100.73, 72.4) * mm, "end": v(-101.62, 73) * mm});
            skLineSegment(sketch, "E5053", {"start": v(-99.88, 71.94) * mm, "end": v(-100.73, 72.4) * mm});
            skLineSegment(sketch, "E5054", {"start": v(-99.54, 71.79) * mm, "end": v(-99.88, 71.94) * mm});
            skLineSegment(sketch, "E5055", {"start": v(-99.22, 71.66) * mm, "end": v(-99.54, 71.79) * mm});
            skLineSegment(sketch, "E5056", {"start": v(-98.92, 71.57) * mm, "end": v(-99.22, 71.66) * mm});
            skLineSegment(sketch, "E5057", {"start": v(-98.66, 71.5) * mm, "end": v(-98.92, 71.57) * mm});
            skLineSegment(sketch, "E5058", {"start": v(-98.47, 71.46) * mm, "end": v(-98.66, 71.5) * mm});
            skLineSegment(sketch, "E5059", {"start": v(-98, 71.43) * mm, "end": v(-98.47, 71.46) * mm});
            skArc(sketch, "E5060", {"start": v(-101.42, 74.4) * mm, "mid": v(-101.53, 73.7) * mm, "end": v(-101.62, 73) * mm});
            skLineSegment(sketch, "E5061", {"start": v(-100.4, 74.74) * mm, "end": v(-101.42, 74.4) * mm});
            skLineSegment(sketch, "E5062", {"start": v(-99.45, 74.94) * mm, "end": v(-100.4, 74.74) * mm});
            skLineSegment(sketch, "E5063", {"start": v(-99.08, 75) * mm, "end": v(-99.45, 74.94) * mm});
            skLineSegment(sketch, "E5064", {"start": v(-98.74, 75.02) * mm, "end": v(-99.08, 75) * mm});
            skLineSegment(sketch, "E5065", {"start": v(-98.42, 75.03) * mm, "end": v(-98.74, 75.02) * mm});
            skLineSegment(sketch, "E5066", {"start": v(-98.16, 75.02) * mm, "end": v(-98.42, 75.03) * mm});
            skLineSegment(sketch, "E5067", {"start": v(-97.96, 75) * mm, "end": v(-98.16, 75.02) * mm});
            skLineSegment(sketch, "E5068", {"start": v(-97.5, 74.9) * mm, "end": v(-97.96, 75) * mm});
            skArc(sketch, "E5069", {"start": v(-97.5, 74.9) * mm, "mid": v(-96.93, 74.99) * mm, "end": v(-96.58, 75.45) * mm});
            skArc(sketch, "E5070", {"start": v(-96.38, 76.12) * mm, "mid": v(-96.48, 75.79) * mm, "end": v(-96.58, 75.45) * mm});
            skArc(sketch, "E5071", {"start": v(-96.38, 76.12) * mm, "mid": v(-96.43, 76.7) * mm, "end": v(-96.86, 77.09) * mm});
            skLineSegment(sketch, "E5072", {"start": v(-99.2, 78.79) * mm, "end": v(-99.89, 79.62) * mm});
            skLineSegment(sketch, "E5073", {"start": v(-98.52, 78.1) * mm, "end": v(-99.2, 78.79) * mm});
            skLineSegment(sketch, "E5074", {"start": v(-98.24, 77.86) * mm, "end": v(-98.52, 78.1) * mm});
            skLineSegment(sketch, "E5075", {"start": v(-97.97, 77.65) * mm, "end": v(-98.24, 77.86) * mm});
            skLineSegment(sketch, "E5076", {"start": v(-97.7, 77.47) * mm, "end": v(-97.97, 77.65) * mm});
            skLineSegment(sketch, "E5077", {"start": v(-97.48, 77.34) * mm, "end": v(-97.7, 77.47) * mm});
            skLineSegment(sketch, "E5078", {"start": v(-97.3, 77.25) * mm, "end": v(-97.48, 77.34) * mm});
            skLineSegment(sketch, "E5079", {"start": v(-96.86, 77.09) * mm, "end": v(-97.3, 77.25) * mm});
            skArc(sketch, "E5080", {"start": v(-99.3, 80.9) * mm, "mid": v(-99.6, 80.26) * mm, "end": v(-99.89, 79.62) * mm});
            skLineSegment(sketch, "E5081", {"start": v(-98.23, 80.93) * mm, "end": v(-99.3, 80.9) * mm});
            skLineSegment(sketch, "E5082", {"start": v(-97.26, 80.86) * mm, "end": v(-98.23, 80.93) * mm});
            skLineSegment(sketch, "E5083", {"start": v(-96.9, 80.8) * mm, "end": v(-97.26, 80.86) * mm});
            skLineSegment(sketch, "E5084", {"start": v(-96.56, 80.74) * mm, "end": v(-96.9, 80.8) * mm});
            skLineSegment(sketch, "E5085", {"start": v(-96.25, 80.66) * mm, "end": v(-96.56, 80.74) * mm});
            skLineSegment(sketch, "E5086", {"start": v(-96, 80.57) * mm, "end": v(-96.25, 80.66) * mm});
            skLineSegment(sketch, "E5087", {"start": v(-95.81, 80.5) * mm, "end": v(-96, 80.57) * mm});
            skLineSegment(sketch, "E5088", {"start": v(-95.4, 80.27) * mm, "end": v(-95.81, 80.5) * mm});
            skArc(sketch, "E5089", {"start": v(-95.4, 80.27) * mm, "mid": v(-94.83, 80.2) * mm, "end": v(-94.36, 80.54) * mm});
            skArc(sketch, "E5090", {"start": v(-93.98, 81.13) * mm, "mid": v(-94.18, 80.83) * mm, "end": v(-94.36, 80.54) * mm});
            skArc(sketch, "E5091", {"start": v(-93.98, 81.13) * mm, "mid": v(-93.86, 81.7) * mm, "end": v(-94.17, 82.2) * mm});
            skLineSegment(sketch, "E5092", {"start": v(-95.95, 84.48) * mm, "end": v(-96.36, 85.47) * mm});
            skLineSegment(sketch, "E5093", {"start": v(-95.48, 83.63) * mm, "end": v(-95.95, 84.48) * mm});
            skLineSegment(sketch, "E5094", {"start": v(-95.28, 83.32) * mm, "end": v(-95.48, 83.63) * mm});
            skLineSegment(sketch, "E5095", {"start": v(-95.07, 83.04) * mm, "end": v(-95.28, 83.32) * mm});
            skLineSegment(sketch, "E5096", {"start": v(-94.88, 82.8) * mm, "end": v(-95.07, 83.04) * mm});
            skLineSegment(sketch, "E5097", {"start": v(-94.7, 82.6) * mm, "end": v(-94.88, 82.8) * mm});
            skLineSegment(sketch, "E5098", {"start": v(-94.55, 82.47) * mm, "end": v(-94.7, 82.6) * mm});
            skLineSegment(sketch, "E5099", {"start": v(-94.17, 82.2) * mm, "end": v(-94.55, 82.47) * mm});
            skArc(sketch, "E5100", {"start": v(-95.44, 86.53) * mm, "mid": v(-95.9, 86) * mm, "end": v(-96.36, 85.47) * mm});
            skLineSegment(sketch, "E5101", {"start": v(-94.4, 86.26) * mm, "end": v(-95.44, 86.53) * mm});
            skLineSegment(sketch, "E5102", {"start": v(-93.5, 85.92) * mm, "end": v(-94.4, 86.26) * mm});
            skLineSegment(sketch, "E5103", {"start": v(-93.16, 85.77) * mm, "end": v(-93.5, 85.92) * mm});
            skLineSegment(sketch, "E5104", {"start": v(-92.85, 85.6) * mm, "end": v(-93.16, 85.77) * mm});
            skLineSegment(sketch, "E5105", {"start": v(-92.59, 85.44) * mm, "end": v(-92.85, 85.6) * mm});
            skLineSegment(sketch, "E5106", {"start": v(-92.36, 85.29) * mm, "end": v(-92.59, 85.44) * mm});
            skLineSegment(sketch, "E5107", {"start": v(-92.2, 85.16) * mm, "end": v(-92.36, 85.29) * mm});
            skLineSegment(sketch, "E5108", {"start": v(-91.88, 84.83) * mm, "end": v(-92.2, 85.16) * mm});
            skArc(sketch, "E5109", {"start": v(-91.88, 84.83) * mm, "mid": v(-91.35, 84.6) * mm, "end": v(-90.8, 84.8) * mm});
            skArc(sketch, "E5110", {"start": v(-90.27, 85.26) * mm, "mid": v(-90.54, 85.03) * mm, "end": v(-90.8, 84.8) * mm});
            skArc(sketch, "E5111", {"start": v(-90.27, 85.26) * mm, "mid": v(-90, 85.77) * mm, "end": v(-90.16, 86.33) * mm});
            skLineSegment(sketch, "E5112", {"start": v(-91.21, 89.03) * mm, "end": v(-91.33, 90.1) * mm});
            skLineSegment(sketch, "E5113", {"start": v(-91, 88.08) * mm, "end": v(-91.21, 89.03) * mm});
            skLineSegment(sketch, "E5114", {"start": v(-90.9, 87.72) * mm, "end": v(-91, 88.08) * mm});
            skLineSegment(sketch, "E5115", {"start": v(-90.78, 87.4) * mm, "end": v(-90.9, 87.72) * mm});
            skLineSegment(sketch, "E5116", {"start": v(-90.66, 87.11) * mm, "end": v(-90.78, 87.4) * mm});
            skLineSegment(sketch, "E5117", {"start": v(-90.54, 86.87) * mm, "end": v(-90.66, 87.11) * mm});
            skLineSegment(sketch, "E5118", {"start": v(-90.44, 86.7) * mm, "end": v(-90.54, 86.87) * mm});
            skLineSegment(sketch, "E5119", {"start": v(-90.16, 86.33) * mm, "end": v(-90.44, 86.7) * mm});
            skArc(sketch, "E5120", {"start": v(-90.15, 90.85) * mm, "mid": v(-90.75, 90.48) * mm, "end": v(-91.33, 90.1) * mm});
            skLineSegment(sketch, "E5121", {"start": v(-89.23, 90.3) * mm, "end": v(-90.15, 90.85) * mm});
            skLineSegment(sketch, "E5122", {"start": v(-88.45, 89.72) * mm, "end": v(-89.23, 90.3) * mm});
            skLineSegment(sketch, "E5123", {"start": v(-88.17, 89.47) * mm, "end": v(-88.45, 89.72) * mm});
            skLineSegment(sketch, "E5124", {"start": v(-87.93, 89.23) * mm, "end": v(-88.17, 89.47) * mm});
            skLineSegment(sketch, "E5125", {"start": v(-87.72, 89) * mm, "end": v(-87.93, 89.23) * mm});
            skLineSegment(sketch, "E5126", {"start": v(-87.55, 88.8) * mm, "end": v(-87.72, 89) * mm});
            skLineSegment(sketch, "E5127", {"start": v(-87.43, 88.63) * mm, "end": v(-87.55, 88.8) * mm});
            skLineSegment(sketch, "E5128", {"start": v(-87.21, 88.22) * mm, "end": v(-87.43, 88.63) * mm});
            skArc(sketch, "E5129", {"start": v(-87.21, 88.22) * mm, "mid": v(-86.77, 87.84) * mm, "end": v(-86.2, 87.88) * mm});
            skArc(sketch, "E5130", {"start": v(-85.55, 88.17) * mm, "mid": v(-85.87, 88.03) * mm, "end": v(-86.2, 87.88) * mm});
            skArc(sketch, "E5131", {"start": v(-85.55, 88.17) * mm, "mid": v(-85.14, 88.59) * mm, "end": v(-85.14, 89.17) * mm});
            skLineSegment(sketch, "E5132", {"start": v(-85.4, 92.05) * mm, "end": v(-85.2, 93.11) * mm});
            skLineSegment(sketch, "E5133", {"start": v(-85.46, 91.09) * mm, "end": v(-85.4, 92.05) * mm});
            skLineSegment(sketch, "E5134", {"start": v(-85.46, 90.72) * mm, "end": v(-85.46, 91.09) * mm});
            skLineSegment(sketch, "E5135", {"start": v(-85.44, 90.37) * mm, "end": v(-85.46, 90.72) * mm});
            skLineSegment(sketch, "E5136", {"start": v(-85.4, 90.06) * mm, "end": v(-85.44, 90.37) * mm});
            skLineSegment(sketch, "E5137", {"start": v(-85.35, 89.8) * mm, "end": v(-85.4, 90.06) * mm});
            skLineSegment(sketch, "E5138", {"start": v(-85.3, 89.6) * mm, "end": v(-85.35, 89.8) * mm});
            skLineSegment(sketch, "E5139", {"start": v(-85.14, 89.17) * mm, "end": v(-85.3, 89.6) * mm});
            skArc(sketch, "E5140", {"start": v(-83.85, 93.5) * mm, "mid": v(-84.53, 93.32) * mm, "end": v(-85.2, 93.11) * mm});
            skLineSegment(sketch, "E5141", {"start": v(-83.13, 92.72) * mm, "end": v(-83.85, 93.5) * mm});
            skLineSegment(sketch, "E5142", {"start": v(-82.55, 91.94) * mm, "end": v(-83.13, 92.72) * mm});
            skLineSegment(sketch, "E5143", {"start": v(-82.35, 91.63) * mm, "end": v(-82.55, 91.94) * mm});
            skLineSegment(sketch, "E5144", {"start": v(-82.18, 91.33) * mm, "end": v(-82.35, 91.63) * mm});
            skLineSegment(sketch, "E5145", {"start": v(-82.04, 91.05) * mm, "end": v(-82.18, 91.33) * mm});
            skLineSegment(sketch, "E5146", {"start": v(-81.94, 90.8) * mm, "end": v(-82.04, 91.05) * mm});
            skLineSegment(sketch, "E5147", {"start": v(-81.88, 90.6) * mm, "end": v(-81.94, 90.8) * mm});
            skLineSegment(sketch, "E5148", {"start": v(-81.78, 90.15) * mm, "end": v(-81.88, 90.6) * mm});
            skArc(sketch, "E5149", {"start": v(-81.78, 90.15) * mm, "mid": v(-81.46, 89.67) * mm, "end": v(-80.9, 89.54) * mm});
            skArc(sketch, "E5150", {"start": v(-80.2, 89.64) * mm, "mid": v(-80.55, 89.6) * mm, "end": v(-80.9, 89.54) * mm});
            skArc(sketch, "E5151", {"start": v(-80.2, 89.64) * mm, "mid": v(-79.7, 89.92) * mm, "end": v(-79.52, 90.48) * mm});
            skLineSegment(sketch, "E5152", {"start": v(-78.95, 93.32) * mm, "end": v(-78.48, 94.28) * mm});
            skLineSegment(sketch, "E5153", {"start": v(-79.29, 92.41) * mm, "end": v(-78.95, 93.32) * mm});
            skLineSegment(sketch, "E5154", {"start": v(-79.4, 92.05) * mm, "end": v(-79.29, 92.41) * mm});
            skLineSegment(sketch, "E5155", {"start": v(-79.47, 91.72) * mm, "end": v(-79.4, 92.05) * mm});
            skLineSegment(sketch, "E5156", {"start": v(-79.52, 91.4) * mm, "end": v(-79.47, 91.72) * mm});
            skLineSegment(sketch, "E5157", {"start": v(-79.55, 91.14) * mm, "end": v(-79.52, 91.4) * mm});
            skLineSegment(sketch, "E5158", {"start": v(-79.56, 90.94) * mm, "end": v(-79.55, 91.14) * mm});
            skLineSegment(sketch, "E5159", {"start": v(-79.52, 90.48) * mm, "end": v(-79.56, 90.94) * mm});
            skArc(sketch, "E5160", {"start": v(-77.07, 94.28) * mm, "mid": v(-77.77, 94.3) * mm, "end": v(-78.48, 94.28) * mm});
            skLineSegment(sketch, "E5161", {"start": v(-76.6, 93.32) * mm, "end": v(-77.07, 94.28) * mm});
            skLineSegment(sketch, "E5162", {"start": v(-76.25, 92.41) * mm, "end": v(-76.6, 93.32) * mm});
            skLineSegment(sketch, "E5163", {"start": v(-76.15, 92.05) * mm, "end": v(-76.25, 92.41) * mm});
            skLineSegment(sketch, "E5164", {"start": v(-76.08, 91.72) * mm, "end": v(-76.15, 92.05) * mm});
            skLineSegment(sketch, "E5165", {"start": v(-76.02, 91.4) * mm, "end": v(-76.08, 91.72) * mm});
            skLineSegment(sketch, "E5166", {"start": v(-76, 91.14) * mm, "end": v(-76.02, 91.4) * mm});
            skLineSegment(sketch, "E5167", {"start": v(-75.99, 90.94) * mm, "end": v(-76, 91.14) * mm});
            skLineSegment(sketch, "E5168", {"start": v(-76.02, 90.48) * mm, "end": v(-75.99, 90.94) * mm});
            skArc(sketch, "E5169", {"start": v(-76.02, 90.48) * mm, "mid": v(-75.85, 89.92) * mm, "end": v(-75.34, 89.64) * mm});
            skArc(sketch, "E5170", {"start": v(-74.65, 89.54) * mm, "mid": v(-75, 89.6) * mm, "end": v(-75.34, 89.64) * mm});
            skArc(sketch, "E5171", {"start": v(-74.65, 89.54) * mm, "mid": v(-74.08, 89.67) * mm, "end": v(-73.76, 90.15) * mm});
            skLineSegment(sketch, "E5172", {"start": v(-72.42, 92.72) * mm, "end": v(-71.69, 93.5) * mm});
            skLineSegment(sketch, "E5173", {"start": v(-73, 91.94) * mm, "end": v(-72.42, 92.72) * mm});
            skLineSegment(sketch, "E5174", {"start": v(-73.2, 91.63) * mm, "end": v(-73, 91.94) * mm});
            skLineSegment(sketch, "E5175", {"start": v(-73.36, 91.33) * mm, "end": v(-73.2, 91.63) * mm});
            skLineSegment(sketch, "E5176", {"start": v(-73.5, 91.05) * mm, "end": v(-73.36, 91.33) * mm});
            skLineSegment(sketch, "E5177", {"start": v(-73.6, 90.8) * mm, "end": v(-73.5, 91.05) * mm});
            skLineSegment(sketch, "E5178", {"start": v(-73.67, 90.6) * mm, "end": v(-73.6, 90.8) * mm});
            skLineSegment(sketch, "E5179", {"start": v(-73.76, 90.15) * mm, "end": v(-73.67, 90.6) * mm});
            skArc(sketch, "E5180", {"start": v(-70.34, 93.11) * mm, "mid": v(-71, 93.32) * mm, "end": v(-71.69, 93.5) * mm});
            skLineSegment(sketch, "E5181", {"start": v(-70.15, 92.05) * mm, "end": v(-70.34, 93.11) * mm});
            skLineSegment(sketch, "E5182", {"start": v(-70.08, 91.09) * mm, "end": v(-70.15, 92.05) * mm});
            skLineSegment(sketch, "E5183", {"start": v(-70.09, 90.72) * mm, "end": v(-70.08, 91.09) * mm});
            skLineSegment(sketch, "E5184", {"start": v(-70.1, 90.37) * mm, "end": v(-70.09, 90.72) * mm});
            skLineSegment(sketch, "E5185", {"start": v(-70.14, 90.06) * mm, "end": v(-70.1, 90.37) * mm});
            skLineSegment(sketch, "E5186", {"start": v(-70.2, 89.8) * mm, "end": v(-70.14, 90.06) * mm});
            skLineSegment(sketch, "E5187", {"start": v(-70.24, 89.6) * mm, "end": v(-70.2, 89.8) * mm});
            skLineSegment(sketch, "E5188", {"start": v(-70.4, 89.17) * mm, "end": v(-70.24, 89.6) * mm});
            skArc(sketch, "E5189", {"start": v(-70.4, 89.17) * mm, "mid": v(-70.4, 88.59) * mm, "end": v(-70, 88.17) * mm});
            skArc(sketch, "E5190", {"start": v(-69.35, 87.88) * mm, "mid": v(-69.67, 88.03) * mm, "end": v(-70, 88.17) * mm});
            skArc(sketch, "E5191", {"start": v(-69.35, 87.88) * mm, "mid": v(-68.77, 87.84) * mm, "end": v(-68.33, 88.22) * mm});
            skLineSegment(sketch, "E5192", {"start": v(-66.31, 90.3) * mm, "end": v(-65.4, 90.85) * mm});
            skLineSegment(sketch, "E5193", {"start": v(-67.09, 89.72) * mm, "end": v(-66.31, 90.3) * mm});
            skLineSegment(sketch, "E5194", {"start": v(-67.37, 89.47) * mm, "end": v(-67.09, 89.72) * mm});
            skLineSegment(sketch, "E5195", {"start": v(-67.61, 89.23) * mm, "end": v(-67.37, 89.47) * mm});
            skLineSegment(sketch, "E5196", {"start": v(-67.83, 89) * mm, "end": v(-67.61, 89.23) * mm});
            skLineSegment(sketch, "E5197", {"start": v(-68, 88.8) * mm, "end": v(-67.83, 89) * mm});
            skLineSegment(sketch, "E5198", {"start": v(-68.1, 88.63) * mm, "end": v(-68, 88.8) * mm});
            skLineSegment(sketch, "E5199", {"start": v(-68.33, 88.22) * mm, "end": v(-68.1, 88.63) * mm});
            skArc(sketch, "E5200", {"start": v(-64.2, 90.1) * mm, "mid": v(-64.8, 90.48) * mm, "end": v(-65.4, 90.85) * mm});
            skLineSegment(sketch, "E5201", {"start": v(-64.33, 89.03) * mm, "end": v(-64.2, 90.1) * mm});
            skLineSegment(sketch, "E5202", {"start": v(-64.54, 88.08) * mm, "end": v(-64.33, 89.03) * mm});
            skLineSegment(sketch, "E5203", {"start": v(-64.64, 87.72) * mm, "end": v(-64.54, 88.08) * mm});
            skLineSegment(sketch, "E5204", {"start": v(-64.76, 87.4) * mm, "end": v(-64.64, 87.72) * mm});
            skLineSegment(sketch, "E5205", {"start": v(-64.88, 87.11) * mm, "end": v(-64.76, 87.4) * mm});
            skLineSegment(sketch, "E5206", {"start": v(-65, 86.87) * mm, "end": v(-64.88, 87.11) * mm});
            skLineSegment(sketch, "E5207", {"start": v(-65.1, 86.7) * mm, "end": v(-65, 86.87) * mm});
            skLineSegment(sketch, "E5208", {"start": v(-65.39, 86.33) * mm, "end": v(-65.1, 86.7) * mm});
            skArc(sketch, "E5209", {"start": v(-65.39, 86.33) * mm, "mid": v(-65.54, 85.77) * mm, "end": v(-65.27, 85.26) * mm});
            skArc(sketch, "E5210", {"start": v(-64.74, 84.8) * mm, "mid": v(-65, 85.03) * mm, "end": v(-65.27, 85.26) * mm});
            skArc(sketch, "E5211", {"start": v(-64.74, 84.8) * mm, "mid": v(-64.2, 84.6) * mm, "end": v(-63.66, 84.83) * mm});
            skLineSegment(sketch, "E5212", {"start": v(-61.14, 86.26) * mm, "end": v(-60.1, 86.53) * mm});
            skLineSegment(sketch, "E5213", {"start": v(-62.05, 85.92) * mm, "end": v(-61.14, 86.26) * mm});
            skLineSegment(sketch, "E5214", {"start": v(-62.39, 85.77) * mm, "end": v(-62.05, 85.92) * mm});
            skLineSegment(sketch, "E5215", {"start": v(-62.69, 85.6) * mm, "end": v(-62.39, 85.77) * mm});
            skLineSegment(sketch, "E5216", {"start": v(-62.96, 85.44) * mm, "end": v(-62.69, 85.6) * mm});
            skLineSegment(sketch, "E5217", {"start": v(-63.18, 85.29) * mm, "end": v(-62.96, 85.44) * mm});
            skLineSegment(sketch, "E5218", {"start": v(-63.33, 85.16) * mm, "end": v(-63.18, 85.29) * mm});
            skLineSegment(sketch, "E5219", {"start": v(-63.66, 84.83) * mm, "end": v(-63.33, 85.16) * mm});
            skArc(sketch, "E5220", {"start": v(-59.18, 85.47) * mm, "mid": v(-59.63, 86) * mm, "end": v(-60.1, 86.53) * mm});
            skLineSegment(sketch, "E5221", {"start": v(-59.6, 84.48) * mm, "end": v(-59.18, 85.47) * mm});
            skLineSegment(sketch, "E5222", {"start": v(-60.06, 83.63) * mm, "end": v(-59.6, 84.48) * mm});
            skLineSegment(sketch, "E5223", {"start": v(-60.27, 83.32) * mm, "end": v(-60.06, 83.63) * mm});
            skLineSegment(sketch, "E5224", {"start": v(-60.47, 83.04) * mm, "end": v(-60.27, 83.32) * mm});
            skLineSegment(sketch, "E5225", {"start": v(-60.67, 82.8) * mm, "end": v(-60.47, 83.04) * mm});
            skLineSegment(sketch, "E5226", {"start": v(-60.85, 82.6) * mm, "end": v(-60.67, 82.8) * mm});
            skLineSegment(sketch, "E5227", {"start": v(-61, 82.47) * mm, "end": v(-60.85, 82.6) * mm});
            skLineSegment(sketch, "E5228", {"start": v(-61.37, 82.2) * mm, "end": v(-61, 82.47) * mm});
            skArc(sketch, "E5229", {"start": v(-61.37, 82.2) * mm, "mid": v(-61.68, 81.7) * mm, "end": v(-61.56, 81.13) * mm});
            skArc(sketch, "E5230", {"start": v(-61.18, 80.54) * mm, "mid": v(-61.37, 80.83) * mm, "end": v(-61.56, 81.13) * mm});
            skArc(sketch, "E5231", {"start": v(-61.18, 80.54) * mm, "mid": v(-60.71, 80.2) * mm, "end": v(-60.14, 80.27) * mm});
            skLineSegment(sketch, "E5232", {"start": v(-57.32, 80.93) * mm, "end": v(-56.24, 80.9) * mm});
            skLineSegment(sketch, "E5233", {"start": v(-58.28, 80.86) * mm, "end": v(-57.32, 80.93) * mm});
            skLineSegment(sketch, "E5234", {"start": v(-58.65, 80.8) * mm, "end": v(-58.28, 80.86) * mm});
            skLineSegment(sketch, "E5235", {"start": v(-58.99, 80.74) * mm, "end": v(-58.65, 80.8) * mm});
            skLineSegment(sketch, "E5236", {"start": v(-59.29, 80.66) * mm, "end": v(-58.99, 80.74) * mm});
            skLineSegment(sketch, "E5237", {"start": v(-59.54, 80.57) * mm, "end": v(-59.29, 80.66) * mm});
            skLineSegment(sketch, "E5238", {"start": v(-59.73, 80.5) * mm, "end": v(-59.54, 80.57) * mm});
            skLineSegment(sketch, "E5239", {"start": v(-60.14, 80.27) * mm, "end": v(-59.73, 80.5) * mm});
            skArc(sketch, "E5240", {"start": v(-55.66, 79.62) * mm, "mid": v(-55.94, 80.26) * mm, "end": v(-56.24, 80.9) * mm});
            skLineSegment(sketch, "E5241", {"start": v(-56.34, 78.79) * mm, "end": v(-55.66, 79.62) * mm});
            skLineSegment(sketch, "E5242", {"start": v(-57.02, 78.1) * mm, "end": v(-56.34, 78.79) * mm});
            skLineSegment(sketch, "E5243", {"start": v(-57.3, 77.86) * mm, "end": v(-57.02, 78.1) * mm});
            skLineSegment(sketch, "E5244", {"start": v(-57.58, 77.65) * mm, "end": v(-57.3, 77.86) * mm});
            skLineSegment(sketch, "E5245", {"start": v(-57.84, 77.47) * mm, "end": v(-57.58, 77.65) * mm});
            skLineSegment(sketch, "E5246", {"start": v(-58.07, 77.34) * mm, "end": v(-57.84, 77.47) * mm});
            skLineSegment(sketch, "E5247", {"start": v(-58.25, 77.25) * mm, "end": v(-58.07, 77.34) * mm});
            skLineSegment(sketch, "E5248", {"start": v(-58.68, 77.09) * mm, "end": v(-58.25, 77.25) * mm});
            skLineSegment(sketch, "E5249", {"start": v(-58.93, 13.84) * mm, "end": v(-58.58, 14.08) * mm});
            skArc(sketch, "E5250", {"start": v(-58.93, 13.84) * mm, "mid": v(-59.25, 13.36) * mm, "end": v(-59.15, 12.8) * mm});
            skArc(sketch, "E5251", {"start": v(-58.78, 12.2) * mm, "mid": v(-58.96, 12.5) * mm, "end": v(-59.15, 12.8) * mm});
            skArc(sketch, "E5252", {"start": v(-58.78, 12.2) * mm, "mid": v(-58.33, 11.84) * mm, "end": v(-57.75, 11.9) * mm});
            skLineSegment(sketch, "E5253", {"start": v(-54.92, 12.5) * mm, "end": v(-53.84, 12.45) * mm});
            skLineSegment(sketch, "E5254", {"start": v(-55.9, 12.44) * mm, "end": v(-54.92, 12.5) * mm});
            skLineSegment(sketch, "E5255", {"start": v(-56.27, 12.4) * mm, "end": v(-55.9, 12.44) * mm});
            skLineSegment(sketch, "E5256", {"start": v(-56.61, 12.33) * mm, "end": v(-56.27, 12.4) * mm});
            skLineSegment(sketch, "E5257", {"start": v(-56.92, 12.25) * mm, "end": v(-56.61, 12.33) * mm});
            skLineSegment(sketch, "E5258", {"start": v(-57.18, 12.17) * mm, "end": v(-56.92, 12.25) * mm});
            skLineSegment(sketch, "E5259", {"start": v(-57.38, 12.1) * mm, "end": v(-57.18, 12.17) * mm});
            skLineSegment(sketch, "E5260", {"start": v(-57.75, 11.9) * mm, "end": v(-57.38, 12.1) * mm});
            skArc(sketch, "E5261", {"start": v(-53.27, 11.15) * mm, "mid": v(-53.55, 11.8) * mm, "end": v(-53.84, 12.45) * mm});
            skLineSegment(sketch, "E5262", {"start": v(-53.98, 10.32) * mm, "end": v(-53.27, 11.15) * mm});
            skLineSegment(sketch, "E5263", {"start": v(-54.68, 9.65) * mm, "end": v(-53.98, 10.32) * mm});
            skLineSegment(sketch, "E5264", {"start": v(-54.97, 9.4) * mm, "end": v(-54.68, 9.65) * mm});
            skLineSegment(sketch, "E5265", {"start": v(-55.25, 9.2) * mm, "end": v(-54.97, 9.4) * mm});
            skLineSegment(sketch, "E5266", {"start": v(-55.52, 9.03) * mm, "end": v(-55.25, 9.2) * mm});
            skLineSegment(sketch, "E5267", {"start": v(-55.76, 8.9) * mm, "end": v(-55.52, 9.03) * mm});
            skLineSegment(sketch, "E5268", {"start": v(-55.94, 8.8) * mm, "end": v(-55.76, 8.9) * mm});
            skLineSegment(sketch, "E5269", {"start": v(-56.34, 8.66) * mm, "end": v(-55.94, 8.8) * mm});
            skArc(sketch, "E5270", {"start": v(-56.34, 8.66) * mm, "mid": v(-56.78, 8.28) * mm, "end": v(-56.83, 7.7) * mm});
            skArc(sketch, "E5271", {"start": v(-56.65, 7.04) * mm, "mid": v(-56.74, 7.37) * mm, "end": v(-56.83, 7.7) * mm});
            skArc(sketch, "E5272", {"start": v(-56.65, 7.04) * mm, "mid": v(-56.3, 6.57) * mm, "end": v(-55.73, 6.48) * mm});
            skLineSegment(sketch, "E5273", {"start": v(-52.85, 6.29) * mm, "end": v(-51.82, 5.95) * mm});
            skLineSegment(sketch, "E5274", {"start": v(-53.8, 6.5) * mm, "end": v(-52.85, 6.29) * mm});
            skLineSegment(sketch, "E5275", {"start": v(-54.17, 6.55) * mm, "end": v(-53.8, 6.5) * mm});
            skLineSegment(sketch, "E5276", {"start": v(-55.25, 0.71) * mm, "end": v(-54.83, 0.68) * mm});
            skArc(sketch, "E5277", {"start": v(-51.82, -2.26) * mm, "mid": v(-51.7, -1.56) * mm, "end": v(-51.62, -0.86) * mm});
            skLineSegment(sketch, "E5278", {"start": v(-52.85, -2.6) * mm, "end": v(-51.82, -2.26) * mm});
            skLineSegment(sketch, "E5279", {"start": v(-53.8, -2.81) * mm, "end": v(-52.85, -2.6) * mm});
            skLineSegment(sketch, "E5280", {"start": v(-54.17, -2.87) * mm, "end": v(-53.8, -2.81) * mm});
            skLineSegment(sketch, "E5281", {"start": v(-54.52, -2.9) * mm, "end": v(-54.17, -2.87) * mm});
            skLineSegment(sketch, "E5282", {"start": v(-54.84, -2.9) * mm, "end": v(-54.52, -2.9) * mm});
            skLineSegment(sketch, "E5283", {"start": v(-55.11, -2.9) * mm, "end": v(-54.84, -2.9) * mm});
            skLineSegment(sketch, "E5284", {"start": v(-55.32, -2.88) * mm, "end": v(-55.11, -2.9) * mm});
            skLineSegment(sketch, "E5285", {"start": v(-55.73, -2.8) * mm, "end": v(-55.32, -2.88) * mm});
            skArc(sketch, "E5286", {"start": v(-55.73, -2.8) * mm, "mid": v(-56.3, -2.89) * mm, "end": v(-56.65, -3.35) * mm});
            skArc(sketch, "E5287", {"start": v(-56.83, -4.02) * mm, "mid": v(-56.74, -3.69) * mm, "end": v(-56.65, -3.35) * mm});
            skLineSegment(sketch, "E5288", {"start": v(-55.76, -5.2) * mm, "end": v(-55.52, -5.34) * mm});
            skLineSegment(sketch, "E5289", {"start": v(-55.94, -5.12) * mm, "end": v(-55.76, -5.2) * mm});
            skLineSegment(sketch, "E5290", {"start": v(-56.34, -4.97) * mm, "end": v(-55.94, -5.12) * mm});
            skArc(sketch, "E5291", {"start": v(-53.84, -8.76) * mm, "mid": v(-53.55, -8.12) * mm, "end": v(-53.27, -7.46) * mm});
            skLineSegment(sketch, "E5292", {"start": v(-55.52, -5.34) * mm, "end": v(-55.25, -5.52) * mm});
            skLineSegment(sketch, "E5293", {"start": v(-55.25, -5.52) * mm, "end": v(-54.97, -5.72) * mm});
            skLineSegment(sketch, "E5294", {"start": v(-54.97, -5.72) * mm, "end": v(-54.68, -5.96) * mm});
            skLineSegment(sketch, "E5295", {"start": v(-54.68, -5.96) * mm, "end": v(-53.98, -6.64) * mm});
            skLineSegment(sketch, "E5296", {"start": v(-53.98, -6.64) * mm, "end": v(-53.27, -7.46) * mm});
            skArc(sketch, "E5297", {"start": v(-56.83, -4.02) * mm, "mid": v(-56.78, -4.6) * mm, "end": v(-56.34, -4.97) * mm});
            skLineSegment(sketch, "E5298", {"start": v(-54.83, 0.68) * mm, "end": v(-54.62, 0.65) * mm});
            skLineSegment(sketch, "E5299", {"start": v(-54.62, 0.65) * mm, "end": v(-54.36, 0.58) * mm});
            skLineSegment(sketch, "E5300", {"start": v(-54.36, 0.58) * mm, "end": v(-54.06, 0.48) * mm});
            skLineSegment(sketch, "E5301", {"start": v(-54.06, 0.48) * mm, "end": v(-53.73, 0.36) * mm});
            skLineSegment(sketch, "E5302", {"start": v(-53.73, 0.36) * mm, "end": v(-53.38, 0.2) * mm});
            skLineSegment(sketch, "E5303", {"start": v(-53.38, 0.2) * mm, "end": v(-52.52, -0.25) * mm});
            skLineSegment(sketch, "E5304", {"start": v(-52.52, -0.25) * mm, "end": v(-51.62, -0.86) * mm});
            skArc(sketch, "E5305", {"start": v(-55.98, 1.5) * mm, "mid": v(-55.77, 0.95) * mm, "end": v(-55.25, 0.71) * mm});
            skArc(sketch, "E5306", {"start": v(-55.98, 1.5) * mm, "mid": v(-55.98, 1.84) * mm, "end": v(-55.98, 2.2) * mm});
            skArc(sketch, "E5307", {"start": v(-55.25, 2.97) * mm, "mid": v(-55.77, 2.73) * mm, "end": v(-55.98, 2.2) * mm});
            skLineSegment(sketch, "E5308", {"start": v(-55.25, 2.97) * mm, "end": v(-54.83, 3) * mm});
            skLineSegment(sketch, "E5309", {"start": v(-54.83, 3) * mm, "end": v(-54.62, 3.04) * mm});
            skLineSegment(sketch, "E5310", {"start": v(-54.62, 3.04) * mm, "end": v(-54.36, 3.1) * mm});
            skLineSegment(sketch, "E5311", {"start": v(-54.36, 3.1) * mm, "end": v(-54.06, 3.2) * mm});
            skLineSegment(sketch, "E5312", {"start": v(-54.06, 3.2) * mm, "end": v(-53.73, 3.33) * mm});
            skLineSegment(sketch, "E5313", {"start": v(-53.73, 3.33) * mm, "end": v(-53.38, 3.48) * mm});
            skLineSegment(sketch, "E5314", {"start": v(-53.38, 3.48) * mm, "end": v(-52.52, 3.94) * mm});
            skLineSegment(sketch, "E5315", {"start": v(-52.52, 3.94) * mm, "end": v(-51.62, 4.54) * mm});
            skArc(sketch, "E5316", {"start": v(-51.62, 4.54) * mm, "mid": v(-51.7, 5.25) * mm, "end": v(-51.82, 5.95) * mm});
            skLineSegment(sketch, "E5317", {"start": v(-55.73, 6.48) * mm, "end": v(-55.32, 6.57) * mm});
            skLineSegment(sketch, "E5318", {"start": v(-55.32, 6.57) * mm, "end": v(-55.11, 6.59) * mm});
            skLineSegment(sketch, "E5319", {"start": v(-55.11, 6.59) * mm, "end": v(-54.84, 6.6) * mm});
            skLineSegment(sketch, "E5320", {"start": v(-54.84, 6.6) * mm, "end": v(-54.52, 6.58) * mm});
            skLineSegment(sketch, "E5321", {"start": v(-54.52, 6.58) * mm, "end": v(-54.17, 6.55) * mm});
            skLineSegment(sketch, "E5322", {"start": v(-62.17, 19.16) * mm, "end": v(-62.04, 19.48) * mm});
            skLineSegment(sketch, "E5323", {"start": v(-62.04, 19.48) * mm, "end": v(-61.91, 19.83) * mm});
            skLineSegment(sketch, "E5324", {"start": v(-61.91, 19.83) * mm, "end": v(-61.66, 20.78) * mm});
            skLineSegment(sketch, "E5325", {"start": v(-61.66, 20.78) * mm, "end": v(-61.49, 21.85) * mm});
            skArc(sketch, "E5326", {"start": v(-61.49, 21.85) * mm, "mid": v(-62.06, 22.27) * mm, "end": v(-62.64, 22.67) * mm});
            skLineSegment(sketch, "E5327", {"start": v(-65.7, 20.17) * mm, "end": v(-65.49, 20.53) * mm});
            skLineSegment(sketch, "E5328", {"start": v(-65.49, 20.53) * mm, "end": v(-65.36, 20.7) * mm});
            skLineSegment(sketch, "E5329", {"start": v(-65.36, 20.7) * mm, "end": v(-65.18, 20.9) * mm});
            skLineSegment(sketch, "E5330", {"start": v(-65.18, 20.9) * mm, "end": v(-64.95, 21.12) * mm});
            skLineSegment(sketch, "E5331", {"start": v(-64.95, 21.12) * mm, "end": v(-64.7, 21.36) * mm});
            skLineSegment(sketch, "E5332", {"start": v(-64.7, 21.36) * mm, "end": v(-64.4, 21.6) * mm});
            skLineSegment(sketch, "E5333", {"start": v(-64.4, 21.6) * mm, "end": v(-63.6, 22.15) * mm});
            skLineSegment(sketch, "E5334", {"start": v(-63.6, 22.15) * mm, "end": v(-62.64, 22.67) * mm});
            skArc(sketch, "E5335", {"start": v(-66.74, 19.88) * mm, "mid": v(-66.16, 19.82) * mm, "end": v(-65.7, 20.17) * mm});
            skArc(sketch, "E5336", {"start": v(-66.74, 19.88) * mm, "mid": v(-67.05, 20.04) * mm, "end": v(-67.36, 20.2) * mm});
            skArc(sketch, "E5337", {"start": v(-67.72, 21.2) * mm, "mid": v(-67.74, 20.63) * mm, "end": v(-67.36, 20.2) * mm});
            skLineSegment(sketch, "E5338", {"start": v(-67.72, 21.2) * mm, "end": v(-67.55, 21.6) * mm});
            skLineSegment(sketch, "E5339", {"start": v(-67.55, 21.6) * mm, "end": v(-67.49, 21.8) * mm});
            skLineSegment(sketch, "E5340", {"start": v(-67.49, 21.8) * mm, "end": v(-67.42, 22.06) * mm});
            skLineSegment(sketch, "E5341", {"start": v(-67.42, 22.06) * mm, "end": v(-67.37, 22.37) * mm});
            skLineSegment(sketch, "E5342", {"start": v(-67.37, 22.37) * mm, "end": v(-67.33, 22.72) * mm});
            skLineSegment(sketch, "E5343", {"start": v(-67.33, 22.72) * mm, "end": v(-67.3, 23.1) * mm});
            skLineSegment(sketch, "E5344", {"start": v(-67.3, 23.1) * mm, "end": v(-67.32, 24.08) * mm});
            skLineSegment(sketch, "E5345", {"start": v(-67.32, 24.08) * mm, "end": v(-67.44, 25.15) * mm});
            skArc(sketch, "E5346", {"start": v(-67.44, 25.15) * mm, "mid": v(-68.1, 25.4) * mm, "end": v(-68.78, 25.63) * mm});
            skLineSegment(sketch, "E5347", {"start": v(-71.05, 22.4) * mm, "end": v(-70.94, 22.8) * mm});
            skLineSegment(sketch, "E5348", {"start": v(-70.94, 22.8) * mm, "end": v(-70.86, 23) * mm});
            skLineSegment(sketch, "E5349", {"start": v(-70.86, 23) * mm, "end": v(-70.74, 23.24) * mm});
            skLineSegment(sketch, "E5350", {"start": v(-70.74, 23.24) * mm, "end": v(-70.58, 23.52) * mm});
            skLineSegment(sketch, "E5351", {"start": v(-70.58, 23.52) * mm, "end": v(-70.4, 23.81) * mm});
            skLineSegment(sketch, "E5352", {"start": v(-70.4, 23.81) * mm, "end": v(-70.18, 24.12) * mm});
            skLineSegment(sketch, "E5353", {"start": v(-70.18, 24.12) * mm, "end": v(-69.55, 24.87) * mm});
            skLineSegment(sketch, "E5354", {"start": v(-69.55, 24.87) * mm, "end": v(-68.78, 25.63) * mm});
            skArc(sketch, "E5355", {"start": v(-71.96, 21.84) * mm, "mid": v(-71.4, 21.93) * mm, "end": v(-71.05, 22.4) * mm});
            skArc(sketch, "E5356", {"start": v(-71.96, 21.84) * mm, "mid": v(-72.3, 21.91) * mm, "end": v(-72.65, 21.98) * mm});
            skArc(sketch, "E5357", {"start": v(-73.27, 22.85) * mm, "mid": v(-73.13, 22.3) * mm, "end": v(-72.65, 21.98) * mm});
            skLineSegment(sketch, "E5358", {"start": v(-73.27, 22.85) * mm, "end": v(-73.2, 23.27) * mm});
            skLineSegment(sketch, "E5359", {"start": v(-73.2, 23.27) * mm, "end": v(-73.2, 23.48) * mm});
            skLineSegment(sketch, "E5360", {"start": v(-73.2, 23.48) * mm, "end": v(-73.21, 23.75) * mm});
            skLineSegment(sketch, "E5361", {"start": v(-73.21, 23.75) * mm, "end": v(-73.25, 24.07) * mm});
            skLineSegment(sketch, "E5362", {"start": v(-73.25, 24.07) * mm, "end": v(-73.3, 24.42) * mm});
            skLineSegment(sketch, "E5363", {"start": v(-73.3, 24.42) * mm, "end": v(-73.38, 24.78) * mm});
            skLineSegment(sketch, "E5364", {"start": v(-73.38, 24.78) * mm, "end": v(-73.66, 25.72) * mm});
            skLineSegment(sketch, "E5365", {"start": v(-73.66, 25.72) * mm, "end": v(-74.06, 26.73) * mm});
            skArc(sketch, "E5366", {"start": v(-74.06, 26.73) * mm, "mid": v(-74.77, 26.78) * mm, "end": v(-75.48, 26.82) * mm});
            skLineSegment(sketch, "E5367", {"start": v(-76.8, 23.1) * mm, "end": v(-76.8, 23.52) * mm});
            skLineSegment(sketch, "E5368", {"start": v(-76.8, 23.52) * mm, "end": v(-76.77, 23.73) * mm});
            skLineSegment(sketch, "E5369", {"start": v(-76.77, 23.73) * mm, "end": v(-76.72, 24) * mm});
            skLineSegment(sketch, "E5370", {"start": v(-76.72, 24) * mm, "end": v(-76.65, 24.3) * mm});
            skLineSegment(sketch, "E5371", {"start": v(-76.65, 24.3) * mm, "end": v(-76.55, 24.64) * mm});
            skLineSegment(sketch, "E5372", {"start": v(-76.55, 24.64) * mm, "end": v(-76.42, 25) * mm});
            skLineSegment(sketch, "E5373", {"start": v(-76.42, 25) * mm, "end": v(-76.02, 25.88) * mm});
            skLineSegment(sketch, "E5374", {"start": v(-76.02, 25.88) * mm, "end": v(-75.48, 26.82) * mm});
            skArc(sketch, "E5375", {"start": v(-77.53, 22.32) * mm, "mid": v(-77, 22.56) * mm, "end": v(-76.8, 23.1) * mm});
            skArc(sketch, "E5376", {"start": v(-77.53, 22.32) * mm, "mid": v(-77.88, 22.3) * mm, "end": v(-78.22, 22.27) * mm});
            skArc(sketch, "E5377", {"start": v(-79.05, 22.94) * mm, "mid": v(-78.78, 22.44) * mm, "end": v(-78.22, 22.27) * mm});
            skLineSegment(sketch, "E5378", {"start": v(-79.05, 22.94) * mm, "end": v(-79.11, 23.36) * mm});
            skLineSegment(sketch, "E5379", {"start": v(-79.11, 23.36) * mm, "end": v(-79.16, 23.56) * mm});
            skLineSegment(sketch, "E5380", {"start": v(-79.16, 23.56) * mm, "end": v(-79.25, 23.82) * mm});
            skLineSegment(sketch, "E5381", {"start": v(-79.25, 23.82) * mm, "end": v(-79.36, 24.12) * mm});
            skLineSegment(sketch, "E5382", {"start": v(-79.36, 24.12) * mm, "end": v(-79.5, 24.43) * mm});
            skLineSegment(sketch, "E5383", {"start": v(-79.5, 24.43) * mm, "end": v(-79.68, 24.77) * mm});
            skLineSegment(sketch, "E5384", {"start": v(-79.68, 24.77) * mm, "end": v(-80.2, 25.6) * mm});
            skLineSegment(sketch, "E5385", {"start": v(-80.2, 25.6) * mm, "end": v(-80.87, 26.45) * mm});
            skArc(sketch, "E5386", {"start": v(-80.87, 26.45) * mm, "mid": v(-81.56, 26.32) * mm, "end": v(-82.26, 26.17) * mm});
            skLineSegment(sketch, "E5387", {"start": v(-82.52, 22.22) * mm, "end": v(-82.63, 22.63) * mm});
            skLineSegment(sketch, "E5388", {"start": v(-82.63, 22.63) * mm, "end": v(-82.67, 22.83) * mm});
            skLineSegment(sketch, "E5389", {"start": v(-82.67, 22.83) * mm, "end": v(-82.7, 23.1) * mm});
            skLineSegment(sketch, "E5390", {"start": v(-82.7, 23.1) * mm, "end": v(-82.7, 23.42) * mm});
            skLineSegment(sketch, "E5391", {"start": v(-82.7, 23.42) * mm, "end": v(-82.7, 23.77) * mm});
            skLineSegment(sketch, "E5392", {"start": v(-82.7, 23.77) * mm, "end": v(-82.67, 24.15) * mm});
            skLineSegment(sketch, "E5393", {"start": v(-82.67, 24.15) * mm, "end": v(-82.52, 25.12) * mm});
            skLineSegment(sketch, "E5394", {"start": v(-82.52, 25.12) * mm, "end": v(-82.26, 26.17) * mm});
            skArc(sketch, "E5395", {"start": v(-83.01, 21.27) * mm, "mid": v(-82.57, 21.65) * mm, "end": v(-82.52, 22.22) * mm});
            skArc(sketch, "E5396", {"start": v(-83.01, 21.27) * mm, "mid": v(-83.34, 21.16) * mm, "end": v(-83.67, 21.04) * mm});
            skArc(sketch, "E5397", {"start": v(-84.65, 21.46) * mm, "mid": v(-84.25, 21.05) * mm, "end": v(-83.67, 21.04) * mm});
            skLineSegment(sketch, "E5398", {"start": v(-84.65, 21.46) * mm, "end": v(-84.82, 21.85) * mm});
            skLineSegment(sketch, "E5399", {"start": v(-84.82, 21.85) * mm, "end": v(-84.92, 22.03) * mm});
            skLineSegment(sketch, "E5400", {"start": v(-84.92, 22.03) * mm, "end": v(-85.07, 22.26) * mm});
            skLineSegment(sketch, "E5401", {"start": v(-85.07, 22.26) * mm, "end": v(-85.27, 22.51) * mm});
            skLineSegment(sketch, "E5402", {"start": v(-85.27, 22.51) * mm, "end": v(-85.5, 22.78) * mm});
            skLineSegment(sketch, "E5403", {"start": v(-85.5, 22.78) * mm, "end": v(-85.75, 23.05) * mm});
            skLineSegment(sketch, "E5404", {"start": v(-85.75, 23.05) * mm, "end": v(-86.47, 23.71) * mm});
            skLineSegment(sketch, "E5405", {"start": v(-86.47, 23.71) * mm, "end": v(-87.34, 24.36) * mm});
            skArc(sketch, "E5406", {"start": v(-87.34, 24.36) * mm, "mid": v(-87.98, 24.04) * mm, "end": v(-88.6, 23.7) * mm});
            skLineSegment(sketch, "E5407", {"start": v(-87.8, 19.84) * mm, "end": v(-88.01, 20.2) * mm});
            skLineSegment(sketch, "E5408", {"start": v(-88.01, 20.2) * mm, "end": v(-88.1, 20.39) * mm});
            skLineSegment(sketch, "E5409", {"start": v(-88.1, 20.39) * mm, "end": v(-88.2, 20.64) * mm});
            skLineSegment(sketch, "E5410", {"start": v(-88.2, 20.64) * mm, "end": v(-88.3, 20.94) * mm});
            skLineSegment(sketch, "E5411", {"start": v(-88.3, 20.94) * mm, "end": v(-88.38, 21.28) * mm});
            skLineSegment(sketch, "E5412", {"start": v(-88.38, 21.28) * mm, "end": v(-88.46, 21.65) * mm});
            skLineSegment(sketch, "E5413", {"start": v(-88.46, 21.65) * mm, "end": v(-88.58, 22.62) * mm});
            skLineSegment(sketch, "E5414", {"start": v(-88.58, 22.62) * mm, "end": v(-88.6, 23.7) * mm});
            skArc(sketch, "E5415", {"start": v(-88.01, 18.79) * mm, "mid": v(-87.7, 19.27) * mm, "end": v(-87.8, 19.84) * mm});
            skArc(sketch, "E5416", {"start": v(-88.01, 18.79) * mm, "mid": v(-88.3, 18.6) * mm, "end": v(-88.58, 18.39) * mm});
            skArc(sketch, "E5417", {"start": v(-89.64, 18.53) * mm, "mid": v(-89.14, 18.24) * mm, "end": v(-88.58, 18.39) * mm});
            skLineSegment(sketch, "E5418", {"start": v(-89.64, 18.53) * mm, "end": v(-89.9, 18.86) * mm});
            skLineSegment(sketch, "E5419", {"start": v(-89.9, 18.86) * mm, "end": v(-90.06, 19) * mm});
            skLineSegment(sketch, "E5420", {"start": v(-90.06, 19) * mm, "end": v(-90.26, 19.18) * mm});
            skLineSegment(sketch, "E5421", {"start": v(-90.26, 19.18) * mm, "end": v(-90.52, 19.37) * mm});
            skLineSegment(sketch, "E5422", {"start": v(-90.52, 19.37) * mm, "end": v(-90.8, 19.57) * mm});
            skLineSegment(sketch, "E5423", {"start": v(-90.8, 19.57) * mm, "end": v(-91.13, 19.76) * mm});
            skLineSegment(sketch, "E5424", {"start": v(-73.46, -93.1) * mm, "end": v(-72.87, -94.02) * mm});
            skArc(sketch, "E5425", {"start": v(-72.87, -94.02) * mm, "mid": v(-72.16, -93.94) * mm, "end": v(-71.45, -93.83) * mm});
            skLineSegment(sketch, "E5426", {"start": v(-70.88, -89.91) * mm, "end": v(-70.8, -90.32) * mm});
            skLineSegment(sketch, "E5427", {"start": v(-70.8, -90.32) * mm, "end": v(-70.79, -90.6) * mm});
            skLineSegment(sketch, "E5428", {"start": v(-70.79, -90.6) * mm, "end": v(-70.8, -90.97) * mm});
            skLineSegment(sketch, "E5429", {"start": v(-70.8, -90.97) * mm, "end": v(-70.83, -91.38) * mm});
            skLineSegment(sketch, "E5430", {"start": v(-70.83, -91.38) * mm, "end": v(-70.89, -91.83) * mm});
            skLineSegment(sketch, "E5431", {"start": v(-70.89, -91.83) * mm, "end": v(-71.1, -92.8) * mm});
            skLineSegment(sketch, "E5432", {"start": v(-71.1, -92.8) * mm, "end": v(-71.45, -93.83) * mm});
            skArc(sketch, "E5433", {"start": v(-70.32, -89.01) * mm, "mid": v(-70.78, -89.35) * mm, "end": v(-70.88, -89.91) * mm});
            skArc(sketch, "E5434", {"start": v(-70.32, -89.01) * mm, "mid": v(-69.99, -88.93) * mm, "end": v(-69.65, -88.83) * mm});
            skArc(sketch, "E5435", {"start": v(-68.71, -89.33) * mm, "mid": v(-69.08, -88.9) * mm, "end": v(-69.65, -88.83) * mm});
            skLineSegment(sketch, "E5436", {"start": v(-68.71, -89.33) * mm, "end": v(-68.58, -89.72) * mm});
            skLineSegment(sketch, "E5437", {"start": v(-68.58, -89.72) * mm, "end": v(-68.45, -89.98) * mm});
            skLineSegment(sketch, "E5438", {"start": v(-68.45, -89.98) * mm, "end": v(-68.26, -90.3) * mm});
            skLineSegment(sketch, "E5439", {"start": v(-68.26, -90.3) * mm, "end": v(-68.03, -90.63) * mm});
            skLineSegment(sketch, "E5440", {"start": v(-68.03, -90.63) * mm, "end": v(-67.75, -91) * mm});
            skLineSegment(sketch, "E5441", {"start": v(-67.75, -91) * mm, "end": v(-67.08, -91.72) * mm});
            skLineSegment(sketch, "E5442", {"start": v(-67.08, -91.72) * mm, "end": v(-66.26, -92.44) * mm});
            skArc(sketch, "E5443", {"start": v(-66.26, -92.44) * mm, "mid": v(-65.6, -92.18) * mm, "end": v(-64.94, -91.9) * mm});
            skLineSegment(sketch, "E5444", {"start": v(-65.41, -87.96) * mm, "end": v(-65.23, -88.34) * mm});
            skLineSegment(sketch, "E5445", {"start": v(-65.23, -88.34) * mm, "end": v(-65.14, -88.61) * mm});
            skLineSegment(sketch, "E5446", {"start": v(-65.14, -88.61) * mm, "end": v(-65.05, -88.96) * mm});
            skLineSegment(sketch, "E5447", {"start": v(-65.05, -88.96) * mm, "end": v(-64.98, -89.37) * mm});
            skLineSegment(sketch, "E5448", {"start": v(-64.98, -89.37) * mm, "end": v(-64.92, -89.82) * mm});
            skLineSegment(sketch, "E5449", {"start": v(-64.92, -89.82) * mm, "end": v(-64.88, -90.8) * mm});
            skLineSegment(sketch, "E5450", {"start": v(-64.88, -90.8) * mm, "end": v(-64.94, -91.9) * mm});
            skArc(sketch, "E5451", {"start": v(-65.1, -86.95) * mm, "mid": v(-65.46, -87.4) * mm, "end": v(-65.41, -87.96) * mm});
            skArc(sketch, "E5452", {"start": v(-65.1, -86.95) * mm, "mid": v(-64.8, -86.78) * mm, "end": v(-64.5, -86.6) * mm});
            skArc(sketch, "E5453", {"start": v(-63.47, -86.84) * mm, "mid": v(-63.94, -86.51) * mm, "end": v(-64.5, -86.6) * mm});
            skLineSegment(sketch, "E5454", {"start": v(-63.47, -86.84) * mm, "end": v(-63.23, -87.18) * mm});
            skLineSegment(sketch, "E5455", {"start": v(-63.23, -87.18) * mm, "end": v(-63.04, -87.4) * mm});
            skLineSegment(sketch, "E5456", {"start": v(-63.04, -87.4) * mm, "end": v(-62.78, -87.65) * mm});
            skLineSegment(sketch, "E5457", {"start": v(-62.78, -87.65) * mm, "end": v(-62.47, -87.92) * mm});
            skLineSegment(sketch, "E5458", {"start": v(-62.47, -87.92) * mm, "end": v(-62.1, -88.2) * mm});
            skLineSegment(sketch, "E5459", {"start": v(-62.1, -88.2) * mm, "end": v(-61.27, -88.72) * mm});
            skLineSegment(sketch, "E5460", {"start": v(-61.27, -88.72) * mm, "end": v(-60.3, -89.21) * mm});
            skArc(sketch, "E5461", {"start": v(-60.3, -89.21) * mm, "mid": v(-59.72, -88.78) * mm, "end": v(-59.16, -88.34) * mm});
            skLineSegment(sketch, "E5462", {"start": v(-60.63, -84.66) * mm, "end": v(-60.36, -84.98) * mm});
            skLineSegment(sketch, "E5463", {"start": v(-60.36, -84.98) * mm, "end": v(-60.2, -85.22) * mm});
            skLineSegment(sketch, "E5464", {"start": v(-60.2, -85.22) * mm, "end": v(-60.02, -85.54) * mm});
            skLineSegment(sketch, "E5465", {"start": v(-60.02, -85.54) * mm, "end": v(-59.85, -85.9) * mm});
            skLineSegment(sketch, "E5466", {"start": v(-59.85, -85.9) * mm, "end": v(-59.68, -86.33) * mm});
            skLineSegment(sketch, "E5467", {"start": v(-59.68, -86.33) * mm, "end": v(-59.38, -87.27) * mm});
            skLineSegment(sketch, "E5468", {"start": v(-59.38, -87.27) * mm, "end": v(-59.16, -88.34) * mm});
            skArc(sketch, "E5469", {"start": v(-60.6, -83.6) * mm, "mid": v(-60.83, -84.13) * mm, "end": v(-60.63, -84.66) * mm});
            skArc(sketch, "E5470", {"start": v(-60.6, -83.6) * mm, "mid": v(-60.35, -83.36) * mm, "end": v(-60.1, -83.11) * mm});
            skArc(sketch, "E5471", {"start": v(-59.04, -83.08) * mm, "mid": v(-59.58, -82.88) * mm, "end": v(-60.1, -83.11) * mm});
            skLineSegment(sketch, "E5472", {"start": v(-59.04, -83.08) * mm, "end": v(-58.73, -83.35) * mm});
            skLineSegment(sketch, "E5473", {"start": v(-58.73, -83.35) * mm, "end": v(-58.49, -83.5) * mm});
            skLineSegment(sketch, "E5474", {"start": v(-58.49, -83.5) * mm, "end": v(-58.17, -83.68) * mm});
            skLineSegment(sketch, "E5475", {"start": v(-58.17, -83.68) * mm, "end": v(-57.8, -83.86) * mm});
            skLineSegment(sketch, "E5476", {"start": v(-57.8, -83.86) * mm, "end": v(-57.38, -84.03) * mm});
            skLineSegment(sketch, "E5477", {"start": v(-57.38, -84.03) * mm, "end": v(-56.43, -84.32) * mm});
            skLineSegment(sketch, "E5478", {"start": v(-56.43, -84.32) * mm, "end": v(-55.36, -84.55) * mm});
            skArc(sketch, "E5479", {"start": v(-55.36, -84.55) * mm, "mid": v(-54.92, -83.99) * mm, "end": v(-54.5, -83.41) * mm});
            skLineSegment(sketch, "E5480", {"start": v(-56.87, -80.24) * mm, "end": v(-56.52, -80.47) * mm});
            skLineSegment(sketch, "E5481", {"start": v(-56.52, -80.47) * mm, "end": v(-56.3, -80.67) * mm});
            skLineSegment(sketch, "E5482", {"start": v(-56.3, -80.67) * mm, "end": v(-56.05, -80.93) * mm});
            skLineSegment(sketch, "E5483", {"start": v(-56.05, -80.93) * mm, "end": v(-55.79, -81.24) * mm});
            skLineSegment(sketch, "E5484", {"start": v(-55.79, -81.24) * mm, "end": v(-55.51, -81.6) * mm});
            skLineSegment(sketch, "E5485", {"start": v(-55.51, -81.6) * mm, "end": v(-54.99, -82.44) * mm});
            skLineSegment(sketch, "E5486", {"start": v(-54.99, -82.44) * mm, "end": v(-54.5, -83.41) * mm});
            skArc(sketch, "E5487", {"start": v(-57.1, -79.2) * mm, "mid": v(-57.2, -79.77) * mm, "end": v(-56.87, -80.24) * mm});
            skArc(sketch, "E5488", {"start": v(-57.1, -79.2) * mm, "mid": v(-56.93, -78.9) * mm, "end": v(-56.76, -78.6) * mm});
            skArc(sketch, "E5489", {"start": v(-55.74, -78.3) * mm, "mid": v(-56.31, -78.25) * mm, "end": v(-56.76, -78.6) * mm});
            skLineSegment(sketch, "E5490", {"start": v(-55.74, -78.3) * mm, "end": v(-55.37, -78.48) * mm});
            skLineSegment(sketch, "E5491", {"start": v(-55.37, -78.48) * mm, "end": v(-55.1, -78.57) * mm});
            skLineSegment(sketch, "E5492", {"start": v(-55.1, -78.57) * mm, "end": v(-54.74, -78.66) * mm});
            skLineSegment(sketch, "E5493", {"start": v(-54.74, -78.66) * mm, "end": v(-54.34, -78.73) * mm});
            skLineSegment(sketch, "E5494", {"start": v(-54.34, -78.73) * mm, "end": v(-53.89, -78.79) * mm});
            skLineSegment(sketch, "E5495", {"start": v(-53.89, -78.79) * mm, "end": v(-52.9, -78.83) * mm});
            skLineSegment(sketch, "E5496", {"start": v(-52.9, -78.83) * mm, "end": v(-51.81, -78.76) * mm});
            skArc(sketch, "E5497", {"start": v(-51.81, -78.76) * mm, "mid": v(-51.53, -78.1) * mm, "end": v(-51.26, -77.44) * mm});
            skLineSegment(sketch, "E5498", {"start": v(-54.38, -75) * mm, "end": v(-53.99, -75.13) * mm});
            skLineSegment(sketch, "E5499", {"start": v(-53.99, -75.13) * mm, "end": v(-53.72, -75.26) * mm});
            skLineSegment(sketch, "E5500", {"start": v(-53.72, -75.26) * mm, "end": v(-53.41, -75.44) * mm});
            skLineSegment(sketch, "E5501", {"start": v(-53.41, -75.44) * mm, "end": v(-53.07, -75.68) * mm});
            skLineSegment(sketch, "E5502", {"start": v(-53.07, -75.68) * mm, "end": v(-52.72, -75.96) * mm});
            skLineSegment(sketch, "E5503", {"start": v(-52.72, -75.96) * mm, "end": v(-52, -76.63) * mm});
            skLineSegment(sketch, "E5504", {"start": v(-52, -76.63) * mm, "end": v(-51.26, -77.44) * mm});
            skArc(sketch, "E5505", {"start": v(-54.87, -74.06) * mm, "mid": v(-54.81, -74.63) * mm, "end": v(-54.38, -75) * mm});
            skArc(sketch, "E5506", {"start": v(-54.87, -74.06) * mm, "mid": v(-54.78, -73.72) * mm, "end": v(-54.7, -73.39) * mm});
            skArc(sketch, "E5507", {"start": v(-53.8, -72.83) * mm, "mid": v(-54.36, -72.92) * mm, "end": v(-54.7, -73.39) * mm});
            skLineSegment(sketch, "E5508", {"start": v(-53.8, -72.83) * mm, "end": v(-53.39, -72.9) * mm});
            skLineSegment(sketch, "E5509", {"start": v(-53.39, -72.9) * mm, "end": v(-53.1, -72.92) * mm});
            skLineSegment(sketch, "E5510", {"start": v(-53.1, -72.92) * mm, "end": v(-52.74, -72.92) * mm});
            skLineSegment(sketch, "E5511", {"start": v(-52.74, -72.92) * mm, "end": v(-52.32, -72.88) * mm});
            skLineSegment(sketch, "E5512", {"start": v(-52.32, -72.88) * mm, "end": v(-51.88, -72.82) * mm});
            skLineSegment(sketch, "E5513", {"start": v(-51.88, -72.82) * mm, "end": v(-50.91, -72.6) * mm});
            skLineSegment(sketch, "E5514", {"start": v(-50.91, -72.6) * mm, "end": v(-49.88, -72.26) * mm});
            skArc(sketch, "E5515", {"start": v(-49.88, -72.26) * mm, "mid": v(-49.77, -71.55) * mm, "end": v(-49.69, -70.84) * mm});
            skLineSegment(sketch, "E5516", {"start": v(-53.33, -69.28) * mm, "end": v(-52.92, -69.31) * mm});
            skLineSegment(sketch, "E5517", {"start": v(-52.92, -69.31) * mm, "end": v(-52.63, -69.37) * mm});
            skLineSegment(sketch, "E5518", {"start": v(-52.63, -69.37) * mm, "end": v(-52.28, -69.47) * mm});
            skLineSegment(sketch, "E5519", {"start": v(-52.28, -69.47) * mm, "end": v(-51.9, -69.6) * mm});
            skLineSegment(sketch, "E5520", {"start": v(-51.9, -69.6) * mm, "end": v(-51.48, -69.78) * mm});
            skLineSegment(sketch, "E5521", {"start": v(-51.48, -69.78) * mm, "end": v(-50.6, -70.24) * mm});
            skLineSegment(sketch, "E5522", {"start": v(-50.6, -70.24) * mm, "end": v(-49.69, -70.84) * mm});
            skArc(sketch, "E5523", {"start": v(-54.05, -68.5) * mm, "mid": v(-53.85, -69.04) * mm, "end": v(-53.33, -69.28) * mm});
            skArc(sketch, "E5524", {"start": v(-54.05, -68.5) * mm, "mid": v(-54.05, -68.16) * mm, "end": v(-54.05, -67.81) * mm});
            skArc(sketch, "E5525", {"start": v(-53.33, -67.04) * mm, "mid": v(-53.85, -67.28) * mm, "end": v(-54.05, -67.81) * mm});
            skLineSegment(sketch, "E5526", {"start": v(-53.33, -67.04) * mm, "end": v(-52.92, -67) * mm});
            skLineSegment(sketch, "E5527", {"start": v(-52.92, -67) * mm, "end": v(-52.63, -66.95) * mm});
            skLineSegment(sketch, "E5528", {"start": v(-52.63, -66.95) * mm, "end": v(-52.28, -66.85) * mm});
            skLineSegment(sketch, "E5529", {"start": v(-52.28, -66.85) * mm, "end": v(-51.9, -66.7) * mm});
            skLineSegment(sketch, "E5530", {"start": v(-51.9, -66.7) * mm, "end": v(-51.48, -66.53) * mm});
            skLineSegment(sketch, "E5531", {"start": v(-51.48, -66.53) * mm, "end": v(-50.6, -66.07) * mm});
            skLineSegment(sketch, "E5532", {"start": v(-50.6, -66.07) * mm, "end": v(-49.69, -65.47) * mm});
            skArc(sketch, "E5533", {"start": v(-49.69, -65.47) * mm, "mid": v(-49.77, -64.76) * mm, "end": v(-49.88, -64.06) * mm});
            skLineSegment(sketch, "E5534", {"start": v(-53.8, -63.5) * mm, "end": v(-53.39, -63.41) * mm});
            skLineSegment(sketch, "E5535", {"start": v(-53.39, -63.41) * mm, "end": v(-53.1, -63.4) * mm});
            skLineSegment(sketch, "E5536", {"start": v(-53.1, -63.4) * mm, "end": v(-52.74, -63.4) * mm});
            skLineSegment(sketch, "E5537", {"start": v(-52.74, -63.4) * mm, "end": v(-52.32, -63.43) * mm});
            skLineSegment(sketch, "E5538", {"start": v(-52.32, -63.43) * mm, "end": v(-51.88, -63.5) * mm});
            skLineSegment(sketch, "E5539", {"start": v(-51.88, -63.5) * mm, "end": v(-50.91, -63.71) * mm});
            skLineSegment(sketch, "E5540", {"start": v(-50.91, -63.71) * mm, "end": v(-49.88, -64.06) * mm});
            skArc(sketch, "E5541", {"start": v(-54.7, -62.93) * mm, "mid": v(-54.36, -63.4) * mm, "end": v(-53.8, -63.5) * mm});
            skArc(sketch, "E5542", {"start": v(-54.7, -62.93) * mm, "mid": v(-54.78, -62.6) * mm, "end": v(-54.87, -62.26) * mm});
            skArc(sketch, "E5543", {"start": v(-54.38, -61.32) * mm, "mid": v(-54.81, -61.7) * mm, "end": v(-54.87, -62.26) * mm});
            skLineSegment(sketch, "E5544", {"start": v(-54.38, -61.32) * mm, "end": v(-53.99, -61.19) * mm});
            skLineSegment(sketch, "E5545", {"start": v(-53.99, -61.19) * mm, "end": v(-53.72, -61.06) * mm});
            skLineSegment(sketch, "E5546", {"start": v(-53.72, -61.06) * mm, "end": v(-53.41, -60.87) * mm});
            skLineSegment(sketch, "E5547", {"start": v(-53.41, -60.87) * mm, "end": v(-53.07, -60.64) * mm});
            skLineSegment(sketch, "E5548", {"start": v(-53.07, -60.64) * mm, "end": v(-52.72, -60.36) * mm});
            skLineSegment(sketch, "E5549", {"start": v(-52.72, -60.36) * mm, "end": v(-52, -59.69) * mm});
            skLineSegment(sketch, "E5550", {"start": v(-52, -59.69) * mm, "end": v(-51.26, -58.87) * mm});
            skArc(sketch, "E5551", {"start": v(-51.26, -58.87) * mm, "mid": v(-51.53, -58.2) * mm, "end": v(-51.81, -57.55) * mm});
            skLineSegment(sketch, "E5552", {"start": v(-55.74, -58.02) * mm, "end": v(-55.37, -57.84) * mm});
            skLineSegment(sketch, "E5553", {"start": v(-55.37, -57.84) * mm, "end": v(-55.1, -57.75) * mm});
            skLineSegment(sketch, "E5554", {"start": v(-55.1, -57.75) * mm, "end": v(-54.74, -57.66) * mm});
            skLineSegment(sketch, "E5555", {"start": v(-54.74, -57.66) * mm, "end": v(-54.34, -57.58) * mm});
            skLineSegment(sketch, "E5556", {"start": v(-54.34, -57.58) * mm, "end": v(-53.89, -57.53) * mm});
            skLineSegment(sketch, "E5557", {"start": v(-53.89, -57.53) * mm, "end": v(-52.9, -57.49) * mm});
            skLineSegment(sketch, "E5558", {"start": v(-52.9, -57.49) * mm, "end": v(-51.81, -57.55) * mm});
            skArc(sketch, "E5559", {"start": v(-56.76, -57.7) * mm, "mid": v(-56.31, -58.07) * mm, "end": v(-55.74, -58.02) * mm});
            skArc(sketch, "E5560", {"start": v(-56.76, -57.7) * mm, "mid": v(-56.93, -57.4) * mm, "end": v(-57.1, -57.1) * mm});
            skArc(sketch, "E5561", {"start": v(-56.87, -56.08) * mm, "mid": v(-57.2, -56.54) * mm, "end": v(-57.1, -57.1) * mm});
            skLineSegment(sketch, "E5562", {"start": v(-56.87, -56.08) * mm, "end": v(-56.52, -55.84) * mm});
            skLineSegment(sketch, "E5563", {"start": v(-56.52, -55.84) * mm, "end": v(-56.3, -55.65) * mm});
            skLineSegment(sketch, "E5564", {"start": v(-56.3, -55.65) * mm, "end": v(-56.05, -55.4) * mm});
            skLineSegment(sketch, "E5565", {"start": v(-56.05, -55.4) * mm, "end": v(-55.79, -55.08) * mm});
            skLineSegment(sketch, "E5566", {"start": v(-55.79, -55.08) * mm, "end": v(-55.51, -54.71) * mm});
            skLineSegment(sketch, "E5567", {"start": v(-55.51, -54.71) * mm, "end": v(-54.99, -53.88) * mm});
            skLineSegment(sketch, "E5568", {"start": v(-54.99, -53.88) * mm, "end": v(-54.5, -52.9) * mm});
            skArc(sketch, "E5569", {"start": v(-54.5, -52.9) * mm, "mid": v(-54.92, -52.33) * mm, "end": v(-55.36, -51.77) * mm});
            skLineSegment(sketch, "E5570", {"start": v(-59.04, -53.24) * mm, "end": v(-58.73, -52.97) * mm});
            skLineSegment(sketch, "E5571", {"start": v(-58.73, -52.97) * mm, "end": v(-58.49, -52.8) * mm});
            skLineSegment(sketch, "E5572", {"start": v(-58.49, -52.8) * mm, "end": v(-58.17, -52.63) * mm});
            skLineSegment(sketch, "E5573", {"start": v(-58.17, -52.63) * mm, "end": v(-57.8, -52.45) * mm});
            skLineSegment(sketch, "E5574", {"start": v(-57.8, -52.45) * mm, "end": v(-57.38, -52.28) * mm});
            skLineSegment(sketch, "E5575", {"start": v(-57.38, -52.28) * mm, "end": v(-56.43, -52) * mm});
            skLineSegment(sketch, "E5576", {"start": v(-56.43, -52) * mm, "end": v(-55.36, -51.77) * mm});
            skArc(sketch, "E5577", {"start": v(-60.1, -53.2) * mm, "mid": v(-59.58, -53.43) * mm, "end": v(-59.04, -53.24) * mm});
            skArc(sketch, "E5578", {"start": v(-60.1, -53.2) * mm, "mid": v(-60.35, -52.96) * mm, "end": v(-60.6, -52.71) * mm});
            skArc(sketch, "E5579", {"start": v(-60.63, -51.65) * mm, "mid": v(-60.83, -52.19) * mm, "end": v(-60.6, -52.71) * mm});
            skLineSegment(sketch, "E5580", {"start": v(-60.63, -51.65) * mm, "end": v(-60.36, -51.34) * mm});
            skLineSegment(sketch, "E5581", {"start": v(-60.36, -51.34) * mm, "end": v(-60.2, -51.1) * mm});
            skLineSegment(sketch, "E5582", {"start": v(-60.2, -51.1) * mm, "end": v(-60.02, -50.78) * mm});
            skLineSegment(sketch, "E5583", {"start": v(-60.02, -50.78) * mm, "end": v(-59.85, -50.4) * mm});
            skLineSegment(sketch, "E5584", {"start": v(-59.85, -50.4) * mm, "end": v(-59.68, -49.99) * mm});
            skLineSegment(sketch, "E5585", {"start": v(-59.68, -49.99) * mm, "end": v(-59.38, -49.04) * mm});
            skLineSegment(sketch, "E5586", {"start": v(-59.38, -49.04) * mm, "end": v(-59.16, -47.97) * mm});
            skArc(sketch, "E5587", {"start": v(-59.16, -47.97) * mm, "mid": v(-59.72, -47.53) * mm, "end": v(-60.3, -47.1) * mm});
            skLineSegment(sketch, "E5588", {"start": v(-63.47, -49.47) * mm, "end": v(-63.23, -49.13) * mm});
            skLineSegment(sketch, "E5589", {"start": v(-63.23, -49.13) * mm, "end": v(-63.04, -48.91) * mm});
            skLineSegment(sketch, "E5590", {"start": v(-63.04, -48.91) * mm, "end": v(-62.78, -48.66) * mm});
            skLineSegment(sketch, "E5591", {"start": v(-62.78, -48.66) * mm, "end": v(-62.47, -48.4) * mm});
            skLineSegment(sketch, "E5592", {"start": v(-62.47, -48.4) * mm, "end": v(-62.1, -48.12) * mm});
            skLineSegment(sketch, "E5593", {"start": v(-62.1, -48.12) * mm, "end": v(-61.27, -47.6) * mm});
            skLineSegment(sketch, "E5594", {"start": v(-61.27, -47.6) * mm, "end": v(-60.3, -47.1) * mm});
            skArc(sketch, "E5595", {"start": v(-64.5, -49.71) * mm, "mid": v(-63.94, -49.8) * mm, "end": v(-63.47, -49.47) * mm});
            skArc(sketch, "E5596", {"start": v(-64.5, -49.71) * mm, "mid": v(-64.8, -49.54) * mm, "end": v(-65.1, -49.37) * mm});
            skArc(sketch, "E5597", {"start": v(-65.41, -48.35) * mm, "mid": v(-65.46, -48.92) * mm, "end": v(-65.1, -49.37) * mm});
            skLineSegment(sketch, "E5598", {"start": v(-65.41, -48.35) * mm, "end": v(-65.23, -47.98) * mm});
            skLineSegment(sketch, "E5599", {"start": v(-65.23, -47.98) * mm, "end": v(-65.14, -47.7) * mm});
            skLineSegment(sketch, "E5600", {"start": v(-65.14, -47.7) * mm, "end": v(-65.05, -47.35) * mm});
            skLineSegment(sketch, "E5601", {"start": v(-65.05, -47.35) * mm, "end": v(-64.98, -46.95) * mm});
            skLineSegment(sketch, "E5602", {"start": v(-64.98, -46.95) * mm, "end": v(-64.92, -46.5) * mm});
            skLineSegment(sketch, "E5603", {"start": v(-64.92, -46.5) * mm, "end": v(-64.88, -45.51) * mm});
            skLineSegment(sketch, "E5604", {"start": v(-64.88, -45.51) * mm, "end": v(-64.94, -44.42) * mm});
            skArc(sketch, "E5605", {"start": v(-64.94, -44.42) * mm, "mid": v(-65.6, -44.14) * mm, "end": v(-66.26, -43.87) * mm});
            skLineSegment(sketch, "E5606", {"start": v(-68.71, -46.98) * mm, "end": v(-68.58, -46.6) * mm});
            skLineSegment(sketch, "E5607", {"start": v(-68.58, -46.6) * mm, "end": v(-68.45, -46.33) * mm});
            skLineSegment(sketch, "E5608", {"start": v(-68.45, -46.33) * mm, "end": v(-68.26, -46.02) * mm});
            skLineSegment(sketch, "E5609", {"start": v(-68.26, -46.02) * mm, "end": v(-68.03, -45.68) * mm});
            skLineSegment(sketch, "E5610", {"start": v(-68.03, -45.68) * mm, "end": v(-67.75, -45.32) * mm});
            skLineSegment(sketch, "E5611", {"start": v(-67.75, -45.32) * mm, "end": v(-67.08, -44.6) * mm});
            skLineSegment(sketch, "E5612", {"start": v(-67.08, -44.6) * mm, "end": v(-66.26, -43.87) * mm});
            skArc(sketch, "E5613", {"start": v(-69.65, -47.48) * mm, "mid": v(-69.08, -47.42) * mm, "end": v(-68.71, -46.98) * mm});
            skArc(sketch, "E5614", {"start": v(-69.65, -47.48) * mm, "mid": v(-69.99, -47.4) * mm, "end": v(-70.32, -47.3) * mm});
            skArc(sketch, "E5615", {"start": v(-70.88, -46.4) * mm, "mid": v(-70.78, -46.97) * mm, "end": v(-70.32, -47.3) * mm});
            skLineSegment(sketch, "E5616", {"start": v(-70.88, -46.4) * mm, "end": v(-70.8, -46) * mm});
            skLineSegment(sketch, "E5617", {"start": v(-70.8, -46) * mm, "end": v(-70.79, -45.7) * mm});
            skLineSegment(sketch, "E5618", {"start": v(-70.79, -45.7) * mm, "end": v(-70.8, -45.34) * mm});
            skLineSegment(sketch, "E5619", {"start": v(-70.8, -45.34) * mm, "end": v(-70.83, -44.93) * mm});
            skLineSegment(sketch, "E5620", {"start": v(-70.83, -44.93) * mm, "end": v(-70.89, -44.48) * mm});
            skLineSegment(sketch, "E5621", {"start": v(-70.89, -44.48) * mm, "end": v(-71.1, -43.52) * mm});
            skLineSegment(sketch, "E5622", {"start": v(-71.1, -43.52) * mm, "end": v(-71.45, -42.48) * mm});
            skArc(sketch, "E5623", {"start": v(-71.45, -42.48) * mm, "mid": v(-72.16, -42.38) * mm, "end": v(-72.87, -42.3) * mm});
            skLineSegment(sketch, "E5624", {"start": v(-74.43, -45.94) * mm, "end": v(-74.4, -45.52) * mm});
            skLineSegment(sketch, "E5625", {"start": v(-74.4, -45.52) * mm, "end": v(-74.34, -45.24) * mm});
            skLineSegment(sketch, "E5626", {"start": v(-74.34, -45.24) * mm, "end": v(-74.24, -44.9) * mm});
            skLineSegment(sketch, "E5627", {"start": v(-74.24, -44.9) * mm, "end": v(-74.1, -44.5) * mm});
            skLineSegment(sketch, "E5628", {"start": v(-74.1, -44.5) * mm, "end": v(-73.92, -44.08) * mm});
            skLineSegment(sketch, "E5629", {"start": v(-73.92, -44.08) * mm, "end": v(-73.46, -43.21) * mm});
            skLineSegment(sketch, "E5630", {"start": v(-73.46, -43.21) * mm, "end": v(-72.87, -42.3) * mm});
            skArc(sketch, "E5631", {"start": v(-75.2, -46.66) * mm, "mid": v(-74.67, -46.45) * mm, "end": v(-74.43, -45.94) * mm});
            skArc(sketch, "E5632", {"start": v(-75.2, -46.66) * mm, "mid": v(-75.55, -46.66) * mm, "end": v(-75.9, -46.66) * mm});
            skArc(sketch, "E5633", {"start": v(-76.67, -45.94) * mm, "mid": v(-76.43, -46.45) * mm, "end": v(-75.9, -46.66) * mm});
            skLineSegment(sketch, "E5634", {"start": v(-76.67, -45.94) * mm, "end": v(-76.7, -45.52) * mm});
            skLineSegment(sketch, "E5635", {"start": v(-76.7, -45.52) * mm, "end": v(-76.76, -45.24) * mm});
            skLineSegment(sketch, "E5636", {"start": v(-76.76, -45.24) * mm, "end": v(-76.86, -44.9) * mm});
            skLineSegment(sketch, "E5637", {"start": v(-76.86, -44.9) * mm, "end": v(-77, -44.5) * mm});
            skLineSegment(sketch, "E5638", {"start": v(-77, -44.5) * mm, "end": v(-77.18, -44.08) * mm});
            skLineSegment(sketch, "E5639", {"start": v(-77.18, -44.08) * mm, "end": v(-77.63, -43.21) * mm});
            skLineSegment(sketch, "E5640", {"start": v(-77.63, -43.21) * mm, "end": v(-78.23, -42.3) * mm});
            skArc(sketch, "E5641", {"start": v(-78.23, -42.3) * mm, "mid": v(-78.94, -42.38) * mm, "end": v(-79.65, -42.48) * mm});
            skLineSegment(sketch, "E5642", {"start": v(-80.22, -46.4) * mm, "end": v(-80.3, -46) * mm});
            skLineSegment(sketch, "E5643", {"start": v(-80.3, -46) * mm, "end": v(-80.31, -45.7) * mm});
            skLineSegment(sketch, "E5644", {"start": v(-80.31, -45.7) * mm, "end": v(-80.3, -45.34) * mm});
            skLineSegment(sketch, "E5645", {"start": v(-80.3, -45.34) * mm, "end": v(-80.27, -44.93) * mm});
            skLineSegment(sketch, "E5646", {"start": v(-80.27, -44.93) * mm, "end": v(-80.2, -44.48) * mm});
            skLineSegment(sketch, "E5647", {"start": v(-80.2, -44.48) * mm, "end": v(-80, -43.52) * mm});
            skLineSegment(sketch, "E5648", {"start": v(-80, -43.52) * mm, "end": v(-79.65, -42.48) * mm});
            skArc(sketch, "E5649", {"start": v(-80.78, -47.3) * mm, "mid": v(-80.32, -46.97) * mm, "end": v(-80.22, -46.4) * mm});
            skArc(sketch, "E5650", {"start": v(-80.78, -47.3) * mm, "mid": v(-81.11, -47.4) * mm, "end": v(-81.45, -47.48) * mm});
            skArc(sketch, "E5651", {"start": v(-82.38, -46.98) * mm, "mid": v(-82.02, -47.42) * mm, "end": v(-81.45, -47.48) * mm});
            skLineSegment(sketch, "E5652", {"start": v(-82.38, -46.98) * mm, "end": v(-82.52, -46.6) * mm});
            skLineSegment(sketch, "E5653", {"start": v(-82.52, -46.6) * mm, "end": v(-82.65, -46.33) * mm});
            skLineSegment(sketch, "E5654", {"start": v(-82.65, -46.33) * mm, "end": v(-82.84, -46.02) * mm});
            skLineSegment(sketch, "E5655", {"start": v(-82.84, -46.02) * mm, "end": v(-83.07, -45.68) * mm});
            skLineSegment(sketch, "E5656", {"start": v(-83.07, -45.68) * mm, "end": v(-83.35, -45.32) * mm});
            skLineSegment(sketch, "E5657", {"start": v(-83.35, -45.32) * mm, "end": v(-84.02, -44.6) * mm});
            skLineSegment(sketch, "E5658", {"start": v(-84.02, -44.6) * mm, "end": v(-84.84, -43.87) * mm});
            skArc(sketch, "E5659", {"start": v(-84.84, -43.87) * mm, "mid": v(-85.5, -44.14) * mm, "end": v(-86.16, -44.42) * mm});
            skLineSegment(sketch, "E5660", {"start": v(-85.69, -48.35) * mm, "end": v(-85.87, -47.98) * mm});
            skLineSegment(sketch, "E5661", {"start": v(-85.87, -47.98) * mm, "end": v(-85.96, -47.7) * mm});
            skLineSegment(sketch, "E5662", {"start": v(-85.96, -47.7) * mm, "end": v(-86.05, -47.35) * mm});
            skLineSegment(sketch, "E5663", {"start": v(-86.05, -47.35) * mm, "end": v(-86.12, -46.95) * mm});
            skLineSegment(sketch, "E5664", {"start": v(-86.12, -46.95) * mm, "end": v(-86.18, -46.5) * mm});
            skLineSegment(sketch, "E5665", {"start": v(-86.18, -46.5) * mm, "end": v(-86.22, -45.51) * mm});
            skLineSegment(sketch, "E5666", {"start": v(-86.22, -45.51) * mm, "end": v(-86.16, -44.42) * mm});
            skArc(sketch, "E5667", {"start": v(-86, -49.37) * mm, "mid": v(-85.64, -48.92) * mm, "end": v(-85.69, -48.35) * mm});
            skArc(sketch, "E5668", {"start": v(-86, -49.37) * mm, "mid": v(-86.3, -49.54) * mm, "end": v(-86.6, -49.71) * mm});
            skArc(sketch, "E5669", {"start": v(-87.63, -49.47) * mm, "mid": v(-87.16, -49.8) * mm, "end": v(-86.6, -49.71) * mm});
            skLineSegment(sketch, "E5670", {"start": v(-87.63, -49.47) * mm, "end": v(-87.86, -49.13) * mm});
            skLineSegment(sketch, "E5671", {"start": v(-87.86, -49.13) * mm, "end": v(-88.06, -48.91) * mm});
            skLineSegment(sketch, "E5672", {"start": v(-88.06, -48.91) * mm, "end": v(-88.32, -48.66) * mm});
            skLineSegment(sketch, "E5673", {"start": v(-88.32, -48.66) * mm, "end": v(-88.63, -48.4) * mm});
            skLineSegment(sketch, "E5674", {"start": v(-88.63, -48.4) * mm, "end": v(-89, -48.12) * mm});
            skLineSegment(sketch, "E5675", {"start": v(-89, -48.12) * mm, "end": v(-89.83, -47.6) * mm});
            skLineSegment(sketch, "E5676", {"start": v(-89.83, -47.6) * mm, "end": v(-90.8, -47.1) * mm});
            skArc(sketch, "E5677", {"start": v(-90.8, -47.1) * mm, "mid": v(-91.38, -47.53) * mm, "end": v(-91.94, -47.97) * mm});
            skLineSegment(sketch, "E5678", {"start": v(-90.47, -51.65) * mm, "end": v(-90.74, -51.34) * mm});
            skLineSegment(sketch, "E5679", {"start": v(-90.74, -51.34) * mm, "end": v(-90.9, -51.1) * mm});
            skLineSegment(sketch, "E5680", {"start": v(-90.9, -51.1) * mm, "end": v(-91.08, -50.78) * mm});
            skLineSegment(sketch, "E5681", {"start": v(-91.08, -50.78) * mm, "end": v(-91.25, -50.4) * mm});
            skLineSegment(sketch, "E5682", {"start": v(-91.25, -50.4) * mm, "end": v(-91.42, -49.99) * mm});
            skLineSegment(sketch, "E5683", {"start": v(-91.42, -49.99) * mm, "end": v(-91.72, -49.04) * mm});
            skLineSegment(sketch, "E5684", {"start": v(-91.72, -49.04) * mm, "end": v(-91.94, -47.97) * mm});
            skArc(sketch, "E5685", {"start": v(-90.5, -52.71) * mm, "mid": v(-90.27, -52.19) * mm, "end": v(-90.47, -51.65) * mm});
            skArc(sketch, "E5686", {"start": v(-90.5, -52.71) * mm, "mid": v(-90.75, -52.96) * mm, "end": v(-91, -53.2) * mm});
            skArc(sketch, "E5687", {"start": v(-92.06, -53.24) * mm, "mid": v(-91.52, -53.43) * mm, "end": v(-91, -53.2) * mm});
            skLineSegment(sketch, "E5688", {"start": v(-92.06, -53.24) * mm, "end": v(-92.37, -52.97) * mm});
            skLineSegment(sketch, "E5689", {"start": v(-92.37, -52.97) * mm, "end": v(-92.61, -52.8) * mm});
            skLineSegment(sketch, "E5690", {"start": v(-92.61, -52.8) * mm, "end": v(-92.93, -52.63) * mm});
            skLineSegment(sketch, "E5691", {"start": v(-92.93, -52.63) * mm, "end": v(-93.3, -52.45) * mm});
            skLineSegment(sketch, "E5692", {"start": v(-93.3, -52.45) * mm, "end": v(-93.72, -52.28) * mm});
            skLineSegment(sketch, "E5693", {"start": v(-93.72, -52.28) * mm, "end": v(-94.66, -52) * mm});
            skLineSegment(sketch, "E5694", {"start": v(-94.66, -52) * mm, "end": v(-95.73, -51.77) * mm});
            skArc(sketch, "E5695", {"start": v(-95.73, -51.77) * mm, "mid": v(-96.18, -52.33) * mm, "end": v(-96.6, -52.9) * mm});
            skLineSegment(sketch, "E5696", {"start": v(-94.23, -56.08) * mm, "end": v(-94.58, -55.84) * mm});
            skLineSegment(sketch, "E5697", {"start": v(-94.58, -55.84) * mm, "end": v(-94.8, -55.65) * mm});
            skLineSegment(sketch, "E5698", {"start": v(-94.8, -55.65) * mm, "end": v(-95.05, -55.4) * mm});
            skLineSegment(sketch, "E5699", {"start": v(-95.05, -55.4) * mm, "end": v(-95.31, -55.08) * mm});
            skLineSegment(sketch, "E5700", {"start": v(-95.31, -55.08) * mm, "end": v(-95.59, -54.71) * mm});
            skLineSegment(sketch, "E5701", {"start": v(-95.59, -54.71) * mm, "end": v(-96.11, -53.88) * mm});
            skLineSegment(sketch, "E5702", {"start": v(-96.11, -53.88) * mm, "end": v(-96.6, -52.9) * mm});
            skArc(sketch, "E5703", {"start": v(-94, -57.1) * mm, "mid": v(-93.9, -56.54) * mm, "end": v(-94.23, -56.08) * mm});
            skArc(sketch, "E5704", {"start": v(-94, -57.1) * mm, "mid": v(-94.17, -57.4) * mm, "end": v(-94.34, -57.7) * mm});
            skArc(sketch, "E5705", {"start": v(-95.36, -58.02) * mm, "mid": v(-94.79, -58.07) * mm, "end": v(-94.34, -57.7) * mm});
            skLineSegment(sketch, "E5706", {"start": v(-95.36, -58.02) * mm, "end": v(-95.73, -57.84) * mm});
            skLineSegment(sketch, "E5707", {"start": v(-95.73, -57.84) * mm, "end": v(-96, -57.75) * mm});
            skLineSegment(sketch, "E5708", {"start": v(-96, -57.75) * mm, "end": v(-96.35, -57.66) * mm});
            skLineSegment(sketch, "E5709", {"start": v(-96.35, -57.66) * mm, "end": v(-96.76, -57.58) * mm});
            skLineSegment(sketch, "E5710", {"start": v(-96.76, -57.58) * mm, "end": v(-97.21, -57.53) * mm});
            skLineSegment(sketch, "E5711", {"start": v(-97.21, -57.53) * mm, "end": v(-98.2, -57.49) * mm});
            skLineSegment(sketch, "E5712", {"start": v(-98.2, -57.49) * mm, "end": v(-99.29, -57.55) * mm});
            skArc(sketch, "E5713", {"start": v(-99.29, -57.55) * mm, "mid": v(-99.57, -58.2) * mm, "end": v(-99.83, -58.87) * mm});
            skLineSegment(sketch, "E5714", {"start": v(-96.72, -61.32) * mm, "end": v(-97.11, -61.19) * mm});
            skLineSegment(sketch, "E5715", {"start": v(-97.11, -61.19) * mm, "end": v(-97.37, -61.06) * mm});
            skLineSegment(sketch, "E5716", {"start": v(-97.37, -61.06) * mm, "end": v(-97.69, -60.87) * mm});
            skLineSegment(sketch, "E5717", {"start": v(-97.69, -60.87) * mm, "end": v(-98.03, -60.64) * mm});
            skLineSegment(sketch, "E5718", {"start": v(-98.03, -60.64) * mm, "end": v(-98.38, -60.36) * mm});
            skLineSegment(sketch, "E5719", {"start": v(-98.38, -60.36) * mm, "end": v(-99.1, -59.69) * mm});
            skLineSegment(sketch, "E5720", {"start": v(-99.1, -59.69) * mm, "end": v(-99.83, -58.87) * mm});
            skArc(sketch, "E5721", {"start": v(-96.22, -62.26) * mm, "mid": v(-96.29, -61.7) * mm, "end": v(-96.72, -61.32) * mm});
            skArc(sketch, "E5722", {"start": v(-96.22, -62.26) * mm, "mid": v(-96.32, -62.6) * mm, "end": v(-96.4, -62.93) * mm});
            skArc(sketch, "E5723", {"start": v(-97.3, -63.5) * mm, "mid": v(-96.74, -63.4) * mm, "end": v(-96.4, -62.93) * mm});
            skLineSegment(sketch, "E5724", {"start": v(-97.3, -63.5) * mm, "end": v(-97.71, -63.41) * mm});
            skLineSegment(sketch, "E5725", {"start": v(-97.71, -63.41) * mm, "end": v(-98, -63.4) * mm});
            skLineSegment(sketch, "E5726", {"start": v(-98, -63.4) * mm, "end": v(-98.36, -63.4) * mm});
            skLineSegment(sketch, "E5727", {"start": v(-98.36, -63.4) * mm, "end": v(-98.78, -63.43) * mm});
            skLineSegment(sketch, "E5728", {"start": v(-98.78, -63.43) * mm, "end": v(-99.22, -63.5) * mm});
            skLineSegment(sketch, "E5729", {"start": v(-99.22, -63.5) * mm, "end": v(-100.19, -63.71) * mm});
            skLineSegment(sketch, "E5730", {"start": v(-100.19, -63.71) * mm, "end": v(-101.22, -64.06) * mm});
            skArc(sketch, "E5731", {"start": v(-101.22, -64.06) * mm, "mid": v(-101.33, -64.76) * mm, "end": v(-101.41, -65.47) * mm});
            skLineSegment(sketch, "E5732", {"start": v(-97.77, -67.04) * mm, "end": v(-98.18, -67) * mm});
            skLineSegment(sketch, "E5733", {"start": v(-98.18, -67) * mm, "end": v(-98.47, -66.95) * mm});
            skLineSegment(sketch, "E5734", {"start": v(-98.47, -66.95) * mm, "end": v(-98.82, -66.85) * mm});
            skLineSegment(sketch, "E5735", {"start": v(-98.82, -66.85) * mm, "end": v(-99.2, -66.7) * mm});
            skLineSegment(sketch, "E5736", {"start": v(-99.2, -66.7) * mm, "end": v(-99.62, -66.53) * mm});
            skLineSegment(sketch, "E5737", {"start": v(-99.62, -66.53) * mm, "end": v(-100.5, -66.07) * mm});
            skLineSegment(sketch, "E5738", {"start": v(-100.5, -66.07) * mm, "end": v(-101.41, -65.47) * mm});
            skArc(sketch, "E5739", {"start": v(-97.05, -67.81) * mm, "mid": v(-97.25, -67.28) * mm, "end": v(-97.77, -67.04) * mm});
            skArc(sketch, "E5740", {"start": v(-97.05, -67.81) * mm, "mid": v(-97.05, -68.16) * mm, "end": v(-97.05, -68.5) * mm});
            skArc(sketch, "E5741", {"start": v(-97.77, -69.28) * mm, "mid": v(-97.25, -69.04) * mm, "end": v(-97.05, -68.5) * mm});
            skLineSegment(sketch, "E5742", {"start": v(-97.77, -69.28) * mm, "end": v(-98.18, -69.31) * mm});
            skLineSegment(sketch, "E5743", {"start": v(-98.18, -69.31) * mm, "end": v(-98.47, -69.37) * mm});
            skLineSegment(sketch, "E5744", {"start": v(-98.47, -69.37) * mm, "end": v(-98.82, -69.47) * mm});
            skLineSegment(sketch, "E5745", {"start": v(-98.82, -69.47) * mm, "end": v(-99.2, -69.6) * mm});
            skLineSegment(sketch, "E5746", {"start": v(-99.2, -69.6) * mm, "end": v(-99.62, -69.78) * mm});
            skLineSegment(sketch, "E5747", {"start": v(-99.62, -69.78) * mm, "end": v(-100.5, -70.24) * mm});
            skLineSegment(sketch, "E5748", {"start": v(-100.5, -70.24) * mm, "end": v(-101.41, -70.84) * mm});
            skArc(sketch, "E5749", {"start": v(-101.41, -70.84) * mm, "mid": v(-101.33, -71.55) * mm, "end": v(-101.22, -72.26) * mm});
            skLineSegment(sketch, "E5750", {"start": v(-97.3, -72.83) * mm, "end": v(-97.71, -72.9) * mm});
            skLineSegment(sketch, "E5751", {"start": v(-97.71, -72.9) * mm, "end": v(-98, -72.92) * mm});
            skLineSegment(sketch, "E5752", {"start": v(-98, -72.92) * mm, "end": v(-98.36, -72.92) * mm});
            skLineSegment(sketch, "E5753", {"start": v(-98.36, -72.92) * mm, "end": v(-98.78, -72.88) * mm});
            skLineSegment(sketch, "E5754", {"start": v(-98.78, -72.88) * mm, "end": v(-99.22, -72.82) * mm});
            skLineSegment(sketch, "E5755", {"start": v(-99.22, -72.82) * mm, "end": v(-100.19, -72.6) * mm});
            skLineSegment(sketch, "E5756", {"start": v(-100.19, -72.6) * mm, "end": v(-101.22, -72.26) * mm});
            skArc(sketch, "E5757", {"start": v(-96.4, -73.39) * mm, "mid": v(-96.74, -72.92) * mm, "end": v(-97.3, -72.83) * mm});
            skArc(sketch, "E5758", {"start": v(-96.4, -73.39) * mm, "mid": v(-96.32, -73.72) * mm, "end": v(-96.22, -74.06) * mm});
            skArc(sketch, "E5759", {"start": v(10.04, -15.16) * mm, "mid": v(10.3, -14.65) * mm, "end": v(10.11, -14.1) * mm});
            skLineSegment(sketch, "E5760", {"start": v(10.04, -15.16) * mm, "end": v(9.73, -15.45) * mm});
            skLineSegment(sketch, "E5761", {"start": v(9.73, -15.45) * mm, "end": v(9.6, -15.6) * mm});
            skLineSegment(sketch, "E5762", {"start": v(9.6, -15.6) * mm, "end": v(9.43, -15.83) * mm});
            skLineSegment(sketch, "E5763", {"start": v(9.43, -15.83) * mm, "end": v(9.26, -16.1) * mm});
            skLineSegment(sketch, "E5764", {"start": v(9.26, -16.1) * mm, "end": v(9.08, -16.4) * mm});
            skLineSegment(sketch, "E5765", {"start": v(9.08, -16.4) * mm, "end": v(8.91, -16.73) * mm});
            skLineSegment(sketch, "E5766", {"start": v(8.91, -16.73) * mm, "end": v(8.53, -17.63) * mm});
            skLineSegment(sketch, "E5767", {"start": v(8.53, -17.63) * mm, "end": v(8.22, -18.67) * mm});
            skArc(sketch, "E5768", {"start": v(8.22, -18.67) * mm, "mid": v(8.73, -19.16) * mm, "end": v(9.25, -19.64) * mm});
            skLineSegment(sketch, "E5769", {"start": v(12.63, -17.58) * mm, "end": v(12.36, -17.9) * mm});
            skLineSegment(sketch, "E5770", {"start": v(12.36, -17.9) * mm, "end": v(12.21, -18.05) * mm});
            skLineSegment(sketch, "E5771", {"start": v(12.21, -18.05) * mm, "end": v(12, -18.23) * mm});
            skLineSegment(sketch, "E5772", {"start": v(12, -18.23) * mm, "end": v(11.75, -18.42) * mm});
            skLineSegment(sketch, "E5773", {"start": v(11.75, -18.42) * mm, "end": v(11.46, -18.62) * mm});
            skLineSegment(sketch, "E5774", {"start": v(11.46, -18.62) * mm, "end": v(11.14, -18.81) * mm});
            skLineSegment(sketch, "E5775", {"start": v(11.14, -18.81) * mm, "end": v(10.26, -19.25) * mm});
            skLineSegment(sketch, "E5776", {"start": v(10.26, -19.25) * mm, "end": v(9.25, -19.64) * mm});
            skArc(sketch, "E5777", {"start": v(13.69, -17.43) * mm, "mid": v(13.13, -17.3) * mm, "end": v(12.63, -17.58) * mm});
            skArc(sketch, "E5778", {"start": v(13.69, -17.43) * mm, "mid": v(13.97, -17.64) * mm, "end": v(14.26, -17.84) * mm});
            skArc(sketch, "E5779", {"start": v(14.48, -18.88) * mm, "mid": v(14.58, -18.32) * mm, "end": v(14.26, -17.84) * mm});
            skLineSegment(sketch, "E5780", {"start": v(14.48, -18.88) * mm, "end": v(14.25, -19.25) * mm});
            skLineSegment(sketch, "E5781", {"start": v(14.25, -19.25) * mm, "end": v(14.17, -19.43) * mm});
            skLineSegment(sketch, "E5782", {"start": v(14.17, -19.43) * mm, "end": v(14.07, -19.69) * mm});
            skLineSegment(sketch, "E5783", {"start": v(14.07, -19.69) * mm, "end": v(13.97, -20) * mm});
            skLineSegment(sketch, "E5784", {"start": v(13.97, -20) * mm, "end": v(13.89, -20.33) * mm});
            skLineSegment(sketch, "E5785", {"start": v(13.89, -20.33) * mm, "end": v(13.81, -20.7) * mm});
            skLineSegment(sketch, "E5786", {"start": v(13.81, -20.7) * mm, "end": v(13.7, -21.67) * mm});
            skLineSegment(sketch, "E5787", {"start": v(13.7, -21.67) * mm, "end": v(13.66, -22.75) * mm});
            skArc(sketch, "E5788", {"start": v(13.66, -22.75) * mm, "mid": v(14.29, -23.09) * mm, "end": v(14.92, -23.4) * mm});
            skLineSegment(sketch, "E5789", {"start": v(17.62, -20.51) * mm, "end": v(17.45, -20.9) * mm});
            skLineSegment(sketch, "E5790", {"start": v(17.45, -20.9) * mm, "end": v(17.35, -21.08) * mm});
            skLineSegment(sketch, "E5791", {"start": v(17.35, -21.08) * mm, "end": v(17.2, -21.3) * mm});
            skLineSegment(sketch, "E5792", {"start": v(17.2, -21.3) * mm, "end": v(17, -21.56) * mm});
            skLineSegment(sketch, "E5793", {"start": v(17, -21.56) * mm, "end": v(16.78, -21.83) * mm});
            skLineSegment(sketch, "E5794", {"start": v(16.78, -21.83) * mm, "end": v(16.52, -22.1) * mm});
            skLineSegment(sketch, "E5795", {"start": v(16.52, -22.1) * mm, "end": v(15.8, -22.76) * mm});
            skLineSegment(sketch, "E5796", {"start": v(15.8, -22.76) * mm, "end": v(14.92, -23.4) * mm});
            skArc(sketch, "E5797", {"start": v(18.6, -20.09) * mm, "mid": v(18.02, -20.1) * mm, "end": v(17.62, -20.51) * mm});
            skArc(sketch, "E5798", {"start": v(18.6, -20.09) * mm, "mid": v(18.93, -20.2) * mm, "end": v(19.26, -20.32) * mm});
            skArc(sketch, "E5799", {"start": v(19.75, -21.27) * mm, "mid": v(19.7, -20.7) * mm, "end": v(19.26, -20.32) * mm});
            skLineSegment(sketch, "E5800", {"start": v(19.75, -21.27) * mm, "end": v(19.63, -21.68) * mm});
            skLineSegment(sketch, "E5801", {"start": v(19.63, -21.68) * mm, "end": v(19.6, -21.88) * mm});
            skLineSegment(sketch, "E5802", {"start": v(19.6, -21.88) * mm, "end": v(19.58, -22.15) * mm});
            skLineSegment(sketch, "E5803", {"start": v(19.58, -22.15) * mm, "end": v(19.57, -22.47) * mm});
            skLineSegment(sketch, "E5804", {"start": v(19.57, -22.47) * mm, "end": v(19.57, -22.82) * mm});
            skLineSegment(sketch, "E5805", {"start": v(19.57, -22.82) * mm, "end": v(19.6, -23.2) * mm});
            skLineSegment(sketch, "E5806", {"start": v(19.6, -23.2) * mm, "end": v(19.75, -24.16) * mm});
            skLineSegment(sketch, "E5807", {"start": v(19.75, -24.16) * mm, "end": v(20.01, -25.21) * mm});
            skArc(sketch, "E5808", {"start": v(20.01, -25.21) * mm, "mid": v(20.7, -25.37) * mm, "end": v(21.4, -25.5) * mm});
            skLineSegment(sketch, "E5809", {"start": v(23.21, -21.99) * mm, "end": v(23.16, -22.4) * mm});
            skLineSegment(sketch, "E5810", {"start": v(23.16, -22.4) * mm, "end": v(23.1, -22.61) * mm});
            skLineSegment(sketch, "E5811", {"start": v(23.1, -22.61) * mm, "end": v(23.02, -22.87) * mm});
            skLineSegment(sketch, "E5812", {"start": v(23.02, -22.87) * mm, "end": v(22.9, -23.17) * mm});
            skLineSegment(sketch, "E5813", {"start": v(22.9, -23.17) * mm, "end": v(22.76, -23.48) * mm});
            skLineSegment(sketch, "E5814", {"start": v(22.76, -23.48) * mm, "end": v(22.58, -23.82) * mm});
            skLineSegment(sketch, "E5815", {"start": v(22.58, -23.82) * mm, "end": v(22.06, -24.65) * mm});
            skLineSegment(sketch, "E5816", {"start": v(22.06, -24.65) * mm, "end": v(21.4, -25.5) * mm});
            skArc(sketch, "E5817", {"start": v(24.04, -21.32) * mm, "mid": v(23.5, -21.49) * mm, "end": v(23.21, -21.99) * mm});
            skArc(sketch, "E5818", {"start": v(24.04, -21.32) * mm, "mid": v(24.4, -21.34) * mm, "end": v(24.74, -21.36) * mm});
            skArc(sketch, "E5819", {"start": v(25.47, -22.14) * mm, "mid": v(25.26, -21.6) * mm, "end": v(24.74, -21.36) * mm});
            skLineSegment(sketch, "E5820", {"start": v(25.47, -22.14) * mm, "end": v(25.47, -22.57) * mm});
            skLineSegment(sketch, "E5821", {"start": v(25.47, -22.57) * mm, "end": v(25.5, -22.77) * mm});
            skLineSegment(sketch, "E5822", {"start": v(25.5, -22.77) * mm, "end": v(25.54, -23.04) * mm});
            skLineSegment(sketch, "E5823", {"start": v(25.54, -23.04) * mm, "end": v(25.62, -23.35) * mm});
            skLineSegment(sketch, "E5824", {"start": v(25.62, -23.35) * mm, "end": v(25.72, -23.69) * mm});
            skLineSegment(sketch, "E5825", {"start": v(25.72, -23.69) * mm, "end": v(25.85, -24.04) * mm});
            skLineSegment(sketch, "E5826", {"start": v(25.85, -24.04) * mm, "end": v(26.25, -24.93) * mm});
            skLineSegment(sketch, "E5827", {"start": v(26.25, -24.93) * mm, "end": v(26.79, -25.87) * mm});
            skArc(sketch, "E5828", {"start": v(26.79, -25.87) * mm, "mid": v(27.5, -25.83) * mm, "end": v(28.2, -25.77) * mm});
            skLineSegment(sketch, "E5829", {"start": v(29, -21.9) * mm, "end": v(29.06, -22.32) * mm});
            skLineSegment(sketch, "E5830", {"start": v(29.06, -22.32) * mm, "end": v(29.07, -22.53) * mm});
            skLineSegment(sketch, "E5831", {"start": v(29.07, -22.53) * mm, "end": v(29.05, -22.8) * mm});
            skLineSegment(sketch, "E5832", {"start": v(29.05, -22.8) * mm, "end": v(29.02, -23.12) * mm});
            skLineSegment(sketch, "E5833", {"start": v(29.02, -23.12) * mm, "end": v(28.97, -23.46) * mm});
            skLineSegment(sketch, "E5834", {"start": v(28.97, -23.46) * mm, "end": v(28.89, -23.83) * mm});
            skLineSegment(sketch, "E5835", {"start": v(28.89, -23.83) * mm, "end": v(28.61, -24.77) * mm});
            skLineSegment(sketch, "E5836", {"start": v(28.61, -24.77) * mm, "end": v(28.2, -25.77) * mm});
            skArc(sketch, "E5837", {"start": v(29.62, -21.03) * mm, "mid": v(29.13, -21.34) * mm, "end": v(29, -21.9) * mm});
            skArc(sketch, "E5838", {"start": v(29.62, -21.03) * mm, "mid": v(29.96, -20.96) * mm, "end": v(30.3, -20.89) * mm});
            skArc(sketch, "E5839", {"start": v(31.22, -21.44) * mm, "mid": v(30.87, -20.98) * mm, "end": v(30.3, -20.89) * mm});
            skLineSegment(sketch, "E5840", {"start": v(31.22, -21.44) * mm, "end": v(31.33, -21.85) * mm});
            skLineSegment(sketch, "E5841", {"start": v(31.33, -21.85) * mm, "end": v(31.4, -22.04) * mm});
            skLineSegment(sketch, "E5842", {"start": v(31.4, -22.04) * mm, "end": v(31.53, -22.29) * mm});
            skLineSegment(sketch, "E5843", {"start": v(31.53, -22.29) * mm, "end": v(31.68, -22.57) * mm});
            skLineSegment(sketch, "E5844", {"start": v(31.68, -22.57) * mm, "end": v(31.87, -22.86) * mm});
            skLineSegment(sketch, "E5845", {"start": v(31.87, -22.86) * mm, "end": v(32.1, -23.17) * mm});
            skLineSegment(sketch, "E5846", {"start": v(32.1, -23.17) * mm, "end": v(32.72, -23.92) * mm});
            skLineSegment(sketch, "E5847", {"start": v(32.72, -23.92) * mm, "end": v(33.5, -24.68) * mm});
            skArc(sketch, "E5848", {"start": v(33.5, -24.68) * mm, "mid": v(34.16, -24.45) * mm, "end": v(34.83, -24.2) * mm});
            skLineSegment(sketch, "E5849", {"start": v(34.55, -20.26) * mm, "end": v(34.72, -20.65) * mm});
            skLineSegment(sketch, "E5850", {"start": v(34.72, -20.65) * mm, "end": v(34.78, -20.84) * mm});
            skLineSegment(sketch, "E5851", {"start": v(34.78, -20.84) * mm, "end": v(34.84, -21.11) * mm});
            skLineSegment(sketch, "E5852", {"start": v(34.84, -21.11) * mm, "end": v(34.9, -21.42) * mm});
            skLineSegment(sketch, "E5853", {"start": v(34.9, -21.42) * mm, "end": v(34.94, -21.77) * mm});
            skLineSegment(sketch, "E5854", {"start": v(34.94, -21.77) * mm, "end": v(34.96, -22.15) * mm});
            skLineSegment(sketch, "E5855", {"start": v(34.96, -22.15) * mm, "end": v(34.95, -23.12) * mm});
            skLineSegment(sketch, "E5856", {"start": v(34.95, -23.12) * mm, "end": v(34.83, -24.2) * mm});
            skArc(sketch, "E5857", {"start": v(34.91, -19.25) * mm, "mid": v(34.53, -19.68) * mm, "end": v(34.55, -20.26) * mm});
            skArc(sketch, "E5858", {"start": v(34.91, -19.25) * mm, "mid": v(35.22, -19.1) * mm, "end": v(35.53, -18.93) * mm});
            skArc(sketch, "E5859", {"start": v(36.56, -19.22) * mm, "mid": v(36.1, -18.86) * mm, "end": v(35.53, -18.93) * mm});
            skLineSegment(sketch, "E5860", {"start": v(36.56, -19.22) * mm, "end": v(36.78, -19.58) * mm});
            skLineSegment(sketch, "E5861", {"start": v(36.78, -19.58) * mm, "end": v(36.9, -19.74) * mm});
            skLineSegment(sketch, "E5862", {"start": v(36.9, -19.74) * mm, "end": v(37.09, -19.95) * mm});
            skLineSegment(sketch, "E5863", {"start": v(37.09, -19.95) * mm, "end": v(37.31, -20.17) * mm});
            skLineSegment(sketch, "E5864", {"start": v(37.31, -20.17) * mm, "end": v(37.57, -20.4) * mm});
            skLineSegment(sketch, "E5865", {"start": v(37.57, -20.4) * mm, "end": v(37.87, -20.64) * mm});
            skLineSegment(sketch, "E5866", {"start": v(37.87, -20.64) * mm, "end": v(38.67, -21.2) * mm});
            skLineSegment(sketch, "E5867", {"start": v(38.67, -21.2) * mm, "end": v(39.62, -21.72) * mm});
            skArc(sketch, "E5868", {"start": v(39.62, -21.72) * mm, "mid": v(40.2, -21.31) * mm, "end": v(40.78, -20.9) * mm});
            skLineSegment(sketch, "E5869", {"start": v(39.45, -17.18) * mm, "end": v(39.72, -17.5) * mm});
            skLineSegment(sketch, "E5870", {"start": v(39.72, -17.5) * mm, "end": v(39.83, -17.68) * mm});
            skLineSegment(sketch, "E5871", {"start": v(39.83, -17.68) * mm, "end": v(39.96, -17.92) * mm});
            skLineSegment(sketch, "E5872", {"start": v(39.96, -17.92) * mm, "end": v(40.1, -18.2) * mm});
            skLineSegment(sketch, "E5873", {"start": v(40.1, -18.2) * mm, "end": v(40.23, -18.53) * mm});
            skLineSegment(sketch, "E5874", {"start": v(40.23, -18.53) * mm, "end": v(40.36, -18.88) * mm});
            skLineSegment(sketch, "E5875", {"start": v(40.36, -18.88) * mm, "end": v(40.6, -19.83) * mm});
            skLineSegment(sketch, "E5876", {"start": v(40.6, -19.83) * mm, "end": v(40.78, -20.9) * mm});
            skArc(sketch, "E5877", {"start": v(39.53, -16.1) * mm, "mid": v(39.27, -16.63) * mm, "end": v(39.45, -17.18) * mm});
            skArc(sketch, "E5878", {"start": v(39.53, -16.1) * mm, "mid": v(39.78, -15.87) * mm, "end": v(40.04, -15.63) * mm});
            skArc(sketch, "E5879", {"start": v(41.1, -15.63) * mm, "mid": v(40.57, -15.42) * mm, "end": v(40.04, -15.63) * mm});
            skLineSegment(sketch, "E5880", {"start": v(41.1, -15.63) * mm, "end": v(41.42, -15.92) * mm});
            skLineSegment(sketch, "E5881", {"start": v(41.42, -15.92) * mm, "end": v(41.58, -16.04) * mm});
            skLineSegment(sketch, "E5882", {"start": v(41.58, -16.04) * mm, "end": v(41.81, -16.2) * mm});
            skLineSegment(sketch, "E5883", {"start": v(41.81, -16.2) * mm, "end": v(42.09, -16.35) * mm});
            skLineSegment(sketch, "E5884", {"start": v(42.09, -16.35) * mm, "end": v(42.4, -16.5) * mm});
            skLineSegment(sketch, "E5885", {"start": v(42.4, -16.5) * mm, "end": v(42.75, -16.65) * mm});
            skLineSegment(sketch, "E5886", {"start": v(42.75, -16.65) * mm, "end": v(43.67, -16.97) * mm});
            skLineSegment(sketch, "E5887", {"start": v(43.67, -16.97) * mm, "end": v(44.73, -17.21) * mm});
            skArc(sketch, "E5888", {"start": v(44.73, -17.21) * mm, "mid": v(45.18, -16.67) * mm, "end": v(45.62, -16.11) * mm});
            skLineSegment(sketch, "E5889", {"start": v(43.34, -12.89) * mm, "end": v(43.69, -13.13) * mm});
            skLineSegment(sketch, "E5890", {"start": v(43.69, -13.13) * mm, "end": v(43.84, -13.27) * mm});
            skLineSegment(sketch, "E5891", {"start": v(43.84, -13.27) * mm, "end": v(44.03, -13.46) * mm});
            skLineSegment(sketch, "E5892", {"start": v(44.03, -13.46) * mm, "end": v(44.24, -13.7) * mm});
            skLineSegment(sketch, "E5893", {"start": v(44.24, -13.7) * mm, "end": v(44.46, -13.98) * mm});
            skLineSegment(sketch, "E5894", {"start": v(44.46, -13.98) * mm, "end": v(44.67, -14.29) * mm});
            skLineSegment(sketch, "E5895", {"start": v(44.67, -14.29) * mm, "end": v(45.17, -15.13) * mm});
            skLineSegment(sketch, "E5896", {"start": v(45.17, -15.13) * mm, "end": v(45.62, -16.11) * mm});
            skArc(sketch, "E5897", {"start": v(43.12, -11.84) * mm, "mid": v(43.02, -12.4) * mm, "end": v(43.34, -12.89) * mm});
            skArc(sketch, "E5898", {"start": v(43.12, -11.84) * mm, "mid": v(43.3, -11.54) * mm, "end": v(43.49, -11.24) * mm});
            skArc(sketch, "E5899", {"start": v(44.52, -10.95) * mm, "mid": v(43.94, -10.89) * mm, "end": v(43.49, -11.24) * mm});
            skLineSegment(sketch, "E5900", {"start": v(44.52, -10.95) * mm, "end": v(44.9, -11.15) * mm});
            skLineSegment(sketch, "E5901", {"start": v(44.9, -11.15) * mm, "end": v(45.08, -11.22) * mm});
            skLineSegment(sketch, "E5902", {"start": v(45.08, -11.22) * mm, "end": v(45.35, -11.3) * mm});
            skLineSegment(sketch, "E5903", {"start": v(45.35, -11.3) * mm, "end": v(45.65, -11.38) * mm});
            skLineSegment(sketch, "E5904", {"start": v(45.65, -11.38) * mm, "end": v(46, -11.44) * mm});
            skLineSegment(sketch, "E5905", {"start": v(46, -11.44) * mm, "end": v(46.37, -11.5) * mm});
            skLineSegment(sketch, "E5906", {"start": v(46.37, -11.5) * mm, "end": v(47.35, -11.54) * mm});
            skLineSegment(sketch, "E5907", {"start": v(47.35, -11.54) * mm, "end": v(48.43, -11.5) * mm});
            skArc(sketch, "E5908", {"start": v(48.43, -11.5) * mm, "mid": v(48.72, -10.85) * mm, "end": v(49, -10.2) * mm});
            skLineSegment(sketch, "E5909", {"start": v(45.93, -7.7) * mm, "end": v(46.32, -7.85) * mm});
            skLineSegment(sketch, "E5910", {"start": v(46.32, -7.85) * mm, "end": v(46.51, -7.94) * mm});
            skLineSegment(sketch, "E5911", {"start": v(46.51, -7.94) * mm, "end": v(46.75, -8.08) * mm});
            skLineSegment(sketch, "E5912", {"start": v(46.75, -8.08) * mm, "end": v(47.01, -8.25) * mm});
            skLineSegment(sketch, "E5913", {"start": v(47.01, -8.25) * mm, "end": v(47.3, -8.46) * mm});
            skLineSegment(sketch, "E5914", {"start": v(47.3, -8.46) * mm, "end": v(47.59, -8.7) * mm});
            skLineSegment(sketch, "E5915", {"start": v(47.59, -8.7) * mm, "end": v(48.3, -9.37) * mm});
            skLineSegment(sketch, "E5916", {"start": v(48.3, -9.37) * mm, "end": v(49, -10.2) * mm});
            skArc(sketch, "E5917", {"start": v(45.43, -6.76) * mm, "mid": v(45.49, -7.33) * mm, "end": v(45.93, -7.7) * mm});
            skArc(sketch, "E5918", {"start": v(45.43, -6.76) * mm, "mid": v(45.53, -6.42) * mm, "end": v(45.62, -6.08) * mm});
            skArc(sketch, "E5919", {"start": v(46.54, -5.53) * mm, "mid": v(45.97, -5.62) * mm, "end": v(45.62, -6.08) * mm});
            skLineSegment(sketch, "E5920", {"start": v(46.54, -5.53) * mm, "end": v(46.95, -5.61) * mm});
            skLineSegment(sketch, "E5921", {"start": v(46.95, -5.61) * mm, "end": v(47.16, -5.63) * mm});
            skLineSegment(sketch, "E5922", {"start": v(47.16, -5.63) * mm, "end": v(47.43, -5.64) * mm});
            skLineSegment(sketch, "E5923", {"start": v(47.43, -5.64) * mm, "end": v(47.75, -5.63) * mm});
            skLineSegment(sketch, "E5924", {"start": v(47.75, -5.63) * mm, "end": v(48.1, -5.6) * mm});
            skLineSegment(sketch, "E5925", {"start": v(48.1, -5.6) * mm, "end": v(48.47, -5.55) * mm});
            skLineSegment(sketch, "E5926", {"start": v(48.47, -5.55) * mm, "end": v(49.42, -5.33) * mm});
            skLineSegment(sketch, "E5927", {"start": v(49.42, -5.33) * mm, "end": v(50.45, -5) * mm});
            skArc(sketch, "E5928", {"start": v(50.45, -5) * mm, "mid": v(50.56, -4.3) * mm, "end": v(50.65, -3.6) * mm});
            skLineSegment(sketch, "E5929", {"start": v(47.02, -2.02) * mm, "end": v(47.44, -2.05) * mm});
            skLineSegment(sketch, "E5930", {"start": v(47.44, -2.05) * mm, "end": v(47.64, -2.09) * mm});
            skLineSegment(sketch, "E5931", {"start": v(47.64, -2.09) * mm, "end": v(47.9, -2.15) * mm});
            skLineSegment(sketch, "E5932", {"start": v(47.9, -2.15) * mm, "end": v(48.21, -2.25) * mm});
            skLineSegment(sketch, "E5933", {"start": v(48.21, -2.25) * mm, "end": v(48.54, -2.37) * mm});
            skLineSegment(sketch, "E5934", {"start": v(48.54, -2.37) * mm, "end": v(48.88, -2.53) * mm});
            skLineSegment(sketch, "E5935", {"start": v(48.88, -2.53) * mm, "end": v(49.75, -2.99) * mm});
            skLineSegment(sketch, "E5936", {"start": v(49.75, -2.99) * mm, "end": v(50.65, -3.6) * mm});
            skArc(sketch, "E5937", {"start": v(46.29, -1.24) * mm, "mid": v(46.5, -1.78) * mm, "end": v(47.02, -2.02) * mm});
            skArc(sketch, "E5938", {"start": v(46.29, -1.24) * mm, "mid": v(46.3, -0.9) * mm, "end": v(46.29, -0.54) * mm});
            skArc(sketch, "E5939", {"start": v(47.02, 0.24) * mm, "mid": v(46.5, 0) * mm, "end": v(46.29, -0.54) * mm});
            skLineSegment(sketch, "E5940", {"start": v(47.02, 0.24) * mm, "end": v(47.44, 0.27) * mm});
            skLineSegment(sketch, "E5941", {"start": v(47.44, 0.27) * mm, "end": v(47.64, 0.3) * mm});
            skLineSegment(sketch, "E5942", {"start": v(47.64, 0.3) * mm, "end": v(47.9, 0.37) * mm});
            skLineSegment(sketch, "E5943", {"start": v(47.9, 0.37) * mm, "end": v(48.21, 0.47) * mm});
            skLineSegment(sketch, "E5944", {"start": v(48.21, 0.47) * mm, "end": v(48.54, 0.6) * mm});
            skLineSegment(sketch, "E5945", {"start": v(48.54, 0.6) * mm, "end": v(48.88, 0.75) * mm});
            skLineSegment(sketch, "E5946", {"start": v(48.88, 0.75) * mm, "end": v(49.75, 1.2) * mm});
            skLineSegment(sketch, "E5947", {"start": v(49.75, 1.2) * mm, "end": v(50.65, 1.8) * mm});
            skArc(sketch, "E5948", {"start": v(50.65, 1.8) * mm, "mid": v(50.56, 2.51) * mm, "end": v(50.45, 3.21) * mm});
            skLineSegment(sketch, "E5949", {"start": v(46.54, 3.75) * mm, "end": v(46.95, 3.83) * mm});
            skLineSegment(sketch, "E5950", {"start": v(46.95, 3.83) * mm, "end": v(47.16, 3.85) * mm});
            skLineSegment(sketch, "E5951", {"start": v(47.16, 3.85) * mm, "end": v(47.43, 3.86) * mm});
            skLineSegment(sketch, "E5952", {"start": v(47.43, 3.86) * mm, "end": v(47.75, 3.85) * mm});
            skLineSegment(sketch, "E5953", {"start": v(47.75, 3.85) * mm, "end": v(48.1, 3.82) * mm});
            skLineSegment(sketch, "E5954", {"start": v(48.1, 3.82) * mm, "end": v(48.47, 3.76) * mm});
            skLineSegment(sketch, "E5955", {"start": v(48.47, 3.76) * mm, "end": v(49.42, 3.55) * mm});
            skLineSegment(sketch, "E5956", {"start": v(49.42, 3.55) * mm, "end": v(50.45, 3.21) * mm});
            skArc(sketch, "E5957", {"start": v(45.62, 4.3) * mm, "mid": v(45.97, 3.84) * mm, "end": v(46.54, 3.75) * mm});
            skArc(sketch, "E5958", {"start": v(45.62, 4.3) * mm, "mid": v(45.53, 4.64) * mm, "end": v(45.43, 4.98) * mm});
            skArc(sketch, "E5959", {"start": v(45.93, 5.93) * mm, "mid": v(45.49, 5.55) * mm, "end": v(45.43, 4.98) * mm});
            skLineSegment(sketch, "E5960", {"start": v(45.93, 5.93) * mm, "end": v(46.32, 6.07) * mm});
            skLineSegment(sketch, "E5961", {"start": v(46.32, 6.07) * mm, "end": v(46.51, 6.16) * mm});
            skLineSegment(sketch, "E5962", {"start": v(46.51, 6.16) * mm, "end": v(46.75, 6.3) * mm});
            skLineSegment(sketch, "E5963", {"start": v(46.75, 6.3) * mm, "end": v(47.01, 6.47) * mm});
            skLineSegment(sketch, "E5964", {"start": v(47.01, 6.47) * mm, "end": v(47.3, 6.68) * mm});
            skLineSegment(sketch, "E5965", {"start": v(47.3, 6.68) * mm, "end": v(47.59, 6.91) * mm});
            skLineSegment(sketch, "E5966", {"start": v(47.59, 6.91) * mm, "end": v(48.3, 7.6) * mm});
            skLineSegment(sketch, "E5967", {"start": v(48.3, 7.6) * mm, "end": v(49, 8.42) * mm});
            skArc(sketch, "E5968", {"start": v(49, 8.42) * mm, "mid": v(48.72, 9.07) * mm, "end": v(48.43, 9.72) * mm});
            skLineSegment(sketch, "E5969", {"start": v(44.52, 9.17) * mm, "end": v(44.9, 9.37) * mm});
            skLineSegment(sketch, "E5970", {"start": v(44.9, 9.37) * mm, "end": v(45.08, 9.44) * mm});
            skLineSegment(sketch, "E5971", {"start": v(45.08, 9.44) * mm, "end": v(45.35, 9.52) * mm});
            skLineSegment(sketch, "E5972", {"start": v(45.35, 9.52) * mm, "end": v(45.65, 9.6) * mm});
            skLineSegment(sketch, "E5973", {"start": v(45.65, 9.6) * mm, "end": v(46, 9.66) * mm});
            skLineSegment(sketch, "E5974", {"start": v(46, 9.66) * mm, "end": v(46.37, 9.7) * mm});
            skLineSegment(sketch, "E5975", {"start": v(46.37, 9.7) * mm, "end": v(47.35, 9.76) * mm});
            skLineSegment(sketch, "E5976", {"start": v(47.35, 9.76) * mm, "end": v(48.43, 9.72) * mm});
            skArc(sketch, "E5977", {"start": v(43.49, 9.46) * mm, "mid": v(43.94, 9.1) * mm, "end": v(44.52, 9.17) * mm});
            skArc(sketch, "E5978", {"start": v(43.49, 9.46) * mm, "mid": v(43.3, 9.76) * mm, "end": v(43.12, 10.06) * mm});
            skArc(sketch, "E5979", {"start": v(43.34, 11.1) * mm, "mid": v(43.02, 10.63) * mm, "end": v(43.12, 10.06) * mm});
            skLineSegment(sketch, "E5980", {"start": v(43.34, 11.1) * mm, "end": v(43.69, 11.35) * mm});
            skLineSegment(sketch, "E5981", {"start": v(43.69, 11.35) * mm, "end": v(43.84, 11.49) * mm});
            skLineSegment(sketch, "E5982", {"start": v(43.84, 11.49) * mm, "end": v(44.03, 11.68) * mm});
            skLineSegment(sketch, "E5983", {"start": v(44.03, 11.68) * mm, "end": v(44.24, 11.92) * mm});
            skLineSegment(sketch, "E5984", {"start": v(44.24, 11.92) * mm, "end": v(44.46, 12.2) * mm});
            skLineSegment(sketch, "E5985", {"start": v(44.46, 12.2) * mm, "end": v(44.67, 12.5) * mm});
            skLineSegment(sketch, "E5986", {"start": v(44.67, 12.5) * mm, "end": v(45.17, 13.35) * mm});
            skLineSegment(sketch, "E5987", {"start": v(45.17, 13.35) * mm, "end": v(45.62, 14.33) * mm});
            skArc(sketch, "E5988", {"start": v(45.62, 14.33) * mm, "mid": v(45.18, 14.89) * mm, "end": v(44.73, 15.43) * mm});
            skLineSegment(sketch, "E5989", {"start": v(41.1, 13.85) * mm, "end": v(41.42, 14.14) * mm});
            skLineSegment(sketch, "E5990", {"start": v(41.42, 14.14) * mm, "end": v(41.58, 14.26) * mm});
            skLineSegment(sketch, "E5991", {"start": v(41.58, 14.26) * mm, "end": v(41.81, 14.41) * mm});
            skLineSegment(sketch, "E5992", {"start": v(41.81, 14.41) * mm, "end": v(42.09, 14.57) * mm});
            skLineSegment(sketch, "E5993", {"start": v(42.09, 14.57) * mm, "end": v(42.4, 14.72) * mm});
            skLineSegment(sketch, "E5994", {"start": v(42.4, 14.72) * mm, "end": v(42.75, 14.87) * mm});
            skLineSegment(sketch, "E5995", {"start": v(42.75, 14.87) * mm, "end": v(43.67, 15.18) * mm});
            skLineSegment(sketch, "E5996", {"start": v(43.67, 15.18) * mm, "end": v(44.73, 15.43) * mm});
            skArc(sketch, "E5997", {"start": v(40.04, 13.85) * mm, "mid": v(40.57, 13.63) * mm, "end": v(41.1, 13.85) * mm});
            skArc(sketch, "E5998", {"start": v(40.04, 13.85) * mm, "mid": v(39.78, 14.1) * mm, "end": v(39.53, 14.33) * mm});
            skArc(sketch, "E5999", {"start": v(39.45, 15.4) * mm, "mid": v(39.27, 14.85) * mm, "end": v(39.53, 14.33) * mm});
            skLineSegment(sketch, "E6000", {"start": v(39.45, 15.4) * mm, "end": v(39.72, 15.72) * mm});
            skLineSegment(sketch, "E6001", {"start": v(39.72, 15.72) * mm, "end": v(39.83, 15.9) * mm});
            skLineSegment(sketch, "E6002", {"start": v(39.83, 15.9) * mm, "end": v(39.96, 16.14) * mm});
            skLineSegment(sketch, "E6003", {"start": v(39.96, 16.14) * mm, "end": v(40.1, 16.42) * mm});
            skLineSegment(sketch, "E6004", {"start": v(40.1, 16.42) * mm, "end": v(40.23, 16.75) * mm});
            skLineSegment(sketch, "E6005", {"start": v(40.23, 16.75) * mm, "end": v(40.36, 17.1) * mm});
            skLineSegment(sketch, "E6006", {"start": v(40.36, 17.1) * mm, "end": v(40.6, 18.05) * mm});
            skLineSegment(sketch, "E6007", {"start": v(40.6, 18.05) * mm, "end": v(40.78, 19.12) * mm});
            skArc(sketch, "E6008", {"start": v(40.78, 19.12) * mm, "mid": v(40.2, 19.53) * mm, "end": v(39.62, 19.93) * mm});
            skLineSegment(sketch, "E6009", {"start": v(36.56, 17.44) * mm, "end": v(36.78, 17.8) * mm});
            skLineSegment(sketch, "E6010", {"start": v(36.78, 17.8) * mm, "end": v(36.9, 17.96) * mm});
            skLineSegment(sketch, "E6011", {"start": v(36.9, 17.96) * mm, "end": v(37.09, 18.17) * mm});
            skLineSegment(sketch, "E6012", {"start": v(37.09, 18.17) * mm, "end": v(37.31, 18.4) * mm});
            skLineSegment(sketch, "E6013", {"start": v(37.31, 18.4) * mm, "end": v(37.57, 18.62) * mm});
            skLineSegment(sketch, "E6014", {"start": v(37.57, 18.62) * mm, "end": v(37.87, 18.86) * mm});
            skLineSegment(sketch, "E6015", {"start": v(37.87, 18.86) * mm, "end": v(38.67, 19.41) * mm});
            skLineSegment(sketch, "E6016", {"start": v(38.67, 19.41) * mm, "end": v(39.62, 19.93) * mm});
            skArc(sketch, "E6017", {"start": v(35.53, 17.15) * mm, "mid": v(36.1, 17.08) * mm, "end": v(36.56, 17.44) * mm});
            skArc(sketch, "E6018", {"start": v(35.53, 17.15) * mm, "mid": v(35.22, 17.31) * mm, "end": v(34.91, 17.47) * mm});
            skArc(sketch, "E6019", {"start": v(34.55, 18.48) * mm, "mid": v(34.53, 17.9) * mm, "end": v(34.91, 17.47) * mm});
            skLineSegment(sketch, "E6020", {"start": v(34.55, 18.48) * mm, "end": v(34.72, 18.87) * mm});
            skLineSegment(sketch, "E6021", {"start": v(34.72, 18.87) * mm, "end": v(34.78, 19.06) * mm});
            skLineSegment(sketch, "E6022", {"start": v(34.78, 19.06) * mm, "end": v(34.84, 19.33) * mm});
            skLineSegment(sketch, "E6023", {"start": v(34.84, 19.33) * mm, "end": v(34.9, 19.64) * mm});
            skLineSegment(sketch, "E6024", {"start": v(34.9, 19.64) * mm, "end": v(34.94, 19.99) * mm});
            skLineSegment(sketch, "E6025", {"start": v(34.94, 19.99) * mm, "end": v(34.96, 20.36) * mm});
            skLineSegment(sketch, "E6026", {"start": v(34.96, 20.36) * mm, "end": v(34.95, 21.34) * mm});
            skLineSegment(sketch, "E6027", {"start": v(34.95, 21.34) * mm, "end": v(34.83, 22.42) * mm});
            skArc(sketch, "E6028", {"start": v(34.83, 22.42) * mm, "mid": v(34.16, 22.67) * mm, "end": v(33.5, 22.9) * mm});
            skLineSegment(sketch, "E6029", {"start": v(31.22, 19.66) * mm, "end": v(31.33, 20.07) * mm});
            skLineSegment(sketch, "E6030", {"start": v(31.33, 20.07) * mm, "end": v(31.4, 20.26) * mm});
            skLineSegment(sketch, "E6031", {"start": v(31.4, 20.26) * mm, "end": v(31.53, 20.5) * mm});
            skLineSegment(sketch, "E6032", {"start": v(31.53, 20.5) * mm, "end": v(31.68, 20.78) * mm});
            skLineSegment(sketch, "E6033", {"start": v(31.68, 20.78) * mm, "end": v(31.87, 21.08) * mm});
            skLineSegment(sketch, "E6034", {"start": v(31.87, 21.08) * mm, "end": v(32.1, 21.39) * mm});
            skLineSegment(sketch, "E6035", {"start": v(32.1, 21.39) * mm, "end": v(32.72, 22.14) * mm});
            skLineSegment(sketch, "E6036", {"start": v(32.72, 22.14) * mm, "end": v(33.5, 22.9) * mm});
            skArc(sketch, "E6037", {"start": v(30.3, 19.1) * mm, "mid": v(30.87, 19.2) * mm, "end": v(31.22, 19.66) * mm});
            skArc(sketch, "E6038", {"start": v(30.3, 19.1) * mm, "mid": v(29.96, 19.18) * mm, "end": v(29.62, 19.25) * mm});
            skArc(sketch, "E6039", {"start": v(29, 20.12) * mm, "mid": v(29.13, 19.56) * mm, "end": v(29.62, 19.25) * mm});
            skLineSegment(sketch, "E6040", {"start": v(29, 20.12) * mm, "end": v(29.06, 20.54) * mm});
            skLineSegment(sketch, "E6041", {"start": v(29.06, 20.54) * mm, "end": v(29.07, 20.75) * mm});
            skLineSegment(sketch, "E6042", {"start": v(29.07, 20.75) * mm, "end": v(29.05, 21.02) * mm});
            skLineSegment(sketch, "E6043", {"start": v(29.05, 21.02) * mm, "end": v(29.02, 21.34) * mm});
            skLineSegment(sketch, "E6044", {"start": v(29.02, 21.34) * mm, "end": v(28.97, 21.68) * mm});
            skLineSegment(sketch, "E6045", {"start": v(28.97, 21.68) * mm, "end": v(28.89, 22.05) * mm});
            skLineSegment(sketch, "E6046", {"start": v(28.89, 22.05) * mm, "end": v(28.61, 22.99) * mm});
            skLineSegment(sketch, "E6047", {"start": v(28.61, 22.99) * mm, "end": v(28.2, 24) * mm});
            skArc(sketch, "E6048", {"start": v(28.2, 24) * mm, "mid": v(27.5, 24.05) * mm, "end": v(26.79, 24.09) * mm});
            skLineSegment(sketch, "E6049", {"start": v(25.47, 20.36) * mm, "end": v(25.47, 20.79) * mm});
            skLineSegment(sketch, "E6050", {"start": v(25.47, 20.79) * mm, "end": v(25.5, 21) * mm});
            skLineSegment(sketch, "E6051", {"start": v(25.5, 21) * mm, "end": v(25.54, 21.26) * mm});
            skLineSegment(sketch, "E6052", {"start": v(25.54, 21.26) * mm, "end": v(25.62, 21.57) * mm});
            skLineSegment(sketch, "E6053", {"start": v(25.62, 21.57) * mm, "end": v(25.72, 21.9) * mm});
            skLineSegment(sketch, "E6054", {"start": v(25.72, 21.9) * mm, "end": v(25.85, 22.26) * mm});
            skLineSegment(sketch, "E6055", {"start": v(25.85, 22.26) * mm, "end": v(26.25, 23.15) * mm});
            skLineSegment(sketch, "E6056", {"start": v(26.25, 23.15) * mm, "end": v(26.79, 24.09) * mm});
            skArc(sketch, "E6057", {"start": v(24.74, 19.58) * mm, "mid": v(25.26, 19.83) * mm, "end": v(25.47, 20.36) * mm});
            skArc(sketch, "E6058", {"start": v(24.74, 19.58) * mm, "mid": v(24.4, 19.56) * mm, "end": v(24.04, 19.53) * mm});
            skArc(sketch, "E6059", {"start": v(23.21, 20.2) * mm, "mid": v(23.5, 19.7) * mm, "end": v(24.04, 19.53) * mm});
            skLineSegment(sketch, "E6060", {"start": v(23.21, 20.2) * mm, "end": v(23.16, 20.63) * mm});
            skLineSegment(sketch, "E6061", {"start": v(23.16, 20.63) * mm, "end": v(23.1, 20.83) * mm});
            skLineSegment(sketch, "E6062", {"start": v(23.1, 20.83) * mm, "end": v(23.02, 21.09) * mm});
            skLineSegment(sketch, "E6063", {"start": v(23.02, 21.09) * mm, "end": v(22.9, 21.38) * mm});
            skLineSegment(sketch, "E6064", {"start": v(22.9, 21.38) * mm, "end": v(22.76, 21.7) * mm});
            skLineSegment(sketch, "E6065", {"start": v(22.76, 21.7) * mm, "end": v(22.58, 22.04) * mm});
            skLineSegment(sketch, "E6066", {"start": v(22.58, 22.04) * mm, "end": v(22.06, 22.86) * mm});
            skLineSegment(sketch, "E6067", {"start": v(22.06, 22.86) * mm, "end": v(21.4, 23.72) * mm});
            skArc(sketch, "E6068", {"start": v(21.4, 23.72) * mm, "mid": v(20.7, 23.59) * mm, "end": v(20.01, 23.43) * mm});
            skLineSegment(sketch, "E6069", {"start": v(19.75, 19.49) * mm, "end": v(19.63, 19.9) * mm});
            skLineSegment(sketch, "E6070", {"start": v(19.63, 19.9) * mm, "end": v(19.6, 20.1) * mm});
            skLineSegment(sketch, "E6071", {"start": v(19.6, 20.1) * mm, "end": v(19.58, 20.37) * mm});
            skLineSegment(sketch, "E6072", {"start": v(19.58, 20.37) * mm, "end": v(19.57, 20.7) * mm});
            skLineSegment(sketch, "E6073", {"start": v(19.57, 20.7) * mm, "end": v(19.57, 21.04) * mm});
            skLineSegment(sketch, "E6074", {"start": v(19.57, 21.04) * mm, "end": v(19.6, 21.42) * mm});
            skLineSegment(sketch, "E6075", {"start": v(19.6, 21.42) * mm, "end": v(19.75, 22.38) * mm});
            skLineSegment(sketch, "E6076", {"start": v(19.75, 22.38) * mm, "end": v(20.01, 23.43) * mm});
            skArc(sketch, "E6077", {"start": v(19.26, 18.54) * mm, "mid": v(19.7, 18.92) * mm, "end": v(19.75, 19.49) * mm});
            skArc(sketch, "E6078", {"start": v(19.26, 18.54) * mm, "mid": v(18.93, 18.43) * mm, "end": v(18.6, 18.3) * mm});
            skArc(sketch, "E6079", {"start": v(17.62, 18.73) * mm, "mid": v(18.02, 18.32) * mm, "end": v(18.6, 18.3) * mm});
            skLineSegment(sketch, "E6080", {"start": v(17.62, 18.73) * mm, "end": v(17.45, 19.12) * mm});
            skLineSegment(sketch, "E6081", {"start": v(17.45, 19.12) * mm, "end": v(17.35, 19.3) * mm});
            skLineSegment(sketch, "E6082", {"start": v(17.35, 19.3) * mm, "end": v(17.2, 19.53) * mm});
            skLineSegment(sketch, "E6083", {"start": v(17.2, 19.53) * mm, "end": v(17, 19.78) * mm});
            skLineSegment(sketch, "E6084", {"start": v(17, 19.78) * mm, "end": v(16.78, 20.05) * mm});
            skLineSegment(sketch, "E6085", {"start": v(16.78, 20.05) * mm, "end": v(16.52, 20.32) * mm});
            skLineSegment(sketch, "E6086", {"start": v(16.52, 20.32) * mm, "end": v(15.8, 20.98) * mm});
            skLineSegment(sketch, "E6087", {"start": v(15.8, 20.98) * mm, "end": v(14.92, 21.62) * mm});
            skArc(sketch, "E6088", {"start": v(14.92, 21.62) * mm, "mid": v(14.29, 21.3) * mm, "end": v(13.66, 20.97) * mm});
            skLineSegment(sketch, "E6089", {"start": v(14.48, 17.1) * mm, "end": v(14.25, 17.47) * mm});
            skLineSegment(sketch, "E6090", {"start": v(14.25, 17.47) * mm, "end": v(14.17, 17.65) * mm});
            skLineSegment(sketch, "E6091", {"start": v(14.17, 17.65) * mm, "end": v(14.07, 17.9) * mm});
            skLineSegment(sketch, "E6092", {"start": v(14.07, 17.9) * mm, "end": v(13.97, 18.21) * mm});
            skLineSegment(sketch, "E6093", {"start": v(13.97, 18.21) * mm, "end": v(13.89, 18.55) * mm});
            skLineSegment(sketch, "E6094", {"start": v(13.89, 18.55) * mm, "end": v(13.81, 18.92) * mm});
            skLineSegment(sketch, "E6095", {"start": v(13.81, 18.92) * mm, "end": v(13.7, 19.89) * mm});
            skLineSegment(sketch, "E6096", {"start": v(13.7, 19.89) * mm, "end": v(13.66, 20.97) * mm});
            skArc(sketch, "E6097", {"start": v(14.26, 16.06) * mm, "mid": v(14.58, 16.54) * mm, "end": v(14.48, 17.1) * mm});
            skArc(sketch, "E6098", {"start": v(14.26, 16.06) * mm, "mid": v(13.97, 15.86) * mm, "end": v(13.69, 15.65) * mm});
            skArc(sketch, "E6099", {"start": v(12.63, 15.8) * mm, "mid": v(13.13, 15.51) * mm, "end": v(13.69, 15.65) * mm});
            skLineSegment(sketch, "E6100", {"start": v(12.63, 15.8) * mm, "end": v(12.36, 16.13) * mm});
            skLineSegment(sketch, "E6101", {"start": v(12.36, 16.13) * mm, "end": v(12.21, 16.27) * mm});
            skLineSegment(sketch, "E6102", {"start": v(12.21, 16.27) * mm, "end": v(12, 16.45) * mm});
            skLineSegment(sketch, "E6103", {"start": v(12, 16.45) * mm, "end": v(11.75, 16.64) * mm});
            skLineSegment(sketch, "E6104", {"start": v(11.75, 16.64) * mm, "end": v(11.46, 16.84) * mm});
            skLineSegment(sketch, "E6105", {"start": v(11.46, 16.84) * mm, "end": v(11.14, 17.03) * mm});
            skLineSegment(sketch, "E6106", {"start": v(11.14, 17.03) * mm, "end": v(10.26, 17.47) * mm});
            skLineSegment(sketch, "E6107", {"start": v(10.26, 17.47) * mm, "end": v(9.25, 17.86) * mm});
            skArc(sketch, "E6108", {"start": v(9.25, 17.86) * mm, "mid": v(8.73, 17.38) * mm, "end": v(8.22, 16.89) * mm});
            skLineSegment(sketch, "E6109", {"start": v(10.04, 13.38) * mm, "end": v(9.73, 13.67) * mm});
            skLineSegment(sketch, "E6110", {"start": v(9.73, 13.67) * mm, "end": v(9.6, 13.83) * mm});
            skLineSegment(sketch, "E6111", {"start": v(9.6, 13.83) * mm, "end": v(9.43, 14.05) * mm});
            skLineSegment(sketch, "E6112", {"start": v(9.43, 14.05) * mm, "end": v(9.26, 14.31) * mm});
            skLineSegment(sketch, "E6113", {"start": v(9.26, 14.31) * mm, "end": v(9.08, 14.62) * mm});
            skLineSegment(sketch, "E6114", {"start": v(9.08, 14.62) * mm, "end": v(8.91, 14.95) * mm});
            skLineSegment(sketch, "E6115", {"start": v(8.91, 14.95) * mm, "end": v(8.53, 15.85) * mm});
            skLineSegment(sketch, "E6116", {"start": v(8.53, 15.85) * mm, "end": v(8.22, 16.89) * mm});
            skArc(sketch, "E6117", {"start": v(10.11, 12.32) * mm, "mid": v(10.3, 12.86) * mm, "end": v(10.04, 13.38) * mm});
            skArc(sketch, "E6118", {"start": v(10.11, 12.32) * mm, "mid": v(9.89, 12.05) * mm, "end": v(9.67, 11.77) * mm});
            skArc(sketch, "E6119", {"start": v(8.61, 11.63) * mm, "mid": v(9.17, 11.49) * mm, "end": v(9.67, 11.77) * mm});
            skLineSegment(sketch, "E6120", {"start": v(8.61, 11.63) * mm, "end": v(8.27, 11.87) * mm});
            skLineSegment(sketch, "E6121", {"start": v(8.27, 11.87) * mm, "end": v(8.09, 11.97) * mm});
            skLineSegment(sketch, "E6122", {"start": v(8.09, 11.97) * mm, "end": v(7.84, 12.09) * mm});
            skLineSegment(sketch, "E6123", {"start": v(7.84, 12.09) * mm, "end": v(7.54, 12.2) * mm});
            skLineSegment(sketch, "E6124", {"start": v(7.54, 12.2) * mm, "end": v(7.2, 12.31) * mm});
            skLineSegment(sketch, "E6125", {"start": v(7.2, 12.31) * mm, "end": v(6.85, 12.41) * mm});
            skLineSegment(sketch, "E6126", {"start": v(6.85, 12.41) * mm, "end": v(5.89, 12.6) * mm});
            skLineSegment(sketch, "E6127", {"start": v(5.89, 12.6) * mm, "end": v(4.8, 12.7) * mm});
            skArc(sketch, "E6128", {"start": v(4.8, 12.7) * mm, "mid": v(4.43, 12.1) * mm, "end": v(4.07, 11.49) * mm});
            skLineSegment(sketch, "E6129", {"start": v(6.77, 8.6) * mm, "end": v(6.4, 8.8) * mm});
            skLineSegment(sketch, "E6130", {"start": v(6.4, 8.8) * mm, "end": v(6.22, 8.91) * mm});
            skLineSegment(sketch, "E6131", {"start": v(6.22, 8.91) * mm, "end": v(6, 9.08) * mm});
            skLineSegment(sketch, "E6132", {"start": v(6, 9.08) * mm, "end": v(5.77, 9.29) * mm});
            skLineSegment(sketch, "E6133", {"start": v(5.77, 9.29) * mm, "end": v(5.52, 9.53) * mm});
            skLineSegment(sketch, "E6134", {"start": v(5.52, 9.53) * mm, "end": v(5.26, 9.8) * mm});
            skLineSegment(sketch, "E6135", {"start": v(5.26, 9.8) * mm, "end": v(4.66, 10.58) * mm});
            skLineSegment(sketch, "E6136", {"start": v(4.66, 10.58) * mm, "end": v(4.07, 11.49) * mm});
            skArc(sketch, "E6137", {"start": v(7.13, 7.6) * mm, "mid": v(7.16, 8.17) * mm, "end": v(6.77, 8.6) * mm});
            skArc(sketch, "E6138", {"start": v(7.13, 7.6) * mm, "mid": v(6.99, 7.28) * mm, "end": v(6.85, 6.95) * mm});
            skArc(sketch, "E6139", {"start": v(5.87, 6.53) * mm, "mid": v(6.45, 6.54) * mm, "end": v(6.85, 6.95) * mm});
            skLineSegment(sketch, "E6140", {"start": v(5.87, 6.53) * mm, "end": v(5.47, 6.67) * mm});
            skLineSegment(sketch, "E6141", {"start": v(5.47, 6.67) * mm, "end": v(5.27, 6.72) * mm});
            skLineSegment(sketch, "E6142", {"start": v(5.27, 6.72) * mm, "end": v(5, 6.76) * mm});
            skLineSegment(sketch, "E6143", {"start": v(5, 6.76) * mm, "end": v(4.69, 6.8) * mm});
            skLineSegment(sketch, "E6144", {"start": v(4.69, 6.8) * mm, "end": v(4.34, 6.81) * mm});
            skLineSegment(sketch, "E6145", {"start": v(4.34, 6.81) * mm, "end": v(3.96, 6.8) * mm});
            skLineSegment(sketch, "E6146", {"start": v(3.96, 6.8) * mm, "end": v(2.99, 6.73) * mm});
            skLineSegment(sketch, "E6147", {"start": v(2.99, 6.73) * mm, "end": v(1.92, 6.53) * mm});
            skArc(sketch, "E6148", {"start": v(1.92, 6.53) * mm, "mid": v(1.72, 5.85) * mm, "end": v(1.54, 5.17) * mm});
            skLineSegment(sketch, "E6149", {"start": v(4.92, 3.12) * mm, "end": v(4.5, 3.2) * mm});
            skLineSegment(sketch, "E6150", {"start": v(4.5, 3.2) * mm, "end": v(4.3, 3.27) * mm});
            skLineSegment(sketch, "E6151", {"start": v(4.3, 3.27) * mm, "end": v(4.05, 3.37) * mm});
            skLineSegment(sketch, "E6152", {"start": v(4.05, 3.37) * mm, "end": v(3.77, 3.51) * mm});
            skLineSegment(sketch, "E6153", {"start": v(3.77, 3.51) * mm, "end": v(3.46, 3.68) * mm});
            skLineSegment(sketch, "E6154", {"start": v(3.46, 3.68) * mm, "end": v(3.14, 3.87) * mm});
            skLineSegment(sketch, "E6155", {"start": v(3.14, 3.87) * mm, "end": v(2.35, 4.45) * mm});
            skLineSegment(sketch, "E6156", {"start": v(2.35, 4.45) * mm, "end": v(1.54, 5.17) * mm});
            skArc(sketch, "E6157", {"start": v(5.53, 2.25) * mm, "mid": v(5.4, 2.8) * mm, "end": v(4.92, 3.12) * mm});
            skArc(sketch, "E6158", {"start": v(5.53, 2.25) * mm, "mid": v(5.48, 1.9) * mm, "end": v(5.44, 1.55) * mm});
            skArc(sketch, "E6159", {"start": v(4.6, 0.88) * mm, "mid": v(5.16, 1.05) * mm, "end": v(5.44, 1.55) * mm});
            skLineSegment(sketch, "E6160", {"start": v(4.6, 0.88) * mm, "end": v(4.19, 0.9) * mm});
            skLineSegment(sketch, "E6161", {"start": v(4.19, 0.9) * mm, "end": v(3.98, 0.9) * mm});
            skLineSegment(sketch, "E6162", {"start": v(3.98, 0.9) * mm, "end": v(3.7, 0.87) * mm});
            skLineSegment(sketch, "E6163", {"start": v(3.7, 0.87) * mm, "end": v(3.4, 0.81) * mm});
            skLineSegment(sketch, "E6164", {"start": v(3.4, 0.81) * mm, "end": v(3.05, 0.74) * mm});
            skLineSegment(sketch, "E6165", {"start": v(3.05, 0.74) * mm, "end": v(2.7, 0.63) * mm});
            skLineSegment(sketch, "E6166", {"start": v(2.7, 0.63) * mm, "end": v(1.78, 0.3) * mm});
            skSolve(sketch);
        }
        {
            var Q0;
            Q0=qCreatedBy(makeId("Front.planeOp"),FACE);
            var sketch = newSketch(context, id + "F3", { "sketchPlane" : qUnion([Q0])});
            skArc(sketch, "E6167", {"start": v(-10, 21.45) * mm, "mid": v(-10.75, 18.07) * mm, "end": v(-12.86, 15.32) * mm});
            skLineSegment(sketch, "E6168", {"start": v(-10, 48.79) * mm, "end": v(-10, 21.45) * mm});
            skArc(sketch, "E6169", {"start": v(-20.77, 56.3) * mm, "mid": v(-13.43, 55.35) * mm, "end": v(-10, 48.79) * mm});
            skArc(sketch, "E6170", {"start": v(-59.13, -10.16) * mm, "mid": v(-51.96, 30) * mm, "end": v(-20.77, 56.3) * mm});
            skArc(sketch, "E6171", {"start": v(-47.25, -15.73) * mm, "mid": v(-54.65, -16.05) * mm, "end": v(-59.13, -10.16) * mm});
            skLineSegment(sketch, "E6172", {"start": v(-47.25, -15.73) * mm, "end": v(-23.57, -2.06) * mm});
            skArc(sketch, "E6173", {"start": v(-19.7, 3.47) * mm, "mid": v(-21.02, 0.28) * mm, "end": v(-23.57, -2.06) * mm});
            skArc(sketch, "E6174", {"start": v(-19.7, 3.47) * mm, "mid": v(-17.32, 10) * mm, "end": v(-12.86, 15.32) * mm});
            skArc(sketch, "E6175", {"start": v(-65.95, 40.7) * mm, "mid": v(-66.08, 40.5) * mm, "end": v(-66.2, 40.28) * mm});
            skArc(sketch, "E6176", {"start": v(-65.95, 40.7) * mm, "mid": v(-65.85, 41.12) * mm, "end": v(-66.03, 41.5) * mm});
            skLineSegment(sketch, "E6177", {"start": v(-67.47, 43.26) * mm, "end": v(-68.62, 44.9) * mm});
            skLineSegment(sketch, "E6178", {"start": v(-66.03, 41.5) * mm, "end": v(-67.47, 43.26) * mm});
            skArc(sketch, "E6179", {"start": v(-67.74, 46.22) * mm, "mid": v(-68.18, 45.56) * mm, "end": v(-68.62, 44.9) * mm});
            skLineSegment(sketch, "E6180", {"start": v(-65.79, 45.78) * mm, "end": v(-67.74, 46.22) * mm});
            skLineSegment(sketch, "E6181", {"start": v(-63.61, 45.12) * mm, "end": v(-65.79, 45.78) * mm});
            skArc(sketch, "E6182", {"start": v(-63.61, 45.12) * mm, "mid": v(-63.19, 45.1) * mm, "end": v(-62.84, 45.35) * mm});
            skArc(sketch, "E6183", {"start": v(-62.55, 45.75) * mm, "mid": v(-62.7, 45.55) * mm, "end": v(-62.84, 45.35) * mm});
            skArc(sketch, "E6184", {"start": v(-62.55, 45.75) * mm, "mid": v(-62.42, 46.16) * mm, "end": v(-62.57, 46.56) * mm});
            skLineSegment(sketch, "E6185", {"start": v(-63.87, 48.42) * mm, "end": v(-64.89, 50.14) * mm});
            skLineSegment(sketch, "E6186", {"start": v(-62.57, 46.56) * mm, "end": v(-63.87, 48.42) * mm});
            skArc(sketch, "E6187", {"start": v(-63.9, 51.39) * mm, "mid": v(-64.4, 50.77) * mm, "end": v(-64.89, 50.14) * mm});
            skLineSegment(sketch, "E6188", {"start": v(-62, 50.8) * mm, "end": v(-63.9, 51.39) * mm});
            skLineSegment(sketch, "E6189", {"start": v(-59.88, 49.97) * mm, "end": v(-62, 50.8) * mm});
            skArc(sketch, "E6190", {"start": v(-59.88, 49.97) * mm, "mid": v(-59.46, 49.92) * mm, "end": v(-59.1, 50.14) * mm});
            skArc(sketch, "E6191", {"start": v(-58.77, 50.52) * mm, "mid": v(-58.93, 50.33) * mm, "end": v(-59.1, 50.14) * mm});
            skArc(sketch, "E6192", {"start": v(-58.77, 50.52) * mm, "mid": v(-58.61, 50.91) * mm, "end": v(-58.72, 51.32) * mm});
            skLineSegment(sketch, "E6193", {"start": v(-59.88, 53.28) * mm, "end": v(-60.75, 55.08) * mm});
            skLineSegment(sketch, "E6194", {"start": v(-58.72, 51.32) * mm, "end": v(-59.88, 53.28) * mm});
            skArc(sketch, "E6195", {"start": v(-59.67, 56.24) * mm, "mid": v(-60.21, 55.66) * mm, "end": v(-60.75, 55.08) * mm});
            skLineSegment(sketch, "E6196", {"start": v(-57.81, 55.51) * mm, "end": v(-59.67, 56.24) * mm});
            skLineSegment(sketch, "E6197", {"start": v(-55.77, 54.51) * mm, "end": v(-57.81, 55.51) * mm});
            skArc(sketch, "E6198", {"start": v(-55.77, 54.51) * mm, "mid": v(-55.36, 54.43) * mm, "end": v(-54.98, 54.63) * mm});
            skArc(sketch, "E6199", {"start": v(-54.63, 54.98) * mm, "mid": v(-54.8, 54.8) * mm, "end": v(-54.98, 54.63) * mm});
            skArc(sketch, "E6200", {"start": v(-54.63, 54.98) * mm, "mid": v(-54.43, 55.36) * mm, "end": v(-54.51, 55.77) * mm});
            skLineSegment(sketch, "E6201", {"start": v(-55.51, 57.81) * mm, "end": v(-56.24, 59.67) * mm});
            skLineSegment(sketch, "E6202", {"start": v(-54.51, 55.77) * mm, "end": v(-55.51, 57.81) * mm});
            skArc(sketch, "E6203", {"start": v(-55.08, 60.75) * mm, "mid": v(-55.66, 60.21) * mm, "end": v(-56.24, 59.67) * mm});
            skLineSegment(sketch, "E6204", {"start": v(-53.28, 59.88) * mm, "end": v(-55.08, 60.75) * mm});
            skLineSegment(sketch, "E6205", {"start": v(-51.32, 58.72) * mm, "end": v(-53.28, 59.88) * mm});
            skArc(sketch, "E6206", {"start": v(-51.32, 58.72) * mm, "mid": v(-50.91, 58.61) * mm, "end": v(-50.52, 58.77) * mm});
            skArc(sketch, "E6207", {"start": v(-50.14, 59.1) * mm, "mid": v(-50.33, 58.93) * mm, "end": v(-50.52, 58.77) * mm});
            skArc(sketch, "E6208", {"start": v(-50.14, 59.1) * mm, "mid": v(-49.92, 59.46) * mm, "end": v(-49.97, 59.88) * mm});
            skLineSegment(sketch, "E6209", {"start": v(-50.8, 62) * mm, "end": v(-51.39, 63.9) * mm});
            skLineSegment(sketch, "E6210", {"start": v(-49.97, 59.88) * mm, "end": v(-50.8, 62) * mm});
            skArc(sketch, "E6211", {"start": v(-50.14, 64.89) * mm, "mid": v(-50.77, 64.4) * mm, "end": v(-51.39, 63.9) * mm});
            skLineSegment(sketch, "E6212", {"start": v(-48.42, 63.87) * mm, "end": v(-50.14, 64.89) * mm});
            skLineSegment(sketch, "E6213", {"start": v(-46.56, 62.57) * mm, "end": v(-48.42, 63.87) * mm});
            skArc(sketch, "E6214", {"start": v(-46.56, 62.57) * mm, "mid": v(-46.16, 62.42) * mm, "end": v(-45.75, 62.55) * mm});
            skArc(sketch, "E6215", {"start": v(-45.35, 62.84) * mm, "mid": v(-45.55, 62.7) * mm, "end": v(-45.75, 62.55) * mm});
            skArc(sketch, "E6216", {"start": v(-45.35, 62.84) * mm, "mid": v(-45.1, 63.19) * mm, "end": v(-45.12, 63.61) * mm});
            skLineSegment(sketch, "E6217", {"start": v(-45.78, 65.79) * mm, "end": v(-46.22, 67.74) * mm});
            skLineSegment(sketch, "E6218", {"start": v(-45.12, 63.61) * mm, "end": v(-45.78, 65.79) * mm});
            skArc(sketch, "E6219", {"start": v(-44.9, 68.62) * mm, "mid": v(-45.56, 68.18) * mm, "end": v(-46.22, 67.74) * mm});
            skLineSegment(sketch, "E6220", {"start": v(-43.26, 67.47) * mm, "end": v(-44.9, 68.62) * mm});
            skLineSegment(sketch, "E6221", {"start": v(-41.5, 66.03) * mm, "end": v(-43.26, 67.47) * mm});
            skArc(sketch, "E6222", {"start": v(-41.5, 66.03) * mm, "mid": v(-41.12, 65.85) * mm, "end": v(-40.7, 65.95) * mm});
            skArc(sketch, "E6223", {"start": v(-40.28, 66.2) * mm, "mid": v(-40.5, 66.08) * mm, "end": v(-40.7, 65.95) * mm});
            skArc(sketch, "E6224", {"start": v(-40.28, 66.2) * mm, "mid": v(-40, 66.53) * mm, "end": v(-39.99, 66.96) * mm});
            skLineSegment(sketch, "E6225", {"start": v(-40.48, 69.17) * mm, "end": v(-40.76, 71.15) * mm});
            skLineSegment(sketch, "E6226", {"start": v(-39.99, 66.96) * mm, "end": v(-40.48, 69.17) * mm});
            skArc(sketch, "E6227", {"start": v(-39.37, 71.93) * mm, "mid": v(-40.07, 71.54) * mm, "end": v(-40.76, 71.15) * mm});
            skLineSegment(sketch, "E6228", {"start": v(-37.83, 70.66) * mm, "end": v(-39.37, 71.93) * mm});
            skLineSegment(sketch, "E6229", {"start": v(-36.2, 69.08) * mm, "end": v(-37.83, 70.66) * mm});
            skArc(sketch, "E6230", {"start": v(-36.2, 69.08) * mm, "mid": v(-35.82, 68.88) * mm, "end": v(-35.4, 68.94) * mm});
            skArc(sketch, "E6231", {"start": v(-34.96, 69.17) * mm, "mid": v(-35.18, 69.05) * mm, "end": v(-35.4, 68.94) * mm});
            skArc(sketch, "E6232", {"start": v(-34.96, 69.17) * mm, "mid": v(-34.66, 69.47) * mm, "end": v(-34.6, 69.89) * mm});
            skLineSegment(sketch, "E6233", {"start": v(-34.93, 72.14) * mm, "end": v(-35.05, 74.13) * mm});
            skLineSegment(sketch, "E6234", {"start": v(-34.6, 69.89) * mm, "end": v(-34.93, 72.14) * mm});
            skArc(sketch, "E6235", {"start": v(-33.6, 74.8) * mm, "mid": v(-34.33, 74.47) * mm, "end": v(-35.05, 74.13) * mm});
            skLineSegment(sketch, "E6236", {"start": v(-32.17, 73.4) * mm, "end": v(-33.6, 74.8) * mm});
            skLineSegment(sketch, "E6237", {"start": v(-30.67, 71.7) * mm, "end": v(-32.17, 73.4) * mm});
            skArc(sketch, "E6238", {"start": v(-30.67, 71.7) * mm, "mid": v(-30.31, 71.47) * mm, "end": v(-29.89, 71.5) * mm});
            skArc(sketch, "E6239", {"start": v(-29.43, 71.7) * mm, "mid": v(-29.66, 71.6) * mm, "end": v(-29.89, 71.5) * mm});
            skArc(sketch, "E6240", {"start": v(-29.43, 71.7) * mm, "mid": v(-29.1, 71.97) * mm, "end": v(-29.02, 72.39) * mm});
            skLineSegment(sketch, "E6241", {"start": v(-29.16, 74.66) * mm, "end": v(-29.13, 76.65) * mm});
            skLineSegment(sketch, "E6242", {"start": v(-29.02, 72.39) * mm, "end": v(-29.16, 74.66) * mm});
            skArc(sketch, "E6243", {"start": v(-27.63, 77.2) * mm, "mid": v(-28.38, 76.93) * mm, "end": v(-29.13, 76.65) * mm});
            skLineSegment(sketch, "E6244", {"start": v(-26.31, 75.7) * mm, "end": v(-27.63, 77.2) * mm});
            skLineSegment(sketch, "E6245", {"start": v(-24.95, 73.9) * mm, "end": v(-26.31, 75.7) * mm});
            skArc(sketch, "E6246", {"start": v(-24.95, 73.9) * mm, "mid": v(-24.6, 73.63) * mm, "end": v(-24.18, 73.63) * mm});
            skArc(sketch, "E6247", {"start": v(-23.71, 73.78) * mm, "mid": v(-23.95, 73.7) * mm, "end": v(-24.18, 73.63) * mm});
            skArc(sketch, "E6248", {"start": v(-23.71, 73.78) * mm, "mid": v(-23.37, 74.03) * mm, "end": v(-23.25, 74.44) * mm});
            skLineSegment(sketch, "E6249", {"start": v(-23.21, 76.71) * mm, "end": v(-23.02, 78.7) * mm});
            skLineSegment(sketch, "E6250", {"start": v(-23.25, 74.44) * mm, "end": v(-23.21, 76.71) * mm});
            skArc(sketch, "E6251", {"start": v(-21.5, 79.13) * mm, "mid": v(-22.26, 78.92) * mm, "end": v(-23.02, 78.7) * mm});
            skLineSegment(sketch, "E6252", {"start": v(-20.29, 77.54) * mm, "end": v(-21.5, 79.13) * mm});
            skLineSegment(sketch, "E6253", {"start": v(-19.07, 75.62) * mm, "end": v(-20.29, 77.54) * mm});
            skArc(sketch, "E6254", {"start": v(-19.07, 75.62) * mm, "mid": v(-18.76, 75.34) * mm, "end": v(-18.33, 75.3) * mm});
            skArc(sketch, "E6255", {"start": v(-17.85, 75.42) * mm, "mid": v(-18.1, 75.36) * mm, "end": v(-18.33, 75.3) * mm});
            skArc(sketch, "E6256", {"start": v(-17.85, 75.42) * mm, "mid": v(-17.5, 75.64) * mm, "end": v(-17.34, 76.04) * mm});
            skLineSegment(sketch, "E6257", {"start": v(-17.12, 78.3) * mm, "end": v(-16.78, 80.27) * mm});
            skLineSegment(sketch, "E6258", {"start": v(-17.34, 76.04) * mm, "end": v(-17.12, 78.3) * mm});
            skArc(sketch, "E6259", {"start": v(-15.22, 80.58) * mm, "mid": v(-16, 80.42) * mm, "end": v(-16.78, 80.27) * mm});
            skLineSegment(sketch, "E6260", {"start": v(-14.14, 78.9) * mm, "end": v(-15.22, 80.58) * mm});
            skLineSegment(sketch, "E6261", {"start": v(-13.08, 76.88) * mm, "end": v(-14.14, 78.9) * mm});
            skArc(sketch, "E6262", {"start": v(-13.08, 76.88) * mm, "mid": v(-12.79, 76.58) * mm, "end": v(-12.37, 76.5) * mm});
            skArc(sketch, "E6263", {"start": v(-11.88, 76.58) * mm, "mid": v(-12.12, 76.55) * mm, "end": v(-12.37, 76.5) * mm});
            skArc(sketch, "E6264", {"start": v(-11.88, 76.58) * mm, "mid": v(-11.5, 76.78) * mm, "end": v(-11.32, 77.16) * mm});
            skLineSegment(sketch, "E6265", {"start": v(-10.93, 79.4) * mm, "end": v(-10.43, 81.33) * mm});
            skLineSegment(sketch, "E6266", {"start": v(-11.32, 77.16) * mm, "end": v(-10.93, 79.4) * mm});
            skArc(sketch, "E6267", {"start": v(-8.85, 81.52) * mm, "mid": v(-9.64, 81.43) * mm, "end": v(-10.43, 81.33) * mm});
            skLineSegment(sketch, "E6268", {"start": v(-7.9, 79.76) * mm, "end": v(-8.85, 81.52) * mm});
            skLineSegment(sketch, "E6269", {"start": v(-7, 77.67) * mm, "end": v(-7.9, 79.76) * mm});
            skArc(sketch, "E6270", {"start": v(-7, 77.67) * mm, "mid": v(-6.74, 77.34) * mm, "end": v(-6.33, 77.24) * mm});
            skArc(sketch, "E6271", {"start": v(-5.83, 77.28) * mm, "mid": v(-6.08, 77.26) * mm, "end": v(-6.33, 77.24) * mm});
            skArc(sketch, "E6272", {"start": v(-5.83, 77.28) * mm, "mid": v(-5.44, 77.45) * mm, "end": v(-5.23, 77.81) * mm});
            skLineSegment(sketch, "E6273", {"start": v(-4.66, 80.01) * mm, "end": v(-4.01, 81.9) * mm});
            skLineSegment(sketch, "E6274", {"start": v(-5.23, 77.81) * mm, "end": v(-4.66, 80.01) * mm});
            skArc(sketch, "E6275", {"start": v(-2.42, 81.96) * mm, "mid": v(-3.22, 81.94) * mm, "end": v(-4.01, 81.9) * mm});
            skLineSegment(sketch, "E6276", {"start": v(-1.63, 80.13) * mm, "end": v(-2.42, 81.96) * mm});
            skLineSegment(sketch, "E6277", {"start": v(-0.9, 77.98) * mm, "end": v(-1.63, 80.13) * mm});
            skArc(sketch, "E6278", {"start": v(-0.9, 77.98) * mm, "mid": v(-0.65, 77.63) * mm, "end": v(-0.25, 77.5) * mm});
            skArc(sketch, "E6279", {"start": v(0.25, 77.5) * mm, "mid": v(0, 77.5) * mm, "end": v(-0.25, 77.5) * mm});
            skArc(sketch, "E6280", {"start": v(0.25, 77.5) * mm, "mid": v(0.65, 77.63) * mm, "end": v(0.9, 77.98) * mm});
            skLineSegment(sketch, "E6281", {"start": v(1.63, 80.13) * mm, "end": v(2.42, 81.96) * mm});
            skLineSegment(sketch, "E6282", {"start": v(0.9, 77.98) * mm, "end": v(1.63, 80.13) * mm});
            skArc(sketch, "E6283", {"start": v(4.01, 81.9) * mm, "mid": v(3.22, 81.94) * mm, "end": v(2.42, 81.96) * mm});
            skLineSegment(sketch, "E6284", {"start": v(4.66, 80.01) * mm, "end": v(4.01, 81.9) * mm});
            skLineSegment(sketch, "E6285", {"start": v(5.23, 77.81) * mm, "end": v(4.66, 80.01) * mm});
            skArc(sketch, "E6286", {"start": v(5.23, 77.81) * mm, "mid": v(5.44, 77.45) * mm, "end": v(5.83, 77.28) * mm});
            skArc(sketch, "E6287", {"start": v(6.33, 77.24) * mm, "mid": v(6.08, 77.26) * mm, "end": v(5.83, 77.28) * mm});
            skArc(sketch, "E6288", {"start": v(6.33, 77.24) * mm, "mid": v(6.74, 77.34) * mm, "end": v(7, 77.67) * mm});
            skLineSegment(sketch, "E6289", {"start": v(7.9, 79.76) * mm, "end": v(8.85, 81.52) * mm});
            skLineSegment(sketch, "E6290", {"start": v(7, 77.67) * mm, "end": v(7.9, 79.76) * mm});
            skArc(sketch, "E6291", {"start": v(10.43, 81.33) * mm, "mid": v(9.64, 81.43) * mm, "end": v(8.85, 81.52) * mm});
            skLineSegment(sketch, "E6292", {"start": v(10.93, 79.4) * mm, "end": v(10.43, 81.33) * mm});
            skLineSegment(sketch, "E6293", {"start": v(11.32, 77.16) * mm, "end": v(10.93, 79.4) * mm});
            skArc(sketch, "E6294", {"start": v(11.32, 77.16) * mm, "mid": v(11.5, 76.78) * mm, "end": v(11.88, 76.58) * mm});
            skArc(sketch, "E6295", {"start": v(12.37, 76.5) * mm, "mid": v(12.12, 76.55) * mm, "end": v(11.88, 76.58) * mm});
            skArc(sketch, "E6296", {"start": v(12.37, 76.5) * mm, "mid": v(12.79, 76.58) * mm, "end": v(13.08, 76.88) * mm});
            skLineSegment(sketch, "E6297", {"start": v(14.14, 78.9) * mm, "end": v(15.22, 80.58) * mm});
            skLineSegment(sketch, "E6298", {"start": v(13.08, 76.88) * mm, "end": v(14.14, 78.9) * mm});
            skArc(sketch, "E6299", {"start": v(16.78, 80.27) * mm, "mid": v(16, 80.42) * mm, "end": v(15.22, 80.58) * mm});
            skLineSegment(sketch, "E6300", {"start": v(17.12, 78.3) * mm, "end": v(16.78, 80.27) * mm});
            skLineSegment(sketch, "E6301", {"start": v(17.34, 76.04) * mm, "end": v(17.12, 78.3) * mm});
            skArc(sketch, "E6302", {"start": v(17.34, 76.04) * mm, "mid": v(17.5, 75.64) * mm, "end": v(17.85, 75.42) * mm});
            skArc(sketch, "E6303", {"start": v(18.33, 75.3) * mm, "mid": v(18.1, 75.36) * mm, "end": v(17.85, 75.42) * mm});
            skArc(sketch, "E6304", {"start": v(18.33, 75.3) * mm, "mid": v(18.76, 75.34) * mm, "end": v(19.07, 75.62) * mm});
            skLineSegment(sketch, "E6305", {"start": v(20.29, 77.54) * mm, "end": v(21.5, 79.13) * mm});
            skLineSegment(sketch, "E6306", {"start": v(19.07, 75.62) * mm, "end": v(20.29, 77.54) * mm});
            skArc(sketch, "E6307", {"start": v(23.02, 78.7) * mm, "mid": v(22.26, 78.92) * mm, "end": v(21.5, 79.13) * mm});
            skLineSegment(sketch, "E6308", {"start": v(23.21, 76.71) * mm, "end": v(23.02, 78.7) * mm});
            skLineSegment(sketch, "E6309", {"start": v(23.25, 74.44) * mm, "end": v(23.21, 76.71) * mm});
            skArc(sketch, "E6310", {"start": v(23.25, 74.44) * mm, "mid": v(23.37, 74.03) * mm, "end": v(23.71, 73.78) * mm});
            skArc(sketch, "E6311", {"start": v(24.18, 73.63) * mm, "mid": v(23.95, 73.7) * mm, "end": v(23.71, 73.78) * mm});
            skArc(sketch, "E6312", {"start": v(24.18, 73.63) * mm, "mid": v(24.6, 73.63) * mm, "end": v(24.95, 73.9) * mm});
            skLineSegment(sketch, "E6313", {"start": v(26.31, 75.7) * mm, "end": v(27.63, 77.2) * mm});
            skLineSegment(sketch, "E6314", {"start": v(24.95, 73.9) * mm, "end": v(26.31, 75.7) * mm});
            skArc(sketch, "E6315", {"start": v(29.13, 76.65) * mm, "mid": v(28.38, 76.93) * mm, "end": v(27.63, 77.2) * mm});
            skLineSegment(sketch, "E6316", {"start": v(29.16, 74.66) * mm, "end": v(29.13, 76.65) * mm});
            skLineSegment(sketch, "E6317", {"start": v(29.02, 72.39) * mm, "end": v(29.16, 74.66) * mm});
            skArc(sketch, "E6318", {"start": v(29.02, 72.39) * mm, "mid": v(29.1, 71.97) * mm, "end": v(29.43, 71.7) * mm});
            skArc(sketch, "E6319", {"start": v(29.89, 71.5) * mm, "mid": v(29.66, 71.6) * mm, "end": v(29.43, 71.7) * mm});
            skArc(sketch, "E6320", {"start": v(29.89, 71.5) * mm, "mid": v(30.31, 71.47) * mm, "end": v(30.67, 71.7) * mm});
            skLineSegment(sketch, "E6321", {"start": v(32.17, 73.4) * mm, "end": v(33.6, 74.8) * mm});
            skLineSegment(sketch, "E6322", {"start": v(30.67, 71.7) * mm, "end": v(32.17, 73.4) * mm});
            skArc(sketch, "E6323", {"start": v(35.05, 74.13) * mm, "mid": v(34.33, 74.47) * mm, "end": v(33.6, 74.8) * mm});
            skLineSegment(sketch, "E6324", {"start": v(34.93, 72.14) * mm, "end": v(35.05, 74.13) * mm});
            skLineSegment(sketch, "E6325", {"start": v(34.6, 69.89) * mm, "end": v(34.93, 72.14) * mm});
            skArc(sketch, "E6326", {"start": v(34.6, 69.89) * mm, "mid": v(34.66, 69.47) * mm, "end": v(34.96, 69.17) * mm});
            skArc(sketch, "E6327", {"start": v(35.4, 68.94) * mm, "mid": v(35.18, 69.05) * mm, "end": v(34.96, 69.17) * mm});
            skArc(sketch, "E6328", {"start": v(35.4, 68.94) * mm, "mid": v(35.82, 68.88) * mm, "end": v(36.2, 69.08) * mm});
            skLineSegment(sketch, "E6329", {"start": v(37.83, 70.66) * mm, "end": v(39.37, 71.93) * mm});
            skLineSegment(sketch, "E6330", {"start": v(36.2, 69.08) * mm, "end": v(37.83, 70.66) * mm});
            skArc(sketch, "E6331", {"start": v(40.76, 71.15) * mm, "mid": v(40.07, 71.54) * mm, "end": v(39.37, 71.93) * mm});
            skLineSegment(sketch, "E6332", {"start": v(40.48, 69.17) * mm, "end": v(40.76, 71.15) * mm});
            skLineSegment(sketch, "E6333", {"start": v(39.99, 66.96) * mm, "end": v(40.48, 69.17) * mm});
            skArc(sketch, "E6334", {"start": v(39.99, 66.96) * mm, "mid": v(40, 66.53) * mm, "end": v(40.28, 66.2) * mm});
            skArc(sketch, "E6335", {"start": v(40.7, 65.95) * mm, "mid": v(40.5, 66.08) * mm, "end": v(40.28, 66.2) * mm});
            skArc(sketch, "E6336", {"start": v(40.7, 65.95) * mm, "mid": v(41.12, 65.85) * mm, "end": v(41.5, 66.03) * mm});
            skLineSegment(sketch, "E6337", {"start": v(43.26, 67.47) * mm, "end": v(44.9, 68.62) * mm});
            skLineSegment(sketch, "E6338", {"start": v(41.5, 66.03) * mm, "end": v(43.26, 67.47) * mm});
            skArc(sketch, "E6339", {"start": v(46.22, 67.74) * mm, "mid": v(45.56, 68.18) * mm, "end": v(44.9, 68.62) * mm});
            skLineSegment(sketch, "E6340", {"start": v(45.78, 65.79) * mm, "end": v(46.22, 67.74) * mm});
            skLineSegment(sketch, "E6341", {"start": v(45.12, 63.61) * mm, "end": v(45.78, 65.79) * mm});
            skArc(sketch, "E6342", {"start": v(45.12, 63.61) * mm, "mid": v(45.1, 63.19) * mm, "end": v(45.35, 62.84) * mm});
            skArc(sketch, "E6343", {"start": v(45.75, 62.55) * mm, "mid": v(45.55, 62.7) * mm, "end": v(45.35, 62.84) * mm});
            skArc(sketch, "E6344", {"start": v(45.75, 62.55) * mm, "mid": v(46.16, 62.42) * mm, "end": v(46.56, 62.57) * mm});
            skLineSegment(sketch, "E6345", {"start": v(48.42, 63.87) * mm, "end": v(50.14, 64.89) * mm});
            skLineSegment(sketch, "E6346", {"start": v(46.56, 62.57) * mm, "end": v(48.42, 63.87) * mm});
            skArc(sketch, "E6347", {"start": v(51.39, 63.9) * mm, "mid": v(50.77, 64.4) * mm, "end": v(50.14, 64.89) * mm});
            skLineSegment(sketch, "E6348", {"start": v(50.8, 62) * mm, "end": v(51.39, 63.9) * mm});
            skLineSegment(sketch, "E6349", {"start": v(49.97, 59.88) * mm, "end": v(50.8, 62) * mm});
            skArc(sketch, "E6350", {"start": v(49.97, 59.88) * mm, "mid": v(49.92, 59.46) * mm, "end": v(50.14, 59.1) * mm});
            skArc(sketch, "E6351", {"start": v(50.52, 58.77) * mm, "mid": v(50.33, 58.93) * mm, "end": v(50.14, 59.1) * mm});
            skArc(sketch, "E6352", {"start": v(50.52, 58.77) * mm, "mid": v(50.91, 58.61) * mm, "end": v(51.32, 58.72) * mm});
            skLineSegment(sketch, "E6353", {"start": v(53.28, 59.88) * mm, "end": v(55.08, 60.75) * mm});
            skLineSegment(sketch, "E6354", {"start": v(51.32, 58.72) * mm, "end": v(53.28, 59.88) * mm});
            skArc(sketch, "E6355", {"start": v(56.24, 59.67) * mm, "mid": v(55.66, 60.21) * mm, "end": v(55.08, 60.75) * mm});
            skLineSegment(sketch, "E6356", {"start": v(55.51, 57.81) * mm, "end": v(56.24, 59.67) * mm});
            skLineSegment(sketch, "E6357", {"start": v(54.51, 55.77) * mm, "end": v(55.51, 57.81) * mm});
            skArc(sketch, "E6358", {"start": v(54.51, 55.77) * mm, "mid": v(54.43, 55.36) * mm, "end": v(54.63, 54.98) * mm});
            skArc(sketch, "E6359", {"start": v(54.98, 54.63) * mm, "mid": v(54.8, 54.8) * mm, "end": v(54.63, 54.98) * mm});
            skArc(sketch, "E6360", {"start": v(54.98, 54.63) * mm, "mid": v(55.36, 54.43) * mm, "end": v(55.77, 54.51) * mm});
            skLineSegment(sketch, "E6361", {"start": v(57.81, 55.51) * mm, "end": v(59.67, 56.24) * mm});
            skLineSegment(sketch, "E6362", {"start": v(55.77, 54.51) * mm, "end": v(57.81, 55.51) * mm});
            skArc(sketch, "E6363", {"start": v(60.75, 55.08) * mm, "mid": v(60.21, 55.66) * mm, "end": v(59.67, 56.24) * mm});
            skLineSegment(sketch, "E6364", {"start": v(59.88, 53.28) * mm, "end": v(60.75, 55.08) * mm});
            skLineSegment(sketch, "E6365", {"start": v(58.72, 51.32) * mm, "end": v(59.88, 53.28) * mm});
            skArc(sketch, "E6366", {"start": v(58.72, 51.32) * mm, "mid": v(58.61, 50.91) * mm, "end": v(58.77, 50.52) * mm});
            skArc(sketch, "E6367", {"start": v(59.1, 50.14) * mm, "mid": v(58.93, 50.33) * mm, "end": v(58.77, 50.52) * mm});
            skArc(sketch, "E6368", {"start": v(59.1, 50.14) * mm, "mid": v(59.46, 49.92) * mm, "end": v(59.88, 49.97) * mm});
            skLineSegment(sketch, "E6369", {"start": v(62, 50.8) * mm, "end": v(63.9, 51.39) * mm});
            skLineSegment(sketch, "E6370", {"start": v(59.88, 49.97) * mm, "end": v(62, 50.8) * mm});
            skArc(sketch, "E6371", {"start": v(64.89, 50.14) * mm, "mid": v(64.4, 50.77) * mm, "end": v(63.9, 51.39) * mm});
            skLineSegment(sketch, "E6372", {"start": v(63.87, 48.42) * mm, "end": v(64.89, 50.14) * mm});
            skLineSegment(sketch, "E6373", {"start": v(62.57, 46.56) * mm, "end": v(63.87, 48.42) * mm});
            skArc(sketch, "E6374", {"start": v(62.57, 46.56) * mm, "mid": v(62.42, 46.16) * mm, "end": v(62.55, 45.75) * mm});
            skArc(sketch, "E6375", {"start": v(62.84, 45.35) * mm, "mid": v(62.7, 45.55) * mm, "end": v(62.55, 45.75) * mm});
            skArc(sketch, "E6376", {"start": v(62.84, 45.35) * mm, "mid": v(63.19, 45.1) * mm, "end": v(63.61, 45.12) * mm});
            skLineSegment(sketch, "E6377", {"start": v(65.79, 45.78) * mm, "end": v(67.74, 46.22) * mm});
            skLineSegment(sketch, "E6378", {"start": v(63.61, 45.12) * mm, "end": v(65.79, 45.78) * mm});
            skArc(sketch, "E6379", {"start": v(68.62, 44.9) * mm, "mid": v(68.18, 45.56) * mm, "end": v(67.74, 46.22) * mm});
            skLineSegment(sketch, "E6380", {"start": v(67.47, 43.26) * mm, "end": v(68.62, 44.9) * mm});
            skLineSegment(sketch, "E6381", {"start": v(66.03, 41.5) * mm, "end": v(67.47, 43.26) * mm});
            skArc(sketch, "E6382", {"start": v(66.03, 41.5) * mm, "mid": v(65.85, 41.12) * mm, "end": v(65.95, 40.7) * mm});
            skArc(sketch, "E6383", {"start": v(66.2, 40.28) * mm, "mid": v(66.08, 40.5) * mm, "end": v(65.95, 40.7) * mm});
            skArc(sketch, "E6384", {"start": v(66.2, 40.28) * mm, "mid": v(66.53, 40) * mm, "end": v(66.96, 39.99) * mm});
            skLineSegment(sketch, "E6385", {"start": v(69.17, 40.48) * mm, "end": v(71.15, 40.76) * mm});
            skLineSegment(sketch, "E6386", {"start": v(66.96, 39.99) * mm, "end": v(69.17, 40.48) * mm});
            skArc(sketch, "E6387", {"start": v(71.93, 39.37) * mm, "mid": v(71.54, 40.07) * mm, "end": v(71.15, 40.76) * mm});
            skLineSegment(sketch, "E6388", {"start": v(70.66, 37.83) * mm, "end": v(71.93, 39.37) * mm});
            skLineSegment(sketch, "E6389", {"start": v(69.08, 36.2) * mm, "end": v(70.66, 37.83) * mm});
            skArc(sketch, "E6390", {"start": v(69.08, 36.2) * mm, "mid": v(68.88, 35.82) * mm, "end": v(68.94, 35.4) * mm});
            skArc(sketch, "E6391", {"start": v(69.17, 34.96) * mm, "mid": v(69.05, 35.18) * mm, "end": v(68.94, 35.4) * mm});
            skArc(sketch, "E6392", {"start": v(69.17, 34.96) * mm, "mid": v(69.47, 34.66) * mm, "end": v(69.89, 34.6) * mm});
            skLineSegment(sketch, "E6393", {"start": v(72.14, 34.93) * mm, "end": v(74.13, 35.05) * mm});
            skLineSegment(sketch, "E6394", {"start": v(69.89, 34.6) * mm, "end": v(72.14, 34.93) * mm});
            skArc(sketch, "E6395", {"start": v(74.8, 33.6) * mm, "mid": v(74.47, 34.33) * mm, "end": v(74.13, 35.05) * mm});
            skLineSegment(sketch, "E6396", {"start": v(73.4, 32.17) * mm, "end": v(74.8, 33.6) * mm});
            skLineSegment(sketch, "E6397", {"start": v(71.7, 30.67) * mm, "end": v(73.4, 32.17) * mm});
            skArc(sketch, "E6398", {"start": v(71.7, 30.67) * mm, "mid": v(71.47, 30.31) * mm, "end": v(71.5, 29.89) * mm});
            skArc(sketch, "E6399", {"start": v(71.7, 29.43) * mm, "mid": v(71.6, 29.66) * mm, "end": v(71.5, 29.89) * mm});
            skArc(sketch, "E6400", {"start": v(71.7, 29.43) * mm, "mid": v(71.97, 29.1) * mm, "end": v(72.39, 29.02) * mm});
            skLineSegment(sketch, "E6401", {"start": v(74.66, 29.16) * mm, "end": v(76.65, 29.13) * mm});
            skLineSegment(sketch, "E6402", {"start": v(72.39, 29.02) * mm, "end": v(74.66, 29.16) * mm});
            skArc(sketch, "E6403", {"start": v(77.2, 27.63) * mm, "mid": v(76.93, 28.38) * mm, "end": v(76.65, 29.13) * mm});
            skLineSegment(sketch, "E6404", {"start": v(75.7, 26.31) * mm, "end": v(77.2, 27.63) * mm});
            skLineSegment(sketch, "E6405", {"start": v(73.9, 24.95) * mm, "end": v(75.7, 26.31) * mm});
            skArc(sketch, "E6406", {"start": v(73.9, 24.95) * mm, "mid": v(73.63, 24.6) * mm, "end": v(73.63, 24.18) * mm});
            skArc(sketch, "E6407", {"start": v(73.78, 23.71) * mm, "mid": v(73.7, 23.95) * mm, "end": v(73.63, 24.18) * mm});
            skArc(sketch, "E6408", {"start": v(73.78, 23.71) * mm, "mid": v(74.03, 23.37) * mm, "end": v(74.44, 23.25) * mm});
            skLineSegment(sketch, "E6409", {"start": v(76.71, 23.21) * mm, "end": v(78.7, 23.02) * mm});
            skLineSegment(sketch, "E6410", {"start": v(74.44, 23.25) * mm, "end": v(76.71, 23.21) * mm});
            skArc(sketch, "E6411", {"start": v(79.13, 21.5) * mm, "mid": v(78.92, 22.26) * mm, "end": v(78.7, 23.02) * mm});
            skLineSegment(sketch, "E6412", {"start": v(77.54, 20.29) * mm, "end": v(79.13, 21.5) * mm});
            skLineSegment(sketch, "E6413", {"start": v(75.62, 19.07) * mm, "end": v(77.54, 20.29) * mm});
            skArc(sketch, "E6414", {"start": v(75.62, 19.07) * mm, "mid": v(75.34, 18.76) * mm, "end": v(75.3, 18.33) * mm});
            skArc(sketch, "E6415", {"start": v(75.42, 17.85) * mm, "mid": v(75.36, 18.1) * mm, "end": v(75.3, 18.33) * mm});
            skArc(sketch, "E6416", {"start": v(75.42, 17.85) * mm, "mid": v(75.64, 17.5) * mm, "end": v(76.04, 17.34) * mm});
            skLineSegment(sketch, "E6417", {"start": v(78.3, 17.12) * mm, "end": v(80.27, 16.78) * mm});
            skLineSegment(sketch, "E6418", {"start": v(76.04, 17.34) * mm, "end": v(78.3, 17.12) * mm});
            skArc(sketch, "E6419", {"start": v(80.58, 15.22) * mm, "mid": v(80.42, 16) * mm, "end": v(80.27, 16.78) * mm});
            skLineSegment(sketch, "E6420", {"start": v(78.9, 14.14) * mm, "end": v(80.58, 15.22) * mm});
            skLineSegment(sketch, "E6421", {"start": v(76.88, 13.08) * mm, "end": v(78.9, 14.14) * mm});
            skArc(sketch, "E6422", {"start": v(76.88, 13.08) * mm, "mid": v(76.58, 12.79) * mm, "end": v(76.5, 12.37) * mm});
            skArc(sketch, "E6423", {"start": v(76.58, 11.88) * mm, "mid": v(76.55, 12.12) * mm, "end": v(76.5, 12.37) * mm});
            skArc(sketch, "E6424", {"start": v(-56.24, -59.67) * mm, "mid": v(-55.66, -60.21) * mm, "end": v(-55.08, -60.75) * mm});
            skLineSegment(sketch, "E6425", {"start": v(-51.32, -58.72) * mm, "end": v(-53.28, -59.88) * mm});
            skLineSegment(sketch, "E6426", {"start": v(-53.28, -59.88) * mm, "end": v(-55.08, -60.75) * mm});
            skArc(sketch, "E6427", {"start": v(-50.52, -58.77) * mm, "mid": v(-50.91, -58.61) * mm, "end": v(-51.32, -58.72) * mm});
            skArc(sketch, "E6428", {"start": v(-50.52, -58.77) * mm, "mid": v(-50.33, -58.93) * mm, "end": v(-50.14, -59.1) * mm});
            skArc(sketch, "E6429", {"start": v(-49.97, -59.88) * mm, "mid": v(-49.92, -59.46) * mm, "end": v(-50.14, -59.1) * mm});
            skLineSegment(sketch, "E6430", {"start": v(-49.97, -59.88) * mm, "end": v(-50.8, -62) * mm});
            skLineSegment(sketch, "E6431", {"start": v(-50.8, -62) * mm, "end": v(-51.39, -63.9) * mm});
            skArc(sketch, "E6432", {"start": v(-51.39, -63.9) * mm, "mid": v(-50.77, -64.4) * mm, "end": v(-50.14, -64.89) * mm});
            skLineSegment(sketch, "E6433", {"start": v(-46.56, -62.57) * mm, "end": v(-48.42, -63.87) * mm});
            skLineSegment(sketch, "E6434", {"start": v(-48.42, -63.87) * mm, "end": v(-50.14, -64.89) * mm});
            skArc(sketch, "E6435", {"start": v(-45.75, -62.55) * mm, "mid": v(-46.16, -62.42) * mm, "end": v(-46.56, -62.57) * mm});
            skArc(sketch, "E6436", {"start": v(-45.75, -62.55) * mm, "mid": v(-45.55, -62.7) * mm, "end": v(-45.35, -62.84) * mm});
            skArc(sketch, "E6437", {"start": v(-45.12, -63.61) * mm, "mid": v(-45.1, -63.19) * mm, "end": v(-45.35, -62.84) * mm});
            skLineSegment(sketch, "E6438", {"start": v(-45.12, -63.61) * mm, "end": v(-45.78, -65.79) * mm});
            skLineSegment(sketch, "E6439", {"start": v(-45.78, -65.79) * mm, "end": v(-46.22, -67.74) * mm});
            skArc(sketch, "E6440", {"start": v(-46.22, -67.74) * mm, "mid": v(-45.56, -68.18) * mm, "end": v(-44.9, -68.62) * mm});
            skLineSegment(sketch, "E6441", {"start": v(-41.5, -66.03) * mm, "end": v(-43.26, -67.47) * mm});
            skLineSegment(sketch, "E6442", {"start": v(-43.26, -67.47) * mm, "end": v(-44.9, -68.62) * mm});
            skArc(sketch, "E6443", {"start": v(-40.7, -65.95) * mm, "mid": v(-41.12, -65.85) * mm, "end": v(-41.5, -66.03) * mm});
            skArc(sketch, "E6444", {"start": v(-40.7, -65.95) * mm, "mid": v(-40.5, -66.08) * mm, "end": v(-40.28, -66.2) * mm});
            skArc(sketch, "E6445", {"start": v(-39.99, -66.96) * mm, "mid": v(-40, -66.53) * mm, "end": v(-40.28, -66.2) * mm});
            skLineSegment(sketch, "E6446", {"start": v(-39.99, -66.96) * mm, "end": v(-40.48, -69.17) * mm});
            skLineSegment(sketch, "E6447", {"start": v(-40.48, -69.17) * mm, "end": v(-40.76, -71.15) * mm});
            skArc(sketch, "E6448", {"start": v(-40.76, -71.15) * mm, "mid": v(-40.07, -71.54) * mm, "end": v(-39.37, -71.93) * mm});
            skLineSegment(sketch, "E6449", {"start": v(-36.2, -69.08) * mm, "end": v(-37.83, -70.66) * mm});
            skLineSegment(sketch, "E6450", {"start": v(-37.83, -70.66) * mm, "end": v(-39.37, -71.93) * mm});
            skArc(sketch, "E6451", {"start": v(-35.4, -68.94) * mm, "mid": v(-35.82, -68.88) * mm, "end": v(-36.2, -69.08) * mm});
            skArc(sketch, "E6452", {"start": v(-35.4, -68.94) * mm, "mid": v(-35.18, -69.05) * mm, "end": v(-34.96, -69.17) * mm});
            skArc(sketch, "E6453", {"start": v(-34.6, -69.89) * mm, "mid": v(-34.66, -69.47) * mm, "end": v(-34.96, -69.17) * mm});
            skLineSegment(sketch, "E6454", {"start": v(-34.6, -69.89) * mm, "end": v(-34.93, -72.14) * mm});
            skLineSegment(sketch, "E6455", {"start": v(-34.93, -72.14) * mm, "end": v(-35.05, -74.13) * mm});
            skArc(sketch, "E6456", {"start": v(-35.05, -74.13) * mm, "mid": v(-34.33, -74.47) * mm, "end": v(-33.6, -74.8) * mm});
            skLineSegment(sketch, "E6457", {"start": v(-30.67, -71.7) * mm, "end": v(-32.17, -73.4) * mm});
            skLineSegment(sketch, "E6458", {"start": v(-32.17, -73.4) * mm, "end": v(-33.6, -74.8) * mm});
            skArc(sketch, "E6459", {"start": v(-29.89, -71.5) * mm, "mid": v(-30.31, -71.47) * mm, "end": v(-30.67, -71.7) * mm});
            skArc(sketch, "E6460", {"start": v(-29.89, -71.5) * mm, "mid": v(-29.66, -71.6) * mm, "end": v(-29.43, -71.7) * mm});
            skArc(sketch, "E6461", {"start": v(-29.02, -72.39) * mm, "mid": v(-29.1, -71.97) * mm, "end": v(-29.43, -71.7) * mm});
            skLineSegment(sketch, "E6462", {"start": v(-29.02, -72.39) * mm, "end": v(-29.16, -74.66) * mm});
            skLineSegment(sketch, "E6463", {"start": v(-29.16, -74.66) * mm, "end": v(-29.13, -76.65) * mm});
            skArc(sketch, "E6464", {"start": v(-29.13, -76.65) * mm, "mid": v(-28.38, -76.93) * mm, "end": v(-27.63, -77.2) * mm});
            skLineSegment(sketch, "E6465", {"start": v(-24.95, -73.9) * mm, "end": v(-26.31, -75.7) * mm});
            skLineSegment(sketch, "E6466", {"start": v(-26.31, -75.7) * mm, "end": v(-27.63, -77.2) * mm});
            skArc(sketch, "E6467", {"start": v(-24.18, -73.63) * mm, "mid": v(-24.6, -73.63) * mm, "end": v(-24.95, -73.9) * mm});
            skArc(sketch, "E6468", {"start": v(-24.18, -73.63) * mm, "mid": v(-23.95, -73.7) * mm, "end": v(-23.71, -73.78) * mm});
            skArc(sketch, "E6469", {"start": v(-23.25, -74.44) * mm, "mid": v(-23.37, -74.03) * mm, "end": v(-23.71, -73.78) * mm});
            skLineSegment(sketch, "E6470", {"start": v(-23.25, -74.44) * mm, "end": v(-23.21, -76.71) * mm});
            skLineSegment(sketch, "E6471", {"start": v(-23.21, -76.71) * mm, "end": v(-23.02, -78.7) * mm});
            skArc(sketch, "E6472", {"start": v(-23.02, -78.7) * mm, "mid": v(-22.26, -78.92) * mm, "end": v(-21.5, -79.13) * mm});
            skLineSegment(sketch, "E6473", {"start": v(-19.07, -75.62) * mm, "end": v(-20.29, -77.54) * mm});
            skLineSegment(sketch, "E6474", {"start": v(-20.29, -77.54) * mm, "end": v(-21.5, -79.13) * mm});
            skArc(sketch, "E6475", {"start": v(-18.33, -75.3) * mm, "mid": v(-18.76, -75.34) * mm, "end": v(-19.07, -75.62) * mm});
            skArc(sketch, "E6476", {"start": v(-18.33, -75.3) * mm, "mid": v(-18.1, -75.36) * mm, "end": v(-17.85, -75.42) * mm});
            skArc(sketch, "E6477", {"start": v(-17.34, -76.04) * mm, "mid": v(-17.5, -75.64) * mm, "end": v(-17.85, -75.42) * mm});
            skLineSegment(sketch, "E6478", {"start": v(-17.34, -76.04) * mm, "end": v(-17.12, -78.3) * mm});
            skLineSegment(sketch, "E6479", {"start": v(-17.12, -78.3) * mm, "end": v(-16.78, -80.27) * mm});
            skArc(sketch, "E6480", {"start": v(-16.78, -80.27) * mm, "mid": v(-16, -80.42) * mm, "end": v(-15.22, -80.58) * mm});
            skLineSegment(sketch, "E6481", {"start": v(-13.08, -76.88) * mm, "end": v(-14.14, -78.9) * mm});
            skLineSegment(sketch, "E6482", {"start": v(-14.14, -78.9) * mm, "end": v(-15.22, -80.58) * mm});
            skArc(sketch, "E6483", {"start": v(-12.37, -76.5) * mm, "mid": v(-12.79, -76.58) * mm, "end": v(-13.08, -76.88) * mm});
            skArc(sketch, "E6484", {"start": v(-12.37, -76.5) * mm, "mid": v(-12.12, -76.55) * mm, "end": v(-11.88, -76.58) * mm});
            skArc(sketch, "E6485", {"start": v(-11.32, -77.16) * mm, "mid": v(-11.5, -76.78) * mm, "end": v(-11.88, -76.58) * mm});
            skLineSegment(sketch, "E6486", {"start": v(-11.32, -77.16) * mm, "end": v(-10.93, -79.4) * mm});
            skLineSegment(sketch, "E6487", {"start": v(-10.93, -79.4) * mm, "end": v(-10.43, -81.33) * mm});
            skArc(sketch, "E6488", {"start": v(-10.43, -81.33) * mm, "mid": v(-9.64, -81.43) * mm, "end": v(-8.85, -81.52) * mm});
            skLineSegment(sketch, "E6489", {"start": v(-7, -77.67) * mm, "end": v(-7.9, -79.76) * mm});
            skLineSegment(sketch, "E6490", {"start": v(-7.9, -79.76) * mm, "end": v(-8.85, -81.52) * mm});
            skArc(sketch, "E6491", {"start": v(-6.33, -77.24) * mm, "mid": v(-6.74, -77.34) * mm, "end": v(-7, -77.67) * mm});
            skArc(sketch, "E6492", {"start": v(-6.33, -77.24) * mm, "mid": v(-6.08, -77.26) * mm, "end": v(-5.83, -77.28) * mm});
            skArc(sketch, "E6493", {"start": v(-5.23, -77.81) * mm, "mid": v(-5.44, -77.45) * mm, "end": v(-5.83, -77.28) * mm});
            skLineSegment(sketch, "E6494", {"start": v(-5.23, -77.81) * mm, "end": v(-4.66, -80.01) * mm});
            skLineSegment(sketch, "E6495", {"start": v(-4.66, -80.01) * mm, "end": v(-4.01, -81.9) * mm});
            skArc(sketch, "E6496", {"start": v(-4.01, -81.9) * mm, "mid": v(-3.22, -81.94) * mm, "end": v(-2.42, -81.96) * mm});
            skLineSegment(sketch, "E6497", {"start": v(-0.9, -77.98) * mm, "end": v(-1.63, -80.13) * mm});
            skLineSegment(sketch, "E6498", {"start": v(-1.63, -80.13) * mm, "end": v(-2.42, -81.96) * mm});
            skArc(sketch, "E6499", {"start": v(-0.25, -77.5) * mm, "mid": v(-0.65, -77.63) * mm, "end": v(-0.9, -77.98) * mm});
            skArc(sketch, "E6500", {"start": v(-0.25, -77.5) * mm, "mid": v(0, -77.5) * mm, "end": v(0.25, -77.5) * mm});
            skArc(sketch, "E6501", {"start": v(0.9, -77.98) * mm, "mid": v(0.65, -77.63) * mm, "end": v(0.25, -77.5) * mm});
            skLineSegment(sketch, "E6502", {"start": v(0.9, -77.98) * mm, "end": v(1.63, -80.13) * mm});
            skLineSegment(sketch, "E6503", {"start": v(1.63, -80.13) * mm, "end": v(2.42, -81.96) * mm});
            skArc(sketch, "E6504", {"start": v(2.42, -81.96) * mm, "mid": v(3.22, -81.94) * mm, "end": v(4.01, -81.9) * mm});
            skLineSegment(sketch, "E6505", {"start": v(5.23, -77.81) * mm, "end": v(4.66, -80.01) * mm});
            skLineSegment(sketch, "E6506", {"start": v(4.66, -80.01) * mm, "end": v(4.01, -81.9) * mm});
            skArc(sketch, "E6507", {"start": v(5.83, -77.28) * mm, "mid": v(5.44, -77.45) * mm, "end": v(5.23, -77.81) * mm});
            skArc(sketch, "E6508", {"start": v(5.83, -77.28) * mm, "mid": v(6.08, -77.26) * mm, "end": v(6.33, -77.24) * mm});
            skArc(sketch, "E6509", {"start": v(7, -77.67) * mm, "mid": v(6.74, -77.34) * mm, "end": v(6.33, -77.24) * mm});
            skLineSegment(sketch, "E6510", {"start": v(7, -77.67) * mm, "end": v(7.9, -79.76) * mm});
            skLineSegment(sketch, "E6511", {"start": v(7.9, -79.76) * mm, "end": v(8.85, -81.52) * mm});
            skArc(sketch, "E6512", {"start": v(8.85, -81.52) * mm, "mid": v(9.64, -81.43) * mm, "end": v(10.43, -81.33) * mm});
            skLineSegment(sketch, "E6513", {"start": v(11.32, -77.16) * mm, "end": v(10.93, -79.4) * mm});
            skLineSegment(sketch, "E6514", {"start": v(10.93, -79.4) * mm, "end": v(10.43, -81.33) * mm});
            skArc(sketch, "E6515", {"start": v(11.88, -76.58) * mm, "mid": v(11.5, -76.78) * mm, "end": v(11.32, -77.16) * mm});
            skArc(sketch, "E6516", {"start": v(11.88, -76.58) * mm, "mid": v(12.12, -76.55) * mm, "end": v(12.37, -76.5) * mm});
            skArc(sketch, "E6517", {"start": v(13.08, -76.88) * mm, "mid": v(12.79, -76.58) * mm, "end": v(12.37, -76.5) * mm});
            skLineSegment(sketch, "E6518", {"start": v(13.08, -76.88) * mm, "end": v(14.14, -78.9) * mm});
            skLineSegment(sketch, "E6519", {"start": v(14.14, -78.9) * mm, "end": v(15.22, -80.58) * mm});
            skArc(sketch, "E6520", {"start": v(15.22, -80.58) * mm, "mid": v(16, -80.42) * mm, "end": v(16.78, -80.27) * mm});
            skLineSegment(sketch, "E6521", {"start": v(17.34, -76.04) * mm, "end": v(17.12, -78.3) * mm});
            skLineSegment(sketch, "E6522", {"start": v(17.12, -78.3) * mm, "end": v(16.78, -80.27) * mm});
            skArc(sketch, "E6523", {"start": v(17.85, -75.42) * mm, "mid": v(17.5, -75.64) * mm, "end": v(17.34, -76.04) * mm});
            skArc(sketch, "E6524", {"start": v(17.85, -75.42) * mm, "mid": v(18.1, -75.36) * mm, "end": v(18.33, -75.3) * mm});
            skCircle(sketch, "E6525", {"center": v(0, 0) * mm, "radius": 3.1 * mm});
            skArc(sketch, "E6526", {"start": v(19.07, -75.62) * mm, "mid": v(18.76, -75.34) * mm, "end": v(18.33, -75.3) * mm});
            skArc(sketch, "E6527", {"start": v(55.08, -60.75) * mm, "mid": v(55.66, -60.21) * mm, "end": v(56.24, -59.67) * mm});
            skLineSegment(sketch, "E6528", {"start": v(54.51, -55.77) * mm, "end": v(55.51, -57.81) * mm});
            skLineSegment(sketch, "E6529", {"start": v(55.51, -57.81) * mm, "end": v(56.24, -59.67) * mm});
            skArc(sketch, "E6530", {"start": v(54.63, -54.98) * mm, "mid": v(54.43, -55.36) * mm, "end": v(54.51, -55.77) * mm});
            skArc(sketch, "E6531", {"start": v(54.63, -54.98) * mm, "mid": v(54.8, -54.8) * mm, "end": v(54.98, -54.63) * mm});
            skArc(sketch, "E6532", {"start": v(55.77, -54.51) * mm, "mid": v(55.36, -54.43) * mm, "end": v(54.98, -54.63) * mm});
            skLineSegment(sketch, "E6533", {"start": v(55.77, -54.51) * mm, "end": v(57.81, -55.51) * mm});
            skLineSegment(sketch, "E6534", {"start": v(57.81, -55.51) * mm, "end": v(59.67, -56.24) * mm});
            skArc(sketch, "E6535", {"start": v(59.67, -56.24) * mm, "mid": v(60.21, -55.66) * mm, "end": v(60.75, -55.08) * mm});
            skLineSegment(sketch, "E6536", {"start": v(58.72, -51.32) * mm, "end": v(59.88, -53.28) * mm});
            skLineSegment(sketch, "E6537", {"start": v(59.88, -53.28) * mm, "end": v(60.75, -55.08) * mm});
            skArc(sketch, "E6538", {"start": v(58.77, -50.52) * mm, "mid": v(58.61, -50.91) * mm, "end": v(58.72, -51.32) * mm});
            skArc(sketch, "E6539", {"start": v(58.77, -50.52) * mm, "mid": v(58.93, -50.33) * mm, "end": v(59.1, -50.14) * mm});
            skArc(sketch, "E6540", {"start": v(59.88, -49.97) * mm, "mid": v(59.46, -49.92) * mm, "end": v(59.1, -50.14) * mm});
            skLineSegment(sketch, "E6541", {"start": v(59.88, -49.97) * mm, "end": v(62, -50.8) * mm});
            skLineSegment(sketch, "E6542", {"start": v(62, -50.8) * mm, "end": v(63.9, -51.39) * mm});
            skArc(sketch, "E6543", {"start": v(63.9, -51.39) * mm, "mid": v(64.4, -50.77) * mm, "end": v(64.89, -50.14) * mm});
            skLineSegment(sketch, "E6544", {"start": v(62.57, -46.56) * mm, "end": v(63.87, -48.42) * mm});
            skLineSegment(sketch, "E6545", {"start": v(63.87, -48.42) * mm, "end": v(64.89, -50.14) * mm});
            skArc(sketch, "E6546", {"start": v(62.55, -45.75) * mm, "mid": v(62.42, -46.16) * mm, "end": v(62.57, -46.56) * mm});
            skArc(sketch, "E6547", {"start": v(62.55, -45.75) * mm, "mid": v(62.7, -45.55) * mm, "end": v(62.84, -45.35) * mm});
            skArc(sketch, "E6548", {"start": v(63.61, -45.12) * mm, "mid": v(63.19, -45.1) * mm, "end": v(62.84, -45.35) * mm});
            skLineSegment(sketch, "E6549", {"start": v(63.61, -45.12) * mm, "end": v(65.79, -45.78) * mm});
            skLineSegment(sketch, "E6550", {"start": v(65.79, -45.78) * mm, "end": v(67.74, -46.22) * mm});
            skArc(sketch, "E6551", {"start": v(68.94, -35.4) * mm, "mid": v(69.05, -35.18) * mm, "end": v(69.17, -34.96) * mm});
            skArc(sketch, "E6552", {"start": v(69.89, -34.6) * mm, "mid": v(69.47, -34.66) * mm, "end": v(69.17, -34.96) * mm});
            skLineSegment(sketch, "E6553", {"start": v(69.89, -34.6) * mm, "end": v(72.14, -34.93) * mm});
            skLineSegment(sketch, "E6554", {"start": v(72.14, -34.93) * mm, "end": v(74.13, -35.05) * mm});
            skArc(sketch, "E6555", {"start": v(74.13, -35.05) * mm, "mid": v(74.47, -34.33) * mm, "end": v(74.8, -33.6) * mm});
            skLineSegment(sketch, "E6556", {"start": v(71.7, -30.67) * mm, "end": v(73.4, -32.17) * mm});
            skArc(sketch, "E6557", {"start": v(72.39, -29.02) * mm, "mid": v(71.97, -29.1) * mm, "end": v(71.7, -29.43) * mm});
            skArc(sketch, "E6558", {"start": v(71.5, -29.89) * mm, "mid": v(71.6, -29.66) * mm, "end": v(71.7, -29.43) * mm});
            skArc(sketch, "E6559", {"start": v(71.5, -29.89) * mm, "mid": v(71.47, -30.31) * mm, "end": v(71.7, -30.67) * mm});
            skLineSegment(sketch, "E6560", {"start": v(73.4, -32.17) * mm, "end": v(74.8, -33.6) * mm});
            skArc(sketch, "E6561", {"start": v(68.94, -35.4) * mm, "mid": v(68.88, -35.82) * mm, "end": v(69.08, -36.2) * mm});
            skLineSegment(sketch, "E6562", {"start": v(70.66, -37.83) * mm, "end": v(71.93, -39.37) * mm});
            skLineSegment(sketch, "E6563", {"start": v(69.08, -36.2) * mm, "end": v(70.66, -37.83) * mm});
            skArc(sketch, "E6564", {"start": v(71.15, -40.76) * mm, "mid": v(71.54, -40.07) * mm, "end": v(71.93, -39.37) * mm});
            skLineSegment(sketch, "E6565", {"start": v(69.17, -40.48) * mm, "end": v(71.15, -40.76) * mm});
            skLineSegment(sketch, "E6566", {"start": v(66.96, -39.99) * mm, "end": v(69.17, -40.48) * mm});
            skArc(sketch, "E6567", {"start": v(66.96, -39.99) * mm, "mid": v(66.53, -40) * mm, "end": v(66.2, -40.28) * mm});
            skArc(sketch, "E6568", {"start": v(65.95, -40.7) * mm, "mid": v(66.08, -40.5) * mm, "end": v(66.2, -40.28) * mm});
            skArc(sketch, "E6569", {"start": v(65.95, -40.7) * mm, "mid": v(65.85, -41.12) * mm, "end": v(66.03, -41.5) * mm});
            skLineSegment(sketch, "E6570", {"start": v(67.47, -43.26) * mm, "end": v(68.62, -44.9) * mm});
            skLineSegment(sketch, "E6571", {"start": v(66.03, -41.5) * mm, "end": v(67.47, -43.26) * mm});
            skArc(sketch, "E6572", {"start": v(67.74, -46.22) * mm, "mid": v(68.18, -45.56) * mm, "end": v(68.62, -44.9) * mm});
            skLineSegment(sketch, "E6573", {"start": v(53.28, -59.88) * mm, "end": v(55.08, -60.75) * mm});
            skLineSegment(sketch, "E6574", {"start": v(51.32, -58.72) * mm, "end": v(53.28, -59.88) * mm});
            skArc(sketch, "E6575", {"start": v(51.32, -58.72) * mm, "mid": v(50.91, -58.61) * mm, "end": v(50.52, -58.77) * mm});
            skArc(sketch, "E6576", {"start": v(50.14, -59.1) * mm, "mid": v(50.33, -58.93) * mm, "end": v(50.52, -58.77) * mm});
            skArc(sketch, "E6577", {"start": v(50.14, -59.1) * mm, "mid": v(49.92, -59.46) * mm, "end": v(49.97, -59.88) * mm});
            skLineSegment(sketch, "E6578", {"start": v(50.8, -62) * mm, "end": v(51.39, -63.9) * mm});
            skLineSegment(sketch, "E6579", {"start": v(49.97, -59.88) * mm, "end": v(50.8, -62) * mm});
            skArc(sketch, "E6580", {"start": v(50.14, -64.89) * mm, "mid": v(50.77, -64.4) * mm, "end": v(51.39, -63.9) * mm});
            skLineSegment(sketch, "E6581", {"start": v(48.42, -63.87) * mm, "end": v(50.14, -64.89) * mm});
            skLineSegment(sketch, "E6582", {"start": v(46.56, -62.57) * mm, "end": v(48.42, -63.87) * mm});
            skArc(sketch, "E6583", {"start": v(46.56, -62.57) * mm, "mid": v(46.16, -62.42) * mm, "end": v(45.75, -62.55) * mm});
            skArc(sketch, "E6584", {"start": v(45.35, -62.84) * mm, "mid": v(45.55, -62.7) * mm, "end": v(45.75, -62.55) * mm});
            skArc(sketch, "E6585", {"start": v(45.35, -62.84) * mm, "mid": v(45.1, -63.19) * mm, "end": v(45.12, -63.61) * mm});
            skLineSegment(sketch, "E6586", {"start": v(45.78, -65.79) * mm, "end": v(46.22, -67.74) * mm});
            skLineSegment(sketch, "E6587", {"start": v(45.12, -63.61) * mm, "end": v(45.78, -65.79) * mm});
            skArc(sketch, "E6588", {"start": v(44.9, -68.62) * mm, "mid": v(45.56, -68.18) * mm, "end": v(46.22, -67.74) * mm});
            skLineSegment(sketch, "E6589", {"start": v(43.26, -67.47) * mm, "end": v(44.9, -68.62) * mm});
            skLineSegment(sketch, "E6590", {"start": v(41.5, -66.03) * mm, "end": v(43.26, -67.47) * mm});
            skArc(sketch, "E6591", {"start": v(41.5, -66.03) * mm, "mid": v(41.12, -65.85) * mm, "end": v(40.7, -65.95) * mm});
            skArc(sketch, "E6592", {"start": v(40.28, -66.2) * mm, "mid": v(40.5, -66.08) * mm, "end": v(40.7, -65.95) * mm});
            skArc(sketch, "E6593", {"start": v(40.28, -66.2) * mm, "mid": v(40, -66.53) * mm, "end": v(39.99, -66.96) * mm});
            skLineSegment(sketch, "E6594", {"start": v(40.48, -69.17) * mm, "end": v(40.76, -71.15) * mm});
            skLineSegment(sketch, "E6595", {"start": v(39.99, -66.96) * mm, "end": v(40.48, -69.17) * mm});
            skArc(sketch, "E6596", {"start": v(39.37, -71.93) * mm, "mid": v(40.07, -71.54) * mm, "end": v(40.76, -71.15) * mm});
            skLineSegment(sketch, "E6597", {"start": v(37.83, -70.66) * mm, "end": v(39.37, -71.93) * mm});
            skLineSegment(sketch, "E6598", {"start": v(36.2, -69.08) * mm, "end": v(37.83, -70.66) * mm});
            skArc(sketch, "E6599", {"start": v(36.2, -69.08) * mm, "mid": v(35.82, -68.88) * mm, "end": v(35.4, -68.94) * mm});
            skArc(sketch, "E6600", {"start": v(34.96, -69.17) * mm, "mid": v(35.18, -69.05) * mm, "end": v(35.4, -68.94) * mm});
            skArc(sketch, "E6601", {"start": v(34.96, -69.17) * mm, "mid": v(34.66, -69.47) * mm, "end": v(34.6, -69.89) * mm});
            skLineSegment(sketch, "E6602", {"start": v(34.93, -72.14) * mm, "end": v(35.05, -74.13) * mm});
            skLineSegment(sketch, "E6603", {"start": v(34.6, -69.89) * mm, "end": v(34.93, -72.14) * mm});
            skArc(sketch, "E6604", {"start": v(33.6, -74.8) * mm, "mid": v(34.33, -74.47) * mm, "end": v(35.05, -74.13) * mm});
            skLineSegment(sketch, "E6605", {"start": v(32.17, -73.4) * mm, "end": v(33.6, -74.8) * mm});
            skLineSegment(sketch, "E6606", {"start": v(30.67, -71.7) * mm, "end": v(32.17, -73.4) * mm});
            skArc(sketch, "E6607", {"start": v(30.67, -71.7) * mm, "mid": v(30.31, -71.47) * mm, "end": v(29.89, -71.5) * mm});
            skArc(sketch, "E6608", {"start": v(29.43, -71.7) * mm, "mid": v(29.66, -71.6) * mm, "end": v(29.89, -71.5) * mm});
            skArc(sketch, "E6609", {"start": v(29.43, -71.7) * mm, "mid": v(29.1, -71.97) * mm, "end": v(29.02, -72.39) * mm});
            skLineSegment(sketch, "E6610", {"start": v(29.16, -74.66) * mm, "end": v(29.13, -76.65) * mm});
            skLineSegment(sketch, "E6611", {"start": v(29.02, -72.39) * mm, "end": v(29.16, -74.66) * mm});
            skArc(sketch, "E6612", {"start": v(27.63, -77.2) * mm, "mid": v(28.38, -76.93) * mm, "end": v(29.13, -76.65) * mm});
            skLineSegment(sketch, "E6613", {"start": v(26.31, -75.7) * mm, "end": v(27.63, -77.2) * mm});
            skLineSegment(sketch, "E6614", {"start": v(24.95, -73.9) * mm, "end": v(26.31, -75.7) * mm});
            skArc(sketch, "E6615", {"start": v(24.95, -73.9) * mm, "mid": v(24.6, -73.63) * mm, "end": v(24.18, -73.63) * mm});
            skArc(sketch, "E6616", {"start": v(23.71, -73.78) * mm, "mid": v(23.95, -73.7) * mm, "end": v(24.18, -73.63) * mm});
            skArc(sketch, "E6617", {"start": v(23.71, -73.78) * mm, "mid": v(23.37, -74.03) * mm, "end": v(23.25, -74.44) * mm});
            skLineSegment(sketch, "E6618", {"start": v(23.21, -76.71) * mm, "end": v(23.02, -78.7) * mm});
            skLineSegment(sketch, "E6619", {"start": v(23.25, -74.44) * mm, "end": v(23.21, -76.71) * mm});
            skArc(sketch, "E6620", {"start": v(21.5, -79.13) * mm, "mid": v(22.26, -78.92) * mm, "end": v(23.02, -78.7) * mm});
            skLineSegment(sketch, "E6621", {"start": v(20.29, -77.54) * mm, "end": v(21.5, -79.13) * mm});
            skLineSegment(sketch, "E6622", {"start": v(19.07, -75.62) * mm, "end": v(20.29, -77.54) * mm});
            skLineSegment(sketch, "E6623", {"start": v(-55.51, -57.81) * mm, "end": v(-56.24, -59.67) * mm});
            skLineSegment(sketch, "E6624", {"start": v(-54.51, -55.77) * mm, "end": v(-55.51, -57.81) * mm});
            skArc(sketch, "E6625", {"start": v(-54.51, -55.77) * mm, "mid": v(-54.43, -55.36) * mm, "end": v(-54.63, -54.98) * mm});
            skArc(sketch, "E6626", {"start": v(-54.98, -54.63) * mm, "mid": v(-54.8, -54.8) * mm, "end": v(-54.63, -54.98) * mm});
            skArc(sketch, "E6627", {"start": v(-54.98, -54.63) * mm, "mid": v(-55.36, -54.43) * mm, "end": v(-55.77, -54.51) * mm});
            skLineSegment(sketch, "E6628", {"start": v(-57.81, -55.51) * mm, "end": v(-59.67, -56.24) * mm});
            skLineSegment(sketch, "E6629", {"start": v(-55.77, -54.51) * mm, "end": v(-57.81, -55.51) * mm});
            skArc(sketch, "E6630", {"start": v(-60.75, -55.08) * mm, "mid": v(-60.21, -55.66) * mm, "end": v(-59.67, -56.24) * mm});
            skLineSegment(sketch, "E6631", {"start": v(-59.88, -53.28) * mm, "end": v(-60.75, -55.08) * mm});
            skLineSegment(sketch, "E6632", {"start": v(-58.72, -51.32) * mm, "end": v(-59.88, -53.28) * mm});
            skArc(sketch, "E6633", {"start": v(-58.72, -51.32) * mm, "mid": v(-58.61, -50.91) * mm, "end": v(-58.77, -50.52) * mm});
            skArc(sketch, "E6634", {"start": v(-59.1, -50.14) * mm, "mid": v(-58.93, -50.33) * mm, "end": v(-58.77, -50.52) * mm});
            skArc(sketch, "E6635", {"start": v(-59.1, -50.14) * mm, "mid": v(-59.46, -49.92) * mm, "end": v(-59.88, -49.97) * mm});
            skLineSegment(sketch, "E6636", {"start": v(-62, -50.8) * mm, "end": v(-63.9, -51.39) * mm});
            skLineSegment(sketch, "E6637", {"start": v(-59.88, -49.97) * mm, "end": v(-62, -50.8) * mm});
            skArc(sketch, "E6638", {"start": v(-64.89, -50.14) * mm, "mid": v(-64.4, -50.77) * mm, "end": v(-63.9, -51.39) * mm});
            skLineSegment(sketch, "E6639", {"start": v(-63.87, -48.42) * mm, "end": v(-64.89, -50.14) * mm});
            skLineSegment(sketch, "E6640", {"start": v(-62.57, -46.56) * mm, "end": v(-63.87, -48.42) * mm});
            skArc(sketch, "E6641", {"start": v(-62.57, -46.56) * mm, "mid": v(-62.42, -46.16) * mm, "end": v(-62.55, -45.75) * mm});
            skArc(sketch, "E6642", {"start": v(-62.84, -45.35) * mm, "mid": v(-62.7, -45.55) * mm, "end": v(-62.55, -45.75) * mm});
            skArc(sketch, "E6643", {"start": v(-62.84, -45.35) * mm, "mid": v(-63.19, -45.1) * mm, "end": v(-63.61, -45.12) * mm});
            skLineSegment(sketch, "E6644", {"start": v(-65.79, -45.78) * mm, "end": v(-67.74, -46.22) * mm});
            skLineSegment(sketch, "E6645", {"start": v(-63.61, -45.12) * mm, "end": v(-65.79, -45.78) * mm});
            skArc(sketch, "E6646", {"start": v(-68.62, -44.9) * mm, "mid": v(-68.18, -45.56) * mm, "end": v(-67.74, -46.22) * mm});
            skLineSegment(sketch, "E6647", {"start": v(-67.47, -43.26) * mm, "end": v(-68.62, -44.9) * mm});
            skLineSegment(sketch, "E6648", {"start": v(-66.03, -41.5) * mm, "end": v(-67.47, -43.26) * mm});
            skArc(sketch, "E6649", {"start": v(-66.03, -41.5) * mm, "mid": v(-65.85, -41.12) * mm, "end": v(-65.95, -40.7) * mm});
            skArc(sketch, "E6650", {"start": v(-66.2, -40.28) * mm, "mid": v(-66.08, -40.5) * mm, "end": v(-65.95, -40.7) * mm});
            skArc(sketch, "E6651", {"start": v(-66.2, -40.28) * mm, "mid": v(-66.53, -40) * mm, "end": v(-66.96, -39.99) * mm});
            skLineSegment(sketch, "E6652", {"start": v(-69.17, -40.48) * mm, "end": v(-71.15, -40.76) * mm});
            skLineSegment(sketch, "E6653", {"start": v(-66.96, -39.99) * mm, "end": v(-69.17, -40.48) * mm});
            skArc(sketch, "E6654", {"start": v(-71.93, -39.37) * mm, "mid": v(-71.54, -40.07) * mm, "end": v(-71.15, -40.76) * mm});
            skLineSegment(sketch, "E6655", {"start": v(-70.66, -37.83) * mm, "end": v(-71.93, -39.37) * mm});
            skLineSegment(sketch, "E6656", {"start": v(-69.08, -36.2) * mm, "end": v(-70.66, -37.83) * mm});
            skArc(sketch, "E6657", {"start": v(-69.08, -36.2) * mm, "mid": v(-68.88, -35.82) * mm, "end": v(-68.94, -35.4) * mm});
            skArc(sketch, "E6658", {"start": v(-69.17, -34.96) * mm, "mid": v(-69.05, -35.18) * mm, "end": v(-68.94, -35.4) * mm});
            skArc(sketch, "E6659", {"start": v(-69.17, -34.96) * mm, "mid": v(-69.47, -34.66) * mm, "end": v(-69.89, -34.6) * mm});
            skLineSegment(sketch, "E6660", {"start": v(-72.14, -34.93) * mm, "end": v(-74.13, -35.05) * mm});
            skLineSegment(sketch, "E6661", {"start": v(-69.89, -34.6) * mm, "end": v(-72.14, -34.93) * mm});
            skArc(sketch, "E6662", {"start": v(-74.8, -33.6) * mm, "mid": v(-74.47, -34.33) * mm, "end": v(-74.13, -35.05) * mm});
            skLineSegment(sketch, "E6663", {"start": v(-73.4, -32.17) * mm, "end": v(-74.8, -33.6) * mm});
            skLineSegment(sketch, "E6664", {"start": v(-71.7, -30.67) * mm, "end": v(-73.4, -32.17) * mm});
            skArc(sketch, "E6665", {"start": v(-71.7, -30.67) * mm, "mid": v(-71.47, -30.31) * mm, "end": v(-71.5, -29.89) * mm});
            skArc(sketch, "E6666", {"start": v(-71.7, -29.43) * mm, "mid": v(-71.6, -29.66) * mm, "end": v(-71.5, -29.89) * mm});
            skArc(sketch, "E6667", {"start": v(-71.7, -29.43) * mm, "mid": v(-71.97, -29.1) * mm, "end": v(-72.39, -29.02) * mm});
            skLineSegment(sketch, "E6668", {"start": v(-74.66, -29.16) * mm, "end": v(-76.65, -29.13) * mm});
            skLineSegment(sketch, "E6669", {"start": v(-72.39, -29.02) * mm, "end": v(-74.66, -29.16) * mm});
            skArc(sketch, "E6670", {"start": v(-77.2, -27.63) * mm, "mid": v(-76.93, -28.38) * mm, "end": v(-76.65, -29.13) * mm});
            skLineSegment(sketch, "E6671", {"start": v(-75.7, -26.31) * mm, "end": v(-77.2, -27.63) * mm});
            skLineSegment(sketch, "E6672", {"start": v(-73.9, -24.95) * mm, "end": v(-75.7, -26.31) * mm});
            skArc(sketch, "E6673", {"start": v(-73.9, -24.95) * mm, "mid": v(-73.63, -24.6) * mm, "end": v(-73.63, -24.18) * mm});
            skArc(sketch, "E6674", {"start": v(-73.78, -23.71) * mm, "mid": v(-73.7, -23.95) * mm, "end": v(-73.63, -24.18) * mm});
            skArc(sketch, "E6675", {"start": v(-73.78, -23.71) * mm, "mid": v(-74.03, -23.37) * mm, "end": v(-74.44, -23.25) * mm});
            skLineSegment(sketch, "E6676", {"start": v(-76.71, -23.21) * mm, "end": v(-78.7, -23.02) * mm});
            skLineSegment(sketch, "E6677", {"start": v(-74.44, -23.25) * mm, "end": v(-76.71, -23.21) * mm});
            skArc(sketch, "E6678", {"start": v(-79.13, -21.5) * mm, "mid": v(-78.92, -22.26) * mm, "end": v(-78.7, -23.02) * mm});
            skLineSegment(sketch, "E6679", {"start": v(-77.54, -20.29) * mm, "end": v(-79.13, -21.5) * mm});
            skLineSegment(sketch, "E6680", {"start": v(-75.62, -19.07) * mm, "end": v(-77.54, -20.29) * mm});
            skArc(sketch, "E6681", {"start": v(-75.62, -19.07) * mm, "mid": v(-75.34, -18.76) * mm, "end": v(-75.3, -18.33) * mm});
            skArc(sketch, "E6682", {"start": v(-75.42, -17.85) * mm, "mid": v(-75.36, -18.1) * mm, "end": v(-75.3, -18.33) * mm});
            skArc(sketch, "E6683", {"start": v(-75.42, -17.85) * mm, "mid": v(-75.64, -17.5) * mm, "end": v(-76.04, -17.34) * mm});
            skLineSegment(sketch, "E6684", {"start": v(-78.3, -17.12) * mm, "end": v(-80.27, -16.78) * mm});
            skLineSegment(sketch, "E6685", {"start": v(-76.04, -17.34) * mm, "end": v(-78.3, -17.12) * mm});
            skArc(sketch, "E6686", {"start": v(-80.58, -15.22) * mm, "mid": v(-80.42, -16) * mm, "end": v(-80.27, -16.78) * mm});
            skLineSegment(sketch, "E6687", {"start": v(-78.9, -14.14) * mm, "end": v(-80.58, -15.22) * mm});
            skLineSegment(sketch, "E6688", {"start": v(-76.88, -13.08) * mm, "end": v(-78.9, -14.14) * mm});
            skArc(sketch, "E6689", {"start": v(-76.88, -13.08) * mm, "mid": v(-76.58, -12.79) * mm, "end": v(-76.5, -12.37) * mm});
            skArc(sketch, "E6690", {"start": v(-76.58, -11.88) * mm, "mid": v(-76.55, -12.12) * mm, "end": v(-76.5, -12.37) * mm});
            skArc(sketch, "E6691", {"start": v(-76.58, -11.88) * mm, "mid": v(-76.78, -11.5) * mm, "end": v(-77.16, -11.32) * mm});
            skLineSegment(sketch, "E6692", {"start": v(-79.4, -10.93) * mm, "end": v(-81.33, -10.43) * mm});
            skLineSegment(sketch, "E6693", {"start": v(-77.16, -11.32) * mm, "end": v(-79.4, -10.93) * mm});
            skArc(sketch, "E6694", {"start": v(-81.52, -8.85) * mm, "mid": v(-81.43, -9.64) * mm, "end": v(-81.33, -10.43) * mm});
            skLineSegment(sketch, "E6695", {"start": v(-79.76, -7.9) * mm, "end": v(-81.52, -8.85) * mm});
            skLineSegment(sketch, "E6696", {"start": v(-77.67, -7) * mm, "end": v(-79.76, -7.9) * mm});
            skArc(sketch, "E6697", {"start": v(-77.67, -7) * mm, "mid": v(-77.34, -6.74) * mm, "end": v(-77.24, -6.33) * mm});
            skArc(sketch, "E6698", {"start": v(-77.28, -5.83) * mm, "mid": v(-77.26, -6.08) * mm, "end": v(-77.24, -6.33) * mm});
            skArc(sketch, "E6699", {"start": v(-77.28, -5.83) * mm, "mid": v(-77.45, -5.44) * mm, "end": v(-77.81, -5.23) * mm});
            skLineSegment(sketch, "E6700", {"start": v(-80.01, -4.66) * mm, "end": v(-81.9, -4.01) * mm});
            skLineSegment(sketch, "E6701", {"start": v(-77.81, -5.23) * mm, "end": v(-80.01, -4.66) * mm});
            skArc(sketch, "E6702", {"start": v(-81.96, -2.42) * mm, "mid": v(-81.94, -3.22) * mm, "end": v(-81.9, -4.01) * mm});
            skLineSegment(sketch, "E6703", {"start": v(-80.13, -1.63) * mm, "end": v(-81.96, -2.42) * mm});
            skLineSegment(sketch, "E6704", {"start": v(-77.98, -0.9) * mm, "end": v(-80.13, -1.63) * mm});
            skArc(sketch, "E6705", {"start": v(-77.98, -0.9) * mm, "mid": v(-77.63, -0.65) * mm, "end": v(-77.5, -0.25) * mm});
            skArc(sketch, "E6706", {"start": v(-77.5, 0.25) * mm, "mid": v(-77.5, 0) * mm, "end": v(-77.5, -0.25) * mm});
            skArc(sketch, "E6707", {"start": v(-77.5, 0.25) * mm, "mid": v(-77.63, 0.65) * mm, "end": v(-77.98, 0.9) * mm});
            skLineSegment(sketch, "E6708", {"start": v(-80.13, 1.63) * mm, "end": v(-81.96, 2.42) * mm});
            skLineSegment(sketch, "E6709", {"start": v(-77.98, 0.9) * mm, "end": v(-80.13, 1.63) * mm});
            skArc(sketch, "E6710", {"start": v(-81.9, 4.01) * mm, "mid": v(-81.94, 3.22) * mm, "end": v(-81.96, 2.42) * mm});
            skLineSegment(sketch, "E6711", {"start": v(-80.01, 4.66) * mm, "end": v(-81.9, 4.01) * mm});
            skLineSegment(sketch, "E6712", {"start": v(-77.81, 5.23) * mm, "end": v(-80.01, 4.66) * mm});
            skArc(sketch, "E6713", {"start": v(-77.81, 5.23) * mm, "mid": v(-77.45, 5.44) * mm, "end": v(-77.28, 5.83) * mm});
            skArc(sketch, "E6714", {"start": v(-77.24, 6.33) * mm, "mid": v(-77.26, 6.08) * mm, "end": v(-77.28, 5.83) * mm});
            skArc(sketch, "E6715", {"start": v(-77.24, 6.33) * mm, "mid": v(-77.34, 6.74) * mm, "end": v(-77.67, 7) * mm});
            skLineSegment(sketch, "E6716", {"start": v(-79.76, 7.9) * mm, "end": v(-81.52, 8.85) * mm});
            skLineSegment(sketch, "E6717", {"start": v(-77.67, 7) * mm, "end": v(-79.76, 7.9) * mm});
            skArc(sketch, "E6718", {"start": v(-81.33, 10.43) * mm, "mid": v(-81.43, 9.64) * mm, "end": v(-81.52, 8.85) * mm});
            skLineSegment(sketch, "E6719", {"start": v(-79.4, 10.93) * mm, "end": v(-81.33, 10.43) * mm});
            skLineSegment(sketch, "E6720", {"start": v(-77.16, 11.32) * mm, "end": v(-79.4, 10.93) * mm});
            skArc(sketch, "E6721", {"start": v(-77.16, 11.32) * mm, "mid": v(-76.78, 11.5) * mm, "end": v(-76.58, 11.88) * mm});
            skArc(sketch, "E6722", {"start": v(-76.5, 12.37) * mm, "mid": v(-76.55, 12.12) * mm, "end": v(-76.58, 11.88) * mm});
            skArc(sketch, "E6723", {"start": v(-76.5, 12.37) * mm, "mid": v(-76.58, 12.79) * mm, "end": v(-76.88, 13.08) * mm});
            skLineSegment(sketch, "E6724", {"start": v(-78.9, 14.14) * mm, "end": v(-80.58, 15.22) * mm});
            skLineSegment(sketch, "E6725", {"start": v(-76.88, 13.08) * mm, "end": v(-78.9, 14.14) * mm});
            skArc(sketch, "E6726", {"start": v(-80.27, 16.78) * mm, "mid": v(-80.42, 16) * mm, "end": v(-80.58, 15.22) * mm});
            skLineSegment(sketch, "E6727", {"start": v(-78.3, 17.12) * mm, "end": v(-80.27, 16.78) * mm});
            skLineSegment(sketch, "E6728", {"start": v(-76.04, 17.34) * mm, "end": v(-78.3, 17.12) * mm});
            skArc(sketch, "E6729", {"start": v(-76.04, 17.34) * mm, "mid": v(-75.64, 17.5) * mm, "end": v(-75.42, 17.85) * mm});
            skArc(sketch, "E6730", {"start": v(-75.3, 18.33) * mm, "mid": v(-75.36, 18.1) * mm, "end": v(-75.42, 17.85) * mm});
            skArc(sketch, "E6731", {"start": v(-75.3, 18.33) * mm, "mid": v(-75.34, 18.76) * mm, "end": v(-75.62, 19.07) * mm});
            skLineSegment(sketch, "E6732", {"start": v(-77.54, 20.29) * mm, "end": v(-79.13, 21.5) * mm});
            skLineSegment(sketch, "E6733", {"start": v(-75.62, 19.07) * mm, "end": v(-77.54, 20.29) * mm});
            skArc(sketch, "E6734", {"start": v(-78.7, 23.02) * mm, "mid": v(-78.92, 22.26) * mm, "end": v(-79.13, 21.5) * mm});
            skLineSegment(sketch, "E6735", {"start": v(-76.71, 23.21) * mm, "end": v(-78.7, 23.02) * mm});
            skLineSegment(sketch, "E6736", {"start": v(-74.44, 23.25) * mm, "end": v(-76.71, 23.21) * mm});
            skArc(sketch, "E6737", {"start": v(-74.44, 23.25) * mm, "mid": v(-74.03, 23.37) * mm, "end": v(-73.78, 23.71) * mm});
            skArc(sketch, "E6738", {"start": v(-73.63, 24.18) * mm, "mid": v(-73.7, 23.95) * mm, "end": v(-73.78, 23.71) * mm});
            skArc(sketch, "E6739", {"start": v(-73.63, 24.18) * mm, "mid": v(-73.63, 24.6) * mm, "end": v(-73.9, 24.95) * mm});
            skLineSegment(sketch, "E6740", {"start": v(-75.7, 26.31) * mm, "end": v(-77.2, 27.63) * mm});
            skLineSegment(sketch, "E6741", {"start": v(-73.9, 24.95) * mm, "end": v(-75.7, 26.31) * mm});
            skArc(sketch, "E6742", {"start": v(-76.65, 29.13) * mm, "mid": v(-76.93, 28.38) * mm, "end": v(-77.2, 27.63) * mm});
            skLineSegment(sketch, "E6743", {"start": v(-74.66, 29.16) * mm, "end": v(-76.65, 29.13) * mm});
            skLineSegment(sketch, "E6744", {"start": v(-72.39, 29.02) * mm, "end": v(-74.66, 29.16) * mm});
            skArc(sketch, "E6745", {"start": v(-72.39, 29.02) * mm, "mid": v(-71.97, 29.1) * mm, "end": v(-71.7, 29.43) * mm});
            skArc(sketch, "E6746", {"start": v(-71.5, 29.89) * mm, "mid": v(-71.6, 29.66) * mm, "end": v(-71.7, 29.43) * mm});
            skArc(sketch, "E6747", {"start": v(-71.5, 29.89) * mm, "mid": v(-71.47, 30.31) * mm, "end": v(-71.7, 30.67) * mm});
            skLineSegment(sketch, "E6748", {"start": v(-73.4, 32.17) * mm, "end": v(-74.8, 33.6) * mm});
            skLineSegment(sketch, "E6749", {"start": v(-71.7, 30.67) * mm, "end": v(-73.4, 32.17) * mm});
            skArc(sketch, "E6750", {"start": v(-74.13, 35.05) * mm, "mid": v(-74.47, 34.33) * mm, "end": v(-74.8, 33.6) * mm});
            skLineSegment(sketch, "E6751", {"start": v(-72.14, 34.93) * mm, "end": v(-74.13, 35.05) * mm});
            skLineSegment(sketch, "E6752", {"start": v(-69.89, 34.6) * mm, "end": v(-72.14, 34.93) * mm});
            skArc(sketch, "E6753", {"start": v(-69.89, 34.6) * mm, "mid": v(-69.47, 34.66) * mm, "end": v(-69.17, 34.96) * mm});
            skArc(sketch, "E6754", {"start": v(-68.94, 35.4) * mm, "mid": v(-69.05, 35.18) * mm, "end": v(-69.17, 34.96) * mm});
            skArc(sketch, "E6755", {"start": v(-68.94, 35.4) * mm, "mid": v(-68.88, 35.82) * mm, "end": v(-69.08, 36.2) * mm});
            skLineSegment(sketch, "E6756", {"start": v(-70.66, 37.83) * mm, "end": v(-71.93, 39.37) * mm});
            skLineSegment(sketch, "E6757", {"start": v(-69.08, 36.2) * mm, "end": v(-70.66, 37.83) * mm});
            skArc(sketch, "E6758", {"start": v(-71.15, 40.76) * mm, "mid": v(-71.54, 40.07) * mm, "end": v(-71.93, 39.37) * mm});
            skLineSegment(sketch, "E6759", {"start": v(-69.17, 40.48) * mm, "end": v(-71.15, 40.76) * mm});
            skLineSegment(sketch, "E6760", {"start": v(-66.96, 39.99) * mm, "end": v(-69.17, 40.48) * mm});
            skArc(sketch, "E6761", {"start": v(-66.96, 39.99) * mm, "mid": v(-66.53, 40) * mm, "end": v(-66.2, 40.28) * mm});
            skArc(sketch, "E6762", {"start": v(59.13, -10.16) * mm, "mid": v(54.65, -16.05) * mm, "end": v(47.25, -15.73) * mm});
            skArc(sketch, "E6763", {"start": v(20.77, 56.3) * mm, "mid": v(51.96, 30) * mm, "end": v(59.13, -10.16) * mm});
            skArc(sketch, "E6764", {"start": v(10, 48.79) * mm, "mid": v(13.43, 55.35) * mm, "end": v(20.77, 56.3) * mm});
            skLineSegment(sketch, "E6765", {"start": v(10, 48.79) * mm, "end": v(10, 21.45) * mm});
            skArc(sketch, "E6766", {"start": v(12.86, 15.32) * mm, "mid": v(10.75, 18.07) * mm, "end": v(10, 21.45) * mm});
            skArc(sketch, "E6767", {"start": v(12.86, 15.32) * mm, "mid": v(17.32, 10) * mm, "end": v(19.7, 3.47) * mm});
            skArc(sketch, "E6768", {"start": v(23.57, -2.06) * mm, "mid": v(21.02, 0.28) * mm, "end": v(19.7, 3.47) * mm});
            skLineSegment(sketch, "E6769", {"start": v(47.25, -15.73) * mm, "end": v(23.57, -2.06) * mm});
            skArc(sketch, "E6770", {"start": v(37.25, -33.05) * mm, "mid": v(41.22, -39.3) * mm, "end": v(38.36, -46.13) * mm});
            skLineSegment(sketch, "E6771", {"start": v(37.25, -33.05) * mm, "end": v(13.57, -19.38) * mm});
            skArc(sketch, "E6772", {"start": v(6.84, -18.8) * mm, "mid": v(10.27, -18.34) * mm, "end": v(13.57, -19.38) * mm});
            skArc(sketch, "E6773", {"start": v(6.84, -18.8) * mm, "mid": v(0, -20) * mm, "end": v(-6.84, -18.8) * mm});
            skArc(sketch, "E6774", {"start": v(-13.57, -19.38) * mm, "mid": v(-10.27, -18.34) * mm, "end": v(-6.84, -18.8) * mm});
            skLineSegment(sketch, "E6775", {"start": v(-37.25, -33.05) * mm, "end": v(-13.57, -19.38) * mm});
            skArc(sketch, "E6776", {"start": v(-38.36, -46.13) * mm, "mid": v(-41.22, -39.3) * mm, "end": v(-37.25, -33.05) * mm});
            skArc(sketch, "E6777", {"start": v(38.36, -46.13) * mm, "mid": v(0, -60) * mm, "end": v(-38.36, -46.13) * mm});
            skLineSegment(sketch, "E6778", {"start": v(72.39, -29.02) * mm, "end": v(74.66, -29.16) * mm});
            skLineSegment(sketch, "E6779", {"start": v(74.66, -29.16) * mm, "end": v(76.65, -29.13) * mm});
            skArc(sketch, "E6780", {"start": v(76.65, -29.13) * mm, "mid": v(76.93, -28.38) * mm, "end": v(77.2, -27.63) * mm});
            skLineSegment(sketch, "E6781", {"start": v(73.9, -24.95) * mm, "end": v(75.7, -26.31) * mm});
            skLineSegment(sketch, "E6782", {"start": v(75.7, -26.31) * mm, "end": v(77.2, -27.63) * mm});
            skArc(sketch, "E6783", {"start": v(73.63, -24.18) * mm, "mid": v(73.63, -24.6) * mm, "end": v(73.9, -24.95) * mm});
            skArc(sketch, "E6784", {"start": v(73.63, -24.18) * mm, "mid": v(73.7, -23.95) * mm, "end": v(73.78, -23.71) * mm});
            skArc(sketch, "E6785", {"start": v(74.44, -23.25) * mm, "mid": v(74.03, -23.37) * mm, "end": v(73.78, -23.71) * mm});
            skLineSegment(sketch, "E6786", {"start": v(74.44, -23.25) * mm, "end": v(76.71, -23.21) * mm});
            skLineSegment(sketch, "E6787", {"start": v(76.71, -23.21) * mm, "end": v(78.7, -23.02) * mm});
            skArc(sketch, "E6788", {"start": v(78.7, -23.02) * mm, "mid": v(78.92, -22.26) * mm, "end": v(79.13, -21.5) * mm});
            skLineSegment(sketch, "E6789", {"start": v(75.62, -19.07) * mm, "end": v(77.54, -20.29) * mm});
            skLineSegment(sketch, "E6790", {"start": v(77.54, -20.29) * mm, "end": v(79.13, -21.5) * mm});
            skArc(sketch, "E6791", {"start": v(75.3, -18.33) * mm, "mid": v(75.34, -18.76) * mm, "end": v(75.62, -19.07) * mm});
            skArc(sketch, "E6792", {"start": v(75.3, -18.33) * mm, "mid": v(75.36, -18.1) * mm, "end": v(75.42, -17.85) * mm});
            skArc(sketch, "E6793", {"start": v(76.04, -17.34) * mm, "mid": v(75.64, -17.5) * mm, "end": v(75.42, -17.85) * mm});
            skLineSegment(sketch, "E6794", {"start": v(76.04, -17.34) * mm, "end": v(78.3, -17.12) * mm});
            skLineSegment(sketch, "E6795", {"start": v(78.3, -17.12) * mm, "end": v(80.27, -16.78) * mm});
            skArc(sketch, "E6796", {"start": v(80.27, -16.78) * mm, "mid": v(80.42, -16) * mm, "end": v(80.58, -15.22) * mm});
            skLineSegment(sketch, "E6797", {"start": v(76.88, -13.08) * mm, "end": v(78.9, -14.14) * mm});
            skLineSegment(sketch, "E6798", {"start": v(78.9, -14.14) * mm, "end": v(80.58, -15.22) * mm});
            skArc(sketch, "E6799", {"start": v(76.5, -12.37) * mm, "mid": v(76.58, -12.79) * mm, "end": v(76.88, -13.08) * mm});
            skArc(sketch, "E6800", {"start": v(76.5, -12.37) * mm, "mid": v(76.55, -12.12) * mm, "end": v(76.58, -11.88) * mm});
            skArc(sketch, "E6801", {"start": v(77.16, -11.32) * mm, "mid": v(76.78, -11.5) * mm, "end": v(76.58, -11.88) * mm});
            skLineSegment(sketch, "E6802", {"start": v(77.16, -11.32) * mm, "end": v(79.4, -10.93) * mm});
            skLineSegment(sketch, "E6803", {"start": v(79.4, -10.93) * mm, "end": v(81.33, -10.43) * mm});
            skArc(sketch, "E6804", {"start": v(81.33, -10.43) * mm, "mid": v(81.43, -9.64) * mm, "end": v(81.52, -8.85) * mm});
            skLineSegment(sketch, "E6805", {"start": v(77.67, -7) * mm, "end": v(79.76, -7.9) * mm});
            skLineSegment(sketch, "E6806", {"start": v(79.76, -7.9) * mm, "end": v(81.52, -8.85) * mm});
            skArc(sketch, "E6807", {"start": v(77.24, -6.33) * mm, "mid": v(77.34, -6.74) * mm, "end": v(77.67, -7) * mm});
            skArc(sketch, "E6808", {"start": v(77.24, -6.33) * mm, "mid": v(77.26, -6.08) * mm, "end": v(77.28, -5.83) * mm});
            skArc(sketch, "E6809", {"start": v(77.81, -5.23) * mm, "mid": v(77.45, -5.44) * mm, "end": v(77.28, -5.83) * mm});
            skLineSegment(sketch, "E6810", {"start": v(77.81, -5.23) * mm, "end": v(80.01, -4.66) * mm});
            skLineSegment(sketch, "E6811", {"start": v(80.01, -4.66) * mm, "end": v(81.9, -4.01) * mm});
            skArc(sketch, "E6812", {"start": v(81.9, -4.01) * mm, "mid": v(81.94, -3.22) * mm, "end": v(81.96, -2.42) * mm});
            skLineSegment(sketch, "E6813", {"start": v(77.98, -0.9) * mm, "end": v(80.13, -1.63) * mm});
            skLineSegment(sketch, "E6814", {"start": v(80.13, -1.63) * mm, "end": v(81.96, -2.42) * mm});
            skArc(sketch, "E6815", {"start": v(77.5, -0.25) * mm, "mid": v(77.63, -0.65) * mm, "end": v(77.98, -0.9) * mm});
            skArc(sketch, "E6816", {"start": v(77.5, -0.25) * mm, "mid": v(77.5, 0) * mm, "end": v(77.5, 0.25) * mm});
            skArc(sketch, "E6817", {"start": v(77.98, 0.9) * mm, "mid": v(77.63, 0.65) * mm, "end": v(77.5, 0.25) * mm});
            skLineSegment(sketch, "E6818", {"start": v(77.98, 0.9) * mm, "end": v(80.13, 1.63) * mm});
            skLineSegment(sketch, "E6819", {"start": v(80.13, 1.63) * mm, "end": v(81.96, 2.42) * mm});
            skArc(sketch, "E6820", {"start": v(81.96, 2.42) * mm, "mid": v(81.94, 3.22) * mm, "end": v(81.9, 4.01) * mm});
            skLineSegment(sketch, "E6821", {"start": v(77.81, 5.23) * mm, "end": v(80.01, 4.66) * mm});
            skLineSegment(sketch, "E6822", {"start": v(80.01, 4.66) * mm, "end": v(81.9, 4.01) * mm});
            skArc(sketch, "E6823", {"start": v(77.28, 5.83) * mm, "mid": v(77.45, 5.44) * mm, "end": v(77.81, 5.23) * mm});
            skArc(sketch, "E6824", {"start": v(77.28, 5.83) * mm, "mid": v(77.26, 6.08) * mm, "end": v(77.24, 6.33) * mm});
            skArc(sketch, "E6825", {"start": v(77.67, 7) * mm, "mid": v(77.34, 6.74) * mm, "end": v(77.24, 6.33) * mm});
            skLineSegment(sketch, "E6826", {"start": v(77.67, 7) * mm, "end": v(79.76, 7.9) * mm});
            skLineSegment(sketch, "E6827", {"start": v(79.76, 7.9) * mm, "end": v(81.52, 8.85) * mm});
            skArc(sketch, "E6828", {"start": v(81.52, 8.85) * mm, "mid": v(81.43, 9.64) * mm, "end": v(81.33, 10.43) * mm});
            skLineSegment(sketch, "E6829", {"start": v(77.16, 11.32) * mm, "end": v(79.4, 10.93) * mm});
            skLineSegment(sketch, "E6830", {"start": v(79.4, 10.93) * mm, "end": v(81.33, 10.43) * mm});
            skArc(sketch, "E6831", {"start": v(76.58, 11.88) * mm, "mid": v(76.78, 11.5) * mm, "end": v(77.16, 11.32) * mm});
            skSolve(sketch);
        }
        {
            var Q0;
            Q0=qCreatedBy(makeId("Front.planeOp"),FACE);
            var sketch = newSketch(context, id + "F4", { "sketchPlane" : qUnion([Q0])});
            skArc(sketch, "E6832", {"start": v(-16.1, -25.31) * mm, "mid": v(-16.55, -25.02) * mm, "end": v(-16.99, -24.73) * mm});
            skArc(sketch, "E6833", {"start": v(-16.1, -25.31) * mm, "mid": v(-13.33, -28.3) * mm, "end": v(-12.4, -32.27) * mm});
            skLineSegment(sketch, "E6834", {"start": v(-12.4, -32.27) * mm, "end": v(-13.63, -79.3) * mm});
            skArc(sketch, "E6835", {"start": v(-13.63, -79.3) * mm, "mid": v(-16.86, -85.52) * mm, "end": v(-23.74, -86.81) * mm});
            skArc(sketch, "E6836", {"start": v(-23.74, -86.81) * mm, "mid": v(-48.12, -76.05) * mm, "end": v(-68.28, -58.63) * mm});
            skArc(sketch, "E6837", {"start": v(-68.28, -58.63) * mm, "mid": v(-70.08, -51.97) * mm, "end": v(-66.03, -46.39) * mm});
            skLineSegment(sketch, "E6838", {"start": v(-25.33, -24.3) * mm, "end": v(-66.03, -46.39) * mm});
            skArc(sketch, "E6839", {"start": v(-25.33, -24.3) * mm, "mid": v(-21.1, -23.33) * mm, "end": v(-16.99, -24.73) * mm});
            skArc(sketch, "E6840", {"start": v(-30, 0.55) * mm, "mid": v(-30, 0.75) * mm, "end": v(-29.98, 0.96) * mm});
            skArc(sketch, "E6841", {"start": v(-30, 0.55) * mm, "mid": v(-31.16, -3.46) * mm, "end": v(-34.18, -6.33) * mm});
            skLineSegment(sketch, "E6842", {"start": v(-34.18, -6.33) * mm, "end": v(-75.28, -28.65) * mm});
            skArc(sketch, "E6843", {"start": v(-75.28, -28.65) * mm, "mid": v(-82.24, -28.98) * mm, "end": v(-86.82, -23.73) * mm});
            skArc(sketch, "E6844", {"start": v(-86.82, -23.73) * mm, "mid": v(-89.97, 2.32) * mm, "end": v(-85.48, 28.17) * mm});
            skArc(sketch, "E6845", {"start": v(-85.48, 28.17) * mm, "mid": v(-80.63, 33.18) * mm, "end": v(-73.7, 32.49) * mm});
            skLineSegment(sketch, "E6846", {"start": v(-33.8, 8.04) * mm, "end": v(-73.7, 32.49) * mm});
            skArc(sketch, "E6847", {"start": v(-33.8, 8.04) * mm, "mid": v(-30.94, 5.01) * mm, "end": v(-29.98, 0.96) * mm});
            skLineSegment(sketch, "E6848", {"start": v(34.17, 8.01) * mm, "end": v(74.87, 30.1) * mm});
            skArc(sketch, "E6849", {"start": v(74.87, 30.1) * mm, "mid": v(81.76, 30.46) * mm, "end": v(86.36, 25.33) * mm});
            skArc(sketch, "E6850", {"start": v(86.36, 25.33) * mm, "mid": v(89.97, -2.4) * mm, "end": v(84.89, -29.9) * mm});
            skArc(sketch, "E6851", {"start": v(84.89, -29.9) * mm, "mid": v(80.02, -34.78) * mm, "end": v(73.16, -34.06) * mm});
            skLineSegment(sketch, "E6852", {"start": v(33.7, -9.87) * mm, "end": v(73.16, -34.06) * mm});
            skArc(sketch, "E6853", {"start": v(33.7, -9.87) * mm, "mid": v(30.75, -6.68) * mm, "end": v(29.9, -2.4) * mm});
            skArc(sketch, "E6854", {"start": v(29.99, 0.78) * mm, "mid": v(29.99, -0.82) * mm, "end": v(29.9, -2.4) * mm});
            skArc(sketch, "E6855", {"start": v(29.99, 0.78) * mm, "mid": v(31.06, 4.98) * mm, "end": v(34.17, 8.01) * mm});
            skArc(sketch, "E6856", {"start": v(13.7, 26.7) * mm, "mid": v(14.8, 26.1) * mm, "end": v(15.88, 25.45) * mm});
            skArc(sketch, "E6857", {"start": v(13.7, 26.7) * mm, "mid": v(10.46, 29.73) * mm, "end": v(9.35, 34.02) * mm});
            skLineSegment(sketch, "E6858", {"start": v(9.35, 34.02) * mm, "end": v(10.55, 80.08) * mm});
            skArc(sketch, "E6859", {"start": v(10.55, 80.08) * mm, "mid": v(13.66, 86.2) * mm, "end": v(20.36, 87.67) * mm});
            skArc(sketch, "E6860", {"start": v(20.36, 87.67) * mm, "mid": v(45.93, 77.4) * mm, "end": v(67.19, 59.88) * mm});
            skArc(sketch, "E6861", {"start": v(67.19, 59.88) * mm, "mid": v(69.1, 53.18) * mm, "end": v(65.03, 47.53) * mm});
            skLineSegment(sketch, "E6862", {"start": v(23.93, 25.21) * mm, "end": v(65.03, 47.53) * mm});
            skArc(sketch, "E6863", {"start": v(23.93, 25.21) * mm, "mid": v(19.87, 24.25) * mm, "end": v(15.88, 25.45) * mm});
            skArc(sketch, "E6864", {"start": v(12.05, 116.88) * mm, "mid": v(12.28, 116.86) * mm, "end": v(12.52, 116.83) * mm});
            skArc(sketch, "E6865", {"start": v(12.05, 116.88) * mm, "mid": v(11.67, 117.05) * mm, "end": v(11.47, 117.4) * mm});
            skLineSegment(sketch, "E6866", {"start": v(10.94, 119.67) * mm, "end": v(10.38, 121.56) * mm});
            skLineSegment(sketch, "E6867", {"start": v(11.47, 117.4) * mm, "end": v(10.94, 119.67) * mm});
            skArc(sketch, "E6868", {"start": v(8.76, 121.68) * mm, "mid": v(9.57, 121.62) * mm, "end": v(10.38, 121.56) * mm});
            skLineSegment(sketch, "E6869", {"start": v(7.92, 119.9) * mm, "end": v(8.76, 121.68) * mm});
            skLineSegment(sketch, "E6870", {"start": v(7.04, 117.75) * mm, "end": v(7.92, 119.9) * mm});
            skArc(sketch, "E6871", {"start": v(7.04, 117.75) * mm, "mid": v(6.78, 117.43) * mm, "end": v(6.39, 117.33) * mm});
            skArc(sketch, "E6872", {"start": v(5.91, 117.35) * mm, "mid": v(6.15, 117.34) * mm, "end": v(6.39, 117.33) * mm});
            skArc(sketch, "E6873", {"start": v(5.91, 117.35) * mm, "mid": v(5.53, 117.5) * mm, "end": v(5.3, 117.84) * mm});
            skLineSegment(sketch, "E6874", {"start": v(4.66, 120.08) * mm, "end": v(4, 121.93) * mm});
            skLineSegment(sketch, "E6875", {"start": v(5.3, 117.84) * mm, "end": v(4.66, 120.08) * mm});
            skArc(sketch, "E6876", {"start": v(2.38, 121.98) * mm, "mid": v(3.2, 121.96) * mm, "end": v(4, 121.93) * mm});
            skLineSegment(sketch, "E6877", {"start": v(1.63, 120.15) * mm, "end": v(2.38, 121.98) * mm});
            skLineSegment(sketch, "E6878", {"start": v(0.86, 117.96) * mm, "end": v(1.63, 120.15) * mm});
            skArc(sketch, "E6879", {"start": v(0.86, 117.96) * mm, "mid": v(0.63, 117.63) * mm, "end": v(0.24, 117.5) * mm});
            skArc(sketch, "E6880", {"start": v(-0.24, 117.5) * mm, "mid": v(0, 117.5) * mm, "end": v(0.24, 117.5) * mm});
            skArc(sketch, "E6881", {"start": v(-0.24, 117.5) * mm, "mid": v(-0.63, 117.63) * mm, "end": v(-0.86, 117.96) * mm});
            skLineSegment(sketch, "E6882", {"start": v(-1.63, 120.15) * mm, "end": v(-2.38, 121.98) * mm});
            skLineSegment(sketch, "E6883", {"start": v(-0.86, 117.96) * mm, "end": v(-1.63, 120.15) * mm});
            skArc(sketch, "E6884", {"start": v(-4, 121.93) * mm, "mid": v(-3.2, 121.96) * mm, "end": v(-2.38, 121.98) * mm});
            skLineSegment(sketch, "E6885", {"start": v(-4.66, 120.08) * mm, "end": v(-4, 121.93) * mm});
            skLineSegment(sketch, "E6886", {"start": v(-5.3, 117.84) * mm, "end": v(-4.66, 120.08) * mm});
            skArc(sketch, "E6887", {"start": v(-5.3, 117.84) * mm, "mid": v(-5.53, 117.5) * mm, "end": v(-5.91, 117.35) * mm});
            skArc(sketch, "E6888", {"start": v(-6.39, 117.33) * mm, "mid": v(-6.15, 117.34) * mm, "end": v(-5.91, 117.35) * mm});
            skArc(sketch, "E6889", {"start": v(-6.39, 117.33) * mm, "mid": v(-6.78, 117.43) * mm, "end": v(-7.04, 117.75) * mm});
            skLineSegment(sketch, "E6890", {"start": v(-7.92, 119.9) * mm, "end": v(-8.76, 121.68) * mm});
            skLineSegment(sketch, "E6891", {"start": v(-7.04, 117.75) * mm, "end": v(-7.92, 119.9) * mm});
            skArc(sketch, "E6892", {"start": v(-10.38, 121.56) * mm, "mid": v(-9.57, 121.62) * mm, "end": v(-8.76, 121.68) * mm});
            skLineSegment(sketch, "E6893", {"start": v(-10.94, 119.67) * mm, "end": v(-10.38, 121.56) * mm});
            skLineSegment(sketch, "E6894", {"start": v(-11.47, 117.4) * mm, "end": v(-10.94, 119.67) * mm});
            skArc(sketch, "E6895", {"start": v(-11.47, 117.4) * mm, "mid": v(-11.67, 117.05) * mm, "end": v(-12.05, 116.88) * mm});
            skArc(sketch, "E6896", {"start": v(-12.52, 116.83) * mm, "mid": v(-12.28, 116.86) * mm, "end": v(-12.05, 116.88) * mm});
            skArc(sketch, "E6897", {"start": v(-12.52, 116.83) * mm, "mid": v(-12.92, 116.92) * mm, "end": v(-13.19, 117.22) * mm});
            skLineSegment(sketch, "E6898", {"start": v(-14.18, 119.33) * mm, "end": v(-15.12, 121.06) * mm});
            skLineSegment(sketch, "E6899", {"start": v(-13.19, 117.22) * mm, "end": v(-14.18, 119.33) * mm});
            skArc(sketch, "E6900", {"start": v(-16.73, 120.85) * mm, "mid": v(-15.92, 120.96) * mm, "end": v(-15.12, 121.06) * mm});
            skLineSegment(sketch, "E6901", {"start": v(-17.18, 118.93) * mm, "end": v(-16.73, 120.85) * mm});
            skLineSegment(sketch, "E6902", {"start": v(-17.6, 116.64) * mm, "end": v(-17.18, 118.93) * mm});
            skArc(sketch, "E6903", {"start": v(-17.6, 116.64) * mm, "mid": v(-17.78, 116.28) * mm, "end": v(-18.15, 116.1) * mm});
            skArc(sketch, "E6904", {"start": v(-18.62, 116.02) * mm, "mid": v(-18.38, 116.05) * mm, "end": v(-18.15, 116.1) * mm});
            skArc(sketch, "E6905", {"start": v(-18.62, 116.02) * mm, "mid": v(-19.02, 116.08) * mm, "end": v(-19.3, 116.37) * mm});
            skLineSegment(sketch, "E6906", {"start": v(-20.4, 118.42) * mm, "end": v(-21.44, 120.1) * mm});
            skLineSegment(sketch, "E6907", {"start": v(-19.3, 116.37) * mm, "end": v(-20.4, 118.42) * mm});
            skArc(sketch, "E6908", {"start": v(-23.03, 119.8) * mm, "mid": v(-22.23, 119.96) * mm, "end": v(-21.44, 120.1) * mm});
            skLineSegment(sketch, "E6909", {"start": v(-23.38, 117.87) * mm, "end": v(-23.03, 119.8) * mm});
            skLineSegment(sketch, "E6910", {"start": v(-23.68, 115.56) * mm, "end": v(-23.38, 117.87) * mm});
            skArc(sketch, "E6911", {"start": v(-23.68, 115.56) * mm, "mid": v(-23.84, 115.19) * mm, "end": v(-24.2, 114.98) * mm});
            skArc(sketch, "E6912", {"start": v(-24.66, 114.88) * mm, "mid": v(-24.43, 114.93) * mm, "end": v(-24.2, 114.98) * mm});
            skArc(sketch, "E6913", {"start": v(-24.66, 114.88) * mm, "mid": v(-25.07, 114.93) * mm, "end": v(-25.37, 115.2) * mm});
            skLineSegment(sketch, "E6914", {"start": v(-26.58, 117.19) * mm, "end": v(-27.7, 118.82) * mm});
            skLineSegment(sketch, "E6915", {"start": v(-25.37, 115.2) * mm, "end": v(-26.58, 117.19) * mm});
            skArc(sketch, "E6916", {"start": v(-29.27, 118.44) * mm, "mid": v(-28.48, 118.63) * mm, "end": v(-27.7, 118.82) * mm});
            skLineSegment(sketch, "E6917", {"start": v(-29.52, 116.48) * mm, "end": v(-29.27, 118.44) * mm});
            skLineSegment(sketch, "E6918", {"start": v(-29.7, 114.16) * mm, "end": v(-29.52, 116.48) * mm});
            skArc(sketch, "E6919", {"start": v(-29.7, 114.16) * mm, "mid": v(-29.84, 113.78) * mm, "end": v(-30.18, 113.56) * mm});
            skArc(sketch, "E6920", {"start": v(-30.64, 113.43) * mm, "mid": v(-30.41, 113.5) * mm, "end": v(-30.18, 113.56) * mm});
            skArc(sketch, "E6921", {"start": v(-30.64, 113.43) * mm, "mid": v(-31.05, 113.46) * mm, "end": v(-31.36, 113.71) * mm});
            skLineSegment(sketch, "E6922", {"start": v(-32.68, 115.64) * mm, "end": v(-33.87, 117.2) * mm});
            skLineSegment(sketch, "E6923", {"start": v(-31.36, 113.71) * mm, "end": v(-32.68, 115.64) * mm});
            skArc(sketch, "E6924", {"start": v(-35.43, 116.74) * mm, "mid": v(-34.65, 116.98) * mm, "end": v(-33.87, 117.2) * mm});
            skLineSegment(sketch, "E6925", {"start": v(-35.58, 114.78) * mm, "end": v(-35.43, 116.74) * mm});
            skLineSegment(sketch, "E6926", {"start": v(-35.63, 112.45) * mm, "end": v(-35.58, 114.78) * mm});
            skArc(sketch, "E6927", {"start": v(-35.63, 112.45) * mm, "mid": v(-35.75, 112.06) * mm, "end": v(-36.08, 111.82) * mm});
            skArc(sketch, "E6928", {"start": v(-36.54, 111.68) * mm, "mid": v(-36.3, 111.75) * mm, "end": v(-36.08, 111.82) * mm});
            skArc(sketch, "E6929", {"start": v(-36.54, 111.68) * mm, "mid": v(-36.94, 111.68) * mm, "end": v(-37.27, 111.92) * mm});
            skLineSegment(sketch, "E6930", {"start": v(-38.68, 113.77) * mm, "end": v(-39.96, 115.27) * mm});
            skLineSegment(sketch, "E6931", {"start": v(-37.27, 111.92) * mm, "end": v(-38.68, 113.77) * mm});
            skArc(sketch, "E6932", {"start": v(-41.49, 114.73) * mm, "mid": v(-40.72, 115) * mm, "end": v(-39.96, 115.27) * mm});
            skLineSegment(sketch, "E6933", {"start": v(-41.54, 112.76) * mm, "end": v(-41.49, 114.73) * mm});
            skLineSegment(sketch, "E6934", {"start": v(-41.47, 110.43) * mm, "end": v(-41.54, 112.76) * mm});
            skArc(sketch, "E6935", {"start": v(-41.47, 110.43) * mm, "mid": v(-41.57, 110.04) * mm, "end": v(-41.89, 109.78) * mm});
            skArc(sketch, "E6936", {"start": v(-42.33, 109.61) * mm, "mid": v(-42.1, 109.7) * mm, "end": v(-41.89, 109.78) * mm});
            skArc(sketch, "E6937", {"start": v(-42.33, 109.61) * mm, "mid": v(-42.74, 109.59) * mm, "end": v(-43.08, 109.81) * mm});
            skLineSegment(sketch, "E6938", {"start": v(-44.58, 111.59) * mm, "end": v(-45.94, 113.02) * mm});
            skLineSegment(sketch, "E6939", {"start": v(-43.08, 109.81) * mm, "end": v(-44.58, 111.59) * mm});
            skArc(sketch, "E6940", {"start": v(-47.43, 112.4) * mm, "mid": v(-46.69, 112.71) * mm, "end": v(-45.94, 113.02) * mm});
            skLineSegment(sketch, "E6941", {"start": v(-47.38, 110.43) * mm, "end": v(-47.43, 112.4) * mm});
            skLineSegment(sketch, "E6942", {"start": v(-47.19, 108.11) * mm, "end": v(-47.38, 110.43) * mm});
            skArc(sketch, "E6943", {"start": v(-47.19, 108.11) * mm, "mid": v(-47.27, 107.71) * mm, "end": v(-47.57, 107.44) * mm});
            skArc(sketch, "E6944", {"start": v(-48, 107.24) * mm, "mid": v(-47.8, 107.34) * mm, "end": v(-47.57, 107.44) * mm});
            skArc(sketch, "E6945", {"start": v(-48, 107.24) * mm, "mid": v(-48.42, 107.2) * mm, "end": v(-48.77, 107.4) * mm});
            skLineSegment(sketch, "E6946", {"start": v(-50.36, 109.1) * mm, "end": v(-51.8, 110.46) * mm});
            skLineSegment(sketch, "E6947", {"start": v(-48.77, 107.4) * mm, "end": v(-50.36, 109.1) * mm});
            skArc(sketch, "E6948", {"start": v(-53.25, 109.76) * mm, "mid": v(-52.52, 110.12) * mm, "end": v(-51.8, 110.46) * mm});
            skLineSegment(sketch, "E6949", {"start": v(-53.1, 107.8) * mm, "end": v(-53.25, 109.76) * mm});
            skLineSegment(sketch, "E6950", {"start": v(-52.78, 105.5) * mm, "end": v(-53.1, 107.8) * mm});
            skArc(sketch, "E6951", {"start": v(-52.78, 105.5) * mm, "mid": v(-52.84, 105.1) * mm, "end": v(-53.13, 104.8) * mm});
            skArc(sketch, "E6952", {"start": v(-53.56, 104.58) * mm, "mid": v(-53.34, 104.7) * mm, "end": v(-53.13, 104.8) * mm});
            skArc(sketch, "E6953", {"start": v(-53.56, 104.58) * mm, "mid": v(-53.96, 104.52) * mm, "end": v(-54.32, 104.7) * mm});
            skLineSegment(sketch, "E6954", {"start": v(-56, 106.32) * mm, "end": v(-57.5, 107.6) * mm});
            skLineSegment(sketch, "E6955", {"start": v(-54.32, 104.7) * mm, "end": v(-56, 106.32) * mm});
            skArc(sketch, "E6956", {"start": v(-58.92, 106.83) * mm, "mid": v(-58.21, 107.22) * mm, "end": v(-57.5, 107.6) * mm});
            skLineSegment(sketch, "E6957", {"start": v(-58.66, 104.87) * mm, "end": v(-58.92, 106.83) * mm});
            skLineSegment(sketch, "E6958", {"start": v(-58.23, 102.59) * mm, "end": v(-58.66, 104.87) * mm});
            skArc(sketch, "E6959", {"start": v(-58.23, 102.59) * mm, "mid": v(-58.27, 102.18) * mm, "end": v(-58.54, 101.88) * mm});
            skArc(sketch, "E6960", {"start": v(-58.96, 101.64) * mm, "mid": v(-58.75, 101.76) * mm, "end": v(-58.54, 101.88) * mm});
            skArc(sketch, "E6961", {"start": v(-58.96, 101.64) * mm, "mid": v(-59.36, 101.55) * mm, "end": v(-59.73, 101.72) * mm});
            skLineSegment(sketch, "E6962", {"start": v(-61.5, 103.24) * mm, "end": v(-63.05, 104.44) * mm});
            skLineSegment(sketch, "E6963", {"start": v(-59.73, 101.72) * mm, "end": v(-61.5, 103.24) * mm});
            skArc(sketch, "E6964", {"start": v(-64.43, 103.6) * mm, "mid": v(-63.74, 104.02) * mm, "end": v(-63.05, 104.44) * mm});
            skLineSegment(sketch, "E6965", {"start": v(-64.07, 101.66) * mm, "end": v(-64.43, 103.6) * mm});
            skLineSegment(sketch, "E6966", {"start": v(-63.52, 99.4) * mm, "end": v(-64.07, 101.66) * mm});
            skArc(sketch, "E6967", {"start": v(-63.52, 99.4) * mm, "mid": v(-63.54, 99) * mm, "end": v(-63.8, 98.67) * mm});
            skArc(sketch, "E6968", {"start": v(-64.2, 98.41) * mm, "mid": v(-64, 98.54) * mm, "end": v(-63.8, 98.67) * mm});
            skArc(sketch, "E6969", {"start": v(-64.2, 98.41) * mm, "mid": v(-64.59, 98.3) * mm, "end": v(-64.97, 98.46) * mm});
            skLineSegment(sketch, "E6970", {"start": v(-66.8, 99.88) * mm, "end": v(-68.43, 101) * mm});
            skLineSegment(sketch, "E6971", {"start": v(-64.97, 98.46) * mm, "end": v(-66.8, 99.88) * mm});
            skArc(sketch, "E6972", {"start": v(-69.77, 100.08) * mm, "mid": v(-69.1, 100.54) * mm, "end": v(-68.43, 101) * mm});
            skLineSegment(sketch, "E6973", {"start": v(-69.3, 98.17) * mm, "end": v(-69.77, 100.08) * mm});
            skLineSegment(sketch, "E6974", {"start": v(-68.63, 95.94) * mm, "end": v(-69.3, 98.17) * mm});
            skArc(sketch, "E6975", {"start": v(-68.63, 95.94) * mm, "mid": v(-68.63, 95.53) * mm, "end": v(-68.87, 95.2) * mm});
            skArc(sketch, "E6976", {"start": v(-69.26, 94.92) * mm, "mid": v(-69.06, 95.06) * mm, "end": v(-68.87, 95.2) * mm});
            skArc(sketch, "E6977", {"start": v(-69.26, 94.92) * mm, "mid": v(-69.65, 94.8) * mm, "end": v(-70.03, 94.92) * mm});
            skLineSegment(sketch, "E6978", {"start": v(-71.95, 96.25) * mm, "end": v(-73.62, 97.28) * mm});
            skLineSegment(sketch, "E6979", {"start": v(-70.03, 94.92) * mm, "end": v(-71.95, 96.25) * mm});
            skArc(sketch, "E6980", {"start": v(-74.9, 96.3) * mm, "mid": v(-74.27, 96.79) * mm, "end": v(-73.62, 97.28) * mm});
            skLineSegment(sketch, "E6981", {"start": v(-74.35, 94.4) * mm, "end": v(-74.9, 96.3) * mm});
            skLineSegment(sketch, "E6982", {"start": v(-73.56, 92.21) * mm, "end": v(-74.35, 94.4) * mm});
            skArc(sketch, "E6983", {"start": v(-73.56, 92.21) * mm, "mid": v(-73.54, 91.8) * mm, "end": v(-73.76, 91.46) * mm});
            skArc(sketch, "E6984", {"start": v(-74.13, 91.16) * mm, "mid": v(-73.95, 91.31) * mm, "end": v(-73.76, 91.46) * mm});
            skArc(sketch, "E6985", {"start": v(-74.13, 91.16) * mm, "mid": v(-74.51, 91.02) * mm, "end": v(-74.9, 91.13) * mm});
            skLineSegment(sketch, "E6986", {"start": v(-76.88, 92.35) * mm, "end": v(-78.62, 93.3) * mm});
            skLineSegment(sketch, "E6987", {"start": v(-74.9, 91.13) * mm, "end": v(-76.88, 92.35) * mm});
            skArc(sketch, "E6988", {"start": v(-79.85, 92.24) * mm, "mid": v(-79.23, 92.77) * mm, "end": v(-78.62, 93.3) * mm});
            skLineSegment(sketch, "E6989", {"start": v(-79.19, 90.38) * mm, "end": v(-79.85, 92.24) * mm});
            skLineSegment(sketch, "E6990", {"start": v(-78.29, 88.24) * mm, "end": v(-79.19, 90.38) * mm});
            skArc(sketch, "E6991", {"start": v(-78.29, 88.24) * mm, "mid": v(-78.24, 87.83) * mm, "end": v(-78.45, 87.48) * mm});
            skArc(sketch, "E6992", {"start": v(-78.8, 87.16) * mm, "mid": v(-78.62, 87.32) * mm, "end": v(-78.45, 87.48) * mm});
            skArc(sketch, "E6993", {"start": v(-78.8, 87.16) * mm, "mid": v(-79.17, 87) * mm, "end": v(-79.57, 87.08) * mm});
            skLineSegment(sketch, "E6994", {"start": v(-81.61, 88.2) * mm, "end": v(-83.4, 89.05) * mm});
            skLineSegment(sketch, "E6995", {"start": v(-79.57, 87.08) * mm, "end": v(-81.61, 88.2) * mm});
            skArc(sketch, "E6996", {"start": v(-84.56, 87.94) * mm, "mid": v(-83.98, 88.5) * mm, "end": v(-83.4, 89.05) * mm});
            skLineSegment(sketch, "E6997", {"start": v(-83.8, 86.12) * mm, "end": v(-84.56, 87.94) * mm});
            skLineSegment(sketch, "E6998", {"start": v(-82.8, 84.02) * mm, "end": v(-83.8, 86.12) * mm});
            skArc(sketch, "E6999", {"start": v(-82.8, 84.02) * mm, "mid": v(-82.73, 83.62) * mm, "end": v(-82.92, 83.25) * mm});
            skArc(sketch, "E7000", {"start": v(-83.25, 82.92) * mm, "mid": v(-83.09, 83.09) * mm, "end": v(-82.92, 83.25) * mm});
            skArc(sketch, "E7001", {"start": v(-83.25, 82.92) * mm, "mid": v(-83.62, 82.73) * mm, "end": v(-84.02, 82.8) * mm});
            skLineSegment(sketch, "E7002", {"start": v(-86.12, 83.8) * mm, "end": v(-87.94, 84.56) * mm});
            skLineSegment(sketch, "E7003", {"start": v(-84.02, 82.8) * mm, "end": v(-86.12, 83.8) * mm});
            skArc(sketch, "E7004", {"start": v(-89.05, 83.4) * mm, "mid": v(-88.5, 83.98) * mm, "end": v(-87.94, 84.56) * mm});
            skLineSegment(sketch, "E7005", {"start": v(-88.2, 81.61) * mm, "end": v(-89.05, 83.4) * mm});
            skLineSegment(sketch, "E7006", {"start": v(-87.08, 79.57) * mm, "end": v(-88.2, 81.61) * mm});
            skArc(sketch, "E7007", {"start": v(-87.08, 79.57) * mm, "mid": v(-87, 79.17) * mm, "end": v(-87.16, 78.8) * mm});
            skArc(sketch, "E7008", {"start": v(-87.48, 78.45) * mm, "mid": v(-87.32, 78.62) * mm, "end": v(-87.16, 78.8) * mm});
            skArc(sketch, "E7009", {"start": v(-87.48, 78.45) * mm, "mid": v(-87.83, 78.24) * mm, "end": v(-88.24, 78.29) * mm});
            skLineSegment(sketch, "E7010", {"start": v(-90.38, 79.19) * mm, "end": v(-92.24, 79.85) * mm});
            skLineSegment(sketch, "E7011", {"start": v(-88.24, 78.29) * mm, "end": v(-90.38, 79.19) * mm});
            skArc(sketch, "E7012", {"start": v(-93.3, 78.62) * mm, "mid": v(-92.77, 79.23) * mm, "end": v(-92.24, 79.85) * mm});
            skLineSegment(sketch, "E7013", {"start": v(-92.35, 76.88) * mm, "end": v(-93.3, 78.62) * mm});
            skLineSegment(sketch, "E7014", {"start": v(-91.13, 74.9) * mm, "end": v(-92.35, 76.88) * mm});
            skArc(sketch, "E7015", {"start": v(-91.13, 74.9) * mm, "mid": v(-91.02, 74.51) * mm, "end": v(-91.16, 74.13) * mm});
            skArc(sketch, "E7016", {"start": v(-91.46, 73.76) * mm, "mid": v(-91.31, 73.95) * mm, "end": v(-91.16, 74.13) * mm});
            skArc(sketch, "E7017", {"start": v(-91.46, 73.76) * mm, "mid": v(-91.8, 73.54) * mm, "end": v(-92.21, 73.56) * mm});
            skLineSegment(sketch, "E7018", {"start": v(-94.4, 74.35) * mm, "end": v(-96.3, 74.9) * mm});
            skLineSegment(sketch, "E7019", {"start": v(-92.21, 73.56) * mm, "end": v(-94.4, 74.35) * mm});
            skArc(sketch, "E7020", {"start": v(-97.28, 73.62) * mm, "mid": v(-96.79, 74.27) * mm, "end": v(-96.3, 74.9) * mm});
            skLineSegment(sketch, "E7021", {"start": v(-96.25, 71.95) * mm, "end": v(-97.28, 73.62) * mm});
            skLineSegment(sketch, "E7022", {"start": v(-94.92, 70.03) * mm, "end": v(-96.25, 71.95) * mm});
            skArc(sketch, "E7023", {"start": v(-94.92, 70.03) * mm, "mid": v(-94.8, 69.65) * mm, "end": v(-94.92, 69.26) * mm});
            skArc(sketch, "E7024", {"start": v(-95.2, 68.87) * mm, "mid": v(-95.06, 69.06) * mm, "end": v(-94.92, 69.26) * mm});
            skArc(sketch, "E7025", {"start": v(-95.2, 68.87) * mm, "mid": v(-95.53, 68.63) * mm, "end": v(-95.94, 68.63) * mm});
            skLineSegment(sketch, "E7026", {"start": v(-98.17, 69.3) * mm, "end": v(-100.08, 69.77) * mm});
            skLineSegment(sketch, "E7027", {"start": v(-95.94, 68.63) * mm, "end": v(-98.17, 69.3) * mm});
            skArc(sketch, "E7028", {"start": v(-101, 68.43) * mm, "mid": v(-100.54, 69.1) * mm, "end": v(-100.08, 69.77) * mm});
            skLineSegment(sketch, "E7029", {"start": v(-99.88, 66.8) * mm, "end": v(-101, 68.43) * mm});
            skLineSegment(sketch, "E7030", {"start": v(-98.46, 64.97) * mm, "end": v(-99.88, 66.8) * mm});
            skArc(sketch, "E7031", {"start": v(-98.46, 64.97) * mm, "mid": v(-98.3, 64.59) * mm, "end": v(-98.41, 64.2) * mm});
            skArc(sketch, "E7032", {"start": v(-98.67, 63.8) * mm, "mid": v(-98.54, 64) * mm, "end": v(-98.41, 64.2) * mm});
            skArc(sketch, "E7033", {"start": v(-98.67, 63.8) * mm, "mid": v(-99, 63.54) * mm, "end": v(-99.4, 63.52) * mm});
            skLineSegment(sketch, "E7034", {"start": v(-101.66, 64.07) * mm, "end": v(-103.6, 64.43) * mm});
            skLineSegment(sketch, "E7035", {"start": v(-99.4, 63.52) * mm, "end": v(-101.66, 64.07) * mm});
            skArc(sketch, "E7036", {"start": v(-104.44, 63.05) * mm, "mid": v(-104.02, 63.74) * mm, "end": v(-103.6, 64.43) * mm});
            skLineSegment(sketch, "E7037", {"start": v(-103.24, 61.5) * mm, "end": v(-104.44, 63.05) * mm});
            skLineSegment(sketch, "E7038", {"start": v(-101.72, 59.73) * mm, "end": v(-103.24, 61.5) * mm});
            skArc(sketch, "E7039", {"start": v(-101.72, 59.73) * mm, "mid": v(-101.55, 59.36) * mm, "end": v(-101.64, 58.96) * mm});
            skArc(sketch, "E7040", {"start": v(-101.88, 58.54) * mm, "mid": v(-101.76, 58.75) * mm, "end": v(-101.64, 58.96) * mm});
            skArc(sketch, "E7041", {"start": v(-101.88, 58.54) * mm, "mid": v(-102.18, 58.27) * mm, "end": v(-102.59, 58.23) * mm});
            skArc(sketch, "E7042", {"start": v(1.55, -2.68) * mm, "mid": v(0.8, -3) * mm, "end": v(0, -3.1) * mm});
            skLineSegment(sketch, "E7043", {"start": v(1.45, -2.51) * mm, "end": v(1.55, -2.68) * mm});
            skArc(sketch, "E7044", {"start": v(2.51, -1.45) * mm, "mid": v(2.05, -2.05) * mm, "end": v(1.45, -2.51) * mm});
            skLineSegment(sketch, "E7045", {"start": v(2.51, -1.45) * mm, "end": v(2.68, -1.55) * mm});
            skArc(sketch, "E7046", {"start": v(3.1, 0) * mm, "mid": v(3, -0.8) * mm, "end": v(2.68, -1.55) * mm});
            skLineSegment(sketch, "E7047", {"start": v(2.9, 0) * mm, "end": v(3.1, 0) * mm});
            skArc(sketch, "E7048", {"start": v(2.51, 1.45) * mm, "mid": v(2.8, 0.75) * mm, "end": v(2.9, 0) * mm});
            skLineSegment(sketch, "E7049", {"start": v(2.51, 1.45) * mm, "end": v(2.68, 1.55) * mm});
            skArc(sketch, "E7050", {"start": v(1.55, 2.68) * mm, "mid": v(2.2, 2.2) * mm, "end": v(2.68, 1.55) * mm});
            skLineSegment(sketch, "E7051", {"start": v(1.45, 2.51) * mm, "end": v(1.55, 2.68) * mm});
            skArc(sketch, "E7052", {"start": v(0, 2.9) * mm, "mid": v(0.75, 2.8) * mm, "end": v(1.45, 2.51) * mm});
            skLineSegment(sketch, "E7053", {"start": v(0, 2.9) * mm, "end": v(0, 3.1) * mm});
            skArc(sketch, "E7054", {"start": v(-1.55, 2.68) * mm, "mid": v(-0.8, 3) * mm, "end": v(0, 3.1) * mm});
            skLineSegment(sketch, "E7055", {"start": v(-1.45, 2.51) * mm, "end": v(-1.55, 2.68) * mm});
            skArc(sketch, "E7056", {"start": v(-2.51, 1.45) * mm, "mid": v(-2.05, 2.05) * mm, "end": v(-1.45, 2.51) * mm});
            skLineSegment(sketch, "E7057", {"start": v(-2.51, 1.45) * mm, "end": v(-2.68, 1.55) * mm});
            skArc(sketch, "E7058", {"start": v(-3.1, 0) * mm, "mid": v(-3, 0.8) * mm, "end": v(-2.68, 1.55) * mm});
            skLineSegment(sketch, "E7059", {"start": v(-2.9, 0) * mm, "end": v(-3.1, 0) * mm});
            skArc(sketch, "E7060", {"start": v(-2.51, -1.45) * mm, "mid": v(-2.8, -0.75) * mm, "end": v(-2.9, 0) * mm});
            skLineSegment(sketch, "E7061", {"start": v(-2.51, -1.45) * mm, "end": v(-2.68, -1.55) * mm});
            skArc(sketch, "E7062", {"start": v(-1.55, -2.68) * mm, "mid": v(-2.2, -2.2) * mm, "end": v(-2.68, -1.55) * mm});
            skArc(sketch, "E7063", {"start": v(13.19, 117.22) * mm, "mid": v(12.92, 116.92) * mm, "end": v(12.52, 116.83) * mm});
            skLineSegment(sketch, "E7064", {"start": v(13.19, 117.22) * mm, "end": v(14.18, 119.33) * mm});
            skLineSegment(sketch, "E7065", {"start": v(14.18, 119.33) * mm, "end": v(15.12, 121.06) * mm});
            skArc(sketch, "E7066", {"start": v(15.12, 121.06) * mm, "mid": v(15.92, 120.96) * mm, "end": v(16.73, 120.85) * mm});
            skLineSegment(sketch, "E7067", {"start": v(17.6, 116.64) * mm, "end": v(17.18, 118.93) * mm});
            skLineSegment(sketch, "E7068", {"start": v(17.18, 118.93) * mm, "end": v(16.73, 120.85) * mm});
            skArc(sketch, "E7069", {"start": v(18.15, 116.1) * mm, "mid": v(17.78, 116.28) * mm, "end": v(17.6, 116.64) * mm});
            skArc(sketch, "E7070", {"start": v(18.15, 116.1) * mm, "mid": v(18.38, 116.05) * mm, "end": v(18.62, 116.02) * mm});
            skArc(sketch, "E7071", {"start": v(19.3, 116.37) * mm, "mid": v(19.02, 116.08) * mm, "end": v(18.62, 116.02) * mm});
            skLineSegment(sketch, "E7072", {"start": v(19.3, 116.37) * mm, "end": v(20.4, 118.42) * mm});
            skLineSegment(sketch, "E7073", {"start": v(20.4, 118.42) * mm, "end": v(21.44, 120.1) * mm});
            skArc(sketch, "E7074", {"start": v(21.44, 120.1) * mm, "mid": v(22.23, 119.96) * mm, "end": v(23.03, 119.8) * mm});
            skLineSegment(sketch, "E7075", {"start": v(23.68, 115.56) * mm, "end": v(23.38, 117.87) * mm});
            skLineSegment(sketch, "E7076", {"start": v(23.38, 117.87) * mm, "end": v(23.03, 119.8) * mm});
            skArc(sketch, "E7077", {"start": v(24.2, 114.98) * mm, "mid": v(23.84, 115.19) * mm, "end": v(23.68, 115.56) * mm});
            skArc(sketch, "E7078", {"start": v(24.2, 114.98) * mm, "mid": v(24.43, 114.93) * mm, "end": v(24.66, 114.88) * mm});
            skArc(sketch, "E7079", {"start": v(25.37, 115.2) * mm, "mid": v(25.07, 114.93) * mm, "end": v(24.66, 114.88) * mm});
            skLineSegment(sketch, "E7080", {"start": v(25.37, 115.2) * mm, "end": v(26.58, 117.19) * mm});
            skLineSegment(sketch, "E7081", {"start": v(26.58, 117.19) * mm, "end": v(27.7, 118.82) * mm});
            skArc(sketch, "E7082", {"start": v(27.7, 118.82) * mm, "mid": v(28.48, 118.63) * mm, "end": v(29.27, 118.44) * mm});
            skLineSegment(sketch, "E7083", {"start": v(29.7, 114.16) * mm, "end": v(29.52, 116.48) * mm});
            skLineSegment(sketch, "E7084", {"start": v(29.52, 116.48) * mm, "end": v(29.27, 118.44) * mm});
            skArc(sketch, "E7085", {"start": v(30.18, 113.56) * mm, "mid": v(29.84, 113.78) * mm, "end": v(29.7, 114.16) * mm});
            skArc(sketch, "E7086", {"start": v(30.18, 113.56) * mm, "mid": v(30.41, 113.5) * mm, "end": v(30.64, 113.43) * mm});
            skArc(sketch, "E7087", {"start": v(31.36, 113.71) * mm, "mid": v(31.05, 113.46) * mm, "end": v(30.64, 113.43) * mm});
            skLineSegment(sketch, "E7088", {"start": v(31.36, 113.71) * mm, "end": v(32.68, 115.64) * mm});
            skLineSegment(sketch, "E7089", {"start": v(32.68, 115.64) * mm, "end": v(33.87, 117.2) * mm});
            skArc(sketch, "E7090", {"start": v(33.87, 117.2) * mm, "mid": v(34.65, 116.98) * mm, "end": v(35.43, 116.74) * mm});
            skLineSegment(sketch, "E7091", {"start": v(35.63, 112.45) * mm, "end": v(35.58, 114.78) * mm});
            skLineSegment(sketch, "E7092", {"start": v(35.58, 114.78) * mm, "end": v(35.43, 116.74) * mm});
            skArc(sketch, "E7093", {"start": v(36.08, 111.82) * mm, "mid": v(35.75, 112.06) * mm, "end": v(35.63, 112.45) * mm});
            skArc(sketch, "E7094", {"start": v(36.08, 111.82) * mm, "mid": v(36.3, 111.75) * mm, "end": v(36.54, 111.68) * mm});
            skArc(sketch, "E7095", {"start": v(37.27, 111.92) * mm, "mid": v(36.94, 111.68) * mm, "end": v(36.54, 111.68) * mm});
            skLineSegment(sketch, "E7096", {"start": v(37.27, 111.92) * mm, "end": v(38.68, 113.77) * mm});
            skLineSegment(sketch, "E7097", {"start": v(38.68, 113.77) * mm, "end": v(39.96, 115.27) * mm});
            skArc(sketch, "E7098", {"start": v(39.96, 115.27) * mm, "mid": v(40.72, 115) * mm, "end": v(41.49, 114.73) * mm});
            skLineSegment(sketch, "E7099", {"start": v(41.47, 110.43) * mm, "end": v(41.54, 112.76) * mm});
            skLineSegment(sketch, "E7100", {"start": v(41.54, 112.76) * mm, "end": v(41.49, 114.73) * mm});
            skArc(sketch, "E7101", {"start": v(41.89, 109.78) * mm, "mid": v(41.57, 110.04) * mm, "end": v(41.47, 110.43) * mm});
            skArc(sketch, "E7102", {"start": v(41.89, 109.78) * mm, "mid": v(42.1, 109.7) * mm, "end": v(42.33, 109.61) * mm});
            skArc(sketch, "E7103", {"start": v(43.08, 109.81) * mm, "mid": v(42.74, 109.59) * mm, "end": v(42.33, 109.61) * mm});
            skLineSegment(sketch, "E7104", {"start": v(43.08, 109.81) * mm, "end": v(44.58, 111.59) * mm});
            skLineSegment(sketch, "E7105", {"start": v(44.58, 111.59) * mm, "end": v(45.94, 113.02) * mm});
            skArc(sketch, "E7106", {"start": v(45.94, 113.02) * mm, "mid": v(46.69, 112.71) * mm, "end": v(47.43, 112.4) * mm});
            skLineSegment(sketch, "E7107", {"start": v(47.19, 108.11) * mm, "end": v(47.38, 110.43) * mm});
            skLineSegment(sketch, "E7108", {"start": v(47.38, 110.43) * mm, "end": v(47.43, 112.4) * mm});
            skArc(sketch, "E7109", {"start": v(47.57, 107.44) * mm, "mid": v(47.27, 107.71) * mm, "end": v(47.19, 108.11) * mm});
            skArc(sketch, "E7110", {"start": v(47.57, 107.44) * mm, "mid": v(47.8, 107.34) * mm, "end": v(48, 107.24) * mm});
            skArc(sketch, "E7111", {"start": v(48.77, 107.4) * mm, "mid": v(48.42, 107.2) * mm, "end": v(48, 107.24) * mm});
            skLineSegment(sketch, "E7112", {"start": v(48.77, 107.4) * mm, "end": v(50.36, 109.1) * mm});
            skLineSegment(sketch, "E7113", {"start": v(50.36, 109.1) * mm, "end": v(51.8, 110.46) * mm});
            skArc(sketch, "E7114", {"start": v(51.8, 110.46) * mm, "mid": v(52.52, 110.12) * mm, "end": v(53.25, 109.76) * mm});
            skLineSegment(sketch, "E7115", {"start": v(52.78, 105.5) * mm, "end": v(53.1, 107.8) * mm});
            skLineSegment(sketch, "E7116", {"start": v(53.1, 107.8) * mm, "end": v(53.25, 109.76) * mm});
            skArc(sketch, "E7117", {"start": v(53.13, 104.8) * mm, "mid": v(52.84, 105.1) * mm, "end": v(52.78, 105.5) * mm});
            skArc(sketch, "E7118", {"start": v(53.13, 104.8) * mm, "mid": v(53.34, 104.7) * mm, "end": v(53.56, 104.58) * mm});
            skArc(sketch, "E7119", {"start": v(54.32, 104.7) * mm, "mid": v(53.96, 104.52) * mm, "end": v(53.56, 104.58) * mm});
            skLineSegment(sketch, "E7120", {"start": v(54.32, 104.7) * mm, "end": v(56, 106.32) * mm});
            skLineSegment(sketch, "E7121", {"start": v(56, 106.32) * mm, "end": v(57.5, 107.6) * mm});
            skArc(sketch, "E7122", {"start": v(57.5, 107.6) * mm, "mid": v(58.21, 107.22) * mm, "end": v(58.92, 106.83) * mm});
            skLineSegment(sketch, "E7123", {"start": v(58.23, 102.59) * mm, "end": v(58.66, 104.87) * mm});
            skLineSegment(sketch, "E7124", {"start": v(58.66, 104.87) * mm, "end": v(58.92, 106.83) * mm});
            skArc(sketch, "E7125", {"start": v(58.54, 101.88) * mm, "mid": v(58.27, 102.18) * mm, "end": v(58.23, 102.59) * mm});
            skArc(sketch, "E7126", {"start": v(58.54, 101.88) * mm, "mid": v(58.75, 101.76) * mm, "end": v(58.96, 101.64) * mm});
            skArc(sketch, "E7127", {"start": v(59.73, 101.72) * mm, "mid": v(59.36, 101.55) * mm, "end": v(58.96, 101.64) * mm});
            skLineSegment(sketch, "E7128", {"start": v(59.73, 101.72) * mm, "end": v(61.5, 103.24) * mm});
            skLineSegment(sketch, "E7129", {"start": v(61.5, 103.24) * mm, "end": v(63.05, 104.44) * mm});
            skArc(sketch, "E7130", {"start": v(63.05, 104.44) * mm, "mid": v(63.74, 104.02) * mm, "end": v(64.43, 103.6) * mm});
            skLineSegment(sketch, "E7131", {"start": v(63.52, 99.4) * mm, "end": v(64.07, 101.66) * mm});
            skLineSegment(sketch, "E7132", {"start": v(64.07, 101.66) * mm, "end": v(64.43, 103.6) * mm});
            skArc(sketch, "E7133", {"start": v(63.8, 98.67) * mm, "mid": v(63.54, 99) * mm, "end": v(63.52, 99.4) * mm});
            skArc(sketch, "E7134", {"start": v(63.8, 98.67) * mm, "mid": v(64, 98.54) * mm, "end": v(64.2, 98.41) * mm});
            skArc(sketch, "E7135", {"start": v(64.97, 98.46) * mm, "mid": v(64.59, 98.3) * mm, "end": v(64.2, 98.41) * mm});
            skLineSegment(sketch, "E7136", {"start": v(64.97, 98.46) * mm, "end": v(66.8, 99.88) * mm});
            skLineSegment(sketch, "E7137", {"start": v(66.8, 99.88) * mm, "end": v(68.43, 101) * mm});
            skArc(sketch, "E7138", {"start": v(68.43, 101) * mm, "mid": v(69.1, 100.54) * mm, "end": v(69.77, 100.08) * mm});
            skLineSegment(sketch, "E7139", {"start": v(68.63, 95.94) * mm, "end": v(69.3, 98.17) * mm});
            skLineSegment(sketch, "E7140", {"start": v(69.3, 98.17) * mm, "end": v(69.77, 100.08) * mm});
            skArc(sketch, "E7141", {"start": v(68.87, 95.2) * mm, "mid": v(68.63, 95.53) * mm, "end": v(68.63, 95.94) * mm});
            skArc(sketch, "E7142", {"start": v(68.87, 95.2) * mm, "mid": v(69.06, 95.06) * mm, "end": v(69.26, 94.92) * mm});
            skArc(sketch, "E7143", {"start": v(70.03, 94.92) * mm, "mid": v(69.65, 94.8) * mm, "end": v(69.26, 94.92) * mm});
            skLineSegment(sketch, "E7144", {"start": v(70.03, 94.92) * mm, "end": v(71.95, 96.25) * mm});
            skLineSegment(sketch, "E7145", {"start": v(71.95, 96.25) * mm, "end": v(73.62, 97.28) * mm});
            skArc(sketch, "E7146", {"start": v(73.62, 97.28) * mm, "mid": v(74.27, 96.79) * mm, "end": v(74.9, 96.3) * mm});
            skLineSegment(sketch, "E7147", {"start": v(73.56, 92.21) * mm, "end": v(74.35, 94.4) * mm});
            skLineSegment(sketch, "E7148", {"start": v(74.35, 94.4) * mm, "end": v(74.9, 96.3) * mm});
            skArc(sketch, "E7149", {"start": v(73.76, 91.46) * mm, "mid": v(73.54, 91.8) * mm, "end": v(73.56, 92.21) * mm});
            skArc(sketch, "E7150", {"start": v(73.76, 91.46) * mm, "mid": v(73.95, 91.31) * mm, "end": v(74.13, 91.16) * mm});
            skArc(sketch, "E7151", {"start": v(74.9, 91.13) * mm, "mid": v(74.51, 91.02) * mm, "end": v(74.13, 91.16) * mm});
            skLineSegment(sketch, "E7152", {"start": v(74.9, 91.13) * mm, "end": v(76.88, 92.35) * mm});
            skLineSegment(sketch, "E7153", {"start": v(76.88, 92.35) * mm, "end": v(78.62, 93.3) * mm});
            skArc(sketch, "E7154", {"start": v(78.62, 93.3) * mm, "mid": v(79.23, 92.77) * mm, "end": v(79.85, 92.24) * mm});
            skLineSegment(sketch, "E7155", {"start": v(78.29, 88.24) * mm, "end": v(79.19, 90.38) * mm});
            skLineSegment(sketch, "E7156", {"start": v(79.19, 90.38) * mm, "end": v(79.85, 92.24) * mm});
            skArc(sketch, "E7157", {"start": v(78.45, 87.48) * mm, "mid": v(78.24, 87.83) * mm, "end": v(78.29, 88.24) * mm});
            skArc(sketch, "E7158", {"start": v(78.45, 87.48) * mm, "mid": v(78.62, 87.32) * mm, "end": v(78.8, 87.16) * mm});
            skArc(sketch, "E7159", {"start": v(79.57, 87.08) * mm, "mid": v(79.17, 87) * mm, "end": v(78.8, 87.16) * mm});
            skLineSegment(sketch, "E7160", {"start": v(79.57, 87.08) * mm, "end": v(81.61, 88.2) * mm});
            skLineSegment(sketch, "E7161", {"start": v(81.61, 88.2) * mm, "end": v(83.4, 89.05) * mm});
            skArc(sketch, "E7162", {"start": v(83.4, 89.05) * mm, "mid": v(83.98, 88.5) * mm, "end": v(84.56, 87.94) * mm});
            skLineSegment(sketch, "E7163", {"start": v(82.8, 84.02) * mm, "end": v(83.8, 86.12) * mm});
            skLineSegment(sketch, "E7164", {"start": v(83.8, 86.12) * mm, "end": v(84.56, 87.94) * mm});
            skArc(sketch, "E7165", {"start": v(82.92, 83.25) * mm, "mid": v(82.73, 83.62) * mm, "end": v(82.8, 84.02) * mm});
            skArc(sketch, "E7166", {"start": v(82.92, 83.25) * mm, "mid": v(83.09, 83.09) * mm, "end": v(83.25, 82.92) * mm});
            skArc(sketch, "E7167", {"start": v(84.02, 82.8) * mm, "mid": v(83.62, 82.73) * mm, "end": v(83.25, 82.92) * mm});
            skLineSegment(sketch, "E7168", {"start": v(84.02, 82.8) * mm, "end": v(86.12, 83.8) * mm});
            skLineSegment(sketch, "E7169", {"start": v(86.12, 83.8) * mm, "end": v(87.94, 84.56) * mm});
            skArc(sketch, "E7170", {"start": v(87.94, 84.56) * mm, "mid": v(88.5, 83.98) * mm, "end": v(89.05, 83.4) * mm});
            skLineSegment(sketch, "E7171", {"start": v(87.08, 79.57) * mm, "end": v(88.2, 81.61) * mm});
            skLineSegment(sketch, "E7172", {"start": v(88.2, 81.61) * mm, "end": v(89.05, 83.4) * mm});
            skArc(sketch, "E7173", {"start": v(87.16, 78.8) * mm, "mid": v(87, 79.17) * mm, "end": v(87.08, 79.57) * mm});
            skArc(sketch, "E7174", {"start": v(87.16, 78.8) * mm, "mid": v(87.32, 78.62) * mm, "end": v(87.48, 78.45) * mm});
            skArc(sketch, "E7175", {"start": v(88.24, 78.29) * mm, "mid": v(87.83, 78.24) * mm, "end": v(87.48, 78.45) * mm});
            skLineSegment(sketch, "E7176", {"start": v(88.24, 78.29) * mm, "end": v(90.38, 79.19) * mm});
            skLineSegment(sketch, "E7177", {"start": v(90.38, 79.19) * mm, "end": v(92.24, 79.85) * mm});
            skArc(sketch, "E7178", {"start": v(92.24, 79.85) * mm, "mid": v(92.77, 79.23) * mm, "end": v(93.3, 78.62) * mm});
            skLineSegment(sketch, "E7179", {"start": v(91.13, 74.9) * mm, "end": v(92.35, 76.88) * mm});
            skLineSegment(sketch, "E7180", {"start": v(92.35, 76.88) * mm, "end": v(93.3, 78.62) * mm});
            skArc(sketch, "E7181", {"start": v(91.16, 74.13) * mm, "mid": v(91.02, 74.51) * mm, "end": v(91.13, 74.9) * mm});
            skArc(sketch, "E7182", {"start": v(91.16, 74.13) * mm, "mid": v(91.31, 73.95) * mm, "end": v(91.46, 73.76) * mm});
            skArc(sketch, "E7183", {"start": v(92.21, 73.56) * mm, "mid": v(91.8, 73.54) * mm, "end": v(91.46, 73.76) * mm});
            skLineSegment(sketch, "E7184", {"start": v(92.21, 73.56) * mm, "end": v(94.4, 74.35) * mm});
            skLineSegment(sketch, "E7185", {"start": v(94.4, 74.35) * mm, "end": v(96.3, 74.9) * mm});
            skArc(sketch, "E7186", {"start": v(96.3, 74.9) * mm, "mid": v(96.79, 74.27) * mm, "end": v(97.28, 73.62) * mm});
            skLineSegment(sketch, "E7187", {"start": v(94.92, 70.03) * mm, "end": v(96.25, 71.95) * mm});
            skLineSegment(sketch, "E7188", {"start": v(96.25, 71.95) * mm, "end": v(97.28, 73.62) * mm});
            skArc(sketch, "E7189", {"start": v(94.92, 69.26) * mm, "mid": v(94.8, 69.65) * mm, "end": v(94.92, 70.03) * mm});
            skArc(sketch, "E7190", {"start": v(94.92, 69.26) * mm, "mid": v(95.06, 69.06) * mm, "end": v(95.2, 68.87) * mm});
            skArc(sketch, "E7191", {"start": v(95.94, 68.63) * mm, "mid": v(95.53, 68.63) * mm, "end": v(95.2, 68.87) * mm});
            skLineSegment(sketch, "E7192", {"start": v(95.94, 68.63) * mm, "end": v(98.17, 69.3) * mm});
            skLineSegment(sketch, "E7193", {"start": v(98.17, 69.3) * mm, "end": v(100.08, 69.77) * mm});
            skArc(sketch, "E7194", {"start": v(100.08, 69.77) * mm, "mid": v(100.54, 69.1) * mm, "end": v(101, 68.43) * mm});
            skLineSegment(sketch, "E7195", {"start": v(98.46, 64.97) * mm, "end": v(99.88, 66.8) * mm});
            skLineSegment(sketch, "E7196", {"start": v(99.88, 66.8) * mm, "end": v(101, 68.43) * mm});
            skArc(sketch, "E7197", {"start": v(98.41, 64.2) * mm, "mid": v(98.3, 64.59) * mm, "end": v(98.46, 64.97) * mm});
            skArc(sketch, "E7198", {"start": v(98.41, 64.2) * mm, "mid": v(98.54, 64) * mm, "end": v(98.67, 63.8) * mm});
            skArc(sketch, "E7199", {"start": v(99.4, 63.52) * mm, "mid": v(99, 63.54) * mm, "end": v(98.67, 63.8) * mm});
            skLineSegment(sketch, "E7200", {"start": v(99.4, 63.52) * mm, "end": v(101.66, 64.07) * mm});
            skLineSegment(sketch, "E7201", {"start": v(101.66, 64.07) * mm, "end": v(103.6, 64.43) * mm});
            skArc(sketch, "E7202", {"start": v(103.6, 64.43) * mm, "mid": v(104.02, 63.74) * mm, "end": v(104.44, 63.05) * mm});
            skLineSegment(sketch, "E7203", {"start": v(101.72, 59.73) * mm, "end": v(103.24, 61.5) * mm});
            skLineSegment(sketch, "E7204", {"start": v(103.24, 61.5) * mm, "end": v(104.44, 63.05) * mm});
            skArc(sketch, "E7205", {"start": v(101.64, 58.96) * mm, "mid": v(101.55, 59.36) * mm, "end": v(101.72, 59.73) * mm});
            skArc(sketch, "E7206", {"start": v(101.64, 58.96) * mm, "mid": v(101.76, 58.75) * mm, "end": v(101.88, 58.54) * mm});
            skArc(sketch, "E7207", {"start": v(102.59, 58.23) * mm, "mid": v(102.18, 58.27) * mm, "end": v(101.88, 58.54) * mm});
            skLineSegment(sketch, "E7208", {"start": v(102.59, 58.23) * mm, "end": v(104.87, 58.66) * mm});
            skLineSegment(sketch, "E7209", {"start": v(104.87, 58.66) * mm, "end": v(106.83, 58.92) * mm});
            skArc(sketch, "E7210", {"start": v(106.83, 58.92) * mm, "mid": v(107.22, 58.21) * mm, "end": v(107.6, 57.5) * mm});
            skLineSegment(sketch, "E7211", {"start": v(104.7, 54.32) * mm, "end": v(106.32, 56) * mm});
            skLineSegment(sketch, "E7212", {"start": v(106.32, 56) * mm, "end": v(107.6, 57.5) * mm});
            skArc(sketch, "E7213", {"start": v(104.58, 53.56) * mm, "mid": v(104.52, 53.96) * mm, "end": v(104.7, 54.32) * mm});
            skArc(sketch, "E7214", {"start": v(104.58, 53.56) * mm, "mid": v(104.7, 53.34) * mm, "end": v(104.8, 53.13) * mm});
            skArc(sketch, "E7215", {"start": v(105.5, 52.78) * mm, "mid": v(105.1, 52.84) * mm, "end": v(104.8, 53.13) * mm});
            skLineSegment(sketch, "E7216", {"start": v(105.5, 52.78) * mm, "end": v(107.8, 53.1) * mm});
            skLineSegment(sketch, "E7217", {"start": v(107.8, 53.1) * mm, "end": v(109.76, 53.25) * mm});
            skArc(sketch, "E7218", {"start": v(109.76, 53.25) * mm, "mid": v(110.12, 52.52) * mm, "end": v(110.46, 51.8) * mm});
            skLineSegment(sketch, "E7219", {"start": v(107.4, 48.77) * mm, "end": v(109.1, 50.36) * mm});
            skLineSegment(sketch, "E7220", {"start": v(109.1, 50.36) * mm, "end": v(110.46, 51.8) * mm});
            skArc(sketch, "E7221", {"start": v(107.24, 48) * mm, "mid": v(107.2, 48.42) * mm, "end": v(107.4, 48.77) * mm});
            skArc(sketch, "E7222", {"start": v(107.24, 48) * mm, "mid": v(107.34, 47.8) * mm, "end": v(107.44, 47.57) * mm});
            skArc(sketch, "E7223", {"start": v(108.11, 47.19) * mm, "mid": v(107.71, 47.27) * mm, "end": v(107.44, 47.57) * mm});
            skLineSegment(sketch, "E7224", {"start": v(108.11, 47.19) * mm, "end": v(110.43, 47.38) * mm});
            skLineSegment(sketch, "E7225", {"start": v(110.43, 47.38) * mm, "end": v(112.4, 47.43) * mm});
            skArc(sketch, "E7226", {"start": v(112.4, 47.43) * mm, "mid": v(112.71, 46.69) * mm, "end": v(113.02, 45.94) * mm});
            skLineSegment(sketch, "E7227", {"start": v(109.81, 43.08) * mm, "end": v(111.59, 44.58) * mm});
            skLineSegment(sketch, "E7228", {"start": v(111.59, 44.58) * mm, "end": v(113.02, 45.94) * mm});
            skArc(sketch, "E7229", {"start": v(109.61, 42.33) * mm, "mid": v(109.59, 42.74) * mm, "end": v(109.81, 43.08) * mm});
            skArc(sketch, "E7230", {"start": v(109.61, 42.33) * mm, "mid": v(109.7, 42.1) * mm, "end": v(109.78, 41.89) * mm});
            skArc(sketch, "E7231", {"start": v(110.43, 41.47) * mm, "mid": v(110.04, 41.57) * mm, "end": v(109.78, 41.89) * mm});
            skLineSegment(sketch, "E7232", {"start": v(110.43, 41.47) * mm, "end": v(112.76, 41.54) * mm});
            skLineSegment(sketch, "E7233", {"start": v(112.76, 41.54) * mm, "end": v(114.73, 41.49) * mm});
            skArc(sketch, "E7234", {"start": v(114.73, 41.49) * mm, "mid": v(115, 40.72) * mm, "end": v(115.27, 39.96) * mm});
            skLineSegment(sketch, "E7235", {"start": v(111.92, 37.27) * mm, "end": v(113.77, 38.68) * mm});
            skLineSegment(sketch, "E7236", {"start": v(113.77, 38.68) * mm, "end": v(115.27, 39.96) * mm});
            skArc(sketch, "E7237", {"start": v(111.68, 36.54) * mm, "mid": v(111.68, 36.94) * mm, "end": v(111.92, 37.27) * mm});
            skArc(sketch, "E7238", {"start": v(111.68, 36.54) * mm, "mid": v(111.75, 36.3) * mm, "end": v(111.82, 36.08) * mm});
            skArc(sketch, "E7239", {"start": v(112.45, 35.63) * mm, "mid": v(112.06, 35.75) * mm, "end": v(111.82, 36.08) * mm});
            skLineSegment(sketch, "E7240", {"start": v(112.45, 35.63) * mm, "end": v(114.78, 35.58) * mm});
            skLineSegment(sketch, "E7241", {"start": v(114.78, 35.58) * mm, "end": v(116.74, 35.43) * mm});
            skArc(sketch, "E7242", {"start": v(116.74, 35.43) * mm, "mid": v(116.98, 34.65) * mm, "end": v(117.2, 33.87) * mm});
            skLineSegment(sketch, "E7243", {"start": v(113.71, 31.36) * mm, "end": v(115.64, 32.68) * mm});
            skLineSegment(sketch, "E7244", {"start": v(115.64, 32.68) * mm, "end": v(117.2, 33.87) * mm});
            skArc(sketch, "E7245", {"start": v(113.43, 30.64) * mm, "mid": v(113.46, 31.05) * mm, "end": v(113.71, 31.36) * mm});
            skArc(sketch, "E7246", {"start": v(113.43, 30.64) * mm, "mid": v(113.5, 30.41) * mm, "end": v(113.56, 30.18) * mm});
            skArc(sketch, "E7247", {"start": v(114.16, 29.7) * mm, "mid": v(113.78, 29.84) * mm, "end": v(113.56, 30.18) * mm});
            skLineSegment(sketch, "E7248", {"start": v(114.16, 29.7) * mm, "end": v(116.48, 29.52) * mm});
            skLineSegment(sketch, "E7249", {"start": v(116.48, 29.52) * mm, "end": v(118.44, 29.27) * mm});
            skArc(sketch, "E7250", {"start": v(118.44, 29.27) * mm, "mid": v(118.63, 28.48) * mm, "end": v(118.82, 27.7) * mm});
            skLineSegment(sketch, "E7251", {"start": v(115.2, 25.37) * mm, "end": v(117.19, 26.58) * mm});
            skArc(sketch, "E7252", {"start": v(110.46, -51.8) * mm, "mid": v(110.12, -52.52) * mm, "end": v(109.76, -53.25) * mm});
            skLineSegment(sketch, "E7253", {"start": v(105.5, -52.78) * mm, "end": v(107.8, -53.1) * mm});
            skLineSegment(sketch, "E7254", {"start": v(107.8, -53.1) * mm, "end": v(109.76, -53.25) * mm});
            skArc(sketch, "E7255", {"start": v(104.8, -53.13) * mm, "mid": v(105.1, -52.84) * mm, "end": v(105.5, -52.78) * mm});
            skArc(sketch, "E7256", {"start": v(104.8, -53.13) * mm, "mid": v(104.7, -53.34) * mm, "end": v(104.58, -53.56) * mm});
            skArc(sketch, "E7257", {"start": v(104.7, -54.32) * mm, "mid": v(104.52, -53.96) * mm, "end": v(104.58, -53.56) * mm});
            skLineSegment(sketch, "E7258", {"start": v(104.7, -54.32) * mm, "end": v(106.32, -56) * mm});
            skLineSegment(sketch, "E7259", {"start": v(106.32, -56) * mm, "end": v(107.6, -57.5) * mm});
            skArc(sketch, "E7260", {"start": v(107.6, -57.5) * mm, "mid": v(107.22, -58.21) * mm, "end": v(106.83, -58.92) * mm});
            skLineSegment(sketch, "E7261", {"start": v(102.59, -58.23) * mm, "end": v(104.87, -58.66) * mm});
            skLineSegment(sketch, "E7262", {"start": v(104.87, -58.66) * mm, "end": v(106.83, -58.92) * mm});
            skArc(sketch, "E7263", {"start": v(101.88, -58.54) * mm, "mid": v(102.18, -58.27) * mm, "end": v(102.59, -58.23) * mm});
            skArc(sketch, "E7264", {"start": v(101.88, -58.54) * mm, "mid": v(101.76, -58.75) * mm, "end": v(101.64, -58.96) * mm});
            skArc(sketch, "E7265", {"start": v(101.72, -59.73) * mm, "mid": v(101.55, -59.36) * mm, "end": v(101.64, -58.96) * mm});
            skLineSegment(sketch, "E7266", {"start": v(101.72, -59.73) * mm, "end": v(103.24, -61.5) * mm});
            skLineSegment(sketch, "E7267", {"start": v(103.24, -61.5) * mm, "end": v(104.44, -63.05) * mm});
            skArc(sketch, "E7268", {"start": v(104.44, -63.05) * mm, "mid": v(104.02, -63.74) * mm, "end": v(103.6, -64.43) * mm});
            skLineSegment(sketch, "E7269", {"start": v(99.4, -63.52) * mm, "end": v(101.66, -64.07) * mm});
            skLineSegment(sketch, "E7270", {"start": v(101.66, -64.07) * mm, "end": v(103.6, -64.43) * mm});
            skArc(sketch, "E7271", {"start": v(98.67, -63.8) * mm, "mid": v(99, -63.54) * mm, "end": v(99.4, -63.52) * mm});
            skArc(sketch, "E7272", {"start": v(98.67, -63.8) * mm, "mid": v(98.54, -64) * mm, "end": v(98.41, -64.2) * mm});
            skArc(sketch, "E7273", {"start": v(98.46, -64.97) * mm, "mid": v(98.3, -64.59) * mm, "end": v(98.41, -64.2) * mm});
            skLineSegment(sketch, "E7274", {"start": v(98.46, -64.97) * mm, "end": v(99.88, -66.8) * mm});
            skLineSegment(sketch, "E7275", {"start": v(99.88, -66.8) * mm, "end": v(101, -68.43) * mm});
            skArc(sketch, "E7276", {"start": v(101, -68.43) * mm, "mid": v(100.54, -69.1) * mm, "end": v(100.08, -69.77) * mm});
            skLineSegment(sketch, "E7277", {"start": v(95.94, -68.63) * mm, "end": v(98.17, -69.3) * mm});
            skLineSegment(sketch, "E7278", {"start": v(98.17, -69.3) * mm, "end": v(100.08, -69.77) * mm});
            skArc(sketch, "E7279", {"start": v(95.2, -68.87) * mm, "mid": v(95.53, -68.63) * mm, "end": v(95.94, -68.63) * mm});
            skArc(sketch, "E7280", {"start": v(95.2, -68.87) * mm, "mid": v(95.06, -69.06) * mm, "end": v(94.92, -69.26) * mm});
            skArc(sketch, "E7281", {"start": v(94.92, -70.03) * mm, "mid": v(94.8, -69.65) * mm, "end": v(94.92, -69.26) * mm});
            skLineSegment(sketch, "E7282", {"start": v(94.92, -70.03) * mm, "end": v(96.25, -71.95) * mm});
            skLineSegment(sketch, "E7283", {"start": v(96.25, -71.95) * mm, "end": v(97.28, -73.62) * mm});
            skArc(sketch, "E7284", {"start": v(97.28, -73.62) * mm, "mid": v(96.79, -74.27) * mm, "end": v(96.3, -74.9) * mm});
            skLineSegment(sketch, "E7285", {"start": v(92.21, -73.56) * mm, "end": v(94.4, -74.35) * mm});
            skLineSegment(sketch, "E7286", {"start": v(94.4, -74.35) * mm, "end": v(96.3, -74.9) * mm});
            skArc(sketch, "E7287", {"start": v(91.46, -73.76) * mm, "mid": v(91.8, -73.54) * mm, "end": v(92.21, -73.56) * mm});
            skArc(sketch, "E7288", {"start": v(91.46, -73.76) * mm, "mid": v(91.31, -73.95) * mm, "end": v(91.16, -74.13) * mm});
            skArc(sketch, "E7289", {"start": v(91.13, -74.9) * mm, "mid": v(91.02, -74.51) * mm, "end": v(91.16, -74.13) * mm});
            skLineSegment(sketch, "E7290", {"start": v(91.13, -74.9) * mm, "end": v(92.35, -76.88) * mm});
            skLineSegment(sketch, "E7291", {"start": v(92.35, -76.88) * mm, "end": v(93.3, -78.62) * mm});
            skArc(sketch, "E7292", {"start": v(93.3, -78.62) * mm, "mid": v(92.77, -79.23) * mm, "end": v(92.24, -79.85) * mm});
            skLineSegment(sketch, "E7293", {"start": v(88.24, -78.29) * mm, "end": v(90.38, -79.19) * mm});
            skLineSegment(sketch, "E7294", {"start": v(90.38, -79.19) * mm, "end": v(92.24, -79.85) * mm});
            skArc(sketch, "E7295", {"start": v(87.48, -78.45) * mm, "mid": v(87.83, -78.24) * mm, "end": v(88.24, -78.29) * mm});
            skArc(sketch, "E7296", {"start": v(87.48, -78.45) * mm, "mid": v(87.32, -78.62) * mm, "end": v(87.16, -78.8) * mm});
            skArc(sketch, "E7297", {"start": v(87.08, -79.57) * mm, "mid": v(87, -79.17) * mm, "end": v(87.16, -78.8) * mm});
            skLineSegment(sketch, "E7298", {"start": v(87.08, -79.57) * mm, "end": v(88.2, -81.61) * mm});
            skLineSegment(sketch, "E7299", {"start": v(88.2, -81.61) * mm, "end": v(89.05, -83.4) * mm});
            skArc(sketch, "E7300", {"start": v(89.05, -83.4) * mm, "mid": v(88.5, -83.98) * mm, "end": v(87.94, -84.56) * mm});
            skLineSegment(sketch, "E7301", {"start": v(84.02, -82.8) * mm, "end": v(86.12, -83.8) * mm});
            skLineSegment(sketch, "E7302", {"start": v(71.95, -96.25) * mm, "end": v(73.62, -97.28) * mm});
            skArc(sketch, "E7303", {"start": v(69.26, -94.92) * mm, "mid": v(69.65, -94.8) * mm, "end": v(70.03, -94.92) * mm});
            skArc(sketch, "E7304", {"start": v(69.26, -94.92) * mm, "mid": v(69.06, -95.06) * mm, "end": v(68.87, -95.2) * mm});
            skArc(sketch, "E7305", {"start": v(68.63, -95.94) * mm, "mid": v(68.63, -95.53) * mm, "end": v(68.87, -95.2) * mm});
            skLineSegment(sketch, "E7306", {"start": v(68.63, -95.94) * mm, "end": v(69.3, -98.17) * mm});
            skLineSegment(sketch, "E7307", {"start": v(69.3, -98.17) * mm, "end": v(69.77, -100.08) * mm});
            skArc(sketch, "E7308", {"start": v(69.77, -100.08) * mm, "mid": v(69.1, -100.54) * mm, "end": v(68.43, -101) * mm});
            skLineSegment(sketch, "E7309", {"start": v(64.97, -98.46) * mm, "end": v(66.8, -99.88) * mm});
            skLineSegment(sketch, "E7310", {"start": v(66.8, -99.88) * mm, "end": v(68.43, -101) * mm});
            skArc(sketch, "E7311", {"start": v(64.2, -98.41) * mm, "mid": v(64.59, -98.3) * mm, "end": v(64.97, -98.46) * mm});
            skArc(sketch, "E7312", {"start": v(64.2, -98.41) * mm, "mid": v(64, -98.54) * mm, "end": v(63.8, -98.67) * mm});
            skArc(sketch, "E7313", {"start": v(63.52, -99.4) * mm, "mid": v(63.54, -99) * mm, "end": v(63.8, -98.67) * mm});
            skArc(sketch, "E7314", {"start": v(58.96, -101.64) * mm, "mid": v(58.75, -101.76) * mm, "end": v(58.54, -101.88) * mm});
            skArc(sketch, "E7315", {"start": v(58.23, -102.59) * mm, "mid": v(58.27, -102.18) * mm, "end": v(58.54, -101.88) * mm});
            skLineSegment(sketch, "E7316", {"start": v(58.23, -102.59) * mm, "end": v(58.66, -104.87) * mm});
            skLineSegment(sketch, "E7317", {"start": v(58.66, -104.87) * mm, "end": v(58.92, -106.83) * mm});
            skArc(sketch, "E7318", {"start": v(58.96, -101.64) * mm, "mid": v(59.36, -101.55) * mm, "end": v(59.73, -101.72) * mm});
            skLineSegment(sketch, "E7319", {"start": v(61.5, -103.24) * mm, "end": v(63.05, -104.44) * mm});
            skLineSegment(sketch, "E7320", {"start": v(59.73, -101.72) * mm, "end": v(61.5, -103.24) * mm});
            skArc(sketch, "E7321", {"start": v(64.43, -103.6) * mm, "mid": v(63.74, -104.02) * mm, "end": v(63.05, -104.44) * mm});
            skLineSegment(sketch, "E7322", {"start": v(64.07, -101.66) * mm, "end": v(64.43, -103.6) * mm});
            skLineSegment(sketch, "E7323", {"start": v(63.52, -99.4) * mm, "end": v(64.07, -101.66) * mm});
            skLineSegment(sketch, "E7324", {"start": v(70.03, -94.92) * mm, "end": v(71.95, -96.25) * mm});
            skArc(sketch, "E7325", {"start": v(74.9, -96.3) * mm, "mid": v(74.27, -96.79) * mm, "end": v(73.62, -97.28) * mm});
            skLineSegment(sketch, "E7326", {"start": v(74.35, -94.4) * mm, "end": v(74.9, -96.3) * mm});
            skLineSegment(sketch, "E7327", {"start": v(73.56, -92.21) * mm, "end": v(74.35, -94.4) * mm});
            skArc(sketch, "E7328", {"start": v(73.56, -92.21) * mm, "mid": v(73.54, -91.8) * mm, "end": v(73.76, -91.46) * mm});
            skArc(sketch, "E7329", {"start": v(74.13, -91.16) * mm, "mid": v(73.95, -91.31) * mm, "end": v(73.76, -91.46) * mm});
            skArc(sketch, "E7330", {"start": v(74.13, -91.16) * mm, "mid": v(74.51, -91.02) * mm, "end": v(74.9, -91.13) * mm});
            skLineSegment(sketch, "E7331", {"start": v(76.88, -92.35) * mm, "end": v(78.62, -93.3) * mm});
            skLineSegment(sketch, "E7332", {"start": v(74.9, -91.13) * mm, "end": v(76.88, -92.35) * mm});
            skArc(sketch, "E7333", {"start": v(79.85, -92.24) * mm, "mid": v(79.23, -92.77) * mm, "end": v(78.62, -93.3) * mm});
            skLineSegment(sketch, "E7334", {"start": v(79.19, -90.38) * mm, "end": v(79.85, -92.24) * mm});
            skLineSegment(sketch, "E7335", {"start": v(78.29, -88.24) * mm, "end": v(79.19, -90.38) * mm});
            skArc(sketch, "E7336", {"start": v(78.29, -88.24) * mm, "mid": v(78.24, -87.83) * mm, "end": v(78.45, -87.48) * mm});
            skArc(sketch, "E7337", {"start": v(78.8, -87.16) * mm, "mid": v(78.62, -87.32) * mm, "end": v(78.45, -87.48) * mm});
            skArc(sketch, "E7338", {"start": v(78.8, -87.16) * mm, "mid": v(79.17, -87) * mm, "end": v(79.57, -87.08) * mm});
            skLineSegment(sketch, "E7339", {"start": v(81.61, -88.2) * mm, "end": v(83.4, -89.05) * mm});
            skLineSegment(sketch, "E7340", {"start": v(79.57, -87.08) * mm, "end": v(81.61, -88.2) * mm});
            skArc(sketch, "E7341", {"start": v(84.56, -87.94) * mm, "mid": v(83.98, -88.5) * mm, "end": v(83.4, -89.05) * mm});
            skLineSegment(sketch, "E7342", {"start": v(83.8, -86.12) * mm, "end": v(84.56, -87.94) * mm});
            skLineSegment(sketch, "E7343", {"start": v(82.8, -84.02) * mm, "end": v(83.8, -86.12) * mm});
            skArc(sketch, "E7344", {"start": v(82.8, -84.02) * mm, "mid": v(82.73, -83.62) * mm, "end": v(82.92, -83.25) * mm});
            skArc(sketch, "E7345", {"start": v(83.25, -82.92) * mm, "mid": v(83.09, -83.09) * mm, "end": v(82.92, -83.25) * mm});
            skArc(sketch, "E7346", {"start": v(83.25, -82.92) * mm, "mid": v(83.62, -82.73) * mm, "end": v(84.02, -82.8) * mm});
            skLineSegment(sketch, "E7347", {"start": v(86.12, -83.8) * mm, "end": v(87.94, -84.56) * mm});
            skLineSegment(sketch, "E7348", {"start": v(109.1, -50.36) * mm, "end": v(110.46, -51.8) * mm});
            skLineSegment(sketch, "E7349", {"start": v(107.4, -48.77) * mm, "end": v(109.1, -50.36) * mm});
            skArc(sketch, "E7350", {"start": v(107.4, -48.77) * mm, "mid": v(107.2, -48.42) * mm, "end": v(107.24, -48) * mm});
            skArc(sketch, "E7351", {"start": v(107.44, -47.57) * mm, "mid": v(107.34, -47.8) * mm, "end": v(107.24, -48) * mm});
            skArc(sketch, "E7352", {"start": v(107.44, -47.57) * mm, "mid": v(107.71, -47.27) * mm, "end": v(108.11, -47.19) * mm});
            skLineSegment(sketch, "E7353", {"start": v(110.43, -47.38) * mm, "end": v(112.4, -47.43) * mm});
            skLineSegment(sketch, "E7354", {"start": v(108.11, -47.19) * mm, "end": v(110.43, -47.38) * mm});
            skArc(sketch, "E7355", {"start": v(113.02, -45.94) * mm, "mid": v(112.71, -46.69) * mm, "end": v(112.4, -47.43) * mm});
            skLineSegment(sketch, "E7356", {"start": v(111.59, -44.58) * mm, "end": v(113.02, -45.94) * mm});
            skLineSegment(sketch, "E7357", {"start": v(109.81, -43.08) * mm, "end": v(111.59, -44.58) * mm});
            skArc(sketch, "E7358", {"start": v(109.81, -43.08) * mm, "mid": v(109.59, -42.74) * mm, "end": v(109.61, -42.33) * mm});
            skArc(sketch, "E7359", {"start": v(109.78, -41.89) * mm, "mid": v(109.7, -42.1) * mm, "end": v(109.61, -42.33) * mm});
            skArc(sketch, "E7360", {"start": v(109.78, -41.89) * mm, "mid": v(110.04, -41.57) * mm, "end": v(110.43, -41.47) * mm});
            skLineSegment(sketch, "E7361", {"start": v(112.76, -41.54) * mm, "end": v(114.73, -41.49) * mm});
            skLineSegment(sketch, "E7362", {"start": v(110.43, -41.47) * mm, "end": v(112.76, -41.54) * mm});
            skArc(sketch, "E7363", {"start": v(115.27, -39.96) * mm, "mid": v(115, -40.72) * mm, "end": v(114.73, -41.49) * mm});
            skLineSegment(sketch, "E7364", {"start": v(113.77, -38.68) * mm, "end": v(115.27, -39.96) * mm});
            skLineSegment(sketch, "E7365", {"start": v(111.92, -37.27) * mm, "end": v(113.77, -38.68) * mm});
            skArc(sketch, "E7366", {"start": v(111.92, -37.27) * mm, "mid": v(111.68, -36.94) * mm, "end": v(111.68, -36.54) * mm});
            skArc(sketch, "E7367", {"start": v(111.82, -36.08) * mm, "mid": v(111.75, -36.3) * mm, "end": v(111.68, -36.54) * mm});
            skArc(sketch, "E7368", {"start": v(111.82, -36.08) * mm, "mid": v(112.06, -35.75) * mm, "end": v(112.45, -35.63) * mm});
            skLineSegment(sketch, "E7369", {"start": v(114.78, -35.58) * mm, "end": v(116.74, -35.43) * mm});
            skLineSegment(sketch, "E7370", {"start": v(112.45, -35.63) * mm, "end": v(114.78, -35.58) * mm});
            skArc(sketch, "E7371", {"start": v(117.2, -33.87) * mm, "mid": v(116.98, -34.65) * mm, "end": v(116.74, -35.43) * mm});
            skLineSegment(sketch, "E7372", {"start": v(115.64, -32.68) * mm, "end": v(117.2, -33.87) * mm});
            skLineSegment(sketch, "E7373", {"start": v(113.71, -31.36) * mm, "end": v(115.64, -32.68) * mm});
            skArc(sketch, "E7374", {"start": v(113.71, -31.36) * mm, "mid": v(113.46, -31.05) * mm, "end": v(113.43, -30.64) * mm});
            skArc(sketch, "E7375", {"start": v(113.56, -30.18) * mm, "mid": v(113.5, -30.41) * mm, "end": v(113.43, -30.64) * mm});
            skArc(sketch, "E7376", {"start": v(113.56, -30.18) * mm, "mid": v(113.78, -29.84) * mm, "end": v(114.16, -29.7) * mm});
            skLineSegment(sketch, "E7377", {"start": v(116.48, -29.52) * mm, "end": v(118.44, -29.27) * mm});
            skLineSegment(sketch, "E7378", {"start": v(114.16, -29.7) * mm, "end": v(116.48, -29.52) * mm});
            skArc(sketch, "E7379", {"start": v(118.82, -27.7) * mm, "mid": v(118.63, -28.48) * mm, "end": v(118.44, -29.27) * mm});
            skLineSegment(sketch, "E7380", {"start": v(117.19, -26.58) * mm, "end": v(118.82, -27.7) * mm});
            skLineSegment(sketch, "E7381", {"start": v(115.2, -25.37) * mm, "end": v(117.19, -26.58) * mm});
            skArc(sketch, "E7382", {"start": v(115.2, -25.37) * mm, "mid": v(114.93, -25.07) * mm, "end": v(114.88, -24.66) * mm});
            skArc(sketch, "E7383", {"start": v(114.98, -24.2) * mm, "mid": v(114.93, -24.43) * mm, "end": v(114.88, -24.66) * mm});
            skArc(sketch, "E7384", {"start": v(114.98, -24.2) * mm, "mid": v(115.19, -23.84) * mm, "end": v(115.56, -23.68) * mm});
            skLineSegment(sketch, "E7385", {"start": v(117.87, -23.38) * mm, "end": v(119.8, -23.03) * mm});
            skLineSegment(sketch, "E7386", {"start": v(115.56, -23.68) * mm, "end": v(117.87, -23.38) * mm});
            skArc(sketch, "E7387", {"start": v(120.1, -21.44) * mm, "mid": v(119.96, -22.23) * mm, "end": v(119.8, -23.03) * mm});
            skLineSegment(sketch, "E7388", {"start": v(118.42, -20.4) * mm, "end": v(120.1, -21.44) * mm});
            skLineSegment(sketch, "E7389", {"start": v(116.37, -19.3) * mm, "end": v(118.42, -20.4) * mm});
            skArc(sketch, "E7390", {"start": v(116.37, -19.3) * mm, "mid": v(116.08, -19.02) * mm, "end": v(116.02, -18.62) * mm});
            skArc(sketch, "E7391", {"start": v(116.1, -18.15) * mm, "mid": v(116.05, -18.38) * mm, "end": v(116.02, -18.62) * mm});
            skArc(sketch, "E7392", {"start": v(116.1, -18.15) * mm, "mid": v(116.28, -17.78) * mm, "end": v(116.64, -17.6) * mm});
            skLineSegment(sketch, "E7393", {"start": v(118.93, -17.18) * mm, "end": v(120.85, -16.73) * mm});
            skLineSegment(sketch, "E7394", {"start": v(116.64, -17.6) * mm, "end": v(118.93, -17.18) * mm});
            skArc(sketch, "E7395", {"start": v(121.06, -15.12) * mm, "mid": v(120.96, -15.92) * mm, "end": v(120.85, -16.73) * mm});
            skLineSegment(sketch, "E7396", {"start": v(119.33, -14.18) * mm, "end": v(121.06, -15.12) * mm});
            skLineSegment(sketch, "E7397", {"start": v(117.22, -13.19) * mm, "end": v(119.33, -14.18) * mm});
            skArc(sketch, "E7398", {"start": v(117.22, -13.19) * mm, "mid": v(116.92, -12.92) * mm, "end": v(116.83, -12.52) * mm});
            skArc(sketch, "E7399", {"start": v(116.88, -12.05) * mm, "mid": v(116.86, -12.28) * mm, "end": v(116.83, -12.52) * mm});
            skArc(sketch, "E7400", {"start": v(116.88, -12.05) * mm, "mid": v(117.05, -11.67) * mm, "end": v(117.4, -11.47) * mm});
            skLineSegment(sketch, "E7401", {"start": v(119.67, -10.94) * mm, "end": v(121.56, -10.38) * mm});
            skLineSegment(sketch, "E7402", {"start": v(117.4, -11.47) * mm, "end": v(119.67, -10.94) * mm});
            skArc(sketch, "E7403", {"start": v(121.68, -8.76) * mm, "mid": v(121.62, -9.57) * mm, "end": v(121.56, -10.38) * mm});
            skLineSegment(sketch, "E7404", {"start": v(119.9, -7.92) * mm, "end": v(121.68, -8.76) * mm});
            skLineSegment(sketch, "E7405", {"start": v(117.75, -7.04) * mm, "end": v(119.9, -7.92) * mm});
            skArc(sketch, "E7406", {"start": v(117.75, -7.04) * mm, "mid": v(117.43, -6.78) * mm, "end": v(117.33, -6.39) * mm});
            skArc(sketch, "E7407", {"start": v(117.35, -5.91) * mm, "mid": v(117.34, -6.15) * mm, "end": v(117.33, -6.39) * mm});
            skArc(sketch, "E7408", {"start": v(117.35, -5.91) * mm, "mid": v(117.5, -5.53) * mm, "end": v(117.84, -5.3) * mm});
            skLineSegment(sketch, "E7409", {"start": v(120.08, -4.66) * mm, "end": v(121.93, -4) * mm});
            skLineSegment(sketch, "E7410", {"start": v(117.84, -5.3) * mm, "end": v(120.08, -4.66) * mm});
            skArc(sketch, "E7411", {"start": v(121.98, -2.38) * mm, "mid": v(121.96, -3.2) * mm, "end": v(121.93, -4) * mm});
            skLineSegment(sketch, "E7412", {"start": v(120.15, -1.63) * mm, "end": v(121.98, -2.38) * mm});
            skLineSegment(sketch, "E7413", {"start": v(117.96, -0.86) * mm, "end": v(120.15, -1.63) * mm});
            skArc(sketch, "E7414", {"start": v(117.96, -0.86) * mm, "mid": v(117.63, -0.63) * mm, "end": v(117.5, -0.24) * mm});
            skArc(sketch, "E7415", {"start": v(117.5, 0.24) * mm, "mid": v(117.5, 0) * mm, "end": v(117.5, -0.24) * mm});
            skArc(sketch, "E7416", {"start": v(117.5, 0.24) * mm, "mid": v(117.63, 0.63) * mm, "end": v(117.96, 0.86) * mm});
            skLineSegment(sketch, "E7417", {"start": v(120.15, 1.63) * mm, "end": v(121.98, 2.38) * mm});
            skLineSegment(sketch, "E7418", {"start": v(117.96, 0.86) * mm, "end": v(120.15, 1.63) * mm});
            skArc(sketch, "E7419", {"start": v(121.93, 4) * mm, "mid": v(121.96, 3.2) * mm, "end": v(121.98, 2.38) * mm});
            skLineSegment(sketch, "E7420", {"start": v(120.08, 4.66) * mm, "end": v(121.93, 4) * mm});
            skLineSegment(sketch, "E7421", {"start": v(117.84, 5.3) * mm, "end": v(120.08, 4.66) * mm});
            skArc(sketch, "E7422", {"start": v(117.84, 5.3) * mm, "mid": v(117.5, 5.53) * mm, "end": v(117.35, 5.91) * mm});
            skArc(sketch, "E7423", {"start": v(117.33, 6.39) * mm, "mid": v(117.34, 6.15) * mm, "end": v(117.35, 5.91) * mm});
            skArc(sketch, "E7424", {"start": v(117.33, 6.39) * mm, "mid": v(117.43, 6.78) * mm, "end": v(117.75, 7.04) * mm});
            skLineSegment(sketch, "E7425", {"start": v(119.9, 7.92) * mm, "end": v(121.68, 8.76) * mm});
            skLineSegment(sketch, "E7426", {"start": v(117.75, 7.04) * mm, "end": v(119.9, 7.92) * mm});
            skArc(sketch, "E7427", {"start": v(121.56, 10.38) * mm, "mid": v(121.62, 9.57) * mm, "end": v(121.68, 8.76) * mm});
            skLineSegment(sketch, "E7428", {"start": v(119.67, 10.94) * mm, "end": v(121.56, 10.38) * mm});
            skLineSegment(sketch, "E7429", {"start": v(117.4, 11.47) * mm, "end": v(119.67, 10.94) * mm});
            skArc(sketch, "E7430", {"start": v(117.4, 11.47) * mm, "mid": v(117.05, 11.67) * mm, "end": v(116.88, 12.05) * mm});
            skArc(sketch, "E7431", {"start": v(116.83, 12.52) * mm, "mid": v(116.86, 12.28) * mm, "end": v(116.88, 12.05) * mm});
            skArc(sketch, "E7432", {"start": v(116.83, 12.52) * mm, "mid": v(116.92, 12.92) * mm, "end": v(117.22, 13.19) * mm});
            skLineSegment(sketch, "E7433", {"start": v(119.33, 14.18) * mm, "end": v(121.06, 15.12) * mm});
            skLineSegment(sketch, "E7434", {"start": v(117.22, 13.19) * mm, "end": v(119.33, 14.18) * mm});
            skArc(sketch, "E7435", {"start": v(120.85, 16.73) * mm, "mid": v(120.96, 15.92) * mm, "end": v(121.06, 15.12) * mm});
            skLineSegment(sketch, "E7436", {"start": v(118.93, 17.18) * mm, "end": v(120.85, 16.73) * mm});
            skLineSegment(sketch, "E7437", {"start": v(116.64, 17.6) * mm, "end": v(118.93, 17.18) * mm});
            skArc(sketch, "E7438", {"start": v(116.64, 17.6) * mm, "mid": v(116.28, 17.78) * mm, "end": v(116.1, 18.15) * mm});
            skArc(sketch, "E7439", {"start": v(116.02, 18.62) * mm, "mid": v(116.05, 18.38) * mm, "end": v(116.1, 18.15) * mm});
            skArc(sketch, "E7440", {"start": v(116.02, 18.62) * mm, "mid": v(116.08, 19.02) * mm, "end": v(116.37, 19.3) * mm});
            skLineSegment(sketch, "E7441", {"start": v(118.42, 20.4) * mm, "end": v(120.1, 21.44) * mm});
            skLineSegment(sketch, "E7442", {"start": v(116.37, 19.3) * mm, "end": v(118.42, 20.4) * mm});
            skArc(sketch, "E7443", {"start": v(119.8, 23.03) * mm, "mid": v(119.96, 22.23) * mm, "end": v(120.1, 21.44) * mm});
            skLineSegment(sketch, "E7444", {"start": v(117.87, 23.38) * mm, "end": v(119.8, 23.03) * mm});
            skLineSegment(sketch, "E7445", {"start": v(115.56, 23.68) * mm, "end": v(117.87, 23.38) * mm});
            skArc(sketch, "E7446", {"start": v(115.56, 23.68) * mm, "mid": v(115.19, 23.84) * mm, "end": v(114.98, 24.2) * mm});
            skArc(sketch, "E7447", {"start": v(114.88, 24.66) * mm, "mid": v(114.93, 24.43) * mm, "end": v(114.98, 24.2) * mm});
            skArc(sketch, "E7448", {"start": v(114.88, 24.66) * mm, "mid": v(114.93, 25.07) * mm, "end": v(115.2, 25.37) * mm});
            skLineSegment(sketch, "E7449", {"start": v(117.19, 26.58) * mm, "end": v(118.82, 27.7) * mm});
            skLineSegment(sketch, "E7450", {"start": v(0, -2.9) * mm, "end": v(0, -3.1) * mm});
            skArc(sketch, "E7451", {"start": v(0, -2.9) * mm, "mid": v(-0.75, -2.8) * mm, "end": v(-1.45, -2.51) * mm});
            skLineSegment(sketch, "E7452", {"start": v(-1.45, -2.51) * mm, "end": v(-1.55, -2.68) * mm});
            skLineSegment(sketch, "E7453", {"start": v(-24.1, 25.54) * mm, "end": v(-63.56, 49.73) * mm});
            skArc(sketch, "E7454", {"start": v(-63.56, 49.73) * mm, "mid": v(-67.31, 55.52) * mm, "end": v(-65.17, 62.07) * mm});
            skArc(sketch, "E7455", {"start": v(-65.17, 62.07) * mm, "mid": v(-44.1, 78.45) * mm, "end": v(-19.16, 87.94) * mm});
            skArc(sketch, "E7456", {"start": v(-19.16, 87.94) * mm, "mid": v(-12.35, 86.28) * mm, "end": v(-9.46, 79.91) * mm});
            skLineSegment(sketch, "E7457", {"start": v(-10.7, 32.88) * mm, "end": v(-9.46, 79.91) * mm});
            skArc(sketch, "E7458", {"start": v(-10.7, 32.88) * mm, "mid": v(-11.83, 28.96) * mm, "end": v(-14.75, 26.12) * mm});
            skArc(sketch, "E7459", {"start": v(-15.72, 25.55) * mm, "mid": v(-15.24, 25.84) * mm, "end": v(-14.75, 26.12) * mm});
            skArc(sketch, "E7460", {"start": v(-15.72, 25.55) * mm, "mid": v(-19.9, 24.37) * mm, "end": v(-24.1, 25.54) * mm});
            skArc(sketch, "E7461", {"start": v(63.9, -63.38) * mm, "mid": v(41.77, -79.72) * mm, "end": v(15.74, -88.61) * mm});
            skArc(sketch, "E7462", {"start": v(15.74, -88.61) * mm, "mid": v(9.12, -86.8) * mm, "end": v(6.34, -80.53) * mm});
            skLineSegment(sketch, "E7463", {"start": v(7.55, -34.46) * mm, "end": v(6.34, -80.53) * mm});
            skArc(sketch, "E7464", {"start": v(7.55, -34.46) * mm, "mid": v(8.89, -30.24) * mm, "end": v(12.27, -27.37) * mm});
            skArc(sketch, "E7465", {"start": v(14.47, -26.28) * mm, "mid": v(13.38, -26.85) * mm, "end": v(12.27, -27.37) * mm});
            skArc(sketch, "E7466", {"start": v(14.47, -26.28) * mm, "mid": v(18.5, -25.3) * mm, "end": v(22.5, -26.47) * mm});
            skLineSegment(sketch, "E7467", {"start": v(22.5, -26.47) * mm, "end": v(62.4, -50.92) * mm});
            skArc(sketch, "E7468", {"start": v(62.4, -50.92) * mm, "mid": v(66.16, -56.79) * mm, "end": v(63.9, -63.38) * mm});
            skArc(sketch, "E7469", {"start": v(58.92, -106.83) * mm, "mid": v(58.21, -107.22) * mm, "end": v(57.5, -107.6) * mm});
            skLineSegment(sketch, "E7470", {"start": v(54.32, -104.7) * mm, "end": v(56, -106.32) * mm});
            skLineSegment(sketch, "E7471", {"start": v(56, -106.32) * mm, "end": v(57.5, -107.6) * mm});
            skArc(sketch, "E7472", {"start": v(53.56, -104.58) * mm, "mid": v(53.96, -104.52) * mm, "end": v(54.32, -104.7) * mm});
            skArc(sketch, "E7473", {"start": v(53.56, -104.58) * mm, "mid": v(53.34, -104.7) * mm, "end": v(53.13, -104.8) * mm});
            skArc(sketch, "E7474", {"start": v(52.78, -105.5) * mm, "mid": v(52.84, -105.1) * mm, "end": v(53.13, -104.8) * mm});
            skLineSegment(sketch, "E7475", {"start": v(52.78, -105.5) * mm, "end": v(53.1, -107.8) * mm});
            skLineSegment(sketch, "E7476", {"start": v(53.1, -107.8) * mm, "end": v(53.25, -109.76) * mm});
            skArc(sketch, "E7477", {"start": v(53.25, -109.76) * mm, "mid": v(52.52, -110.12) * mm, "end": v(51.8, -110.46) * mm});
            skLineSegment(sketch, "E7478", {"start": v(48.77, -107.4) * mm, "end": v(50.36, -109.1) * mm});
            skLineSegment(sketch, "E7479", {"start": v(50.36, -109.1) * mm, "end": v(51.8, -110.46) * mm});
            skArc(sketch, "E7480", {"start": v(48, -107.24) * mm, "mid": v(48.42, -107.2) * mm, "end": v(48.77, -107.4) * mm});
            skArc(sketch, "E7481", {"start": v(48, -107.24) * mm, "mid": v(47.8, -107.34) * mm, "end": v(47.57, -107.44) * mm});
            skArc(sketch, "E7482", {"start": v(47.19, -108.11) * mm, "mid": v(47.27, -107.71) * mm, "end": v(47.57, -107.44) * mm});
            skLineSegment(sketch, "E7483", {"start": v(47.19, -108.11) * mm, "end": v(47.38, -110.43) * mm});
            skLineSegment(sketch, "E7484", {"start": v(47.38, -110.43) * mm, "end": v(47.43, -112.4) * mm});
            skArc(sketch, "E7485", {"start": v(47.43, -112.4) * mm, "mid": v(46.69, -112.71) * mm, "end": v(45.94, -113.02) * mm});
            skLineSegment(sketch, "E7486", {"start": v(43.08, -109.81) * mm, "end": v(44.58, -111.59) * mm});
            skLineSegment(sketch, "E7487", {"start": v(44.58, -111.59) * mm, "end": v(45.94, -113.02) * mm});
            skArc(sketch, "E7488", {"start": v(42.33, -109.61) * mm, "mid": v(42.74, -109.59) * mm, "end": v(43.08, -109.81) * mm});
            skArc(sketch, "E7489", {"start": v(42.33, -109.61) * mm, "mid": v(42.1, -109.7) * mm, "end": v(41.89, -109.78) * mm});
            skArc(sketch, "E7490", {"start": v(41.47, -110.43) * mm, "mid": v(41.57, -110.04) * mm, "end": v(41.89, -109.78) * mm});
            skLineSegment(sketch, "E7491", {"start": v(41.47, -110.43) * mm, "end": v(41.54, -112.76) * mm});
            skLineSegment(sketch, "E7492", {"start": v(41.54, -112.76) * mm, "end": v(41.49, -114.73) * mm});
            skArc(sketch, "E7493", {"start": v(41.49, -114.73) * mm, "mid": v(40.72, -115) * mm, "end": v(39.96, -115.27) * mm});
            skLineSegment(sketch, "E7494", {"start": v(37.27, -111.92) * mm, "end": v(38.68, -113.77) * mm});
            skLineSegment(sketch, "E7495", {"start": v(38.68, -113.77) * mm, "end": v(39.96, -115.27) * mm});
            skArc(sketch, "E7496", {"start": v(36.54, -111.68) * mm, "mid": v(36.94, -111.68) * mm, "end": v(37.27, -111.92) * mm});
            skArc(sketch, "E7497", {"start": v(36.54, -111.68) * mm, "mid": v(36.3, -111.75) * mm, "end": v(36.08, -111.82) * mm});
            skArc(sketch, "E7498", {"start": v(35.63, -112.45) * mm, "mid": v(35.75, -112.06) * mm, "end": v(36.08, -111.82) * mm});
            skLineSegment(sketch, "E7499", {"start": v(35.63, -112.45) * mm, "end": v(35.58, -114.78) * mm});
            skLineSegment(sketch, "E7500", {"start": v(35.58, -114.78) * mm, "end": v(35.43, -116.74) * mm});
            skArc(sketch, "E7501", {"start": v(35.43, -116.74) * mm, "mid": v(34.65, -116.98) * mm, "end": v(33.87, -117.2) * mm});
            skLineSegment(sketch, "E7502", {"start": v(31.36, -113.71) * mm, "end": v(32.68, -115.64) * mm});
            skLineSegment(sketch, "E7503", {"start": v(32.68, -115.64) * mm, "end": v(33.87, -117.2) * mm});
            skArc(sketch, "E7504", {"start": v(30.64, -113.43) * mm, "mid": v(31.05, -113.46) * mm, "end": v(31.36, -113.71) * mm});
            skArc(sketch, "E7505", {"start": v(30.64, -113.43) * mm, "mid": v(30.41, -113.5) * mm, "end": v(30.18, -113.56) * mm});
            skArc(sketch, "E7506", {"start": v(29.7, -114.16) * mm, "mid": v(29.84, -113.78) * mm, "end": v(30.18, -113.56) * mm});
            skLineSegment(sketch, "E7507", {"start": v(29.7, -114.16) * mm, "end": v(29.52, -116.48) * mm});
            skLineSegment(sketch, "E7508", {"start": v(29.52, -116.48) * mm, "end": v(29.27, -118.44) * mm});
            skArc(sketch, "E7509", {"start": v(29.27, -118.44) * mm, "mid": v(28.48, -118.63) * mm, "end": v(27.7, -118.82) * mm});
            skLineSegment(sketch, "E7510", {"start": v(25.37, -115.2) * mm, "end": v(26.58, -117.19) * mm});
            skLineSegment(sketch, "E7511", {"start": v(26.58, -117.19) * mm, "end": v(27.7, -118.82) * mm});
            skArc(sketch, "E7512", {"start": v(24.66, -114.88) * mm, "mid": v(25.07, -114.93) * mm, "end": v(25.37, -115.2) * mm});
            skArc(sketch, "E7513", {"start": v(24.66, -114.88) * mm, "mid": v(24.43, -114.93) * mm, "end": v(24.2, -114.98) * mm});
            skArc(sketch, "E7514", {"start": v(23.68, -115.56) * mm, "mid": v(23.84, -115.19) * mm, "end": v(24.2, -114.98) * mm});
            skLineSegment(sketch, "E7515", {"start": v(23.68, -115.56) * mm, "end": v(23.38, -117.87) * mm});
            skLineSegment(sketch, "E7516", {"start": v(23.38, -117.87) * mm, "end": v(23.03, -119.8) * mm});
            skArc(sketch, "E7517", {"start": v(23.03, -119.8) * mm, "mid": v(22.23, -119.96) * mm, "end": v(21.44, -120.1) * mm});
            skLineSegment(sketch, "E7518", {"start": v(19.3, -116.37) * mm, "end": v(20.4, -118.42) * mm});
            skLineSegment(sketch, "E7519", {"start": v(20.4, -118.42) * mm, "end": v(21.44, -120.1) * mm});
            skArc(sketch, "E7520", {"start": v(18.62, -116.02) * mm, "mid": v(19.02, -116.08) * mm, "end": v(19.3, -116.37) * mm});
            skArc(sketch, "E7521", {"start": v(18.62, -116.02) * mm, "mid": v(18.38, -116.05) * mm, "end": v(18.15, -116.1) * mm});
            skArc(sketch, "E7522", {"start": v(17.6, -116.64) * mm, "mid": v(17.78, -116.28) * mm, "end": v(18.15, -116.1) * mm});
            skLineSegment(sketch, "E7523", {"start": v(17.6, -116.64) * mm, "end": v(17.18, -118.93) * mm});
            skLineSegment(sketch, "E7524", {"start": v(17.18, -118.93) * mm, "end": v(16.73, -120.85) * mm});
            skArc(sketch, "E7525", {"start": v(16.73, -120.85) * mm, "mid": v(15.92, -120.96) * mm, "end": v(15.12, -121.06) * mm});
            skLineSegment(sketch, "E7526", {"start": v(13.19, -117.22) * mm, "end": v(14.18, -119.33) * mm});
            skLineSegment(sketch, "E7527", {"start": v(14.18, -119.33) * mm, "end": v(15.12, -121.06) * mm});
            skArc(sketch, "E7528", {"start": v(12.52, -116.83) * mm, "mid": v(12.92, -116.92) * mm, "end": v(13.19, -117.22) * mm});
            skArc(sketch, "E7529", {"start": v(12.52, -116.83) * mm, "mid": v(12.28, -116.86) * mm, "end": v(12.05, -116.88) * mm});
            skArc(sketch, "E7530", {"start": v(11.47, -117.4) * mm, "mid": v(11.67, -117.05) * mm, "end": v(12.05, -116.88) * mm});
            skLineSegment(sketch, "E7531", {"start": v(11.47, -117.4) * mm, "end": v(10.94, -119.67) * mm});
            skLineSegment(sketch, "E7532", {"start": v(10.94, -119.67) * mm, "end": v(10.38, -121.56) * mm});
            skArc(sketch, "E7533", {"start": v(10.38, -121.56) * mm, "mid": v(9.57, -121.62) * mm, "end": v(8.76, -121.68) * mm});
            skLineSegment(sketch, "E7534", {"start": v(7.04, -117.75) * mm, "end": v(7.92, -119.9) * mm});
            skLineSegment(sketch, "E7535", {"start": v(7.92, -119.9) * mm, "end": v(8.76, -121.68) * mm});
            skArc(sketch, "E7536", {"start": v(6.39, -117.33) * mm, "mid": v(6.78, -117.43) * mm, "end": v(7.04, -117.75) * mm});
            skArc(sketch, "E7537", {"start": v(6.39, -117.33) * mm, "mid": v(6.15, -117.34) * mm, "end": v(5.91, -117.35) * mm});
            skArc(sketch, "E7538", {"start": v(5.3, -117.84) * mm, "mid": v(5.53, -117.5) * mm, "end": v(5.91, -117.35) * mm});
            skLineSegment(sketch, "E7539", {"start": v(5.3, -117.84) * mm, "end": v(4.66, -120.08) * mm});
            skLineSegment(sketch, "E7540", {"start": v(4.66, -120.08) * mm, "end": v(4, -121.93) * mm});
            skArc(sketch, "E7541", {"start": v(4, -121.93) * mm, "mid": v(3.2, -121.96) * mm, "end": v(2.38, -121.98) * mm});
            skLineSegment(sketch, "E7542", {"start": v(0.86, -117.96) * mm, "end": v(1.63, -120.15) * mm});
            skLineSegment(sketch, "E7543", {"start": v(1.63, -120.15) * mm, "end": v(2.38, -121.98) * mm});
            skArc(sketch, "E7544", {"start": v(0.24, -117.5) * mm, "mid": v(0.63, -117.63) * mm, "end": v(0.86, -117.96) * mm});
            skArc(sketch, "E7545", {"start": v(0.24, -117.5) * mm, "mid": v(0, -117.5) * mm, "end": v(-0.24, -117.5) * mm});
            skArc(sketch, "E7546", {"start": v(-0.86, -117.96) * mm, "mid": v(-0.63, -117.63) * mm, "end": v(-0.24, -117.5) * mm});
            skLineSegment(sketch, "E7547", {"start": v(-0.86, -117.96) * mm, "end": v(-1.63, -120.15) * mm});
            skLineSegment(sketch, "E7548", {"start": v(-1.63, -120.15) * mm, "end": v(-2.38, -121.98) * mm});
            skArc(sketch, "E7549", {"start": v(-2.38, -121.98) * mm, "mid": v(-3.2, -121.96) * mm, "end": v(-4, -121.93) * mm});
            skLineSegment(sketch, "E7550", {"start": v(-5.3, -117.84) * mm, "end": v(-4.66, -120.08) * mm});
            skLineSegment(sketch, "E7551", {"start": v(-4.66, -120.08) * mm, "end": v(-4, -121.93) * mm});
            skArc(sketch, "E7552", {"start": v(-5.91, -117.35) * mm, "mid": v(-5.53, -117.5) * mm, "end": v(-5.3, -117.84) * mm});
            skArc(sketch, "E7553", {"start": v(-5.91, -117.35) * mm, "mid": v(-6.15, -117.34) * mm, "end": v(-6.39, -117.33) * mm});
            skArc(sketch, "E7554", {"start": v(-7.04, -117.75) * mm, "mid": v(-6.78, -117.43) * mm, "end": v(-6.39, -117.33) * mm});
            skLineSegment(sketch, "E7555", {"start": v(-7.04, -117.75) * mm, "end": v(-7.92, -119.9) * mm});
            skLineSegment(sketch, "E7556", {"start": v(-7.92, -119.9) * mm, "end": v(-8.76, -121.68) * mm});
            skArc(sketch, "E7557", {"start": v(-8.76, -121.68) * mm, "mid": v(-9.57, -121.62) * mm, "end": v(-10.38, -121.56) * mm});
            skLineSegment(sketch, "E7558", {"start": v(-11.47, -117.4) * mm, "end": v(-10.94, -119.67) * mm});
            skLineSegment(sketch, "E7559", {"start": v(-10.94, -119.67) * mm, "end": v(-10.38, -121.56) * mm});
            skArc(sketch, "E7560", {"start": v(-12.05, -116.88) * mm, "mid": v(-11.67, -117.05) * mm, "end": v(-11.47, -117.4) * mm});
            skArc(sketch, "E7561", {"start": v(-12.05, -116.88) * mm, "mid": v(-12.28, -116.86) * mm, "end": v(-12.52, -116.83) * mm});
            skArc(sketch, "E7562", {"start": v(-13.19, -117.22) * mm, "mid": v(-12.92, -116.92) * mm, "end": v(-12.52, -116.83) * mm});
            skLineSegment(sketch, "E7563", {"start": v(-13.19, -117.22) * mm, "end": v(-14.18, -119.33) * mm});
            skLineSegment(sketch, "E7564", {"start": v(-14.18, -119.33) * mm, "end": v(-15.12, -121.06) * mm});
            skArc(sketch, "E7565", {"start": v(-15.12, -121.06) * mm, "mid": v(-15.92, -120.96) * mm, "end": v(-16.73, -120.85) * mm});
            skLineSegment(sketch, "E7566", {"start": v(-17.6, -116.64) * mm, "end": v(-17.18, -118.93) * mm});
            skLineSegment(sketch, "E7567", {"start": v(-17.18, -118.93) * mm, "end": v(-16.73, -120.85) * mm});
            skArc(sketch, "E7568", {"start": v(-18.15, -116.1) * mm, "mid": v(-17.78, -116.28) * mm, "end": v(-17.6, -116.64) * mm});
            skArc(sketch, "E7569", {"start": v(-18.15, -116.1) * mm, "mid": v(-18.38, -116.05) * mm, "end": v(-18.62, -116.02) * mm});
            skArc(sketch, "E7570", {"start": v(-19.3, -116.37) * mm, "mid": v(-19.02, -116.08) * mm, "end": v(-18.62, -116.02) * mm});
            skLineSegment(sketch, "E7571", {"start": v(-19.3, -116.37) * mm, "end": v(-20.4, -118.42) * mm});
            skLineSegment(sketch, "E7572", {"start": v(-20.4, -118.42) * mm, "end": v(-21.44, -120.1) * mm});
            skArc(sketch, "E7573", {"start": v(-21.44, -120.1) * mm, "mid": v(-22.23, -119.96) * mm, "end": v(-23.03, -119.8) * mm});
            skLineSegment(sketch, "E7574", {"start": v(-23.68, -115.56) * mm, "end": v(-23.38, -117.87) * mm});
            skLineSegment(sketch, "E7575", {"start": v(-23.38, -117.87) * mm, "end": v(-23.03, -119.8) * mm});
            skArc(sketch, "E7576", {"start": v(-24.2, -114.98) * mm, "mid": v(-23.84, -115.19) * mm, "end": v(-23.68, -115.56) * mm});
            skArc(sketch, "E7577", {"start": v(-24.2, -114.98) * mm, "mid": v(-24.43, -114.93) * mm, "end": v(-24.66, -114.88) * mm});
            skArc(sketch, "E7578", {"start": v(-25.37, -115.2) * mm, "mid": v(-25.07, -114.93) * mm, "end": v(-24.66, -114.88) * mm});
            skLineSegment(sketch, "E7579", {"start": v(-25.37, -115.2) * mm, "end": v(-26.58, -117.19) * mm});
            skLineSegment(sketch, "E7580", {"start": v(-26.58, -117.19) * mm, "end": v(-27.7, -118.82) * mm});
            skArc(sketch, "E7581", {"start": v(-27.7, -118.82) * mm, "mid": v(-28.48, -118.63) * mm, "end": v(-29.27, -118.44) * mm});
            skLineSegment(sketch, "E7582", {"start": v(-29.7, -114.16) * mm, "end": v(-29.52, -116.48) * mm});
            skLineSegment(sketch, "E7583", {"start": v(-29.52, -116.48) * mm, "end": v(-29.27, -118.44) * mm});
            skArc(sketch, "E7584", {"start": v(-30.18, -113.56) * mm, "mid": v(-29.84, -113.78) * mm, "end": v(-29.7, -114.16) * mm});
            skArc(sketch, "E7585", {"start": v(-30.18, -113.56) * mm, "mid": v(-30.41, -113.5) * mm, "end": v(-30.64, -113.43) * mm});
            skArc(sketch, "E7586", {"start": v(-31.36, -113.71) * mm, "mid": v(-31.05, -113.46) * mm, "end": v(-30.64, -113.43) * mm});
            skLineSegment(sketch, "E7587", {"start": v(-31.36, -113.71) * mm, "end": v(-32.68, -115.64) * mm});
            skLineSegment(sketch, "E7588", {"start": v(-32.68, -115.64) * mm, "end": v(-33.87, -117.2) * mm});
            skArc(sketch, "E7589", {"start": v(-33.87, -117.2) * mm, "mid": v(-34.65, -116.98) * mm, "end": v(-35.43, -116.74) * mm});
            skLineSegment(sketch, "E7590", {"start": v(-35.63, -112.45) * mm, "end": v(-35.58, -114.78) * mm});
            skLineSegment(sketch, "E7591", {"start": v(-35.58, -114.78) * mm, "end": v(-35.43, -116.74) * mm});
            skArc(sketch, "E7592", {"start": v(-36.08, -111.82) * mm, "mid": v(-35.75, -112.06) * mm, "end": v(-35.63, -112.45) * mm});
            skArc(sketch, "E7593", {"start": v(-36.08, -111.82) * mm, "mid": v(-36.3, -111.75) * mm, "end": v(-36.54, -111.68) * mm});
            skArc(sketch, "E7594", {"start": v(-37.27, -111.92) * mm, "mid": v(-36.94, -111.68) * mm, "end": v(-36.54, -111.68) * mm});
            skLineSegment(sketch, "E7595", {"start": v(-37.27, -111.92) * mm, "end": v(-38.68, -113.77) * mm});
            skLineSegment(sketch, "E7596", {"start": v(-38.68, -113.77) * mm, "end": v(-39.96, -115.27) * mm});
            skArc(sketch, "E7597", {"start": v(-39.96, -115.27) * mm, "mid": v(-40.72, -115) * mm, "end": v(-41.49, -114.73) * mm});
            skLineSegment(sketch, "E7598", {"start": v(-41.47, -110.43) * mm, "end": v(-41.54, -112.76) * mm});
            skLineSegment(sketch, "E7599", {"start": v(-41.54, -112.76) * mm, "end": v(-41.49, -114.73) * mm});
            skArc(sketch, "E7600", {"start": v(-41.89, -109.78) * mm, "mid": v(-41.57, -110.04) * mm, "end": v(-41.47, -110.43) * mm});
            skArc(sketch, "E7601", {"start": v(-41.89, -109.78) * mm, "mid": v(-42.1, -109.7) * mm, "end": v(-42.33, -109.61) * mm});
            skArc(sketch, "E7602", {"start": v(-43.08, -109.81) * mm, "mid": v(-42.74, -109.59) * mm, "end": v(-42.33, -109.61) * mm});
            skLineSegment(sketch, "E7603", {"start": v(-43.08, -109.81) * mm, "end": v(-44.58, -111.59) * mm});
            skLineSegment(sketch, "E7604", {"start": v(-44.58, -111.59) * mm, "end": v(-45.94, -113.02) * mm});
            skArc(sketch, "E7605", {"start": v(-45.94, -113.02) * mm, "mid": v(-46.69, -112.71) * mm, "end": v(-47.43, -112.4) * mm});
            skLineSegment(sketch, "E7606", {"start": v(-47.19, -108.11) * mm, "end": v(-47.38, -110.43) * mm});
            skLineSegment(sketch, "E7607", {"start": v(-47.38, -110.43) * mm, "end": v(-47.43, -112.4) * mm});
            skArc(sketch, "E7608", {"start": v(-47.57, -107.44) * mm, "mid": v(-47.27, -107.71) * mm, "end": v(-47.19, -108.11) * mm});
            skArc(sketch, "E7609", {"start": v(-47.57, -107.44) * mm, "mid": v(-47.8, -107.34) * mm, "end": v(-48, -107.24) * mm});
            skArc(sketch, "E7610", {"start": v(-48.77, -107.4) * mm, "mid": v(-48.42, -107.2) * mm, "end": v(-48, -107.24) * mm});
            skLineSegment(sketch, "E7611", {"start": v(-48.77, -107.4) * mm, "end": v(-50.36, -109.1) * mm});
            skLineSegment(sketch, "E7612", {"start": v(-50.36, -109.1) * mm, "end": v(-51.8, -110.46) * mm});
            skArc(sketch, "E7613", {"start": v(-51.8, -110.46) * mm, "mid": v(-52.52, -110.12) * mm, "end": v(-53.25, -109.76) * mm});
            skLineSegment(sketch, "E7614", {"start": v(-52.78, -105.5) * mm, "end": v(-53.1, -107.8) * mm});
            skLineSegment(sketch, "E7615", {"start": v(-53.1, -107.8) * mm, "end": v(-53.25, -109.76) * mm});
            skArc(sketch, "E7616", {"start": v(-53.13, -104.8) * mm, "mid": v(-52.84, -105.1) * mm, "end": v(-52.78, -105.5) * mm});
            skArc(sketch, "E7617", {"start": v(-53.13, -104.8) * mm, "mid": v(-53.34, -104.7) * mm, "end": v(-53.56, -104.58) * mm});
            skArc(sketch, "E7618", {"start": v(-54.32, -104.7) * mm, "mid": v(-53.96, -104.52) * mm, "end": v(-53.56, -104.58) * mm});
            skLineSegment(sketch, "E7619", {"start": v(-54.32, -104.7) * mm, "end": v(-56, -106.32) * mm});
            skLineSegment(sketch, "E7620", {"start": v(-56, -106.32) * mm, "end": v(-57.5, -107.6) * mm});
            skArc(sketch, "E7621", {"start": v(-57.5, -107.6) * mm, "mid": v(-58.21, -107.22) * mm, "end": v(-58.92, -106.83) * mm});
            skLineSegment(sketch, "E7622", {"start": v(-58.23, -102.59) * mm, "end": v(-58.66, -104.87) * mm});
            skLineSegment(sketch, "E7623", {"start": v(-58.66, -104.87) * mm, "end": v(-58.92, -106.83) * mm});
            skArc(sketch, "E7624", {"start": v(-58.54, -101.88) * mm, "mid": v(-58.27, -102.18) * mm, "end": v(-58.23, -102.59) * mm});
            skArc(sketch, "E7625", {"start": v(-58.54, -101.88) * mm, "mid": v(-58.75, -101.76) * mm, "end": v(-58.96, -101.64) * mm});
            skArc(sketch, "E7626", {"start": v(-59.73, -101.72) * mm, "mid": v(-59.36, -101.55) * mm, "end": v(-58.96, -101.64) * mm});
            skLineSegment(sketch, "E7627", {"start": v(-59.73, -101.72) * mm, "end": v(-61.5, -103.24) * mm});
            skLineSegment(sketch, "E7628", {"start": v(-61.5, -103.24) * mm, "end": v(-63.05, -104.44) * mm});
            skArc(sketch, "E7629", {"start": v(-63.05, -104.44) * mm, "mid": v(-63.74, -104.02) * mm, "end": v(-64.43, -103.6) * mm});
            skLineSegment(sketch, "E7630", {"start": v(-63.52, -99.4) * mm, "end": v(-64.07, -101.66) * mm});
            skLineSegment(sketch, "E7631", {"start": v(-64.07, -101.66) * mm, "end": v(-64.43, -103.6) * mm});
            skArc(sketch, "E7632", {"start": v(-63.8, -98.67) * mm, "mid": v(-63.54, -99) * mm, "end": v(-63.52, -99.4) * mm});
            skArc(sketch, "E7633", {"start": v(-63.8, -98.67) * mm, "mid": v(-64, -98.54) * mm, "end": v(-64.2, -98.41) * mm});
            skArc(sketch, "E7634", {"start": v(-64.97, -98.46) * mm, "mid": v(-64.59, -98.3) * mm, "end": v(-64.2, -98.41) * mm});
            skLineSegment(sketch, "E7635", {"start": v(-64.97, -98.46) * mm, "end": v(-66.8, -99.88) * mm});
            skLineSegment(sketch, "E7636", {"start": v(-66.8, -99.88) * mm, "end": v(-68.43, -101) * mm});
            skArc(sketch, "E7637", {"start": v(-68.43, -101) * mm, "mid": v(-69.1, -100.54) * mm, "end": v(-69.77, -100.08) * mm});
            skLineSegment(sketch, "E7638", {"start": v(-68.63, -95.94) * mm, "end": v(-69.3, -98.17) * mm});
            skLineSegment(sketch, "E7639", {"start": v(-69.3, -98.17) * mm, "end": v(-69.77, -100.08) * mm});
            skArc(sketch, "E7640", {"start": v(-68.87, -95.2) * mm, "mid": v(-68.63, -95.53) * mm, "end": v(-68.63, -95.94) * mm});
            skArc(sketch, "E7641", {"start": v(-68.87, -95.2) * mm, "mid": v(-69.06, -95.06) * mm, "end": v(-69.26, -94.92) * mm});
            skArc(sketch, "E7642", {"start": v(-70.03, -94.92) * mm, "mid": v(-69.65, -94.8) * mm, "end": v(-69.26, -94.92) * mm});
            skLineSegment(sketch, "E7643", {"start": v(-70.03, -94.92) * mm, "end": v(-71.95, -96.25) * mm});
            skLineSegment(sketch, "E7644", {"start": v(-71.95, -96.25) * mm, "end": v(-73.62, -97.28) * mm});
            skArc(sketch, "E7645", {"start": v(-73.62, -97.28) * mm, "mid": v(-74.27, -96.79) * mm, "end": v(-74.9, -96.3) * mm});
            skLineSegment(sketch, "E7646", {"start": v(-73.56, -92.21) * mm, "end": v(-74.35, -94.4) * mm});
            skLineSegment(sketch, "E7647", {"start": v(-74.35, -94.4) * mm, "end": v(-74.9, -96.3) * mm});
            skArc(sketch, "E7648", {"start": v(-73.76, -91.46) * mm, "mid": v(-73.54, -91.8) * mm, "end": v(-73.56, -92.21) * mm});
            skArc(sketch, "E7649", {"start": v(-73.76, -91.46) * mm, "mid": v(-73.95, -91.31) * mm, "end": v(-74.13, -91.16) * mm});
            skArc(sketch, "E7650", {"start": v(-74.9, -91.13) * mm, "mid": v(-74.51, -91.02) * mm, "end": v(-74.13, -91.16) * mm});
            skLineSegment(sketch, "E7651", {"start": v(-74.9, -91.13) * mm, "end": v(-76.88, -92.35) * mm});
            skLineSegment(sketch, "E7652", {"start": v(-76.88, -92.35) * mm, "end": v(-78.62, -93.3) * mm});
            skArc(sketch, "E7653", {"start": v(-78.62, -93.3) * mm, "mid": v(-79.23, -92.77) * mm, "end": v(-79.85, -92.24) * mm});
            skLineSegment(sketch, "E7654", {"start": v(-78.29, -88.24) * mm, "end": v(-79.19, -90.38) * mm});
            skLineSegment(sketch, "E7655", {"start": v(-79.19, -90.38) * mm, "end": v(-79.85, -92.24) * mm});
            skArc(sketch, "E7656", {"start": v(-78.45, -87.48) * mm, "mid": v(-78.24, -87.83) * mm, "end": v(-78.29, -88.24) * mm});
            skArc(sketch, "E7657", {"start": v(-78.45, -87.48) * mm, "mid": v(-78.62, -87.32) * mm, "end": v(-78.8, -87.16) * mm});
            skArc(sketch, "E7658", {"start": v(-79.57, -87.08) * mm, "mid": v(-79.17, -87) * mm, "end": v(-78.8, -87.16) * mm});
            skLineSegment(sketch, "E7659", {"start": v(-79.57, -87.08) * mm, "end": v(-81.61, -88.2) * mm});
            skLineSegment(sketch, "E7660", {"start": v(-81.61, -88.2) * mm, "end": v(-83.4, -89.05) * mm});
            skArc(sketch, "E7661", {"start": v(-83.4, -89.05) * mm, "mid": v(-83.98, -88.5) * mm, "end": v(-84.56, -87.94) * mm});
            skLineSegment(sketch, "E7662", {"start": v(-82.8, -84.02) * mm, "end": v(-83.8, -86.12) * mm});
            skLineSegment(sketch, "E7663", {"start": v(-83.8, -86.12) * mm, "end": v(-84.56, -87.94) * mm});
            skArc(sketch, "E7664", {"start": v(-82.92, -83.25) * mm, "mid": v(-82.73, -83.62) * mm, "end": v(-82.8, -84.02) * mm});
            skArc(sketch, "E7665", {"start": v(-82.92, -83.25) * mm, "mid": v(-83.09, -83.09) * mm, "end": v(-83.25, -82.92) * mm});
            skArc(sketch, "E7666", {"start": v(-84.02, -82.8) * mm, "mid": v(-83.62, -82.73) * mm, "end": v(-83.25, -82.92) * mm});
            skLineSegment(sketch, "E7667", {"start": v(-84.02, -82.8) * mm, "end": v(-86.12, -83.8) * mm});
            skLineSegment(sketch, "E7668", {"start": v(-86.12, -83.8) * mm, "end": v(-87.94, -84.56) * mm});
            skArc(sketch, "E7669", {"start": v(-87.94, -84.56) * mm, "mid": v(-88.5, -83.98) * mm, "end": v(-89.05, -83.4) * mm});
            skLineSegment(sketch, "E7670", {"start": v(-87.08, -79.57) * mm, "end": v(-88.2, -81.61) * mm});
            skLineSegment(sketch, "E7671", {"start": v(-88.2, -81.61) * mm, "end": v(-89.05, -83.4) * mm});
            skArc(sketch, "E7672", {"start": v(-87.16, -78.8) * mm, "mid": v(-87, -79.17) * mm, "end": v(-87.08, -79.57) * mm});
            skArc(sketch, "E7673", {"start": v(-87.16, -78.8) * mm, "mid": v(-87.32, -78.62) * mm, "end": v(-87.48, -78.45) * mm});
            skArc(sketch, "E7674", {"start": v(-88.24, -78.29) * mm, "mid": v(-87.83, -78.24) * mm, "end": v(-87.48, -78.45) * mm});
            skLineSegment(sketch, "E7675", {"start": v(-88.24, -78.29) * mm, "end": v(-90.38, -79.19) * mm});
            skLineSegment(sketch, "E7676", {"start": v(-90.38, -79.19) * mm, "end": v(-92.24, -79.85) * mm});
            skArc(sketch, "E7677", {"start": v(-92.24, -79.85) * mm, "mid": v(-92.77, -79.23) * mm, "end": v(-93.3, -78.62) * mm});
            skLineSegment(sketch, "E7678", {"start": v(-91.13, -74.9) * mm, "end": v(-92.35, -76.88) * mm});
            skLineSegment(sketch, "E7679", {"start": v(-92.35, -76.88) * mm, "end": v(-93.3, -78.62) * mm});
            skArc(sketch, "E7680", {"start": v(-91.16, -74.13) * mm, "mid": v(-91.02, -74.51) * mm, "end": v(-91.13, -74.9) * mm});
            skArc(sketch, "E7681", {"start": v(-91.16, -74.13) * mm, "mid": v(-91.31, -73.95) * mm, "end": v(-91.46, -73.76) * mm});
            skArc(sketch, "E7682", {"start": v(-92.21, -73.56) * mm, "mid": v(-91.8, -73.54) * mm, "end": v(-91.46, -73.76) * mm});
            skLineSegment(sketch, "E7683", {"start": v(-92.21, -73.56) * mm, "end": v(-94.4, -74.35) * mm});
            skLineSegment(sketch, "E7684", {"start": v(-94.4, -74.35) * mm, "end": v(-96.3, -74.9) * mm});
            skArc(sketch, "E7685", {"start": v(-96.3, -74.9) * mm, "mid": v(-96.79, -74.27) * mm, "end": v(-97.28, -73.62) * mm});
            skLineSegment(sketch, "E7686", {"start": v(-94.92, -70.03) * mm, "end": v(-96.25, -71.95) * mm});
            skLineSegment(sketch, "E7687", {"start": v(-96.25, -71.95) * mm, "end": v(-97.28, -73.62) * mm});
            skArc(sketch, "E7688", {"start": v(-94.92, -69.26) * mm, "mid": v(-94.8, -69.65) * mm, "end": v(-94.92, -70.03) * mm});
            skArc(sketch, "E7689", {"start": v(-94.92, -69.26) * mm, "mid": v(-95.06, -69.06) * mm, "end": v(-95.2, -68.87) * mm});
            skArc(sketch, "E7690", {"start": v(-95.94, -68.63) * mm, "mid": v(-95.53, -68.63) * mm, "end": v(-95.2, -68.87) * mm});
            skLineSegment(sketch, "E7691", {"start": v(-95.94, -68.63) * mm, "end": v(-98.17, -69.3) * mm});
            skLineSegment(sketch, "E7692", {"start": v(-98.17, -69.3) * mm, "end": v(-100.08, -69.77) * mm});
            skArc(sketch, "E7693", {"start": v(-100.08, -69.77) * mm, "mid": v(-100.54, -69.1) * mm, "end": v(-101, -68.43) * mm});
            skLineSegment(sketch, "E7694", {"start": v(-98.46, -64.97) * mm, "end": v(-99.88, -66.8) * mm});
            skLineSegment(sketch, "E7695", {"start": v(-99.88, -66.8) * mm, "end": v(-101, -68.43) * mm});
            skArc(sketch, "E7696", {"start": v(-98.41, -64.2) * mm, "mid": v(-98.3, -64.59) * mm, "end": v(-98.46, -64.97) * mm});
            skArc(sketch, "E7697", {"start": v(-98.41, -64.2) * mm, "mid": v(-98.54, -64) * mm, "end": v(-98.67, -63.8) * mm});
            skArc(sketch, "E7698", {"start": v(-99.4, -63.52) * mm, "mid": v(-99, -63.54) * mm, "end": v(-98.67, -63.8) * mm});
            skLineSegment(sketch, "E7699", {"start": v(-99.4, -63.52) * mm, "end": v(-101.66, -64.07) * mm});
            skLineSegment(sketch, "E7700", {"start": v(-101.66, -64.07) * mm, "end": v(-103.6, -64.43) * mm});
            skArc(sketch, "E7701", {"start": v(-103.6, -64.43) * mm, "mid": v(-104.02, -63.74) * mm, "end": v(-104.44, -63.05) * mm});
            skLineSegment(sketch, "E7702", {"start": v(-101.72, -59.73) * mm, "end": v(-103.24, -61.5) * mm});
            skLineSegment(sketch, "E7703", {"start": v(-103.24, -61.5) * mm, "end": v(-104.44, -63.05) * mm});
            skArc(sketch, "E7704", {"start": v(-101.64, -58.96) * mm, "mid": v(-101.55, -59.36) * mm, "end": v(-101.72, -59.73) * mm});
            skArc(sketch, "E7705", {"start": v(-101.64, -58.96) * mm, "mid": v(-101.76, -58.75) * mm, "end": v(-101.88, -58.54) * mm});
            skArc(sketch, "E7706", {"start": v(-102.59, -58.23) * mm, "mid": v(-102.18, -58.27) * mm, "end": v(-101.88, -58.54) * mm});
            skLineSegment(sketch, "E7707", {"start": v(-102.59, -58.23) * mm, "end": v(-104.87, -58.66) * mm});
            skLineSegment(sketch, "E7708", {"start": v(-104.87, -58.66) * mm, "end": v(-106.83, -58.92) * mm});
            skArc(sketch, "E7709", {"start": v(-106.83, -58.92) * mm, "mid": v(-107.22, -58.21) * mm, "end": v(-107.6, -57.5) * mm});
            skLineSegment(sketch, "E7710", {"start": v(-104.7, -54.32) * mm, "end": v(-106.32, -56) * mm});
            skLineSegment(sketch, "E7711", {"start": v(-106.32, -56) * mm, "end": v(-107.6, -57.5) * mm});
            skArc(sketch, "E7712", {"start": v(-104.58, -53.56) * mm, "mid": v(-104.52, -53.96) * mm, "end": v(-104.7, -54.32) * mm});
            skArc(sketch, "E7713", {"start": v(-104.58, -53.56) * mm, "mid": v(-104.7, -53.34) * mm, "end": v(-104.8, -53.13) * mm});
            skArc(sketch, "E7714", {"start": v(-105.5, -52.78) * mm, "mid": v(-105.1, -52.84) * mm, "end": v(-104.8, -53.13) * mm});
            skLineSegment(sketch, "E7715", {"start": v(-105.5, -52.78) * mm, "end": v(-107.8, -53.1) * mm});
            skLineSegment(sketch, "E7716", {"start": v(-107.8, -53.1) * mm, "end": v(-109.76, -53.25) * mm});
            skArc(sketch, "E7717", {"start": v(-109.76, -53.25) * mm, "mid": v(-110.12, -52.52) * mm, "end": v(-110.46, -51.8) * mm});
            skLineSegment(sketch, "E7718", {"start": v(-107.4, -48.77) * mm, "end": v(-109.1, -50.36) * mm});
            skLineSegment(sketch, "E7719", {"start": v(-109.1, -50.36) * mm, "end": v(-110.46, -51.8) * mm});
            skArc(sketch, "E7720", {"start": v(-107.24, -48) * mm, "mid": v(-107.2, -48.42) * mm, "end": v(-107.4, -48.77) * mm});
            skArc(sketch, "E7721", {"start": v(-107.24, -48) * mm, "mid": v(-107.34, -47.8) * mm, "end": v(-107.44, -47.57) * mm});
            skArc(sketch, "E7722", {"start": v(-108.11, -47.19) * mm, "mid": v(-107.71, -47.27) * mm, "end": v(-107.44, -47.57) * mm});
            skLineSegment(sketch, "E7723", {"start": v(-108.11, -47.19) * mm, "end": v(-110.43, -47.38) * mm});
            skLineSegment(sketch, "E7724", {"start": v(-110.43, -47.38) * mm, "end": v(-112.4, -47.43) * mm});
            skArc(sketch, "E7725", {"start": v(-112.4, -47.43) * mm, "mid": v(-112.71, -46.69) * mm, "end": v(-113.02, -45.94) * mm});
            skLineSegment(sketch, "E7726", {"start": v(-109.81, -43.08) * mm, "end": v(-111.59, -44.58) * mm});
            skLineSegment(sketch, "E7727", {"start": v(-111.59, -44.58) * mm, "end": v(-113.02, -45.94) * mm});
            skArc(sketch, "E7728", {"start": v(-109.61, -42.33) * mm, "mid": v(-109.59, -42.74) * mm, "end": v(-109.81, -43.08) * mm});
            skArc(sketch, "E7729", {"start": v(-109.61, -42.33) * mm, "mid": v(-109.7, -42.1) * mm, "end": v(-109.78, -41.89) * mm});
            skArc(sketch, "E7730", {"start": v(-110.43, -41.47) * mm, "mid": v(-110.04, -41.57) * mm, "end": v(-109.78, -41.89) * mm});
            skLineSegment(sketch, "E7731", {"start": v(-110.43, -41.47) * mm, "end": v(-112.76, -41.54) * mm});
            skLineSegment(sketch, "E7732", {"start": v(-112.76, -41.54) * mm, "end": v(-114.73, -41.49) * mm});
            skArc(sketch, "E7733", {"start": v(-114.73, -41.49) * mm, "mid": v(-115, -40.72) * mm, "end": v(-115.27, -39.96) * mm});
            skLineSegment(sketch, "E7734", {"start": v(-111.92, -37.27) * mm, "end": v(-113.77, -38.68) * mm});
            skLineSegment(sketch, "E7735", {"start": v(-113.77, -38.68) * mm, "end": v(-115.27, -39.96) * mm});
            skArc(sketch, "E7736", {"start": v(-111.68, -36.54) * mm, "mid": v(-111.68, -36.94) * mm, "end": v(-111.92, -37.27) * mm});
            skArc(sketch, "E7737", {"start": v(-111.68, -36.54) * mm, "mid": v(-111.75, -36.3) * mm, "end": v(-111.82, -36.08) * mm});
            skArc(sketch, "E7738", {"start": v(-112.45, -35.63) * mm, "mid": v(-112.06, -35.75) * mm, "end": v(-111.82, -36.08) * mm});
            skLineSegment(sketch, "E7739", {"start": v(-112.45, -35.63) * mm, "end": v(-114.78, -35.58) * mm});
            skLineSegment(sketch, "E7740", {"start": v(-114.78, -35.58) * mm, "end": v(-116.74, -35.43) * mm});
            skArc(sketch, "E7741", {"start": v(-116.74, -35.43) * mm, "mid": v(-116.98, -34.65) * mm, "end": v(-117.2, -33.87) * mm});
            skLineSegment(sketch, "E7742", {"start": v(-113.71, -31.36) * mm, "end": v(-115.64, -32.68) * mm});
            skLineSegment(sketch, "E7743", {"start": v(-115.64, -32.68) * mm, "end": v(-117.2, -33.87) * mm});
            skArc(sketch, "E7744", {"start": v(-113.43, -30.64) * mm, "mid": v(-113.46, -31.05) * mm, "end": v(-113.71, -31.36) * mm});
            skArc(sketch, "E7745", {"start": v(-113.43, -30.64) * mm, "mid": v(-113.5, -30.41) * mm, "end": v(-113.56, -30.18) * mm});
            skArc(sketch, "E7746", {"start": v(-114.16, -29.7) * mm, "mid": v(-113.78, -29.84) * mm, "end": v(-113.56, -30.18) * mm});
            skLineSegment(sketch, "E7747", {"start": v(-114.16, -29.7) * mm, "end": v(-116.48, -29.52) * mm});
            skLineSegment(sketch, "E7748", {"start": v(-116.48, -29.52) * mm, "end": v(-118.44, -29.27) * mm});
            skArc(sketch, "E7749", {"start": v(-118.44, -29.27) * mm, "mid": v(-118.63, -28.48) * mm, "end": v(-118.82, -27.7) * mm});
            skLineSegment(sketch, "E7750", {"start": v(-115.2, -25.37) * mm, "end": v(-117.19, -26.58) * mm});
            skLineSegment(sketch, "E7751", {"start": v(-117.19, -26.58) * mm, "end": v(-118.82, -27.7) * mm});
            skArc(sketch, "E7752", {"start": v(-114.88, -24.66) * mm, "mid": v(-114.93, -25.07) * mm, "end": v(-115.2, -25.37) * mm});
            skArc(sketch, "E7753", {"start": v(-114.88, -24.66) * mm, "mid": v(-114.93, -24.43) * mm, "end": v(-114.98, -24.2) * mm});
            skArc(sketch, "E7754", {"start": v(-115.56, -23.68) * mm, "mid": v(-115.19, -23.84) * mm, "end": v(-114.98, -24.2) * mm});
            skLineSegment(sketch, "E7755", {"start": v(-115.56, -23.68) * mm, "end": v(-117.87, -23.38) * mm});
            skLineSegment(sketch, "E7756", {"start": v(-117.87, -23.38) * mm, "end": v(-119.8, -23.03) * mm});
            skArc(sketch, "E7757", {"start": v(-119.8, -23.03) * mm, "mid": v(-119.96, -22.23) * mm, "end": v(-120.1, -21.44) * mm});
            skLineSegment(sketch, "E7758", {"start": v(-116.37, -19.3) * mm, "end": v(-118.42, -20.4) * mm});
            skLineSegment(sketch, "E7759", {"start": v(-118.42, -20.4) * mm, "end": v(-120.1, -21.44) * mm});
            skArc(sketch, "E7760", {"start": v(-116.02, -18.62) * mm, "mid": v(-116.08, -19.02) * mm, "end": v(-116.37, -19.3) * mm});
            skArc(sketch, "E7761", {"start": v(-116.02, -18.62) * mm, "mid": v(-116.05, -18.38) * mm, "end": v(-116.1, -18.15) * mm});
            skArc(sketch, "E7762", {"start": v(-116.64, -17.6) * mm, "mid": v(-116.28, -17.78) * mm, "end": v(-116.1, -18.15) * mm});
            skLineSegment(sketch, "E7763", {"start": v(-116.64, -17.6) * mm, "end": v(-118.93, -17.18) * mm});
            skLineSegment(sketch, "E7764", {"start": v(-118.93, -17.18) * mm, "end": v(-120.85, -16.73) * mm});
            skArc(sketch, "E7765", {"start": v(-120.85, -16.73) * mm, "mid": v(-120.96, -15.92) * mm, "end": v(-121.06, -15.12) * mm});
            skLineSegment(sketch, "E7766", {"start": v(-117.22, -13.19) * mm, "end": v(-119.33, -14.18) * mm});
            skLineSegment(sketch, "E7767", {"start": v(-119.33, -14.18) * mm, "end": v(-121.06, -15.12) * mm});
            skArc(sketch, "E7768", {"start": v(-116.83, -12.52) * mm, "mid": v(-116.92, -12.92) * mm, "end": v(-117.22, -13.19) * mm});
            skArc(sketch, "E7769", {"start": v(-116.83, -12.52) * mm, "mid": v(-116.86, -12.28) * mm, "end": v(-116.88, -12.05) * mm});
            skArc(sketch, "E7770", {"start": v(-117.4, -11.47) * mm, "mid": v(-117.05, -11.67) * mm, "end": v(-116.88, -12.05) * mm});
            skLineSegment(sketch, "E7771", {"start": v(-117.4, -11.47) * mm, "end": v(-119.67, -10.94) * mm});
            skLineSegment(sketch, "E7772", {"start": v(-119.67, -10.94) * mm, "end": v(-121.56, -10.38) * mm});
            skArc(sketch, "E7773", {"start": v(-121.56, -10.38) * mm, "mid": v(-121.62, -9.57) * mm, "end": v(-121.68, -8.76) * mm});
            skLineSegment(sketch, "E7774", {"start": v(-117.75, -7.04) * mm, "end": v(-119.9, -7.92) * mm});
            skLineSegment(sketch, "E7775", {"start": v(-119.9, -7.92) * mm, "end": v(-121.68, -8.76) * mm});
            skArc(sketch, "E7776", {"start": v(-117.33, -6.39) * mm, "mid": v(-117.43, -6.78) * mm, "end": v(-117.75, -7.04) * mm});
            skArc(sketch, "E7777", {"start": v(-117.33, -6.39) * mm, "mid": v(-117.34, -6.15) * mm, "end": v(-117.35, -5.91) * mm});
            skArc(sketch, "E7778", {"start": v(-117.84, -5.3) * mm, "mid": v(-117.5, -5.53) * mm, "end": v(-117.35, -5.91) * mm});
            skLineSegment(sketch, "E7779", {"start": v(-117.84, -5.3) * mm, "end": v(-120.08, -4.66) * mm});
            skLineSegment(sketch, "E7780", {"start": v(-120.08, -4.66) * mm, "end": v(-121.93, -4) * mm});
            skArc(sketch, "E7781", {"start": v(-121.93, -4) * mm, "mid": v(-121.96, -3.2) * mm, "end": v(-121.98, -2.38) * mm});
            skLineSegment(sketch, "E7782", {"start": v(-117.96, -0.86) * mm, "end": v(-120.15, -1.63) * mm});
            skLineSegment(sketch, "E7783", {"start": v(-120.15, -1.63) * mm, "end": v(-121.98, -2.38) * mm});
            skArc(sketch, "E7784", {"start": v(-117.5, -0.24) * mm, "mid": v(-117.63, -0.63) * mm, "end": v(-117.96, -0.86) * mm});
            skArc(sketch, "E7785", {"start": v(-117.5, -0.24) * mm, "mid": v(-117.5, 0) * mm, "end": v(-117.5, 0.24) * mm});
            skArc(sketch, "E7786", {"start": v(-117.96, 0.86) * mm, "mid": v(-117.63, 0.63) * mm, "end": v(-117.5, 0.24) * mm});
            skLineSegment(sketch, "E7787", {"start": v(-117.96, 0.86) * mm, "end": v(-120.15, 1.63) * mm});
            skLineSegment(sketch, "E7788", {"start": v(-120.15, 1.63) * mm, "end": v(-121.98, 2.38) * mm});
            skArc(sketch, "E7789", {"start": v(-121.98, 2.38) * mm, "mid": v(-121.96, 3.2) * mm, "end": v(-121.93, 4) * mm});
            skLineSegment(sketch, "E7790", {"start": v(-117.84, 5.3) * mm, "end": v(-120.08, 4.66) * mm});
            skLineSegment(sketch, "E7791", {"start": v(-120.08, 4.66) * mm, "end": v(-121.93, 4) * mm});
            skArc(sketch, "E7792", {"start": v(-117.35, 5.91) * mm, "mid": v(-117.5, 5.53) * mm, "end": v(-117.84, 5.3) * mm});
            skArc(sketch, "E7793", {"start": v(-117.35, 5.91) * mm, "mid": v(-117.34, 6.15) * mm, "end": v(-117.33, 6.39) * mm});
            skArc(sketch, "E7794", {"start": v(-117.75, 7.04) * mm, "mid": v(-117.43, 6.78) * mm, "end": v(-117.33, 6.39) * mm});
            skLineSegment(sketch, "E7795", {"start": v(-117.75, 7.04) * mm, "end": v(-119.9, 7.92) * mm});
            skLineSegment(sketch, "E7796", {"start": v(-119.9, 7.92) * mm, "end": v(-121.68, 8.76) * mm});
            skArc(sketch, "E7797", {"start": v(-121.68, 8.76) * mm, "mid": v(-121.62, 9.57) * mm, "end": v(-121.56, 10.38) * mm});
            skLineSegment(sketch, "E7798", {"start": v(-117.4, 11.47) * mm, "end": v(-119.67, 10.94) * mm});
            skLineSegment(sketch, "E7799", {"start": v(-119.67, 10.94) * mm, "end": v(-121.56, 10.38) * mm});
            skArc(sketch, "E7800", {"start": v(-116.88, 12.05) * mm, "mid": v(-117.05, 11.67) * mm, "end": v(-117.4, 11.47) * mm});
            skArc(sketch, "E7801", {"start": v(-116.88, 12.05) * mm, "mid": v(-116.86, 12.28) * mm, "end": v(-116.83, 12.52) * mm});
            skArc(sketch, "E7802", {"start": v(-117.22, 13.19) * mm, "mid": v(-116.92, 12.92) * mm, "end": v(-116.83, 12.52) * mm});
            skLineSegment(sketch, "E7803", {"start": v(-117.22, 13.19) * mm, "end": v(-119.33, 14.18) * mm});
            skLineSegment(sketch, "E7804", {"start": v(-119.33, 14.18) * mm, "end": v(-121.06, 15.12) * mm});
            skArc(sketch, "E7805", {"start": v(-121.06, 15.12) * mm, "mid": v(-120.96, 15.92) * mm, "end": v(-120.85, 16.73) * mm});
            skLineSegment(sketch, "E7806", {"start": v(-116.64, 17.6) * mm, "end": v(-118.93, 17.18) * mm});
            skLineSegment(sketch, "E7807", {"start": v(-118.93, 17.18) * mm, "end": v(-120.85, 16.73) * mm});
            skArc(sketch, "E7808", {"start": v(-116.1, 18.15) * mm, "mid": v(-116.28, 17.78) * mm, "end": v(-116.64, 17.6) * mm});
            skArc(sketch, "E7809", {"start": v(-116.1, 18.15) * mm, "mid": v(-116.05, 18.38) * mm, "end": v(-116.02, 18.62) * mm});
            skArc(sketch, "E7810", {"start": v(-116.37, 19.3) * mm, "mid": v(-116.08, 19.02) * mm, "end": v(-116.02, 18.62) * mm});
            skLineSegment(sketch, "E7811", {"start": v(-116.37, 19.3) * mm, "end": v(-118.42, 20.4) * mm});
            skLineSegment(sketch, "E7812", {"start": v(-118.42, 20.4) * mm, "end": v(-120.1, 21.44) * mm});
            skArc(sketch, "E7813", {"start": v(-120.1, 21.44) * mm, "mid": v(-119.96, 22.23) * mm, "end": v(-119.8, 23.03) * mm});
            skLineSegment(sketch, "E7814", {"start": v(-115.56, 23.68) * mm, "end": v(-117.87, 23.38) * mm});
            skLineSegment(sketch, "E7815", {"start": v(-117.87, 23.38) * mm, "end": v(-119.8, 23.03) * mm});
            skArc(sketch, "E7816", {"start": v(-114.98, 24.2) * mm, "mid": v(-115.19, 23.84) * mm, "end": v(-115.56, 23.68) * mm});
            skArc(sketch, "E7817", {"start": v(-114.98, 24.2) * mm, "mid": v(-114.93, 24.43) * mm, "end": v(-114.88, 24.66) * mm});
            skArc(sketch, "E7818", {"start": v(-115.2, 25.37) * mm, "mid": v(-114.93, 25.07) * mm, "end": v(-114.88, 24.66) * mm});
            skLineSegment(sketch, "E7819", {"start": v(-115.2, 25.37) * mm, "end": v(-117.19, 26.58) * mm});
            skLineSegment(sketch, "E7820", {"start": v(-117.19, 26.58) * mm, "end": v(-118.82, 27.7) * mm});
            skArc(sketch, "E7821", {"start": v(-118.82, 27.7) * mm, "mid": v(-118.63, 28.48) * mm, "end": v(-118.44, 29.27) * mm});
            skLineSegment(sketch, "E7822", {"start": v(-114.16, 29.7) * mm, "end": v(-116.48, 29.52) * mm});
            skLineSegment(sketch, "E7823", {"start": v(-116.48, 29.52) * mm, "end": v(-118.44, 29.27) * mm});
            skArc(sketch, "E7824", {"start": v(-113.56, 30.18) * mm, "mid": v(-113.78, 29.84) * mm, "end": v(-114.16, 29.7) * mm});
            skArc(sketch, "E7825", {"start": v(-113.56, 30.18) * mm, "mid": v(-113.5, 30.41) * mm, "end": v(-113.43, 30.64) * mm});
            skArc(sketch, "E7826", {"start": v(-113.71, 31.36) * mm, "mid": v(-113.46, 31.05) * mm, "end": v(-113.43, 30.64) * mm});
            skLineSegment(sketch, "E7827", {"start": v(-113.71, 31.36) * mm, "end": v(-115.64, 32.68) * mm});
            skLineSegment(sketch, "E7828", {"start": v(-115.64, 32.68) * mm, "end": v(-117.2, 33.87) * mm});
            skArc(sketch, "E7829", {"start": v(-117.2, 33.87) * mm, "mid": v(-116.98, 34.65) * mm, "end": v(-116.74, 35.43) * mm});
            skLineSegment(sketch, "E7830", {"start": v(-112.45, 35.63) * mm, "end": v(-114.78, 35.58) * mm});
            skLineSegment(sketch, "E7831", {"start": v(-114.78, 35.58) * mm, "end": v(-116.74, 35.43) * mm});
            skArc(sketch, "E7832", {"start": v(-111.82, 36.08) * mm, "mid": v(-112.06, 35.75) * mm, "end": v(-112.45, 35.63) * mm});
            skArc(sketch, "E7833", {"start": v(-111.82, 36.08) * mm, "mid": v(-111.75, 36.3) * mm, "end": v(-111.68, 36.54) * mm});
            skArc(sketch, "E7834", {"start": v(-111.92, 37.27) * mm, "mid": v(-111.68, 36.94) * mm, "end": v(-111.68, 36.54) * mm});
            skLineSegment(sketch, "E7835", {"start": v(-111.92, 37.27) * mm, "end": v(-113.77, 38.68) * mm});
            skLineSegment(sketch, "E7836", {"start": v(-113.77, 38.68) * mm, "end": v(-115.27, 39.96) * mm});
            skArc(sketch, "E7837", {"start": v(-115.27, 39.96) * mm, "mid": v(-115, 40.72) * mm, "end": v(-114.73, 41.49) * mm});
            skLineSegment(sketch, "E7838", {"start": v(-110.43, 41.47) * mm, "end": v(-112.76, 41.54) * mm});
            skLineSegment(sketch, "E7839", {"start": v(-112.76, 41.54) * mm, "end": v(-114.73, 41.49) * mm});
            skArc(sketch, "E7840", {"start": v(-109.78, 41.89) * mm, "mid": v(-110.04, 41.57) * mm, "end": v(-110.43, 41.47) * mm});
            skArc(sketch, "E7841", {"start": v(-109.78, 41.89) * mm, "mid": v(-109.7, 42.1) * mm, "end": v(-109.61, 42.33) * mm});
            skArc(sketch, "E7842", {"start": v(-109.81, 43.08) * mm, "mid": v(-109.59, 42.74) * mm, "end": v(-109.61, 42.33) * mm});
            skLineSegment(sketch, "E7843", {"start": v(-109.81, 43.08) * mm, "end": v(-111.59, 44.58) * mm});
            skLineSegment(sketch, "E7844", {"start": v(-111.59, 44.58) * mm, "end": v(-113.02, 45.94) * mm});
            skArc(sketch, "E7845", {"start": v(-113.02, 45.94) * mm, "mid": v(-112.71, 46.69) * mm, "end": v(-112.4, 47.43) * mm});
            skLineSegment(sketch, "E7846", {"start": v(-108.11, 47.19) * mm, "end": v(-110.43, 47.38) * mm});
            skLineSegment(sketch, "E7847", {"start": v(-110.43, 47.38) * mm, "end": v(-112.4, 47.43) * mm});
            skArc(sketch, "E7848", {"start": v(-107.44, 47.57) * mm, "mid": v(-107.71, 47.27) * mm, "end": v(-108.11, 47.19) * mm});
            skArc(sketch, "E7849", {"start": v(-107.44, 47.57) * mm, "mid": v(-107.34, 47.8) * mm, "end": v(-107.24, 48) * mm});
            skArc(sketch, "E7850", {"start": v(-107.4, 48.77) * mm, "mid": v(-107.2, 48.42) * mm, "end": v(-107.24, 48) * mm});
            skLineSegment(sketch, "E7851", {"start": v(-107.4, 48.77) * mm, "end": v(-109.1, 50.36) * mm});
            skLineSegment(sketch, "E7852", {"start": v(-109.1, 50.36) * mm, "end": v(-110.46, 51.8) * mm});
            skArc(sketch, "E7853", {"start": v(-110.46, 51.8) * mm, "mid": v(-110.12, 52.52) * mm, "end": v(-109.76, 53.25) * mm});
            skLineSegment(sketch, "E7854", {"start": v(-105.5, 52.78) * mm, "end": v(-107.8, 53.1) * mm});
            skLineSegment(sketch, "E7855", {"start": v(-107.8, 53.1) * mm, "end": v(-109.76, 53.25) * mm});
            skArc(sketch, "E7856", {"start": v(-104.8, 53.13) * mm, "mid": v(-105.1, 52.84) * mm, "end": v(-105.5, 52.78) * mm});
            skArc(sketch, "E7857", {"start": v(-104.8, 53.13) * mm, "mid": v(-104.7, 53.34) * mm, "end": v(-104.58, 53.56) * mm});
            skArc(sketch, "E7858", {"start": v(-104.7, 54.32) * mm, "mid": v(-104.52, 53.96) * mm, "end": v(-104.58, 53.56) * mm});
            skLineSegment(sketch, "E7859", {"start": v(-104.7, 54.32) * mm, "end": v(-106.32, 56) * mm});
            skLineSegment(sketch, "E7860", {"start": v(-106.32, 56) * mm, "end": v(-107.6, 57.5) * mm});
            skArc(sketch, "E7861", {"start": v(-107.6, 57.5) * mm, "mid": v(-107.22, 58.21) * mm, "end": v(-106.83, 58.92) * mm});
            skLineSegment(sketch, "E7862", {"start": v(-102.59, 58.23) * mm, "end": v(-104.87, 58.66) * mm});
            skLineSegment(sketch, "E7863", {"start": v(-104.87, 58.66) * mm, "end": v(-106.83, 58.92) * mm});
            skSolve(sketch);
        }
        {
            var Q0;
            Q0=qCreatedBy(makeId("Front.planeOp"),FACE);
            var sketch = newSketch(context, id + "F5", { "sketchPlane" : qUnion([Q0])});
            skArc(sketch, "E7864", {"start": v(15, 24.5) * mm, "mid": v(15.74, 20.72) * mm, "end": v(17.86, 17.5) * mm});
            skArc(sketch, "E7865", {"start": v(24.08, 6.72) * mm, "mid": v(25.81, 3.28) * mm, "end": v(28.71, 0.74) * mm});
            skArc(sketch, "E7866", {"start": v(28.9, 68.4) * mm, "mid": v(19.47, 67.52) * mm, "end": v(15, 59.19) * mm});
            skArc(sketch, "E7867", {"start": v(58.76, -16.6) * mm, "mid": v(68.21, -16.9) * mm, "end": v(73.68, -9.18) * mm});
            skArc(sketch, "E7868", {"start": v(-43.76, -42.58) * mm, "mid": v(-48.74, -50.62) * mm, "end": v(-44.79, -59.22) * mm});
            skArc(sketch, "E7869", {"start": v(44.79, -59.22) * mm, "mid": v(48.74, -50.62) * mm, "end": v(43.76, -42.58) * mm});
            skArc(sketch, "E7870", {"start": v(-6.22, -24.21) * mm, "mid": v(-10.07, -24) * mm, "end": v(-13.71, -25.24) * mm});
            skArc(sketch, "E7871", {"start": v(-15, 59.19) * mm, "mid": v(-19.47, 67.52) * mm, "end": v(-28.9, 68.4) * mm});
            skArc(sketch, "E7872", {"start": v(-17.86, 17.5) * mm, "mid": v(-15.74, 20.72) * mm, "end": v(-15, 24.5) * mm});
            skArc(sketch, "E7873", {"start": v(-28.71, 0.74) * mm, "mid": v(-25.81, 3.28) * mm, "end": v(-24.08, 6.72) * mm});
            skArc(sketch, "E7874", {"start": v(-73.68, -9.18) * mm, "mid": v(-68.21, -16.9) * mm, "end": v(-58.76, -16.6) * mm});
            skArc(sketch, "E7875", {"start": v(-44.79, -59.22) * mm, "mid": v(0, -74.25) * mm, "end": v(44.79, -59.22) * mm});
            skArc(sketch, "E7876", {"start": v(73.68, -9.18) * mm, "mid": v(64.3, 37.12) * mm, "end": v(28.9, 68.4) * mm});
            skArc(sketch, "E7877", {"start": v(-3.1, 0) * mm, "mid": v(-3, -0.8) * mm, "end": v(-2.68, -1.55) * mm});
            skArc(sketch, "E7878", {"start": v(-1.55, -2.68) * mm, "mid": v(-0.8, -3) * mm, "end": v(0, -3.1) * mm});
            skArc(sketch, "E7879", {"start": v(1.55, -2.68) * mm, "mid": v(2.2, -2.2) * mm, "end": v(2.68, -1.55) * mm});
            skArc(sketch, "E7880", {"start": v(3.1, 0) * mm, "mid": v(3, 0.8) * mm, "end": v(2.68, 1.55) * mm});
            skArc(sketch, "E7881", {"start": v(2.51, 1.45) * mm, "mid": v(2.05, 2.05) * mm, "end": v(1.45, 2.51) * mm});
            skArc(sketch, "E7882", {"start": v(0, -2.9) * mm, "mid": v(0.75, -2.8) * mm, "end": v(1.45, -2.51) * mm});
            skArc(sketch, "E7883", {"start": v(1.55, 2.68) * mm, "mid": v(0.8, 3) * mm, "end": v(0, 3.1) * mm});
            skArc(sketch, "E7884", {"start": v(-2.51, 1.45) * mm, "mid": v(-2.8, 0.75) * mm, "end": v(-2.9, 0) * mm});
            skArc(sketch, "E7885", {"start": v(-2.51, -1.45) * mm, "mid": v(-2.05, -2.05) * mm, "end": v(-1.45, -2.51) * mm});
            skArc(sketch, "E7886", {"start": v(2.51, -1.45) * mm, "mid": v(2.8, -0.75) * mm, "end": v(2.9, 0) * mm});
            skLineSegment(sketch, "E7887", {"start": v(1.45, 2.51) * mm, "end": v(1.55, 2.68) * mm});
            skLineSegment(sketch, "E7888", {"start": v(2.51, 1.45) * mm, "end": v(2.68, 1.55) * mm});
            skLineSegment(sketch, "E7889", {"start": v(2.9, 0) * mm, "end": v(3.1, 0) * mm});
            skLineSegment(sketch, "E7890", {"start": v(1.45, -2.51) * mm, "end": v(1.55, -2.68) * mm});
            skLineSegment(sketch, "E7891", {"start": v(13.71, -25.24) * mm, "end": v(43.76, -42.58) * mm});
            skLineSegment(sketch, "E7892", {"start": v(-13.71, -25.24) * mm, "end": v(-43.76, -42.58) * mm});
            skLineSegment(sketch, "E7893", {"start": v(-28.71, 0.74) * mm, "end": v(-58.76, -16.6) * mm});
            skCircle(sketch, "E7894", {"center": v(27.88, 91.22) * mm, "radius": 1 * mm});
            skLineSegment(sketch, "E7895", {"start": v(70.46, -46.46) * mm, "end": v(75.46, -37.8) * mm});
            skLineSegment(sketch, "E7896", {"start": v(70.46, -46.46) * mm, "end": v(79.12, -51.46) * mm});
            skLineSegment(sketch, "E7897", {"start": v(75.46, -37.8) * mm, "end": v(84.12, -42.8) * mm});
            skCircle(sketch, "E7898", {"center": v(37.28, 87.8) * mm, "radius": 1 * mm});
            skLineSegment(sketch, "E7899", {"start": v(79.12, -51.46) * mm, "end": v(84.12, -42.8) * mm});
            skLineSegment(sketch, "E7900", {"start": v(-70.46, -46.46) * mm, "end": v(-79.12, -51.46) * mm});
            skLineSegment(sketch, "E7901", {"start": v(2.51, -1.45) * mm, "end": v(2.68, -1.55) * mm});
            skCircle(sketch, "E7902", {"center": v(35.22, 82.16) * mm, "radius": 1 * mm});
            skLineSegment(sketch, "E7903", {"start": v(-75.46, -37.8) * mm, "end": v(-84.12, -42.8) * mm});
            skLineSegment(sketch, "E7904", {"start": v(-84.12, -42.8) * mm, "end": v(-79.12, -51.46) * mm});
            skLineSegment(sketch, "E7905", {"start": v(-5, 84.25) * mm, "end": v(-5, 94.25) * mm});
            skArc(sketch, "E7906", {"start": v(13.71, -25.24) * mm, "mid": v(10.07, -24) * mm, "end": v(6.22, -24.21) * mm});
            skCircle(sketch, "E7907", {"center": v(33.17, 76.52) * mm, "radius": 1 * mm});
            skArc(sketch, "E7908", {"start": v(-1.55, 2.68) * mm, "mid": v(-2.2, 2.2) * mm, "end": v(-2.68, 1.55) * mm});
            skCircle(sketch, "E7909", {"center": v(0, 0) * mm, "radius": 104.25 * mm});
            skLineSegment(sketch, "E7910", {"start": v(28.71, 0.74) * mm, "end": v(58.76, -16.6) * mm});
            skArc(sketch, "E7911", {"start": v(-17.86, 17.5) * mm, "mid": v(-21.65, 12.5) * mm, "end": v(-24.08, 6.72) * mm});
            skArc(sketch, "E7912", {"start": v(-28.9, 68.4) * mm, "mid": v(-64.3, 37.12) * mm, "end": v(-73.68, -9.18) * mm});
            skArc(sketch, "E7913", {"start": v(0, 2.9) * mm, "mid": v(-0.75, 2.8) * mm, "end": v(-1.45, 2.51) * mm});
            skLineSegment(sketch, "E7914", {"start": v(-75.46, -37.8) * mm, "end": v(-70.46, -46.46) * mm});
            skCircle(sketch, "E7915", {"center": v(23.77, 79.94) * mm, "radius": 1 * mm});
            skLineSegment(sketch, "E7916", {"start": v(15, 24.5) * mm, "end": v(15, 59.19) * mm});
            skLineSegment(sketch, "E7917", {"start": v(-15, 24.5) * mm, "end": v(-15, 59.19) * mm});
            skLineSegment(sketch, "E7918", {"start": v(5, 84.25) * mm, "end": v(-5, 84.25) * mm});
            skCircle(sketch, "E7919", {"center": v(25.83, 85.58) * mm, "radius": 1 * mm});
            skLineSegment(sketch, "E7920", {"start": v(5, 94.25) * mm, "end": v(-5, 94.25) * mm});
            skLineSegment(sketch, "E7921", {"start": v(5, 84.25) * mm, "end": v(5, 94.25) * mm});
            skLineSegment(sketch, "E7922", {"start": v(59.9, 60.5) * mm, "end": v(49.18, 69.5) * mm});
            skLineSegment(sketch, "E7923", {"start": v(49.18, 69.5) * mm, "end": v(54.83, 76.24) * mm});
            skLineSegment(sketch, "E7924", {"start": v(54.83, 76.24) * mm, "end": v(65.56, 67.24) * mm});
            skLineSegment(sketch, "E7925", {"start": v(65.56, 67.24) * mm, "end": v(59.9, 60.5) * mm});
            skLineSegment(sketch, "E7926", {"start": v(81.93, 20.54) * mm, "end": v(84.01, 8.72) * mm});
            skLineSegment(sketch, "E7927", {"start": v(84.01, 8.72) * mm, "end": v(93.86, 10.46) * mm});
            skLineSegment(sketch, "E7928", {"start": v(93.86, 10.46) * mm, "end": v(91.78, 22.28) * mm});
            skLineSegment(sketch, "E7929", {"start": v(91.78, 22.28) * mm, "end": v(81.93, 20.54) * mm});
            skArc(sketch, "E7930", {"start": v(-6.22, -24.21) * mm, "mid": v(0, -25) * mm, "end": v(6.22, -24.21) * mm});
            skArc(sketch, "E7931", {"start": v(24.08, 6.72) * mm, "mid": v(21.65, 12.5) * mm, "end": v(17.86, 17.5) * mm});
            skLineSegment(sketch, "E7932", {"start": v(0, 2.9) * mm, "end": v(0, 3.1) * mm});
            skLineSegment(sketch, "E7933", {"start": v(-1.45, 2.51) * mm, "end": v(-1.55, 2.68) * mm});
            skLineSegment(sketch, "E7934", {"start": v(-2.51, 1.45) * mm, "end": v(-2.68, 1.55) * mm});
            skLineSegment(sketch, "E7935", {"start": v(-2.9, 0) * mm, "end": v(-3.1, 0) * mm});
            skLineSegment(sketch, "E7936", {"start": v(-2.51, -1.45) * mm, "end": v(-2.68, -1.55) * mm});
            skLineSegment(sketch, "E7937", {"start": v(-1.45, -2.51) * mm, "end": v(-1.55, -2.68) * mm});
            skLineSegment(sketch, "E7938", {"start": v(0, -2.9) * mm, "end": v(0, -3.1) * mm});
            skSolve(sketch);
        }
        {
            var Q0;
            Q0 = qSketchRegion(id + "F0", true);
            extrude(context, id + "F6", {"entities" : qUnion([Q0]), "depth" : 3 * mm, "offsetDistance" : 25 * mm});
        }
        {
            var Q0;
            Q0 = qSketchRegion(id + "F1", true);
            extrude(context, id + "F7", {"entities" : qUnion([Q0]), "depth" : 5 * mm, "offsetDistance" : 25 * mm});
        }
        {
            var Q0;
            Q0 = qSketchRegion(id + "F2", true);
            extrude(context, id + "F8", {"entities" : qUnion([Q0]), "depth" : 5 * mm, "offsetDistance" : 25 * mm});
        }
        {
            var Q0;
            Q0 = qSketchRegion(id + "F3", true);
            extrude(context, id + "F9", {"entities" : qUnion([Q0]), "depth" : 5 * mm, "offsetDistance" : 25 * mm});
        }
        {
            var Q0;
            Q0 = qSketchRegion(id + "F4", true);
            extrude(context, id + "F10", {"entities" : qUnion([Q0]), "depth" : 5 * mm, "offsetDistance" : 25 * mm});
        }
        {
            var Q0;
            Q0 = qSketchRegion(id + "F5", true);
            extrude(context, id + "F11", {"entities" : qUnion([Q0]), "depth" : 10 * mm, "offsetDistance" : 25 * mm});
        }
    });
